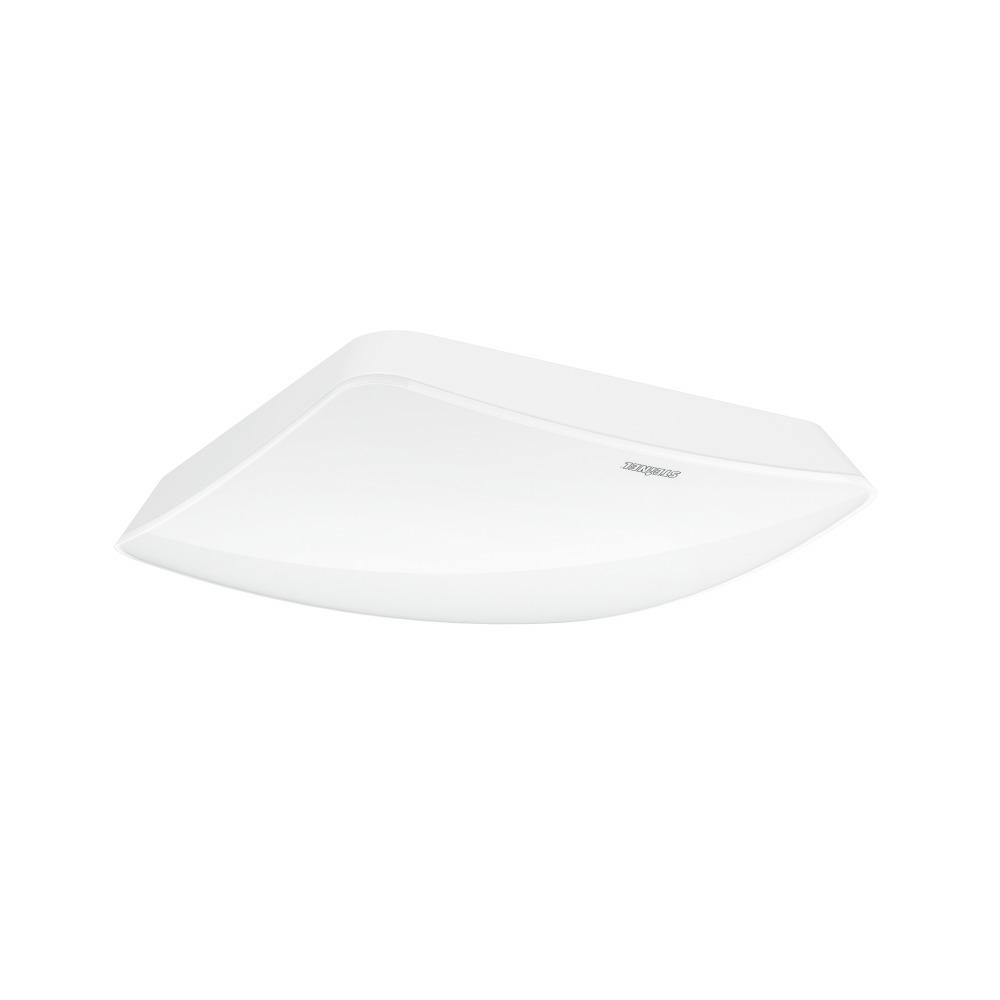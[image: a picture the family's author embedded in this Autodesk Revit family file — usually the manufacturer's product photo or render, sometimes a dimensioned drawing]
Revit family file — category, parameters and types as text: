
# Revit family: truepresence_057923
name_source: partatom
category: Electrical Fixtures
revit_build: Autodesk Revit 2016 (Build: 20151007_0715(x64)
units: mm (PartAtom-declared; Revit-internal decimal feet)

## family parameters
Cut with Voids When Loaded = No
Host = Face
Maintain Annotation Orientation = No
Part Type = Normal
Room Calculation Point = No
Round Connector Dimension = Use Diameter
Shared = No

## types (1)
- True Presence
    Apparent Load = 0 VA
    Default Elevation = 1800 mm
    Description = Type: Presence detector; Dimensions (L x W x H): 50 x 103 x 103 mm; Mains power supply: 220 – 240 V / 50 – 60 Hz; Power consumption: 1 W; Sensor Technology: High frequency; Application, place: Indoors; Application, room: classroom, lecture hall, one-person office, open-plan office, high-bay warehouse, production facilities, conference room / meeting room, hotel room, care room, duty room, recreation room, dining hall / staff restaurant, changing room, kitchenette, sports hall, reception / lobby, WC / washroom, warehouse, Indoors; Installation site: ceiling; Installation: Concealed wiring; HF-system: 7,2 GHz; Electronic scalability: Yes; Mechanical scalability: No; Mounting height: 2 – 12 m; Optimum mounting height: 2,8 m; Detection angle: 360 °; Angle of aperture: 360 °; Sneak-by guard: Yes; Capability of masking out individual segments: No; Reach, radial: Ø 15 m (177 m²); Reach, tangential: Ø 15 m (177 m²); Reach, presence: Ø 15 m (177 m²); True Presence reach: Ø 9 m (64 m²); Twilight setting TEACH: Yes; Twilight setting: 2 – 1000 lx; Time setting: 30 sec – 30 min; Switching output 1, resistive: 2000 W; Switching output 1, number of LEDs / fluorescent lamps: 8 pcs.; Switching output 1, floating: No; Constant-lighting control: No; Basic light level function: No; Functions: Group parameterisation, Semi-/fully automatic, Lighting scenario, Manual ON / ON-OFF, Neighbouring-group function, Normal / test mode; Settings via: Bluetooth; With remote control: No; Interconnection: Yes; IP-rating: IP20; Material: Plastic; Ambient temperature: -20 – 50 °C; Colour: white; Colour, RAL: 9003; Manufacturer's Warranty: 5 years; Version: COM1 - concealed white; PU1, EAN: 4007841057923
    Height = 0 mm  [stored 0 ft]
    Length = 200 mm  [stored 0.656168 ft]
    Manufacturer = Steinel
    ModVariant = No
    Model = 057923
    Number of Poles = 1
    OnlyDefault = No
    Power Factor = 1
    Product Name = True Presence
    Product group = Presence detector
    ProductGroupID = 4
    RLX_Detail_Level = 1
    RLX_LegendID = 4.1
    RlxData = Q
eAHUvXeUVNW7rtuAIElEFEUQRKTJGUldtaqQnLNIEhok5xyaIEFyDpIlJxUkCCh2VRciZgXM
OeesP0Uxcr5n1jv3qT3uuXfcf84Y5zD20+/7vfWtueaaK9Ddsn8rV9rly2n25/K/TrDuT35v
TC/bH1/e0sG75DZs50lLmx01EtbhvrgNL1/+Os91aU3HjBowbHT/icPGjG43aZS5YeMH5c+X
h01v6JY2Pm1S2qC0smmdzA1Km2CMTrvbJZXSaqXVS2uQ1iitTlpd66ic1thGr6I5pE4yj2WX
L3+Xp3Bau2FDhk5sPmrYxImDxqeVzcU+Co5P6582MK3ffxuNkar+L0fKbSN9neeKtPaDJgzN
VcSN4PZb7X/RnSvtCqU/2cH///nzv6fvGrfrMWPT0k6ZG50rLe3BUm2DNyZVCq7uMzP28DPt
gzwl9odX15geuzraLMj/V0Ywd+ic2M3vlAjSHiwcfDZyVWzH9m/CY2fcGXr3k02x1ks/CXep
czrc8KXNsbtabQ/3b9g5vKfKzliBClPDL86ZHDq2ZXesXv354XI/fR6amn937OffOgTzarbJ
aF4vK7bsZIdgWq5rYzWHZ8WWv98+yOm6I7bxpul+X3H29b7N7a1JleJf9J7p5xNnPtpvLGW/
MfarfWWzL80hmzn0uHtsOC3to/IF39wd+zISyn55wmsZeV9M+rRGF2L1MjbF3gk/ErvUvH18
3OKJsUaNb4zfdONV8XwdVsX6Va8Un3C2TbzB2snMIW5r4ubw/GcN48VvbB7/6frpscn914QH
HW4fL113YuyRYfWDMitaxBv+PC3Wt3qlYIBt28y2rTH0YqjYuA7xOusmxFbVK5B9bHOH+KVx
E2Jr/vo0tu2zJ2I37tkce2PLjljHyB2xwkV3xq75en5scO/vsp/9e1fsk4NTYyc+m5W9aYM7
ltic+/KkcyzKQ+TqD9GvccKMw/Fyzqr0Xu/3FWZfOsaAY9z89+rY2iPtg/Q6E/0xuvNu8493
Pdsm6GTzn3Ff/XjHyS2Cv/JkxR4s+Ev2t+M6BHPWToiVGnZ1aMDmDkF4/IRY14HHwyWbtA+2
LJvIugWTbdvbbNunX28YrCzXPJh99fSYXW9xu97iut7idr3FuN7seojb9RDmeuCccI198cTW
2LvWb9dA8KVdA3b9xO36eZzrx66ZuF0zYa6Zv35qF595bH+4V7ERsX8fbxt//fi+8JGuXWO5
5reJ13h0bzjvfaHY4D/axfdtOXsr+b1PtHWe/Lqv28THt/ggRn7n8dbx4Nf3YuT3/NvKxqkQ
Jz/4YksbJz1O/u2YpvFpe+u7fFmLJvHVK+u5nIzP6CfjM/oZg7HIGYOxyNkn+yZnn+ybfEyx
PLuZKzmeuao/nNIf9v02fpAyfuDHt/kEKfMJ/HwsC1LmH/j52xhByvEG/nhtn0HK+gR+fWyO
QWzi2j3M0+YY9Gh0fA/zVL9bf5sj/W79NX5Av82R8QP6NR+X2xyZj8s1f5eT8Rn9Ol6XMwZj
payPy9kn+ya3NSzPXNlvwTdvLc9c1e/mSq719+Nzvvz4nC+X6/y6XOfX5awxc2Uc1tjP/5PN
LeIrTpUPbJ+xdw42id/4aW3nW9Xu4K49rtVXSreL79/4YQzftVYbu4YrxvFtNjWL989u4DxK
Tc7n9OHZju3xXCeMqzzsc+sPfL+NE/hxTAM/vn0e+P3adoGfj43nzi9jKnf3l/oDco3jvMZ3
Xvt13sZjPs5z/zGu5unGxeu4XK7jdZ75Mi497RplxFduDrs1/PqhmvEzLzZ13tY4/svmFs6/
PWd77Id+rZ2vNqVzRrHFbZy/uPHB8MRQMl9o5ySs/jc/rB088nAT1/PBynBwrlmG8wUvNA3O
76np/D/Wu1Ln8VK4VZBx/Nsw57TojNbBgnobnH9/UZvggRp9Hif/qn/r4K2h27nWYicatQqq
zv/O+VorWwYz3igQJ69Sv2Xw7qlrnf9P/pbBoWMlnK/1nxbB77VKOf/H2y2Cz94p7fzXNgeO
k21PzWgSXGpYx/lljTOC19eGne/+Zc3gzJGmznPdfWzXH/2Tbv46/EbLVs7fP2F1eMmK1s5n
FL0mu7I9H+kpHhyJdamYzG194k217ZBY7XiRM01cz5PDwvHlozKcv/RY03iRN2o6/33yOnf+
u16t4ouWfuaO9599reOfz1vs/LTpbeL5vpkbYl+L/moVn/pPdhj/9R8LYuOLLPwvP+DYItf/
TnhhePCHC//L+x6+ebFvWdJyCzzf0QGe77HwaF6BzyfwV8qjfGfIdgUMPgN8QXm0kDxaWOCv
kkeLyF9t6sfBF1WNsj/A810YHi0mrlVGjr9O4OmhRtkGjxYXeMalRtk3MF/fg79eNXqDwJeQ
R28U+JIGn7NtKYHneKnRm0RpZeRlDLYD/M0G+ytr+Pngb1GNlpNH/bHjb1WNlhfpyujDV1CN
VpRHKwl8ZXmUnwz4DOV7e8BXk0erC3wN5TVN/Zj4WqrR2vIo1yDg68ijdQXXr+/hOvVj4rlW
qVG/Dvj8qlGukduMeoY/X3h/TvH1VaNlBb6BPMq6A561BjxrDXi/5njWGvCsNeBZX8CzvoBn
f3iU9QV8Q3mU9WW+jQw+gwyDz9CQPDXevpF3n6GBwEfkUX7EAnxjefR2gW8ijzYV+GbyaHOB
byGPthT4VvJoa4FvI4+2Ffh28mh7ge8gj3YU+E7yaGeB7yKPdhX4bvLoHQLfXR69U+B7yKM9
Bb6XPNpb4PvIo3cJfF95tJ/AZ8qj/QV+gDx6t8APlEcHCfxgeXSIwA+VR4cJ/HB5dITAj5RH
Rwn8aHl0jMCPlUfHCfx4eXSCwbXKtcs1CviJ8ijXKOC5Lvmca54a8NwHeHSSwN8mj04W+Cny
KNcu4Lle+fxG1WT4kqrRqQJfQh6dJvBZ8ijXNOC5jvn8etVkeHLATxd4nv/UaBl5lOse8KXk
Ua57wM+QR2cKPH/fUKM3GfTifR/ZLIEvIo/eI/D8/U2Nzhb4OfJod4HvYfB5IYMa8AXl0bkC
X0AezSWPzhN4/lDz516Bny+P9hX4TIM/uQ1qwPP3Cx5dIPB15NGFAr9IHuUeAzz3FZ/z9xc1
4MkBv1jga8mj/L3IZ+hQga8qjw4X+CXy6FKBry6P1jDoxfs+smUCX00eXS7wDeVR7lvAjze4
b1cY4wSeex9dKU+NHyVdJU+NHyFdLU+NHyZdI0+NX6sa9c8x/DrV6CCBv08e9c9J/HrVaH+B
3yCP9hP4jfLoJnn0LoHfLI/2Fvgt8uhWebSnwN8vj26TR+8U+O3y6A6xUxl9+F2q0d1ijzJ6
8HdI98pT47tK98lT4ztL98tT4w+oRjsK/APyaHuBf1AefUgebSvwB+XR1gJ/SB5tKfAPy6PN
Bf6wPNpU4I/Io0fl0dsF/pg8GhX4R+TRQOCPy6PcG4Afb4w1RhvLBX6ZspHy1Pil0uHy3P88
LxYbmcZ8Y4HBc2aAsVDgydFMeZ53fYx7BX6e0cOYY8w1yHoZ5IAnR+nD8+zuZswW+HsMtIs8
NX6WtJM8NX6mtIN8O9M2xnSjmTHFmGq0MloY0wSeHKUPHzEmGpOMJkZjY7LAk6P04Y8bJwzO
BeBXyaMTBH6FwK802JbzyzaAPymPPirwXNPUKNc6vccMPgM81xYePWJwPT4sT43nmsajB+VR
Pw6e+4Qa9fvjvvPzwfMcoUZ5vnC/8tzgM8Bvk0fp22fsNugF/C55lOcLPTwr+Azweww+22H4
bfHsg33z3PNzwz+mGvVri1+jGl1t0Mvzk88Az3MWj26UR9cJ/AZ5dL24Txl9aw3GALzfH+ed
+bxqpP4581RLLqe0nOumJ345WCeStrpq9tBiMxLNxlSJPD+paiw8fEbi5rQ8rmfO5zMT5Q9e
CF5ZXjX7kQdnJfpVfTx4rU7VWLHvZyW+mZQeeXxV1ex1u2Ykpk1Pd/34X9dViVzYmRZmnBuP
2fj2h/H/+axBZPSyh0J7Xp+eKPlH7sh9K6tmM/5T8QsBPYy/unN2cGBZ1RDjVzm8w+V/1Lsn
ce1/5jt/eMI9CXqTf5L/xdD77NLLY6vvqxuPPnpP4ttNZbI3bNkRZ9vid/dvdFvB3+I90mcl
Pj/3Y/adRUrkPFhxZuLLfP+GHmmTnsOcz5Wr1GjoU1VymHPhl8uEp46ok8OcZ399Q+jpjCCn
1Ibpib+K3JL98Olkzz9t9mXXOJr0o7JqZb89s0nO+e7TE42al8ve/UTLHNb2463XZX+ep33O
txeyEmenlc4+/s9FN4eN5Ts2yn84Obe2e+aFn+xXz8352mseClf4tZrzb63tGy5yumHAscx5
9InwA2enBRx7vy+Phla22xGkHFfAcelYIhzLGy8cCS19uEqEY7n+QIXQwFlNIsztgVM7Qx2q
BxGOJbtEeqjr5HTXvzHf+cem2PljWx2X21Zr4vzXba+K3ZZVJ8KavPbFgNjLtyT92D2NQi9c
uujmMPnvPdmZvZJz2/fSxFizIXPdnB97+evsk49F3LEcf6plzk9n1zVy67O/Tk6/7HEhxgyO
1skZ02tZBv7CnGI5j2+sG36h58zE+pIlcu4ccS7E+Ro9MDt+8LsrM7g2mjbfER/U57EQ6/D6
qh3xc8ObO7/n4R3xkeXPnyJXT3ZKj/Nre2THe6wr4K6xO28um3PtvrXZ6W/PSBRbfkPOV6uH
xNhX+yN1ci4+97ybT+abDXJ+7P9BNtftT/na56zY3yCDc9rYqJF+RXBkcJtIrYVZiXMlCgfT
9neMfLk3KzGqzNxwio85PyQr8VmjvPEuLbtE/jg7PHHdht05pZtMjDR/r0Zi7MYaiWbn50em
vLQn5+EVwxPke89dG3+sX1aC/guld8RW7cxKME7LMsvCK/YkfZmfcwelhiV7pj2+K9Lm2+S2
GxbUiBb/ITnmKzuGR/MP3uP2tWJgVvS3foXcHG7anRW9tsx6N7cb9mVF1x6c7ebcdnhWtNuB
tID93vH28GiBcrsjzOfTyzWi8Yk1osxzzb+7I98dGx4lP3rgqqDF3VlR+nev3BnutjMryjzH
HFwSO7Mn6RvcUCD+8qBkz6rFu3O6PZPc9uMBNRKHr6npxuy4bHji93f2uH2tPToh8exXqyNZ
Rb8ILvfMSnz6zL7wS190i/y7eHKi1sqp4fcOL448WWx64uehf4d4nr1SIitx6eKw2O7yvSJ5
q01OhDbOjQ1otizScP30RNd2l2O/bMmI/LIsK1Grf644c3vlr5GJr0PHc97acVVkyflKiXJP
VEvcvPeByE+fVE+8M7d6ovMtqyILFuzPufjaiMTX8++MlFtWNH72+emJ43fUi6R9dDFWZ1Vy
/Y/8sS524dTUxMj94yLtf18Tu+vqKe48Nq46N/TYL8n+o6vnhc4dSvZ/03BZeGvxqYmtV8+I
PPvxx+Ev1iXzLZn5gi5Lkj78/drI1fNHuTGf+vn78G8/z0iU+axkpOjU+yP3f9U/MTN0MnLt
qPRo4Z8j7rn70RdVopU6Vk3kKr0/cvu7I6OvfZE8rqsPT48WyCwU/+dSg8jrRyZHa698KBYe
tCiyKpgYvVh6feyjUpsih4tNj+46lBZjDb+5MSv60KTuYdawRbXJ0QV2PbCGx++bHh1g1wNr
2GV5VrS7edbw9hKjoiX3PRJhDT/4ulJ04P5qUdaw5E01orNaV4+yhi803h959vERUcYc9m3R
YPnz06Os4anOv4ffXJm8NgY22RCecmpqlDU82WxTeGiRKe56uLH/rOycX5L9DdZNz37nULL/
1OolsbeKT42yhleO/SjW6L5kfmZ/3viJJUl/x/Nrc2YuGeXGHHXh69j3/5kRZQ1vvvv+nEYH
B0QLTD0WCbetkFi+IYjWLFIrEj9bJVFzXNUoa7gjZ2Ri5owT7rhOL4wk8q++Ptq8wK7IO1l1
Eyd/rBvtUPC34Pi3VybK/NgyWr//gcgtA/fnfPTt2OhXJ48EP7aYkvNn63HRJ8eOjMz4+u9Y
rlXTonP/7R9Z2mBm7Ip8M90choyLxCZHs6JcVzc8syRcqdD0KOt/XdPd4d9fmBHtXats5Prb
CgaHXpsW/ftMn8iyF1dEVrcf7Y6lUs/9kW13jImy5tOmXx99dmPEzW31jbdF3+mUnFvvl1tG
s49d6c7F9vzjokNu2B9p0++hoPPMcdGfb54YYW7fHM6K9rDz2OTK9pGS7bKi3370rbu/nmk4
M7rZzvvz64tHOjXOip5fXTXMPGcXnh5dd3C2u07O5bbjsOcG66lnhXue1HwwK/qnPVsYc8PC
rOgl81wng+fYvm643nn7zjvq//bu09euJct5bix5fFQ017o1OVwD5z4cHR1WcH8O4391XyR6
x9wbElkNtkV67agbbfl83QTr/+bX+aP3z2/prvnft+6LTP93bKJBkZPB5SenRmbVHpfgGPM9
VSAo9lBWgvksyP1uePCE5HPy652rw906zkxk/1gssnRkenjBgmmJh7cMjJTLvzpW94XpCe6X
8YfXxp7bkPy+pt5P+eNV/pyW4Bp+MHN5znPzRrt78+HT+3OG9hmTyPdHwciY54onXikfTXCd
VP21bmLA5OQ8uzZqmdhxMX+C62TAu2MTM4fsz2Ge2zPGJW6rPzWHeQ4cn5Vouu7DGOvwwOyZ
ieuP2PVt5zd2ZmqiXjRvjDVZUXFG4tkZ88Jcq/c9PS1x/vih8M+Z/dz3Vvr+J5rLTG4jj3GF
kdfIJ640zS8KmBY0ChmFjauMIsbVRlFxjWkxca0pXGcUN643bjBKGDcaJY1Sxk1GaaOMcbMo
a3qLUc641fBjMj6UN9KNCkZFo5JR2ahiVDWqieqmNYyaRi2jtlHHqGvcZtQzGK++0cBoaDQy
MoyQERZ8E8micRE2Nm43mhhNDX4ma260EC1NW4nWptBGtDWFdqK9KXQQHU2hk+hsCl1EV1Po
Ju4whe7iTlPoIXqaQi/R2xT6iLtMoa/oZwqZor8pDBB3mw40BhmDDX98Q8wPNYYZw40Rhj9G
dKQxyhhtjDE4Xn+s6FhjnDHemGBMNCYZk8UUU9ZgqjHNyDKmGzOMmcYsI3UdWI97jNnGHGOu
Mc+415hvLDD8mqALjUXGYmOJwfr4tUGXGsuM5cYKY6Wxylgt1phmGmuNdcZ9xnpjg7HR2GSw
drDZ2GJsNe43thmZxnZjh7HT2GXsNvYY7H+vsc/YbxwwHjAeNB4yOL8HjUPGw8Zh44hx1Dhm
PCKOm54wTopHTR8zThmPG9lGzIgbOQbrnTBOG08YZ4wnjbPGUwbn7WnjGeNZ4znjeeMF40Wj
rTHCeMk4Z5w3LhgvGy2NVoa/rrjGINPgWky9RvEcI6Re23jOOfj7gXsDmHsno73BtQb4Ngbz
Avwr/xdTP5c9A3PbNT58csZVi7ODtMIbG626bnWQebxq6PXnzwbPju4RvnXnoeBAl0fC/1zb
J3hrdHb4kx4bgqlH/g1HJ84JbrpYNHglrW9wvG/hoHrvEYEtRdq6JzoHaQemNxz/XuUgbeXy
RsU//TvcYEXDCNufPdohQr1j3O2RCp/NCzM+yv4vLSoRLpe7QwR9vHW7yJiLW0Psr3Le98Ps
7722JYOZ5WpG0ObZVSJ+v1Xfru3msbBuNPjp42JBNfs3gFmHewUfhO9wmvPbi+FjbdcFB5/a
36jczceDyf/MDS9Zmx3cYfv8ZvNzAfvZ9cOTQflCJUKzns4bvHR4cCOOn/zIlrOhMqVyhYpW
KhWm/9E2tWycig1XrrnTHWv96TuCM+3eDa/auzKo2+nGYMClRcHP19QOLq1ZENR/KBKsWzjf
zYe63OK+7vOh5UYGD7crEWF+vWcUjFCfTb8y0vn3OS4/9uvO4JNJ/wR/P70h+O3lr4Pz7xwK
cv2VP/J6hXNBje6vBZyXFXd9EvQ49GJQtNK7wZsLng/a77w2ctv8c8GcqaUj1TafC155unak
8vcvBawz569Qi+YR+nuObh255sPnAtaXcY4uaRDhfLKunM8PP6oa4Tz2//xCwHnYsOp8MP76
38Lsl/VgPqxfrhLngy/unODmyfGfrJMreX7tOFgHjot1KHq4UIR1OHNbYZtXh+DQ0i0B1wHr
xfGyfhznDW+fc+Nxfjhe9s/1+Gihl5xynpjvskvngqfGtw1KLTgfDOm/MvizWs3IS/k2hb4q
USuy+9ZToRcbN4+0OrsuNP6PmpEy+78K/ft2zUj74oXDL5cr5WqU+pET/wZ8vr7A5YC69Lef
uPrnoZ+6etcv77j6P9PfdfU7K19z9f5yr7v6t+ZnnLY8d8blL77xuNNLPR53eb3C213d5bFt
rl52qYOrUfbX52gizP6/SnsiTJ2/yC2uPvB3eVdn7jkT4vPGM18I8fnp8w1dnVm5rasrTEru
f/I/yf3/lTfbjV9xUXL/g0LJ/c/9Mrn/77p3dJ+jjHfT6NPJ/cWT+5+9sJyrK02u4PbfacNT
yf3ddC65/xORZH11Z1fv2trKreOwT1u5dT34ZTOnZw40c3lm7gauHvNW/WRfRnL9h5my/08/
S67/0w2T69+u5KdufmU3Jtf/5XLvurrcQ8n1f/FUcv3f7Jxc/wcWJvf/ygvJ/Tfu0ixi/44r
nL2lpdPGXcpHQg9uDnG+uS5+71EyUubfzaHrovnc9XKh/78B+UMFPgm4XlqN+sTV1w5+x+mn
z7wVVNyxOHTj88+5muuPmucE19vnj73q9Pzvr7rP3+j9pFOeK1vr7grt6Jbt6u6Dtjvl+RMp
ty/E+We/PD/GjzoQ4nmy8sYD7rnzZen9oQv9c8J8nnlzaac8dxiP51Baly2hTjc/HnKf2/OJ
+WSeS3d13qXJ/der/JSb56gvs91xXZiXnEerlcl5PJNY6ea977qJAevD9cB499ZsF7A+P638
PczxrSqTcPu/NL1UmPX5aGMZV4/Nibn9jX13l9t/l/7t3PryPGE+PF8O99oUyqx5a8ipzZPx
11Rs7fp4DnE86ys0d3WXag2c8rxifbg+6Oc5xvrwXGN9eP6xPmeWJs/b1K3J88VzkPF4DrI+
Te5Lnj+eV8zncoXX3PFtLJbc/5GPW7t5LmvTxl0n4+94O+C6KbXtA6cXi3/mdEqbK93nZQvf
lLyeltVy2nBI8jo7fiR5nX3RJznObJsr43y0/R+nzw6swr8lDD/77zGn9R/P48Y99UyX5P4W
rHR64IVdTk/fd9DpwiVHnX57xXGnsWYnnM7fdNJp14KPOw09c9rpwxefcpp5bq/b76oTl5w2
LF7Z7bfSi8eddmuWz/XdXbSH019XrHV667unnN7SMznegqPJ8Vpfk1yXX3om1+WpLz51fWnl
/nE64ucCbj0Ghm52mm93HafX//VCcE/79cGS8OJgU7HFQdoLzwe/PHQqYD8XtjwfHH712eCb
yOnA/v1tsHzrU8E/XRJBkTrPBdfGXwyy/u7rthsXFAxW9SgUtNtXMGC+Y4rNy2D+vzbYmfFH
hxeD+14rEIw7+EJwbu9jYcZ/blzF8OXez/H3VIj5v7F0Z4jjqTg4CLHf8hsuZ3C8g7o+nMF6
vPr2cxlpzd/KWPPIkfDp1Y9kPPXcP2HWi77ZBf7IqDB2RHh28H1GzaWLw6znoK41QjuO5g2x
n7Qnc4UaXmoSzpyQFrp3W/sw6/5R9VWh2Z+0DBUp/mnodMt/Mwref2fYvu/J6Fe5rTsO1uHI
0bbBLWtfDCr3WRmwRmm7D2eMK7U8YB7vNNwVMD7rxDxYp4++rhNaUSYRnJ64NnR83Nkg7a+v
QvfseTYYOOCXcO9vbXv7Y9+6uZ+57ds35/OYAvkV8mhegc8n8FfKo/kNtitg8BngC8qjhYzC
xlVGEeNqg6yo6mtMixnk1xp+HPx1BtsWN6432CfZDfJoCXGjMnrwJQWeHmqUbfBoKYFnXGqU
fQNz8j34m1SjpQW+jDx6s8CXNficbW8R+HLy6K2ivDL60g22A3wFg/1VNPx88JVUo5XlUX/s
+Cqq0aqimjL68NWNGkZNo5Y8Wlvg68ijdeXR2wS+njxaX+AbKG9o6sfEN1KNZsijIYEPy6Nc
wBBRRl/U8GPiG6tGOSbA325wvFyzXCNNjKZGM4FvLvAt5NGWAt9KHm0t8G0Enp/xAN/OYN35
GZC1BjxrDvgOBmtMP+vb0SDvJI92Nlhj5tBFdVfTbgbzvcPgM+hu0HOn0cPoKfC95NHeAt9H
Hr1L4PvKo/0EPlMe7S/wA+TRuwV+oDw6yBhsDDGGyqPDBH64PDpC4EfKo6MEfrQ8Okbgx8qj
4wR+vDw6QeAnyqOTjMnGFGOqPDpN4LPk0ekCP0MenSnws+TRewR+tjw6R+DnyqPzBP5eeXS+
scBYaCySRxcL/BJ5dKnAL5NHlwv8Cnl0pcCvkkdXC/waeXStwK+TR+8z1hsbjI3y6CaDa3Wz
0UPgt8ijvQSe65LPtxrUgL9fHt0m8Nvl0R0Cv1MezRR4rlc+32VQ7zb2GHtV7zPdbxxQ9oA8
+qDAPySPDhX44QafHzSoAU8O+EMC/7A8elgeHSnwR+TR0QJ/VB49JvCPyKPHDXrxvo/shMCf
lEcfNR4zThmPy6PZAh+TR6cKfJbB53GDGvA58mhC4E/Lo0/Io2cE/kl59KzAPyWPzhZ47h8+
f9qgfsZ41nhO9fOmLxgvKntJHj0n8OflUe4xwC8x+PyCajI8OeBfFvhX5NFX5dFlAv+aPLpC
4F+XR98Q+Dfl0bcMevG+j+xtgX9HHn3XeM943+gpj24Q+I3GJuMDg3v6PuNDY630I3lq/Grp
x/LU+JXST+Sp8culn8pT4z9TjS4V+M/l0cUC/4U8ukDgvzTmG18Z8wT+a3l0jsB/I49+K4/e
I/DfyaMzBf57efQHeXS6wP8oj/4kj04T+J/l0f+IX5TRh/9VNXpR/KaMHvxk6e/yk0wvGROk
f8hT48dJ/5Snxv+lGh0j8H/Lo6ME/h959F95dITAX5ZHhwk8P2hQo4NNAJ/LGGQ2t+ndpoDP
oxrtbxngr1CN5pVH+9nngM+nGr3LMsBfqRrtbRng86tGe1oGeO6RdcYa412Bf1vZKnlq/BtS
7m889z/Pi5cNnllPGS8YPGcWGucE/kXjXoM+emYbs4yzAn/GyDJiRsIgm2GQA54cpQ8/1Zhi
ZAv8Y8ZEY7zxqMCfUDZWnhp/TDpafqTpcOOQMcDYaew3hhpDjAcF/oAx0KCPnj7GFmObkWn0
NXYIPDlKH76AnYeCRiGBLyyPXiXw9j+C4cBfbbBtUYNtAH+NPFpM4K+VR68z6C1u8Bngr5dH
bzBKGDfKU+NLqkZLyaN+HPxNqlG/v9Lm/XzwZVSjNxtljVsMPgN8OXmUvluN8ga9gE+XRysY
9FQ0+AzwlQw+q2z4bfHsg31XMfzc8FVVo35t8dVUo9UNemsYfAb4mvJoLXm0tsDXkUfrituU
0VfP8GPi/f4478yHPxJ3r9jd9F//VuF/fpb8dyG5XXfyexPfl0fbJz+bHUV9FnL9yfGuMM9n
Vyqjx2d4xqPOa/jPyPA+C5v3ffnM+X4yenwW0Kbx2B+fXU1kGT0+w5NR5zeoGxu+z2dRZaxT
AYP+x5UxB5/Rz7bUBQ3qUwYZfT7jczLqQgY1zxbf5zM+J6MubPh+3+ezq2hTH57+k0SW0eMz
PBl1EYP6qOH7fFY2JWPd6L9RGcfhM/rZlrqoQV3CIKPPZ37tWTcy308f9TXKbzAlo89nKBla
zECLG77PZygZeq2BXmf4Pp+hZCife/V9Pmtsn/nxyMDvlzn4+nrz9Pl5UfvjSO2ppD6Ol3Ho
8WvFepBR+3Xm3JBRlzTYBxnjU99skNHjs1LK/Byob1Lm90mWntLHPunZqczPi6y0Mj8v6jIp
fcyNrIky+pgbPVuV+fmTbVbGcTAPjqGswXEwZ5/dqozriayscYtBHxlzoz5skNHjs3LK/Pyp
Dyqjj/mSHUrJmBv73K+MufisvDJq5ku9Vxl9PtujjPUra7DGzQx/jsqaI6tgkJW1rxwDdQvD
9/msojJq5kvdUhnn0mf+uuJaI6OubDAeNcdF3cogo89nVZRRc1zUrZXR57Oqyqg5Buo2yujz
WTVl/jip26b0caxk1ZVRc1zU7ZQxns9qKKPmuKhrKqPPZxFl9HGs9LRX5teDrJYyejhW6o7K
6PNZbWXUHCt1HWX0+ayeMvo4Lno6K6PHZ3WV+WOnvi2lj+Mne10ZfRwrPW8qo8dnryljHxwX
8zivjPn5rL4yao6V+iVl9PmsgTJqjpX6RWX0+ayhsjzKqBulZPSShZX5daPnOWVsyzqRZSij
5vipzyqjz2chZbmVUZ9RlteU/bLPQFk+ZdT+2iDjmqGOGtwL+e0rGXVjg4w1Zz1vN9YZZDzD
fNYkJaOXvk3KuPfpo6epMmrWnbqLMvp81kxZWWXUzZXRw7mg7qCsrKnPWijjGUFG3VJZOWXU
rZTdqoza3+fc02xL3cbgeLl/yajbGmQV7CsZdTuDjPuNjNrfb9xbZNR+zmQcC3VHg225Z8io
Oxlk1Fw/1F0N3+czf29xf5BRv23QxzpzTbHGaww/ns9Wp2RcZ4y/XBlj+aybMmquM+rUPp/d
oT5qrj3qlcoYz2fdlfnrk/rOlD6uUTJ+TmHO9HGN0rPKIPPXMVkPZf46pu6pjD6uZTJ+dmJb
+hob9ESU+eudrJdBX2P7ertB3dsgo89n/Lzm+7i+6Qkro8dnfczTR801T32XQUafz/gZ0Pdx
zdOzkcj66PFZX2X+vqDup4w+7g0yfg5lW/q4D+jJUEaPzzLN0+fvFer+RJbRx/2SafAznO/j
fqGnoTJ/T5ENMOjz9xT13cro474i42dk38d9Rc8Og8zfe2QDlfl7j3qQMvq4/8j4+Z1t6eP+
o4d/q0jm71GywUSW+XuUeogy+rhPyfh50Pdxn9JzgMi29fcy2VBl/l6mHqaMPu5nMn6fwLb0
cT/Tw8+fZP6eJxtOZBk93M/UIwzf5zN+9+T7uMfp4eddMnp8NpLIMmrucepRhu/z2RXalj7u
cXr4eZk+enw2msgyau5x6jGG7/NZbm1LH/czPfzcTh89PhtLZJl/DlCPU0Yf97jr0bb0cT/T
c8JgW/8cIBuvzD8HqCcoo497nOwPZfRxj9PD7xgYzz8HyCYSWeafA9STlNHHfU/2mzL6uMfp
4XcLbEuPzyYTWeafA9RTlNHHfU/2izL6uJ/p4fcqbEuPz6YSWeafA9TTlNHHfU/2szL6Mg16
ThtsS0+mQZZlkGXa1/4G9XTD9/nsB2WZptzP9PC7IPro8dkMIsv8c4B6pjL6uMfJvlNGH/cz
PfxeiW39c4BsFpFl/jlAfY8y+rjHyb5RRh/3Mz3PKvPPAbLZyvxzgHqOMvq4x2cbXxnslz7u
Z3r4HRiZfw6QzSWyjB7uZ+p5hu/z2RfK6OMep+eCMv8cILtXmX8OUM9P6eO+J/tUGX3c4/Tw
+zr2S4/PFhBZ5p8D1AuV0cd9T/axMvq4x+nhd3psS4/PFhFZ5p8D1IuV0cd9T/ahMvq4n+nh
94NsS4/PlhBZRs39TL3U8H0+e18ZfdzP9LyrzD8HyJYp888B6tu1X/q4x8neM9hHffsaMpYb
KwyfcY9TryayPnp8tlJZWBn1KmURZdQh7beRMsZaYzBePfvKeNRrDZ/xHKFeR2R99PjMj3eb
MnruM+gj4zlCvd4gYzufBZoLfTxb6Nlk0EePzzYoa6KMemNKRi+Z/96nmXm2paeB9nGjMsbf
bLCPkvaVPuoths94VlFvJbI+enzmxyuhjJ77DfrIphnU2wwytvNZI82FPp5p9Ow06KPHZ9uV
tVJGvSMlo5fMf+/Txjzb7jB2GYx3vX0lY/zUjF7q3Ybvm656jzJ6fOa/f7lZGT171VdGGfW+
lKyd6v3KqBmPHj9eKfPk9BwwmAtZB4P6AcNnM1QfUkaPzx5URs2zmfohZfT5zH+fU9oyeunx
45HRR3bQYL832Vcy6ocNn81SfVgZPT7jd/z0FVFGzxEiZfeoPqqM7XzGfyug7ypl9BwjUjbb
HPUjBhnbzTbI+G8Ovm+OOXpOElnfbPvqs+NElnVXRn2CSNlsc2T+e6Qe5tmWHv57BX2F7CsZ
4z9qkBW0r2TUjxk+m6v6lDJ6fObHK6CMnsfVx67oo85Oyfi7iDqmjB6f8d9r2C9fyeiJUyi7
V3WOMnp8xn/n8X3zzdHzBJFtS4/PEsr6KqM+nZLRS+a/R8o0z7anDf77FePltq9kjH/GIKtr
X8monzR8tkD1WWX0+MyPV0cZPU+pj4y/K6mfVsZ2PuO/mbEP+vh7kZ7nDDJ6fPaMsoHKqJ9N
yegl898jDTbPtvQ8bzBebftKxvipGb3ULxi+b7HqF5XR47PymnMtZfS8pL6ayqjPpWRDVZ9X
Rs149Pjxqponp+eCwVzIhhvULxs+W6L6dWX0+OwVZdRLDepXldHnM//9UHXL6KXHj0dGH9lr
BvutYV/JqN8wfLZM9ZvK6PFZOa1VNWX0vKU+suWq31bGdj4rq20bKqPnHfWRjVX9rjJqtqXH
fy9F33iDHv67LnOeYF9XGO8ZTZSNS8neN0/fGGXUHxBZxnYrDeqm2pY+n31onr5Ryqg/Msjo
WWV8ZPht6fPZx+bpG6GM+hMiy+hZbVCP0n7p89mn5ukbpoz6MyLL6FljUN+tbenz2efm6aNe
a1CPTOnz2ReW0zfEvpJRf2mQUa8zqEdoW/p89pV5+gYpo/6ayDJ67jOoh2tb+nz2jXn67lZG
/S2RZfSsN6j9tvT57Dvz9PVXRv09kWX0bDCoh2m/9PnsB/P09VNG/SORZfRsNKiHalv6fPaT
efqoNxnUg1P6fPaz5fTdZV/JqP9jkFFvNqgHaVv6fPaLefp6K6P+lcgyerYY1AO1LX0+u2ie
PuqtBnW/lD6f/WY5fT3tKxn17wYZ9f0GdTdtS5/PLpmnj3qbQX1nSp/P/rCcvjvtKxn1nwYZ
9XaDuru2pc9nf5mnj3qHQd03pc9nf1tOH/VOg/qulD6f/WM5fdS7DOpeKX0++9dy+qh3G9Q9
U/p8dtly+qj3GNR9Uvp8lqbsDvVR51JGz16D2m9Ln8/875a6KqPOo23p2WdQ91ZGn8+uUNZZ
GXVeZfTsN6h7pPT5LJ8y6gMG9R0pfT7zv5vrqD5q/k0Y60LPAwZ1F2X0+cz/nrC9Murkv0uZ
HaXnQYO6lbalz2eFlFE/ZFB3Tunzmf/dZlv1UfNvoZgfPQcN6k7K6POZ/z1ra2XUV6uPnkMG
dQdl9PnM/863pTLqa9RHz8MGdXtl9PnM//65uTJq/v0Tc6bnsEHdThl9PvO/C2+qjLq4+ug5
YlD7benz2fXqoz5qULdVRp/P/O/vb1dGzb/xYn70HDOo2yi7PSXz/y0hqoyafwPGtmz3iEHd
Whl9PvP/XSNQRn2T+ug5blA3U0afz/x/Y2mojNp/zzBeGbX7B1A2l9GWLTf4XsN/r0K2zKD2
vx8aqYzafz9EttSgvtXg2DLt6wIj3epKygZYvdDg+1r/vTIZfdS+r4/V9xqVLauibcnmGdTV
lPWweq5R1Wr/+91e6qOnuvrI6KP2fd2snm3wM5n/OY/sHoPa/368izJq/7Mk2SyD2v9evpMy
av/zKtlMg9r/nNzM6qkGv+/IMFirFvZ1msHvHfzvMsjoo/Z9EasnGfxuKKJtG1s92Qhb7X/v
Q0Yfte/jujhhcL799cJ14LPGGm+VMupRyugjJ7td2QRl1E2UrVBG3VQZ1yn7YJ/NU7KTllH7
654en7VQH/WjBnVLZfT5rL8ynon00tM5JaOPzD9PecaSUXdR3zGr2ZZ5+PuXe5qM2j8Pjiij
7qhteTaR82zxzzWedWTU/jnJs5OM2m9Lxj6oOxlcBzyfyaj9cfB3CnNmvl3Vd7/V5NT+exAy
+si6qW+rMmr//dB2y/g7jr/b+qqPjPHI/Pcl25RR+33stmyfwd+f/u9fMsYj62lwHLuUUfdS
tlMZ9V3K2Ja/0xnLfy+wQ330+PnxfR3HxjFkaluyxwzqgcro8Zm/NrheyKgHqG+NMuqRKRm9
ZHcrW201GbW/FzZrW/Y5SH2blFEPVrZRGfUQZessI6cempIxP7IRKdkGy+gZlpKtt4x6uLK1
VrMt2/njyHX58h+/XL78Yf03efHht5e3f2vyp/HX5cS/RI1WfNpwxe6pfHX/t+TLSiv+Svx5
eeWfl5f/efmef62pxT+XU8p7Ll7+kM3580s/J5d/dLJ939ed97Rcu2tY1nUt15YtnbakW4Eu
Zdus+6RS2nUFXtnl/rmJzc792bhoW+NHNpe5nWJRMrKv/3teJvhfw/+/mv+535tSelhVt7Ip
2X+3+ax8sQmP/byzcxWxFy3a+yMbW1ZdbfmlyP9Zr1ZcPyP5q4qDNvdrPmscr/PG/eGVve5v
mLf/nJjh/JvtIpaXDshN41Y7fyo9FH+8VWXny26qGzectyxunzm/6Jom8Y7Pf7o7ZcyYfJh9
4Ft++eit9CXHvz/MPPCaj+vRHNTj5uC89uW85uC85qb++2N+TI6DsRif4+B4tC/z97t9cUxs
T84xMS6eY2J/eJtv0DiouhfPOvm1qvbxifJ8Rs54tl/nUb+22q963Hyc1/jOa7/Oaz7qd+vj
fOor21JfU/XKv03ihVZuD6+tWDZ7bc1mcfufRrgV/1W9JvFTOa/F8H0yG1vPzXH800VC8VMX
ajiPUpPzOX14tmN7vP3PMuxmXOVhn1t/8F/9F2oEfhzTwI9vnwd+v7Zd4Odj4wW181fby5jK
3fzVH5BrHOdtPMZ3XvtN5jmvMR/n7ZWT5RlX82T+vp/jSubJ43We+TIu/ZuuDeKnHqkV/LN1
V3bu6yPxhntrBxs+fiHbsrh95nLL4vaZyz9teUv84wlNXN6pfLn47plNXT6/4JuxWR2auXx4
rbdiz/Vq7nI7J+W3tW/h8iaZg8rv6dPS94dT+sO+38YPUsYP/PjMMWU+gZ8PWcr8Az9/xmAs
josxbK5uv+zT5homZ5821zDHyxxjE6/dS84c7dV9e8nVH0vpj5Fr/HjK+HFyzcflzJG1I9f8
Xc4cWWtyHa/LmaPN1eXM0fbtcuZoc3U5rxS0ubrc1na3zdX3s/6+n/X343O+/PhxP77Or8t1
fl2/zZ/rweXM0c+fMTj3Ot445575s0/OvdYnzrknZ468VpCcOXJvkq+1V7N+2nKnW/9fKrSw
cXa59e92W8t4LG13uHaFi9knbm8Vr/T+7vDgelfHDme1duPgU19Xl/oau34TWsbrz3gnRk/q
q+4qrW5u49waJ099HV7qa/JeL9k43nBRXdeT+io9Mj5j29TX7TEe45KnvpKP/TMP8tTX9nGO
OAby1Ff7pb7yz7YN+21TXwto+wr8vlJfHZj6SkGbZ+DnmfraQcsCf1yprya08QK/JqmvL0x9
rWHq6w5TX4OY+nrE1Ncm2twDv/6DFjYLYmm3xjmP1w1pEXTq/nbMndOUVy6mvorR1iZYeebi
HtYn9XWNqa9x1Pjuekh91aOOJWDb1NdBpr4mUuvgelJfJal1c3nq6ya15i5PfSWlzpHLU19b
uW9Ls/IcA3NIfbVl6isvdW24ntTXYupacnnqqzN17bk89fWanGfmzb5SX106skQ0/tj6OgHr
bBq32nnOA+eDnPPA+cDzHH5gRCufh31u/YHvZzw/DurH1/l12+r8unuW8Zpkfr6H8dUf13wY
x3mN77zNh/06zzPNtvc58/T9zN95HZfzjEfN+Hyecr3F/fXGeDx/6Pn/ep2lf4Vl6qstk9+9
/j//54Ry2wd5jCsEPq/A890xf640/PfSeL4rpkYLCHxBebSQQW9hg88Af5U8WkTgrxb4ogJ/
jUFfMcOPg/f7uNa8nwP+OtVocYPseoMa8DfIoyUM+m40/Dj4kqpRf+z4UqpRftagt7TBZ4Av
I4/eLPBl5dFbRDll9N1q+HHwfh+cC+ZQ3kg3OG+AryCP+j/4iipQzgPgOQeArySPstaAryyP
sv6AryKP+nOEr6oa9ecRX0016s81vrpqlHMJ+BryKOcX8FxLgK8pj3JuAV9LHuUcA762PMr5
BnwdeZRrAPB15VF/zeBvU41yvQC+njzKtQB4rgPA15dHuQ4A30AeLSvwDeVRf53gG6lGuW4A
nyGP+usNH1KNcj0BPiyPco0BnusZ8IE8yvUH+Ig8yvMB8FF51D9D8I1Vo/45g79dNdpE4JvK
o/xqFfDN5dEWAt9SHm0l8K3l0TYC31YebSfw7eXRDgLfUR7tJPCd5dEuAt9VHu0m8HfIo90F
/k55tIfA95RHewl8b3m0j8DfJY/2Ffh+8mimwPeXRwcI/N3y6ECBHySPDhb4IfLoUIEfJo8O
F/gR8uhIgR8lj44W+DHy6FiBHyePjhf4CfLoRIGfJI9OFvh0eXSKwE+VR6cJfJY8Ot2gF+/7
yGYI/Ex5dJbA3yOPzpZH5wj8XHl0nsDfK4/OF/gF8uhCgV8kjy4W+CXy6FJ5dJnAL5dHVwj8
Snl0lTy6WuDXyKNrBX6dPHqfwK+XRzeIjcrow29SjW4WW5TRg9+qGr1f4LfJo30EvpfBdtsN
+gC/Qx7dKfC75NHd8ugegd8rj+4T+P3y6AF59AGBf1AefUjgD8qjhwT+YXn0sMAfkUePCvwx
efQRefS4wJ+QR08K/KPy6GMCf0oefVzgs+XR8kZu4wp5ajz96cYko4LAT5BHKwo89zk1Wkng
eS5Qo5UFfpQ8WkXgR8ijVQWe5xQ1Wk3gh8ij1QV+kDxaQ+DvlkdrCjzPWWq0lsD3k0drC/xd
8mgdge8tj9YV+J7y6G0Cf6c8Wk/g75BH6wt8V3m0gcB3lkcbCnxHebSRwLeXRzMEvq08GhL4
1vJoWOBbyqOBwDeXRyMC31QejQr87fJoY4NrMGb46xYfV4366xyfoxr19wU+oRr19xH+tGr0
qMA/IY8eFvgz8ughgX9SHn1I4M/Kow8I/FPyqH/+4J9Wje4R+Gfk0Z0Cv00e5bm41rjPeFbg
75dH+wp8H2O1wTbPCTzbUqOZAs+2Kwy2eV7g6aVGBwh8prHMYJsXBJ5eanSgwLPtYoNtXhR4
eqnRwQLPtgsNtnlJ4OmlRocKPNvON9jmnMDTS40OF3i2nWewzXmBp5caHSnwbDvHYJsLAk8v
NTpa4Nl2lsE2Lws8vdToWIFn2xkG27wi8PRSo+MFnm2nGWzzqsDTS41OFHi2jRlXGE1EM2Xk
eO4xtIU8NT5H2kqeGs89hraRp8aflraTp8Y/Ie0gT43nHkM7yVPjn5R2kafGn5V2k6fGc4+h
3eWp8U8bvYxtBvcVWQ+DHPDkKH34ycYUw68tnvUmJ2Nts40TRnmBf00eTRf4LIF/XR6dLvAz
Bf4egV8gj95rsN9TxgmBf1T+EVP2Afhj8ugbAn9EHn3YOGg8KE+NP6Aa3S+P+nHwe1Wju8Uu
ZfTh31SN+rnhOTY+32FQA367PLpc4LfIo5vl0ZUCv0ke3Sg2KKMPv141ukrg1wj8OoN9LzX8
3PBLVKPMH/CL5FF/nuaa9+cRP9vgGfa//jM7+t9eN5l8raR7XeOXKa+enHQgKzG0Z0/3escf
v52eiIyYE+PVe9FyWYk+P+eK81q3L1NeSflt5bGJb36Ym9O+8JjIjszRiU259uWMeqpKpNrU
5ol8FYom2r22IbIwb53EkF9rJ3gV4D0PFU1Mub65y1ct2p9T76bRCfofrDY/5/I7YxKMk/oK
y7398sbHlc1yr1McM2VHbOqXydcj6jWR7tWWXXuOCnfdn3wN4iNnl4aXf5Ps+fTj38Nt05Pb
pr7yMvrwvMiTV491+/ooujfSbG5yDneVLxrtPy05t9J/1o6+cjk558bFm0crHkoeS/G6o6Nt
8u13xzjx4pjoPaPudcee+orMqqWzov+x19ixVkW/nh690V57xxrqdZlube8/kBU9ZK9N5FV3
V343PbrBXp9Hz9flsqKd7RV7bJv6Ss0Pyo2Nbig3L8L67BoxOtrlzN4I67Yhq3n0RLmiUda5
5YQ60Z4LakdZ5/MPF40WuK65yy/N2xf5rPXoKP2F/7g3UumTMVHGSX0F56ED+YLTNydfL1is
/s5wzy+Tr1DUa0Pdqzm3TBoem7U/+arEq/Itje3/JtnzVMeLse/Tk9umvrLzi4/n5RzMP9bt
69Fm+3J+6KY53FI08dL05NyKLaudWD+qjpvzK8WaJyYfSR7LFXm7JzJu+COy6rs5kdTXfaa+
BjT1VaGprxBNfc1o6utHU19Lmvrq0tRXmqa+9jT1daipr0lNfZVq6itWU1/Dmvp61tTXtupe
c9fA7WuyEoe6fO+ugZ6xqYnWF+eGeW1fvR0zEjuGFrT/hpgeeX3J9MT31e8Pr48EkQa9Jyda
F7onFvlzSaRXdlZixRUXYrymMPW1gFvu6pt4/6fNOcM+ejbyzg8dE3d+USRxcVj1SO3f0xPX
V0pPlM13PvL6WyUT/f5obq8sbRK5Zf+2nMcnDEjwasuLtVbkvLVitLsvWvQrGj9zb/Ke2vPM
VfE/rpqeyCrfPFI8z47YtmLJV5GGL66J7aptrxV8bVjkypx64SUvJ1+DePOvM8In7ZWrvG71
ywe/Cv94Ivk6xdTXLA46vyny6sq+Cea5YXCR6I//dnSvfS69NT162+fpiRtffCly5Jpm0YbD
b3KvYuz/8t3RRRW358S+evC/vfYx9XWQ9gSM+mefXlXpXiv5mb0aNLfdg7yC9rFQVnSNvZKS
+6t7nenRl+1VlRxX70cnRxfaPcirTmuesPvXXm3J2r7SIiva1e5HXiOb+irMQn/dFX3lh02R
S91fiHx8tFO03t9Xufurb/EK0Qsj0qPMf8L5UtHDVzWPMv6mK7ZHZu0aEL29/tHIgBYrI90H
jXb3RckS1wQ97k3eU7NqFQ4eqTk9ynl5tde+cMPYlOjiHbMj9z68LFwqI3l/LSqeGTttPYz5
4G1LYk2CKdEf5t0baXbNLzF7r2uU6yT1daKZ/TbnzP7yrijz/Pz5qxKLj3SKcj38fTw90efF
5DxXpDdPRI6WcmMW3D4wUX/v4kid2GORNX+PSbzX6F73zGmXMSJRY9r+CK8l9Wts653IZcX/
ieS2eeUx0CtEXtN8xpVGfqOAUdAoZBQ2rjKKGFcbRY1rjGLGtcZ1RnHjeuMGo4Rxo1HSKGXc
ZJQ2yhg3G2WNW4xyxq0G38OlGxWMikYlo7JRxahqVDOqGzWMmkYto7ZRx6hr3GbUM+obDYyG
RiMjwwiJsCkEgn7ghAE3B7APaCxuN4UmgjlCU9HMFDguaC5amEJLwbpAK9HaFFhLaCPamgLf
swPnAtoLf746WO0h62h0MjobXYyuht+2m/k7jO7GnQbfa/c0ehm9jT7GXUZfo5+RafQ3/JwH
mL/bGGgMMgYbQ4yhxjBjuMCzBmWlfk28jrB8pDHKGG2MMcYa4wzWdLwxwZhoTDImG1OMqcY0
I8uYbsww+H59lnGPwXmcbcwx5hrzjHuN+cYCY6HBWrFO4NfSr49fa7/2/lz4c+PPVSvbFvy6
+HPLeQZ/7v3xNrMM/LXCMYK/lriuoLGoYQpR4a9Njg/8teuvZa5t7/1nvtdv68fyYze2bcDv
28/Fz83P1c/dH5NXjjMVvwZe/dp49Wvm1a+lV7/GXv3ae/XnxKs/V17z23xS8efW6/+ONUo9
p/grUlhk/v9W+H/lmJvbfsY/+VTw2qPLgmVb59vrrOYHk0eeDd6rcdzRcMjZ4Mm3zgTbPz8V
vFYk4cDf++qZ4HyHp4NNc9q47Xid1XoDLb6sTXBNritDhcO/hyflLhlifDzjvpuoE2bsUu2a
hhhn5ZlJIca9bfajIfZz7sMrwsyF7d6yXvo++qVpiO1mW8Y4pwvkDbNdLduG7TKHTw6x3UcH
rgwxH+bBcTCPVa2fdsf2pM2B7Rmb8ZgD43N8bM9cGI+5MD7Hx77YbmfR27m90ob0r+k0o0c0
sr5Cevjsq1UjH536PXRya1VX1/34BlejfN6h0hVOd6/5M6Bv3dsfBeT9//nQ1WtLv+vq53q+
5eqtf7zu6qHRV1zNXOjf/3DM1cyR+upCJ1zNMVC/NGlzst+OjZrjZn8oNceBlu15OkzOcVM3
/qCqqzle6o/eeD/E56yDq09NcfX6Asl5DHsgOY+X8yb3v61ycv8rxyb3v/5Ycv+cA8Zx58LG
va5icv+VmiX3/9V9yf13Op7c/wU7d+wvbV5y/52qJfdftlhy/xufaubW8ZM1Td36/lOriatP
PBl19dY7kudj0uQ6ri6xOXk+1n2QPB8o4x9OT56PQcuT56P7a8nzceul5PlY2i15Hvr+mjwP
VTKS56H+s8n9z7kvuf+tdZP7v6EI+d7QgDbNbL9TQrVPXrDjnhLKe9vLtu57Q33vftPps9+8
4fIfS33o6jcOfeDqjX/+4eo6R/9wdXKee0PJeU8JvZeo48Zf8RnHNSV0rnZjV783tLGrpxZK
7v/Jlsn9p61tYedrSqjxxe52/vaGGo895/SjL552+ZFXyts67w191f8WO+9TQr9eiru6z6sx
VyfP11533vi8T54tbn5n2m1x87vikxOuLtPppKvv2xx3ddVrc1x9OqOl20/Zs8n9ns54xtW8
DpT9vrU0ud/vrspxdbevkvtNXqd73fXKfjfnT+7XXoXoxm36ZXK/fe5I7ve17cn9Di+R3O+Y
7OS6N22UXPf7hybX/cqfkute45bkul/3SHLd37icXPexJ5Prnrxf94aS9++U0IWC1dw676tY
za3z+7dTp4ce6evyDPVnPP1HKfc8GHksn9Pdt7pxM57c9ht/PafZ/cT6ZDwz9H1Xn3zjTafv
/Mv1tTfjqhWvuLrNifOuTt5nezPaTH/S5V+Uy3G6qvaj7vMHtz/q6nOfufXJyOq62tVav4yx
m7q6OvOlXE7L3v8465zR8JeH+LYhreGDJV09ttENrv7pn9f46zKt7Gvcb3szTl8/19Ufla7o
6h5XcN/vzeC1nPSt6ZOcT5dqyfmM2JycD88hPi/2zjGnt28+6nRHycNOb6j6oNOVHybn3TDn
pI2bHqq8njo99G/mDvf5eF4laH90HWYM+U97V5+1VxuSV1qUPJ5K0Qdc3Wp28nhmX508nsyd
byTnf2ZO8rgmV3DHcemMu08yjuRp6c7TrDubOf3tDXc/ZeQukny+X6xel/OeUbBudfe57seM
tkdKuHrXD3mcDiyTPM+L7k6e110vJ8/z4W+T5zf5HLd12508v4WPJM/vD/mT+7+pV3L/hxa4
50qoTN0Lbh3qjH/DaSz6gdMXhrCfdPc8QJsUYH7poa+2M+/0UJF7k9vvqFXfjjM9NPuuhNMS
P5e285weOn0o26mew6Enlua48TKPJvtmv5XcLn+pMq7vsTPJfv29ERqyJXl+Jj+ZPF9pq5Pb
j5uSnGefhsl5/9ksOd8Co5Lz1d9/oXobnw521MkJuG4XrHzW8YD5orkWBh3zLQy2Jp4L6t2+
zr6HeD748tNeLu9VM18QL/F8wCusL419Ltg/8UiYbUfZNcs4cw9Mz+C+GGmvuKyeeSZouurJ
YN4N8SB31WeCH9KXBwV/fS5o1Lyle510ie/yuf3MmPhNmNdFc90z1timT7m5ZWb1C40YdCZo
fPGNDMaYbWMzv7SXimWcr23XZOdFjSpdvdRdgy8UbRkwXr2N+ezzNY22bbwYpm/E3ANh7q+P
qhfNmH1XNCN/rznhtO7dMp5v0DvM/pjv7Ff6ZsQzWobTjgzOqB8Owmk/jMj4xv4OZH8cF/fh
l5++4+6/xa/0DWXaaznHdzoT4j627Rtxn7+T51AjnguhZ2aHFpR9JrBXCLtr3L6Fcz/X27dx
7ncPeVSj/vtUfF6Bz2fw50qD7QHP99V4tIDAF5RHCxn0Fjb4DPBXyaNFBJ7fHwDef8+P5/cJ
9PE7BT8O3u+D3zP4OeD5nQM1Wtwg4/cP1IDnZxA8yu8k6OP3En4cPL+joEb9seNLqUZvMugt
bfAZ4MvIo/5nPnxZ1egtopwy+m41/Dh4vw/OBXMob6Qb/mcyfEXVaCWBryyPVhH4qgJfTR6t
LvD8TEiN1hT4WvIov2cBfB2jrnGb4X/OxNdXjTYQeH4PQ402EvgMeZSLFvA8xAHPTYZHecgC
np9n8Whjgb9dHm0i8E0Nfkbj51c/Zzw/w1KjLQW+lTzaWuDbyKP+Z1F8O4FvL492EPiO8mgn
ge8sj3YR+K5GN+MOo7vA3ymP9hD4nvJoL4HvLY/2Efi7BL6vPNpP4DPlUX9t4PurRgcI/N3G
QGOQMVjgh8ijQ41hxnBjhDw6UuBHyaOjBX6MPDpW4MfJo+MFfoI8OlHgJ8mjkwV+ijw61Zhm
ZBnT5dEZAj9THp0l8PfIo7MFfo48Olfg58mj9wr8fHl0gcAvlEcXGYsN5rlEHl0q8Mvk0eUC
v0IeXSnwq+TR1QK/Rh5dK/Dr5NH7BH69PLrB2GhsMjbLo1sEfqs8er/Ab5NHtwv8Dnl0p8Dv
kkd3C3y6PLpH4PfKo/sEfr88esCgF+/7yB4Q+Afl0YcE/qA8ekgefVjgD8ujR4yjxjHjEXn0
uMCfkEdPCvyj8uhjAn9KHn1cHs0W+Jg8Ghf4HHk0IY+eFvgn5NEzxpPGWeMpefRpgX9GHn1W
PKeMPvzzqtEXxIvK6MG/pBo9J/Dn5dEFAs/9xXYXDPoA/7I8+orAvyqPviaPvi7wb8ijbwr8
W/Lo2/LoaYF/Rx5913jPeN/4QB79UOA/kkc/FvhP5NFPBf4zefRzefQLgf9SHv1K4L+WR78R
+G/l0e8M5vy98YM8Wt6oYAyWp8bTm27sMioK/A55tLLAb5NHqwn8Vnm0hsBvlkdrCfwmebSO
cZux3lgnj9YXeJ5r1GhDgV8lj2YI/Ap5NBD4ZfJoVOCXyKO3C3yWPNrUaG4sNObLoy0Efp48
2krg58ijbQT+Hnm0vcDPlEc7Cjx/z1GjnQWe+VGjXY07jCnGJHn0ToGfII/2FPhx8mhvgR8j
j/YV+FHyaKbAj5BH+wv8cHn0boNr8EeD6/A74yfjZ3n0G4H/jzzq7wv8L6rRLwT+V3n0U4G/
KI9+LPC/yaMfCvzv8ijzfNe4ZPwhj54W+D/l0TcF/i959HWB/1sefUXgz8ujLxlPGk8b/wj8
OXl0kcAvME4bZ4x/Bf6yPLpU4BcbceO04X/owrMtNbpc4Nk222CbXPY54OnFoytNAM+2jxls
k9tqwNOLR1dbDXi2O2mwTR6rAU8vHl1rNeDZ7rjBNldYDXh68eh9VgOe7Y4abJPXasDTi0c3
WA14tnvYOGLksxrwV8qjW6wG/EbThwy2yW814NkOj95vNeDZ7gGDbQpYDXh68eh2qwHPdvsM
tiloNeDpxaM7rQY82/1oDDaGGsOMkQb3G+B/lo6Wp8Zzj6Fj5anx3GPoeHlqPPcYOlGeGn9R
OlmeGv+bdKo8NZ77bZoxw7gk8Nxj6Cx5ajz3GDpbnhr/l3Gvcd7gvpptzDXIAU+O0offbewx
/NriWW9yMta1kGlh4yqBLyKPXi3wRQX+Gnm0mMBfK/DXCTz/E4PUKP8zguz3BoP9AZ7/iUD8
jQb7AHxJeZT/iT/A8z/th0dLG2WMm+Wp8WVVo7fIo34cfDnV6K2ivDL68OmqUT83PMfG5xUM
asBXlEcrCXxlebSKPFpV4KvJo9VFDWX04WuqRvmf4wN8bYHnf4eJfdc1/Nzwp+y8U6PMH/C3
yaP+PNUz788jvr7BH4n7fZ9djVHq3O4T/9nsKKXPKrnPkn15zNOfrowenyX7k696vcJy/xn7
wPvsY23LdnkNlM/oQ32WSWQZn+cz+KyPQUaPz/oqQ640+KwKhfUxV5/RT0ad36AuaPg+n/E5
GXUBw/f7Pp+VpE19jEP/NUSW0eMzPBl1IYM6w/B9PiumjP0VNuivqoyxfUY/21JfZVBXN8jo
8xmfk1EXMXy/7/NZUdrUd7U5309Gj8/q0aY+tvGfkdHjs7q0qY/14LOaRJbR47PayhiHY+ez
Bso4Dp/5NWU9/gd77wFv3VGXC++QUIwgLQgqSFBKEFhMWbNmBik5EHpLaNKUJBBCCS0JEJqE
DqEKiHRCKFIUEcu1gwXl2q5dv/v53Y979XrRa8ErIiqS+zyzZpHNm/dNzjrsc97Zez/55X/2
/j/vf9aevc5z1jP/qcToZxivx+9+fRjxO8KI8f5OGF+J8fUEGF9vAJviJoyvxPjKf+frPWBT
3ITdqGK8zjfDiN+5YiwzYXxlWb7eEMbXk2HTZ0wYX4nxldfm611hU9yEnVIxft63wIjfq2L8
vhPGV5blK/nJ15vAiDFuwibu8u+D72nfBmPc9J7+zSvGOPq0G1dsek//4RVjHH3aLSo21YH1
uHfF+Bn0ad9esek9/ftWjHH0aTet2PSe/okVYxx92ndWjHEnVrt/xaYyxG9Wsek9/QdWjHH0
ad9Rsek9/dMqxjj6tAcvYawD7aEVY/0mbLqnvH/E6H8PjPf+WPyc7t0jK8Z/5728JeyFxxAc
n6cTditCFWMs4/47IWDLMX9RsavglTEsd1LF+EKM/q3poOwUQ/9/VowvLEfsu+ggjs8rYvRv
AyPGZw0x+reFEaPP69P/X7ApbsJuVzE+f4jR7yo21Yv+X1eMcawHsen5wmcDMfoGxs+Y6kr/
f1eMcawvMVsxPn+I0XcVm74T/b+rGOP4vYj5il27YvT7ik3fnf4/VIxx/P7EQsX4/CNGf6gY
fX5/+v9YMcZNWKwYn3vE6KeK0ec9of9PFWPchOWKHV8x+neo2DdWjP53V4zleD/p/3PFGDdh
d6zY9StG/04VYwzvMf1/qRjjJuzOFePzkRj9u1SMPn8X9P+1YoybsJMrdsOK0d+p2PQ7pP/v
FWMcf2fE7loxPkeJ0b9bxejz90j/PyrGuAk7pWJ83hOjf/eK0efvlv6lFWPchN2jYjeoGP17
Vowx5AD9Y44hOB4LPmH3IgSMz1Ni9O8NI8ZnJzH694ERo0/+0GfOOcVN2H0JIY7PSWL07wcj
Rp+con/VWpZxE3Z/vGfcifhJjP4DYMTok3v0r17LnriEPRDvGXezitE/lRAwliMf6TNvnOIm
7DRCiOPzlhj9B8GI0Sdv6TNHmeIm7MGEEMdnNjH6D4ERm/hOn/nUFEfOE3soIcR9J34So/8w
GDH65Dz9a9eyjJuw78F7xn1bxeg/nBCwG+Mn4+g/AkaMPv9e6LN9P8VN2CMJIe5Y/CRG/1Ew
YvT5N0Sf+dwUN2GPJoS4q+EnMfrfCyNGn39r9JlDTHET9n2EEHdV/CRG/zEwYvRPhtFnPjjF
nYx3xE6HETsOP0+GnQ47A0bsZPzcgdGfyjJuws7Ee8bRvyuM/mNh0/Um7IxjRoxxd4Mxhvkq
4xgzYY8jBIw+/3bpnwWb4ibszFqWcfx7ZgzzKcYxZsIeTwgYff490z8bNsVN2ONqWcbxb5wx
zL8Zx5gJewIhYPT5N07/ibApbsIeX8syjn/3jGGezzjGTNiTCAGjz2cB/SfDprgJe0Ityzg+
CxjDfJlxjJmwcwgBo8/nA/2nwKa4CXtSLcs4Ph8Ywz4CxjFmwp5KCBh9PjPoPw02xU3YObUs
4/jMYMzxFWPMhD0d71mWPp8j9J8BI8a4CXtqLcs4PkcYw74txjFmws4lBIw+ny30z4NNcRP2
9FqWcXy2MIZ9a4xjzISdTwgYfT5b6D8TNsVN2Lm1LOP4vGHMcRVjzIQ9C+9Zlj6fQfSfDSPG
uAk7v5ZlHJ9BjLlKxRgzYRfgPcvS53OJ/nNgxBg3Yc+uZRnHZ1WJqRhjJuy5eM+y9Pmsov88
GDHGTdhzalnG8fnFmK/AGMeYCXt+xejz+UX/BRVj3IT9SsUYx2caY75cMcZM2PdXjD6fafRf
WDHGTRj7VlgXxvGZxph/gxFjzIRdSAgY/dP5DvYi2BR3Ot/BeCTCFHcG3jHmS4RQ9nT8nLAX
EwJG/0wY/ZfAprgJu+MxI8a4x8IY80VCKMuYCXtpxeg/Dkb/ZRVj3ISdXK/HuLNqzBdqHGMm
7OUVo89nH/1XVIxxE3ZKvR7jzq4x/6fGMWbCXlkx+nz20X9VxRg3Yfeq12PcE2vM52scYybs
oorR57OP/qsrxrgJu1+9HuOeXGP+vsYxZsJeUzH6fPbRf23FGDdhp9brMe4pNeZvaxxjJux1
FaP/VBj911eMcRP2kHo9xj2txvxNjWPMhL2hYvSfDqP/AxVj3ITxWANyg3HPgDHmczBijJmw
N1aM/rkw+m+qGOMm7NH1eow7r8b8VY1jzIS9uWL0z4fR/8GKMW7CTq/XY9wza8xf1jjGTNhb
Kkb/WTD6P1Qxxk3Y8+v1bgGMsYz5Cxi/LzHGEXsrbMKeXf23VYwxE/bcpetdAJwx76pxjJmw
t1eM/nNg9N9RMcZN2PPq9Rj33BozXY8xE/ZOvGf96D8PRv/FtSzjJuzdeD99D8byWhfWOMY8
H8aY98AYx7ITxiMqiDHuBTDGvKRijJmwi/GecfS/H3Yx7L0wYoybsEfUsox7IYwxL60YYybs
ErxnWfoXwuh/dCluwt4HnHH0XwSj/34YMV5vwh5ay14I7MUwxkzXY8yEfQDvWZb+S2D0Pwgj
xrgJO61ej3EvhTHmIxVjzIT9MN6zLP2Xweh/CEaMcRN2/1qWcS+HMeblFWPMhH0Y71mW/itg
9D8CI8a4Cbt3Lcu4V8IY8+GKMWbCPor3LEv/VTD6PwIjxrgJu3sty7iLYIz5UMUYM2E/ivcs
S//VMPofXIqbsI8BZxz918Do/xiMGK83YTu1LONeC2PMByrGmAn7ON6zLP3Xwej/OIwY4ybs
TrUs414PY8y7KsaYCfsE3rMs/TfA6F+yFDdhPwGccfR/AEb/J2HEeL0Jy7Us494IY8z7KsaY
CfspvGdZ+m+C0f9pGDHGTRjHcaa4N+MdY95fMcZM2H/Ce8bR/0EY/Z+BEWPchNlalnFvgTFm
uh5jJuxn8Z5l6f8QjP57a1nGTdjP4T3j6L8VRv/ipbgJ+3ngjKP/Nhj99yzFTdgvAGcc/bfD
6L97KW7CfhE44+i/A0b/nUtxE/ZLwBlH/50w+r8KI8bvMWGfrBj9d8Hofwo2xU0Yx+mIMe7d
sE/BOJ5HjDET9suEgD26YvR/hVDFGEtsamM+Eu9ZljHPqtdjnd8DY33fUTF+7oT9Gt7zevQv
htF/21LchH0aOOPovxdG/9dhxHi9CZu+x8XALoEx5q31eoyZsN/Ae5al/z4Y/TcvxU3YZ4Az
jv77YfT/M4wYrzdhHCOd4j6Ad4x5U8UYM2G/ifeMo/9BGP3fghFj3IRxLHaK+2G8Y8wbK8aY
CfttvGcc/Q/B6L9hKW7Cfgc44+h/GEb/d2HEeL0J43jwFPcRvGPM6yvGmAn7L3jPOPofhdH/
PRgxxk3YSbUs434ExpjXVYwxE/b7eM+y9H8URv8PYMQYN2G3rGUZ9zEYY6brMWbC/hDvWZb+
j8Ho/xGMGOMm7Ob1eoz7OIwxr60YYybsj/GeZen/OIz+n8CIMW7CvqOWZdwnYIx5TcUYM2F/
ivcsS/8nYPQvWoqbsD8Dzjj6Pwmj///AiPF6E3ZiLcu4n4Ix5lUVY8yE/Ve8Z1n6Pw2j///C
iDFuwji3YYr7T3jHmFdWjDET9ud4zzj6PwOj///BiDFuwm5cyzLuZ2GMma7HmAn7b3jPsvR/
Dkb//4cRY9yEcT7GFPfzeMeYV1SMMRP2Wbxn3M3xk9hnYS+occQYS+x/wBh3HH4S/++wZYxx
9DlnhHG3xM9nwv4C9pewCTuv+v+zYrfCKzH6f7WEPaP6/6tiJ+GVGP3PLWFPq/5fV+zWeCVG
/2+WsKdU/39X7LvwSoz+3y5hT67+31XsNnglRv/vl7AnVv8fKnZbvBKj//kl7Ozq/2PFbodX
YvT/zxJ2VvX/qWIdXonR/8IS9tjq/3PFbo9XYvS/uISdUf1/qZjBKzH6X1rCHlP9f62YxSsx
+v+2hH1v9f+9Yg6vxOh/eQl7VPX/o2Ier8Tof2UJe0T1L61Yj1dixa8cIvY9/Hf409hJqBj9
qZ+L2ENh9I+tZYeK0T9uCXswcPpXrViET4z+1Zaw04DRn8Y6Enxi9K9R44g9EEZ/GtfIFaM/
9WMSuz+M/jSGcYeK0b8mjH8fxO4Loz+NV3x3xeh/U40jdm8Y/Wls4o4Vo3+dGkfsnjD605jD
nSpGf+qnJnZ3GP1pfOHOFaN/Aoz1I3Y3GP1pLOEuFaM/9csT24HRX+77/wVgfD6cAeP1+MyY
sG+pGP1fhNF/7FLchE3PNT7riNHnnDBej/4vweifVTHGTdj0jOVzlxj9m9Q4+p+E0T+7Yoyb
sOl5Tw0gRv+mNY7+p2D0n1gxxk3YpD0/XjH6N6txjPllGP0nV4xxEzbp5Y9VjP531jjG/AqM
/lMqxrgJm7T7RytG/xY1jjG/CqP/tIoxbsJuWbGPVoz+rSrGmF+D0X/GUtyEnVSxD9c4+reu
GGM+DaN/3lLchE3tqw/WOPq3qXGM+XUY/WdWjHETNrUJ318x+rercYz5DRj9CyrGuAnrKvbe
itG/fcXeXTH6U7udGGOJTW3qH4T/GRjzrymHeNMSNgAnT99VMcb4in0fMOL0p3yBGK9HLNU4
Xu8/w5gzTtf7gSXsDjWO5RjHmFix0+ETpz9djxjjiN2xxvF6vwljnjtd73VL2J1rHMsxjjHf
XbEz4ROnP12PGOOInVzjeL3fgt0J/nS91yxhd61xLMc4xtylYo+DT5z+dD1ijCN2So3j9X4b
tgN/ut6rlrB71DiWYxxj7laxx8MnTn+6HjHGEbtXjeP1fgd2d/jT9V6xhN2nxrEc4xhzz4o9
AT5x+tP1iDGO2P1qHK/3u7B7w5+u97Il7AE1juUYx5j7VuxJ8InTn65HjHHETq1xvN5/gd0f
/nS9lyxhD6pxLMc4xjywYufAJ05/uh4xxhF7SI3j9X4Pdhr86XovWsIeVuNYjnGMeXDFngqf
OP3pesQYR+zhNe5F8H8f9lD40/W+fwl7ZI1jOcYx5nsq9nT4xOlP1yPGOGKPrnG83h/AHgF/
ut7zl7Dvq3EsxzjGPKpi58InTn+6HjHGETu9xvF6fwj7XvjT9Z6zhD2vxrEc4xjzmIqdD584
/el6xBhH7Pk17q7wqbfU4zMrdkrF6D92CaO20n9cxe4Bnxj9s5awXwJG//EVuxd8YvTPXsKo
mfSfULH7wCdGf9JQYp+C0X9Sjbtfxeg/eQn7ZeD0z6nYA+AToz9pIzHqHv2n1rhTK0b/aUsY
NY7+0yv2IPjE6E+aR+zXYPTPrXEPqRj985Ywahf98yv2MPjE6E9aRuzXYfSfXeMeCZ8a9Sz4
z6nYw2scYy5YwhhHf4p7Nnz+zp8LbOLLs5awiQc/BeznYS9A3Cvq9W4Onzix768Y/T+C0X/V
UtyEvbBit6hx9C+s2HMrRv9FFWO5P4bR/6GluAl7ccWeV+Pov6RiL6gY/ZdW7IUVo/+yir28
YvQ/vBRHnNjLl7CXAqP/kYrx+/4sjPfklRX7CfisN7//RRX7RMXov3oJ+xPg9F9TMZabsLdU
7OMVY8xrK/axitH/gYp9BBjx18F/fcU+VDH6b6jYD1eM/lSWGD+X/htr3AcqRv9NFXtfxei/
uWKXVIz+Dy5hfwqc/lsrxutP2PTd+H2J0Z9+v/zdEqP/w7XsxRXjtd5WsfdUjP7bK/ZaYMTp
v2MJ4/WIfWAJewcwxrxzCXs7MPrvqtjrWQ5G/91L2NuA0X/PEvZWYPQvXsJ+CBj99y5hbwFG
/5KKvQE+Mfrvq9gbK0b//RV7NTB+D36HD1bsoorRn+4VMd5D+h+qca+sGP1ljr8YOLn80Rp3
zHF/vTj1uD847eLPHHPxNf7gki+//tJ/uZT/4wT1r/DIdPz/75e+55KTLrrc/1/4yqX/WE5Q
x88X/scnL0GJ8T+8ucmnT7vxb5x243s+g/9/mv+f8Buv+4uTxsPaP/ahiz5y0kUfwc/y/yUf
uug77n7aCfz/ZWee9OLj7n3S60586ItPWFz35ve57l9f40HXPAE1nv4755L3n/wrv3WzHfr8
huN/l52EPiGHf92/uJsc/gOPgF4N+HgC+xiwf/U6QgUqPH7udeBdeunnjr3W4sHPecqZTzvn
lHPPePYTn3r2s37TFoowOfnnP7r+nT/8rlveme+vWoKPr8H3OOOxZx3Ly13K5TOf/+IDfvFJ
7/w5th8W//CKc+64/P7iu/zxHQ7FEX+nKYbvz3z7A+7EGF5nek//+Av5GfgILL1Z/gzU6xd/
5J9uyjbH4p/O+vFfeMI9dsr7f3jF3/78J97+gOn9d0/vEXPHKQZl7zSVXa4HrzV+Hj/wquW6
n3v3G+84fcYX/vYfyvtX5zv9wvL7D97zdqXurMf0/muvdRW6i+lafH/4uKsvcO07TnF8P30O
638kfDlmui7LTu/5edN/x09vyuull/7dscct7na/h92Xv3D82X/Nv15jyXvZP7/9ZNoSBEpY
tg8Xv/Pb97vTR/5x3OTsUP8Jx1A2L7zLaKeXP99KLobu4r9xgddlgbzW4mT8D7sQdjHsU7DP
wha4/nVgJ8IM7GTYqTB+7tNhF8JeCXsD7K2wi2Efgn0c9jOwT8E+A/s92J/BPgv7HOzzsC/B
ODf1ONg1YNeEXQd2AuxGsBvDToTdHHYS7LYwA+thCXZH2MmwU2D3gt0PdirsIbCHwx4NOx32
ONgTYOfAng47H3YB7PmwC2Evhr0U9nLYK2EXwV4Dex3sDbA3wt4MewvsrbC3w94JezfsYtgl
sPfDPgj7EOwjsB+BfQz2cdgnYD8J+2nYz8B+DvYLsF+CfQr2K7Bfg/067DOw34T9Nux3Yb8H
+wPYH8H+BPZnsP8K+3PYf4N9FvY/YH8J+yvY52B/A/tb2N/DPg/7P7AvwL4I+xLs32Bfhn0F
xv7GY2BXgR0LOw52VdjVYFeHXQP2DbDjYd8IuybsWrBvgl0bdh3YdWHXg10fdgLsBrBvht0Q
diPYt8C+FfZtsBvDbgL7dthNYSfCbgb7Dth3wm4OuwXslrBbwU6C3Rr2XbDbwG4Lux2sg90e
ZmAW5mAe1sMCbIBFWIJl2B1g3w27I+xOsDvDOJf5ZNgO7K6wu8FOgd0ddg/YPWH3gt0bdh/Y
fWH3g90f9gDYA2Gnwk6DPQj2YNhDYA+FPQz2PbCHwx4BeyTsUbBHw74X9n2wx8BOh50BOxP2
WNjjYGfBHg87G/YE2BNhT4I9GXYO7Cmwp8KeBns67Bmwc2Hnwc6HPRP2LNizYRfAngN7Lux5
sOfDXgD7ftgLYRfebXEhbPEivMIWL8YrbPESvMIWL8UrbPEyvMIWL8crbPEKvMIWr8QrbPEq
vMIWF+EVtng1XmGL1+AVtngtXmGL1+EVtng9XmGLN+AVtvgBvMIWb8QrbPEmvMIWb8YrbPGD
eIUt3oJX2OKH8ApbvBWvsMXb8ApbvB2vsMU78ApbvBOvsMW78ApbvBuvsMV78ApbXIxX2OK9
eIUtLsErbPE+vMIW78crbPEBvMIWH8QrbPHDeIUtPoRX2OLDeIUtPoJX2OKjeIUtfgSvsMWP
4hW2+BheYYsfwyts8XG8whY/jlfY4hN4hS1+Aq+w8p+ez3o+XwVcOBZ2HOyqsKvBrg67Buwb
YMfDvhF2Tdi1YN8EuzbsOrDrwq4Huz7sBNgNYN8MuyHsRrBvgX0r7NtgN4bdBPbtsJvCToTd
DPYdsO+E3Rx2C9gtYbeCnQS7Ney7YLeB3RZ2O1gHuz3MwCzMwTysh52y84Grn7Lzlm8/ZefP
Tzll5+XPPWXnI588ZefME+6+83sX3H3nxn93953znnGPnWte7Z47N/voPXe+ePq9dv7kVvfe
ud7iPjtX/Zv77Fz3r+67894v3G/nNt/8gJ3b3feBO7d/86k7n/7H03Ze/7gH76S/e8jOBa95
2M4N7/bwnb+57iN3/vRfH7XzJ//+vWhnnP41doeHPHonv/VhO28dTtv5q1vdb+fCs+65c8Ff
33Xn+R+7886v/tgddr78uWHn5If5nWt84fY7N/nkbXfe/JO33vm137/lzp1PuPnOZ55zs52H
L266c+0P3ninf+K37th73Wjn9TvfvPPFB5+wc8vvv97Ol37pOjuPusG1d0678Fo7n//KN+48
+g3H7/y2/4adl3zu6jt/+KNX27nRS6668/NnH7djH3XszhcefZWd155zzM5Fr1rsHHv2pSff
4o/+4+RPP+LLJ9/xX/7t5L//6L+efP9nf+nk8Rmgn23fAXFanG6bofNrJ06L0/NZ03YJcVqc
bpuh82snTovT81nTdglxWpxum6HzaydOi9PzWdN2CXFanG6bofNrJ06L0/NZ03YJcVqcbpuh
82snTovT81nTdglxWpxum6HzaydOi9PzWdN2CXFanG6bofNrJ06L0/NZ03YJcVqcbpuh82sn
TovT81nTdglxWpxum6HzaydOi9PzWdN2CXFanG6bofNrJ06L0/NZ03YJcVqcbpuh82snTovT
81nTdglxWpxum6HzaydOi9PzWdN2CXFanG6bofNrJ06L0/NZ03YJcVqcbpuh82snTovT81nT
dglxWpxum6HzaydOi9PzWdN2CXFanG6bofNrJ06L0/NZ03YJcVqcbpuh82snTovT81nTdglx
Wpxum6HzaydOi9PzWdN2CXFanG6bofNrJ06L0/NZ03YJcVqcbpuh82snTovT81nTdglxWpxu
m6HzaydOi9PzWdN2CXFanG6bofNrJ06L0/NZ03YJcVqcbpuh82snTovT81nTdglxWpxum6Hz
aydOi9PzWdN2CXFanG6bofNrJ06L0/NZ03YJcVqcbpuh82snTovT81nTdglxWpxum6HzaydO
i9PzWdN2CXFanG6bofNrJ06L0/NZ03YJcVqcbpuh82snTovT81nTdglxWpxum6HzaydOi9Pz
WdN2CXFanG6bofNrJ06L0/NZ03YJcVqcbpuh82snTovT81nTdglxWpxum6HzaydOi9PzWdN2
CXFanG6bofNrJ06L0/NZ03YJcVqcbpuh82snTovT81nTdglxWpxum6HzaydOi9PzWdN2CXFa
nG6bofNrJ06L0/NZ03YJcVqcbpuh82snTovT81nTdglxWpxum6HzaydOi9PzWdN2CXFanG6b
ofNrJ06L0/NZ03YJcVqcbpuh82snTovT81nTdglxWpxum6HzaydOi9PzWdN2CXFanG6bofNr
J06L0/NZ03YJcVqcbpuh82snTovT81nTdglxWpxum6HzaydOi9PzWdN2CXFanG6bofNrJ06L
0/NZ03YJcVqcbpuh82snTovT81nTdglxWpxum6HzaydOi9PzWdN2CXFanG6bofNrJ06L0/NZ
03YJcVqcbpuh82snTovT81nTdglxWpxum6HzaydOi9PzWdN2CXFanG6bofNrJ06L0/NZ03YJ
cVqcbpuh82snTovT81nTdglxWpxum6HzaydOi9PzWdN2CXFanG6bofNrJ06L0/NZ03YJcVqc
bpuh82snTovT81nTdglxWpxum6HzaydOi9PzWdN2CXFanG6bofNrJ06L0/NZ03YJcVqcbpuh
82snTovT81nTdglxWpxum6HzaydOi9PzWdN2CXFanG6bofNrJ06L0/NZ03YJcVqcbpuh82sn
TovT81nTdglxWpxum6HzaydOi9PzWdN2CXFanG6bofNrJ06L0/NZ03YJcVqcbpuh82snTovT
81nTdglxWpxum6HzaydOi9PzWdN2CXFanG6bofNrJ06L0/NZ03YJcVqcbpuh82snTovT81nT
dglxWpxum6HzaydOi9PzWdN2CXFanG6bofNrJ06L0/NZ03YJcVqcbpuh82snTovT81nTdglx
Wpxum6HzaydOi9PzWdN2CXFanG6bofNrJ06L0/NZ03YJcVqcbpuh82snTovT81nTdglxWpxu
m6HzaydOi9PzWdN2CXFanG6bofNrJ06L0/NZ03YJcVqcbpuh82snTovT81nTdglxWpxum6Hz
aydOi9PzWdN2CXFanG6bofNrJ06L0/NZ03YJcVqcbpuh82snTovT81nTdglxWpxum6HzaydO
i9PzWdN2CXFanG6bofNrJ06L0/NZ03YJcVqcbpuh82snTovT81nTdglxWpxum6HzaydOi9Pz
WdN2CXFanG6bofNrJ06L0/NZ03YJcVqcbpuh82snTovT81nTdglxWpxum6HzaydOi9PzWdN2
CXFanG6bofNrJ06L0/NZ03YJcVqcbpuh82snTovT81nTdglxWpxum6HzaydOi9PzWdN2CXFa
nG6bofNrJ06L0/NZ03YJcVqcbpuh82snTovT81nTdglxWpxum6HzaydOi9PzWdN2CXFanG6b
ofNrJ06L0/NZ03YJcVqcbpuh82snTovT81nTdglxWpxum6HzaydOi9PzWdN2CXFanG6bofNr
J06L0/NZ03YJcVqcbpuh82snTovT81nTdglxWpxum6HzaydOi9PzWdN2CXFanG6bofNrJ06L
0/NZ03YJcVqcbpuh82snTovT81nTdglxWpxum6HzaydOi9PzWdN2CXFanG6bofNrJ06L0/NZ
03YJcVqcbpuh82snTovT81nTdglxWpxum6HzaydOi9PzWdN2CXFanG6bofNrJ06L0/NZ03YJ
cVqcbpuh82snTovT81nTdglxWpxum6HzaydOi9PzWdN2CXFanG6bofNrJ06L0/NZ03YJcVqc
bpuh82snTovT81nTdglxWpxum6HzaydOi9PzWdN2CXFanG6bofNrJ06L0/NZ03YJcVqcbpuh
82snTovT81nTdglxWpxum6HzaydOi9PzWdN2CXFanG6bofNrJ06L0/NZ03YJcVqcbpuh82sn
TovT81nTdglxWpxum6HzaydOi9PzWdN2CXFanG6bofNrJ06L0/NZ03YJcVqcbpuh82snTovT
81nTdglxWpxum6HzaydOi9PzWdN2CXFanG6bofNrJ06L0/NZ03YJcVqcbpuh82snTovT81nT
dglxWpxum6HzaydOi9PzWdN2CXFanG6bofNrJ06L0/NZ03YJcVqcbpuh82snTovT81nTdglx
Wpxum6HzaydOi9PzWdN2CXFanG6bofNrJ06L0/NZ03YJcVqcbpuh82snTovT81nTdglxWpxu
m6HzaydOi9PzWdN2CXFanG6bofNrJ06L0/NZ03YJcVqcbpuh82snTovT81nTdglxWpxum6Hz
aydOi9PzWdN2CXFanG6bofNrJ06L0/NZ03YJcVqcbpuh82snTovT81nTdglxWpxum6HzaydO
i9PzWdN2CXFanG6bofNrJ06L0/NZ03YJcVqcbpuh82snTovT81nTdglxWpxum6HzaydOi9Pz
WdN2CXFanG6bofNrJ06L0/NZ03YJcVqcbpuh82snTovT81nTdglxWpxum6HzaydOi9PzWdN2
CXFanG6bofNrJ06L0/NZ03YJcVqcbpuh82snTovT81nTdglxWpxum6HzaydOi9PzWdN2CXFa
nG6bofNrJ06L0/NZ03YJcVqcbpuh82snTovT81nTdglxWpxum6HzaydOi9PzWdN2CXFanG6b
ofNrJ06L0/NZ03YJcVqcbpuh82snTovT81nTdglxWpxum6HzaydOi9PzWdN2CXFanG6bofNr
J06L0/NZ03YJcVqcbpuh82snTovT81nTdglxWpxum6HzaydOi9PzWdN2CXFanG6bofNrJ06L
0/NZ03YJcVqcbpuh82snTovT81nTdglxWpxum6HzaydOi9PzWdN2CXFanG6bofNrJ06L0/NZ
03YJcVqcbpuh82snTovT81nTdglxWpxum6HzaydOi9PzWdN2CXFanG6bofNrJ06L0/NZ03YJ
cVqcbpuh82snTovT81nTdglxWpxum6HzaydOi9PzWdN2CXFanG6bofNrJ06L0/NZ03YJcVqc
bpuh82snTovT81nTdglxWpxum6HzaydOi9PzWdN2CXFanG6bofNrJ06L0/NZ03YJcVqcbpuh
82snTovT81nTdglxWpxum6HzaydOi9PzWdN2CXFanG6bofNrJ06L0/NZ03YJcVqcbpuh82sn
TovT81nTdglxWpxum6HzaydOi9PzWdN2CXFanG6bofNrJ06L0/NZ03YJcVqcbpuh82snTovT
81nTdglxWpxum6HzaydOi9PzWdN2CXFanG6bofNrJ06L0/NZ03YJcVqcbpuh82snTovT81nT
dglxWpxum6HzaydOi9PzWdN2CXFanG6bofNrJ06L0/NZ03YJcVqcbpuh82snTovT81nTdglx
Wpxum6F7qd2ll77vs9+wePD5Zz3xqWedc63j/YnXOt7A/MCflpamd3c969lnnf3Mp5593lPO
OudxZ5174t3PffwZ550HAFGn3u3EUx/0wBPv/aATT3vozkMegrf3OgWwMcb3GW8ecu4zzzrx
6eeedd5ZT33sWY85/6zzzgd4yhnnP/MpeLWmfMQRfvLflq1UiqUqPvk755xz9llnnnvGMx/7
hPPOPufLTzjnjKc8/axrHR8tC19A4w/TxYCXqXD54OpPmGNYCc2s+hRCmLenh/ESAyzCEoxx
5XNsqQ1DLWMtg235QIZbxlsWsCzheGnHEo4lHEs4lnAs4VjCsYRjCccSniU8S/hSHZbwLOFZ
wrOEZwnPEp4lepboWaJnib58A5boWaJniZ4lepYov6rAEoElAksElggsEVgisERgicASgZ9R
uDKwxMASA0sMLDGwxMASA0sMLDGwRORnRJaILBFZIrJE+eVElogsEVkiskRhYWKJxBKJJRJL
JH5GYonEEoklEktkfkZmicwSmSUyS2SWyCyRWSKzRPlNTzxkGWtYyBqWsobFrGE5a1jQGpa0
hkWt4afZ+usvZW0pOzJgpMDIAVvKjiwYaVB4YAsRbGGCLVSwhQu2kMEWNthCB1v4YAshbGGE
LZSwhRO2kML6UudCC1t4YQsxbGGGLdSwhRu2kMMWdthCD1v4YfvyfQtDbKGILRyxhSS2sMQW
mtjCE1uIYgtTbKGKLVyxhSy2sMUWutjCFzs+XApjbKGMLZyxhTS2sMYW2tjCG1uIYwtzbKGO
LdyxhTy2sMcW+tjxj7sQyBYG2UIhWzhUH2WFRbbQyBYe2UIkW5hkC5Vs4ZItZLKFTbbQyRY+
2UIoWxhlC6Vs4ZQtpLKFVbbQyhZeufJkc4bccIVXrvDKFV65witXeOUKr1zhlSu8coVXrjxX
XOGVK7xyhVeu8MoVXrnCK1d45cbny/iAqU8YctKNz5jxITM+ZcbHzPicGR80hVeu8MoVXrnC
K1d45QqvXOGVK7xyhVeu8MoVXrnCK1d45QqvXOGVK7xyhVeu8MoVXrnCK1d45QqvXOGVK7xy
hVeu8MoVXrnCK1d45QqvXOGVK7xyhVeu8MoVXrnCK1d45QqvXOGVK7xyhVeu8MoVXrnCK1d4
5QqvXOGVK7xyhVeu8MoVXrnycHKFV67wyhVeucIrV3jlCq9c4ZUrvHKFV67wyhVeucIrV3jl
Cq9c4ZUrvHKFV67wyhVe+cIrX3jlC6984ZUvvPKFV77wyhde+cIrX3jlC6984ZUvvPKFV77w
yhde+cIrX3jlC6984ZUvvPKFV748r3zhlS+88oVXvvDKF175wis/KtgoYaOGVRHj88qPMjbq
2Chko5KNUlZ45QuvfOGVL7zyhVe+8MoXXvnCK1945QuvxgaIL7zyhVe+8MoXXvnCK1945Quv
fOGVL7zyhVcUkvK3y3rC+HQsyobXojl4LRpQAosCFAEoz+HyKC3KUR7+RTeKbLCEWgC4g7xX
agHgJqgFsO8tANfV1hReIfWDger7sXHAf4r9MGQbgZc/VkDDkCxaY6mPY3MIUMwZLa2AdtDY
TgKUh5jxNM55KoeHZh+HHioXxqaZ6/Dcyjn4AW2LscUIKBqfYhw8nkXjY6PrDfQoxmzy2PR0
Xe9TjgFFBzO2QwHFjFoE1MKMzUvXBYhxdNAXk8eWEyD4EE+0MsaWk+sGqCuaUYHVKA8nQAnt
CTzKjRk13bou9h7f2iR8o7Hx57pkcoSqo+wwtq0AJdOjsYpr12aS63IIuJt4GuPy5TnnO4Pv
G2NEi3WULOs7sDxAoyPaPbVd2qFhY4IJOab6FX0Hxcpoe6LpUdubHrcmQxV7i1qMzTDfBTQc
cSNMhIyWZ6zHd8w++hgNvli5px5fKPV5QEEztqlQiRR9TtA9k/uxKT+2ePlHeNk7lIwmDBBD
fOL4m0UtUH/8wlLOYwMEFzMxJKh/xC9jbH/iHuLL9LhB0dbGN35pA349BjoU8thCd51NoATu
Wo+2RvlY24F9+F0bfP1+zC5sN4BcSD5ANzP+ai04gZuObx1wd8qXtB0ajSHgi0P2x+as6XKO
Bjd/iGG8E8h9QQ78jgwJNOYxHage0hDRTq5NWdP1aDwh9wDp05gVGPxp4OPR4sXtHpvzpsNv
A83DlO0wZkm5w43HZ+NXPYDUJQXDB6LiqGuGIpevmLshmCH1aB+YlIq4Z/wa44BmIe4Nonkj
cufxlXHvY4QQl6Zcxh+e6fFLI8vB6xKFPCPmhD/P0IfyR5U7cBaswe8C/1LuTeoy7i9yHe9x
b0ojMHWoQEKjjnQOpQWTwBL+yhDJr8ibk3DnDdqsxkfc2tIqS/ijwh9+QE3w2yxNotThzqBt
iYslpCv82oDw549fBZob+PvgX1rCnz+qCOLnHr+N8fKoAJ4j+FsAB0uTJOG3mPE4KEQFgUtB
kArXyPiNmVgh/G0aPLn6kPBo4p1I+ENDuyXhMYU/l9JojB3qgxYZ/qRA+9LWBMQ/J/yyM54x
pZkc8XeMxwF+ESDi+OQAhO+Dh1wEDcAKXB6QwS+73KuM+ALh8Ya/DbQX8YssTUS2fmTt3gM8
2iV+Ej+Jn8RvFeJXMl+Jn8RvLURf4qfMD8mdxE/it57ixzwMad6VZH5MLPeU+TGLVOa3oRms
xE/iJ/FTt6e6PdXtuRbZ2iq7kSV+Ej+Jn8RvReK3Pt2e4zCdhvw2NKnbjUZK+6R90j5p39Zp
n+a7tDsPZTfCtYoYiZ/ET+In8ZP4Hb7XU0N+G5wZSvwkfhK/rRa/cZHBalY6HHyv5+7mu4wa
ppUOyvaWM0aJn8RP4rfV4jeuiluN+JUtZRpc6bDnyZ5jQS3z28i5MBI/iZ/ET+K3om5PiZ/W
uK9Pdinxk/hJ/CR+Er/Dj/kp89OYn3Y30+5mRSO1u1nZplO7m63X7mbq9lwe69L7MTtV5qfM
T5mfMr+1zfz2ecKLZnsq81Pmp8xPmZ/2tda+1trXen3G9K4sw1Xmp8xPmZ8yv7XN/MZzHq5s
a08tdbgyIdjGf5f4SfwkfhK/DRc/jflto7hd2XeW+En8JH4SP4mfZntu5Fq+KxJAiZ/ET+In
8VuR+B38Di/q9tycMbgrEqr9+DeJn8RP4rfV4scuQR3kroPct09EJX4SP4nfVovfnrc364tq
hhhsH6LpB+fswe/wss9LHQ6zyJ25Jo63Nc75OATncgrj8Uhx6MOgHV7WR0QlfhI/iZ/Eb0Xd
nhI/iZ/ELw8xe2NyNmw7QWK9jT2aRq4fgmdrjVBvcw5+sCkatp0IReNTjGg/fTWqNw5dEjGb
bPwY1PuUY0DRwRi2PlGuj9nFHKx3xlYoOD9E53jtodYhwHcBMf1QP29wQeKHO+i7FH1O3jqT
e8ORm/E2lnt52Q/faYcX7fDSGx/Teu3wssqlDsr89mP87WhcE8LhyIzyahMWsdoUfKza4ELs
hyHbqEXuWuReNFLiJ/FrSvwOvtuTn6huz6MhVqv+TImfMj9lfur2XFG3p2Z7qttT3Z7q9mQy
nUNAHu37Hp27pS/RdwbdvDFG65LLJb/2nXU2OKDOIIxZuO8c+h+DCTmm2rPrO29itphV4J3t
a8HeZJf73toh59KV7LtgB+TtwUSXTcnofTe47KNHypacrVGxT30eUNCgm3P8RHV7unLvTTeY
IaQhWmxklUuPr+l6N+A3gu523Ddlfk1lfvx1pE47vKw6K9qG6ynzU+anzE+Z34oyv4Of8LI7
8WO7JnbLJ7mzzQeETUk0dLJWOqxPwrYqXZb2SfukfdK+rdO+JPHbug1dDhVNiZ/ET+In8ZP4
aXezrRNDiZ/ET+In8ZP4SfwkflrpgGkhHiMBxjhf14DE3g9a6VA0UisdNN/lCua7aLKnJnuu
z9ihMj9lfsr8lPmtKPM7ePE7+GV+bP1omd+h42fr6Ev8JH4SP4nfisRvfSZ7asLL+mRo+yWs
Ej+Jn8RP4rfh4rfK3c20wct+idFBX1fiJ/GT+En8JH6a8KIJL5rwogkvZS+ay3azvuyd9rXW
Bi+uv4IJL+r21ISX9elOVeanzE+ZnzK/FWV+Bz/hZa8bvGjMb31Ear+6QyV+Ej+Jn8RvReJ3
8Jnf7mZ7Xn53s72Ln2Z77pcYHfR1JX4SP4mfxG9txW93md8qJ7xI/A5apPbr8yR+Ej+Jn8RP
4qcJL5rwogkvmvCiCS860QjHBMU+x964aH0MkR2HqcOZ1ms54WWVmZ+WOuxXJnbQ11Xmp8xP
mZ8yvxVlfprwotme6zORRuIn8ZP4SfxWJH4HP+Fld2N+q5zwoszvoDO0/fo8iZ/ET+In8dtw
8Vtlt6cmvOyXGB30dSV+Ej+Jn8RP4qcJL5rwogkvmvCiCS+a8LJZE15W2e2pzO+gM7T9+jxl
fsr8lPkp81Pmp8xPmZ8yP2V+yvyU+e0t89NsT8321GzPPMTsjcnZsMcB+aW3sY9D7/oheM6X
ItTbnIMfbIomVygan2IcvP9qFFYaDTnGbLLxY1DvU44BRQdjyqbLrutjdjEH652xFQrOD9E5
XnuodQjwXUBMP9TPG1xQ5qfMT5mfMj9lfsr8lPkp81Pmp8xvb5lfq0sdNNtzv8bN1vm6GvNT
5qfMT5nfhmd+q5zwonV+6yx4y3WX+En8JH4Svw0Xv1VmfhK/ZQFZ5/cSP4mfxE/ityLx04QX
TXjRhBdNeOGUnhxCCt73Pab1lIE03xlM8IkxWpdcLrNufGedDQ6oMwjjnB7fOQvHhBxTndPj
O29itv3gvLN9Ldib7HLfWzvkXCYR+S7YwWPmj4kuGzZ3ca3BZR99jAaDmTUq9qnPAwoaN041
8l2KPiePj8290Zifxvz2NubXqvitMvPTOr91zvaW667MT5mfMj9lfivK/Fqd8LLKMT+J37KA
rPN7iZ/ET+In8Vtb8WNfRupMygbz1PuQrPNM8wBhuVRMqY/oKMkSv3UWqf2qu8RP4ifxk/it
SPxa7fZcpfhpwst+idFBX1fiJ/GT+En8ViR+29DtKfE7aJHar8+T+En8JH4Svw0Xv1VOeJH4
7ZcYHfR1JX4SP4mfxE/ip+3NtL2ZtjfT9mZa6qClDntb6qBuT63z0zo/rfPTOj8bsct4LKsN
XYedyGNvehutHRczYjfyAfuOG8/1jL7uWW4T9jrH6sjeRV82KLddttzE3GCZY2/4bLW2G7Br
ujWhx5LEcc9y2/XepoTVjQGrINkvhShnUghY4OhNSOVapss5GiyyHGIYVzyaLmLXc6zFNNwZ
vayxNN1ggAzRRtSlluvdgJWX2FAd6yM5092azvHjbfZYVhlKY8F0WHXpUI1sB1v2YM8dFlji
s7Gkc8Bu7VycmfGBqDjqmn0/fsXcDcEMqfduMCl5fsWM5ZpxcFgdGgyiWYnceXxlE4YYPWrH
SuTORdNjcSa3b8eG7QWy+Mo5OZ9CH8oSztxhG3esDsXvAv9S7k3qMu6v7TEfEvdmGCdHogLJ
4U4PcQiOl09d7PkrQyS/Im9Owp03rkfBiFub+TtLXcDN7ANqgt+mbVX81O150F2K6/B56vZU
t6e6PSV+6vZUt6e6PdXtqW5PdXsq89tb5qelDur2VLenuj3V7aluT3V7ooO6dI6iv7tHD7RH
F+lQ+0u565/Bvn65Ryf02KuKflePnusBXbIxjH2v2G8Px3uWffiwP1+5FvrScY2MjmoTKzR/
kTurFdEvjW5ydHFnHBk61GmcKeSA7md0v48HgUZkxQ7fI0d0fqMvvBRMBl3cpYc4I75AOK00
4CBSXM8ky1bAOvT8bXMd1eupXk/1eqrXc8N7PbXGfZtF7kjfXeIn8ZP4Sfy2TvyU+G19Yirt
k/ZJ+6R9G659mut5pORnm3GJn8RP4ifxk/hpyG/rMkGJn8RP4ifxW1vx4+yTKz/TQZnfNmd4
R/ruEj+Jn8RP4rci8dNCB032XJ9JrhI/iZ/ET+In8VO3p7o9tcRdS9y1xF1L3Ddrifsquz25
1BAr/7TMb+3FUpmfMj9lfsr8VpT5aWdPdXuq21P7u2h/F+3vsnX7u7Q65rfKzE8bvBxpAsm6
4cr8lPkp81Pmt+GZnzZ4WTdhOoj6SvwkfhI/iZ/ETxNe1n4Mb65gSvwkfhI/id+Gi5+6PecK
wzbES/wkfhI/iZ/ET5mfMj8tddBSBy110FKHzVrqsOcxvzFl1IlGGymMyvyU+SnzU+a3tpnf
7rY327P4jQUlfhI/zt53w5CsdT71sWeziBCOebQ4gtL2ue8rpKUOWuqgpQ5bt9Sh1XV+Er9t
GMOb+x2V+SnzU+anzG9tM7/xaPf557gnnee3kdncHAGU+En8JH4SP4mfJrxsnRhK/CR+Er+t
Fj92CaYVid/B7/CyuzE/LXWYkxFtS6zET+In8dtq8aMwrK/47a7bc8/iNxbUhJeNzAolfhI/
iZ/Eb20zv30WP832RNNoUzNBiZ/ET+In8ds68dN8l43VtN1qtbRP2iftk/atSPtaXemw515P
JX5K/IbBkAaUSi3z421IJkfXUziHWO9MSqa3zvVDtokPAUTlEFLwvu+DH8quKb4zfrAxRuuS
y2x8Wt9ZZ4MD6gzCRshZOCbkmIwpKyd9503Mth+cd1hOOUb1JjusrLSoRea4P64V7OBjDia6
bPgXD2hwWG3mYzTYuaZGxT71eUBB40y9Voo+J4+Pzb3RBi/a4GVdNnjZ3XyXUcNywmrkHn9S
oP0uVzpoyA8Pkd1mUusWp8xPmV+RSImfKw0P06GdFyR+6yJ+GvLbXHHabzGV+En8JH7q9lS3
p5b5bWyGdyQRlfhJ/CR+Er8Vid/BL/NT5qfM70jidmW4xE/iJ/GT+K2t+GnMT+J3ZSJ3pH+X
+En8JH4SvxWJn2Z7eo9ZaSZZ5sBHeugKb+PeSPwkfhI/id+KxG99uj21zG/rtVnaJ+2T9kn7
tk77drnSYVwioc3NNlIoJX4SP4mfxE/ip8meGylwV9TDLPGT+En8JH4rEr+DH/LTfJc2hs+u
SGRa/TeJn8RP4ifxW1vx291Khz1v8KJuzw2etyPxk/hJ/CR+Gy5+2tqz1ezraNZL4ifxk/ht
tfgxuVnVaX4H3+2pzE/dnnsVUImfxE/it9Xix6xI4jdowosmvBiLYwhi2ekfJziE2A84pCDq
UIchYR94b3q2k9Fi0KEOeTzmw3c4yQInSfiUM+jCu4OTK2JIDut8je1jOVrCdREnVPQ49SJa
O55c4TqcUOGS8Ty8wvvxttpkc8ZRGL2LvhxmYTuwL+RscKZFb8pZGbYbBpxvYUKP8yeG8vuw
Xe9xkgaOsgg48qKcXGE7bNwfAk6z8Cakci3T5RwNTtQYYhiPtzBdzAN2sZb4rW235+4mvOy5
23MsqKUOGymMyvyU+Snzk/itrfjtrttzz+KnCS9ole61W7H1chI/iZ/ET+In8VO358aK3JFE
WOIn8ZP4Sfw2XPzGBG4PZ9kq81PmpzE/jfkVjcR58GHwNuDoeI359Tb7wcdxpNN0JjuHocds
B2s4hpm7jH/EeFFyQ4plHD1jkBGDlRifzL4fhzVzNwQzpN47bIecPIc1cxcwzO76gPFQRHPA
Mncew5y49zF6nLTLzr7cuWj6nHzE0Klz7NnLncUwZ07Op9AHw5H73GGcenAe46/4lzIemrqM
MVXbG+8xHjqw4KZPeFG355Gyn23Glfkp81Pmp8xvbTO/fZ7woswPTaNNFUiJn8RP4ifxW5H4
tXqog7o9N1XAvp7vJfGT+En8JH4rEr+DX+R+8Jkfu5wj1jqhjzsOwbmcwng8Uhx6DAnoOL+1
yRQlfhI/iZ/ET+K369meEr+vJ9tqqazET+In8ZP4ra34Hfw6P4lfSwL29dRF4ifx20rxK1Mh
rbZ4Wfvpngff78lPVL/n16M6rZSV+kn9tlL9+AiT+K16rUOrM1601qEVwWmpHhI/iZ/ET/2e
6vfc9aCfMr+WBOzrqYvET+In8ZP4bbj4aa3D1yMSm1pW4ifxk/hJ/NZW/DTmt7mr0PdbdCV+
Ej+Jn8RvbcVvd9M9lfntt5Cs4/UlfhI/iZ/Eb0Xid/ATXnaX+Un81lGc9rvOEj+Jn8RP4rci
8Tv4LV6U+anbc68iKfGT+En8tlr8mBWt6liHg8/89ip+45Zk2TvbD9HmYdeTPbXIfa9a01o5
aZ+0T9q31dq3DUca7bnXc1wfiGOphphzdIOLSSsdWhOxvdZH4ifxk/hJ/Da811Nr3PcqEJtc
TuIn8ZP4SfxWJH6t9npeXvz23OupxG9T9FDaJ+2T9kn7tk77ksRvbU4e2i+xlfhJ/CR+Er8N
F789D/mNBTXkt5FCKfGT+En8JH4rEr9tWOigyZ77lYkd9HUlfhI/iZ/Eb8PF7/JDfnvv9pT4
HbRI7dfnSfwkfhI/id+KxG995rtI/LQ0XuIn8ZP4SfxWJH6tdnuuMvPTbM/9ysQO+roSP4mf
xE/iJ/Hb9QYvEr+DFqn9+jyJn8RP4ifxW1vxoxSlzqRsjE19SNZ5pnmAvA8xpT7aPmfN9twv
AVnn60r8JH4SP4nf2orf7nb2XGW3pya8rLPgLddd4ifxk/hJ/CR+6vbcyLV8y2J36HuJn8RP
4ifx23DxW2W3pzK/Q0VkXX2Jn8RP4ifx23DxW2W3pya8rKvYHVpviZ/ET+K31eLHrGj7TvPb
+zo/id+hIrKuvsRP4ifx22rxGydHpt4nF0Me4hDcOIsk9jn2xkXrY4ijRA6DcX1vfEwhZF9U
M8Rg+xBNPzhnD36Ru2Z7arH6XsVX4ifxk/httfitMvNbn0Xuez7UQUN+e9Wa1spJ+6R90r6t
1r5VJn6tat8q57uo17M1EdtrfSR+Ej+Jn8Rv6+a7KPHbuoUNh2qktE/aJ+2T9m2d9mm6i0YK
JX4SP4mfxG9F4nfw013GmTlXtrmZFjocmvXIx2PPdY7MKK82YS6XTcFH9gkUKPbDkG0Ezl5z
QsOQLLbPw5Z5/VQw5my9w5Sv3Pc1CnPGsjcm56mct7GPQ+/6IXh2muNSvrc5Bz/YFE39QB+N
TzEO2JVvisJssyHHmE02nFyGcpiVljErLYfBmPp5fcwu5oBaGFuh4PwQneO1h1r3AN8FxPRD
/bzBBYkfbqrvUvQ5eetM7g0fYeNtLPfysh++i9GEwdswTL9Z3/XWWfzCUs4ulJK+MzEkl2zE
LyNWkuAXhomDvY3W+vrr4OzAZHwwmDZYf7U2gRI5hN5FXz7WdmAfftfGGxTniJK13QByWRNA
NzP+ai04YVMy0QVn+0Iv2zmDCYnRR29CKtcyXc7RRNAL0xNLkOkiyBGSxG9F4tfqkJ/ET2J3
+Uy3KNyoKVAviZ/rhuSs984aM26QizsUew/JR+vSQzbHm5VMjq6ncGJmeIUSnu0O6p7xHB4h
PMbRlPB9D4mfdAFij+evdcnlosC+g3gEB9QZhLGg7xxUiKIQU9V33+Hpny30AlXra8HeZIf2
hkUtcnmY+y5Ah9AKgAxkU2THd4PLUACoFr5YjYp96vOAggZiN36ixM+Ve286tPNCGqKNEOIq
mr0b8BtBowv3jamGNWgyQntt9rjdo+SbDr8NBw3OdrClnZY73HgIL37VA1p0vNEZagvVBkGy
70d9z90QzIB1Bm4wKXkyJ+PXGAcH1gSDaFYidx56j4ZHjB61YyVy57C8AC0WNvHQqCuQhd7n
hLZp6EP51eYOnAVr0BDBv5SGQeoyGhcW6xU8GgYDC65qlV+r4sdfbexyQuu4x58UaK9uz8uL
wbYJpMRPmV+RW4mfxO/rX+XXqvgp89s2YdvN95X4Sfwkfur23PBuT2V+uxGDbYuR+En8JH4S
vw0XP2V+2yZsu/m+Ej+Jn8RP4ifx04FGW7fuT+In8ZP4SfzWVvw4hWsfz3EfU0ZMWsIEY0xx
GxymQZXJM8lgdlPZBTWnwLlMscNkdsyE9piVZjDTGdBusg/FHL37JPGT+En8JH4rEj8+8lOH
ebBuwHbXmF0JzRghrHTCnGOP9VBD3Q+bk6ANpjnnHgtPOCiXMH0VC5E48xnLbcK4gg/TkbHy
qUxLxnTlEoX1M7hGxuomM0rRlYvfKrs9WYnYSfyOnmitqsEg8ZP4SfwkfisSP832VOa3PqIo
8ZP4SfwkfhsufprtuapsaZOuI/GT+En8JH4bLn6r7PbUmN+mCKDET+In8ZP4Sfw023PrJuhI
/CR+Ej+J34aL3+W7PccJmpmbBWIru4ztg4ea0mHyZsA2c9hjdtwUGJNbNNlzU5K95e8h7ZP2
SfukfRuufer1XH7o6/04J0fiJ/GT+En8ViR+B7/SYVz8oBONJGjzJ5lK/CR+Ej+Jn8RP3Z4a
8tNxfjrRqBy+VA7zOeSHjvPTiUaux1FIEScl1qXqWMtu+4CzlXA4o9UyPy3zm5+BHa2sVZmf
Mj9lfsr8NjzzW+F8F+3vcrS0atWfK+2T9kn7pH0r0r6DT/x2t7PnKue7SPxWLUJH63oSP4nf
VorfeH69wbnqA45tl/qtrfppwsv6dDMeLZU70udK/aR+W6l+TBmsxM+EgWlRWlvxO/jUr64G
1KEOaz9BRuIn8ZP4KfNbW/HbXeZ3+TG/pEXuay9eR8rodotL/CR+Ej+J34aL3yoH/ZT57VZc
Wo+T+En8JH4SP4mf1vltXSYo8ZP4SfwkfhI/iZ/ET4vctchdi9wT9jrGIeG5LPI3HfY1dtb1
PvVa5L5di9zH/lJtbL2RwqjMT5mfMj9lfmub+e1utqcmvLQ+/nY06ifxk/hJ/CR+ayt+u5vt
qQkvR0NcWv9MiZ/ET+In8VuR+LV6qoMyv9aF6GjUT+In8ZP4SfxWJH4Hv7/Z7jI/id/REJfW
P1PiJ/GT+En8ViR+B5/57W7MT92erQvR0aifxE/iJ/GT+K2t+O0u85P4HQ1xaf0zJX4SP4mf
xE/ip3V+G7mc4YoEWOIn8ZP4SfxWJH6tjvmtMvNjrhm7pI2t114sJX4SP4mfxE/ip8xv7cXs
irK8w/2bxE/iJ/GT+K1I/Fqd8LLn2Z5jyqgdXjZSGCV+Ej+Jn8RvbcVPE150mO3hsrrdYBI/
iZ/ET+K3IvHbhjE/HWm0G2FZhxiJn8RP4ifxW5H4HXy3pzI/ZX57FVqJn8RP4ifxW1vx290i
9z2P+Y0FNeanMb/jKZXDkKx1ON0l9hwNJhRztt4F2+e+nAEDKA8xe2NyNqQPgryNfRx61w/B
k7CEeptz8INN0eQKReNTjIP3X43qjRtyjNlk48cgHC2TY0DRwZj6eX3MqEVALYytUHB+iM7x
2kOtQ4DvAmL6oX7e4ILET+In8Vtb8VPmp8xPmZ/E73jru2AHj1aAiS6b0jbx3eCyjz5Gg4MK
S7PDdxHn0uWht9a4sdnhuxR9Tt7C7w07r8Y2RGlIXPYDJaMJg7dhmJo1vuutw4eiQZJdKCV9
Z2JILtmIlkisLSS0VmJvehut9bUt0g9omxgfTMi+tmssztBDqyb0LvrysbbLlg0d4w2Kc0jJ
2m5Ay8qagLaWGds1tuu9TQnfOjjbly9pO2dSCPji3oRUrmW6nKOJaFvFMN4J00W0jEKS+G2d
+LH1G7vswRec3ZjRvh7IGyzgSyGHRDrnsdUMCOc5ooEfcaojDnkco7TMb+2TQeZtU/4WbBoG
nWWrs2ylfTrL9viEFhKbKy5aH0NkeyWh1WG26yxbfm2JH27CXpOrlstJ/NTrqV5PJX5bl/il
3WV+TAwkfhI/3AFKpYb8eBuSQSdIT+EcSqOYUEKnnsOYZkYH3Hiz0H+Xgvd9j4HNqUMQQ5zo
eLMuuVzGHX2HXsPggDqDMBb0nUP3I3sDY6qjmr5Dt19GD41jP00t2JvsMMpqUYtc+zPV66le
z5wwIh/6UDq0c4cBbrAGPdAh5tIjnLqMXmXbG+/RIzzw+Z5WJH4Hv9KBvE+dSdmgz6oPCbMR
xi+EbxdiwswE/LnkMYHLCXMCevxJobNf4reZ2dycTFOZnzI/ZX7K/NZW/PY632V3id9hej35
gcgFNeS39j2h0j5pn7RP2rd12rfLxO8w4qf5LnOSq5ZjJX4SP4mfxG/DxW/PvZ4SP+S5LQvY
11M3iZ/ET+In8ZP4aaXDxorckQRS4ifxk/hJ/FYkfpzUlTosv3RDwOLMZLE6boSwwwUWXHrs
gzFkLulM2OECU3Iw0Sv3WHPJDCthswxsQMG5X1hpGsbBPCw7xY4XZTkqlqmWKCwdxTUydrUw
sUKa73KkB7zwI2euEj+Jn8RP4rci8Tv4yZ57ne+iMb8ji8K2CKbET+In8ZP4rUj8Ws38xtV6
e1jpcJgxP8323BRxlPhJ/CR+Er8ViV+rmZ8mvGyKYK3ye0j8JH4SP4nfhovfKjM/LXVYpQAd
zWtJ/CR+Ej+J34rEbxu6PSV+R1OwVvnZEj+Jn8RP4rfh4qduz1WKxqZcS+In8ZP4Sfw2XPxW
2e2pCS8SPx1lq32ti2zqNL+yZbnpsMu4w6GC2Q62nLqccVgcjjXssYX5gPOZueAt4/hAHEOI
jc+z78cDC3M3BDOk3rvBJJwiV6KCjYPDbujBIJpHEebO4wBD7EIdow9p4AM4Y1mc6XEEIw9s
xhHNBbI4wFD7Wpetrpf3tZb4bYpgrfJ7KPNT5qfMT5nf2mZ++3yow2GWOmjMb5UCdDSvJfGT
+En8JH4rEr+DX+qwO/FbZeYn8TuagrXKz5b4SfwkfhK/tRU/7fCinVr2KogSP4mfxE/iJ/HT
xtba2BrHIQdfBueLLkacAp0x+j4Y9n4T0kHuOsjdBhwdPzLCd5rwogkvAVNvBufswXd77i7z
01KHvWZHm1xOmZ8yP2V+yvyU+SnzU+anzC85673DvHLnOU6O5gFOY0G+i2NTPNq3I5Rw0oqW
OhTZVOanzE+Z3/Gxi0MfBu9xaJNJlpzY5KxpE76bMj9lfsr8lPmtKPPjI3+jzvPTUocNFnGJ
n8RP4ifxW5H4tTrmp6UOm5Cprfo7SPwkfhI/iZ/ET2N+W9dNK/GT+En8JH4bLn6a7bnqrGkT
rifxk/hJ/CR+Gy5+6vbcBLFa9XeQ+En8JH4SP4mfuj3V7amlDlrqUKbu8ywBe8gP38WIkwW8
Frl3LvS5t9kPOLhBSx2O3lIH7e2pJRV7zQiV+SnzU+anzG9FmZ+WOmid3/qIscRP4ifxk/it
SPwOfqnD7jI/TXjZa3a0yeUkfhI/iZ/Eb23F7+D39uQnxi4ZnFwch+BcToHnFGuHl7UbM5T4
SfwkfhK/DRe/Vc72lPhtSjYo8ZP4SfwkfhI/zfZcu8zt6xVhiZ/ET+In8VuR+GnCiya8aMJL
HiLOQDDTqW+u8zb22Pbc9UPwHKSG6npMFc/BDzZFw15zQtH4FCP2Rv9qVG/ckGPMJhs/BvU+
5RhQdDCmzMV3XR+zizlY78w4Pd91wfkhOsdrD/UohgDfBcT0Q/28wQWJn8Rvq8WPfxxpReJ3
8BNedjfmt8puTz69NOb39WZdLZRX5ifxk/httfhRGCR+aGAPVdYwgSUkNLDxX2k2Q+l6h8Y8
DjEbXEwa82tBuFZRB4mfxE/iJ/FT5rdr8VPmtwrhaeEaEj+Jn8RP4rfh4rfKdX7K/FoQrlXU
QeIn8ZP4SfzWVvyYh6XOpGywMWMfknV+7Mc1mDcQU+qj7dF9WcbpcsKkgD4ZYxwKjJB3OHk9
2nyEbs9xsFDdnhs5E1TiJ/GT+En81lb8djfhZc/iNxaU+En8OB/TDUOyaF6hSdWzWUQIY8Fo
UgU0sfo6+9JptifvTA4hBe/7HnNay+7HvjOY3RpjtC65XKac+s46GxxQZxDGW+o7Z+GYkCOa
qeWW+s6bmNFIdWyq1oK9yQ633NoBv4CxYLDYaTkHE1025dfju8FlHz12pMaO3TUq9qnPAwqi
CVyvlaLPyeNjc29KVQ/Z07rWQhtb82lrjTa2DpmTr1MXIv7wp42tD36pwz5nfocRP36iZnuu
otvxaF9DmZ8yP2V+yvw2PPMbey/30O15GPHTmN/RFq1Vfb7ET+In8ZP4bbj4jRq2GvFT5rcq
8Tna15H4SfwkfhK/DRe/y2d+u5vvosQPfbxHW6P26/OlfdI+aZ+0b0Xad/BDfrub73J57dvl
ZM/DiJ8Sv/0So4O+rsRP4ifxk/itSPy0u5m29lyfTFHiJ/GT+En8JH673uBF810OOkPbr8+T
+En8JH4Svw0XP8132S8BWefrSvwkfhI/iZ/Eb9eZn8b81lnwlusu8ZP4Sfwkfhsufnue8DIW
/JoNXiR+ywKyzu8lfhI/iZ/Eb+vEb88rHaR966x3y3WX9kn7pH3Svq3TPq10WJ9JmcuCtcr3
Ej+Jn8RP4ifx05Dfxq5lP5JgSvwkfhI/iZ/ET+In8cOZWAGnAnDjepzWEGI/DNnGYTCcLExI
ZzrwNiSTo+spnEOsdyYl01vnetyvxLW+iNKZDn3kjAHciogDKnrcoGjteHCF63BAhUvG8+wK
z/MBEGWTzRl3rXfRl1MkbAf2hZwNjrToTbmtthsGHG9hAo4QMUO5+bbrPW46TrIIOPGCgzLW
djixLQQcZuFNSOVapss5GhyoMeAYghJkupiHAedumD5mVy5lOlA9JBzwFlGXWq53A07Z6HGQ
CWY+8Oo60yEc9kyHbVjjrmV+R8qk1g3HA8fVxxNOJEoQOYmfsx6nBuG8y3IoJh/cvYfk4/RL
b/pJ6SR+Y3PId1B8nKLkU85oK1EZcGpTDMklG42V+EEukxtSLA3KDLWFakOos+9Hfc/dEMyQ
eu8Gk5KnfOQuoL3pcAxWMIimAufOQ+9NGGL0kGY+gDNOEjM9TqGKaEO48lecOwu9zwnnjYU+
lLOqcgfO4hgs/C7wL6VhkLqMxoXtcdgrGgYD//zThmd+/KuNnba11jjfskBL/NTtWfRKp/kp
83PIsdGRERy1NaHNx2QdMuljKN0bCTm3cT1UMyKpPtxpftuQ+Wm257KArPN7iZ/ET+Knbs8N
z/zG1XrLmZ9WOmzdEN+hOi3tk/ZJ+6R9G659e+71HEXza5a4a8jvUBFZV1/iJ/GT+En81lb8
2AeZOgzHG0xW6EOy40A9IO9DTKnH2CZmUGnID3dgXUVqv+ot8ZP4SfwkfisSP53mpwON1kdk
JX4SP4mfxG9F4nfw812U+a2P2OxXBrfX60r8JH4SP4nfhovfnsf8xoJfM+anyZ57FZvWykn8
JH4SP4nfhovfKsf8NOGlNRHba30kfhI/iZ/ET+K3693NJH57FZvWykn8JH5bKX5l9xPsUqbt
zbTDS4+97PKwa/VTv2drKrbX+kj9pH5bqX58hEn8tmV7s1X2e0r89io2rZWT+En8JH7q91zb
fs9xJ7YrW+i35xkvh1nlLvFrTcT2Wh+Jn8RP4ifx23DxU+a3V4HY5HISP4mfxE/iJ/HTmN/W
bQEj8ZP4SfwkfhI/iZ/ET+f5JZ3nx8kg5RzXQ374LkacAOdtGHC+LAdScHifzvMrpxiazmTn
cKZutoM1PJw3dxmHAek8P+6+iVOMe5wr7IPFYc+8OanzPY4cDG7IPY4WJpcSDigMHucRDzhr
MIZxNM/h4EwQzuDVpBHCIZG4RsbxwyZWaN/G/LTKHb+YTe36VOanzE+ZnzI/ZX7K/DZW5I4k
3hI/iZ/ET+K34eK359meyvyU+eEEZ9KAUjkMyeLgEBwW0nMOFaGYs0V3BQ4P6Us/GSCcCJ29
MVPnmOs8+j3i0Lt+CL6ssQLUW5w24geb4rjmGFA0PkX0c/ivRuEsaSxAjRndHuwuwef1PmWc
OZ3DYEz9vB59IDEH1MKM/XWuC84P0Tlee6h1D/AdOlYMul7GSw0uSPwkfhK/FYlfq8c6SPyO
lP1sM67MT+In8ZP4rUj8Dv5Yh92t87v8Uged5L51vZyH6ry0T9on7ZP2ra32sRNpHw+z1Rp3
3N9DRWNTfImfxE/iJ/FbW/HbXeK3515PiZ/ET0N+Q8Jsao/BwnGsMGECtuspnEOcoGQw6R9j
mtkm9v6gXZFDSMFzSjeGHwn5zmCIM8ZoXXK5jDv6zjrL2d3RGYSNUc7CMSHHVEc1fedNzJgm
7rzD0OoY1WNuPUZZMU8cY64jFOzgMfZposumjMj6bnCYcO+xRAFLOGpU7FOfBxTkBPKxYIo+
J4+PzZhlTuiQRQ7F1UoHrFvgzTGdCxjgttnjdgetdAgRfxnO2VaH/C7f65nU7bmxGd1uM1Nl
fsr8iihL/FxpeJgOU7tCwj7/MdlcJN90vRvQHME8KzQaJH698TGFUFfrhYiJbpP4rc+Q397F
jwSIXTJY0xmH4FxOYRRSTOfDEliPFqpJpRmw24ew4o5O16rET+In8VO359p2e+7zmB8bRFA6
tH4woz2iDYQmkcQPd2ATBFviJ/GT+En8ViR+B9/tuTvxGzUsJyyF6jGSgN7+vWd+Er9NED5+
B4mfxE/iJ/FbW/Hb3YQXjfltimCt8ntI/CR+Ej+J34rEbxvG/JT5rVKAjua1JH4SP4mfxG9F
4nfw3Z7K/DZj/O1oiKDET+In8ZP4ra347fOYn9b5bcjklsOJq8RP4ifxk/itSPzU7amlDuuT
iUr8JH4SP4nf2orf7jK/PU94UeanzE87vGiHl6KROstWi9y3fJG7JrwcrgtxHTFlfsr8lPkp
81Pmd/izbJX5KfNT5qfMT5mftjfDc8D1V5D5bcNsT21vto5Z3uHqrMxPmZ8yP2V+a5v57W6p
g3Z4OdzDf9sxiZ/ET+In8dtw8dvzhBft7aluT3V7qttT3Z7q9ryybs9Wlzoo89v2LO9w31+Z
nzI/ZX7K/DY885P4He7hv+2YxE/iJ/GT+K1I/Fqd8LJn8dNsT3V7qttT3Z7q9lS357p2e2rM
b9uzvMN9f2V+yvyU+SnzW1HmpzE/bW+m7c0yTj72xuRs2OMAifU29nHoXT8Ezz0SCPU25+AH
m6LJFYrGpxgH778a1Rs35BizycaPQb1POQYUHYzpKxSzizngrEpjKxScH6JzvPZQ6xDgu4CY
fqifN7gg8ZP4Sfw2XPyU+R0u89l2TJmfxE/iJ/HbcPHTmN+2C93hvr/ET+In8ZP4rUj8Wp3w
oszvcA//bcckfhI/iZ/Eb0XipzE/jflpzE9jfhzVzCGk4H3fY2STjWLrO4MxzhijdcnlMvDo
O+tscECdQdgY5SwcE3JMdVjTd97EbPvBeWf7WrA32eW+t3bIuYyj+i7YwWPw00SXDZu7+MTB
ZR89jmNIztao2Kc+Dyho3Dja6rsUfU4eH5t7U6pahk4P+eE7neqgUx2uYG/PVsVvlZmf9vbc
lIxRmZ8yP2V+yvzWNvNjcy51JmVjbOpDss5T6QBh0lxMqY9oK+Y9j/mNBVPvMIEvRze4mCR+
Er8+9iW1cB3mWWbMswxgWV+nWjplfsr8bMTU21hJgum5sTe9jdaO6a3rkMa6ZDwzXF8n8tqE
CcDIl3sXfaGS7bLlzF6DxLc3TCys7QY8iawJoJsZJ/Larvc2JeS7AXlxSW9t50wKASmvNyGV
a5kOzy+DtHuIYcyBTRcxFRjZuekxXbhk3aYbDJAh2oi61HJ49iEXxyxjZMzK/K4g82t1zG+V
4kd6xS4Z53wcgnM5BfbExA6T2QPmqaN7xiTLO7EpIrGp30OZnzI/ZX4Svw3P/FbZ7Snx2xQx
lPhJ/CR+Ej+J3+EPsz1Mt6fET+Knbk/XUziHWLrLXIdut946rOLP6IFj/5wmvKjbM6LLFXOb
BuzcwL6xjH5W9NeCINn3Y89u7oZghtR7h96y5MmcjHlLcXCYJhUMotn3mjuPnl4Thhg9OmXZ
95ox3mB6zFLiVg7YvKFAFj29OTmfQh/KXKbcYUsHTJNCFzT+pXQJpy6jW9mi99KjS3hgwbS2
4sc7ceVjfsr8NkWwVvk9lPkp81Pmp8xvw8VvlWN+mvCySgE6mteS+En8JH4SP4mfuj23boKO
xE/iJ/GT+K1I/NZntuc4QTNz1Sxm9mZsHzzUwTxM3gzofsas43FTYMzsXF7poCG/o5msrfKz
pX3SPmmftG9F2tfqGvdV9npK/FYpQEfzWhI/iZ/ET+K3tuJHKdJ8Fy0p3IuISvwkfhI/id/a
ip8me0r49iJ8LCPxk/hJ/CR+Gy5+6vbcq0BscjmJn8RP4ifxW1vxU7enMr+9CrTET+In8ZP4
ra347XO357g4XrM9N3IVhMRP4ifxk/itrfjtLvNTt+des6NNLifxk/hJ/CR+KxK/9Vnml7TO
byOzuTliLfGT+En8JH4rEr9W1/lpa885orAtsRI/iZ/ET+In8dv1Di/a2nNTxFHiJ/GT+En8
1lb8djfmp8xvUwRrld9D4ifxk/hJ/CR+u878KLc6yH2VInS0riXxk/htpfiVs+6swfF6wxCS
1E/qJ/XbuhkwUj+p31aqHxvwEr9tOcxWax2OVnrV8udK/CR+Ej9lfmub+e11lbuWOmxdoneo
Dkv7pH3Svq3WPiZFaeu0b+/r/DTb81ARWVdf4ifxk/httfhxJuSmi98qez0lfusqdofWW+In
8ZP4Sfw2PPNbpfhptuehIrKuvsRP4ifxk/htuPhpnd+6CtR+1lviJ/GT+En8JH5a6bB1E2Ak
fhI/id9Wi58mvAzR5mHX4qcxv/3Mxg7y2hI/iZ/Eb6vFbzsnvGilw9YleofqqrRP2iftk/Zt
Xa+ntE/a5zrHhl/RQJuGwdgUfCQzChT7Ycg2AmffCKFhSNY6n/rYTwVjzta7YPvc9zUqDzF7
Y3Keynkb+zj0rh+CL1truM73NufgB5viuNUUoGh8inHw/qtRvXHokIjZZOPHi/c+5RhQdDCm
fl4fs4s5oBbGVig4P0TneO2h1j3AdwEx/VC/4OCCtE/aJ+1bkfa1epqfprscmvTIrwo3KZ3E
D+o+JGe9d9YY56u6x95D8k2CnPdVR5PJ0fUUziFOUDK9dVD3bBNPNcO1csCmkd73PSSezwXr
OwOxjzFal1wuCuw762xwQJ1B2BjlLBwTckxV333nTcy2Hxyq1teCvckO7Q2LWuTSoPBdsAOa
LsFEl02pve8Gl330MRp8sRoV+9TnAQWNG5sdvkvR5+Txsbk3paqlDXHID9/hMmHwNuATx2aN
7/Cl8aFokGQXpi8ZQ3LJRrRE4nQP8WV63KBo7fglXYcv45Lx/J6+tmtsQnsId6130ZfPth2a
XmjoGHz93pTbarsBLStrAtpaZmzX2K73uOn41gF3p3xJ2zmTQsAXx/5dqVzLdDlHg5s/xDDe
CW3sid8mf0GbvsqP3zF2OaF13ONPCrTXEvdrKfNT5gfpCExA6/NX4ifxCwkzICKEuIpm7wY0
R9DjgEYDZztgR1BH7bUZtImj5JsOTREHDc52sKWTIndodUB40c4Z0J3BFkvGNtpQbQh19v2o
77kbghlS791gUvLU94w2TBwcmkzBIJqVyJ2H3kOqYvSoHSuROxdNjxYL+zfQo1EgC73PCR0z
oQ+lXZM7NNjQZEJDBP9SGgapy2hc2N54vy0be0r8lOldXuxL3yb+bMqrMj9lfsr80MMv8WMy
GHsm65BJ6ju7JBJybuN6qGZEUp3ZWkxdQBrdB8gw8nh78Oe4M81PHRI5gwGbPiSMyIypLKQ9
xITRGXSUZNZ+T5nfqJpowKCzAX09g0OTqFwrGbR04hCcyymwXRM7jOqgV8Sje8ag1wOQBKft
eyDx05hf6Y5Vt6crXc6mk/g5JpYSP3TAl151HN0n8dtEIZf4SfwkfprwsqIJLwef+Y06fWWZ
3567PZX5bXAGK/GT+En8JH5bJ35jT2Xm9LF5K9zV67kpSaC0T9on7ZP2bZ327X2yp8RP4qdl
flrpUGRTKx3K+g5N9jwq8132uddznCijIb+NnLujzE+ZnzI/ZX7K/Ha9sacyP2V+yvyU+Snz
0zK/o7zSQZlf26sJWhZKZX7K/JT5KfNbUebHDuDUYfW/GyCK2FAFq+NGCJsbYq8djyWBQ10f
yH2PDHY2yj222xlXEbqIvQe52RE2GQqjrGHHIWx2WHYiwg5F5VrYNQjXyNjQ0MQK7dtkT3V7
arKntvbU7mZFI7W7GR/A2uClmTXuu8v8Rg1bze5m6vZsOZubUzdlfsr8lPkp81tR5rdxy/yU
+SnzU+anzE+Zn7b2bG93M2V+GvObk+0txyrzU+anzE+Z34Znfnvu9jzMBi+UW2x4pq091375
g8RP4ifxk/htuPjteXczdXuq21Pdnur2VLenuj3b6/bk9JN9PNRB4ifxk/hJ/CR+Er/2xG93
Y37K/JbHuvR+HCdVt6e6PdXtqW7Pte323F3mt0rx05jfpoinxE/iJ/GT+O1F/HjA/JqcZSvx
2xTBWuX3kPhJ/LZS/Ax3HsFi9YjzSkOS+u1F/Zo4yX13/Z57nu6pQT8N+mnQT4N+RSS1xQuf
ttriZc22eFll6qctXlaZfh3Nayn1U+q3lakfH2HK/LwJA4UhbXjmt2fxGwvqTKO1X9R3OJGV
+En8JH7q9pT46UyjjRS4w4nehEn8JH4SP4nfhoufxvymB75eL9sPTuIn8ZP4Sfw2XPz23O2p
CS+a8KIJL5rwUjRSE1404aU3Pq7ZhBdlfsr4Lsv4pnuhzE+ZnzI/ZX7K/DTmpzE/Y1Pw5fzl
oouxH4ZsozI/ZX7K/LS/2brub6bMb8p29HpZBqjMT5mfMj9lfivK/GJZNtHn3g0hBhydPpR2
dOp6G3sfvQ+2H/K4Ot73fTDBDbkP1lKdUudi8A6Q7U0M4/J1Z5CSeWvwatII2T7iGjlmZ2KF
TMoGzfY+JOv8uHbD4MNiSn20fc4a85PoXSZ6072Q+En8JH4SvxWJ3/oc5c4dfmKXvYMaR5sH
9Xqq11O9nslZjz8JY8YmJFoHaLMO6vVUr6d6Pdvr9dznja21xl2TPTXkJ/GT+En8rkz8Wu31
3POQn8RP4ifxk/hJ/CR+6yp+GvKbhrn0etnQn4b8NOSnIT8N+W34kN+eM7+x4Nds7clJN7FL
xjkfh+BcTmEcP4xDHwbvMYZokmUOLKFp+x5I/CR+Ej+J39qK3z6P+R1G/HSow6aIusRP4ifx
k/itSPwOfsxvd+K3ysxP4ifx62PPnnSqZ8zZYnkO1tP0PN2ZUMb6Hm9Mzoa8A+Kxzgf9Aq4f
gid9CPUWC3D8YFMcjxYFFI1PEet6/FejeoOVQDFmLPPh8iCU633KWEOUw2BM/bwea35iDqiF
sRUKzg/ROV57qHUI8B0WEhksNRovNbgg8cNN9V2KPidvsZoKS6x4c8ptPOSH77S7mXY3u4Ld
zQ5e/MaVf1rmtymCdJDfg0IVTlzgvws/eRW+LC68C39eeuh/X7mU//ZJ2jWX/p2x/O8Y2HKR
8ToXfvLSUq6EXO7HNWqZ6R++/dZ8x88fjdekTX55u6sfD1zgc6/+4MX5i7MWT1w8FT/PIUK7
9rmLMxaPWzwG6BmLp+BfHrMwi7CIi7xwC8+I46eIQ/DpCnw9dgexhu+udx6ucSaucrhSHT73
cagF4r7pboudxSmHfFq3eNLi6Yuz+e/XPxVXeBqin7l4MkrYI0cy+lC7wQ4+6RxciXVhTZ65
eOziCYvzgJyz+I9Ln4Cf/LZPx7+j9FUn77zpOsdesLhgcSK9q9TXqz8LJc7F3XsarlXirt3j
Dp2IO9Xjp8W3N0uvYbpSK6/Hnoe7+NXf+spqdUy50rUXxx2Gh8ccBluGpn+/4TKI95/jX9zF
H/++65/8tf9Q8MXCvLzin2fcUf3vtvj0682owVsRuwN7A+yqpdzJJ7+0vI5PEvxlf/J8+Idh
9BVi5RL1B8te2X/XubKAI/z7Va/Gf5h+bw9birpPeX/Zs2r5GdUtxZW3NzkUgH8M/htvCZxj
/y917x0lVdVu6wMKkkREUQRBRBqQnENX7SpyziiShAbJOYcmSJCcc5ScVJAgoNhVXYiYFRBz
xpzTpyhG7vusmuvcOr80fv/cMe5lnKfnfGe9e+211w50t5xvz8xROhdHnH+83XUj/y/3fkPr
8GPyzPR/rsqRK0fumTkLJa/JhhZX00epXTn/64z9/71+/tf0Xe/mNmp0jhwnzY20RX24RJvg
zQkVgut6TY89+ly74Kpi+8Irq06NXRdtGuT9Kz2YPXhW7LZ3iwU5Hi4YfDZ8RWz7tm/Co6fd
E3rvk42xVos/CXeueSpc/5VNsXtbbgv3rd8pvLvijli+cpPDL8+aGDq6eVesTt254TI/fR6a
nHdX7Off2gdzqrVOb1YnM7bkRPtgSs4bYtWGZsaWftAuyO6yPbbh1ql+X3H29YHN7e0JFeJf
9Jzu5xNnPtpvLGW/MfarfWWxL80hizl0u290OEeOi2Xzv7Ur9mUklPXquNfTc7+c9DkanI/V
Sd8Yezf8WOxys3bxMQvHxxo0vCV+6y3XxvO0XxHrU6VCfNyZ1vF6qycyh7itiZvDi5/Vjxe9
pVn8p5umxib2XRUecKhdvGSt8bHHhtQNSi1rHq//85RY7yoVgn62bVPbturgS6EiY9rHa64Z
F1tRJ1/W0U3t45fHjIut+uvT2NbPnordsntT7M3N22MdInfHChbeEbv+67mxgT2/y3r+752x
Tw5Mjh3/bEbWxvXuWGKz1l6VxrEoD5GrP0S/xgkzDsfLOavYc53fV5h96RgDjnHT3ytjqw+3
C9JqjvfH6M67zT/e5UzroKPNf9rauvEOE5sHf12VGXs4/y9Z345pH8xaPS5WYsh1oX6b2gfh
seNiXfofCxdv3C7YvGQ86xZMtG1r27bPvlE/WF6mWTDzuqkxu97idr3Fdb3F7XqLcb3Z9RC3
6yHM9cA54Rr74qktsfes366B4Eu7Buz6idv18yTXj10zcbtmwlwzf/3UNj796L5wjyLDYv8+
2Sb+xrG94cNdusRyzm0dr/r4nnDutaHYwD/axvduPnMH+QNPtXGe/MavW8fHNv8wRn7PsVbx
4Nf3Y+T3/9vSxikXJz/wcgsbJy1O/u2oJvEpe+q6fEnzxvGVy+u4nIzP6CfjM/oZg7HIGYOx
yNkn+yZnn+ybfFSRq3YxV3I8c1V/OKU/7Ptt/CBl/MCPb/MJUuYT+PlYFqTMP/DztzGClOMN
/PHaPoOU9Qn8+tgcg9j41buZp80x6Nbg2G7mqX63/jZH+t36a/yAfpsj4wf0az4utzkyH5dr
/i4n4zP6dbwuZwzGSlkfl7NP9k1ua1iWubLf/G/dUZa5qt/NlVzr78fnfPnxOV8u1/l1uc6v
y1lj5so4rLGf/yebmseXnSwb2D5j7x5oHL/l0xrOt6zR3l17XKsXSraN79vwUQzfpXpru4bL
x/GtNzaN982q5zxKTc7n9OHZju3xXCeMqzzsc+sPfL+NE/hxTAM/vn0e+P3adoGfj43nzi9j
Knf3l/oDco3jvMZ3Xvt13sZjPs5z/zGu5unGxeu4XK7jdZ75Mi49bRukx5dvCrs1/PqRavHT
Lzdx3tY4/sum5s6/M2tb7Ic+rZyvPKlTepGFrZ2/tOHh8PhQMp9v5ySs/rc+qhE89mhj1/Ph
8nBwtmm68/nPNwnO7a7m/D/Wu1zn8XK4ZZB+7Nsw57TwtFbBvDrrnf9gQevgoaq9niT/qm+r
4O3B27jWYscbtAwqzf3O+erLWwTT3swXJ69Yt0Xw3skbnP9P3hbBwaPFnK/+n+bB79VLOP/H
O82Dz94t6fzXNgeOk21PTmscXK5f0/klDdODN1aHne/6ZbXg9OEmznPdfWzXH/0Tbvs6/GaL
ls4/OG5leNGyVs6nF74+6057PtJTNDgc61w+mdv6xJto20GxGvFCpxu7nqeHhONLR6Q7f/mJ
JvFCb1Zz/vvkde78dz1axhcs/swd7z97W8U/n7PQ+SlTW8fzfDM7xL4W/NUyPvmfrDD+6z/m
xcYWmv9fvt/RBa7/3fD88MCP5v+X9z1888L3gfyMDPirBJ6fB6hRvq0DPN9AAv4aeZTv0Ngu
n8FngM8vjxaQR/mZG/DXyqOF5K8z9ePg+Y6XGmV/gOe7MDzKd/Jwg+F78DcKPJ9To2yDR4sK
PONSo+wbmKvvwd+kGuXnH8AXk0dvEfjiBp+zbQmB53ip0VsF3177nlLm2Q7wtxnsq7Th54O/
XTVaRh71x46/QzVaVqQpow9fTjVaXh6tIPD8WoMarSiPVhL4yvJoFYHn+376qhl+THx11WgN
edRfk/iaqtFagmvX93CN+jHxXKfUqF8HfF7VKNdJbaOO4c8X3p9TfF3VaGmBryePsu6AZ60B
z1oD3q85nrUGPGsNeNYX8Kwv4NkfHmV9AV9fHmV9mW8Dg88g3eAzNCRPjbdv5N1naCDwEXmU
H9EB31AebSTwjeXRJgLfVB5tJvDN5dEWAt9SHm0l8K3l0TYC31YebSfw7eXRDgLfUR7tJPCd
5dEuAn+XPHq3wHeVR+8R+G7yaHeB7yGP9hT4XvLovQLfWx7tI/AZ8mhfge8nj94n8P3l0QEC
P1AeHSTwg+XRIQI/VB4dJvDD5dERAj9SHh0l8KPl0TECP1YeHWdwrXLtco0Cfrw8yjUKeK5L
PueapwY89wEenSDwteXRiQI/SR7l2gU81yuf36KaDF9cNTpZ4IvJo1MEPlMe5ZoGPNcxn9+k
mgxPDvipAs/znxotJY9y3QO+hDzKdQ/4afLodIHn7xtq9FaDXrzvI5sh8IXk0fsFnr+/qdGZ
Aj9LHu0q8N0MPi9gUAM+vzw6W+DzyaM55dE5As8fav48IPBz5dHeAp9h8CeXQQ14/n7Bo/ME
vqY8Ol/gF8ij3GOA577ic/7+ogY8OeAXCnx1eZS/F/kMHSzwleTRoQK/SB5dLPBV5NGqBr14
30e2ROAry6NLBb6+PMp9C/ixBvftMmOMwHPvo8vlqfEjpCvkqfHDpCvlqfFDpKvkqfGrVaP+
OYZfoxodIPBr5VH/nMSvU432Ffj18mgfgd8gj26UR+8V+E3yaE+B3yyPbpFHuwv8g/LoVnn0
HoHfJo9uFzuU0YffqRrdJXYrowd/t3SPPDW+i3SvPDW+k3SfPDV+v2q0g8A/JI+2E/iH5dFH
5NE2An9AHm0l8Afl0RYC/6g82kzgD8mjTQT+sDx6RB5tJPBH5dGowD8mjwYCf0we5d4A/Fhj
tDHSWCrwS5QNl6fGL5YOlef+53mx0Mgw5hrzDJ4z/Yz5Ak+OZsjzvOtlPCDwc4xuxixjtkHW
wyAHPDlKH55n913GTIG/30A7y1PjZ0g7ylPjp0vby7c1bW1MNZoak4zJRkujuTFF4MlR+vAR
Y7wxwWhsNDQmCjw5Sh/+mHHc4FwAfoU8Ok7glwn8coNtOb9sA/gT8ujjAs81TY1yrdN71OAz
wHNt4dHDBtfjo/LUeK5pPHpAHvXj4LlPqFG/P+47Px88zxFqlOcL9yvPDT4D/FZ5lL69xi6D
XsDvlEd5vtDDs4LPAL/b4LPtht8Wzz7YN889Pzf8E6pRv7b4VarRlQa9PD/5DPA8Z/HoBnl0
jcCvl0fXibXK6FttMAbg/f4478znNSP1z+lnWnA55ci+cWrilwM1IzlWVsoaXGRaoumoipEX
J1SKhYdOS9yW4yrXM+vz6YmyB84HF5ZWynrs4RmJPpWeDF6vWSlW5PsZiW8mpEWeXFEpa83O
aYkpU9NcP/7XNRUj53fkCDPOLUdtfPvD+P98Vi8ycskjod1vTE0U/yNXZO3ySlmM/0z8fEAP
46/slBXsX1IpxPgVD213+R917k/c8J+5zh8ad3+C3uQf/oul/zMzkVVyaWzl2lrx6OP3J77d
WCpr/ebtcbYtel/fBrXz/xbvljYj8fnZH7PuKVQs++Hy0xNf5vk39FjrtGzmfLZMhQaDn6mY
zZwLvloqPHlYzWzmPPPrm0PPpgfZJdZPTfxV6PasR08le/5pvTer6pGkH5FZPeud6Y2zz3Wd
mmjQrEzWrqdaZLO2H2+5Mevzq9plf3s+M3FmSsmsY/9ccnPYULZDg7yHknNrs3tO+Ok+ddyc
b7j+kXC5Xys7//bq3uFCp+oHHMusx58KP3RmSsCx9/nySGh52+1BynEFHJeOJcKxvPnS4dDi
RytGOJab9pcL9Z/ROMLcHjq5I9S+ShDhWLKKpYW6TExz/RvynHtikp0/ttVxuW21Js5/3eba
WO3MmhHW5PUv+sVevT3pR+9uEHrp8iU3h4l/787K6JGc295XxseaDprt5vzEq19nnXgi4o7l
2DMtsn86s6aBW599NbP7ZI0JMWZwpGb2qB5L0vHnZxXJfnJDrfBL3acn1hUvln3PsLMhztfI
/lnxA99dk8610aTZ9viAXk+EWIc3VmyPnx3azPndj26PDy977iS5erJSepxf3S0r3m1NPneN
3XNb6ewb9q7OSntnWqLI0puzv1o5KMa+2h2umX3phRfdfDLeqpf9Y98Ps7huf8rTLnvZvnrp
nNOGRtW0q4PDA1tHqs/PTJwtVjCYsq9D5Ms9mYkRpWaHU3zM+UGZic8a5I53btE58seZoYkb
1+/KLtl4fKTZ+1UTozdUTTQ9Nzcy6ZXd2Y8uG5og33P2hvgTfTIT9J8vuT22YkdmgnFalFoS
XrY76Uv9nCsoMSTZM+XJnZHW3ya3XT+varToD8kxL2wfGs07cLfb17L+mdHf+hRwc7h1V2b0
hlLr3Nxu3psZXX1gpptzm6GZ0bv25wjY793vDI3mK7Mrwnw+vVI1Gh9fNco8V/27K/Ld0aFR
8iP7rw2a35cZpX/X8h3hu3ZkRpnnqAOLYqd3J329m/PFXx2Q7FmxcFf2Xc8lt/24X9XEoeur
uTE7LBma+P3d3W5fq4+MSzz/1cpIZuEvgivdMxOfPrc3/MoXd0X+XTgxUX355PD7hxZGni4y
NfHz4L9DPM8uFMtMXL40JLarbI9I7soTE6ENs2P9mi6J1F83NdGl7ZXYL5vTI78syUxU75sz
ztwu/DU88XXoWPbb26+NLDpXIVHmqcqJ2/Y8FPnpkyqJd2dXSXS6fUVk3rx92ZdeH5b4eu49
kTJLCsfPvDg1cezuOpEcFy/Faq5Irv/hP9bEzp+cnBi+b0yk3e+rYvdeN8mdx4aVZoee+CXZ
f2TlnNDZg8n+b+ovCW8pOjmx5bppkec//jj8xZpkvjkjT9B5UdKHv18duW7uCDfmMz9/H/7t
52mJUp8VjxSe/GDkwa/6JqaHTkRuGJEWLfhzxD13L35RMVqhQ6VEzpL7Io3eGx59/YvkcV13
aGo0X0aB+D+X60XeODwxWmP5I7HwgAWRFcH46KWS62IXS2yMHCoyNbrzYI4Ya/jNLZnRRyZ0
DbOGzStPjM6z64E1PLZ2arSfXQ+sYeelmdGu5lnDRsVGRIvvfSzCGn74dYVo/32Vo6xh8Vur
Rme0qhJlDV9quC/y/JPDoow55NvCwdIXp0ZZw5Odfg+/tTx5bfRvvD486eTkKGt4ounG8OBC
k9z1cEvfGVnZvyT7662ZmvXuwWT/yZWLYm8XnRxlDa8ZfTHWYG0yP70vd/z4oqS/+8XV2dMX
jXBjjjj/dez7/0yLsoa33fdgdoMD/aL5Jh+NhNuUSyxdH0SrFaoeiZ+pmKg2plKUNdyePTwx
fdpxd1yn5kcSeVfeFG2Wb2fk3cxaiRM/1oq2z/9bcOzbaxKlfmwRrdt3f+T2/vuyL347OvrV
icPBj80nZf/Zakz06dHDI9O+/juWc8WU6Ox/+0YW15seuzrPdDeHQWMisYnRzCjX1c3PLQpX
KDA1yvrf2GRX+PeXpkV7Vi8dual2/uDg61Oif5/uFVny8rLIynYj3bFU6L4vsvXuUVHWfMrU
m6LPb4i4ua28pXb03Y7JufV8tUU06+g17lxsyzsmOujmfZHWfR4JOk0fE/35tvER5vbNocxo
NzuPja9pFyneNjP67cVv3f31XP3p0U123l9cVzTSsWFm9NzKSmHmObPg1OiaAzPddXI2lx2H
PTdYTz0r3POk2sOZ0T/t2cKY6+dnRi+b5zoZOMv2dfNNztt33lH/N3av3nYtWc5zY9GTI6I5
16zK5ho4+9HI6JD8+7IZ/6u1kejds29OZNbbGumxvVa0xYu1Eqz/W1/njT44t4W75n/fsjcy
9d/RiXqFTgRXnp4cmVFjTIJjzPNMvqDII5kJ5jMv13vhgeOSz8mvd6wM39VheiLrxyKRxcPT
wvPmTUk8url/pEzelbFaL01NcL+MPbQ69sL65Pc1dX7KG6/455QE1/DDGUuzX5gz0t2bj57a
lz2416hEnj/yR0a9UDRxoWw0wXVS6ddaiX4Tk/Ps0qBFYvulvAmuk37vjU5MH7Qvm3luSx+T
qF13cjbz7D82M9FkzUcx1uGhmdMTNx2269vOb+z05ESdaO4Ya7Ks/LTE89PmhLlW1z47JXHu
2MHwzxl93PdWyfWcGc1pJpdxlXG1kdvII64xzSvymeY3ChgFjWuNQsZ1RmFxvWkRcYMp3GgU
NW4ybjaKGbcYxY0Sxq1GSaOUcZsobXq7Uca4w/BjMj6UNdKMckZ5o4Jxp1HRqGRUFlVMqxrV
jOpGDaOmUcuobdQxGK+uUc+obzQw0o2QERZ8E8micRE2NBoZjY0mBj+TNTOaixamLUUrU2gt
2phCW9HOFNqLDqbQUXQyhc6iiyncJe42ha7iHlPoJrqbQg/R0xR6iXtNobfoYwoZoq8p9BP3
mfY3BhgDDX98g8wPNoYYQ41hhj9GdLgxwhhpjDI4Xn+s6GhjjDHWGGeMNyYYE8UkU9ZgsjHF
yDSmGtOM6cYMI3UdWI/7jZnGLGO2Mcd4wJhrzDP8mqDzjQXGQmORwfr4tUEXG0uMpcYyY7mx
wlgpVplmGKuNNcZaY52x3thgbDRYO9hkbDa2GA8aW40MY5ux3dhh7DR2GbsN9r/H2GvsM/Yb
DxkPG48YnN8DxkHjUeOQcdg4Yhw1HhPHTI8bJ8Tjpk8YJ40njSwjZsSNbIP1ThinjKeM08bT
xhnjGYPz9qzxnPG88YLxovGS8bLRxhhmvGKcNc4Z541XjRZGS8NfV1xjkGFwLaZeo3iOEVKv
bTznHPz9wL0BzL2j0c7gWgN8a4N5Af7C/8HUzWnPwFx2jQ+dmH7twqwgR8ENDVbcuDLIOFYp
9MaLZ4LnR3YL37HjYLC/82Phf27oFbw9Miv8Sbf1weTD/4aj42cFt14qHFzI0Ts41rtgUKXn
sMCWIseapzoFOfZPrT/2/TuDHMuXNij66d/hesvqR9j+zJH2EertYxpFyn02J8z4KPu/vKBY
uEyu9hH0yVZtI6MubQmxvztzfxBmf++3KR5ML1MtgjbLqhjx+630Tg03j/m1osFPHxcJKtu/
Acw81CP4MHy30+zfXg4fbbMmOPDMvgZlbjsWTPxndnjR6qzgbtvnN5teCNjPzh+eDsoWKBaa
8Wzu4JVDAxtw/OSHN58JlSqRM1S4Qokw/Y+3rm7jlK+/fNU97ljrTt0enG77XnjFnuVBrY63
BP0uLwh+vr5GcHnVvKDuI5Fgzfy5bj7UZRb2dp8PLjM8eLRtsQjz6zktf4T6TNo1kU6/z3L5
0V93BJ9M+Cf4+9n1wW+vfh2ce/dgkPOvvJE3yp0NqnZ9PeC8LLv3k6DbwZeDwhXeC96a92LQ
bscNkdpzzwazJpeMVN50NrjwbI3Ind+/ErDOnL8CzZtF6O8+slXk+o9eCFhfxjmyqF6E88m6
cj4/ulgpwnns+/n5gPOwfsW5YOxNv4XZL+vBfFi/nMXOBV/cM87Nk+M/UTNn8vzacbAOHBfr
UPhQgQjrcLp2QZtX++Dg4s0B1wHrxfGyfhznze+cdeNxfjhe9s/1+HiBV5xynpjvkstng2fG
tglKzDsXDOq7PPizcrXIK3k2hr4qVj2y646ToZcbNou0PLMmNPaPapFS+74K/ftOtUi7ogXD
r5Yp4WqU+rHj/wZ8vi7flYC65LefuPrnwZ+6eucv77r6P1Pfc/W7y1939b4yb7j6t2annbY4
e9rlL7/5pNPL3Z50eZ2C21zd+Ymtrl5yub2rUfbX60gizP6/yvFUmDpvodtdvf/vsq7O2H06
xOcNp78U4vNT5+q7OuPONq4uNyG5/4n/JPf/V+4sN375Bcn9Dwgl9z/7y+T+v+vawX2OMt6t
I08l9xdP7n/m/DKurjCxnNt/x/XPJPd369nk/o9HkvV1nVy9c0tLt45DPm3p1vXAl02dnt7f
1OUZueq5etTbdZN96cn1H2LK/j/9LLn+z9ZPrn/b4p+6+ZXekFz/V8u85+oyjyTX/+WTyfV/
q1Ny/R+an9z/hZeS+2/YuWnE/h1XOGtzC6cNO5eNhB7eFOJ8c1383q14pNS/m0I3RvO46+V8
338D8kfyfRJwvbQc8Ymrbxj4rtNPn3s7KL99YeiWF19wNdcfNc8JrrfPn3jN6bnfX3Ofv9nz
aac8V7bU2hnafleWq7sO2OaU50+kzN4Q55/98vwYO2J/iOfJ8lv2u+fOlyX3hc73zQ7zecZt
JZ3y3GE8nkM5Om8OdbztyZD73J5PzCfjbJqrcy9O7r/Onc+4eY74Mssd1/k5yXm0XJ6cx3OJ
5W7ee28cH7A+XA+M90C1tgHr89Py38Mc34pSCbf/y1NLhFmfixtKuXp0dsztb/R7O93+O/dt
69aX5wnz4flyqMfGUEa1O0JObZ6Mv6p8K9fHc4jjWVeumas7V67nlOcV68P1QT/PMdaH5xrr
w/OP9Tm9OHneJm9Jni+eg4zHc5D1abw2ef54XjGfK+Ved8e3oUhy/4c/buXmuaR1a3edjL37
nYDrpsTWD51eKvqZ00mtr3Gfly54a/J6WlLdaf1Byevs2OHkdfZFr+Q4M22ujHNx2z9On+9f
kX9LGH7+36NO6z55lRv35HOdk/ubt9zp/pd2Oj219oDT+YuOOP326mNOY02PO5278YTTLvmf
dBp67pTTRy894zTj7B633xXHLzutX/ROt98KLx9zelfTPK7vvsLdnP66bLXTO9476fT27snx
5h1Jjtfq+uS6/NI9uS7PfPGp68tR5h+nw37O59ajf+g2p3l21XR6018vBfe3WxcsCi8MNhZZ
GOR46cXgl0dOBuzn/OYXg0OvPR98EzkV2L+/DZZueSb4p3MiKFTzheCG+MtB5t+93XZjgvzB
im4FgrZ78wfMd1SROenM/9d6O9L/aP9ysPb1fMGYAy8FZ/c8EWb8F8aUD1/p+QJ/T4WY/5uL
d4Q4nvIDgxD7Lbv+SjrHO6DLo+msx2vvvJCeo9nb6aseOxw+tfKx9Gde+CfMetE3M98f6eVG
DwvPDL5Pr7Z4YZj1HNClamj7kdwh9pPj6Zyh+pcbhzPG5Qg9sLVdmHW/WGVFaOYnLUKFin4a
OtXi3/T8D94Ttu970vvc2cYdB+tw+Eib4PbVLwd39loesEY5dh1KH1NiacA83q2/M2B81ol5
sE4Xv64ZWlYqEZwavzp0bMyZIMdfX4Xu3/180L/fL+Ge39r29se+dXM/c9u3b85fZQrkV8uj
uQU+j8BfI4/mNdgun8FngM8vjxYwChrXGoWM6wyywqqvNy1ikN9g+HHwNxpsW9S4yWCfZDfL
o8XELcrowRcXeHqoUbbBoyUEnnGpUfYNzMn34G9VjZYU+FLy6G0CX9rgc7a9XeDLyKN3iLLK
6Esz2A7w5Qz2V97w88FXUI3eKY/6Y8dXVI1WEpWV0YevYlQ1qhnV5dEaAl9THq0lj9YW+Dry
aF2Br6e8vqkfE99ANZouj4YEPiyPcgFDRBl9UcOPiW+oGuWYAN/I4Hi5ZrlGGhtNjKYC30zg
m8ujLQS+pTzaSuBbCzw/4wG+rcG68zMgaw141hzw7Q3WmH7Wt4NB3lEe7WSwxsyhs+oupncZ
zPdug8+gq0HPPUY3o7vA95BHewp8L3n0XoHvLY/2EfgMebSvwPeTR+8T+P7y6ABjoDHIGCyP
DhH4ofLoMIEfLo+OEPiR8ugogR8tj44R+LHy6DiBHy+PTjAmGpOMyfLoFIHPlEenCvw0eXS6
wM+QR+8X+Jny6CyBny2PzhH4B+TRucY8Y76xQB5dKPCL5NHFAr9EHl0q8Mvk0eUCv0IeXSnw
q+TR1QK/Rh5da6wz1hsb5NGNBtfqJqObwG+WR3sIPNcln28xqAH/oDy6VeC3yaPbBX6HPJoh
8FyvfL7ToN5l7Db2qN5rus/Yr+whefRhgX9EHh0s8EMNPj9gUAOeHPAHBf5RefSQPDpc4A/L
oyMF/og8elTgH5NHjxn04n0f2XGBPyGPPm48YZw0npRHswQ+Jo9OFvhMg8/jBjXgs+XRhMCf
kkefkkdPC/zT8ugZgX9GHp0p8Nw/fP6sQf2c8bzxguoXTV8yXlb2ijx6VuDPyaPcY4BfZPD5
edVkeHLAvyrwF+TR1+TRJQL/ujy6TODfkEffFPi35NG3DXrxvo/sHYF/Vx59z3jf+MDoLo+u
F/gNxkbjQ4N7eq3xkbFaelGeGr9S+rE8NX659BN5avxS6afy1PjPVKOLBf5zeXShwH8hj84T
+C+NucZXxhyB/1oenSXw38ij38qj9wv8d/LodIH/Xh79QR6dKvA/yqM/yaNTBP5nefQ/4hdl
9OF/VY1eEr8powc/Ufq7/ATTy8Y46R/y1Pgx0j/lqfF/qUZHCfzf8ugIgf9HHv1XHh0m8Ffk
0SECzw8a1OhAE8DnNAaYzWV6nyngr1KN9rUM8FerRnPLo33sc8DnUY3eaxngr1GN9rQM8HlV
o90tAzz3yBpjlfGewL+jbIU8Nf5NKfc3nvuf58WrBs+sZ4yXDJ4z842zAv+y8YBBHz0zjRnG
GYE/bWQaMSNhkE0zyAFPjtKHn2xMMrIE/gljvDHWeFzgjysbLU+NPyodKT/cdKhx0Ohn7DD2
GYONQcbDAr/f6G/QR08vY7Ox1cgwehvbBZ4cpQ+fz85DfqOAwBeUR68VePsfwXDgrzPYtrDB
NoC/Xh4tIvA3yKM3GvQWNfgM8DfJozcbxYxb5KnxxVWjJeRRPw7+VtWo319J834++FKq0duM
0sbtBp8Bvow8St8dRlmDXsCnyaPlDHrKG3wG+AoGn91p+G3x7IN9VzT83PCVVKN+bfGVVaNV
DHqrGnwG+GryaHV5tIbA15RHa4nayuirY/gx8X5/nHfmwx+Ju1fsbvqvf6vwPz9L/ruQXK47
+b2J77tK2yc/mxlFfRZy/cnxrjbPZ9coo8dneMajzm34z8jwPgub9315zPl+Mnp8FtCm8dgf
n11HZBk9PsOTUec1qBsavs9nUWWsUz6D/ieVMQef0c+21PkN6pMGGX0+43My6gIGNc8W3+cz
PiejLmj4ft/ns2tpUx+e/hNEltHjMzwZdSGD+ojh+3xWOiVj3ei/RRnH4TP62Za6sEFdzCCj
z2d+7Vk3Mt9PH/X1ym82JaPPZygZWsRAixq+z2coGXqDgd5o+D6foWQon3v1fT5raJ/58cjA
75c5+Pom8/T5eVH740jtqaA+jpdx6PFrxXqQUft15tyQURc32AcZ41PfZpDR47MSyvwcqG9V
5vdJlpbSxz7p2aHMz4uspDI/L+pSKX3MjayxMvqYGz1blPn5k21SxnEwD46htMFxMGef3aGM
64mstHG7QR8Zc6M+ZJDR47Myyvz8qQ8oo4/5kh1MyZgb+9ynjLn4rKwyauZLvUcZfT7brYz1
K22wxk0Nf45KmyMrZ5CVtq8cA3Vzw/f5rLwyauZL3UIZ59Jn/rriWiOjvtNgPGqOi7qlQUaf
zyoqo+a4qFspo89nlZRRcwzUrZXR57PKyvxxUrdJ6eNYyaooo+a4qNsqYzyfVVVGzXFRV1NG
n88iyujjWOlpp8yvB1l1ZfRwrNQdlNHnsxrKqDlW6prK6PNZHWX0cVz0dFJGj89qKfPHTl07
pY/jJ3tDGX0cKz1vKaPHZ68rYx8cF/M4p4z5+ayuMmqOlfoVZfT5rJ4yao6V+mVl9PmsvrKr
lFE3SMnoJQsr8+tGzwvK2JZ1IktXRs3xU59RRp/PQspyKaM+rSy3Kftln4GyPMqo/bVBxjVD
HTW4F/LaVzLqhgYZa856NjLWGGQ8w3zWOCWjl76Nyrj36aOniTJq1p26szL6fNZUWWll1M2U
0cO5oG6vrLSpz5or4xlBRt1CWRll1C2V3aGM2t/n3NNsS93a4Hi5f8mo2xhk5ewrGXVbg4z7
jYza32/cW2TUfs5kHAt1B4NtuWfIqDsaZNRcP9RdDN/nM39vcX+QUb9j0Mc6c02xxqsMP57P
VqZkXGeMv1QZY/nsLmXUXGfUqX0+u1t91Fx71MuVMZ7Puirz1yf1PSl9XKNk/JzCnOnjGqVn
hUHmr2Oybsr8dUzdXRl9XMtk/OzEtvQ1NOiJKPPXO1kPg76G9rWRQd3TIKPPZ/y85vu4vukJ
K6PHZ73M00fNNU99r0FGn8/4GdD3cc3Ts4HI+ujxWW9l/r6g7qOMPu4NMn4OZVv6uA/oSVdG
j88yzNPn7xXqvkSW0cf9kmHwM5zv436hp74yf0+R9TPo8/cU9X3K6OO+IuNnZN/HfUXPdoPM
33tk/ZX5e496gDL6uP/I+Pmdbenj/qOHf6tI5u9RsoFElvl7lHqQMvq4T8n4edD3cZ/Ss5/I
tvX3MtlgZf5eph6ijD7uZzJ+n8C29HE/08PPn2T+nicbSmQZPdzP1MMM3+czfvfk+7jH6eHn
XTJ6fDacyDJq7nHqEYbv89nV2pY+7nF6+HmZPnp8NpLIMmrucepRhu/zWS5tSx/3Mz383E4f
PT4bTWSZfw5Qj1FGH/e469G29HE/03PcYFv/HCAbq8w/B6jHKaOPe5zsD2X0cY/Tw+8YGM8/
B8jGE1nmnwPUE5TRx31P9psy+rjH6eF3C2xLj88mElnmnwPUk5TRx31P9osy+rif6eH3KmxL
j88mE1nmnwPUU5TRx31P9rMy+jIMek4ZbEtPhkGWaZBl2Ne+BvVUw/f57AdlGabcz/TwuyD6
6PHZNCLL/HOAeroy+rjHyb5TRh/3Mz38Xolt/XOAbAaRZf45QH2/Mvq4x8m+UUYf9zM9zyvz
zwGymcr8c4B6ljL6uMdnGl8Z7Jc+7md6+B0YmX8OkM0msowe7mfqOYbv89kXyujjHqfnvDL/
HCB7QJl/DlDPTenjvif7VBl93OP08Ps69kuPz+YRWeafA9TzldHHfU/2sTL6uMfp4Xd6bEuP
zxYQWeafA9QLldHHfU/2kTL6uJ/p4feDbEuPzxYRWUbN/Uy92PB9PvtAGX3cz/S8p8w/B8iW
KPPPAepG2i993ONk7xvso659DRlLjWWGz7jHqVcSWR89PluuLKyMeoWyiDLqkPbbQBljrTIY
r459ZTzq1YbPeI5QryGyPnp85serrYyetQZ9ZDxHqNcZZGzns0BzoY9nCz0bDfro8dl6ZY2V
UW9Iyegl89/7NDXPtvTU0z5uUcb4mwz2Udy+0ke92fAZzyrqLUTWR4/P/HjFlNHzoEEf2RSD
eqtBxnY+a6C50MczjZ4dBn30+GybspbKqLenZPSS+e99Wptn2+3GToPxbrKvZIyfmtFLvcvw
fVNV71ZGj8/89y+3KaNnj/pKKaPem5K1Vb1PGTXj0ePHK2GenJ79BnMha29QP2T4bJrqg8ro
8dnDyqh5NlM/oow+n/nvc0paRi89fjwy+sgOGOz3VvtKRv2o4bMZqg8po8dn/I6fvkLK6DlM
pOx+1UeUsZ3P+G8F9F2rjJ6jRMpmmqN+zCBju5kGGf/NwffNMkfPCSLrm2lffXaMyLKuyqiP
EymbaY7Mf4/UzTzb0sN/r6CvgH0lY/zHDbL89pWM+gnDZ7NVn1RGj8/8ePmU0fOk+tgVfdRZ
KRl/F1HHlNHjM/57DfvlKxk9cQplD6jOVkaPz/jvPL5vrjl6niKybenxWUJZb2XUp1Iyesn8
90gZ5tn2lMF/v2K8XPaVjPFPG2S17CsZ9dOGz+apPqOMHp/58Woqo+cZ9ZHxdyX1s8rYzmf8
NzP2QR9/L9LzgkFGj8+eU9ZfGfXzKRm9ZP57pIHm2ZaeFw3Gq2FfyRg/NaOX+iXD9y1U/bIy
enxWVnOuroyeV9RXTRn12ZRssOpzyqgZjx4/XiXz5PScN5gL2VCD+lXDZ4tUv6GMHp9dUEa9
2KB+TRl9PvPfD1WxjF56/Hhk9JG9brDfqvaVjPpNw2dLVL+ljB6fldFaVVZGz9vqI1uq+h1l
bOez0tq2vjJ63lUf2WjV7ymjZlt6/PdS9I016OG/6zLncfZ1mfG+0VjZmJTsA/P0jVJG/SGR
ZWy33KBuom3p89lH5ukboYz6okFGzwrjouG3pc9nH5unb5gy6k+ILKNnpUE9Qvulz2efmqdv
iDLqz4gso2eVQX2ftqXPZ5+bp496tUE9PKXPZ19YTt8g+0pG/aVBRr3GoB6mbenz2Vfm6Rug
jPprIsvoWWtQD9W29PnsG/P03aeM+lsiy+hZZ1D7benz2Xfm6eurjPp7IsvoWW9QD9F+6fPZ
D+bp66OM+kciy+jZYFAP1rb0+ewn8/RRbzSoB6b0+exny+m7176SUf/HIKPeZFAP0Lb0+ewX
8/T1VEb9K5Fl9Gw2qPtrW/p8dsk8fdRbDOo+KX0++81y+rrbVzLq3w0y6gcN6ru0LX0+u2ye
PuqtBvU9KX0++8Ny+u6xr2TUfxpk1NsM6q7alj6f/WWePurtBnXvlD6f/W05fdQ7DOp7U/p8
9o/l9FHvNKh7pPT57F/L6aPeZVB3T+nz2RXL6aPebVD3SunzWQ5ld6uPOqcyevYY1H5b+nzm
f7fURRn1VdqWnr0GdU9l9PnsamWdlFHnVkbPPoO6W0qfz/Ioo95vUN+d0ucz/7u5Duqj5t+E
sS70PGRQd1ZGn8/87wnbKaNO/ruUmVF6HjaoW2pb+nxWQBn1IwZ1p5Q+n/nfbbZRHzX/For5
0XPAoO6ojD6f+d+ztlJGfZ366DloULdXRp/P/O98Wyijvl599DxqULdTRp/P/O+fmymj5t8/
MWd6DhnUbZXR5zP/u/AmyqiLqo+ewwa135Y+n92kPuojBnUbZfT5zP/+vpEyav6NF/Oj56hB
3VpZo5TM/7eEqDJq/g0Y27LdYwZ1K2X0+cz/d41AGfWt6qPnmEHdVBl9PvP/jaW+Mmr/PcNY
ZdTuH0DZXEZattTgew3/vQrZEoPa/35ouDJq//0Q2WKD+g6DY8uwr/OMNKsrKOtn9XyD72v9
98pk9FH7vl5WP2DcaVlFbUs2x6CurKyb1bONSlb73+/2UB89VdRHRh+177vL6pkGP5P5n/PI
7jeo/e/HOyuj9j9Lks0wqP3v5Tsqo/Y/r5JNN6j9z8lNrZ5s8PuOdIO1am5fpxj83sH/LoOM
PmrfF7F6gsHvhiLatqHVE42w1f73PmT0Ufs+rovjBufbXy9cBz5rqPFWKKMeoYw+crJGysYp
o26sbJky6ibKuE7ZB/tslpKdsIzaX/f0+Ky5+qgfN6hbKKPPZ32V8Uykl55OKRl9ZP55yjOW
jLqz+o5azbbMw9+/3NNk1P55cFgZdQdty7OJnGeLf67xrCOj9s9Jnp1k1H5bMvZB3dHgOuD5
TEbtj4O/U5gz8+2ivgetJqf234OQ0Ud2l/q2KKP23w9ts4y/4/i7rbf6yBiPzH9fslUZtd/H
Lsv2Gvz96f/+JWM8su4Gx7FTGXUPZTuUUd+rjG35O52x/PcC29VHj58f39dxbBxDhrYle8Kg
7q+MHp/5a4PrhYy6n/pWKaMenpLRS3afspVWk1H7e2GTtmWfA9S3URn1QGUblFEPUrbGMnLq
wSkZ8yMblpKtt4yeISnZOsuohypbbTXbsp0/jpxXrvzxy5UrH9V9izeufntl27cmfxp/XUn8
S9Rg2af1l+2azFf3f4u+rLDsr8SfV5b/eWXpn1fu/9eamv9zJaW8/9KVj9icP7/0cXLlRyfb
9n7daXeL1TuHZN7YYnXpkjkW3ZWvc+nWaz6pkOPGfBd2un9uYrNzfzYs2NrwsU2lGlEsSEb2
9X/NywT/a/j/V/M/93trSg+r6lY2JfvvNo+VLzfmsZ97Zs5C7qWMORpaVl1teaXI/16vVlw3
LfmrigM29+s/axiv+eaD4eU9Hqyfu++smOH8W20jlpcMyE3jVjt/Mi0Uf7Llnc6X3lgrbjhv
Wdw+c37B9Y3jHV78dFfKmDH5MPvAt/jy8TvoS47/YJh54DUf16M5qMfNwXnty3nNwXnNTf0P
xvyYHAdjMT7HwfFoX+YfdPvimNienGNiXDzHxP7wNt+gYVBpD5518mtV+ePjZfmMnPFsv86j
fm21X/W4+Tiv8Z3Xfp3XfNTv1sf51Fe2pb6m6sK/jeMFlm8Lry5fOmt1taZx+59GuAP/VZ3G
8ZPZr8fwvTIaWs9tcfyzhULxk+erOo9Sk/M5fXi2Y3u8/c8y7GJc5WGfW3/wX/3nqwZ+HNPA
j2+fB36/tl3g52PjBTXyVt7DmMrd/NUfkGsc5208xnde+03m2a8zH+ftlZNlGVfzZP6+n+NK
5snjdZ75Mi79G28I4icfqx78s2VnVq6bIvH6e2oE6z9+KcuyuH3mcsvi9pnLP21xe/zjcY1d
3rFsmfiu6U1cPjf/W7EZ7Zu6fGj1t2Mv9GjmcjsnZbe2a+7yxhkDyu7u1cL3h1P6w77fxg9S
xg/8+MwxZT6Bnw9ZyvwDP3/GYCyOizFsrm6/7NPmGiZnnzbXMMfLHGPjb9hDzhzt1X17yNUf
S+mPkWv8eMr4cXLNx+XMkbUj1/xdzhxZa3Idr8uZo83V5czR9u1y5mhzdTmvFLS5utzWdpfN
1fez/r6f9ffjc778+HE/vs6vy3V+Xb/Nn+vB5czRz58xOPc63jjnnvmzT8691ifOuSdnjrxW
kJw5cm+Sr7ZXs37aYodb/1/KNbdxdrr1v6t2i3gsx65wjXKXso43ahmv8MGu8MA618UOZbZy
4+BTX1eX+hq7PuNaxOtOezdGT+qr7iqsbGbj3BEnT30dXupr8t4o3jBef0Et15P6Kj0yPmPb
1NftMR7jkqe+ko/9Mw/y1Nf2cY44BvLUV/ulvvLPtg37bVNfC2j7Cvy+Ul8dmPpKQZtn4OeZ
+tpBywJ/XKmvJrTxAr8mqa8vTH2tYerrDlNfg5j6esTU1yba3AO//gPmNw1iOe6Icx5vHNQ8
6Nj1nZg7pymvXEx9FaOtTbD89KXdrE/q6xpTX+Oo8d31kPqqRx1LwLapr4NMfU2k1sH1pL5K
Uuvm8tTXTWrNXZ76SkqdI5envrZy7+amZTkG5pD6asvUV17q2nA9qa/F1LXk8tRXZ+rac3nq
6zU5z8ybfaW+unR4sWj8iXU1A9bZNG6185wHzgc554Hzgec5/NCwlj4P+9z6A9/PeH4c1I+v
8+u21fl19yzjNc74fDfjqz+u+TCO8xrfeZsP+3WeZ5pt73Pm6fuZv/M6LucZj5rx+Tzleov7
643xeP7Q8//1Okv/CsvUV1smv3v9v//PCeWyD64yrhb43ALPd8f8ucbw30vj+a6YGs0n8Pnl
0QIGvQUNPgP8tfJoIYG/TuALC/z1Bn1FDD8O3u/jBvN+DvgbVaNFDbKbDGrA3yyPFjPou8Xw
4+CLq0b9seNLqEb5WYPekgafAb6UPHqbwJeWR28XZZTRd4fhx8H7fXAumENZI83gvAG+nDzq
/+DLq0A5D4DnHAC+gjzKWgP+TnmU9Qd8RXnUnyN8JdWoP4/4yqpRf67xVVSjnEvAV5VHOb+A
51oCfDV5lHMLeH5iw6OcY8DXkEc534CvKY9yDQC+ljzqrxl8bdUo1wvg68ijXAuA5zoAfF15
lOsA8PXk0dICX18e9dcJvoFqlOsG8OnyqL/e8CHVKNcT4MPyKNcY4LmeAR/Io1x/gI/Iozwf
AB+VR/0zBN9QNeqfM/hGqtHGAt9EHuVXq4BvJo82F/gW8mhLgW8lj7YW+DbyaFuBbyePthf4
DvJoR4HvJI92Fvgu8uhdAn+3PNpV4O+RR7sJfHd5tIfA95RHewn8vfJob4HvI49mCHxfebSf
wN8nj/YX+AHy6ECBHySPDhb4IfLoUIEfJo8OF/gR8uhIgR8lj44W+DHy6FiBHyePjhf4CfLo
RIFPk0cnCfxkeXSKwGfKo1MNevG+j2yawE+XR2cI/P3y6Ex5dJbAz5ZH5wj8A/LoXIGfJ4/O
F/gF8uhCgV8kjy6WR5cI/FJ5dJnAL5dHV8ijKwV+lTy6WuDXyKNrBX6dPLpebFBGH36janST
2KyMHvwW1eiDAr9VHu0l8D0Mtttm0Af47fLoDoHfKY/ukkd3C/weeXSvwO+TR/fLow8J/MPy
6CMCf0AePSjwj8qjhwT+sDx6ROCPyqOPyaPHBP64PHpC4B+XR58Q+JPy6JMCnyWPljVyGVfL
U+PpTzMmGOUEfpw8Wl7guc+p0QoCz3OBGr1T4EfIoxUFfpg8WkngeU5Ro5UFfpA8WkXgB8ij
VQX+Pnm0msDznKVGqwt8H3m0hsDfK4/WFPie8mgtge8uj9YW+Hvk0ToCf7c8Wlfgu8ij9QS+
kzxaX+A7yKMNBL6dPJou8G3k0ZDAt5JHwwLfQh4NBL6ZPBoR+CbyaFTgG8mjDQ2uwZjhr1t8
XDXqr3N8tmrU3xf4hGrU30f4U6rRIwL/lDx6SOBPy6MHBf5pefQRgT8jjz4k8M/Io/75g39W
Nbpb4J+TR3cI/FZ5lOfiamOt8bzAPyiP9hb4XsZKg21eEHi2pUYzBJ5tlxls86LA00uN9hP4
DGOJwTYvCTy91Gh/gWfbhQbbvCzw9FKjAwWebecbbPOKwNNLjQ4WeLada7DNWYGnlxodKvBs
O8dgm3MCTy81Olzg2XaWwTbnBZ5eanSkwLPtDINtXhV4eqnR0QLPttMMtrkg8PRSo2MFnm2n
GGzzmsDTS42OF3i2jRlXG41FU2XkeO4xtLk8NT5b2lKeGs89hraWp8afkraVp8Y/JW0vT43n
HkM7ylPjn5Z2lqfGn5HeJU+N5x5Du8pT4581ehhbDe4rsm4GOeDJUfrwE41Jhl9bPOtNTsba
ZhnHjbIC/7o8mibwmQL/hjw6VeCnC/z9Aj9PHn3AYL8njeMC/7j8Y6bsA/BH5dE3Bf6wPPqo
ccB4WJ4av181uk8e9ePg96hGd4mdyujDv6Ua9XPDc2x8vt2gBvw2eXSpwG+WRzfJo8sFfqM8
ukGsV0Yffp1qdIXArxL4NQb7Xmz4ueEXqUaZP+AXyKP+PM02788jfqbBM+z/+c/M6H973WTy
tZLudY1fprx6csL+zMTg7t3d6x1//HZqIjJsVoxX70XLZCZ6/Zwzzmvdvkx5JeW3d45OfPPD
7Ox2BUdFtmeMTGzMuTd7xDMVI5UnN0vkKVc40fb19ZH5uWsmBv1aI8GrAO9/pHBi0k3NXL5i
wb7sOreOTND/cOW52VfeHZVgnNRXWO7pkzs+pnSme53iqEnbY5O/TL4eUa+JdK+27NJ9RLjL
vuRrEB87szi89Jtkz6cf/x5uk5bcNvWVl9FH50Sevm6029fF6J5I09nJOdxbtnC075Tk3Er+
WSN64Upyzg2LNouWP5g8lqK1RkZb59nnjnH8pVHR+0c84I499RWZlUpmRv9jr7FjrQp/PTV6
i732jjXU6zLd2j64PzN60F6byKvurvluanS9vT6Pnq/LZEY72Sv22Db1lZoflhkdXV9mToT1
2TlsZLTz6T0R1m19ZrPo8TKFo6xzi3E1o93n1YiyzuceLRzNd2Mzl1+eszfyWauRUfoL/vFA
pMIno6KMk/oKzoP78wSnbku+XrBI3R3h7l8mX6Go14a6V3NunjA0NmNf8lWJ1+ZZHNv3TbLn
mQ6XYt+nJbdNfWXnFx/PyT6Qd7Tb1+NN92b/cJfmcHvhxCtTk3MrsqRGYt2Imm7OF4o0S0w8
nDyWq3N3TaTf/EdkxXezIqmv+0x9DWjqq0JTXyGa+prR1NePpr6WNPXVpamvNE197Wnq61BT
X5Oa+irV1Fespr6GNfX1rKmvbdW95q6BRqsyEwc7f++uge6xyYlWl2aHeW1fne3TEtsH57f/
hpgWeWPR1MT3VR4Mr4sEkXo9JyZaFbg/FvlzUaRHVmZi2dXnY7ymMPW1gJvv7Z344KdN2UMu
Ph9594cOiXu+KJS4NKRKpMbvaYmbKqQlSuc5F3nj7eKJPn80s1eWNo7cvm9r9pPj+iV4teWl
6suy31420t0XzfsUjp9+IHlP7X7u2vgf105NZJZtFil61fbY1iLJV5GGL62K7axhrxV8fUjk
muw64UWvJl+DeNuv08In7JWrvG71y4e/Cv94PPk6xdTXLA44tzHy2vLeCea5fmCh6I//dnCv
fS65JS1a+/O0xC0vvxI5fH3TaP2ht7pXMfZ99b7ogvLbsmNfPfzfXvuY+jpIewJG/bNPr6p0
r5X8zF4NmsvuQV5B+0QoM7rKXknJ/dW15tToq/aqSo6r5+MTo/PtHuRVp9WO2/1rr7ZkbS80
z4x2sfuR18imvgqzwF/3Ri/8sDFyuetLkY+PdIzW+ftad3/1Llouen5YWpT5jztXInro2mZR
xt949bbIjJ39oo3qHon0a7480nXASHdfFC92fdDtgeQ9NaN6weCxalOjnJfXeuwN149Nii7c
PjPywKNLwiXSk/fXgqIZsVPWw5gP114UaxxMiv4w54FI0+t/idl7XaNcJ6mvE83osyl75pf3
Rpnn5y9em1h4uGOU6+HvY2mJXi8n57ksrVkicqSEGzP/tv6JunsWRmrGnois+ntU4v0GD7hn
Ttv0YYmqU/ZFeC2pX2Nb70ROK/53JJfN6yoDvVrkNs1jXGPkNfIZ+Y0CRkHjWqOQcZ1R2Lje
KGLcYNxoFDVuMm42ihm3GMWNEsatRkmjlHGbUdq43Shj3GHwPVyaUc4ob1Qw7jQqGpWMykYV
o6pRzahu1DBqGrWM2kYdo65Rz6hvNDDSjZAIm0Ig6AdOGHBzAPuAhqKRKTQWzBGaiKamwHFB
M9HcFFoI1gVailamwFpCa9HGFPieHTgX0E7489Xeag9ZB6Oj0cnobHQx/LZ3mb/b6GrcY/C9
dnejh9HT6GXca/Q2+hgZRl/Dz7mf+fuM/sYAY6AxyBhsDDGGCjxrUFrq18TrMMuHGyOMkcYo
Y7QxxmBNxxrjjPHGBGOiMcmYbEwxMo2pxjSD79dnGPcbnMeZxixjtjHHeMCYa8wz5husFesE
fi39+vi19mvvz4U/N/5ctbRtwa+LP7ecZ/Dn3h9vU8vAXyscI/hriesKGoqqphAV/trk+MBf
u/5a5tr23n/me/22fiw/dkPbBvy+/Vz83Pxc/dz9MXnlOFPxa+DVr41Xv2Ze/Vp69Wvs1a+9
V39OvPpz5TWvzScVf269/q9Yo9Rzir86hQXm/0+F/1eO2bnsZ/wTzwSvP74kWLJlrr3Oam4w
cfiZ4P2qxxz1B50Jnn77dLDt85PB64USDvwDr50OzrV/Ntg4q7XbjtdZrTPQoktaB9fnvCZU
MPx7eEKu4iHGxzPue4maYcYu0bZJiHGWn54QYtzaMx8PsZ+zH10dZi5s97b10nfxlyYhtptp
GeOcypc7zHbVbRu2yxg6McR2F/dfE2I+zIPjYB4rWj3rju1pmwPbMzbjMQfG5/jYnrkwHnNh
fI6PfbHdjsKNuL1yDOpbzWl6t2hkXbm08JnXKkUunvw9dGJLJVfX+vhmV6N83r7C1U53rfoz
oG/NOxcD8r7/fOTq1SXfc/UL3d929ZY/3nD14OgFVzMX+vc9GnM1c6S+rsBxV3MM1K9M2JTs
t2Oj5rjZH0rNcaClu58Kk3Pc1A0/rORqjpf64psfhPicdXD1yUmuXpcvOY8hDyXn8Wru5P63
3pnc//LRyf2vO5rcP+eAcdy5sHFvLJ/cf4Wmyf1/tTa5/47Hkvs/b+eO/eWYk9x/x8rJ/Zcu
ktz/hmeaunX8ZFUTt77/VG/s6uNPR1295e7k+Zgwsaari21Kno81HybPB8r4h9KS52PA0uT5
6Pp68nzccTl5PhbflTwPvX9NnoeK6cnzUPf55P5nrU3uf0ut5P5vLkS+J9SvdVPb76RQjRPn
7bgnhXLXftXWfU+o931vOX3+mzdd/mOJj1z95sEPXb3hzz9cXfPIH65OznNPKDnvSaH3EzXd
+Ms+47gmhc7WaOjq9wc3dPXkAsn9P90iuf8cq5vb+ZoUanipq52/PaGGo886vfjFsy4/fKGs
rfOe0Fd9b7fzPin06+W4q3u9FnN18nztceeNz3tdtdnN73TbzW5+V39y3NWlOp5w9dpNcVdX
uiHb1afSW7j9lD6T3O+p9OdczetA2e/bi5P7/e7abFff9VVyv8nrdI+7XtnvprzJ/dqrEN24
Tb5M7rfX3cn9vr4tud+hxZL7HZWVXPcmDZLr/uDg5Lpf81Ny3avenlz3Gx9LrvubV5LrPvpE
ct2T9+ueUPL+nRQ6n7+yW+e95Su7df6gEXVa6LHeLk9Xf/qzf5Rwz4PhR/M43XWHGzf96a2/
8ddzDrufWJ/05wZ/4OoTb77l9N1/ub72pF+77IKrWx8/5+rkfbYnvfXUp13+RZlspytqPO4+
f3jb464++5lbn/TMLitdrfVLH72xi6szXsnptPSDT7LO6fV/eYRvG3LUf7i4q0c3uNnVP/3z
On9d5ij9OvfbnvRTN8129cWS5V3d7Wru+z3pvJaTvlW9kvPpXDk5n2GbkvPhOcTnRd496rTR
piNOtxc/5PTmSg87Xf5Rct71s0/YuGmhO9dRp4X+zdjuPh/LqwTtj67D9EH/aefqM/ZqQ/IK
C5LHUyH6kKtbzkwez8zrkseTsePN5PxPz0oe18Ry7jgun3b3Sfrhq1q48zTjnqZOf3vT3U/p
uQoln++XqtTivKfnr1XFfa77Mb3N4WKu3vnDVU77l0qe5wX3Jc/rzleT5/nQt8nzm3yO27rt
Sp7fgoeT5/eHvMn939ojuf+D89xzJVSq1nm3DjXHvuk0Fv3Q6UuD2E+aex6gjfMxv7TQV9uY
d1qo0APJ7bdXr2vHmRaaeW/CabGfS9p5TgudOpjlVM/h0FOLs914GUeSfTPfTm6Xt0Qp1/fE
6WS//t4IDdqcPD8Tn06erxwrk9uPmZScZ6/6yXn/2TQ533wjkvPV33+hOhueDbbXzA64buct
f97xkPnCOecHHfLMD7YkXgjqNFpj30O8GHz5aQ+X96iWJ4gXezHgFdaXR78Q7Bt/OMy2I+ya
ZZzZ+6emc18Mt1dcVsk4HTRZ8XQw5+Z4kKvSc8EPaUuD/L++EDRo1sK9TrrYd3ncfqaN/ybM
66K57hlrdJNn3NwyMvuEhg04HTS89GY6Y8y0sZlfjleKpJ+rYddkpwUNKly32F2DLxVuETBe
nQ157PNVDbZuuBSmb9js/WHur4tVCqfPvDeanrfHrHCOrnelv1ivZ5j9Md+ZF3qnx9NbhHMc
HpheNxyEc/wwLP0b+zuQ/XFc3Idffvquu/8WXugdyrDXco7teDrEfWzbN+A+f/eqgw14LoSe
mxmaV/q5wF4h7K5x+xbO/Vxv38a53z1cpRr136ficwt8HoM/1xhsD3i+r8aj+QQ+vzxawKC3
oMFngL9WHi0k8Pz+APD+e348v0+gj98p+HHwfh/8nsHPAc/vHKjRogYZv3+gBjw/g+BRfidB
H7+X8OPg+R0FNeqPHV9CNXqrQW9Jg88AX0oe9T/z4UurRm8XZZTRd4fhx8H7fXAumENZI83w
P5Phy6tGKwj8nfJoRYGvJPCV5dEqAs/PhNRoNYGvLo/yexbA1zRqGbUN/3Mmvq5qtJ7A83sY
arSBwKfLo1y0gOchDnhuMjzKQxbw/DyLRxsKfCN5tLHANzH4GY2fX/2c8fwMS422EPiW8mgr
gW8tj/qfRfFtBb6dPNpe4DvIox0FvpM82lnguxh3GXcbXQX+Hnm0m8B3l0d7CHxPebSXwN8r
8L3l0T4CnyGP+msD31c12k/g7zP6GwOMgQI/SB4dbAwxhhrD5NHhAj9CHh0p8KPk0dECP0Ye
HSvw4+TR8QI/QR6dKPCT5NHJxhQj05gqj04T+Ony6AyBv18enSnws+TR2QI/Rx59QODnyqPz
BH6+PLrAWGgwz0Xy6GKBXyKPLhX4ZfLocoFfIY+uFPhV8uhqgV8jj64V+HXy6Hpjg7HR2CSP
bhb4LfLogwK/VR7dJvDb5dEdAr9THt0l8Gny6G6B3yOP7hX4ffLofoNevO8je0jgH5ZHHxH4
A/LoQXn0UYE/JI8eNo4YR43H5NFjAn9cHj0h8I/Lo08I/El59El5NEvgY/JoXOCz5dGEPHpK
4J+SR08bTxtnjGfk0WcF/jl59HnxgjL68C+qRl8SLyujB/+KavSswJ+TR+cJPPcX25036AP8
q/LoBYF/TR59XR59Q+DflEffEvi35dF35NFTAv+uPPqe8b7xgfGhPPqRwF+URz8W+E/k0U8F
/jN59HN59AuB/1Ie/Urgv5ZHvxH4b+XR7wzm/L3xgzxa1ihnDJSnxtObZuw0ygv8dnn0ToHf
Ko9WFvgt8mhVgd8kj1YX+I3yaE2jtrHOWCOP1hV4nmvUaH2BXyGPpgv8Mnk0EPgl8mhU4BfJ
o40EPlMebWI0M+Ybc+XR5gI/Rx5tKfCz5NHWAn+/PNpO4KfLox0Enr/nqNFOAs/8qNEuxt3G
JGOCPHqPwI+TR7sL/Bh5tKfAj5JHewv8CHk0Q+CHyaN9BX6oPHqfwTX4o8F1+J3xk/GzPPqN
wP9HHvX3Bf4X1egXAv+rPPqpwF+SRz8W+N/k0Y8E/nd5lHm+Z1w2/pBHTwn8n/LoWwL/lzz6
hsD/LY9eEPhz8ugrxtPGs8Y/An9WHl0g8POMU8Zp41+BvyKPLhb4hUbcOGX4H7rwbEuNLhV4
ts0y2CanfQ54evHochPAs+0TBtvkshrw9OLRlVYDnu1OGGxzldWApxePrrYa8Gx3zGCbq60G
PL14dK3VgGe7Iwbb5LYa8PTi0fVWA57tHjUOG3msBvw18uhmqwG/wfQRg23yWg14tsOjD1oN
eLZ7yGCbfFYDnl48us1qwLPdXoNt8lsNeHrx6A6rAc92PxoDjcHGEGO4wf0G+J+lI+Wp8dxj
6Gh5ajz3GDpWnhrPPYaOl6fGX5JOlKfG/yadLE+N536bYkwzLgs89xg6Q54azz2GzpSnxv9l
PGCcM7ivZhqzDXLAk6P04XcZuw2/tnjWm5yMdS1gWtC4VuALyaPXCXxhgb9eHi0i8DcI/I0C
z//EIDXK/4wg+73ZYH+A538iEH+LwT4AX1we5X/iD/D8T/vh0ZJGKeM2eWp8adXo7fKoHwdf
RjV6hyirjD58mmrUzw3PsfF5OYMa8OXl0QoCf6c8WlEerSTwleXRKqKqMvrw1VSj/M/xAb6G
wPO/w8S+axl+bviTdt6pUeYP+NryqD9Pdcz784iva/BH4n7fZ1djlDqX+8R/NjNK6bMK7rNk
31Xm6U9TRo/Pkv3JV71ebbn/jH3gffaxtmW73AbKZ/ShPssgsozP8xh81ssgo8dnvZUh1xh8
VpHC+pirz+gno85rUOc3fJ/P+JyMOp/h+32fz4rTpj7Gof96Isvo8RmejLqAQZ1u+D6fFVHG
/goa9FdSxtg+o59tqa81qKsYZPT5jM/JqAsZvt/3+awwbeq7zpzvJ6PHZ3VoUx/b+M/I6PFZ
LdrUx3rwWTUiy+jxWQ1ljMOx81k9ZRyHz/yash5k1A0MxuPYbzDIwwYZ6+szlAy90UCLGr7P
ZygZyudoc8P3+ayYMsa5ySCPKGMbn6Fsi95soA0Nvw+foWQoY6ONDd/ns6bK2N8tBnlLZRyv
z1C2Rbk+0ZIGGX0+89cu9wceShj0eU9dVhl91HCrMu+puymjjxrSlPk5MI9WytgHNZRS5j11
G2X0UcNtyrynLq2MPur/wd6bAEp31GXeHZJACFtYVFTQoKwCh1pOnapCllwI+5awyaYkQAhL
gJCEHSTs+yIgshPCIosi4jLu4IIyio67fjN+8zGj44DjgiMiKpLveerUIc2b903uufS9b3X3
8yb/213/+6/T1d3PPb/616k6Rfvu6mPcydXuU31THfpvVH3Tc5bvV32MY5n2XdU3PWf59Opj
HMu0Byz52Abag6qP7Zt802fKz48+lr8Pxs/+WPycPruHVR9/z8/yprDnH0PneD6dfDejq/oY
y7j/QRd8yzF/WX1XwiNjWO/m1ccH+li+BQuoO8Ww/L+qjw+sR9/3sIA4nq/oY/mWMPp4rqGP
5VvB6GOZx2f5f8OmuMl36+rj+Yc+lrvqm9rF8uerj3FsB33T+YXnBvpYNjC+xtRWlv9P9TGO
7aXPVh/PP/Sx7Kpvek8s/131MY7viz5ffdeqPpb76pveO8v/UH2M4/unL1Qfz3/0sTxUH8t8
/yz/Y/UxbvLF6uN5jz6WU/WxzM+E5X+qPsZNvlx9J1Yfy7etvqtVH8vfW32sx8+T5X+uPsZN
vttV33Wrj+XbVx9j+Bmz/C/Vx7jJd4fq4/mRPpbvWH0s87tg+V+rj3GT75Tq+5bqY3mn+qbv
kOV/rz7G8Tuj707Vx/MofSzfufpY5vfI8n9UH+Mm36nVx/M9fSzfpfpY5nfL8iXVx7jJd9fq
+6bqY/lu1ccYaoDlY46hc9wWfPLdnS74eD6lj+V7wOjjuZM+lu8Jo49l6odl5pxT3OS7F12I
43mSPpbvDaOPZWqK5eNrXcZNvvvgOeNOxk/6WL4vjD6WqT2Wr1Lrnrzkux+eM+5G1cfyaXTB
x3rUI8vMG6e4yXc6XYjj+ZY+lu8Po49l6pZl5ihT3OR7AF2I4zmbPpYfCKNv0jvLzKemOGqe
vgfRhbjvxk/6WH4wjD6WqXmWr1XrMm7yfR+eM+7bq4/lh9AF3w3wk3EsPxRGH8v8e2GZ/fsp
bvI9jC7EHYuf9LH8cBh9LPNviGXmc1Pc5HsEXYi7Mn7Sx/L3w+hjmX9rLDOHmOIm3w/Qhbjj
8ZM+lh8Jo4/lU2AsMx+c4k7BM/rOgNF3HH6eAjsDdiaMvlPwcwfG8lSXcZPvUXjOOJbvBGP5
0bDpeJPvzGNGH+PuDGMM81XGMWbyPYYu+Fjm3y7LZ8GmuMn3qFqXcfx7ZgzzKcYxZvI9li74
WObfM8tnw6a4yfeYWpdx/BtnDPNvxjFm8j2OLvhY5t84y4+HTXGT77G1LuP4d88Y5vmMY8zk
ewJd8LHMcwHLT4RNcZPvcbUu43guYAzzZcYxZvKdQxd8LPP8wPKTYFPc5HtCrcs4nh8YwzEC
xjFm8j2ZLvhY5jmD5afAprjJd06tyzieMxhzYvUxZvKdi+esyzLPIyw/FUYf4ybfk2tdxvE8
whiObTGOMZPvPLrgY5nnFpbPh01xk+/cWpdxPLcwhmNrjGPM5LuALvhY5rmF5afBprjJd16t
yziebxhzXPUxZvI9Hc9Zl2Weg1h+Bow+xk2+C2pdxvEcxJgrVR9jJt8z8Zx1WeZ5ieVnwehj
3OR7Rq3LOJ6rSkz1MWbyPRvPWZdlnqtYfg6MPsZNvmfVuozj+YsxX4UxjjGT77nVxzLPXyw/
r/oYN/l+rfoYx3MaY75SfYyZfD9YfSzznMby86uPcZOPYytsC+N4TmPMv8HoY8zku5Au+Fg+
g89gL4BNcWfwGYxbIkxxZ+IZY75MF+qegZ+T74V0wcfyo2Asvwg2xU2+2x0z+hj3aBhjvkQX
6jJm8r24+lh+DIzll1Qf4ybfKfV4jDurxnyxxjFm8r20+ljmuY/ll1Uf4ybfqfV4jDu7xvzf
GseYyffy6mOZ5z6WX1F9jJt8d6/HY9zja8wXahxjJt8rq49lnvtYflX1MW7y3bsej3FPrDF/
X+MYM/leXX0s89zH8muqj3GT77R6PMY9qcb8bY1jzOR7bfWx/GQYy6+rPsZNvgfW4zHuKTXm
b2ocYybf66uP5XNhLP9Q9TFu8nFbA2qDcU+FMeZzMPoYM/neUH0snwdj+Y3Vx7jJ94h6PMad
X2P+usYxZvK9qfpYvgDG8g9XH+Mm3xn1eIx7Wo35qxrHmMn35upj+ekwln+k+hg3+Z5bj3cT
+BjLmL+E8f3Sxzj63gKbfM+o5bdWH2Mm37OXjvdM+BnzzhrHmMn3tupj+Vkwlt9efYybfM+p
x2Pcs2vMdDzGTL534Dnbx/JzYCy/sNZl3OR7F55P74OxPNaFNY4xz4Ux5t0wxrHu5OMWFfQx
7nkwxryo+hgz+S7Cc8ax/IOwi2DvgdHHuMn30FqXcc+HMebF1ceYyXcxnrMuyxfCWP7IUtzk
ey/8jGP5BTCW3wejj8ebfA+qdS+E74UwxkzHY8zkez+esy7LL4Kx/AEYfYybfKfX4zHuxTDG
fLj6GDP5fhTPWZfll8BY/iCMPsZNvvvUuox7KYwxL60+xky+D+E567L8MhjLH4bRx7jJd49a
l3EvhzHmQ9XHmMn3ETxnXZZfAWP5x2D0MW7y3aXWZdwrYYz5YPUxZvL9OJ6zLsuvgrH8gaW4
yfdR+BnH8qthLP8EjD4eb/Lt1LqMew2MMe+vPsZMvo/hOeuy/FoYyz8Jo49xk+/2tS7jXgdj
zDurjzGT7+N4zrosvx7G8sVLcZPvp+BnHMs/BGP5p2H08XiTL9e6jHsDjDHvrT7GTL6fwXPW
ZfmNMJZ/FkYf4yYfr+NMcW/CM8a8r/oYM/n+E54zjuUfhrH8czD6GDf5bK3LuDfDGDMdjzGT
7+fxnHVZ/hEYy++pdRk3+X4BzxnH8ltgLF+0FDf5fhF+xrH8VhjL716Km3y/BD/jWH4bjOV3
LcVNvl+Gn3Esvx3G8juW4ibfr8DPOJbfAWP512H08X1Mvk9UH8vvhLH8SdgUN/l4nY4+xr0L
9kkYr+fRx5jJ96t0wfeI6mP51+iqPsbSN/UxH4bnrMuYp9fjsc3vhrG9b68+vu7k+w085/FY
vgjG8luX4ibfp+BnHMvvgbH8mzD6eLzJN72Pi+C7GMaYt9TjMWby/Raesy7L74Wx/KaluMn3
afgZx/L7YCz/Zxh9PN7k4zXSKe79eMaYN1YfYybfb+M541j+AIzl34HRx7jJx2uxU9yP4hlj
3lB9jJl8n8FzxrH8QRjLr1+Km3y/Cz/jWP4QjOXfg9HH400+Xg+e4j6MZ4x5XfUxZvL9Fzxn
HMsfgbH8+zD6GDf5bl7rMu7HYIx5bfUxZvL9AZ6zLss/DmP5D2H0MW7y3bTWZdxHYYyZjseY
yfdHeM66LP8EjOU/htHHuMl343o8xn0MxpjXVB9jJt+f4DnrsvyTMJb/FEYf4ybfd9W6jPs4
jDGvrj7GTL4/w3PWZfmnYCy/cilu8v05/Ixj+adhLP8/MPp4vMl3cq3LuJ+BMeYV1ceYyfdf
8Zx1Wf5ZGMv/DUYf4yYf5zZMcf8Jzxjz8upjzOT7CzxnHMs/B2P5/4XRx7jJd4Nal3E/D2PM
dDzGTL7/juesy/IvwFj+/2D0MW7ycT7GFPeLeMaYl1UfYybfZ/GccTfGT/o+C3tejaOPsfT9
TxjjjsNP+v8HbNnHOJY5Z4RxN8XPp8H+EvZXsMl3fi3/r+q7GR7pY/mvl3xPreX/XX03xyN9
LH9uyfeUWv589d0Cj/Sx/DdLvifV8v+pvu/BI30s/+2S74m1/HfVd0s80sfy3y/5Hl/L/1B9
t8IjfSx/Ycl3di3/Y/XdGo/0sfx/l3xn1fI/VV+HR/pY/uKS79G1/M/Vdxs80sfyl5Z8Z9by
v1SfwSN9LH95yffIWv7X6rN4pI/lf1vyfX8t/3v1OTzSx/JXlnwPr+X/qD6PR/pY/uqS76G1
fEn19Xikr5Srhuj7Pv4e5enaSag+lqdxLvoeBGP52Fp3qD6Wj1vyPQB+lo+vvogyfSxfecl3
OnwsT9c6Esr0sXxCjaPvfjCWp+saufpYnsYx6bsPjOXpGsZtq4/lq8P490HfvWAsT9crvrf6
WL5mjaPvHjCWp2sTt6s+lk+qcfTdDcbydM3h9tXH8jROTd9dYCxP1xfuUH0sXw/G9tF3ZxjL
07WEO1Yfy9O4PH07MJaXx/5/CT6eH86E8Xg8Z0y+b60+ln8ZxvKjl+Im33Re47mOPpY5J4zH
Y/lXYCyfVX2Mm3zTOZbnXfpYvmGNY/kTMJbPrj7GTb7pfE8G0Mfyd9Y4lj8JY/nx1ce4yTex
5yerj+Ub1TjG/CqM5SdWH+Mm38TLn6g+lr+7xjHm12AsP6n6GDf5Jnb/ePWxfJMax5hfh7H8
lOpj3OS7afV9pPpYvln1MeY3YCw/dSlu8t28+j5U41i+RfUx5lMwls9fipt8U//qAzWO5VvW
OMb8Jozlp1Uf4ybf1Cd8X/WxfOsax5jfgrH8zOpj3OTrqu891cfybarvXdXH8tRvp4+x9E19
6h9G+dMw5l9TDvHGJd8AP3X6zupjjK++H4CPfpanfIE+Ho++VON4vP8MY844He+Hlny3rXGs
xzjGxOo7A2X6WZ6ORx/j6LtdjePxfhvGPHc63muXfHeocazHOMZ8b/U9CmX6WZ6ORx/j6Dul
xvF4vwO7PcrT8V695LtTjWM9xjHmjtX3GJTpZ3k6Hn2Mo+/UGsfjfQa2g/J0vFcs+e5a41iP
cYy5c/U9FmX6WZ6ORx/j6Lt7jePxfhd2F5Sn471syXfPGsd6jGPM3arvcSjTz/J0PPoYR9+9
axyP93uwe6A8He8lS7771jjWYxxj7lV9T0CZfpan49HHOPpOq3E83n+B3Qfl6XgvWvLdv8ax
HuMYc7/qOwdl+lmejkcf4+h7YI3j8X4fdjrK0/FesOR7cI1jPcYx5gHV92SU6Wd5Oh59jKPv
ITXuBSj/AexBKE/H+8El38NqHOsxjjHfV33nokw/y9Px6GMcfY+ocTzeH8IeivJ0vOcu+X6g
xrEe4xjz8Oo7D2X6WZ6ORx/j6DujxvF4fwT7fpSn4z1ryfecGsd6jGPMI6vvApTpZ3k6Hn2M
o++5Ne5OKJO35PGjqu/U6mP50Us+spXlx1TfXVGmj+Wzlny/Ah/Lj62+u6NMH8tnL/nITJYf
V333RJk+lieG0vdJGMtPqHH3rj6Wn7jk+1X4WT6n+u6LMn0sT2ykj9xj+ck17rTqY/kpSz4y
juVzq+/+KNPH8sQ8+n4DxvJ5Ne6B1cfy+Us+sovlC6rvwSjTx/LEMvp+E8byM2rcw1Amo56O
8rOq7yE1jjHPXPIxjuUp7hko8zt/NnyTXp6+5Jt08DPw/SLseYh7WT3ejVGmn74frD6W/xjG
8iuW4ibf86vvJjWO5Qur79nVx/ILqo/1/gTG8o8sxU2+F1bfc2ocyy+qvudVH8svrr7nVx/L
L6m+l1Yfyx9aiqOfvpcu+V4MH8sfrj6+35+H8TN5efX9FMpsN9//K6vv49XH8quWfH8KP8uv
rj7Wm3xvrr6PVR9jXlN9H60+ln+o+j4MH/2vRfl11ffB6mP59dX3o9XH8lSXPr4uy2+oce+v
PpbfWH3vrT6W31R9F1cfyz+85Psz+Fl+S/Xx+JNvem98v/SxPH2//G7pY/lHa92Lqo/Hemv1
vbv6WH5b9b0GPvpZfvuSj8ej7/1LvrfDx5h3LPneBh/L76y+17EejOV3LfneCh/L717yvQU+
li9a8v0IfCy/Z8n3ZvhYvrj6Xo8yfSy/t/reUH0sv6/6XgUf3wffwweq75XVx/L0WdHHz5Dl
D9a4l1cfy8safyH81PJHatwxx31+cdpxf3j6RZ8+5qIT/vDir7zukn+5hP9jB/Wvcst0/P/v
l7z74pu/8jL/f/Grl/xj2UEdP5//H5+4GDXGf3hyw0+dfoPfOv0Gd3sq//8U/7/eb732L28+
btb+0Q++8sM3f+WH8bP8f/EHX/lddzn9evz/JY+6+QuPu8fNX3vyg154vcW1b3zPa3/+hPtf
/Xpo8fTvnIvfd8qv/c6NdljmOxz/XboT+uQ5/OP+xd3w8C94BO+V4R93YB8D9q9dR2hAdY+v
exJKJ1z49N+2RRHMRf75j697hw+986Z34PPjFydeeCzjL+H6mC986b6//IR3/AI7CIt/eNk5
t1t+ftEd/+S2h/oRf/sphs8f9bb73p4xPM70nOXxNfASWFuz/BpoyS//2D99JzsVi3866yd/
6XF33SnP/+Flf/uLH3/bfafn3zs9R8ztphjUvf1Ud7kdPNal7+n4ctzPvesNt5te44t/+w/l
+avy7X9p+fkH7nbr0na2Y3r+9ce6EouL6Vh8fvi4qyxw7NtNcXw+vQ7bfyT/csx0XNadnvP1
pn8nTk/K40kFuPh7/jrvCUull/zz206hLbnw5Vt2/Ba/+5l73/7D/zjevezQ8uOOIQ8vvONo
Z5S/yyojhu7i37hy69JAHmtxCv6HXQi7CPZJ2GdhCxz/JNjJMAM7BXYajK97LuxC2Mthr4e9
BXYR7IOwj8F+DvZJ2Kdhvw/7c9hnYZ+DfQH2ZRgnnR4HOwF2ddhJsOvBrg+7Aexk2I1hN4fd
CmZgPSzBbgc7BXYq7O6we8NOgz0Q9hDYI2BnwB4DexzsHNi5sAtgz4Q9F3Yh7IWwF8NeCns5
7JWwV8NeC3s97A2wN8HeDHsL7G2wd8DeBbsIdjHsfbAPwD4I+zDsx2AfhX0M9nHYT8N+FvZz
sF+A/RLsV2CfhP0a7Ddgvwn7NOy3YZ+B/R7s92F/CPtj2J/C/hz2X2F/AfvvsM/C/ifsr2B/
Dfsc7G9gfwv7e9gXYP8X9kXYl2Bfhv0b7Cuwr8I4kHgM7EqwY2HHwY6HXRl2FdgJsKvCToRd
DXZ12DVg14RdC3YS7Nqw68CuC7se7Jtg3wz7Ftj1Yd8K+zbYt8NuALsh7Dtg3wk7GXYj2HfB
vht2Y9hNYDeF3Qx2c9gtYN8DuyXsVrBbwzrYbWAGZmEO5mE9LMAGWIQlWIbdFva9sNvBbg+7
A4yTlE+B7cDuBLsz7FTYXWB3hd0NdnfYPWD3hN0Ldm/YfWD3hd0PdhrsdNj9YQ+APRD2INiD
Yd8HewjsobCHwR4OewTs+2E/AHsk7AzYmbBHwR4NewzsLNhjYWfDHgd7POwJsCfCzoE9CfZk
2FNg58KeCjsPdj7sAtjTYE+HPQP2TNizYM+GPQf2XNjzYD8Iez7swjsvLoQtXoBH2OKFeIQt
XoRH2OLFeIQtXoJH2OKleIQtXoZH2OLleIQtXoFH2OKVeIQtXoVH2OLVeIQtXoNH2OK1eIQt
XodH2OL1eIQtfgiPsMUb8AhbvBGPsMWb8Ahb/DAeYYs34xG2+BE8whZvwSNs8VY8whZvwyNs
8XY8whbvwCNs8U48whbvwiNs8W48whYX4RG2eA8eYYuL8QhbvBePsMX78AhbvB+PsMUH8Ahb
/CgeYYsP4hG2+BAeYYsP4xG2+AgeYYsfwyNs8eN4hC0+ikfY4ifwCFt8DI+wxU/iEbb4OB5h
i5/CI6z80/lZ5+crQQvHwo6DHQ+7MuwqsBNgV4WdCLsa7Oqwa8CuCbsW7CTYtWHXgV0Xdj3Y
N8G+GfYtsOvDvhX2bbBvh90AdkPYd8C+E3Yy7Eaw74J9N+zGsJvAbgq7GezmsFvAvgd2S9it
YLeGdbDbwAzMwhzMw3rYqTvvv8qpO2/+jlN3/uLUU3de+uxTdz78iVN3HnW9u+z8/jPvsnOD
v7vLzvlPvevO1a98t50bfeRuO1864+47f3qze+xcZ3HPneP/5p471/7re+2854v33rnlN993
59b3ut/Obd502s6n/vH0ndc95gE76e8euPPMVz9451vu/JCdv7n2w3b+7F8fvvOn//796Gec
8XV22wc+Yie/5cE7bxlO3/nrm91758Kz7rbzzM/faee5H73Dzq//xG13vvK5YeeUB/udE754
m50bfuJWO2/66Vvs/MYf3HTnDte78c6nn3WjnYcsvnPnWh+4wU7/+G/bsXe//s7rdr5550sP
uN7OTX/wOjtf/pWTdh7+TdfaOf3Ca+x84atX23nE60/c+Yy/6s6LPneVnT/68SvvXP9Fx+/8
4tnH7diHH7vzxUdcaec15xyz88pXLHaOPfuSU27yx/9xyqce+pVTbvcv/3bK33/kX0+5zzO+
fMp4DtDPtj8BaVqabluh81snTUvT81XTdg1pWppuW6HzWydNS9PzVdN2DWlamm5bofNbJ01L
0/NV03YNaVqabluh81snTUvT81XTdg1pWppuW6HzWydNS9PzVdN2DWlamm5bofNbJ01L0/NV
03YNaVqabluh81snTUvT81XTdg1pWppuW6HzWydNS9PzVdN2DWlamm5bofNbJ01L0/NV03YN
aVqabluh81snTUvT81XTdg1pWppuW6HzWydNS9PzVdN2DWlamm5bofNbJ01L0/NV03YNaVqa
bluh81snTUvT81XTdg1pWppuW6HzWydNS9PzVdN2DWlamm5bofNbJ01L0/NV03YNaVqabluh
81snTUvT81XTdg1pWppuW6HzWydNS9PzVdN2DWlamm5bofNbJ01L0/NV03YNaVqabluh81sn
TUvT81XTdg1pWppuW6HzWydNS9PzVdN2DWlamm5bofNbJ01L0/NV03YNaVqabluh81snTUvT
81XTdg1pWppuW6HzWydNS9PzVdN2DWlamm5bofNbJ01L0/NV03YNaVqabluh81snTUvT81XT
dg1pWppuW6HzWydNS9PzVdN2DWlamm5bofNbJ01L0/NV03YNaVqabluh81snTUvT81XTdg1p
WppuW6HzWydNS9PzVdN2DWlamm5bofNbJ01L0/NV03YNaVqabluh81snTUvT81XTdg1pWppu
W6HzWydNS9PzVdN2DWlamm5bofNbJ01L0/NV03YNaVqabluh81snTUvT81XTdg1pWppuW6Hz
WydNS9PzVdN2DWlamm5bofNbJ01L0/NV03YNaVqabluh81snTUvT81XTdg1pWppuW6HzWydN
S9PzVdN2DWlamm5bofNbJ01L0/NV03YNaVqabluh81snTUvT81XTdg1pWppuW6HzWydNS9Pz
VdN2DWlamm5bofNbJ01L0/NV03YNaVqabluh81snTUvT81XTdg1pWppuW6HzWydNS9PzVdN2
DWlamm5bofNbJ01L0/NV03YNaVqabluh81snTUvT81XTdg1pWppuW6HzWydNS9PzVdN2DWla
mm5bofNbJ01L0/NV03YNaVqabluh81snTUvT81XTdg1pWppuW6HzWydNS9PzVdN2DWlamm5b
ofNbJ01L0/NV03YNaVqabluh81snTUvT81XTdg1pWppuW6HzWydNS9PzVdN2DWlamm5bofNb
J01L0/NV03YNaVqabluh81snTUvT81XTdg1pWppuW6HzWydNS9PzVdN2DWlamm5bofNbJ01L
0/NV03YNaVqabluh81snTUvT81XTdg1pWppuW6HzWydNS9PzVdN2DWlamm5bofNbJ01L0/NV
03YNaVqabluh81snTUvT81XTdg1pWppuW6HzWydNS9PzVdN2DWlamm5bofNbJ01L0/NV03YN
aVqabluh81snTUvT81XTdg1pWppuW6HzWydNS9PzVdN2DWlamm5bofNbJ01L0/NV03YNaVqa
bluh81snTUvT81XTdg1pWppuW6HzWydNS9PzVdN2DWlamm5bofNbJ01L0/NV03YNaVqabluh
81snTUvT81XTdg1pWppuW6HzWydNS9PzVdN2DWlamm5bofNbJ01L0/NV03YNaVqabluh81sn
TUvT81XTdg1pWppuW6HzWydNS9PzVdN2DWlamm5bofNbJ01L0/NV03YNaVqabluh81snTUvT
81XTdg1pWppuW6HzWydNS9PzVdN2DWlamm5bofNbJ01L0/NV03YNaVqabluh81snTUvT81XT
dg1pWppuW6HzWydNS9PzVdN2DWlamm5bofNbJ01L0/NV03YNaVqabluh81snTUvT81XTdg1p
WppuW6HzWydNS9PzVdN2DWlamm5bofNbJ01L0/NV03YNaVqabluh81snTUvT81XTdg1pWppu
W6HzWydNS9PzVdN2DWlamm5bofNbJ01L0/NV03YNaVqabluh81snTUvT81XTdg1pWppuW6Hz
WydNS9PzVdN2DWlamm5bofNbJ01L0/NV03YNaVqabluh81snTUvT81XTdg1pWppuW6HzWydN
S9PzVdN2DWlamm5bofNbJ01L0/NV03YNaVqabluh81snTUvT81XTdg1pWppuW6HzWydNS9Pz
VdN2DWlamm5bofNbJ01L0/NV03YNaVqabluh81snTUvT81XTdg1pWppuW6HzWydNS9PzVdN2
DWlamm5bofNbJ01L0/NV03YNaVqabluh81snTUvT81XTdg1pWppuW6HzWydNS9PzVdN2DWla
mm5bofNbJ01L0/NV03YNaVqabluh81snTUvT81XTdg1pWppuW6HzWydNS9PzVdN2DWlamm5b
ofNbJ01L0/NV03YNaVqabluh81snTUvT81XTdg1pWppuW6HzWydNS9PzVdN2DWlamm5bofNb
J01L0/NV03YNaVqabluh81snTUvT81XTdg1pWppuW6HzWydNS9PzVdN2DWlamm5bofNbJ01L
0/NV03YNaVqabluh81snTUvT81XTdg1pWppuW6HzWydNS9PzVdN2DWlamm5bofNbJ01L0/NV
03YNaVqabluh81snTUvT81XTdg1pWppuW6HzWydNS9PzVdN2DWlamm5bofNbJ01L0/NV03YN
aVqabluh81snTUvT81XTdg1pWppuW6HzWydNS9PzVdN2DWlamm5bofNbJ01L0/NV03YNaVqa
bluh81snTUvT81XTdg1pWppuW6HzWydNS9PzVdN2DWlamm5bofNbJ01L0/NV03YNaVqabluh
81snTUvT81XTdg1pWppuW6HzWydNS9PzVdN2DWlamm5bofNbJ01L0/NV03YNaVqabluh81sn
TUvT81XTdg1pWppuW6HzWydNS9PzVdN2DWlamm5bofNbJ01L0/NV03YNaVqabluh81snTUvT
81XTdg1pWppuW6HzWydNS9PzVdN2DWlamm5bofNbJ01L0/NV03YNaVqabluh81snTUvT81XT
dg1pWppuW6HzWydNS9PzVdN2DWlamm5bofNbJ01L0/NV03YNaVqabluh81snTUvT81XTdg1p
WppuW6HzWydNS9PzVdN2DWlamm5bofNbJ01L0/NV03YNaVqabluh81snTUvT81XTdg1pWppu
W6HzWydNS9PzVdN2DWlamm5bofNbJ01L0/NV03YNaVqabluh81snTUvT81XTdg1pWppuW6Hz
WydNS9PzVdN2DWlamm5bofNbJ01L0/NV03YNaVqabluh81snTUvT81XTdg1pWppuW6HzWydN
S9PzVdN2DWlamm5bofNbJ01L0/NV03YNaVqabluh81snTUvT81XTdg1pWppuW6HzWydNS9Pz
VdN2DWlamm5bofNbJ01L0/NV03YNaVqabluh81snTUvT81XTdg1pWppuW6HzWydNS9PzVdN2
DWlamm5bofNbJ01L0/NV03YNaVqabluh81snTUvT81XTdg1pWppuW6HzWydNS9PzVdN2DWla
mm5bofNbJ01L0/NV03YNaVqabluh81snTUvT81XTdg1pWppuW6HzWydNS9PzVdN2DWlamm5b
ofNbJ01L0/NV03YNaVqabluh81snTUvT81XTdg1pWppuW6HzWydNS9PzVdN2DWlamm5bofNb
J01L0/NV03YNaVqabluh81snTUvT81XTdg1pWppuW6HzWydNS9PzVdN2DWlamm5bofNbJ01L
0/NV03YNaVqabluh81snTUvT81XTdg1pWppuW6HzWydNS9PzVdN2DWlamm5bofNbJ01L0/NV
03YNaVqabluh81snTUvT81XTdg1pWppuW6HzWydNS9PzVdN2DWlamm5bofNbJ01L0/NV03YN
aVqabluh81snTUvT81XTdg1pWppuW6HzWydNS9PzVdN2DWlamm5bofNbJ01L0/NV03YNaVqa
bluh81snTUvT81XTdg1pWppuW6HzWydNS9PzVdN2DWlamm5bofNbJ01L0/NV03YNaVqabluh
81snTUvT81XTdg1pWppuW6HzWydNS9PzVdN2DWlamm5boXtp3SWXXPzZqy4ecMFZj3/yWedc
40R/8jVONDA/8KelpenZnc56xllnP+3JZ5//pLPOecxZ5518l/Mee+b558OBqNPufPJp97/f
yfe4/8mnP2jngQ/E07ufCrcxxvcZTx543tPOOvnc8846/6wnP/qsR15w1vkXwHnqmRc87Ul4
tKa8xBF+8nfLVhrFWtU/lXfOOefssx513plPe/Tjzj/7nK887pwzn3TuWdc4MVpWfiaNP0wX
Ax8uW386nuOvS2Rmy/mUv6Kbn04P4xEGWIQlGOPKy9jSGIZaxloGW0ZbhlvGW1awrOF4aFeO
zRqONRxrONZwrOFYw7GGYw3PGp41fGkOa3jW8KzhWcOzhmcNzxo9a/Ss0bNGX94Ba/Ss0bNG
zxo9a5RvKrBGYI3AGoE1AmsE1gisEVgjsEbgaxSpDKwxsMbAGgNrDKwxsMbAGgNrDKwR+RqR
NSJrRNaIrFG+m8gakTUia0TWKCJMrJFYI7FGYo3E10iskVgjsUZijczXyKyRWSOzRmaNzBqZ
NTJrZNYo3/QkQ9axhpWsYS1rWM0a1rOGFa1hTWtY1Rq+mq1ff6lrS91RAaMERg2MIhhVMMqg
6MAWIdiiBOtK3aIFW8RgixpskYMterBFELYowhZJ2KIJW0RhfWlzkYUturBFGLYowxZp2KIN
W8RhizpskYct+rB9eb9FIbZIxBaN2CISW1Rii0xs0YktQrFFKbZIxRat2CIWW9Rii1xs0Ysd
zy1FMbZIxhbN2CIaW1Rji2xs0Y0twrFFObZIxxbt2CIeW9Rji3xs0Y8tArJFQbZIyBYN1TNZ
UZEtMrJFR7YIyRYl2SIlW7Rki5hsUZMtcrJFT7YIyhZF2SIpWzRli6hsUZUtsrJFV66c2Jyh
NlzRlSu6ckVXrujKFV25oitXdOWKrlzRlSvnFVd05YquXNGVK7pyRVeu6MoVXbnx/DKeYOoZ
hrpy4zlmPMmMZ5nxNDOeZ8YTTdGVK7pyRVeu6MoVXbmiK1d05YquXNGVK7pyRVeu6MoVXbmi
K1d05YquXNGVK7pyRVeu6MoVXbmiK1d05YquXNGVK7pyRVeu6MoVXbmiK1d05YquXNGVK7py
RVeu6MoVXbmiK1d05YquXNGVK7pyRVeu6MoVXbmiK1d05YquXNGVK7pyRVeunJxc0ZUrunJF
V67oyhVduaIrV3Tliq5c0ZUrunJFV67oyhVduaIrV3Tliq5c0ZUrunJFV77oyhdd+aIrX3Tl
i6580ZUvuvJFV77oyhdd+aIrX3Tli6580ZUvuvJFV77oyhdd+aIrX3Tli6580ZUv5ytfdOWL
rnzRlS+68kVXvujKjwQbETYyrEKM5ys/Ymzk2AiykWQjyoqufNGVL7ryRVe+6MoXXfmiK190
5YuufNHV2P/wRVe+6MoXXfmiK1905YuufNGVL7ryRVe+6IogKX+7bCeMZ8dCNjwW5uCxMKAE
FgKUk3g5D5dTaSFHAUfhRsEGa6gHgE+Qn5V6APgQ1APY9x6A62pvCo9A/WBAfT92Dvir2A9D
RvdhGHt5cA1DshZw6+PYHYIr5oyeVkA/aOwnwZWHmHE2znmqh5NmH4celAtj18x1OG/lHPyA
vsXYY4QrGp9iHDzOReNpo+sNeBRjNnnserqu9ynHgKqDGfuhcMWMVgS0wozdS9cFwDg68MXk
secEF8qAJ3oZY8/JdQPoim5UYDPKyQmuhP4ETuXGjEy3rou9x7s2Ce9o7Py5LpkcQXXUHca+
FVzJ9Ois4ti1m+S6HAI+TZyNcfhynvOdwfuNMaLHOiLL+g4qD2B0RL+n9ks7dGxMMCHHVN+i
70CsjL4nuh61v+nx0WRQsbdoxdgN811AxxEfhInAaDnHerzH7KOP0eCNlc/U4w2lPg+oaMY+
FRqRos8J3DO5H7vyY4+Xf4SXPkPNaMIAGOIVx28WrUD78YWlnMcOCA5mYkigf8SXMfY/8Rni
zfT4gKKtnW98aQO+HgMOhTz20F1nEySBT61HX6O8rO2gPnzXBm+/H7ML2w0QF5IPyM2MX62F
JvCh410HfDrlTdoOncYQ8MaB/bE7a7qco8GHP8QwfhJIfSEOfEeGAhrzmA5SD2mI6CfXrqzp
enSekHtA9GnMCgz+NPDy6PHi4x6786bDt4HuYcp2GLOk3OGDx2vjqx4g6pKC4QXRcLQ1g8jl
LeZuCGZIPfoHJqUC94yvMQ7oFuKzQTQ/iNx5vGV89jECxKUrl/GHZ3p8aVQ5dF2ikGfEnPDn
GfpQ/qhyB81CNfgu8Jvy2aQu4/NFruM9PpvSCUwdGpDQqaOcQ+nBJKiEXxki+Rb54SR88gZ9
VuMjPtrSK0v4o8IffkBL8G2WLlHq8Mmgb4mDJaQrfNtw4c8fXwW6G/j74F9awp8/mgjh5x7f
xnh4NADnEfwtQIOlS5LwLWacDopQIeBSEaLCMTK+MROrC3+bBmeuPiScmvhJJPyhod+ScJrC
n0vpNMYO7UGPDH9SkH3pa8LFPyd82RnnmNJNjvg7xukAXwSEOJ454ML7wUkuQgZQBQ4Pl8GX
XT6rjPjiwukNfxvoL+KLLF1E9n5k7X4GOLULfoKf4Cf4rQJ+JfMV/AS/tYC+4KfMD8md4Cf4
rSf8mIchzbuCzI+J5Z4yP2aRyvw2NIMV/AQ/wU/Dnhr21LDnWmRrqxxGFvwEP8FP8FsR/NZn
2HO8TKdLfhua1O2GkWKf2Cf2iX1bxz7Nd2l3HspuwLWKGMFP8BP8BD/B7/Cjnrrkt8GZoeAn
+Al+Ww2/cZHBalY6HPyo5+7mu4wM00oHZXvLGaPgJ/gJflsNv3FV3GrgV24p0+BKhz1P9hwr
apnfRs6FEfwEP8FP8FvRsKfgpzXu65NdCn6Cn+An+Al+h7/mp8xP1/x0dzPd3awwUnc3K7fp
1N3N1uvuZhr2XL7WpedjdqrMT5mfMj9lfmub+e3zhBfN9lTmp8xPmZ8yP93XWve11n2t1+ea
3hVluMr8lPkp81Pmt7aZ37jPwxXd2lNLHa4IBNv4e8FP8BP8BL8Nh5+u+W0j3K7oPQt+gp/g
J/gJfprtuZFr+S4PgIKf4Cf4CX4rgt/B3+FFw56bcw3u8kC1H78T/AQ/wW+r4cchQW3kro3c
tw+igp/gJ/htNfz2fHuzvlAzxGD7EE0/OGcP/g4v+7zU4TCL3JlrYntb45yPQ3AupzBujxSH
Pgy6w8v6QFTwE/wEP8FvRcOegp/gJ/jlIWZvTM6GfScg1tvYo2vk+iF49tbo6m3OwQ82RcO+
E13R+BQj+k9fi+qNw5BEzCYbPwb1PuUYUHUwhr1P1OtjdjEH652x1RWcH6JzPPZQ2xBQdgEx
/VBfb3BB8MMn6LsUfU7eOpN7wys348dYPstLf/hOd3jRHV5642Narzu8rHKpgzK//bj+djSO
CXA4KqM82oRFrDYFHysbXIj9MGQbtchdi9wLIwU/wa8p+B38sCdfUcOeRwNWq35NwU+ZnzI/
DXuuaNhTsz017KlhTw17MpnOISCP9n2Pwd0ylug7g2HeGKN1yeWSX/vOOhscvM4gjFm47xzG
H4MJOaY6sus7b2K2mFXgne1rxd5kl/ve2iHnMpTsu2AH5O3BRJdNyeh9N7jso0fKlpytUbFP
fR5Q0WCYc3xFDXu68tmbbjBDSEO0uJFVLiO+puvdgG8Ew+343JT5NZX58etIne7wsuqsaBuO
p8xPmZ8yP2V+K8r8Dn7Cy+7gx35N7JZ3cmefDx52JdHRyVrpsD4J26q4LPaJfWKf2Ld17EuC
39bd0OVQaAp+gp/gJ/gJfrq72dbBUPAT/AQ/wU/wE/wEP610wLQQjysBxjhf14DE3g9a6VAY
qZUOmu9yOfNdNNlTkz3X59qhMj9lfsr8lPmtKPM7ePgd/DI/9n60zO/Q62frWBb8BD/BT/Bb
EfzWZ7KnJrysT4a2X2AV/AQ/wU/w23D4rfLuZrrBy37B6KCPK/gJfoKf4Cf4acKLJrxowosm
vJR70Vx6N+tLn+m+1rrBi+svZ8KLhj014WV9hlOV+SnzU+anzG9Fmd/BT3jZ6w1edM1vfSC1
X8Ohgp/gJ/gJfiuC38Fnfrub7XnZu5vtHX6a7blfMDro4wp+gp/gJ/itLfx2l/mtcsKL4HfQ
kNqv1xP8BD/BT/AT/DThRRNeNOFFE1404UU7GmGboNjn2BsXrY8hcuAwddjTei0nvKwy89NS
h/3KxA76uMr8lPkp81Pmt6LMTxNeNNtzfSbSCH6Cn+An+K0Ifgc/4WV31/xWOeFFmd9BZ2j7
9XqCn+An+Al+Gw6/VQ57asLLfsHooI8r+Al+gp/gJ/hpwosmvGjCiya8aMKLJrxs1oSXVQ57
KvM76Axtv15PmZ8yP2V+yvyU+SnzU+anzE+ZnzI/ZX57y/w021OzPTXbMw8xe2NyNhxxQH7p
bezj0Lt+CJ7zpejqbc7BDzZFk6srGp9iHLz/WhRWGg05xmyy8WNQ71OOAVUHY8pNl13Xx+xi
DtY7Y6srOD9E53jsobYhoOwCYvqhvt7ggjI/ZX7K/JT5KfNT5qfMT5mfMj9lfnvL/Fpd6qDZ
nvt13Wydj6trfsr8lPkp89vwzG+VE160zm+dgbfcdsFP8BP8BL8Nh98qMz/Bbxkg6/xc8BP8
BD/Bb0Xw04QXTXjRhBdNeOGUnhxCCt73Pab1lAtpvjOY4BNjtC65XGbd+M46Gxy8ziCMc3p8
5ywKJuSY6pwe33kTs+0H553ta8XeZJf73toh5zKJyHfBDh4zf0x02bC7i2MNLvvoYzS4mFmj
Yp/6PKCiceNUI9+l6HPyeNncG13z0zW/vV3zaxV+q8z8tM5vnbO95bYr81Pmp8xPmd+KMr9W
J7ys8pqf4LcMkHV+LvgJfoKf4Le28ONYRupMygbz1PuQrPNM8+DCcqmYUh8xUJIFv3WG1H61
XfAT/AQ/wW9F8Gt12HOV8NOEl/2C0UEfV/AT/AQ/wW9F8NuGYU/B76AhtV+vJ/gJfoKf4Lfh
8FvlhBfBb79gdNDHFfwEP8FP8BP8dHsz3d5MtzfT7c201EFLHfa21EHDnlrnp3V+WuendX42
4i7jsaw2dB3uRB5709to7biYEXcjH3DfceO5ntHXe5bbhHudY3Vk76IvNyi3Xba8ibnBMsfe
8NxqbTfgrunWhB5LEsd7ltuu9zYlrG4MWAXJcSlEOZNCwAJHb0IqxzJdztFgkeUQw7ji0XQR
dz3HWkzDO6OXNZamGww8Q7QRban1ejdg5SVuqI71kZzpbk3n+PI2eyyrDKWzYDqsunRoRraD
Lfdgzx0WWOK1saRzwN3auTgz4wXRcLQ1+358i7kbghlS791gUvJ8ixnLNePgsDo0GESzEbnz
eMsmDDF6tI6NyJ2LpsfiTN6+HTdsLy6Lt5yT8yn0oSzhzB1u447Vofgu8Jvy2aQu4/O1PeZD
4rMZxsmRaEBy+KSHOATHw6cu9vzKEMm3yA8n4ZM3rkfFiI828ztLXcCH2Qe0BN+mbRV+GvY8
6CHFdXg9DXtq2FPDnoKfhj017KlhTw17athTw57K/PaW+Wmpg4Y9NeypYU8Ne2rYU8OeGKAu
g6MY7+4xAu0xRDrU8VLe9c/gvn65xyD0OKqKcVePkesBQ7IxjGOvuN8etvcs9+HD/fnKsTCW
jmNkDFSbWF3zF7mzWRHj0hgmxxB3xpahQ53GmUIOGH7G8Pu4EWhEVuzwPnLE4DfGwkvFZDDE
XUaIM+KLC7uVBmxEiuOZZNkLWIeRv21uo0Y9NeqpUU+Nem74qKfWuG8z5I703gU/wU/wE/y2
Dn5K/LY+MRX7xD6xT+zbcPZprueRkp9t9gt+gp/gJ/gJfrrkt3WZoOAn+Al+gt/awo+zT654
Twdlftuc4R3pvQt+gp/gJ/itCH5a6KDJnuszyVXwE/wEP8FP8NOwp4Y9tcRdS9y1xF1L3Ddr
ifsqhz251BAr/7TMb+1hqcxPmZ8yP2V+K8r8dGdPDXtq2FP3d9H9XXR/l627v0ur1/xWmfnp
Bi9HmkCybn5lfsr8lPkp89vwzE83eFk3MB1EewU/wU/wE/wEP014WftreHOBKfgJfoKf4Lfh
8NOw51wwbEO84Cf4CX6Cn+CnzE+Zn5Y6aKmDljpoqcNmLXXY8zW/MWXUjkYbCUZlfsr8lPkp
81vbzG93tzfbM/zGioKf4MfZ+24YkrXOpz727BbRhW0eLbagtH3u++rSUgctddBSh61b6tDq
Oj/Bbxuu4c19j8r8lPkp81Pmt7aZ37i1+/x93JP289vIbG4OAAU/wU/wE/wEP0142ToYCn6C
n+C31fDjkGBaEfwO/g4vu7vmp6UOczKibYkV/AQ/wW+r4UcwrC/8djfsuWf4jRU14WUjs0LB
T/AT/AS/tc389hl+mu2JrtGmZoKCn+An+Al+Wwc/zXfZWKbtltVin9gn9ol9K2Jfqysd9jzq
qcRPid8wGMqAqNQyP34MyeToeoJziPWTScn01rl+yDbxJICoHEIK3vd98EO5a4rvjB9sjNG6
5DI7n9Z31tng4HUGYaPLWRRMyDEZU1ZO+s6bmG0/OO+wnHKM6k12WFlp0YrM6/44VrCDjzmY
6LLhXzxcg8NqMx+jwZ1ralTsU58HVDTO1GOl6HPyeNncG93gRTd4WZcbvOxuvsvIsJywGrnH
nxRkv8uVDrrkh5PIbjOpdYtT5qfMryBS8HOl42E69POC4Lcu8NMlv82F037DVPAT/AQ/DXtq
2FPL/DY2wzsSRAU/wU/wE/xWBL+DX+anzE+Z35HgdkV+wU/wE/wEv7WFn675CX5XBLkj/V7w
E/wEP8FvRfDTbE/vMSvNJMsc+EgnXfnb+GwEP8FP8BP8VgS/9Rn21DK/rWez2Cf2iX1i39ax
b5crHcYlErq52UaCUvAT/AQ/wU/w02TPjQTc5Y0wC36Cn+An+K0Ifgd/yU/zXdq4fHZ5kGn1
d4Kf4Cf4CX5rC7/drXTY8w1eNOy5wfN2BD/BT/AT/DYcfrq1Z6vZ19Fsl+An+Al+Ww0/Jjer
2s3v4Ic9lflp2HOvABX8BD/Bb6vhx6xI8Bs04UUTXozFNgSx3OkfOziE2A/YpCBqU4ch4T7w
3vTsJ6PHoE0d8rjNh++wkwV2kvApZ8iFnw52roghOazzNbaPZWsJ10XsUNFj14to7bhzheuw
Q4VLxnPzCu/Hj9UmmzO2wuhd9GUzC9tBfSFngz0telP2yrDdMGB/CxN67D8xlO/Ddr3HThrY
yiJgy4uyc4XtcOP+ELCbhTchlWOZLudosKPGEMO4vYXpYh5wF2vBb22HPXc34WXPw55jRS11
2EgwKvNT5qfMT/BbW/jtbthzz/DThBf0Svc6rNh6PcFP8BP8BD/BT8OeGwu5I0FY8BP8BD/B
b8PhNyZwe9jLVpmfMj9d89M1v8JI7AcfBm8Dto7XNb/eZj/4OF7pNJ3JzuHSY7aDNbyGmbuM
X+J6UXJDiuU6esZFRlysxPXJ7PvxsmbuhmCG1HuH2yEnz8uauQu4zO76gOuhiOYFy9x5XObE
Zx+jx067HOzLnYumz8lHXDp1jiN7ubO4zJmT8yn0wfDKfe5wnXpwHtdf8ZtyPTR1GddUbW+8
x/XQgRU3fcKLhj2PlP1ss1+ZnzI/ZX7K/NY289vnCS/K/NA12lRACn6Cn+An+K0Ifq1u6qBh
z00F2DfyvgQ/wU/wE/xWBL+DX+R+8Jkfh5wj1jphjDsOwbmcwrg9Uhx6XBLQdn5rkykKfoKf
4Cf4CX67nu0p+H0j2VZLdQU/wU/wE/zWFn4Hv85P8GsJYN9IWwQ/wW8r4VemQlrd4mXtp3se
/LgnX1Hjnt8IdVqpK/qJfltJP57CBL9Vr3VodcaL1jq0ApyW2iH4CX6Cn8Y9Ne6564t+yvxa
Atg30hbBT/AT/AS/DYef1jp8I5DY1LqCn+An+Al+aws/XfPb3FXo+w1dwU/wE/wEv7WF3+6m
eyrz22+QrOPxBT/BT/AT/FYEv4Of8LK7zE/wW0c47XebBT/BT/AT/FYEv4O/xYsyPw177hWS
gp/gJ/htNfyYFa1qW4eDz/z2Cr/xlmTZO9sP0eZh15M9tch9r6xprZ7YJ/aJfVvNvm3Y0mjP
o57j+kBsSzXEnKMbXExa6dAaxPbaHsFP8BP8BL8NH/XUGve9AmKT6wl+gp/gJ/itCH6tjnpe
Fn57HvVU4rcpPBT7xD6xT+zbOvYlwW9tdh7aL9gKfoKf4Cf4bTj89nzJb6yoS34bCUrBT/AT
/AS/FcFvGxY6aLLnfmViB31cwU/wE/wEvw2H32Uv+e192FPwO2hI7dfrCX6Cn+An+K0Ifusz
30Xw09J4wU/wE/wEvxXBr9Vhz1VmfprtuV+Z2EEfV/AT/AQ/wU/w2/UNXgS/g4bUfr2e4Cf4
CX6C39rCjyhKnUnZGJv6kKzzTPPg8j7ElPpo+5w123O/ALLOxxX8BD/BT/BbW/jt7s6eqxz2
1ISXdQbectsFP8FP8BP8BD8Ne27kWr5l2B36XPAT/AQ/wW/D4bfKYU9lfodCZF3Lgp/gJ/gJ
fhsOv1UOe2rCy7rC7tB2C36Cn+C31fBjVrR9u/ntfZ2f4HcoRNa1LPgJfoLfVsNvnByZep9c
DHmIQ3DjLJLY59gbF62PIY6IHAbj+t74mELIvlAzxGD7EE0/OGcPfpG7Zntqsfpe4Sv4CX6C
31bDb5WZ3/osct/zpg665LdX1rRWT+wT+8S+rWbfKhO/Vtm3yvkuGvVsDWJ7bY/gJ/gJfoLf
1s13UeK3dQsbDmWk2Cf2iX1i39axT9NddKVQ8BP8BD/Bb0XwO/jpLuPMnCu6uZkWOhya9aiM
057rHJVRHm3CXC6bgo8cEyiu2A9DthF+jprTNQzJ4vZ5uGVeP1WMOVvvMOUr932Nwpyx7I3J
earnbezj0Lt+CJ6D5jiU723OwQ82RVNf0EfjU4wD7so3RWG22ZBjzCYbTi5DPcxKy5iVlsNg
TH29PmYXc0ArjK2u4PwQneOxh9r2gLILiOmH+nqDC4IfPlTfpehz8taZ3BuewsaPsXyWl/7w
XYwmDN6GYfpmfddbZ/GFpZxdKDV9Z2JILtmILyNWkeALw8TB3kZrff06ODswGR8Mpg3Wr9Ym
SCKH0Lvoy8vaDurDd228QXVeUbK2GyAuawLkZsav1kITNiUTXXC2L/KynTOYkBh99CakcizT
5RxNhLwwPbEEmS5CHCEJfiuCX6uX/AQ/we6ymW4h3MgU0Evwc92QnPXeWWPGG+TiE4q9B/LR
u/TA5vhhJZOj6wlOzAyvroRzuwPdM87DowuncXQlfN8D8RMXAHucf61LLhcC+w7wCA5eZxDG
ir5zoBChEFPlu+9w9s8WvEDT+lqxN9mhv2HRilxO5r4L4BB6AcBANgU7vhtcBgFALbyxGhX7
1OcBFQ1gN76i4OfKZ2869PNCGqKNAHGFZu8GfCPodOFzY6phDbqMYK/NHh/3iHzT4dtwYHC2
gy39tNzhgwd48VUP6NHxg86gLagNgWTfj3zP3RDMgHUGbjApeSon42uMg4NqgkE0G5E7D96j
4xGjR+vYiNw5LC9Aj4VdPHTqisuC9zmhbxr6UL7a3EGzUA06IvhN6RikLqNzYbFewaNjMLDi
qlb5tQo/frWxywm94x5/UpC9hj0vC4NtA6Tgp8yv4FbwE/y+8VV+rcJPmd+2gW0371fwE/wE
Pw17bviwpzK/3cBg22IEP8FP8BP8Nhx+yvy2DWy7eb+Cn+An+Al+gp82NNq6dX+Cn+An+Al+
aws/TuHax33cx5QRk5YwwRhT3AaHaVBl8kwymN1U7oKaU+BcpthhMjtmQnvMSjOY6QzXbrIP
xRy9z0nwE/wEP8FvRfDjKT91mAfrBtzuGrMrwYzRhZVOmHPssR5qqPfD5iRog2nOucfCE16U
S5i+ioVInPmM5TZhXMGH6chY+VSmJWO6conC+hkcI2N1kxlRdMXwW+WwJxsRO8Hv6EFrVR0G
wU/wE/wEvxXBT7M9lfmtDxQFP8FP8BP8Nhx+mu25qmxpk44j+Al+gp/gt+HwW+Wwp675bQoA
BT/BT/AT/AQ/zfbcugk6gp/gJ/gJfhsOv8sOe44TNDNvFohb2WXcPnioKR0mbwbcZg73mB1v
CozJLZrsuSnJ3vL7EPvEPrFP7Ntw9mnUc/mkr+fjnBzBT/AT/AS/FcHv4Fc6jIsftKORgDZ/
kqngJ/gJfoKf4KdhT13y03Z+2tGobL5UNvM55Ie289OORq7HVkgROyXWpepYy277gL2VsDmj
1TI/LfObn4EdraxVmZ8yP2V+yvw2PPNb4XwX3d/laLFq1a8r9ol9Yp/YtyL2HXzit7s7e65y
vovgt2oIHa3jCX6C31bCb9y/3mBf9QHbtot+a0s/TXhZn2HGo0W5I72u6Cf6bSX9mDJYwc+E
gWlRWlv4HXzqV1cDalOHtZ8gI/gJfoKfMr+1hd/uMr/LXvNLWuS+9vA6Uka3W7/gJ/gJfoLf
hsNvlRf9lPntFi6txwl+gp/gJ/gJflrnt3WZoOAn+Al+gp/gJ/gJflrkrkXuWuSecK9jbBKe
yyJ/0+G+xs663qdei9y3a5H7OF6qG1tvJBiV+SnzU+anzG9tM7/dzfbUhJfWr78djfYJfoKf
4Cf4rS38djfbUxNejgZcWn9NwU/wE/wEvxXBr9VdHZT5tQ6io9E+wU/wE/wEvxXB7+Dvb7a7
zE/wOxpwaf01BT/BT/AT/FYEv4PP/HZ3zU/Dnq2D6Gi0T/AT/AQ/wW9t4be7zE/wOxpwaf01
BT/BT/AT/AQ/rfPbyOUMlwdgwU/wE/wEvxXBr9VrfqvM/Jhrxi7pxtZrD0vBT/AT/AQ/wU+Z
39rD7PKyvMP9TvAT/AQ/wW9F8Gt1wsueZ3uOKaPu8LKRYBT8BD/BT/BbW/hpwos2sz1cVrcb
n+An+Al+gt+K4LcN1/y0pdFuwLIOMYKf4Cf4CX4rgt/BD3sq81Pmt1fQCn6Cn+An+K0t/Ha3
yH3P1/zGirrmp2t+JxKVw5CsddjdJfa8GkxXzNl6F2yf+7IHDFx5iNkbk7OhfBDkbezj0Lt+
CJ6Cpau3OQc/2BRNrq5ofIpx8P5rUb1xQ44xm2z8GIStZXIMqDoYU1+vjxmtCGiFsdUVnB+i
czz2UNsQUHYBMf1QX29wQfAT/AS/tYWfMj9lfsr8BL8Tre+CHTx6ASa6bErfxHeDyz76GA02
KizdDt9F7EuXh95a48Zuh+9S9Dl5i3JvOHg19iFKR+LSH6gZTRi8DcPUrfFdbx1eFB2S7EKp
6TsTQ3LJRvREYu0hobcSe9PbaK2vfZF+QN/E+GBC9rVfY7GHHno1oXfRl5e1Xbbs6BhvUJ2X
lKztBvSsrAnoa5mxX2O73tuU8K6Ds315k7ZzJoWAN+5NSOVYpss5moi+VQzjJ2G6iJ5RSILf
1sGPvd/YZQ+9YO/GjP71QN1gAV8KOSTKOY+9ZriwnyM6+BG7OmKTxzFKy/zWPhlk3jblb8Gm
YdBettrLVuzTXrYnJvSQ2F1x0foYIvsrCb0Os1172fJtC374EPaaXLVcT/DTqKdGPZX4bV3i
l3aX+TExEPwEP3wCRKUu+fFjSAaDID3BOZROMV0Jg3oO1zQzBuDGDwvjdyl43/e4sDkNCOIS
JwberEsul+uOvsOoYXDwOoMwVvSdw/AjRwNjqlc1fYdhv4wRGsdxmlqxN9nhKqtFK3Idz9So
p0Y9c8IV+dCHMqCdO1zghmowAh1iLiPCqcsYVba98R4jwgPP72lF8Dv4lQ7UfepMygZjVn1I
mI0wviG8uxATZibgzyWPCVxOmBPQ408Kg/2C32Zmc3MyTWV+yvyU+SnzW1v47XW+y+4Sv8OM
evIFkQvqkt/aj4SKfWKf2Cf2bR37dpn4HQZ+mu8yJ7lqOVbwE/wEP8Fvw+G351FPwQ95bssA
+0baJvgJfoKf4Cf4aaXDxkLuSIAU/AQ/wU/wWxH8OKkrdVh+6YaAxZnJYnXc6MIdLrDg0uM+
GEPmks6EO1xgSg4meuUeay6ZYSXcLAM3oODcL6w0DePFPCw7xR0vynJULFMtUVg6imNk3NXC
xOrSfJcjneDlP3LmKvgJfoKf4Lci+B38ZM+9znfRNb8jQ2FbgCn4CX6Cn+C3Ivi1mvmNq/X2
sNLhMNf8NNtzU+Ao+Al+gp/gtyL4tZr5acLLpgBrle9D8BP8BD/Bb8Pht8rMT0sdVgmgo3ks
wU/wE/wEvxXBbxuGPQW/owmsVb624Cf4CX6C34bDT8Oeq4TGphxL8BP8BD/Bb8Pht8phT014
Efy0la3ua12wqd38yi3LTYe7jDtsKpjtYMuuyxmbxWFbwx63MB+wPzMXvGVsH4htCHHj8+z7
ccPC3A3BDKn3bjAJu8iVqGDj4HA39GAQza0Ic+exgSHuQh2jD2ngCThjWZzpsQUjN2zGFs3F
ZbGBoe5rXW51vXxfa8FvU4C1yvehzE+ZnzI/ZX5rm/nt86YOh1nqoGt+qwTQ0TyW4Cf4CX6C
34rgd/BLHXYHv1VmfoLf0QTWKl9b8BP8BD/Bb23hpzu86E4tewWi4Cf4CX6Cn+CnG1vrxtbY
Djn4cnG+cDFiF+iMq++D4eg3XdrIXRu524Ct40dF+E4TXjThJWDqzeCcPfhhz91lflrqsNfs
aJPrKfNT5qfMT5mfMj9lfsr8lPklZ713mFfuPK+To3uA3ViQ72LbFI/+7ehK2GlFSx0KNpX5
KfNT5ndi7OLQh8F7bNpkkqUmNjlr2oT3psxPmZ8yP2V+K8r8eMrfqP38tNRhgyEu+Al+gp/g
tyL4tXrNT0sdNiFTW/V7EPwEP8FP8BP8dM1v64ZpBT/BT/AT/DYcfprtueqsaROOJ/gJfoKf
4Lfh8NOw5ybAatXvQfAT/AQ/wU/w07Cnhj211EFLHcrUfe4lYA/54bsYsbOA1yL3zoU+9zb7
ARs3aKnD0VvqoHt7aknFXjNCZX7K/JT5KfNbUeanpQ5a57c+MBb8BD/BT/BbEfwOfqnD7jI/
TXjZa3a0yfUEP8FP8BP81hZ+B39vT75i7JLBzsVxCM7lFLhPse7wsnbXDAU/wU/wE/w2HH6r
nO0p+G1KNij4CX6Cn+An+Gm259plbt8ohAU/wU/wE/xWBD9NeNGEF014yUPEHghm2vXNdd7G
Hrc9d/0QPC9Sg7oeU8Vz8INN0XDUnK5ofIoR90b/WlRv3JBjzCYbPwb1PuUYUHUwpszFd10f
s4s5WO/MOD3fdcH5ITrHYw91K4aAsguI6Yf6eoMLgp/gt9Xw4x9HWhH8Dn7Cy+6u+a1y2JNn
L13z+0azrhbqK/MT/AS/rYYfwSD4oYM9VKxhAktI6GDjX+k2g3S9Q2cem5gNLiZd82sBXKto
g+An+Al+gp8yv13DT5nfKsDTwjEEP8FP8BP8Nhx+q1znp8yvBXCtog2Cn+An+Al+aws/5mGp
Mykb3JixD8k6P47jGswbiCn10fYYvizX6XLCpIA+GWMcKowu77DzerT5CMOe48VCDXtu5ExQ
wU/wE/wEv7WF3+4mvOwZfmNFwU/w43xMNwzJonuFLlXPbhFduBaMLlVAF6uvsy+dZnvyk8kh
pOB932NOa7n7se8MZrfGGK1LLpcpp76zzgYHrzMI40fqO2dRMCFHdFPLR+o7b2JGJ9Wxq1or
9iY7fOTWDvgCxorB4k7LOZjosilfj+8Gl330uCM17thdo2Kf+jygIrrA9Vgp+pw8Xjb3pjT1
kHta11boxtY821qjG1uHzMnXqQsRf/jTja0PfqnDPmd+h4EfX1GzPVcx7Hi0j6HMT5mfMj9l
fhue+Y2jl3sY9jwM/HTN72hDa1WvL/gJfoKf4Lfh8BsZthr4KfNbFXyO9nEEP8FP8BP8Nhx+
l838djffRYkfxniPNqP26/XFPrFP7BP7VsS+g7/kt7v5Lpdl3y4nex4Gfkr89gtGB31cwU/w
E/wEvxXBT3c306091ydTFPwEP8FP8BP8dn2DF813OegMbb9eT/AT/AQ/wW/D4af5LvsFkHU+
ruAn+Al+gp/gt+vMT9f81hl4y20X/AQ/wU/w23D47XnCy1jx627wIvgtA2Sdnwt+gp/gJ/ht
Hfz2vNJB7Ftn3i23XewT+8Q+sW/r2KeVDuszKXMZWKt8LvgJfoKf4Cf46ZLfxq5lPxIwBT/B
T/AT/AQ/wU/ww55YAbsC8Mb12K0hxH4Yso3DYDhZmC7t6cCPIZkcXU9wDrF+MimZ3jrX4/NK
XOuLKO3p0EfOGMBHEbFBRY8PKFo7blzhOmxQ4ZLx3LvCc38ARNlkc8an1rvoyy4StoP6Qs4G
W1r0pnysthsGbG9hArYQMUP58G3Xe3zo2MkiYMcLXpSxtsOObSFgMwtvQirHMl3O0WBDjQHb
EJQg08U8DNh3w/Qxu3Io00HqIWGDt4i21Hq9G7DLRo+NTDDzgUfXng7hsHs6bMMady3zO1Im
tW5+nHBcPT1hR6IEyAl+znrsGoT9LsummDxx9x7Ix+6X3vQT6QS/sTvkOxAfuyj5lDP6SiQD
dm2KIblko7GCH3CZ3JBi6VBm0BbUBqiz70e+524IZki9d4NJyRMfuQvobzpsgxUMokng3Hnw
3oQhRg808wScsZOY6bELVUQfwpW/4txZ8D4n7DcW+lD2qsodNIttsPBd4DelY5C6jM6F7bHZ
KzoGA//804ZnfvyrjZ1ua63rfMuAFvw07Fl4pd38lPk55NgYyAiObE3o8zFZByZ9DGV4IyHn
Nq4HNSOS6sPt5rcNmZ9mey4DZJ2fC36Cn+CnYc8Nz/zG1XrLmZ9WOmzdJb5DOS32iX1in9i3
4ezb86jnCM2vW+KuS36HQmRdy4Kf4Cf4CX5rCz+OQaYOl+MNJiv0IdnxQj1c3oeYUo9rm5hB
pUt++ATWFVL71W7BT/AT/AS/FcFPu/lpQ6P1gazgJ/gJfoLfiuB38PNdlPmtD2z2K4Pb63EF
P8FP8BP8Nhx+e77mN1b8umt+muy5V9i0Vk/wE/wEP8Fvw+G3ymt+mvDSGsT22h7BT/AT/AQ/
wW/XdzcT/PYKm9bqCX6C31bCr9z9BHcp0+3NdIeXHveyy8Ou6adxz9Yottf2iH6i31bSj6cw
wW9bbm+2ynFPwW+vsGmtnuAn+Al+Gvdc23HP8U5sV7TQb88zXg6zyl3waw1ie22P4Cf4CX6C
34bDT5nfXgGxyfUEP8FP8BP8BD9d89u6W8AIfoKf4Cf4CX6Cn+Cn/fyS9vPjZJCyj+shP3wX
I3aA8zYM2F+WF1KweZ/28yu7GJrOZOewp262gzXcnDd3GZsBaT8/3n0Tuxj32FfYB4vNnvnh
pM732HIwuCH32FqYWkrYoDB47Ec8YK/BGMareQ4bZ0JwBo8mjS5sEoljZGw/bGJ17ds1P61y
xxezqUOfyvyU+SnzU+anzE+Z38ZC7kjwFvwEP8FP8Ntw+O15tqcyP2V+2MGZMiAqhyFZbByC
zUJ6zqGiK+ZsMVyBzUP6Mk4GF3aEzt6YaXDMdR7jHnHoXT8EX9ZYwdVb7DbiB5viuOYYrmh8
ihjn8F+Lwl7SWIAaM4Y9OFyC1+t9ythzOofBmPp6PcZAYg5ohRnH61wXnB+iczz2UNseUHYY
WDEYehkPNbgg+Al+gt+K4Nfqtg6C35Gyn232K/MT/AQ/wW9F8Dv4bR12t87vsksdtJP71o1y
Hsp5sU/sE/vEvrVlHweR9nEzW61xx+d7KDQ2pSz4CX6Cn+C3tvDbXeK351FPwU/w0yW/IWE2
tcfFwvFaYcIEbNcTnEOcXMlg0j+uaWabOPqDfkUOIQXPKd24/EiX7wwuccYYrUsul+uOvrPO
cnZ3dAZhY5SzKJiQY6pXNX3nTcyYJu68w6XVMarH3HpcZcU8cVxzHV3BDh7XPk102ZQrsr4b
HCbceyxRwBKOGhX71OcBFTmBfKyYos/J42UzZpnTdcgih1LUSgesW+CHYzoXcIHbZo+PO2il
Q4j4y3DOtnrJ77KjnknDnhub0e02M1Xmp8yvQFnwc6XjYTpM7QoJ9/mPyeaCfNP1bkB3BPOs
0GkQ/HrjYwqhrtYLERPdJvitzyW/vcOPAohdMljTGYfgXE5hBCmm82EJrEcP1aTSDdjtSVhx
R2doVfAT/AQ/DXuu7bDnPl/zY4cIpEPvBzPaI/pA6BIJfvgENgHYgp/gJ/gJfiuC38EPe+4O
fiPDcsJSqB5XEjDav/fMT/DbBPDxPQh+gp/gJ/itLfx2N+FF1/w2BVirfB+Cn+An+Al+K4Lf
NlzzU+a3SgAdzWMJfoKf4Cf4rQh+Bz/sqcxvM66/HQ0ICn6Cn+An+K0t/Pb5mp/W+W3I5JbD
wVXwE/wEP8FvRfDTsKeWOqxPJir4CX6Cn+C3tvDbXea35wkvyvyU+ekOL7rDS2Gk9rLVIvct
X+SuCS+HG0JcR58yP2V+yvyU+SnzO/xetsr8lPkp81Pmp8xPtzfDecD1l5P5bcNsT93ebB2z
vMO1WZmfMj9lfsr81jbz291SB93h5XAn/233CX6Cn+An+G04/PY84UX39tSwp4Y9NeypYU8N
e17RsGerSx2U+W17lne496/MT5mfMj9lfhue+Ql+hzv5b7tP8BP8BD/Bb0Xwa3XCy57hp9me
GvbUsKeGPTXsqWHPdR321DW/bc/yDvf+lfkp81Pmp8xvRZmfrvnp9ma6vVnGzsfemJwNRxyA
WG9jH4fe9UPwvEcCXb3NOfjBpmhydUXjU4yD91+L6o0bcozZZOPHoN6nHAOqDsb01RWzizlg
r0pjqys4P0TneOyhtiGg7AJi+qG+3uCC4Cf4CX4bDj9lfofLfLbdp8xP8BP8BL8Nh5+u+W07
6A73/gU/wU/wE/xWBL9WJ7wo8zvcyX/bfYKf4Cf4CX4rgp+u+eman6756Zofr2rmEFLwvu9x
ZZOdYus7g2ucMUbrksvlwqPvrLPBwesMwsYoZ1EwIcdUL2v6zpuYbT8472xfK/Ymu9z31g45
l+uovgt28Lj4aaLLht1dvOLgso8e2zEkZ2tU7FOfB1Q0brza6rsUfU4eL5t7U5paLp0e8sN3
2tVBuzpczr09W4XfKjM/3dtzUzJGZX7K/JT5KfNb28yP3bnUmZSNsakPyTpP0sGFSXMxpT6i
r5j3fM1vrJh6hwl8ObrBxST4CX597Etq4TrMs8yYZxmgsr5OtXTK/JT52Yipt7GKBNNzY296
G60d01vXIY11yXhmuL5O5LUJE4CRL/cu+iIl22XLmb0GiW9vmFhY2w04E1kTIDczTuS1Xe9t
Ssh3A/Likt7azpkUAlJeb0IqxzIdzl8GafcQw5gDmy5iKjCyc9NjunDJuk03GHiGaCPaUuvh
3IdcHLOMkTEr87uczK/Va36rhB/lFbtknPNxCM7lFDgSEztMZg+Yp47hGZMsP4lNgcSmvg9l
fsr8lPkJfhue+a1y2FPw2xQYCn6Cn+An+Al+h9/M9jDDnoKf4KdhT9cTnEMsw2Wuw7Bbbx1W
8WeMwHF8ThNeNOwZMeSKuU0D7tzAsbGMcVaM10Ig2ffjyG7uhmCG1HuH0bLkqZyMeUtxcJgm
FQyiOfaaO4+RXhOGGD0GZTn2mnG9wfSYpcRbOeDmDcVlMdKbk/Mp9KHMZcodbumAaVIYgsZv
ypBw6jKGlS1GLz2GhAdWTGsLP34SV3zNT5nfpgBrle9DmZ8yP2V+yvw2HH6rvOanCS+rBNDR
PJbgJ/gJfoKf4Kdhz62boCP4CX6Cn+C3Ivitz2zPcYJm5qpZzOzNuH3wUC/mYfJmwPAzZh2P
NwXGzM7llQ665Hc0k7VVvrbYJ/aJfWLfitjX6hr3VY56Cn6rBNDRPJbgJ/gJfoLf2sKPKNJ8
Fy0p3AtEBT/BT/AT/NYWfprsKfDtBXysI/gJfoKf4Lfh8NOw514Bscn1BD/BT/AT/NYWfhr2
VOa3V0ALfoKf4Cf4rS389nnYc1wcr9meG7kKQvAT/AQ/wW9t4be7zE/DnnvNjja5nuAn+Al+
gt+K4Lc+y/yS1vltZDY3B9aCn+An+Al+K4Jfq+v8dGvPOVDYlljBT/AT/AQ/wW/Xd3jRrT03
BY6Cn+An+Al+awu/3V3zU+a3KcBa5fsQ/AQ/wU/wE/x2nfkRt9rIfZUQOlrHEvwEv62EX9nr
zhpsrzcMIYl+op/ot3UzYEQ/0W8r6ccOvOC3LZvZaq3D0UqvWn5dwU/wE/yU+a1t5rfXVe5a
6rB1id6hHBb7xD6xb6vZx6QobR379r7OT7M9D4XIupYFP8FP8Ntq+HEm5KbDb5WjnoLfusLu
0HYLfoKf4Cf4bXjmt0r4abbnoRBZ17LgJ/gJfoLfhsNP6/zWFVD72W7BT/AT/AQ/wU8rHbZu
AozgJ/gJflsNP014GaLNw67hp2t++5mNHeSxBT/BT/Dbavht54QXrXTYukTvUK6KfWKf2Cf2
bd2op9gn9rnOseNXGGjTMBibgo9URnHFfhiyjfBzbISuYUjWOp/62E8VY87Wu2D73Pc1Kg8x
e2Nynup5G/s49K4fgi+31nCd723OwQ82xfFWU3BF41OMg/dfi+qNw4BEzCYbPx689ynHgKqD
MfX1+phdzAGtMLa6gvNDdI7HHmrbA8ouIKYf6hscXBD7xD6xb0Xsa3U3P013OTTpUbkSbiKd
4Ae6D8lZ7501xvlK99h7IN8k4LyvHE0mR9cTnEOcXMn01oHu2SbuaoZj5YCbRnrf90A8zwvW
dwawjzFal1wuBPaddTY4eJ1B2BjlLAom5Jgq333nTcy2Hxya1teKvckO/Q2LVuTSofBdsAO6
LsFEl01pve8Gl330MRq8sRoV+9TnARWNG7sdvkvR5+Txsrk3pamlD3HID9/hMGHwNuAVx26N
7/Cm8aLokGQXpjcZQ3LJRvRE4vQZ4s30+ICiteObdB3ejEvG83362q+xCf0hfGq9i768tu3Q
9UJHx+Dt96Z8rLYb0LOyJqCvZcZ+je16jw8d7zrg0ylv0nbOpBDwxnH/rlSOZbqco8GHP8Qw
fhK6sSe+TX5Bm77Kj+8xdjmhd9zjTwqy1xL3ayjzU+YHdAQmoPX8K/gJfiFhBkQEiCs0ezeg
O4IRB3QaONsBdwR1ZK/NkE0ckW86dEUcGJztYMsgRe7Q6wB40c8ZMJzBHkvGbbRBbYA6+37k
e+6GYIbUezeYlDz5ntGHiYNDlykYRLMRufPgPVAVo0fr2IjcuWh69Fg4voERjeKy4H1OGJgJ
fSj9mtyhw4YuEzoi+E3pGKQuo3Nhe+P9ttzYU/BTpndZ2JexTfzZlEdlfsr8lPlhhF/wYzIY
eybrwCT5ziGJhJzbuB7UjEiqM3uLqQtIo/sADCOPtwe/jzvT/NQhkTO4YNOHhCsyYyoLtIeY
cHUGAyWZrd9T5jdSEx0YDDZgrGdw6BKVYyWDnk4cgnM5BfZrYoerOhgV8RieMRj1gEvAafsz
EPx0za8Mx2rY05UhZ9MJfo6JpeCHAfgyqo6t+wS/TQS54Cf4CX6a8LKiCS8Hn/mNnL6izG/P
w57K/DY4gxX8BD/BT/DbOviNI5WZ08fmrXDXqOemJIFin9gn9ol9W8e+vU/2FPwEPy3z00qH
gk2tdCjrOzTZ86jMd9nnUc9xoowu+W3k3B1lfsr8lPkp81Pmt+sbeyrzU+anzE+ZnzI/LfM7
yisdlPm1vZqgZVAq81Pmp8xPmd+KMj8OAKcOq//dACjihipYHTe6cHND3GvHY0ngUNcH8r5H
Bnc2yj1utzOuInQR9x7kzY5wk6EwYg13HMLNDsudiHCHonIs3DUIx8i4oaGJ1bVvkz017KnJ
nrq1p+5uVhipu5vxBKwbvDSzxn13md/IsNXc3UzDni1nc3PapsxPmZ8yP2V+K8r8Nm6ZnzI/
ZX7K/JT5KfPTrT3bu7uZMj9d85uT7S3HKvNT5qfMT5nfhmd+ex72PMwNXohb3PBMt/Zc++UP
gp/gJ/gJfhsOvz3f3UzDnhr21LCnhj017Klhz/aGPTn9ZB83dRD8BD/BT/AT/AS/9uC3u2t+
yvyWr3Xp+XidVMOeGvbUsKeGPdd22HN3md8q4adrfpsCT8FP8BP8BL+9wI8bzK/JXraC36YA
a5XvQ/AT/LYSfoZ3HsFi9Yj9SkMS/fZCvyZ2ct/duOeep3vqop8u+uminy76FUjqFi882+oW
L2t2i5dVpn66xcsq06+jeSylfkr9tjL14ylMmZ83YSAY0oZnfnuG31hRexqt/aK+w0FW8BP8
BD8Newp+2tNoIwF3OOhNPsFP8BP8BL8Nh5+u+U0nfD1eej84wU/wE/wEvw2H356HPTXhRRNe
NOFFE14KIzXhRRNeeuPjmk14UeanjO/SjG/6LJT5KfNT5qfMT5mfrvnpmp+xKfiy/3LhYuyH
IduozE+ZnzI/3d9sXe9vpsxvynb0eGkGqMxPmZ8yP2V+K8r8Ylk20efeDSEGbJ0+lH506nob
ex+9D7Yf8rg63vd9MMENuQ/Wkk6pczF4B5ftTQzj8nVnkJJ5a/Bo0uiyfcQxcszOxOoyKRt0
2/uQrPPj2g2DF4sp9dH2Oeuan6B3KfSmz0LwE/wEP8FvRfBbn63ceYef2GXvQONo86BRT416
atQzOevxJ2HM2IVE7wB91kGjnhr11Khne6Oe+3xja61x12RPXfIT/AQ/we+K4NfqqOeeL/kJ
foKf4Cf4CX6C37rCT5f8pstcerz00p8u+emSny756ZLfhl/y23PmN1b8ult7ctJN7JJxzsch
OJdTGK8fxqEPg/e4hmiSZQ4s0LT9GQh+gp/gJ/itLfz2+ZrfYeCnTR02BeqCn+An+Al+K4Lf
wV/z2x38Vpn5CX6CXx97jqSTnjFni+U5WE/Tc3dnujLW93hjcjbUHTwe63wwLuD6IXjKh67e
YgGOH2yK49aicEXjU8S6Hv+1qN5gJVCMGct8uDwI9XqfMtYQ5TAYU1+vx5qfmANaYWx1BeeH
6ByPPdQ2BJQdFhIZLDUaDzW4IPjhQ/Vdij4nb7GaCkus+OGUj/GQH77T3c10d7PLubvZwcNv
XPmnZX6bAqSDfB8EVTh5gX8XfuJKfFhceEf+vOTQf1+9hL/7BO3qS79nLP8dA1uuMh7nwk9c
UuqVkMv8OKHWmX7xHbfgM77+aDwmbSwvPxbn5fy43wKve5UHLC5YnLV4/OLJ+HkOPbRrXbA4
E55Hws5cPAm/eeTCLMIiLvLCLTwjTpwiDvFPR+DjsTuINXx2nfNxjEfhKIer1eF1H4PfIO6a
d17sLE495NW6xRMW5y7O5u+ve9rivMVTEP20xRNRwx45ktGH2jft4JXOwZHYlvPwzp62ePTi
cYvz4Tln8R+XPA4/+W7Pxe9R+/ipdP50nGOfuXjm4mSWrlQfr/J01DgPn95TcKwSd60en9DJ
+KR6/LR492bpMUxHauXx2PPxKX7tW19Zq44pR7rW4rjDqO+Yw/iWXdPvv2XZieef41/cRR/7
geue8vW/KP7Fwry0+r/AuKP671Z49evMaMFbELsDez3s+FLvlFNeXB7HMwn+sj9xAcqHUfTl
+soh6g/WvaJ/J11RwBF+f/yV+Yvpe3vwUtQ9y/NLz1XTOYvubimuPL3hoQ6Uj8G/8SP52i93
+/3uT9z1vtaOSy75/LHXXNztvKc87dzTzjzvzCeddcFZ510fX+GhnzTP39O/S9/KVYCRb67u
5Ygp8usfR+Z8ve/S0g3K08N/yvzVSRfyu7m8dpUDTD8O+aP93c/c+w6/+5nP3H769aFl/FGe
slicDNvLP7Z6/Pc7D7jkzy/57OKke971Hnct3/stj7klWv3fFndeHHsl/uPPY/HvuCsfx38n
XPnKx1/5qieceOJVT7jqVU+8+rWufuLVrnm1q171Gte+xjWvddJJ1z7pxKtf57rXOem6eH4S
D3IMax573AmoeNLVrno1eGf+u+STi2ufcOzn8N8x/z977wHWVLYu/O8QCBaKCAhKFTwgoEgM
vQVGEGcGjAgRpQgDGgSkV6lBxpEaYGz0aHACJBJESoAIRKVJRwhICb1D6L3+t3Puqfd/7zn3
++69332ey34ge2eXtfb6rXe9633ftbM2H8DGB4HyQfarAFHwVgHoNzH9UzkACBuUnQPGeRg8
qncMAkCgEBgbJ3jPMOi3c8CjfOwcx0/D9U1/8oTxXwxPfNUmIIX47nq+vdeHIUHpS2acZwwc
fl1QfrgYAaZw4m+S/j0PCBu4X5jv24G/ZAoe4TsNge/3AFxgNmx8UD4ACezlYH+/4uDjgMAB
gQMCBwQOCBwQOCBwQOCAwAGBAwIHBA4IHBAAeIJ6WDIZGMUBooym0ckNPQ1F1wb4xg0Xco0j
364+MbcoG2/PKAteRur9tKfwhrxsKm7+cB+ImkH2xe/YHepJqdvpQKVLdl/92mFEdevbNKhd
hfWoNklMO03HjyXhB4DJTKfJmQl/r7Bo+PIoT7QLoaSfUELSqho9+V8BH5pqVai8dUotD52S
1U3QqNM+f7WTMT3uEMRo27qH7w+MyJDGInD0upNVdt+yv5lM9M9JjpoX/VDRT7Nwf7ZF1ELX
rnMaluf7IU80qQS0q29FEPq7vjBY1T4PasLsfHo7puY9igKjswpRElhV7Lc0/jOXJdXn/dSs
pnRxResxlVDL0He8eNJYw7oMq2e8jDRxkbtDT9VMTD9N7yLOru5f8pWRekBXtepwPh8qNj21
0MKL1XRludqI9495jgjjEzTPs1LNNoqdszYd4buQdnfbzNL6XTiyej3Mwz0qKrZqHKL3n3f/
EMoeoTmlr7/S6yxRs07X3cmV1tPYnZ/qF7hHer+HXYYUMyUHjO0h7yAJF7HX/pIvB4GU2+zK
QPPvILA+Vj2aDWHT8wHok3uDU5n3GRIxWVGLxLwp5DXwUIrmhomvKbIatYoDpqh+jK9N5Kdd
Ep80YHZ/Se3/akvdD9fZPintv6i4QpB9gbcLbs6zyu7sW30x03IPZ76pp8xW5QnbkhQhQNKg
Z2F6f5uX8EhG+Yey/jy0y9cOizFE+XYEsb+rw2zj+WRew1wdWBVxOtaKpl7xohhda/1291u/
0T7GrBivJVftQEr+NqX/o28/kIhJKaSkSBwC0Sp+4stKhEb+S/xh2spWxKfkFKIzCYMJaGxc
TNCDvIsclg5RUnBVbkbEBtSdGWjvHbLZ9mlJOuPiE7zrw9gpbHxYQzNETlvH7wNPH9ZQLyFX
fWrT7ETkKE2eqf4sxti1i8ykEezflf7wiKj+MxrVNVSwZ3IhmigpprpGfIcTRJu0jGfFNwCT
1OKcfcACZR7QrrG7wJMa9KOh9+69rM1MYIpIcomblo/OfH9V/+/S/I9y8J5eLQvhrryVnSeW
g/N9oKfreM/V9XJr+ud9QLEzwJS/paVEHQucNDjULBNjmvokdomoUfem3I0wcVTZsGS+Oe81
WwhurKU8kESaL9c4lvW9m7pB+9jxo2s34xss9i5yOZrwNSfvAzX6sV+JSOU7ws3PZbxp/DoL
r4xti5Bj/aWofeD+3qRmdvkbsCYmCbPGjo+Zibdqymr83eYt8SOxRrVPI4Lts5sQ/OJ/XzK2
K+cRyldXBU0Q/clVESHlr95QRS801jqX7AMePr29FtKPegUYI8aDINWKXytdQqP25EOxU9Ts
/KCFPFOLpxF2f5/gP/8dWt8T5NUcr+qzQQt6sdA+scLZNFAZhPZzty1VYejcEcYC5wzqomZk
SLvoyP68py3qWTPymrP3pjJ3Gp6UI5oxYSSFu4GpN0b8cOqsjxBCuYkv6ogTKOShF7nkaYEU
f+eNyBp/4oPG8HVa3cXVF/ZwIed4roizNGuUMDFP09BRKBf9cSwnqya5pT705RSBplJliDDe
cORfSLDMNVjA/0zXmG7tJXo7yxchP6hvekE1e63JhBU/8lxLbV6dYZyrwEKlG+22ymWHEVEO
d2KZQmybNVr8+JG/BsCOPcQJAOxVKD1XKqmjZ0fH0HMorfYj2AjvO2fv/HCPop2P3J7jNCkv
wlCE7ncZxdrbiamubmlVNBMik6fM51oaRYbtHeCSL/860X96W4nmx0z19mN5GgosJidzNrsi
ryhOIxwNU/02TYJJ5Ia32h53jx0BxLUJ6o0tZ7EOfN5oC3JBuUmFmYUcuaEweGK9Qrq1KCuf
QBVpE/k69IOCSe8qMwPx6TXUdvUYnch+U+CYQFWkQwkRki5EMRUmltY6jbCpmZJ3fYKm8FNS
VLPAppYm8T3+lc0IOYK6Z82DO6fc7uUazxuW95SO4/iXxrlCbpMG8gMVcF3S8TXAtolPqGpG
WbDTdtsSrMF/lrmjVdjy/iT2r8rrzZ5BB76N3Bx1oz2vPFKWvXcrCaSXk0ttHrWQqEa1gmI6
sF0WFqIS9v0WqAUZbRYf3Uz4d0zj8ZK+pl7Muiba0y6xqbQIyb9K9J/b5BRv7UlxTb/sxij3
cpjrxXmvYIOLafem/eKaZhj2kXiagRfWW+9iJAfAw8ePNovEvaxvTpmjgI3OpMITFXbSlo+J
cPn+Kks4ZR+4Y3HeF+3lT0qrO3MZoMewYQ8BMA4ZSDCdLgPUKjkaNjwNEmwM/ajaRiLpkJCL
Q7uP3LJMMRXefLrw+FmudaekxqvSlahIlb4vVrQamg8DSdLY0SfPUs/v8RDKguW321aPraaQ
w6IwCrgV1ErijXSbqPQeUoo8y9xev0xGPraqavMvhebESgoDXGy/7+D76C0q+x7qW+73ruuI
r+BIkRnYmZD6eypRw5aESrkUsJ1Qi32KPEpN/HZG4Esg+tsp60f9J5NZGUjwqYX/yMLOGVWk
I0XovH9PRiHvad+E8QP/3cj0mQkXCq2oqeFZExqtkZzcWB916M3LkwB7oxmfimfymLF3gs9U
IbqfpHh7iK9e04xNU3GAwNAl1VYYeqERiCquy3octZ4QYwhW6QgnD9aOC9wAhAHAEkOSVUbD
dY9zF067mbEM0CP1oUrcHdO5DBZGewT5VtWgtxTUA08nth+iMTGJysZm5r5RsOhCZTMNqkov
fihDguc7eF9n75oLYdSPpHbHfNvmxj4gXl2v7Zm08c0M+lp6kjCGmIc1TsT+CYKsJACN/SNW
cNcfzaXK0K6h25QkXKLFH+2lu+IdbV7I6DRUHSi4TP6NnsCcvVtRW1Bi/5c267FQOfzIdmWJ
phMpJVO50dj/r22XP+Xy/7+Gpd8gozKL1IqEpKIdRnSP8T7vSfU3zWsi3ypyKA5gTKzwjZMu
1vo42UPSAM6TZK9ofzLri/beQ63CsiP3osoDKcHTibecVbTapmdrWMd47jvGPhwEH60R5kg6
VhXtgGVjSwIEuABJORyBLWkBCjhIgvZhKAuZGij9ehHWoxIwhEaIW4eFZau2BzI8m/G961ug
BkhzVF8eW4SRy0TUHANp5o172UNI4WFu/pcUnKqK0FmWYMjk1k4VanM7lFGmWLvQLDuENLVg
PZ8aCoxm7QPKHhsRrmrnu2a7+Of/xQASH9QDx/zB/z8uetfkUrLTp+VJyfPGI2ugMf1bLnWv
kCFGisTPgf2+22ioSrTzIsFzCZ+tOetqI7jJXK2gUBgLm0ucdn9K499dQ5t6Ut1RBcOu7THU
fcAAdWiZs356NSXOt7s8p1QFdWWKr0fycrb5XWPfp2jBp3qKF7lyrSi7VsUlZp2VWQzTye72
W229/aV8QyifU3nTCuU6OThTtsKHg5fYKFpsdlxsg5cAu2s8IQBdGBqpCJGuEjoOCEMBtnAs
QP9FK9ruRDQ5M07QRPf6NyE2UicGP0DViTgxTHU7jB/UhGJ7TW6Qx+C6ZvvAO/ZeYoBjvNMg
t+DstqBnKlxceWE3nOTjn71zHuyAzDEQnG/xyLwlYWKpWXacs/ds1qMeBepOG13EieZWiSnB
B1wEOQwCkoA3lH7sT0jYOdgBYQsDNMB82fNiRUiK2UOiVC2kOOLmY0MgK08tDOulxgQNzRkn
o3BvubB/uurfXgt32ahOpcyQ5IhJjY3NUpBlmsWXH8hNcekIE23i/K0l1jgvGwZcvBE1d03t
L3IRpI7dZXujd3GILyXr5GaEH97I2wxeblwtJjc/Lt2WXJSZJVBlElKmR/nxhQLtxup1Lnif
IV1YgKP22jegfZwlAPwrr6Q1ODaMVQK/XNOmD7OD6mKdzR4S6AgYgHuPYu+aNBTWSIH92NgC
rF4F3d6cVPuYd5Y7n0QIoYh77jpMcieiSZveC2mgdSTDQHyU0c7CKlt3d8pPYKQcc7WRP51y
vOQV/6HDAvXINEkwti2PuunaF3+46uFVIgkpgvLCLcdWBX14doosuK0m3c9dGjWmAfC8xAb8
3qf9CypQbdg0eCrxpD8pzLrkPds1sROd9fMeqBQmh71r/rHbBGmg9Gja4N07nRVGdJv4WOhR
3qc9VrboQudq71JnDauoofl5ySHzm7h3XOE/CT5lW2xmKc9b6Oi+nG+b7SGRO2+nNfomDV3B
kV9MFqDI+TWBHQo4e+e0xnF9+6RjzHCTrxxM3Edh3MfEY7BZu0t+HDIJavpqnq2HY68IQ4Wh
4oCBJ1RUj66oHj56Ovx7HBaAQTxbuYCjsZ51wpMwgIMufIyelSQM8+nyyuCzHnmrapZDyfAU
n5P4KiLHMNWWj48N0cV2m/iRcRlTbPcIYaraG9CjKQoWAV3OKe89gXHy3R7QZfPq2we4ba/9
pGniKvE4m1h5JFNCyUHF5ezaSilupdnAYa3BfAHso/aBlLQj3YYz6G01uY0IXWFoHa+H7J8F
GtADYOTiYQfJFVXFjlTvU2Imtv7PyogPwnhbxRf+bbn94xFeEeetS47fp54y6aWWmtg+x7+J
GL9gW55dqpbXRyqbnrjIJSggcNmUeeouX3IV9G4quj+9F44fnprbimB8mXS9mRk6cWhee/T4
Hsk5rsGTZuDD1ywfvgw9eSwSykYB2zsgUBsW8FhSCuL5lZ9PB6gyOv090cDYP/wKVgmmDhmS
9OALiHYYhclm84npe3YBCUfB/RDPYZgmBGsNCYcYew4fjYSKAlVeUKBenoTHlMYHXIyhyrEW
ame5n06T4p1lxyS7T8X4ekeH2TmKkyi34vGznCQChQ+NGOQWUsVkUPzkliPBkwXvpzjtKFBd
R15fdRiXPtw2M7l2oc32kWn4TVTvvbWV1Lb+qJY64WZKCvIEsyGs6SrkmWaq4CKRpbvgyM9/
Mipq6c+P30AAuvLtIn5+bJCWiLPJZJw4MW/ZKb7UfC9gK6Lr3+cNo63PTuWazKxLRctNXORN
6slI6GfM3/yCYSQPITZJW99l1hoKAnePHf35pNGhxgXO26mXvHaq+uJ6ZJfWl+dHea+f7/5i
WiPl+BvS1LorzyLwDUNbC8oVAInEKp2OPXLIDk3HvhQ+VqNHJ2p9U8dJx2ojxQE9USApSoDJ
Xov9hQOOlVICRCEeMF0ldvqF9wC8lYttpER4+KjSYextrB6oph+wXdUfNJ0ayPRX6WnCu1gE
rjZxfKbmpGpaUc8WmXv3k1IwUtJPGxcajR3hUhaZL1ci7Fk3iX5unW3TVFa7H94sNGX8HknK
icynTZSRkS2Mno8m6DuIX+caHmvpQgxp6z91VjS6Ks6Pdc269eXN9rDsJNdURy85zagWaJYv
MPfCD6xBGb3kZ56SXd6OTnMYl3xDMx1/B8kJsoNTQYoTJWre5Do3+n5qxx7Pu5K9e9EV2I8+
qT/gzJxHg4b1f94txqkpox3KEcelDzMMJWIwLIkmYzr5ch7KtsAP8k7R1EJ+6o/dAtgNsDlI
tnlFEbMpUUlJaVW1eiGwzz2eudRpSqPhlvS80TRugVfv36tPyIfCtZoXmPboidDZWiaVv3ag
B7IUyHxF6lELwRAq+GbbxZt0f8D5XOMwjIQZXUUQmGh0qaEWw481HtHRNtt3dXeg3OJWhumK
IMPb1DCpr6Amj7HCed5M5eqqWeJxyesAXZFdSQ5sENoQzzl2uiLYnGQHYRzwyGMCfJ59oA/s
kE0OPxxufMgHKrYRThuWo83T+a+IvLQDJeIYDHTUFYFarPggxHOQs06AC+yZMZBPRa6swEJG
cw3tt0xTAbTqVIeZ1jOLeFq58mK0dwtfosSLLZPJFzuXKok0+/6HjK3VDvQayyYdrSZPQ8PX
pUooKRhXA4ZWsRzBaQhxY2+l2jx4Z0olAzdZfru1vSvsHkurSy656yalueGLia+7e/tVIhOu
hpHCuCSlOI2wGMptXplt3SlMkzzD8y46givxaEPL8/mXo+faOm/TTt0qcrantTmYpPUTHVVz
Yt27zBk05XaBRv1KMDAg6Nf8MD0zDF3kA55hboZpbi0wmJ4z9khrd3ZtN+E3r3HB04yHk1Kf
Waxfy3v9dWDxR7M3+SRaYTG7U9gnVnWTiW5FNimpedbYxMfMff4qJgUzvlODML5qz+fCzGrf
feSOctsDg5hGNqYund15Rl5lK6t9NWO0Cop8tOJVp+0nWn0OjwUU2kunLmQW54VkzDG7V2z6
+/rIaAN0ee/JiUGFL1FRI/xJGW+5MiWbFfJWUU8XYaZ+ZQ8cmJ/WYD7TFCPtHf00F+k3RvST
NYS+5ch1VMfJeUtyJZ3LMgNttggTUrYMKkh97srY6aiKMAwSuWS9x2601AhqLpX7WsGs6Qum
vYIYCMXv6ju8g9UcKTbicCvL8oFJys64nbBJ+W9GOifWl7qAGnfbrN622/HyXoc1G5S3PW2+
if95zXIVawr9Ysya47MeXclmeeIDNP+YpDEGkrnTK+RUjskhlsnClXh/6+79rr+iecU+9ekC
JaN9hfPmvyP92txFU1xTM2SjV1V9OMG+CZpOZpWEChptYd3llUMiZSEQGskJN2MBNkIV9CxO
XAyj305ss6msQRjqOD5taePMy2rrbreKSoq210WMKoj0pJC3n4/4JdyrCagT5mBy1OrBB2Fg
A9AGmN/UfzhOHerDZewJ5d/Vq1qCAiUL7HSR90ANUMvHC0ipPwzHvQdq7aTUIbjhpI3IkilJ
h8envw/n8hdgQv1FtSINpVLfwWbDcdrY2mOaoCEKT9AAP+jcrTIZkptNlZOKtb2WTartmShi
+4xyF4ZlodvgVubLp9yk9YLgoNJ+MpqAECalOL5MnJjeB4ZQmVvTMx3OKpop7szyUzHPbhEZ
J6ZJqb5WWTvlnzMfqTCiklJKapzTezykm2n7wBGVFMtC5fvI77OMXnczrEsdv7+K6zNTUxhR
w1CQ48ZNt0qVGxfjmAPl5U7ibj0rEu1aL8jtUz6BP6i6NuncOGfVZrtKXUE3h9ztkaepElxo
5TdW66kzscYhk6U3JgMDJfRVi9s7nZx7A+Nuv7jkgrKJu/G8mZirQ9tRc213Y6Q+OZFDTMPY
l0QTZecuB3AO3FsJtIE9b35smEXNap9itTszyD7VylaEpGrlKqNDkZFV3yn4GGEviNNLQIfo
JT/gIPqAbb6rIdCDizDm2TuEvXsqJnEfmO84WUOhVKrDTMm4fIm3F+NM+NvHuQirpfvAsiRt
bavRCA/AnSlW77hcvjhRgvzukZuTEpzJdyflJ36jTggMniJ9penmrXiOmdOV+74WT464kRPF
BZc2nkkbz/ZkdjNs4zWi4r+aFznYvio/la7S44ZGaWLUvMXCV1JM0KdocL/IFMdn5i2ajoUR
Hv+mlEIbemlmO0iTaRZ6L6RfYB/g8s2WEGv21ta3V8rOfnkk7qkViURIImIobfvAe8jU5Jp1
Y7VFpop3tMPTsHkf8TgzFxPhKhPTLxpGHRbnG54xSZgcdrpwrZ41aCSKfbMO2QaPcUFwICfR
d0c49bQBKFYYq6YHiivWjvsr1Oe4E10Y993xo43XLrElwDQPldBF6RxL0Gy2JD5PAPTqy45G
TsJm/aB+HHBxSbdaQC0AUsZumqAm+1JmdJm9L0HtjpCfvn0CfI6DySb9Upg9CRACL7M7HAUF
V3p8/KJEO6FASpHx5sNq31q5eOy526Vi3vMJtoXWixsRZxkWX4+7G1o7Z8X/HOZh6UJF1J3s
7c/37roZu0LJWOC9yqx3axNs04j6+zj8X3i2kxmWbVMzHf1pZgaOLXQJ7jcMZpezS0c/vtx8
Afe09grWGQwUnZByZDY7vsTlKv4yR3Dwk0kJM6+V8NBJl3nISFEjSEmnMXRCXzbPEeXiGuCR
Gd6dht5gB4fQ+VYw0Q8PPKHHYQAWrsEBFj8YbPHzD6Anh6REXhpKuq0nmgwcU4JNiryDAWCJ
wV9E2B2KXQZbP04UoqbHnEmQSjA+VAKYbUV6tiSR43m+A+tEGFQd2kry2NO4l2w1QOQCgB48
PSdAvxB5hn6G/guHNdsmZJDdDwpAcAvsNQZwUWyVH6gkjoGZvAX/X5po6zHBGqw9JpNgrHem
SXmRpP88ZQd9e0wDfyzQ8gFJ0V7DGKP/5S+I/naLN75324LVE2+KyVs618IV6kzbhYwZQCUh
6TRfa7JXCoZEM0Lp1sdbGL0rabeZL7dQJ0r//MBo1TDQ80ThynB2VNJOfkM/t5C7hV9AC+BS
i1UEwLhECeib2Ev3wdg1ICOSDsLjR+Edh+IBgM4nDrwPlwLRlCyCbZVu5seuFjhqzkz4XXWC
tlyFJChjVVyeUB/ufrqJlMg7OSw8EVA6GhuOleKA07nYtukcU+EQPUkh+nE7fqBCzyhBXO9b
WnaH44FrxocMjoBxEYAHC8FJ+kCxwJNPSUokFl9DZBz6NumBB6dK70aawfgd8ect7WjneJug
R2b1HIHPXZvg5eYhU1M9kMK/ZfPnb5yPp2QY2yp5b7+Sd3rz18eR55G3OBtASjL28OSJj9Jv
NqEF3xfk2Vajq9pQLduH1gp7RCwDpfkE2sUwyJ9u9XVUw0sx8H7KO55QhPadQ1jrO0L+fbB5
SWu2QYOE22n0JGgt4AAfhk2ScYOgA3E63NjITuk036D8IGgYgZYyFv6VC8L3zdHAaH+TI0E1
xwwIaFAdOwr40LF8bEmTR+fB34TAJLkua0DChfyruNtMWmXOcF0RTpo+GoX7ju8ba6AEa8zm
CxXDgnZZbaSi7EthKL8YBLTVgDFJOwEAos428lb0DkQYbQPvEDbpzjANtySRHJNi5UlSCKnC
eWaHxXThSpPZUD1k6l6xjapzNDneKmjsio6Vn1TUAMmftGmU8G+Oj471WG4Haf14g1CBqI8O
Q9uEL6znWXfYUFaniaSZtMaHXrEtZ6e5i5W78lr6sgT2SJlruJerK1YyzDIqMZkyupw8sTjF
pjXuejPWg5Q99YXjXqnXWHeTma5eovE6R7TdJeC9B1iOdbaHeorwPjPAE/R2OarC+XTZQAmi
AbT3geFlp8E1gTh/TO0OF8oOLiUsQP/mFoMBiiRFJRgw1J4gzN4H9cdJ6SWx2RuAdaF+xE5I
jB08RBctY8N+c6BBF5sNCxDZOYwP2cmFW/C1sAljpSTNxLyOhvPzg7kaQHCtMFlRbBJ70jQM
0ZIAT30+QgkOp5Db65PosTIk0oSGIM6DC/PSmRaa6lkTEHFe97Hpm33g4mwT2XpZe9Qo/3Vr
m3MkgSFOwRXEl1+j9JwlRjIJcOBPI79/lsd/2YCpMEwEmnwZAu3GGMwDA+hwcc2XPCdnYkly
jOryieEg/+UEr+4ir/Uhs6Rds4/IsswvX2bLvAWtt1d9GkNbIxjULCoG4eW5A2/ZPvJsIBl0
hwXaeyAkKQNrtpHHxyD2mnpsiceOgi2Q60hJRgDUR8gP4hnO5Stoz64Hx2HB3hYyKj9oECn4
4PdBCSWYdBJxNlhfBi8JMg6AfLOGhOnnjI59CwRzQSJnYbNXREpHYey/TBLPcKF+4jryFoxj
simqH7E/A8bfzMSlFLUguEG36KRE8GqapL1eJBR7VpidLi5ZguX4PgmXD9SQC40UJbvUMAEG
BtDDyRne31TeoHCztv4jXwOjk3Rld2alLam9TQWtU3ZoxSdIJtXX0L+yidb7m1Q5KKZpaNt+
kobRFdjg35P803fIcn/izBwTv8CUgTezHgztvFwq3FZNq2JuL7drl7fyXo9RnTUTvE2SW5iw
WIOZFp43FSm+l4JozhlBzLMpGn5utODXtb/AQy/B2kL0D9XuAwSKEjiY9nCu7mcD0Io7IzQO
AA5vFYGRRkDTIwHeJxQpe9+DI14JgIK6DSvXCsD7vrOH1wDMqGF5tzqRl/Z66+GtwE2AF+xU
wJ4GBJpBB3vvEjDcY/etrdO59BQ1w8vY9cCelh1kjeVrABXwDB2w9sfC+05NkyJnxAd/Qk8H
muku/KTmkpHPN8iF0B7Xg/6iB0MogaJ4DxTF4KzYBez9/IK86fzbBAzj/ULW8hWddMVfYpQN
VSdXfTaCzMZ5SE6gKBL/bVEEAC9XbsduV7feEb+JI9In1wfFuW4Ru/rLb8sENAcwJNFvor2v
ZqT3LfRnIHQXnFKIOU2+xnV82LvC4SJy5V4aFkmwel8VoyM5UeD6xESGveF9ohO5OynhLvZm
JN+DIw7YmDmAJwE4K74Ap5uxAe9g0gmykYpaYMXZSxmaQvRMuewg+hCwc50KNxMHAYF8PNns
+H0Ov+Yy9gYlFXsNXhsLqRLg9QBK2KS+SSaoIXwTlMBIJGgd+bGn3AHdUwNIFHDczVR0GvuT
2lTLoWQYf2ApC/iYk1LSdP1wJBRIAkMSspLfp7GZ2IRTaPkGGNC/YWimu1qVOTv653p/lBQn
xtztKVjPib9la/XMK14yUPkWMap/wuIBjP4nEfvXa3G/suipUhuz+lEDM1v3oYW9wc10tL/y
+nhMG7xXB33E3ShAsjllpIxrOO/YXUG2qodV0aV1Mce5psq9cOiWOTCqNBPvnJRo5cSwyvCE
L/O9Sy2eeObBNfJCeyNcV6/CDpCTKDmLBQLYVtiHOgQgKCVtLAeUTRjKlmFnJ3BJzBBOFxLV
xtJFz4DNDmdXMnj4ozo46AD2O6BKrfIFvXAIbfhblEsrPIp+HCb99qwYJDgcYg+OAJByIkfM
oUfyrHBmiFHpwx0eVWZ4DcGfB0q1idL17D8h0Lc7Grer9YAEbaSHDt0xQSZYH1El3PSdEqni
HbduMY2xlatTWmrxWM9vqlibAb9Byim1mCQGGKVFdFKJhGj75MgqL6L0MYV7Z/81tT/vOVOF
5jcx5ef/aK8/4VJ8Ps6mlACP2inyipebADZNXuX7ZTQlU5pULFxWGLvyo0WiN9bilBnT8wa9
eSsMYdNedwsT05bxiBC1qYzSK6qGnl/0n5pzFXQIcD0cPQEJeFiNNpJLWgL9YUWjieSFRCtp
C2uPFPvg8OJ0NH9zVPjJ6hnvzYrfPVTjK+cuG1qjPGz6l6Tm1gWq7Lh8OaZhGgscdBkIRis8
HlBzeCszGwCGPWCTwgnwVh4sGCJ8qQcOqdJ5Xvo063GAiAE6KLdsIHy4jh7oKgJAhugG9GSp
Qeg99tTOkfcRJztCU/Rj+ykP7Nl/UkFbaE6I2xPnI4X5cGBvPi1vx3vsIkwfQQeMaz2+T8L+
hA6ZwGpMVyLMrYqMu6yXIod5yCJSq5vRRc+a4C2MtpYBHcjM1IrfGzOaIZ+hTs7eO57ISCKc
DzSQ/92FfeKj/sRMuUS35RbmgpNTVEZhja51dOKg8y6s1EVltul+7YJFwz4QevTKku8psdIC
xz0XQ7SP0cSryyeKc9/PWSAMbcix33O6ltuoeOEf6lek5lvI6b+TbxGNbpBSNLR+WNW4Aru5
yBEZflLv2NEE01uG9SPPvMUXT7Zn0yTwowrqjD7WlYtxd3ypCwmOp8g2JHDwYNusvmSdjoie
zEBXbX94bv/ADox8A1cAtu0PEI/DWLWAJaj/yzPtkiUJxmzhsXV8QIUdm0OVkDjAthn+SVIP
NEpjuwy8SbqST/z6UKcygYyKAeOWEn6W8grxjvAuMWfM4FCNe1+GWbzHG8yYd3PORmTyvOQd
ro3wjEFArlXv2DHz5OHTCcbRweEyDi/hKW+55Ev5MiTbbxCcyV4MQWtK2Hl4gs/XbsuYZX5y
aakEq60mL3iFM5fY2tPeTnOLJGiOxLakRRBTnIhwY9AW+4cL5MObr0EKNsbVu2LvWywdjpsO
OZdzEJJT1tyKaWZfUrIedsQrmL4rl+wuTS1ztzEIdQ5bh/ncoxbZR0W7t9vk7KnXNka86yxm
eoItR/e6fpvJtCOJ+2kXKgDmaRupuKAYyDYqdHq6qtbOOtr9soF1dCmbjL7X6USL7Bh+7F0h
eRzaOKj6ZqWfbC8+8mKc4XzXEsyUVComFfzBwcLC0gl0sfcB6jLHtrVv5vjRtZJd/kU2FfPQ
lPCnzrlr5EHOnvMBO5DQdufAFroQ6wStTrbnvD8ee+H3T9m8onYkgLJ1qRLq6mWBW4WmPS+/
7zAIvQVlIdf27PBO+LZlKEtlL8UAVWjNuiKbV7pV8d1rZikyJYSeujrRmyjcuDh8VNfuYd68
pOMwzAHwPjYI02sxBtivnISqQzWWoJLubMZ1b+4Y9G9GP7Hw+D4P+EgumeEDGDNkmgU53438
zI94UZpUU1sZaO/rrxbG6h3R3ZxUYLTfc3WaYlINVUeKtCea9dtNlNuFwR7x5T+srN9P0PDV
QuiTo+Iu/8p8MKFe1VIBGXEuP9RNRdz4daxJ5zb/p8Ei6YaOwAvUwjSfruwOMzEZT/ABFTlR
wWnVX3C5TW6/rJYuZCH7VkXus6zU1M28EL3aVzSzGWYW5jem3Q1GIhHRw/r2L+8mcfTXKYba
3RGSpNHBj9JE40hwA93IVgvnwsqPXtLmsF7l856HShosCWKC6k5y1J3EIobBmtUe5FFfgGpj
o6Y5S3g9jnEm8GU8BH/fO1V37ZIkAJxkb1yqBRDJAslYkzlJk9t6d7iHjjsPH1a5Y96Pe/nR
JRJWNm9mjCER2H9UnvYFR0IVMDnxXdpy8QFaK9s88uksm880JBFPQ9WmRa/MTrneyvKKliPi
243tkSVqBgaXpf5pjt9ggk9eWGd5jQkwjFdICGBZJSP2vqu7SMoP98irph/tXj8Q2j1EwWkh
nSyMnN0u/+RsxMGKmhKP30tJN4R39i3iPSNwfo9YKlYp5SozCNH1nEH9Nken7tIoAgsxdsbI
RJMkv9Ma3Qs2iTdQ9Twdff8dff9w/3CvownWo4cSbAZt5gbvCOmMHkq0CDCsOynQ8pOQ5B10
3UmoDsTrNJ7PAtHBPcfGJ5UczrVjeDORa9QsgHv2UL4UMYhtIvvkIjQIuMOvow+GhRAdl3Sl
nqjzXZTLSDh98XD5Fzt+eOL3SXyIWg0YQuotaVy9TiVwd5p63gzt60dESGm63m8KzeytTlrc
ZgRLWrzK+pricpM0pvuOsq6+Uxo6uCJXZKg+lObVoof5XeD++Q/o0ee5Nll+rDIXHOOynTgm
ry0kityEnswh5Ox0eDx7DT4fwklMa358j0ntSdn4cF3dbUtrSvwFwlC1SKB2Ku37K6OlQU5O
sqfK8aEDuLkrMZe7ChA0dFBBT3bVTp3mvc5eijr6eKJVTqXBnp2jkMPriLNvTijgBmn9kt/+
+jQezrPNQ8qHj76H6aWE+783tJk8VidCLx2hcw/aTE4kmgxxzx5xN4gspYuAktwfzj33MfWj
CPM199xLk1ApcLN7HLYeKdIv6e4pqIbtr4VzD5kFcy9y7wPHTBZM9gG+625GnsJNk1jndGPj
OdMUUoYpGBCp6I+5N7B2fyt73itgRzpS6/79Q0M3SKsWstQCidO3n6WLxQjM9VJN4D1JVWHz
Sf9xGf0zfjZjgxoZSEN2t5Uaml9o5YZzC5IWtQltrJy8XUPT6nQqtQ9jdUVaJk4wVy7cckEQ
emhMAusP0r+Of1p5Ad49ym0V3hm9scMlusrssbTdu9HUYbXY1zLL5dSz5vDId67FmeCwLjlJ
pRRYh/QMXwcfrTmLb0pwFCIERpwtBfK9Kfr+H57egO0DkYrg/3X5RY5+UEWIDNLo7nogM0P9
YZB9v74/th8aJOke7Q55f7qyyiz4UgD3gtpIiQx4jciO+hX+mzIbIoOpu9UmO4eeeGk9NJkE
W32uIbxWicup3GtlBOVMS9dlIZBKvt3dWtf3ZEj3ClCLVx3HPo3zzIjjuqOii9RcaLqIyA2j
Dum2/Mz2qSlmgXOKw0clBR8DA3tp8Fm4//Olzd8ws3Kjxwo9sWp6nFcX9LlSj+wDJ1vbDc06
o5KevfZgrkgb7QM/5nV0L6fP9+WIMrYkilxbdio6CqzD+gj2oYanFL7q/mo5Zl89G5qatNt4
SqGgeDZUsa7DXgOMDElIw5J7BC3TbucHDixbJUnWx5GJGeLFaWufYdO+xaQx6x/005yddq9x
De+g5DhiWo/O2OuHuEdeyF3kWE3gfIMbrHinFT4jyXtLbFCoMyB8RrpEvEBHbzWBvW+S803k
NGfuIvtqYh/vTc5c3GAG7f3DwIFjOu5O7Kv9khmVVcLNBK2Iw4x2/rjJFrv71KsFpur5v9Fu
hz2WKNHMnbXJDRLpMHVGRlOQgG/PCsZxH3jyhhR8NvbIXP7bYlecLkEhY3Vx9wPTpOxsZPTZ
yNpzet+eL/m/XNhT7LOrTfnFXot2+WGaQfIigo7lJXUaioEX3ip6dxcTHHMRyntfrmvMrGg5
oGcvEwaW+vHThXEqW4LEfcDIyTl7mUneEriX18q6i4woRuyshf5qHocOPE/NXlMp+2FnPXPr
yuWyYs7XPl5FxLz6OWSA0k9asl80H8zWkTfd2pAdn25efeLWxpqN2WN1777+QAmryl5bu1qM
3FNBsdiFmzNNUUUEhlF6SsXP/KwioyIMS9dv/NAZlkhYCkZ7MHxPltgiUrhzRWI40O12GT4K
uoMy2VtFHufceJ66u6V7Rg48Aec/uZEg6zRV2Z+5D0hJSyyaKC+VG2/XkUW+Y1g7kXWvgVVO
znt04gJ6p3g64S4/Je9rd1n34rZK2HfcT6eKy0Nr6ju2J5m7H96lP6NOZ4hcJDlsUNpWldwy
21g0754sE/dNivFemwxPTGj0zPSO6ytn/BjBeXeBj+HeZqIdqlu823Lu+nXN3ECtd67L7U0t
E6S7gt0uhpn5wgW/FRk9U+Ju4xOV+sdPpPwHK/q4vWyaQcTJAsyDHkLYFl02O3+vqXLHjtfU
cTcFuYi1NXPZBZ+JxN6kummYGgeFe/LV/6ffwn/wjg9OPyBwQOCAwAGBAwIHBA4IHBA4IHBA
4IDAAYEDAgcEDgj8txAI2+/e3//SyQ78zYSe32aIBeer/B82oefREt6XfzOhpzh4k2wQjr+e
WvPQ4SO/z+jJ9m3Cz8Dfp/RkYwfYD/PxcnNxsh/904Sfhw7zgdN6qvML6Jt6+oUnFglKXURc
/8nL1//Rr6/y3xUUfjhxUlpFVeM7Mx/Cx09V7R1CwmfULOy9Hz559jyzTdnI/MbNiKevfyN+
Gf3DpctXHO79LGNgiL6D+WVI9uzd6hG5BTBvgb++qz9W5be9fH8zDei3/X87DWiR0n9LtR9k
ckDggMABgQMCBwQOCBwQOCBwQOCAwAGBAwIHBA4IHBA4IHBA4IDAAYEDAgcEDggcEDggcEDg
gMABgQMCBwQOCBwQOCBwQOCAwAGBAwIHBA4IHBA4IHBA4IDAAYEDAgcEDggcEDggcEDggMD/
XgLgJHq6gfGmItaNbkFBPPuA8BvXIyFsqjv3Szty2kmfVjSDjJslahhBnxZ2kLzlnroXEhYg
4hXyq6rg+wwUHSsb3HjXwhctcsD3pSV76+xZeYQV8kaXm1TuNCTPL/VG7L4MRk+77gPj1i1h
z/skWNDhPDN3cCrq8aCd4sF94J6EYGBq2OYLxMAYlXNbv43iLdKskvvpxhdabejFNoppsqav
5V2rTPPYMq/hykup/I5tweq0oR338N6PC+9taBHvd/751PU2yB29+0BjacY+cL4E2cNZfZs4
sHe3cX3T9cNeq+7flCiip1SNofkrozH0M7XE3TNT1t26I9c0r/19llmecdaPKZntaPRUS+tU
6QlC3qUklu3jwSr/efhpb7v/vXL0/6bk8JW+MIoZKcQ6bwcpWXfu/81N/C/PFRJPHNn1Sjeb
Hgsb2oTp2/034kBCqLQcp05t/+XF3F2xHoe5OvWduImChe3m27Ntb/yWtmRCSKEsveGLG7Uf
xZCVWRs5BYu0ByEi1tWZ1Mqb6trNjqXO7dML3pu/DGUob3VR3Tj41+YiXLS7vfL5ENoNHnnV
M+7nNcNwsJ4Jdetsy03FOyVOyEtlStPbLyDvyptbzn7dB2Qb3T5kDMBzu/PmMfq1d7znP9dc
CDMYF3JC9669T6GEsC7yKChkT5zZSN8Vii/Tsal0/thEW39+RxTdn60dcyuPnod7arwPPKCq
BI4MxN7CBocGIqXCmC17szMSbZBXtuZ7l52WPJ/vhtb0MMIUlVTXNd94IY3qFi00K1/1psSP
5QO91tO1n3UkpKvO20+0smYHGtwghTRG5a/bYafL1gUHXrVeRJ7TU/UPrFjydh9V0WH6TyrL
V5734E7vz0971bt5VGR6vvVeMagVJ2HN87coZq47vwwM6wy8bFsMUzSHOnnnGsl3oJz9kAKU
4C2fXOTSOF0XqZv3LH4jotp2+Ub6rjpvC3nMYU9y0WKHkRV2Fbo8vXkTnNBRG70PqDgNtGN3
tipuIId5BcOaLP1XBv/nXcqmyfDKR/Quc1Tf3PpWANhwl6W4uVtwRvvw3UrCF6VKmTsRD1ze
4OWEdFE/DnPnEdrehBpHwZa6bt5GUYLTmTMuk4U/hP2hGzbXZYEzAa8rLcvdPRHhvWQc4e9C
tv3DC90fH8ys7cW4j+79cEeEHGKxeSZvtCSR1Lt1npa+ef6KmoAvetSv8tfh5rsShsWrFz7b
65dQGYjEwIkiayea+wSjuMj9c5wkY2cl1GAfoOF3uzuRBOj1FnMewyX5hbMjv5Xg59fmcg2C
Vu3pGsZumcFPxtZWFHUnO9Z3qUcvDgzcwnol7ex4eT7pbd181GM6sNYYzdpdVeK53KIVTBjY
5HFQFfDfLMc0SYQocbMqPDVQtCXtuoVO3RjvofZ1N6g3SjWY3GWMFq1fyCvc2q69GrVOXFB5
423WADMJfRzXGHaU0oXMzwxwWkWVC4U3Dnu2P7R87H7FM8ZhdH0pkGeoKq+y3EO0Ru1YMY+j
+/fzcZVhlU9aV7VUQurDP9/q8tGOX9ctiPCvbLxjatGX4H6+j+qH52HUu2R1EYPoutj/Rm3y
n54VZNGPRT5BrgwdU2X1El0oZeNSKU6R8wiE7hX2sI8TM0+bUDHC1sJfAsqznEUeX6unhsd5
H6+e+SrkNWdsSBMYNzP+SiojZkcmUZwWsj4svL8Qxx7xD28Sppsav1rviyI/2wcej57k+K8j
+KXyWUwM6vGzJ85NuuX1w0nbdoMqun9YGDEgOoMzkBYvSOHPjTkXnzcIeXaN57dnTUbn1NWc
85Mb3Y/O2mSO5vYxt0JUjErVgiIimyaMnr45lJK3LPapnoB06lqcDxm7zpNDXhUbxRtEpfXr
Tq5rS1x4veDttQ9AMZTBwflVk1H7Dn9qTQy1wlfE5UZ8RQ3WI/Dxjf4f3xIcRQLcuPb6iboD
n7MqN6+8FDND5nLKq/uXH5Vw9kRo4nvPOQmborYayxxZ0Jj6GdsGV7HdP3y6/QfmarkQL9tA
X0O2KOy3zuVHfoTQMx5I39GWnKn0S6dqw/IXPnRe1Bx3aPfLrh77ZawhLJ80vhwtj8dIw4KC
Bke8Akdn0FVbqOeNCmbTgYozlIm+qteisMzO5eh1+9AzC0ZOI6icqbSd1N2KWjqnZWVnQfIW
pXHEY/lRJ2vraVeWsyBDfBYDvhNUhAtX0PfVNmrlfP4n69B9oGjq5JPe2XejoophFnOeBVIO
EqY9wjq7VqcEUO5Lzzp4CtIZRhnGtAwxnJLDT0aNN3sDrWu3GgOzWBE/heXMa29KnBvJ/bqq
i3B3Ug6ZOwd1Ql1zC/Tn8HbkjaPFy5QuBqgH+p1H7FEaodcrftKMnru3VzOQ5lgXvQ8Mnihw
3e6PMICONw9O26b2exZRMHnVtkWjLqsG2194ySm2ZtY9wQpl/oiuKfwNstbDbHwhb4z16Wmt
kswV1/RaWr/Qjmr69a7KyQJgK+9XSui6QBhmITX0TvVt26sTZmK7eEMasFPQbpbBhcdlYjcX
B9aabK9mzr+TFOkNuaAxXYp6hGKbjtzb9nISaCnX0Osb9smbSJWphK1znrOvbbLpKzOvnb/o
nOBdki5d2vyZNdnr4Drsv0uzzdep+PSR80J8W0tqA7OcX9oe7I0O51rjywskB3omPzWFtDzp
21EpWrGscBytSnBzmsxtMjSvat4eskHMXCVnr2/flOzMb/sxeZrMelalK9Sb2UXNnhZsKVc3
XddvtF/5fuRRSLlW9W6cS9eKwoMXuqwy/XqHFb1hQ9s5ihaLHDa4krq62zMosm3DQ0XbXhiX
/T5zUnWsvmLOAOrv/oqSizw/bnEc/6oHjVqqgw0PXFJ4gpp832pmvNUxW7G4sQOdX44N2yTs
A6XIzQXn7knHONA6uOOt5Veyt4yplvDX1K+7Oelb5LQP+Czzk7pWRLyYEv5S+hVFrWB7N13a
057T3Iu4ko9iUvRp1Db+nxOX5lTmpiseHz2F/yzZ19Ym/dB0qVlpPrril84zYUKSXZkEW4jD
6EZBZdbXtLN7Z04VrpiMTeuioq0N8PZrXGGysFwd/k2v3Rf8JYm6NVfZw/7A2edzbayAMWxx
fOJrI30vkjd7MrPBiFyFA2dxbi/cByaxu7ho7YLA95fB2kCi9n7hHWi+PvZkm7CI3BnK2gcu
QZefljrsTaZd2wfUwWK00nfGFMEqKpMVQDafCltRQmr8+Bw1F1MFepi/4He5JPBpmQ0Xcqrc
ZMPaV8Dk7XYyorULA9OMht13tVBg/smTrxpsc6oy/gDmrwT2jMOBsktD2+IynjI6aW94J19u
kAn+4KzU+cPxfA7dlRHIz+FZFgbNAKrO0yoSPtv1CFkFvVwRpc2Ff7boH1JbcFUUfKkm0Ns3
GfchZ9PiJDUdaRgXg6RjXSk+3w3d38nCaZHwhPZ80s5b0IJ6TDue99RzH7idObkCdmkNb7nj
9n7Z4rCdc7ujckQ33qXNtq8ee19h8q4Bo39AWdAMlXujfh4ZT0ci1cHX9qRc2H6yD+Bhz5p/
ecCHfOWt5Za9t40xQTa8PiWkKeLCt0S5qzS9dT7LPEwhwVVxRZOZuISzV47ei3djZs3duaKq
tiXpKZOx93ykuKd0j/+Husw5tOTwUuAZzwrc3pMRWC1tJvD8e1qYFxM0gTXlvNVMbPLVYz4d
fbq1rsL9XdR6Js/Ley2Gt52GZRxCFyihPs5l8SvHXOd8bMfL4hOZwYjSFc0K97FP2Pt5K27j
w131q2LhQZMqqYvrXxd4Lii8vqAhvLt71KjngU6lc9c93D7gaCI55B143bs8ZqBV/acsjN9u
pufU4sDs/HUerWWKxuzeEH491WjvOXdRf9LOUvemLvtoS+tMmY2tt4w+NSsLr92jYuYvFL79
sNp0+5yN0XHH9Rejpyo7Kzu03GvX1Hg28u3l9oHwO6MW84GCn2EvxqVzVJ94t75xpTiwjMM+
5K+WZQ4QZCC5g74a7duoiCaYmrtsjMc17lPUF9fj5Ccy77jp3rnfhFyIjfNyWrcvneW2ncmc
Fike2b4Q2XejNlq7IqOm0tbdsc21Tjkzu1Y70KRFj1ar48yoDy68M5WERs9V+8nolxcxoBkx
8B6cpjU+s7fMMMz/hH4lfTqnRVws9ISREByROe7OKr8ovXtb5yLP5wjGPpBmfSWyrkM11N29
d0UdpDQ681q0E3mr//65KsOmok8uYABmPPGF2F6tIqSC2lmQok5Jpn3aO4E2IgtMpcQhdOez
HKnveT5l+ZaOCGbHR/cJd5cipresFORrw96R3vpx3S7ZxkXGo7zGiEy8RStVpyHM/9RLL2Xf
JpKU1ITCImK6SauL2rOC1WAhKCeqaXyLjthTa+e2Kp51nRv121a48aEbrtm9tGttlLWBrlIA
k+Z+r4D325UcZa2Sx9yy4w2+ipoRHRt6f2wnSu+Vb0K++lS8fY935uN/ERToVL6T/4xgaFP5
2eaN2BNQHZ3RgPMHRWv+ciHs+lpfhyz1661s0QykuaLhkgKRqe1FjCYvGhFcmywj4zE51Szx
Da2ryS0DMj2Fhjfff3T9QfuCLNHdIm7D0mmW50Ncs5C8him/S7LiKTOwa2h75D5P0dMIQSS7
WReRMyIyF/eBXzbXtTNgqjN0mu6q2h0xKmpAROFGJPmH/lMyd1C/eq4etdDajbvOY8+YschZ
mGUSxnTLVQxqezi//kMr6n/ICbqKzCJ7hv98H5FJ82ny7bKuMjOBi41jHD8Dj7TrfK3H5iPE
k1sDHgRtEd1cbCZXzstKpfg0CAZU3ErtIbksGre4KPcttiszlFGxgi+qrzprVEzEe7fl36tj
rGrf39oemd0lR/nFImEyeFypcxSJ1tEOFwzwn6acTU6OIkJGacuP35uMpUavqfavf5E2YtLc
xmHkEzIstWyqjbnV56LFtfF7edRHxuhBBlzQzNx/EfqHdN6bH/osZfAlyrQO5qeORVeMQx8x
qNqPYirYDp+toqvR/xHa/8KYDmQTbd5m3GVjagIfS85oAwZXXbfzC4/IlPs/mLT0Vd50vGBa
gJGeJWF90ppdNGzb56wLUhv9uc7bFOmQqTdY9IUpvKXTym0wcCnmeHOi8kkTTwq5aVwC0xcd
XPGkaaVvOxEjn8xpXD8dX1ejzDD2fOeONm40tuxNKVxfk/3CzBrgtOzULPNyJJqhb1rFezu3
i//gsSICvrxKPG7Sbqpbx3nTljp0WY1341WgPUbKud1nSw6P35tN3tabCay1qjh+i5jTqi5L
K5DfjcVgRhwMthEGfbM8+MSui6ULOVVj0UmLO64Wai9CF5eHlcLOas7ldoJ+ODWHpKwIdW38
odJBI7B8JykeI0cY8PCZpRRZtzFJlT/MKgp9JTiOBE2lgG+3C95cmXdaD6dPh9hrVLYQHU6o
6qYiRtNsjpcRkfXMN2JaaiR37W5/UqljbLHnWXL15A3V/mfK7bMmAQz02odqi44fM+I++38J
2HHvcu/P++zO+eMnqvU2H6bqiqCnbfbeEiUt9jyzdrZiT33jxQ2yc/L6OUMlDqZEzi8Fxpcv
pzZ23hVscVt3dVlt121s9GOruFaGna9HruQdLXmCN2k557yJ7p2frTGs27brqpmKa1G0NrxR
wp+ICutVYSkODNyhazAlfuPUCsS7X10Y+eFLcNjusqcdo3cnrhfLKtE5VVrcEJm6ReX1IIb8
uNVssAYGb+Kuadx3iw5u6fLCmyxyPlrLbflscgr3ysZ0LvAHqZAFv3IEgZdfsSr41gjlazX+
BrzwfcxuRT0J0jKyotxMkm4PbrpJ1c17NbuZNzf+hcfxh0lP6htQ5xM3cR1eU/Oj1b0CDi3u
i+/coEWDKz8MmpTER1tbDbyYYKTyPXacf9PJY9llqGtBwLeVPKqWz+rKut6eE099JDmxQsG9
fzm1yPfi9mbH9gNHBSsCGLUefdPK0/T4S8yv2vciyz+ZoC5QyUGejrVhb2lXNBRCzm8KUvkG
HvJb15JvjIG3IGNh58eNyAr7Q5mxgf3SPvDSYnBTBxEkK7tAdZ7jqY767Cinbsrn+EJcnNG7
xuQUnx9olxzNXXpWX14WfOqB89Cd2vVeJIoUslnI42I8yMumfDOybUPu7VspvOxvxf1ilAEH
N8jXhbUbTe3D0lCne1/bxFH69CIj98AEr+eecNAk6tvozPXbjJbCl3Db/aM2/6+PnxJ66+EV
tOXAU92/Z8vThx4Y4BR8kV984xX/yW2kweeopS1VPKZib1dypuwFoM77pqom74POo3TBByGI
4oW59W0FL55TFdc3LUpRERbnrc9F7q07Ti3q7tyCfVJ4wnN9adh+XlFUK6uSZRV2aqAf1AQq
4njrZOdE+JOGuZ7Myh3xCw57PGM64V0XfN6PWu6C76gNf9qOtoWXqgTa60TGUtrmoT89+ZKV
OLMId/l5s2R31yroyfWMgbuh+vRpndOlqk1Rsa4ivlO7u9YhfmW0sKfEt76xuBht8u1SdINV
b7SqVPBTU9KgCXztphnyvmgoymDPmhy1gucPSHQOQRl+ppeuw504b3dsSS7Uz6KqQjXdgm+t
6iB+Gxlgralc4ykIevWMH20W37hTjcwnlr/oD+mOndzGjiA0Rd00pUJON7qlBoZcKS9WtNxO
VoG+cWYeVx/AyG88Ap2WF8j8WNqDJOYuHsZsps+sB57zNnPDH4mb/9hbsKzsXPYzqvdjJCd3
to/v+DaPjCf5a/eyOFGXau2/D8hhEnzPG/1mq31TLYRX5OekwEfIYgc3k4spYZ0DhNBW9TRK
8vvFoWDffnYMKmL7KpVog++/U6eLzHXMvloDvuHCyKM3usS8d+nyk8TQCXd7+Byqh60ztaPh
SlZ5rDhmYSrrs7JVF6sqiL6ZGc00WgvxtW1k9oVVs0bw0b7TXU7xXjvG0DXNR8vtxYpbZgpx
tAhxFnLr/S7ieNnu13L7O6K/qJnjAuEzBFIJ+FYlp4xlQyb1dSN6GVRisqwI6pSN7WZ1+1Rk
Q0v3Vlrtc69CdaLjzjMf6NubMyZN6JRgkVSFR+sT4xQnjUVkeVMkp2NbWd8irlp57546vMDb
effp0Nhd+6ptcTGLIGjh8Gp9RzZRR6fhskr3KqZzjtQX8l4z/Gvh7ZLU7/YB9yahC5o1vPG1
U+c/uSjMz1pyun+ccWhIr7f3FRdeFK++/eZWDZ0m4S6T4Mct8YYqZ5neAlW7PCz+RGw74EGK
ro7p7F7EE6/QVq3nnGjKFW+56Hfqr7IHG7derI2/QkiMznbwfHjte240woo2qR78gE79/6h7
84Amr3R/HKXKjFYoIqAgwYEWBAqI7FvQymKVQCkElNWCskrYAyQsWobKIqRUkSQsqUEDJBBE
CCGERQUMO2IIS0jCJjshrGHH3+vM3LnOcn+9vXfmfmf+Oznv+56853nPc57t8zzH5b3I01mT
TE2LW0gQ4IVZxCaamD0NjGyJ4TBCV1Jwm9aNKO/4+exvxZuerH7RUd2IfLstC9qMKOauxJzM
LTq87rlu6HuRq7fXQdUP9K7X8GJGqJHajLacFy337rcan/lb5vwX6fn/86+pTV0iTmvHnVzr
TmrqGGHpRrgKbB4HGJ9gEq6RWlY6eSxHrzRf5HXCdCaGUIKPu1HaoB7h0LVhhizISLe2Li+Z
8BsYUfTju1+t+m5TR283qsMJAuURMCmkpkZomGVnJ+Tcb407oq3jO0q3XSIidGvBv/O2T4pY
NcR74oW3HMZxh/ddGK6UeYjB+HQMTjqy9cuR3+eJj2kfhC8Ew44vQLRhNzodZ5jpQfW7WLyp
lYsAypuca2wgE59IX+1v9OG9jZl/bnTXSs8xvaa6yzXRv4jhbA2yinJx6iFtgzxS3ouckFFm
vhdBOjRuGYw5U6xo+NAqOb0rJQXc8VCNcolG+sllp7jZO5d/sUjlyW2YxYAaC0x22Vf88aaM
OOCrpQoTsgN7xKMNRt6sn20lkGhyvHtIaAUUdbj8SFrw9Y4WInaqBO9No+lIQhxGe5KlLsfd
zgMp3QjY4C8rRvK7ok1IPOl0tkpS4hWKVflhsAEpuvI8obZOa3XMKpIRkLIU5/HO9OT/dg2J
+uFKA+SgUtFOrHNLMykC/ZteBI4N3emFiQqlE6dFj1AKMxQDbUYRvDJXZ64jCw93JWhrv2bB
P1e45DZNesA/mEb2i5B6Tm4Be30dqIMBv7u2NBX/IvJ2d0lehreV573XQTR9R56ZvGkIdHlH
ylnPcmd01i2p1OssQk/ILBWURTOGG3D44ULufmu9v8JVx/lbHZNE9Xz55LhL7SShTnaQGEh1
CBuuBQeO1l0H067JCAasMzrsrHYsntGz6QEUF7qVUZSN4C5Lv4G6a9Vo5UA1OkY9F4TLyuN6
7jvZVJ5wCGpsEH+Q0/8AW5pCzIvHNJ32x30+/LaSSAR3nPfhixYF7bluve1X8rHjuR5OHmkz
SRh5XU7dU8r9eY4Wf2Vrql9FZ26CEDcQHicX0NIbOaxvu907E7MMXtIjTkg4NJxxsXPOr4tZ
xknHzG6iTPKJ6oLVCjzWjyfGd1MsAQtoJzHDiei6GTrIfQfR54beWufx7RvP7FGZHQX1Q0jm
lvvxgZUQzgq3L8rW1EV1KHdjPH4pAmtzJTNGX4OXjHlVqqCOkp2h5aLsiDhE19zczoVFdqJ1
ZrCuf9rzqG6FUdt9hvK1NgxqJYZ1wVQrvVcXfXRdyHGHjgmPKezWQKcm7UO86TINM6YEiUvB
gZM6JrjzMdfWERU+gS4I5YXnM2I3e00Ugr+MfS/CVz233RAZvXKDP3ytQHtZwBULfzmD60iu
9RnPkTJ6kBB/vSL7biCYp3ljAaFqve9QVSLA5TdScIoJQ2wWNr7nzZduYmGvZh1bhZo6kH2p
qSlbBHVD5amUxXcJP8IV5AnTn2OPeYIkDujRK0cahbDCfAxofWf9hWmmhEocIWCtxcA4ZKwr
TJHK57gxBRz8xZ4A9+rw+ccea/ESd+KMmOStODMIKcm3PCH3G/HJIj6k7AnzRIBb0JUmAu5z
n7FhqqRQR2RSjYD1ViMoKZlfFpv53/LG3z4vutox/mPYFj0iJDCyy+RRUtGt5i3vfU1ZpfhN
sW/6Y5GjoAlMftPLY3eJ0QWrs12U5ETGvjlNTDS7bUPd+GGXYWzwWL6OBSX4tobjTkeoeFnp
2sa7Jg8CMSI2fhiOL9d+MrX/+c4D30mFuyzBWuU7z3XQsYajHhUW+iHhc0yLhja0mDur1irc
r8TR6Ts+v+ep7ZaqlCfdiVEx0xuqYKOML9fIMVOv2Ng4cbuzJya1b227pGgavpaTWC1eT1yz
Hu2a89UDnxfYXqn/uuN1c2vKxh9NmIYf4FO1cy+nwon+guWHHkO8E81x24UGpnspJkLSm434
IYKf5cR+Uo5LySlXhYUYHDyXaipK8F1zmkKw2HvKzeIn37mmbg6VO/RQPTy7wA/QqOdiniyE
6WpikaO+d4K3vjHqCyMsN7LzvUg25YKJs99VWGyFlgvktHShSppqS3j3xFuCulAp3Ls84QDD
sbUcjBSvfV7VIC44fTRrArt2f8dFA/NeZLbctlUGMDa+5dLGXFve0rJf4vuEGAaVzLRESjss
Vy5etjg7UeQAA8W4rCusvt49SUCyTPoCZUtQfkwnlkh/85xPjxZm+1iDyZRt73LlKTkVDMI7
IRHvY5tU5W/uSmP2jit/w8OK04Y7jHcSZQAX0xoiWJQ6vo6fqgSlEBbfjGXaMhbIs8a9usJT
D1+YProHBCXQa47yD+7uOIKLt9Re9p0PU4pPKe9FIlfEWfcGtCeKi76ZzJnwTQDTTZsYkqsl
edqKQxdMX2f1j3zvUkyI2pcIuW/SeOtkdNh5b/NU8mTD/pKpdXY/Mlvhq93rXcOnLzPVcJqc
fNXjtcq7j6BRCWsK85A5Spt4lKSz/Ql9BbBfh50dp08d/V7kC98asdtvTNJXHGl+1fkM/vEe
FHX/x5aOl7veXSKL6DjuSkm+LdQHo3WSkfwuPbf8MNdzPdr7IrfKDgg0RThAuqjNx6gkB69W
VhJxsFFqASJ92VRBujccTeY6QHXfoQuWz2z/LTf8P+wRaxmuLnUl7+08HKbCMOTaeXRaAEG5
rrNz68xnRRhxUl79kg/TREJCO9GpqyuoHpT85J2jHca7XLZDFwmFJKhh+L65BSa+WELq8vfP
N0u6bAw5y4sIA81Tcg1FGTivuHgcJUyrFwAkMZcHNB30XRBYX6Vy8T1oi5Sujt6Lz6c1uac2
tCpnPbo6u2c2k1PBx3o6eamI9KFsm7Q4+S0vhcCBMr3h9PzxOCjzTGXC8VDT39f9driCUnO1
Qq+elqRjX2inSd5YCUzhS3vVuyBziPvbtcQfo38+4JEfVK1f5nVXXiOR3URcdOZwmElQtk/j
zxO+PgOGKvH+uejB5YVO0cTeiDg7Wkfm5JCxMS89q9rQir0wJJioTM32ZkXaVBgWt+HiZH7z
Sx9IVBHC2J40KWK1vxdpWvn0+xe/9MB/ef1w/rxQp6yLk97PdwC5kohqKRs3FTTClge+NzUp
F4sOQ/nMZEfzhx04RmjmSP/e8XeihfN5yyvJ1DJWtAW6LAOOjYs4aVJ2qnLRCiXuxxHDBSo4
bsm/IpRUvpbfojB5Zp/G04jRmC2mp7leT4N4EjkKPWl4pTVXLiG5GeJbwGQLQVkZVo3rWwZz
ezMm1mPz0a9uB0XZ9Y0+4vfBbFqZxX4+3wF+npBeOvKteHrxels/eRj91vj2q9flfSTVqIEE
ZU7RcVSt+F3SetnUVWUlWq9RWFPcl7GojCJlKVOlSYuJ19ATPYNJTxa1yJzJefhcIWRA2HBX
P1aDWSUP7QIzCL4LyOUzsxiPr2OnOdLM5D13ivqiB+4w9lyVh0lXlH0ZKAlluyE8UHT6wpxN
w6IdHFdD+6GvhK64f8q5AlKCyrdKSTOfEetZr4/6bPwhFFV6W1w3MHJgmeJYo95VCfHsKVIn
fC7fqYU2W5mOkbIRhbniS1Kw5YvH1EeSQHUt18Gy7EXxLfxa9NR7EScqJJb5XC8Wp3mqlhtl
iwTfDXwX/wy+J4UPOUeTpcPAaqGrB3vSJ56RpyZdhPoTbFS1+GrSmwEozdKuqLP6i7SdmPHX
b4lryHVfh40DXD3xFHdNBh7NPR3GdU0OW3G8W+Qz1rwj6c7jC1pNE3C9Qdl5blWenbw82660
hCssBOGYzLww7tPLJF6xguDKrHmbAc7SMaep3ssRvcLKrqkMAHbzL8JTxILebAevfE0ld3HE
DwZEB2IEe/nF075MoaFgQNFfYeTog24nvW2l9NPVS2+LU/jb4IGmevBeR8QZ/raEmJEVxZ/A
GxjzfNM7U/gu4MWb5bBx8xR8yoL4gI+8ohzq0usKGEtyR04tzYd3J/DOf7lw//EX3jZmZGTb
PH43wa637+Tg1QHilpFDE39PL0grW/SUDVZwxe5fyeNLye3aV471npk7Ffdz+NNcm7vIR92n
HBXoCUmU0DL7RquaHyO5yCKbL0xRjS3iIjOPkD2JC5+W1im2CL4RJxVHFr1LNMAUySfHbkqB
r1RsgAp1FSe1B0RmthnWno5RGvsZyeXL8l8XMbZlVCrSoYrzFTDAschah6WaHa23cngcFhE/
NjBn52EUqwPqdAwcSYxTkDd9/JRGC683xGBLqLrLjwQL70WOeIPjI6eAqP2dKE0kXlE6bIYI
Z8gLCY/d4+77zW4ZhYE7e2fq62fFrnbNNHbBNaWgGQNNZm2owSHWqrffwrLanciM6A+uRKtB
6t2meA03gh/1XlLNM38COHFmI7iHLeZBY44UdGGQ45mqhwxlNHfCxulP59A5ZJsKo405Ek9s
Uj6oxPktdnlZr+Bm5NyX9km6qdY0SLFQnfpB4oMTySHFNkf4XYie40bUp70hDKjbDzzIJso3
4iyJn/Tjy7l7PVrHnOATkSP41FSsNp+vXkOatt12e7XxRGHVZv5U1xQGhtUNE6qU6UySdK3o
tj2VM4Z8ILYR+saEHSaQW+ieGQO/6NPcWHa8e6omCi4MqkeA35h2S7jXtXtjo7SuL3BwssnQ
jBE9pO6JbgWvSIVVy/mwl+7pkd3vRheFL8kJV86FeN9qRkp5wOk7LxZdJa6Dv41C8pKLZ90v
9qrtVZpaV3hYzJ3Xggrv8pYQReGGmBPb2icF3lAX/6UQfpdjiwU4gEFUHhFL6DWenBQLdSMs
ium4gfqgEyndfTOvcHDtTSnQjCmZNyV6Z7j63RC77vaga1drAdMaRzu3op66TncIv6kwIa8r
ZcDxbGqvTOBsaVDcoaBd0Wv/+KX/a0c8sOoR6YonUYMIaWdTiURiQa8k6DrmE/UpeyJDmyNV
rg27LZ8dpho50TlMfJ2dcJYZNp/JHV8MCSwhteiOV0J6FHQhjpbfP4/5lxHgIiKSTcUFDFoj
TWc8IdvnZTobnm1Ns3K0Tzx8LmS4nTY83UU3BMKvJz9TxltvbOa27P9uaZEINvQartmuc+GZ
xsRcB907saN7imW/+fzoD79E0P89aNTApICG93/kp3y9/1yopqPCVF1pmqaj5AJLR2Q13w3L
uxapQQ1bh3kbBaMSmoU037LeZEN/nKt/+gOXxFBQVI3Jw3Cb6ueqUqaZ23ArHlNn2cK2pwuP
TEz0bomMfxY7NTUv2jaVJGXi7LnCeTBCDda9tGYRvaM++WPsfj2gBhsJifnlL/eWiz1SNtkR
i+PfMXVXp9JzACktYdq3/W5eNphll9HhC9LvGWQ9qJ1rBPH1xgH8yDSi0ZXse77cfTOjaVH+
hg9rRTJazGSPHQ+cEg/RFX4mAebEX4/tH9CyQsD2euF75jtdcjBeE1l1OvFmLzxh0IQSt7TK
bzmaPVvrIrtRXYgol3Ze+1TuS/fMfeoTvqMT8s7uJqqvKNbB2nwXfJPiZthgoKo8PtnhODJA
bMxIEfo90w/bhq8O1YXYFSV+j5iy2uGZkOew1dLplHhZgjbTpUF8unrbKgJDdiPUO4YEZ9Tr
xwb0UeYBTaHnKX4N0EE28JHfTOmqKqE5ZrZj/YfNGJml7vcXSFn7X1zrn9h4IdhOvORxpVaN
BJ1yk2vxel6kGACFm7cTO4sWRRtnPCQ3NVAwNIfjzRvaUH5HfFmZmiq1YBXp8UEgV/NmRtoN
MsJhgdeHNzxTC/YPPy4dwqO3RgaFmvbDYkjmttuK4V09F5dD8+1kTnPLdfl0J1Ld7raPihrO
2+eZ6T6qTfFsrXRt8Hfh08/IVuCzeV1y/e47lQgNjFjkcN1vRhPe4I4GLAX5+ANmfLwpbGzC
PtFrzTRUfB6VnpEK0/T2YVdaxqpRLR1Ba6JOv7SC/8nXD1T0RWpKueCDA9lg8WDp2IBWBv6d
Pc3psgmovENbcydJqbQ+Imdffu6UdAxBaMd6SQtPfE3s6xkWsxugHX03HzZM5D3u6H5TKR3r
J3o81I+ThyhGbxzojah1DjfOgfkzxsSdT3TG5We0lXQytmzTCvmi+KD4U1sQljYQWSEvS9kU
Mdj9oPIMD0AEk6E7o5FdSLy22HNNlrxPhnyHPTnBunTX3b0V5XuW0JOYcKBXd1tuDs7vnM3r
8B4pp6bl7lwh6QiYGC+O2Ff926qr0hlZOtSa/KbS3RjB8lbsqUGq6q5rGBlwgL2NlrgMDltz
i3IhzLpd9STivpBLoEOkXCpmscE2jefEs3KYPgUZB4kRicWwQkiH45ijpwylyJOMWZ94E65e
sP9Cr2SQ+7WBdNSN2W0JHTkPA+UOArN0+1Ok9CCmkPdjXKKHzTd2kr3vRYqMclsgKli/Dpqm
V+PEOiHCv/h0P4plUaCgrZROO+3B6OM7TFZgqJEjB8t9SfCz5Rsv1hRMSwUGJ53Hec7sserH
OpPlypc7CCVA4DDHMv5nhPjdAbHECVeCoY1I9f7jcOUJ4ov+8jEmuNkFthGScJEnHHE3z872
CuZ2LFIJzJEOwnx/RBG1nD2ZaxEJuvsk6vGkD3iPLpf5ZtwaM7abPV/rqdDhhATfy4ZGLH4r
cYlpQgw3x8GwKzGVmCKoxbO2YezDTqQurCVM+HIGK2GW9/PiVScecyttUBhANm32m3t4g7XI
zBq1RT4Tfy9SHcN82TUPkuka7+4awPtR43U9W9qXt0ceD5xZ1HOxavemRzGh+jHj3sjmpH+C
x+m/yR9xAx4yxUQ+exafphRIJBZVWdo88r34KS1r7nFH4yfm+j8vlPbMZdXe3ih8izWw0rnr
3egqDAksXt91xr9rZgTicWc15NPreBFR3d0TRd+Nj7DCQylyhLzg/KplGBMVjuavsM9iyTct
4WkEGAuq12nb7CjyU1xV5G0ugn9tGIepbzJNPIx0L4L5D8zQ8yMYK4YrptDAvpi6yOG1r9G4
n/A3ZKJf2YmF5tw1hRtQfwtXyaGe81VbC2ih8PYhDgp40gZREL7uNeIC/VZ87cOcjYInq/W4
gir9LkzpdcLi4UbCZECs81zmskeukEh1t0UwId8eOTXbRKuM8eoBvQYWjDsz3jg3t3pdXlqY
SuQDksOt0qVnrfP6RsAdr81fIuOn8YaK8w/ncC4a70UkWs8f/aX7P74eur2/wpa3B5WWMWur
4uVaJHkk7A9RpQg1lKdvLf4MyKtstbDdeaTC2TpRh2NOg0jyfI56MjrLF25DPRwFop1RmcS4
HwOc3PNgX96ai9bsZDwe43Nt6h1BFJcvHWx3wLI3Yh9V9Bc+cjchs3uFspLrcsWYNA2S2JEu
Eg6sEk4oRvmicXkSegMm777rTZgso3bEz/cnrkevUm1difG5kd4syUVnCX2Ox+3YpI42DJuj
NSbEZOhYnMoNMjy/gOCSCHvExBgJA86eayxzYD6tqn7+cXCrgBfANNjXDNOZT7zliABEZkZ3
OG1nfA866s+5Ni5TEu5HcQoGInA0KQB7OIwvFuO7G89ZNLcX2rEMps/JtdABYNGEojS+xWF1
vg1NFbQaYr1swTHraTNkI9VouXRKXBSnHgmhjG6sBxLCzSwQmB8R4KzeolyPK12GulFkhVmo
bXRuLPY1BGrTjbv4mqZ4G5RORSgui6l06cO6zfl8gwUGw7HIf2A1IHWLGT6JwSEOzLj5PRa+
aNm7HrYaGlhg8V7k097bozGN01peYo/9PU7FfvP2uVprH1VCUh/rbQY/v37bDV60m6kvvb8J
ukeIrHoXYbdmQhrlcoYfTalotHFM8j2mzBEBrWl+g+gFCatemvqk8lcUSJ6We00iHOtTZeeb
7KNVDif1DegKkhr5ZKnQcl9XwuuesYK+N2W944QMQ+vXLQSct2avwl12CQGrBjiplJRbJCXH
7yTc+XgJ/Su0xRVdh4Ztwt2I3WPsWnAJrIYPPVVjUN68o+NxXsK8L9Z60gu6NG2YA5KDQtsA
l5tBtXTtHGalk2VVA6AqLGrMAPjmbFmbzHhrXumi6KxQC45GXQ7EbDrZJAq+9MKjqsSTaYiv
wsPIw8QM7a+5ufDAFRfCPGVAbweEJawhl8STSteujkrvQK15442fnSPbt7JynWWgOgstMprR
Gy+nETmX3Inxx+sVMUHQzang4Ta2o43/ulJQ0XnkDliiRsJsAHE2Qjo9yym4WyVU8A0jZRma
k5WbDk9sLgJNWjSIFSzCfnKfmbF46mYTArNQDNk7VT7Ru/he5Bbkx6ijdekRs03ylDm2nxj1
ES4hZZn3Rpd/0wONcnsbTSTGv4jrHp+7+mz8fmeZDZoL6rZgWPrGueGbkXoem20oX1PRsOS+
3IIMqvuovfz6SXLzpv5wT2/kzoaSTx8xxIflkhhdYy57cV6+i4fyzXX9QatpQJ1gFq275lYF
damcRQoLeXei+YplA7Kl3/Vaj46Se7raUQ/o9zDZ6bD4NI3cSsVbZ6afbU8sqpvGfTPJgNTP
b4tP04IWJ5zEWdXb47d3c5l2gsn5a8zbG8suhMWj1ym28cc6ZHz4SSw46lq3w4aM/dP1zuBl
yriS6UhfFTK6zHZXcIVb79VoK8oRaptx8GFy3FrhwDl56zSBe7rzQiANd1ww4N7jT8i9nhVY
S/BrUShkzEWLUSdu+fhO9ObcywrcS6/adHIHTEkrh/lmRtoNuZ//rxexBHYez5L2oHvoOVhC
oFAnYUrKSmfr73LOmzsZR4/eI1QpZGP2vjWEFKwhHK1bCee+dJn37OJDQY1pfe5oNN/JcfKQ
T1h0bjeMNsSJXDBz2ybbyRQ6MTMqqws02WGLjgoNblZS0M6UzF6nLjaRgElFp904bvFoMcO0
KRThEr6qQXsvontNH07byu8lDzfi3OO6FlCZlX59yw6yvt5xVZe/nE/iHBoTEwGCFlNBv889
enW4htKikzCZHuFs58T4ibQxj6EjfOqE2LkC3mU+6Ez00h9J6MPt7Mor8DS5C+uCsxqty4MF
O6ZUEEvnxO6tYeG6vPPEIIGvt3On1aRr+LpMcaNvDZnb7l2rnroMtWXEoH8Rlvk/9PqGujES
bicozEoH7bwXiZnJDbLFFxNKu7y+oaQCcD2+5BiXiBbospVMN360Svhi3fOd4B7Ls+Ut1be8
PuK2+5r6QjD3POmh5fZyolLwdTIOZxUVtzh6H7lKPlwRzYyp0xnVAhkGoFu6Byhp5TEOwy2G
OqW9NiGKJbJFQ2K/DxEn500uwnoLYQoVVeOqdbs2b4LdBSCq8ObIjue5yDQabfq9yH2QQplU
WtxVVlFjklNwHhK9KjWfeGMYf0MxanxdlzW7tOizappry3hENDzUCiA83mYejZIeCVuWcBjc
jeqqfLDiTEHomzqrb6u1Yf1R2qQzU5Hij+IEQRiZspExhQyVlp7T7/zmt+P1HNacHBAkXJ1Y
sX++TGx+Nz2wLChuadq2wmk/fXR6yqveMm5OWU6NmMi4g4BnvBk5X/4Vrcb4p8qQqmYu5R7F
t2F5rsVQoz2T19kLfmFuaANEWcnmRLB2mGkKbcCHmmxEO2nUB93XvDagorx7A+Gb/Db6p2Cl
FgOKOChwm+vECKDjair9ieU4cA4tEPAaPw1usKSZsx+dZbzdih7KmcWbWs5dkyxmLbKygZjB
kNiT4ATxJZQP88RtskzwsUZb+5gM7UstzUCIazXygmmUXovOCaakJOhsyj8jZvqP3RaGp2bZ
CU99w9ZPn44jOY7nRvMdPXQXbeFi+fN5FeFc2nMtX5i4SOj8N210BVJr6/BJKA+3PDWSLHz5
JsquwOzR/Cn9yVsAjo/KH/BK85FZtNMHTcqQmbbIH8XFlJ8KlLb0oR7uxwhpxPXgRXMAX+2t
rEFlizlyuL/b0h8oZQVdfbPhzCGWf9Gl60nzcAJEV3qv4IVZYUzkpTF4MHlYNFO+yIYmNdJQ
UeQz59SJ4JbZWYT4MRZEX0YLrHg+enIr5w1UNoZyy4+zQNKkaG0ec1UbOrE5SPWQdkU5Mgzr
R2M8Ez/ZWp08v7fnIhUUpntziCr5IDufulLu/pJvQ0rYl44aRC/HapCqGCWDINIrWPku87Zb
tU70gr/ZRWYAjbcQaBQ5NrWtCOMdom/2QiTNd+yTw1ltKzt3jTa/YDEfeapAM56GzLCMQko9
0yNZcmVgDJNId0kLKNTqiylBOdP7+Y5sn2nhb3FUqgqXyzbQGmdjhfllAderrDi3+Rbq9+8j
1+x/Imo56EIcVscvtv1jv+8vjCaRm6M5RIXOD6jh09SwRGIJ/0RzrK9f352v9n1qiSv8l1+3
vYEbOC2rRgwJbJ5W3U7zsa/0Sm+JNqQ42T+Kc/Ze2EhNq/vM2V5miza1ml/G2EpuaWWtLAG2
jo4Q/raFbmceaRPyyMEmOXzXxp8YSIc6Mc2nlNArn6Am6YV2SxxQNqeufTGxs/+YBznBLzKo
WjA9oKiLVJ4oHVo3c7IaQuM0jx81Gd04EHPxhXnjFnZM5dVb4aJmmK0XzZvDepCt8464tz0F
46EF5oTaIupPpjYpCrt/mvOBy9ybQqt6Wpfd4bmWl7lwqu9AU0djghpf9nmpOx3lFL3um+tc
Qd+dfSJDaRcX7hfHkZeo8AGcMe2Um5t9ZU6WrhSgz7umG0uZ13tZUSIaexYlvH6BniI+szXv
RdyLnLZpXpsJF3/8bzmFwUHkdCconB/ZayWpD4U6spWUO3TPpOzGz91t3/hEo7FwNjdtcZ9j
QO81SWBjtQcpXgH8GVqEji96qWQpME1lMrKTgTjgaRY4N98pOB7UeLdpu6pBfmZDHY3P0OLc
8mPBAvh6nPZ6W0bC3pQ6BcZyGF/eHpse1viJF2P8uP8s17Wgk3s9IReryeW4DRhMWSDj69SD
llbm1pD9uwlqFEirANz6xb1PTZRuQk9u1flNBNMT1NZe51efUylXLBmdBPI1YkYfyos9DVGR
B913w+SZ9XCv11SOWXs2krzohqrUhQU2kWfusEoYCMmTSBjaFRu9JwFDGDSP7ncMbxRVQZGQ
N2Fhi9DhNl7t2bQi7o/RxSkEJbWUFNTnFywu/BLF/6Wux2zIxn41WZkZliA4XnPx58BTWwqE
entQ89iclM47Qba3P93JppPlxJxv/v43y3T8D/qRXixa7HgGfDEuW85grugVHsnied/vOBFN
UDJzYkKxdGHm+vbPyewfkrpxZ+jk+3MlXI4ZHbFmdSpmQGk/q3hglDXKdGKOjd/sdByDzkS1
ONo/Cki9A2lwR3TPXl+fCG7wFd4PoKpSFLEeB7uiv4yX3v0aS3YcX2EFBgl0x6m2B9sMVD+D
W0gJ+w2WxqYW3m7IpGNG3kRELmBDXDEoTV29ntcsqXGsH8UBrJbyI/yz/zNyH1gNn6QbzNHh
tf74lL/YmhZvIojhqy+1bWdM5TW2nyymAykm1ags2wChxnIc9U9bE/7dh61J8aw6Fd2N2Eqb
8p3cPTZPn2MacNkNhjD/BhktsaRxdHrFGCRWiqeUaEVsYPIC0uLurIEKdn/wmJpw66PC1ljh
VZmKwaVpYeGL3pbWzkUYvZaE7Er3ZiZMDU/UoLk3d1pFOkLM57H8ZGZo4h3OmVHQyG5X6IPv
ApDRx2uKeucZVP2bt2xj1RsTaLlUgmlPALmE/y7zjfh/7FEiIkcY84nPYbcWMmWXQZwWvQAE
OSEV2TJBDi/tRYygphF2giHRARMLQUiXjermMIJodqQ6YbyvKkWgs9znjtVVKvdpuOWwwDyT
e+cXvsz/wCVzQCIWPxfxAuwZ1DksH62V/16kbnmKBJ11tYaAs5vpUnpdxtfDpB2sHPRYUrAU
8jtbOBGL3DjkFuaGXQyhjXCWKypW9O/vQr4qWavuZqOp/s1YU+YEDQak9PRKSToNJBDxGIHO
KCPluHLO/v24rzh94/N1TSGmbjYHG1gDeH9miPa3REyqABI9XZ8ubbmpy0M38kybW84flR/N
UT1NXdmwyt3VG0vIySCyUcw8tp+uAwadQvRREiRDawp6ebkJhxTei3hL+P8Caf4VL9+mlElZ
c7B2nkk1Vfc1HW17KND7pV9yENqDjbBiPlR6mKyCLUGvNDe/OGOoq3Cm5uvmQF1DwwP6R4wS
a0hpi68x0U31hbfccUfiFMUYEbL1jpK8kWQrPUbg7e9rz681hGxHhxnk4fb0n68KBkZ7s3yL
W9/q052nkJY9md0QBSJmKRAlPnJPSsfK88LzBgdEWWhThss5A0M5ze8WzGezoEbC876TXsf1
NSrtF7QGeGEkTGoKFV5S9M47Nxvq9O1vJ6SkFMYv/l+BnMAw979nut4DTFdazCgKMF2zcva+
jbYCTFcXm1aC3o70Zp1LJRJqud2g4RDu7e1dLtZ+hDE+YrDLXaXR1AbRG+u368ytaff/6LDN
8NAZnnzooO/eKMlWx5ZDoXo9sajDBz7fgs0w6VGCK4uet6gWU9FHkO673f5U//r8D6YrLpPi
N91SQ9OVWnG6bKZRQuCOuXxaM/l0yTAJaW/3Rk8z47FPb44PiMNCLBZmb5t3UMtZuuHrjt5h
yvVR0OGXfIXC5qMx79J//8hIrX1AAu4+OpBe7P5WM7CWIqtG0LJOcEeYbwdh4xz1oBFv8HGJ
8jBACbq7eOPPi/ngmXXXIYPoe18MkyzeOj7IpqxW8UNk1Irqhol5abfdyeaw/vPatj1lHMkH
jxfXiOdjSE11ebxlDzlfyr0MAKSW2x+ugfJ71ZIqPCPz/M+j/hcNBjNsn2ZXsh7euLSbdObZ
f3HXf3YfeBPTy7CTWdmpDAlp0Fjs9JCFAEWrKiDx862d9cN11ysCC9a55Lj6EtSJaGJJmrfv
wbzY8rmw1wk+ldoLIGnXPgO7zk6a0cPvbnCwFA9XdRJFJ2G9UUHHCY66QDFvMCEGEhfgYiGT
9k9cJGswQUcREWL5mAqDyRnCer0MS3I5SIsDoKCMyCp5RsuMtNog2jgRQ7VJ+9n1vYhYjcQr
8AF+K5vzxSAbxnuFRtmQW6ScraEO78h72zucepdMJCTKPuRzOOoz0z+5GP5zYv8WLdE7I6Zi
t8IMb/ve7j7DjzcMnYlda755Y+7kGo/i3rxBIDNX9B3NCdhCilOnZXMzI9RpxKheeUOGQcE1
210rMgzzdy6hASuqnGUY9eUV7zitwWzL6Ha8cp0VbU9+wlspBOqSYiZ4YPeUc3WyXFXqhzjX
yuJFsuIYvKlIRjBbcO+EfdLoBMudcQ+GRom90bK1hKfgSWFSkIsRu3rj8KYJ8U7m5t2m4K57
5BmTp40SitpyJcv2C8VkTAqR2+7XApVuhtpuEpQusv9PqK2oP2BFVKeF/1kRkZScxPx4Sesm
ojh8+aUExN9UQ3f7CSzXfGaNkJFle+NaeX89kOhqnihdTNPRYRcXtR95PS4wdOdGUGpmB2MG
1t1LNf+8t/w5GOQFgBdtuUQikCIkaXvwcji3tyh6fh+wjzpgiZ1Tnwo/dot92Fv+6BZLuJJ6
KD806c7u70ZVRjIoryD3nvI5V/DoRk9zGklZ3acNurPeya3X4f1pyd6JHvUZ6dQ03OT3aUfy
uVdK8Pr7XzhSlACcPfhuyPkMMNcBDFRwIiSEnhfHY/0JZ/FoAuCZt7RJO6N44c/UFv054sDz
kGXlu+5fDZ7MsiFQDw/2rS0EkHFH1Bqj5SYNiPw5ITkAF3qi960Gopdi3MbUc3to+1rwJspc
Rn1dDetfdF4lHvc1XOh7APHiz6P+/cav1ls+uTZtjyOfDs8u7E5FwbqnxmWiyo+KXqAgXxbJ
YQtbsjDuMXy3dW/05s4DtlpK0SvaZSe77Mer0L6IjOvGTh7tHGx9BOT6KWNZ9Yon/iezoWys
T4edefGSH+WEJYemxzInu+jbJteupDOZSe6l3hOLRyr4i9yd4Vf0GsqnCOQ4VC9G3yE5iHFy
TYjFBwoM1dOIqeUv0fiD/6+D93+fvv+d3t8xTBWMaqI6F1Xgm0MPv+N7qrSQ1wKdmHrjgRRH
RfkQgzTvuIgVnQR07kMGbDkcG4A/WFoDfa11ywQeRtK26nm7Gknv13awa6REyU2/dSVb/KRB
CBDYJ3CneJCGvXpEMXamWGsnR/xWjU+XhMSCoFt+ruBE7yi7b42+Kokh3LSNXtPos9ydXQrK
XGNJ8lRbdA7MvfjvvPj/7p4PhnkkNHzyLw3zH+Ja1+0nR+7uY9/Aff3WbbgGyN5Zc3kl9IsK
d0QOoFXYlI9TZNVTM1lW4G+cDWVpDVPT+fkMu6aWRuK7G3PQLqNh04BxLqGF7UPt8C98RcsC
tArMB9eIji7A+TYfOD8GJvFBq4g2nAo6DNSx0q3VH45enUdh6rOW+29vF6grLXTaP/rA+Yl3
6v7C6CgmaHM+GB2Tf2N09I6LJYoo3mE0Zdvt+s0der4+X+GhWxoyn4v3YQkC9zr3mftXX3/6
+48p5sN6FgfyNPn9bC3sUETRKF/rLOsJxEUNvRQpSJP2cQFbfBs2R6raZkpNHP7q548f/Dvt
X8vGB0S3fx8lxzRGNHWOqYpFhEWBvnjHXjpfaeqIVIT1OsWQyBgBpBMwDqxKBBDzcXqWzmhv
qMb0w4IrNU3dwu3WEdNK574lYfJ1lidHvhJcW35z2lPAoxsxI+p4jS4k9w08xx5B70mCPasT
/yzU7weO2JBRnsUYbKClV+++F4qY67RBf4CssnIp5+Ay6eHFKQKoI+CNV66ytBSD/535/Zt0
iSVHBLTLHjOuHowKrh/21eMmHkybf0OVTtdxtstHxH+duTxTHYhGifd1WjlMpBJqCLVfZd/2
nLpaJHGOCYnsRpXP1teZmLKirw6szRHfi8j2VizG6LITDGrVUXse7abfysa2D+iZmU9V/oDe
2bjJWyMHo8QUXXvL3dOe69WRuVPceHqME5Ttm54lKc2cs3KA6t2ruPNPpp3oVO0M1cpFC3qC
aWvLcurxT0E5XzwWmzWX29EoWg9gORZG5lB/wHIgtKzAWRXh5leH6ol482vo/2Rj1ZPGL6cm
8uNb7JqaG4m8l30kbFj1Bw+njBYTZNELsDE9S1JSShdOLCmq6rQ699tTQBpm2WRNvSbN+CFn
BJN3hO6yVfAhrlXsjlJ8zWvdnDeIt5eWhPuq+NQfP2o6uiGyafFCU3TV8BUkmRC84DqOboS3
0MpV1X0aA8tHyL78oczV4SYiMvqDXSBxQUTkwGtYxld6GRRSIAU6+lrm2G4qzu0FUNrpxxM6
bwcOL4aY1ZnQrBqP3L+ij9ywqC8ad/bQsbgFBW9qf4yqOSS2bj80ZGqYHzyCg9RU+IT5BLB5
p3vHC1g+bpTwct+QwfozdeRTIV96Ki0NB4aJHlHR2TBITSp1Tc1knrh5Db9gySgxJ62IVv7C
J/y13H9hsdDjqzDjOGZ4jPErc+vX9sfX5SVnO2tN3QthgzR7RBDRLMxYn6ljwO9pZeqEF/P1
HK9dLLi0Jc7N48Dodfbj8XtXZe+hhyjcnj4tDomJ2HdJHnOvBExWBR0g41Bzf1VHV4+p6975
RvYeRdjAHTJF2rPdrlo1v9ULVm8xqrl27RGeS5IpQUnrMRWBAk7mU3E3Jn9hjv/Sl0FqXffU
88BTHT/kCK0FVDvxslTpkTdRw874ugxtdZ93eFPGvUByX0uHo440U5IdQMZqPFGzCYAV3DAJ
iVBNeJ3wyXggGxrm4wgEN5xGg9jB0OhUfMOIYmAN6gi3R+wVvniZKe3oIVKfKbrM+G5VuklB
NS3PtIe4jynp1eNWwJXy7p/GxrmElTOlwMfaVVvA14iA/wJbQsQ+Mf/kn0u5D1iuGeJkOx4b
kIoB6qtIzrf+jnre/Nst+Kgf4Bl4nL/nQIUCnoGrVq1Fbw20bEoSAReiDUlKBj/p8EftvXlC
wiiPE0GqKfxubIQFGw2M6joJyHBvbrphyYqQbgWS5mT2SuoaBhLR/A8i3HKF20tCwCyuwuxu
GRpOeR0ks/b9qpDVgjlZZQYgqj7I8AfsFLqulA4v9VDBUvQdd9Co+N2tvDHQK6aBUD9MMus/
eD/gD55DX9OeEPES/kgVYHKa/4FakTBTPygh9FIKIluXXQopIXmlbq2NcUkrBzG1X33HzO62
PrRdWDcezLdbtzDxTTu7k92qffkjOh/6Kqp+6NG5mJwmrd85jCG0KI+nZjaUG9NfvmqEsP2G
9ntIPNQ1qXuE/rXGBuMvx6rht9gabcxzz/Xcsmw3ltSa2+jeffY9a3Ka9rW/1fto3L/X/HWl
c6zAibSB3i3bMb4c/K5HHk9pMcjw7JtQYlFT0XFOXHDswESbzAyGb6W70j5RZcmEtD1RH/nJ
zsGw3NTMo4dLn9d2JPmOTkNxtevzrE5e33kydOZBeuC7zflGeCCWRGLMRNonWyhAa4OOjg7L
+4Tcrq8vCjYvKhyfdQU/QFmryMho1uBZ6Xo2gUAC3DRy/7rY2b83p3+bvt/09HipbMsa7GqT
joq9rU3YeaNWrgwLzAng27Imy4+vMVBvYMIUwQRWfSkopYDlcA0q9gWnV5BpUzOPoVAXDeBa
rI6efI1Y/5yyLpdzi8NE/zVWrXIbostjpzl6aWaphK87Cr3s5ZxeFiD/wOYlxzTR8XVfZL2j
XL+vjK/+IM1PqQXAdEafJZtBHaG6UlIgtdQ7IRf+ieQDrHXIia4oFiDsozEAjgJU8zsGwO00
+KgXwO1PcR+4HXcEdXmGdmL7SkvruvaUkJiyvJGaHhZe/EcUy3fLqLzM4C0mR+fZkmAue3Y7
P8ohvbL6keYMJQGnHVTVO+bRxpeUAqdCnWwC0AT0J/cmGws9hZyGR5y8tsWQzmqcSyAAZdk2
H45el8+aWPZoBBge8YCN/sDw4E++74kxfiEuviR6Ybc7FPVdQC5Srtb7vPZ1fFB7O1qgY7ii
gaHDARjL0lwBd8fGf1n0zR/JFYvTZUHMKGG+RL+q168HCKpA9Zy6I/dmpiXNeB4YlAqzz9ei
3ef75Y9pC9TgcFXI96R0OHO5g4NhcOEwF24uJyD5ySqD1muLBnMrUKAlI3LqTvfrohf5yxXq
HbkY18MzGZfeEEmNj30mJ9wIHEtElqFOSE/l2MGWX/huv67Iq2iP0Q7jWE5H+RFKw5chdWmF
opcpkn5yIx2V4STc4W794vUgckmK4B3BTJ3Ih+jbHpIKjhfNiLcxLqJbw55KB8mnrV/HbGU7
6I/7u0KIeNUXhXUJyYHYYnyaafOAh1MLNAbadaOB/Flozs0lw3uu2kc34wnWMhl4n5bc+B1I
x4YqI3ydjVd+RfNw1AfSg4BoGABNOsC58zH9/v3a0mWswgdH3RiwmxGXmjJUuCbCJJQilhNk
sAPFFQ0TlPJ6ZB9Npnkr0XCaALxI0lfpUsnaD9PH+S4WZfYpiDJocwunPjc7oXhzMAUrmF11
yWkb86CO9NPtE7PfHoX+8+ghNgl1tNL1iLLSYwKV5JCWFwCu9fjWGD7qAnBtCcC10R4ogGv9
gXyu/+BaLtgIjab+wdJ2tH8onfzaLnyretom1LrpVSMRWjQXxbLW6mJfo+JZ23H1ZKZNcrRq
lU3s2hUi3hTiADnzYx11LWhEPvft8AOMZsfWQyaR7zWVeJkeovwtDWQhDZzKoODLWPCbiJfx
VfGO++0hXGhIzqI4UOz3527uGOglgOY1bwf4dgjg2w40Bp27Jd3JpevomtepE5Qb/QH8GeI/
gqWrWv5m7BgKX9ZzE7ykrlqYk88VBCJQY2EvY258RFFl6jf12c677zrSEFa1dUeWqvz7S0jU
2JSX9SFaxRsBFVBwc6vGDt5urdxuwvCzmHg9IaU8mG5SnjzyXuR68gNIbYDQN489vXv9UMtH
o/695q9Txw+diFKZarTAihu4jjEkzpcHmmr432IV+QufBRL5Jt2FTi2y4SV41KNo0pqGeZ3W
miXLllEIFaksuBBr83LSPgmuo38/yMWwf5rQ/5h2Hq+GoXglbYOkpW0ShAstjgo7nVAPF3WU
tMNnx2P+3sv+G/Udzt+RCb/Ned1WaTXsEoDVciOjidhZNF9HB6yWivrmhGxPiOb2iIo7YyIo
9+CidT5V/3YNB2lowPJSSIKz2EHlIAx660tkpU3S5J44SVdXH3KhptveOPMtDT9ql9zcGXKx
EsjUK4J9aup5tqWPb2nF9jbtCdRIJfAldXVHPQobUTXmvxx7+R8SNAGIeznqDzgBtR55vn5V
lgdPr37Bks/x/GQ76CKbfW/digs3UwerzgAcatfSKhhvzGWTIjfHvQOoshqAM8wR9I2z7Cla
99RA/rEEA5D03reR/G9ry8YXuIXpyDcranxdPS5hJBmpOuFTt/15lyQ7MC3gk6QPknWHCwIk
a+uiV2dBvkvg/pkAWc13gS4fNOnEidLBvfu7IfjO5k77u2cqF4+F77xs8Ko6NcxRGjTxHakI
R99PFxbnYmLjCb4q+1YRhjAhpoAn7Sg5Ari0U0B/TggU7QHYLN8+Z19ltmKkwbO7v9QmRPCM
zJg8ZBoZ134/IbTMFUiyjuRnXOlDPghsHD248uIjKobmDgcF7Ez4BgF1SymQToWXT4HkCj2o
wjjJhQ+F1aDXCdgnJyyYuhG+t7WihQYyUXNL/n2Lc3IyUaSs0S6oe0v9CVeiahsYje9JH7jj
NfjR0H+v+WtibZ/RiRZ6rCWxu5UVQnIhNGO6+Yr2bE20JhRqeO6ZktL5Fe/iLbk6uVmK5Ubq
ErkrcmPN+JOvZo+2J8tvxL1bVa6vqoX5m4KBSl7V6yThDjObBE/NSxGAjRgEb5+WlY6HtraQ
kjvuoX/vNf+t+lC7y+Gse12yIlFlWSjvkakcSCpLyNoG6tvrH3VijQ5jBArFdNuBQPLeuJkR
qarrsyNlsxGdsBARWnrhD/Tn6wvmtGZ54ZrZzilJKOgnlho5oJkO1VWYxVkSSQByQUcS+YqY
eOmO54//HKpItBMJab5EYsqHoh09aWc+E2C0iutql5SZCPHBvkSiynzFmMOyhWWj7dggTWHX
ZdUUUosEvp3BOAAeA1Iv2o+8mLAwMWNH5Je/fvWylaVsx9Ig8gDpaTRQ92ka0rbLMIA65tm+
OShwctG1jAGfcLz8uYTmnrzh4uxa9cTUpfCEm5Fsusuy2Ne0EGXHD+KzAxCf3n8Wn96ph3BL
fjkNAH8+thsZkwGk517uwxZjY5m/Zs5eqOOJDb6tZczdmTt/ppUoOUz56HiO+IZdvuQI01Ur
KpPXmOxds/tzYeZDk2wjM/7CgisgijIPl2cogn0Oro+MP5Ht+/PTQONTxCZQ2Hplp0/Vo39d
HpycQanJt54gcGv9Wu4Zr02xU4DaZaMDNimnfgtEO2OA8ix7Hz/9t+1fpenqrZzXWdZZnJz0
xHel6wHxhI5sK71eS5tYom+cg6TkSI2OYEo7ZYdesB8K626vjNDKT3SsqIZnmrcHpd2eXXPH
3uaUU8DStepAxhhHIDWK+KLn2x8934scqrGvjjn1qovyKv5xEEBR3rGTD92xStgVrd3s4fXm
mDrTHHXypEedp3S4+NzfzuHfracwoTSvzvEl77vZcWdu01rD3WYiLLBq+3SM3hAruEsHYwtf
iXH0oO9Nd0DnduJSNA2zFm+cnbr6aK+8sVL3bGP5ODtfMbTZNsahxKdFj0MuRknrwjHUBOW+
9F6RjX+K1PwgMZn6UB1JSZ5vXJbIvby2qEuTzDv7uW/g/YV7DoYfNNpUtsK233FAXio81wWY
0vRPTNmTFoA6qyGaYTYX4dftWy8vIabsWARhBRH7/8SU2L9iSpvXmw5WZzYW3bYNQvYGZoMZ
nQnvdhmz2XGJzQoqk3UZ3y7ERadNCjIrUDtyhdRC2+ZOW4czVeKfAkC6Ai89tTdGVs8iuQdZ
bO+8vNxISGddA1NXKlEJQK0hbXv8AQQGUgggEi+sffPRqpGPtwHp6u3mAUGDhC74NJfgs/L9
ne3vvIoUCxJOcohISw6rbIcSYPyQwT184c5HD4rgu8tNDfoHphW/6S+D6ppSQ2axXWFzVk4O
norpnFepQt+L4e71Ao1dy1EL8Q3eLadu53pKVf0l1ZekOqsddPUcXWE/KgLIKl/77ONR/7b9
a9C4B09GuU5MmilOPjD0Dbjex+acvkKuFwWlEHHieRKHVU2mk8Cu8UeIt3tCTttBzv+G3puY
Q3ftngZM/qBNJ07lzzFuiSFdkc3CTjpMvb3ePkYAcbpO5tagl21veqC+kRn/27f7d+s5eG79
9CjkdPSkV+SNG2OsRE92ZEKgnj8VAnWBLrhq5FaXEHAKEREg0pqjPao+ysGc3nxQNNJ3Itvt
6v3aDVHKbSCZceSabi6h1yMKojd37SHLnQmxULbH+3TNEsu/3D5Us7x5N3z0H08WiTY0QYUI
pAoydME//05w3uMbWuSoIWFNgVaS6GQ+5POqcBx2LwHTXBFuykjKwrCDe9nef1BbCXFVNg+l
E1+T4cbPpzU8dl+OvguEr3U515Z53+YWZiBftgPBHiY8N0F6oWTJp97BvUtRfszqRNKIccjM
cLPC8B/YcGKXERAFsKGm+mRd/rd8CwUFsufm/Mn3Is+IpogPqb8tx49eGG3U2j05KbiUL/Z7
N1HIG00PglpbG9WS09nB19WZ2ZJVgXH5+lC2OtG7YK8kBfACn/4LMh1A5XzhXOgTsfpsjVj0
YhNHD9fDKZY7eTL4O4svWv/CQSt9cUDC36reJVle+PpE5zufOay1MwDvMBcnyd520F3dk1Xy
GSw+Tnr6gyBjoM2ug0HLNTZ2PWxd+OQmxJHnv3R+0Z1iQ/Plo1H5g8f/Qsb+xQv94cdfVfH8
2xs+6sF7EuP82iYU9beA8uGNzr7ZzzQdqpfKgCpdSovRiRJaxQTllohe4tpvUwQjb/t2RGrA
0E3tjA6B9o5GMnCOUZG2DdO/3JGcRiimFXti6NlOULBxUS/ZfQm5BdQsavtMwuWjP/s3bQKF
4oH67Uwny2ZGQOqKrSgIpj8jV/5FHuCkDI4LoIbchJHkhOne6dls/CLOI/LWNQZ2t9J2iCYT
hDttHzjuHRf66ffVwvoni2Witpxt8Vt19brXmipxyVkwJBPRwlaiRzVvVwBYXlCr8T+eQgfk
EFlz2wX32lRPVEben6/JWbzx3dhAOMuDQDJcXV7gFQ6SWe0z6HXvkjtOAvtM2+oBI7eBsBsh
x2ZL/BHgvor07GwfOwbV2TrYkMDXgciSbZl+L3PDzKe43cu6CoXtR5+NlmvVyU5OXyJdHBN/
wYyUjw5IC39eTIBN3RJi0GtxuQ8A6w9LRKcR0UWNgd7KzRIfB0Q+TPgw2PULC0zCUzRaSEYo
yEXLzzIwqG+5JoK7TvGomMMXf/6YKt/n3zSAWY9PmkoBUTH7eFJtaISApcOLP8inDzIl56Np
Wb5A4VZQCrK9O+RIzIOmmdT0WoOxln5fZAwhrzPkq0xe86h9o8jzX7AIfo0Im8tzHtlOPFLj
U7uZQxzOraG7WXeyyK6pKUTBz67EGqp9Qu8YFMhOW506YLVnXhNLjJDofs3pN4R2YPMCYofk
JzxaaU5W0bBr5b3+NCdLOOlVJw0lbfOTd239L1ulH9PmX7ZdAqre/TJPc6SpW3fM2z0XQRa3
5vTBmm0e90aAGq1fC+Y2ocxEZcb8dZTrAW0Tj+UrMflt/czKbIyx3A/d9CzKyvRL/qi1uYOz
uYVFtSbHX7D65HjrP362VrwikI+7PXCu2NNdtZTf+L0RrN9qQT3FuoyFHwh+8Vf/J6ooHlgv
kRx/0ZBQKTkTOYvc5o1h1uuP79W14dYfnGk1+/h+0KGehu6KBprx+Ov0LN0T4/xhdqetfcDS
M/Wi8zgqCjSqkYPPXG5lGm3Vw80GIEa1QlbebCpOwWX5fJmjpWX8YcjsxoFfktH/fQfFgd8g
GsKU6nPaoXxSutftjFXydwHSMYZmcrMMiv4tDtk8RpABS0W5zphF4FU/5Q8Ou1+eAEHo+pyu
7tfDRtBNC7xrusGEsorpblcCumUZIawfrfoFnfBjavzLtg9IbJeFLmZstZHf9QWPu7d2DQ1t
mt6TyY2YKHpBn5El4jyxYSshLItLIx2f/aatVyylQDxEqgaSU2wzU/0sWubwlz0PXmJLb7mj
KptShcoDh8ru/MOn+ht630RnUCpgN0c2Jusc+HRbYb+0pmKt8squ1gXNmr/+u29UnfK1hLk9
ip8Bp5eMunYXft1eaWFoO4uuYln4WYUtHtw2aCgL8Rp2taP7FhN5hUmoHEsGSVaT6QTUWFL5
aDTR+xy2uMzcMKJ6sI/PjADOdWm8m2XlwFOnwrlOUCngqKnHoNxtoZeE8eSgEYIyjJbKysX9
PH2djLTl1KcnsGQA1BJuTVu23Fb0zC+slF+z9RaDqchF3U1ME0zODTsxrnIvp4zLt5B3mvJK
d2pmlNveYC1YJZpJJRG6X5bf46CXBBJKLbXn1+uusve2izN5qadySPW+JVv7d6FpiS2f5H00
4X/bpoJ2BhJIz1qKjlsSqi+pc+gRDm+LyUoq/uR9ffgs0XS7Ajj16NkRp1mNukW+Z8TaMaW0
xEtcrHURgLxpDDmMvW3nAd6LibSpPTryj6eBZHQJAz0A1Fp5MZt4xPvgqTVToMiJz6xv9qb7
HbfQv/6/J56Vch71FrkQXa00b/W+al9ctvv26iljoAZh/88yHe2ZTyNcJhN/75qxw0Ss76Ee
dw0/mASwnkNpUwmJyccl/iJsdtg87/Z7kc1DfRqhQbXZxfjXg+NR8o+wmkwL+XTjPj8gR9pl
TX3m8FcOOjo81brLv5AA+WvW6M/dRNNyjYiIivowrf+PuzePZzt7+4fpwkwXHbW11k4XWopR
a5FoZ6hOaxlDpJbQobVW1BoSpB3TaquaGlW7tLSWBKlaIiKiLUJtVSKI2HeS2CII+mTu+/mD
zqt92ufnvl/f/v47Vz7JdZ33+Zyc5TrXeV99WSzgzZgsT7008h8mesEFNMtlbxppxilBZPGx
/KuB9a7O5HCgiFpP60xxiuiUA6XQBBNB/UHk9cct803KFHKkbXZkuInOYmRmjc61cUNQGtEs
9PB9rxLlF1OouaD2zWGwW4NxB2TSb1Sbnz5wRt/5deKN2+F8Mixbx0srds8jpA5J9nxsRFks
f7Gz6G515QG2vk81hBp4kqmGIcH9/E8QzBBxSeDK7xvaEP7ODMe4GaJV/bKbDjo+a5HdV6JH
wM+Or41g3Bk7Hm/UuVOcE9xV7BPhHwRwu5fNT+BZLpKU12j5t2JK0B9L5PHwtaSHji0C+Jj1
H69rRhHZKq8Wavu7V5yex4oCBlNofj40fz4rjX4uBlAFe7dR77/KX7Hp05jpa7fcX/7Qq9wp
3/GKfUcIZVYRQQnBKgxWuLZaLutlAaquyP/LwLf4wXYF+asTmbchP3ODscYrsp495zKdkpLm
zBsxp0bDeX/vibyx5ai+sr+pmOYvtmdq3g7T6NPse/0+qIehaBih1hWywEBXZzIj368YQLEp
kY/0ixGPGs91MfQfJJmGzrVBJP2JlOaZlxiU/1m9qg0YBH8nXV9Mux9OfZ3GcZcMl/mtjWOu
dHjBenDGj3WJ6JWEdldcqA6XatnBH3/LWdDKXxd3DI+suCqdX1iPg4fbH272Yf+c2VMESlw0
2LZp+Nxg4/8tfsVqE5WgLjnRF24cXBDUh7rfrAjGcjmjvT6hGsA1uVcPPf6t+xv8ZE9Y+ePu
LIqh7G8Zicw+dUscA2tRg52LPFSXvq73P0BIcphtjdIo4Acj3Xy/Ll69Q3MctvJykPK+SWWG
IFDa/1EDCn63UsW0bNqnlCRNQVV29pS7YQfXPwi0ahgiDXjqrO315QpQzMvFfeKlxtU1+raF
2V7FLbma8W7MXCY/RSsqQtDtyUaNN9L49PxM78d7d/sPDta8XWSxaogRY1hf6UWgCYbEK7l0
47rcfm6wDnI7nlW7QImKz2Ala+vnN0FGo0+HlI5n1kwaU6NgDNZu6Y1a/1X+ClrY5YJyn1ZQ
UKOJVnVj48rDPeH6IdYwh7HM2/h8B0x5weQyIUBshGkhb1KftHhYMbzqyuct/6sq/6EfbIuC
FzEdUmBpgHoMzWZJJuXC+xIHP3qNqIWqXhF99Zp9dlfSzq4ZRLA1OeTXl7AmuVW5GrwWw9aA
gloI84aFId1Eercc2tftUEzVMhD2rJnhonvJoOQK6dniFHsckn19Lm8ExG5zcWXs+G48unz8
zSBbdNGwxkkSVzrLuYS2LlW0sedPjEY8HcDEzk2ro216QRJdNBj5WI/V+8LRwyzJBN9LWQUM
nvWtWG8+H0C0NqX8O6lWqZBaYcky1AtFfnhBGwImA75HsliyA96id603J3GPSgl9tlW+gnpK
8N0St9z3GlTITwzuSkF0i1CpJSpWfXj49KAjf0VRZMYPHDb2MUCgUvPVwQWK7t7j0ln5pp4c
b7yFEqqn4aFTzmdr8q083HV9yrukYGC24Q9f4Py4fWk71vwOc3Bm1p/VgwmfLgeM74zy317O
ZKuZh1hi6UmJlHfH32dXwMvAKtVovMvZQ2e2GqigFDw1NMbPaFUkYSbr0I/oX8jUBEngY0/n
W3U78R8bE4mhQLIDIq5fvCNzuLFJFyZEowY2BBnDkr1Jd/0ZmgpAxZyH1sLnm+gyvqlNR0z5
HXMt912JuaJBKFCn/eoSP001+rrUi41aRQpr5NCud8I0GURhFfITFmS30XlCN8IyMhYFyWUC
s++9sKJdgDBiS5ap3XqSU1kpMnHC1u9Pubnja+G/j6wcBoYxKCXy4+qblG408F/lrzgu5/9t
JBm6wchjYdbUk9VNofqgNJVivoMq4FTeIJVtDc/lCm7XP+xzQVOvpDpmVgMoH4v3K86ZXSJe
Ha7pWr0A7FT77l/mv8UPdl4OqqbrzgXjv8fHyGXUonO8uq/2ST3Oiw7hHp9dHa8hsCP5eZ5Z
KQaRcYAjv/J5A227aEHmasNhTSCn+5W9i3wWrz89bmw18m1qHL156UHkkpz6gNmZX4BRSKza
yfCT78m7H+6GfmxMId5awlqLKjfoWly98oR/8bAcd10lR775nZo5zPsdd60p1z+XKQaMiRhF
g6xZkCR04MHN724PQutA5p/hJn6FfspY89d0Q4dUo9gZl9TvqG4Mq6G1GFvF8Lc3HyZ+bHeT
/BWhjjsOTe0ux9BX0bRn1mJGyT4tWRNBwZzDd4gJvRGwsEvcfnmH1u1eK9ZRjr/1rhutqeRf
9nQ24O2vgSEfr1XZ3dlk9lsVvpPpcPe9MrmaM2Ffqi2q8ZQtK0vkBM/WYGZf5oWvTV2eDBfl
yt0v2OUn7NHmr7iYVO4zCWrro4gPDzrgzXhFd8EVu7d+x/aVWxkByptUb6kQpZbe5Y5AjHLK
isV8UXlem3YotA/T8ZROzp2l8RdeMtARKZ+2YH5CJm0+mwAFKzYsvGlje1wGI9L9ttuRxc7D
2rpLd+RLQ3FREDF+WOJMXk0Qxffoijaxcnobt/Tc6OteouaZXnuft1AX724ntWwURJPvj4yg
6p5I5CrfCLj8uc7wFf1zpwenkmHjcr3ttsFhtzBVB0gT1cUghOji2uaFlEOV7rs4ziwp8JB9
CsLSbBqhkLacyUAY6piWlbtUcRhrqcSSeCj1s1X5XDX/o54dplmTRNaJ9cL7VV06Fxw6gxd6
Jl1HPUtyhsD+OP8e8KEoiEhJwwEeLhrhhRlUd59YORckvlJkHp2kBQKumwOXVLd+MfN1DsVt
0SuVzIsysNRrTU5UAIYhE2BGLbDEgcRpd/t6q59JKTQ0j9f1rm4fKJ1tTFxoxhcX31990NZ7
mNlzEUTjB79Y/7Tv7MZXslMnqLD7tDRSXkeHHzzn6o2wDZx0OTHbNG2GLaFpAnG1I92o65In
6tRmSipP6w4Ai9zJ13zI3qbps91hJ3dNveEf/RzizmzU+HH5a6bwp/A+aPTBsAsDDxqyhs2Z
Kr80U1UyyQ9OvK3LYGiymuWcZpSUzBn42BKC4kAEOn6uMXVP/kUylDH+tokca8rm36jtP/r5
BcXHtftPlfcdGx06nwaLT1fzfNSZQlO7luZGtB00aAIff0OEiIpOLdm835U5Xo+lty3jqDNq
kJkI5WsVq14n2IOYcv8XrGUAUoiBvCZ1bcvxfd3eSPC3Nd/FAqCCaIgzaSLj8Hp+hvsEiDrV
ejeC0e3ak9pNmjFfT5FBKwXNmb+RnX476PvHwNWJOD5XplV0SkQNnxFRCYoK239lIwqJzA6e
e1vSG+BB33/yIgWGw3RNmZNmbq5tMMo03JRZB1DJLGUTy5ZNsD+T5MiniJlWbaqmSFXio64G
9nylgXIZV/DzUQpf7ojcZTAlVXbS27CX3pYPlgA99QHoWhL5ya4wBOQRfOewNXBcdewxRFjJ
23/odRMhxUt1eIKoaVJblwW42D5gf++DQHiP/CZn60ag31R5O6pH3zwNeaZ94WSyC1b/gdz0
xUctf3sSjNs02OePGz1fzw8wHYuO0tCdLPHmHwiLcICWIipt/Fyu7uv+x9Fuhw5uPdqvWnIK
2H4QcIjJj0l49UDe155ZPezpkMFKgFb26mWq7x95m8lI1Qf0B7Pu8xKU7Ecu2rT6Q41r+xjL
nYkL1UsTRQEK0h8EUF2E4HGlhxuB/Iizbcq9W0ZQ7ZGuNCnDjNI6tPJtq1umoeA4i6ONyLsJ
jognMyJRCOxhVlxNfhx8DXgzOvbZZFnHmrMI87QODjQdXOQi6Hloo86Py1+xDhACMkxPTTEq
OH7KvfFQf3VIe+CaDlU81JvovV2aEqlg9Cbj8kHBywNdbTOFMxoT93xc7TOaROWfa1Ubh+cI
/eto9uOafBuyxszAc+2ZNzmsmOeeReYpcCOp9SPwVn7Ufrb0P+MN6Lc9kVVbjeSr9uoCP1Js
04picP5ggvbFxUHM4mj+s8lgRddhb6zyfbtEPneGcg73rIK+LMsspdxZSufWVOtE2LUYhd8p
+MklmOdbfDAOTk3c+XwjiO21y/V0HS5M2dC+VaU29V62x2SorY+15S1tJ0ohiGclOtkS5ZXe
Zyjh2RrpT30eYFLA5BECTGIC3EdazdPXVZIkX/oVWAEbHaLXh+vUKjaq/rj8FT5PClm3qg/y
a4EDEWSno/1Ae0UKNUTsxDnOuADuZBYjfvifOE37uLr/K7IQUHaw1fDQ2Hy49yXb7Dfv8c/T
Gky0lt2IVPvmWYQ2hHe5Tl9R+Q5GqcLywVGFJ1tdp6/ytAsI3wkg4TXwlsdTIW2nmDWBdt3w
25miGjzDi9Zxxrx4u6zwKltnE5+a2JuNj6fo1rHig5N0/bUJ/Dxs2s01RIxl5c+t3J25EYMQ
DdRWWBKjrnm+KUOF0kwhxAQnoSRswPyIRETboSfy6eXx6zIB9DeN5nCvapL7peZ3/nxXO9GZ
HB0bLTlGW5MsD3OqOHNq8x5/o4F/yl9+oL3XMHpxNs+xngSONMEolmd33HkwtydCP2yot6+C
e31M/VIiKTYh391bCpO4rNJReOpUhXoRvufgzhsfm/w25V3Sk/WlBeOOU9C0CwS08PWJZIvn
UEXDR21RvtIIZEyMDe8JsUAM6u1Au5WiG2qHe4PH+awZWGfgnFKWOljG60tyeVsN/Gv36YO6
/OTwjJSLDt2EYpOQlea0uOzeLNcakFQ+PwsGcOT3XbITQWWndLgGdKGWzKYU/ef66WlxZksV
+l5VZJA4P/t1Bq1i98omFAcWZ2/n9COt9sIcqZ5ZzcCewTSD6GJTj0zJIOkA1Q8CmIKHV45u
+sXHwhcfJ8ptT1SlINyvS92VwUsb9LYGPyjMsX+wRqR5izADKWSzbSnws8wUfa7ekn4+3Q/k
EACdhKcRmHPaIPMDpLVpTCZj54YrTh9X45uSdzlN2WUMu8wrFQexf77nV7I3HuWSvO7FTO0h
FADeQru5r9xS//Z+DBM+XnG4pdARZJ6fmX25kdLkahctYUrQyRJkPtlqvF83WAoc4PqQhW9B
TP00fuKnLdG5WXviFVu0v0YvNs8cM9SZwk9huH/PX2c2VnKnSJBbNziYpu+QACpA/tKz4pSA
7X7AIFofaB9sITupBrD+ZIacJU4M7vu+1HYtS/GIvw9D15YJvLRQq00kZY+thhhc36jv4/IX
90NRbo7QKL6YoDVYi/XHCamPa3vGGhmdYlZcQkWsbuPfpWVi5pYGyNyo0BktUq5FisZkiJ1d
cIExrzOOXaem97Hdb1QGSTmmnUrWFhHxFu9G7+KkwaTLBw0hOVghjIv7KpyHeBIPUeHoB4mY
Bu+9Q9Cm3USCa3EV3ET0PTvt6vCYt+HNVY8vbzX0r+2Dq0Gybbhr6fCQGMT5mVm1tpyJlVJA
tydTI5glqb1cgHZeuDA5uzJ7iNykZEXp0KoAOO8vw9QGAypSQMZLWfcm7mWET9yAVm2AIWiZ
Bi396/Ksb5TMnCJiygCm9Gsix+jFnBsb6c4zYJ5RwlmQ6DC4v8Nrhu1qMOHuc8h7RQMu00LS
vMcesHKtDTh+dGs66Q9srBrB+9fhzMB+x4ITWPv2hVQZv3mQdRL0g4AvvLql7LvZd33GdSVZ
s5F+PXj5m3FI49dFztzFicaCYQTNZ9v7jag2APzWijsDg0paVZ37gW96AozNe+QYE8penFxy
VAQBhZRHh8hFZgoVxebM5RdMEKRcct7jC4KixVebMLM/sRZ5+qzzSlu+e/s6R5DAzmNBye88
3i/nvdf2vjRvrt/c9KqOEPBqFhx8PxVrLbdmd0+VzlUU9DbM8J4nLNsPqBU5mQ1DiEWB0TAW
FTBK7Jj1oRM0geQoE8irqRsb315+Jd7BUkHzL9nTfSDrFWAs4ZRWslJHproktsSUHGlZIcJs
LQq6MlWR7T4eqt1G92H1rMqIVy8NNjXoLcuNdaztX+sLEfts83z50nLX4hQkt9X1MQP9rKY+
OgnRJ/9BIJLP4+3wqvHuoivpbcQ7YPkJz+LOkWyYV5GXJ04dweemzDII4X/hTSJzigKfQrmX
nZTdCO8bLv8cgSN69RLrm6G5ELkxKEtV0zor3BODmUXwuqzZkZQVedaFl6VGEsFh3JlABtis
PbODHefGIaz+Dnx3sn+rgX/tInNbTvnQuOi5p6/lWr2l3Vvzpi5JsY1DMquw+4mBjasfBESm
KYWH4gEqnJWgyvOlqnfrUmjFqTHgbdP8KKGk+zzu8ewevH+PafP09x4boXwXQEVfc5lajYf6
WB9uBwVAvcotsl3cDANptpADRRrriiA/Vt0Ryi9pTbEB26NT9BeN4Tuju4HZMd7UeyzreCjH
iUP8Ybf5RpUfl7/Ygbktr3zY+7TkjB4Az2SgzpARjo0kUxyk/HoOHshpqFw66vwrQ7Ijvl6n
rRlvbGJf+xzr1oNOxqTSSw14HYcBVWaHPjb9bcqCB/XjPU7LRP+tpjTgUg0/dt/w5AcBWRjz
HDACsPJBIBT65GdoVPdans8HgRpAvna1Y7tWuMFvWWinVATNI4kL0Las3B241dC/zmkkgKss
kd5pt1rMhEQ0a/UQnvsawtUc7yyDUjpDrWxampMnSuQbq3QY4tpToWFEXwDe1piGMO/V9a/4
Hku+6bUuqWXdDTifnNeD5g9Am+59yms032YUlYeaDY7Gwat7Z4JvZ6dA+fTXSUSUC5/awxQL
lMMgwmZAYyZNNQHmozA/n5W5rPvh7u5Xg0v6avzXUvPsx9Fux1N6V/+cvPGZRvqKg6JsYCnv
77wC3esfBDxCVuU0vWi5pvl9SmrM/x46jmSPdmd6zrm/jlFjyO9xfpdpnbi8DINeNeNxn+3/
4TNV+JYeharrSgdO9uT5IYVSrIPLS4F4SPlhgyZQ661gjMsR2kzuDZDCOcC5Dikd6VrVtxnK
/MQHEQDRKerBEDBwhLCTvuVYo0kWhrVl6HXhi0vWP/zQ8rRvsiFa4aIW7vXwNvqNf1kzAeYk
72xC/q12aMVZ0revzd2sXbXa9EEiPsd15ZjTCKbAbJXVf4chEsTT0d0npVPS0DZOSLQHPvXq
ofJktEesIFbyTTw/YL/qo42qZfYiztf0SEtmPhltlRiavJTwgm2t0asY/chc25R0ateeiXxs
X1fP/PW55qeQxl9J8TkTdrYYtJAbsey05ATeBnkr2fAfT9O2jTo/Ln/56Bqz8maqo+TBdSVL
PD/MJqqkuGfX0KgXBtslR5q+gw6U2tkQfIsfIAUbiKA33rkfo+42XgYjmvq2qg7YZ+Gkivbv
O/ex7W9Ulj3Hbs2HAp7nM6faTWw55gZKu8rdqVkjmJzEtZnjyOcPcLHP59+8OGlPFLdvz/fq
hA2N5iylxEH4ueDGuTcj+rcW9nyzeoDwq4htLpfdZpF3ki26Mm0w5T/lj4BB4JeGInwWY687
mPLc7NfZrzEnmPISgFGDKkPyPCVUaZ1dbrQmrLv80MgQ9jeSxcvkZ1wOQCYJ/zVPawafdLwy
InOHJ3W753IrJw2pLmVJiLlpLpXHIEtyTtpPLegRTTQc20z4rB6WoTOeGETw3YchtM8G7QkI
zDV7lXIY1AZ1idJ1Hd2sU5o60EILbVwK+UCCcol8S5T4n8/1dVgy0ro6XeVXeZV7poi//Paq
yKyl3jFrXceU3N+JY/7JvrGx9YQA3bTI1w8ykw4etAHdjMYv1RyEEJcALyY6Do9oDvIjo9yU
OnMOfrfpNxt/zy9/+YGTIIry+2pftOG8n07FJcx0rW3KXXOtpVEvfNYgPfEOZ1X5ihQ/jf0f
3W3Fqz7ARmOHmiKT5MOAC/zczMB+3Y+sfrPiHsSy84yeSbuM2/ijGpu2Z7O7SHjRoSSUST1u
15G1y6e2eD7a+RPnRR0BfMpAV9IL/Qv+5UnHLMMTTDHbiCtmi3OmdRQUHimFqpeLjOrX/bVp
ipL+AzNdbUL2j1atCvOGu7agCsO0U0zYySVdZbxWkw2tOyzQEtXBHBaOWB0WOfJBABaDX/ck
8zO8SgxVh6chohx/YcgC65szdRY7O4oCvZO0rLSsI/K8Od3Jg0lJifey+F7NFmh/4YPPhvsJ
CD5Ni3L97XVdVX2GclGcF1H3BNo2OcPFtfeh63Lb/Cm2SCh7oEORJIqKvZs/Og4bT1qWje4k
HIi1XL4YK1B3fFPX+E3dxpwciz/d20fLqO4swlhneV2imka/uTdz0hri90HAwKQvRIpSxBVS
Y3bbK06+KlChdARO+/zcZDWMie7IJZhRCDbbEzap3Cx8xTKFQrkTG3AHcr4kXBfowtHPPpB9
YZlqF+OkMY56kZUodLZqs+ZvV9KYHdzR0yl3nuNjCkwsskiq/ZV6pCOrcUo04i5vV+7DK1u8
od3lOAUZ0y4GZLis/pi6W2KCOgp6TX4OJstUfC+7xyM0Zf7vQQo+BjbLq0qX+/xlOf5ohiiL
0XgtnyldisVandMB9g0Oezs5x2RKDeZdoaPnQNaH6ow3vZjfufb5BP7Z1+22nlaXE9XUxaBo
UX/Dkr7CpLgBXjukiP1nY6h8TyIR90hNdDIx4XD5SR+zvTpuSoshj4eky7jKRXz6Ie4mjR8J
X+5t4A8tf8zoEdoV3L0Dm0BtWD8RUr2YvF20nfYol39H8P+a41P+4R67Hbs/EBi6lGIhZ+1V
1tjmP4FBi7dBmnQl2SHL6xLhrx6KSIIqpk+G0TV7e00wam0akzVWYgqB0v0fte7/mXgiIB+W
2vFu8W70zO3rJ8HZ4CTwrvV4p1XozNHrGk9HfZsvRsv3avdR2NtCAj97MVhA4Lgu5nF3PX2V
yQ4jlmZES4/qJOS6Bq/Fi0W6UQPWbZveOaH3cYH8gRXhGzrgGJ24sh4bhbErUKoAmfC0HLNc
ezCCLTc2oNmWvzLIzEvpNvqOewtrNRFmluZqXsePDWO1Rfu3Izp8t/etXICG+SD/biI+v0SQ
AJdywsEXSaJGRyB22leNLZcINi3l3/+9QeHHxS+f9/0csGD8E59wVyeSjbWveVVdAyaXc5hR
jkninXla+TgZtGaZribPwHu/Kbnpa/uWZKRp5pmkZW3kDhFl/bl+5mPD36psFQVmkn3PjUmp
W2XcycqHQT2TbwXQh7MSCai+XsodrqDfKom1m1h0I0yboTvowios1grjxfITHLAkMKOAlWfy
N7YU+bZk/a7B7sxEACpJbm0/qymD6mQkFWkRbEbpa98tNSy2v1lKsUepyEXxBNaXTgKMkSlg
SBB1cfLheQHXXxr7UhMkARXeZFTvjpnP3tTj19la3X6tKC6yUbGRUbnjnBqu+PibLBfDIKfa
xjpM5QeBwWH7nbFzx8r98CiliqPUQqhJoCszFaL8zxhppRdPIYDuZfYIEzei3ybMeUw/rU9T
loaWxBib+az1RSZF5KJk7QiuipTodX/Ok0DWHXq2jHqko3GXluPduvcwQJrtiNyq3zknVckJ
dPB1LPfmlUOfac8vPTUTjg9wzul5H+o0yHrqttBNdHf1jvMaDvUk6OlmJKHQA2bbslY0Jx7P
LxdRT2GzFPN1r04etLHM14y/682CPITUfaYK39SjXVen/ng67Bog+hIvvriwZy3JWwQltf6y
FgoChWMXttUTDtBUWfK/6Zmivcowqj7XDA8mcmZzF75H+fuYbWdsLVRrXwdn5uyLtZwPAicr
dx8cNmpk/1XZUfhB4Dhg+MC7ed2xYzUoX2n2EPemof5nyUYEBCQQNDHv4WGfSjHfizbVrv3u
Xt2QZeZQ8pzqUA9+aLk1BtYnTFiIYQTr7lPU14l1q+QwYwJs3hdQ8kEwki592n8CHShmuBGe
aEousKueERbnZyAskpjSmXgpOZWfULvdZbST7I+sp+P6dhwaR5b7zepF1+yNA9VFr5RG38S0
WmK1XJwJ0Fyukg46THJmo8aPyl8+LpuKZNDv5ePqwRLayggu6XlXW4VTqS0k1ZMHvrkd/iOT
HmoIHrRgpvjpajFI0dnWYN+jV4ZXjlKIE+e5N68f+sjuNysqRxXY7pXkAPdO+llS+gpxlzAR
QRKXqQp/PbzQ+/h0+6i/7hu6kyzV9hjDpQYyRvZcyo23MSU5brt0Y0shZz0oDbXFju5zHaAg
jUuKPIjg6Jp+alqcKDd+W83yjoailHr89+xLScme9MXplhDmbDsYIhFefmW/wFf26R8c8m53
1NEIv9Z0FPKMfUhd2ZNS2fjQBWXmFdfg5T6FWCifb0zkDuJls/v3S3GFGbkLkCN+LpNUUy4h
pPeWgu+uJ3ZnNiI3ZCeSiuJIpyMGnVpfZykp2XXrV4oYhbBFg0fluj3S+0x+2hU8/kGgvHCR
q5fYbTI5mMzV4Wfkw1rNg1rHQ8MrKfv5d/FCn2xU+VH5SwfjHYaT9XkObaeVGCEgmqh+6fNn
A63yFbVXiQzSlCaw/wj5F58jh3tTalXh5UfenVIfDwnGrK8zTpeA5Tn0y8UvPrL6zYoShI6p
s/jYVyw5aGiGYsXeBuS2ZJJHXQ2GgIK9b2VvJy5co+G8Vp+NedIQS/qKM+0/+fCvdLqC7jvw
I9AjnlhUbSlycUIHsdnbA2Fcs/SLnqRKG7YRewt5ARehG7Jf7yt7Ln/sPNdb19Pzt5+RsOSR
Vr8XLzjy83I8q5g0VAS51yHvh+in60NF0dXA40zpAmNIezHE6Pes9PXT2dJrDUGWhNOBvH78
5Y3gwpxKoGuYaUiWcsaIJj9ULM8sOFEImBp7BTKwD0gXvtBRYHJaGjpZTwdn4z1SuOOkSDqj
YNq0/LM8G18c8bprfcoabWt0UsZBKLrIbISd+mtBIjou4/6eiUR02oC5GOuMTrhY8VQwIbA3
udh6dtmgY1HbeqqmQvZC5szL3Xs3AvmWy4Lby5s8CNLZJ7ptn7ocefVeN0sIMsGnacBipdRa
+pyeyFlmnCvhh3fsKLuJd6nk9LMwmm5oe/VB+wyldRxw5uTWnrTtVAsqmE/ulm/ViPiheee9
hcl55QHn99i+mN4dD4S0DJuW6/1c6bXEpbV+S5HPu7EEhB/PW2f29si+9HM/V1s43nUQoeSQ
UVO2Ft/3KyT5yHSG4O9p0pwUfWed5U5d7ztYcFf3A7kytC3GX8N3kZsHAvarLWx6r66MWq+x
SIgxV4SIoZqn6O+TOOJntnz4PrxEOuA4N592/pTopu9vFr7cUaUiUyA/kOoT9zotd4iZM1me
lQnEL2qnSPIDJbd3lv/sMwVXVzogHS9uooljyVlaFSDCHrVBDjDWpj1Q18UcN1v9dqUdv07m
3vTVjGXwYiGAMWElU7Jlc1L7bP5aw9/fEd616b6qH9JJA9Uv8eA7J4+zB1FCAYO5fPZ3aXTx
brstRS1oBrmmAW1tDG5sSu+Ngl3pLLFEUQas0Ema3JndkhPsKJhwnIh4J0lrCeQRBzewnIY6
EyFGXjk7or6yvwq12LXlTUmfC46NNQN5G0iztP2Av2aVuyXxft8lPBGfQ80IqH9jR4YEuzCZ
liIjmr3p8wHm/HR4bsAHnrPwWYG6zb7r36JA4fi4J/MlJE1oq3gXzU8r/6JCcajHQkyKNt9V
KyUY2mPQs8SjR/FcQwcdox9rr8nsti5xtAzBRC8eJ4ixQQLThz7dkF+aDI5PIOQX5A3Dg7/X
0sMOzWqtuaq5dkTTNDz5jINWwBlFXTNztfW4urE908P0GTXnktyRYM4EMXcEbMwrBp0/9pka
fLpu/4lPvvsg0NJ709d/zqcmRn9EXtaOztUW6TOSLD91OLy+RIy1jbhylJ+BumyCXIpDvWoP
TvUSm4JRGouMI7QPEbYWkDi9g8YLu2bkZdSg/mdt6L55gwH1kjzk232hX9lhBQ4sXbuEjZI7
H9hkZFmgwfRYvbKUAKh41LlUqKOCmguw2X5o006J/0/yDmZZSGkgDAJWxK2jMdNTl4qpk1R4
rZsZjUdfvHnVMQZqFk59K/wdx8whFiKpUyCZoinGM7wAUHVExNslcgVZlz/dFl/cJS/KeZXs
xi+nd3fDMhq7qjs742vkn+uqtDTNZDPueXBvesgmTDzylH1+PVKSAdzj2FVuC/ZFI6Sjixan
HiL+bwm0Fdj302icGTlvrqUmX0myL8O5oXOFidUKo9a/IolTyJ0SP7biQZmWo0Oa+8uJFtlF
HFl7V1oiORqGJ3mF90M2vdhPv5MvfLLLc8o91q3gcrDOMd3DUHpXew8GZXsCq6t4Ah3sge0V
Dh5pwJoKL2lUNcW/JvneRlCMjK556hSv3k+1LwwXYgZy2SB5iTosHkW9I5y5Ho7f9kGAIM/j
nTQaO2sd5tB7wPGXwdKFvhWo6vQ186ayIDmXmug10n5qxf2UBM+MyjaNAWOwKCDLtWLbm8/T
n/LhuA40P8eUXWypXaMuNDjtZWjCXFkGgZRoEr3VXZdMBHXx6S+ErUHabRJtgMEctthU1Sbq
R0HbcL/FdZMmo79ksqiJC3sQ3R1oPtWVRE/2fqINr4NtWfa96Hvv60NTjo98fHSa/EBwkWys
J9fFyBVil3AKwXcMa/Edw3c+3a5fziUkbk5tud6aH5CSN1EMlrCIfDoBD7fqG3bDApOY7CvV
vCflakLM8W5D8YH19juJMVLenvZIzznKk0F7/OoPsOufrsK39UTWbazteMdiR34mJPt1ppHQ
uqrVVE3wZJYr88/b+vaTui9ODw8wiLCw3aGPvJa4rqO5aerKOaiirLtcQeSZLYXKP864Zspp
Yh5kDqXdjVZYvH0dcPHR+uMKoh8lISauJryvjMsCFpa9gF4Z6W7jnHQIWaCa8x6Z3jQPoVJF
u+/MUYHAfg6u2Wnk4rrOrO4q89baHnFeLSAzix+YFU0c+mMc7682Qff194KfOxaqbQL2KkLF
+1PFHNtExWzajGGJdx6srVoN77z1eRJVPuSn6/kOLvnb01RrMGYtPpRnnvapMM7hVC+/MCfW
ybUXEKQQ18Sg7y8DGbiVptYUz9eMeti9oXtdlYh+Ley3scl2bJ8yeerUHgqhd9cCjaL0LRaq
CXBy93RPdQNek0XTyWQI72tVd6TU9Uuu0G1oYsjtIRZBgSuFJqsn4SfQSGlciOTm8+aNygW+
/K9wgBd0siHNNR2qSI0268H4L/TYe2YZNFJ9zWvw3UAkHLH9kJkZXEPj2iD9Qbsd3rzcdcw4
+IbXjU3mvmGBzz1uMZh+IIBXWOxd0qQgpvucuZ1kPcT2x5bFyk/TOg8Kby3U580lvQEOv3Qr
qr8+WFXolOZ01VFlBYSYJVbFVtVGJZFPq51EhNCQChXfD3yWM53f5NuS4J0+q6kWfyw6jSa7
aJSopviK3GWOEFEpcSAkqa5097FhZz87hix6Ju73QkeweRouKtuser1BEn0RJD/c9c+a4snG
N3cPYlVsz0k3Xbql45fFmd5VXNHNTzhiZpUzZBKEeDxZ4D4G23F+3C/fvgjnh4DSYAtmFeZS
Ogw5vgfHraJcJRHltqbgIfmZg4Wv6JVLs86tepHtCKe2AM97Q78NTo+vVRSCyrUv1WZzi8+c
EtlY72+7fGCpL8UBkesTRJXfmW/wIACMqum+p73+QcBf8OHWzjS7IFMQsbUAg58RyOn/7n4W
aX4a9c67Bl3x63dJS9T+8/1fecAmCErzD4wushQOmgqZ15lIg4lw+n5XRv8KhiYtIiBo/7PH
VqwmF4PUzpc6SWAyvN4HBIUZxMo/t85xJtF7SZaV34dsfHn7fhzbbprtNAKOLr/WmUK1eNuh
7oAX5yYX2FcT/O/c4bi/zkivwlTe16/RR2rb96b4r7ZZ5L4symv1fT0L9r9fYRALINnd8yDw
L4V9phd+uTtCY3YAluHLylyRz7xlA5aOkhqyZY/cxZ/LPy0RsZj0f1HYDH++kA/GpMsGsMkl
Yd4BEp70IgXHrBNz/FgOdxVmE/LaQaFq7uzm5dzGF/f/q8zfjHUcWamY1ieahnYDiB8EOPhX
rrJRxqZKYceYcmSeLorrJUzaLi3vtjpcVsgcgqxGzChF/X8EKgrsmp9yfu5Abnjc1EHaR2oE
TLnLKzPntCCvGjDhzYu5vDM9gSCqu8pjH9ozGtwbJ4y4QjPXNPoROiqi4IGyN1T2Rrtdkfxu
IyARA7/xRV2RXqrWHgyfUeSxxKrBfzOKtP7DKGKaJVQIM+YzithQI7A688rUn3BtwzODJAOl
V1nIscM9PA0B8md2DF8aw6s1p24Vg4IdHl7MokqAbVbHH/RTxrJqVe3HDHtOLTD4cddFQbLl
k1iKNtjX4i2xN4I/c0ceerIRxzddFjzDsNaaWpKd8xPhNETsraDDz5knLWMijg22ai4Ggtnb
lnWyss/hSxbC3RhOEqeXDizbNMILIeVe7MVXb29sJfQT+Hzc4lJnRDvysfPO+3MKo7DXzt6X
Pgg8kp/72pAvgR/HbM13NePqz022q7VKgDK84BbhBHQn1fZqRcT6ookV60+DQF3aKahnz2U6
TI3yfJbtkdThwXEhPhq18g+fsiX121/ehI3y5o/qmYac9aRsz5I2lLvJkFQ1TuleKvLePMrf
qL7p85QiXxzvNSn7By2nu+JoLy99JGKnPrCnvWgSS/5b1dWxwJ375Bnr7/Id3oYTzKZznklL
t555lf8Vxt4tmYccEajcVNlvWhA8L3clsFxrHapxaiK7eNLhF4u3mPDQ6GWdypGcnWX+xFzn
jtPuA2rY+IA35ITCBRUahsMC3XTzQiPLAJuO5f9PW0HQLPzaKSwukZEQqcFfQcS5TVtieytW
y9AVNy7hLVPpSauJMxlrbz2zPN+tbTsM8IYVWImxrQUefu1qc3tV6DJdEu+ruGr3Hmcl0ebq
C2kfNKp8U3Af496TIgrsV8FlOA2T7lLCucUuSu+CzJ/Pnstl84lpi05amSG6QIgqwqGNWPkJ
3ww71GZwaKdDXnBAuUddGx6oNlAkf37Bu2Pajcv1JvYxhM4Gs6zgDF0f6oAVRAOkKZ9n+VDh
zEYtm8pfHIAgf7ZZ8uoBw5zZ22sB3cqdKwx08KhE9xEmVQCzHh1S3DeKu96HSV9/3EmgnUDb
uxsIoQk2f05VbTL2LQs7NTkvW6FD89+/1BXnLpxkppyT49+pt9X090aXxJ4/GR1r7hYDi2Pt
d2t1viVZWquogESjxNxce1LCb7K2tBW2MoBWQF9dbrEJQbu5+ktXR5YLCeY12e0jJn8Js3iM
7qcxz2vf5TIhQRh/d7rhfSBmkmkQd5aqVR4R1uZ1qnL05J+cTbj+yTXR3bH4QeA0vCDfRFOM
ECinboMda9LJFmO5nFELuEFPH13sh+3TjZ90S0lmtb8PUh50p0g4VZf4u/Cn3mdy45/sHl96
SLtNJ0ie5kWviPOzBKavsT07O+XVHZR0au7ywGd3rhwaf+Q86C6Gl23tzZPbvXuXMidj3QTU
iKQO9e4k3fik8W/twa70qbhIE5J7ZHmqKcW5hnbNbHUqaADEj5C5aPF4OSC+rkXkMDYOYqvc
oWrWyGXSQQ2JKH9FQZUzWwl0C+MIBMIgJSZToC6C5S2Tt27JGeGX0Mc1FofVOL0yASNvmozA
GNXhyyxZ0i5urnxMcM2qRS8TZrD9UNVGOIIWAJ/SmkYLvWt7R3rD94G6SyYK5bNvRScED7cU
0dXQcME/wo3wJjLkOAtxr47JpPvhQmlqiJUlGNSlhV546OHljco2lb94/BQV49PQnpM6akCT
xhAtIqCxKMuWxPaTjrzHw6Lop1kSdZn3V2Jss1SpBhE1EitxGhPLGEDzAmJmt/Ume9+0IIGi
7T57Pwb1Oq2lf2lhDWxdxeZlNCV/EIjb3gn/2fuRV0/q5cvWzrf01QbaZ7xQScnYjH+IIlYt
y78v2FLgWRGll0rHR8WuuFW3RMHcHEps4Gk5zW8Tecs7o+d2RnkLxzmJdRZph2h7iDulz/cN
FTgWlFcyfv9+21cvVwUoZMhMsNLvjqn3iU4JhZmz2DY/iZCMk9b5NW+VFxUftE2f/+gWkUQA
TcZ32PldmUl5fpv8zaiEvAluNh71hnRONXiot/C6/PJ7Sz+7jmVVercPNhZkL4TDTNAOKw17
YRXz0nsXzfkU4Fc/3Vhfeux1prcITlozeLR2ZFdL3SSRtl2SjVoUH3SD8KZsIrGB5997FL0S
OeQda0m5yirXUAwPKYryykFx5tl/1lZ92vo39mRnWFBBTUalvU5EIIVi33epIyMiCB4R2NJ7
Rk7cPwf3OLwvSmy2A98B6kKl2aIjRbl/7xbeUohbGBwrIIgi/26ov9gCMLyAtcBcc8w0sGjB
Q+RPZI0wjCQXqApGrwvcu4TOSEdczTfdLvMbBaNcEu8W3W4GL6aamYXnCvVvRPaDcL4aCmYQ
z8RjLhVqN6eQCpWJjshJJvhWknFLoXZTGfeyrLNxk0vTurNu7U1zv/Eyh7cVb3M5Limdeu3W
wLV7pP5LDzcq3FT+YqfnP8Qq7eMlVT5RmebOcvFEkrboVE2eykLjB4ECVJhcZMZ6CnJ3PAB2
iiOX265bG8Sznmq1kJcgV+IvbT2pyiYI/6vCXyTnBf0gqMXLosnMinFinFlzVoSbV8pjAx5t
FPAuVOkXZnBqTGQNoEhiNVioMGusCVh8xY5obLlmH95vl7OVVd2WDO8atscmysXclYiI9nW3
9s/h5PJPZg+Hr3hxb7rKRl7pahju+4vmNzWTm+1rX6K5xpGgmVuxQGZVgKWvDDAUEDSFuCzs
1jfSLeXI2Jhoe6dYm7cQNHjKuQSkApmEMkPcwFfalfTEtDQk7NaVvFqHU/q9K1nNfCWTSnSS
yMVx2w4tPNkI3jgdkwwimcauceNAZBG+O+r8W/wgW8NIvJDZuBbzllRlUnm7GxeZUAvYT2xb
OUbarcwgoMVDNFPMg4yRMVClzhv27zbq21T+8j59ifO23bf11qt8RT7J8FkSzLmewCcJF400
F2M78gPOH0wAstoi69Va32al89nepSvNraca3SElXNUzipssftvC3TVrv1xyHUUUag4YrWmS
HzHSj1AetOYqPzSRv00IbM2djdvmPoS79M7XOGxSufnu6tFttBtbCXkrl7CClmu+OjUVFsoz
tNAauQKvFIS6GQbnpOEfvv/IOgG4pBRl4dMUEOxv/brJYsEMhMpybjMwW+K5XO3jn92UuoS/
+3UTshCUQblEWs1bJalA3oKJTXe3/e1A49UO7VyyGS/O66hEUqulQ33N6EWYh2jwEZnfumBz
ypmjBV1N1fcAk1AG91XgoU3qNgpfvJ6VUKDtA2UtLg5Y3JUIC1aMx1w1g7cGc+65INtbKr5/
3mbwKznTH/BmjxkqjhiTM7JsEObDvKjMNCIVPPy1f6PFb7osqLC82upJI+gM1u4NDLHy9u1p
Ys7PsqwilPgb/1dOgP1BnZShxx8E6E585kp3pn4AEb5+M8kNNXKo7FONIOp9aRJWL3I3z208
KdULH7y4d2WWxahu1ZZNkQAbN4J0WN2FIKkTbLHuckVPjKGfptj+vbvgz/xVgE565sDmrg6j
jMjYV5N29UJPu6/5jW178EEAP6Efg37tWnW60SKCoNvI1Am91R3IXStdC65cTxRWcU1z+v0U
wrzStSycfzB5jXbNiks9o9uxTBqxYD9Iv7LkqmBSPuPJw5/FWeoY5tE0xOdVXhOS5kxHKRbr
IbKlUj+F7WgnWqTVrt2M76sfN0jYVbnOqQoIqbg4UAvz/dVvu88wbA4uiXUhE347bSCD8r2y
NFvCz6+OTHybgSMc6rWKj4GN2EliV6QHz+b2kR9+FYfulnpDBPIsyhBeLNumgXOzWW6qE+Xp
uVlguQprW3Os1InV33ERZ6cZP+IB+Yg4H4MLeGd4aW8/VevtP7Qg5f5ERJcVcFxx02yqny0Z
3JQ/9Zo0UuRrNUCnla5nZoEtcear3o9HjcJ2mUzoEqAejlM+PqfuJGXzuVxLU/xdwqzEBx3r
+S9tyNVafnrb8plP/j++9BzkhHe+UxC9oplpDoTCimIK/dSsLfMhocu94rxCc/mZk9y/Gfpp
mo/Sf3C1svTAuU2EyjN74GqW9Dz5T89mn6zUf+oDw5SU+yFvRxzu27qhd38QeAHn+MlVFFns
nMxkVinHZYpc1evp9Lb1Sm9LKJyfbpsf1fwJy3t0Xu0TLSBYTEVemDcK6OF1CelU4K6fqryy
NFFapuIbUNuL9YPDSp/rRaREyye8IcXN4URQu18v7BMezsTf6qPQi/+aJ72j22evtTSmSyBN
S1SyWVfr9KbTo+hzD9bjhhZvwjoWIPs5ZELwk+tdafv16KbIu6t/dHJJvudKErxZDjmyx1j3
wt61OdY8ODRTWg74Ffd7uyca8d6ae/aps0mBV86y3MTrlfUo25bVst/2pq3fX+22X3YivMH2
nc27QulzPaPXWIDqGRji+zABaXH0xfwAPLIIf17PsTeuYnqQuyAi73kwjezZc8mqb5r1u8jh
ggRDTpumQrtuhSlWJsV09oNAx6unAVlKhh2VF2+Cx8aD1pRxhEd7n0P0Qgfaphbs9cSwrRDg
hbzJEG2z8JhloXzD9KDt71x5Urd6zlFmwtIfNSWT2L8QDy0RX6tllotH3Cpa4nq/+iDwpzXG
kUvadUWhdAGadSB2RSS+kZGISiosO7F6g4fVzC04GhYB1uxwAcC5Ow+1Zkdwjr5XTkmAGWk8
zjKsTCLng+Q54f3SfTRAu9HPqOkHP866VVt/ENhdW4ftW7jov1cl7czyRKvSq4Yh6DAlkXOq
eNUTzXl8Nt87N9swOOKXB8sBC3DFJDCj9iHUczKqBQS00AexmKTDEazjumUQUOhgzTJS8sW8
0Rsm6RRwrubQmJ8+cT4hht5awsyPpy8yhHpgvO+fyZYa2YlAry0umO2NRK4qxsCB3MOC5JKO
6GQ68lhx2dWA8eLUvvokAdqDEsc2SsIfMwXhaSpW66kilrvz0T/Z8sKsBpz3qa+s3/TWpzHq
cmRH1R1Yilb0topddKlw5M/UU6pr3V7CJ1wLdEay19oa0pMCVuVHCab8Wvv6cBobUI/n6t1w
T3s1LedOCJHkAjyTM9TmyBr864hsp3k2/IxsrZSjeVoAvkbeqSRFnp/4bTc4gnnvbJMLh9DP
CCcZvEob86YtnEx1QAdjztbbTbk2lDizHkjNSqOeFEaCGfU3fI9POTTsWC2KSrXKHg9kApGP
q3QPrHkSQCTnmwFX/c5Vh1GblLa5cglFRh6yvQqXoJZzCDgAQRcjM7uPadKn1dpF3GWwlsdg
PLjaIs2Pt96Fn8vGd7YdGr7GAQ0Hj9XPep+itTJJFyJG7gqNPsh1vEcdGfIJ5Bm4g1cTnzAG
OLrDvvo4oRa5wlz0us4tjD0qosJD2OBuu1Tcyd7eyEbJrmwysw1O62sVGJld7hkRU8E/nT/4
YojMTK7BIsN/2rtWcD3UijSUmaR2kNLKuq8cwawTGky/tgzG1jfidq0xhrJNZ6uGfwqNG6FZ
M/V9FfQCEvhTmky20BgSPh2ZVj1I3h3Ag5vedQAfIce9K0mF83jUyPjC8sVSsO8FFkSZi1R6
OuqAZZ3X7Zif8Q2ZHr2EG4caR9or36vw0wD+KxpA0AxwTYPV1ni7qSEZ+TPh5UmHLMSyV7bR
KXcm+PxJh+yCY9NqfEYutzUN/kknNdjAEhmDO8wMXF/M2XHna8OvBc4UFCVLWuS+TY/BuNLv
ZZr2hpzWnVxOAQ2OdPF4j191lB+d6vDXkyGXkrSrGW3cq6c51v/k+PqjKyOJ6/5P8JzWxsF9
X/0djGJyZsV/XcIyTKQZHhsb+2N85RaLpkUaQELBICc1rjpcTdy0SNvxDvfsw01RKxsVfXng
3U7ZoDtUz/bTlfcveLH13ahtfm4Az2Q2g8mGoMKkBBuc4hBnRtpuJUuaNgQy4zNcemYj3vbu
TXZnVgFkN1n8poUgJxWPdpaalK8cGSIvoZ9+M+ePJmCFI6XgQV/lzsMLyTTg0fn8khnDE6ho
e7f8yOklPZj6B4Efdg9/ArWPtvP7ipYeLnDx7Nk0NUOenjtnqj/snfPMpu8vYajl6xYMbYRG
j4x3OTA2dpD8fKCHPR98Ak0UGHoZrFjXyJ4gpTztY48smOs3OQc/vL6cur+/lj8YLZm+nEMs
h8ucqcaRyddkFS1VZAvdwOOEMML1Sg5SO8DDk2NJ1rlZinsUAYKGJaiGqaGeduuJclW3eyLi
LKx9V9Gqq6dRT+iJxeHMH0R0lWItLF/yVtTVeGr8VJclnrO+bDfB16MLY8PZRhXO/SLRlshu
/7nptZFx4b0Bz/sO472Sx27GihlpErThrr33C6reEd43xN5bN42U8lkTGaGS1cwi3ZHPFY6C
I8BvVC+0vIMCfo5YWYiMfjtxsP6xKfJnOiJFhsy050wwFyN+0DPsjQl7dhW2sBd8Ry+cT2HY
4TeG7xpqF1EruJeab1nHXlc2pZnrIx9G/sw2kbcbGzE0HfQxMknLpq4+ECysG0+o0ieugKNl
1vvyx+P/AHNPntFLrbzjqIojPwsZKs9b6Y3Odu3hxZ3XM2Td7tZu/iAgFhrXVDgFB7ZnsHsa
nsnsKj8IVvixaafm9HRBX8MrPPEdzQb1KEA12rmVqZzLS/pbxOjI09H5bPLz03+1QuG9d59A
MllOObLn3I2dfrLqey/r2UXjLyWq35ZwT+TISjqbyLsdx5buE11yhaOdWMFPoeHjb3Jk7FdO
BlhbxoVdL8W5gtqN1H7QwZdrzLt6D+sq7GWtCeESFMKjBYb84YYBSFfy03N1dR8EduZT5dbf
tm+PapxQaU5XR57pshdx9u2GCZ2E8fRzhb9HPMcBdLDJHv1pUhlGV8+NvDewJMeLLd7E47KE
AZLr/LWE0jhMMg7c81boPdfcCTZbqV+w3UtMg+eUn03jEvbvw5w+MjZ2FjUN3O+bihSunzCb
VMIXjsOuKJTMqOQ031J4Mv1A1/4esj9+UoLXG2UTadFLnwTfAu6N2Z2EAO5jhnQvmHbf8GoK
N589QgFrLroAI/qfSWtDe59Lh1v5Lw6M/t7exgu2INJ7MYjttul/wO+NW60AeUPaaOF1KW8d
MrL1+MOwnrEitKqQUVEIpUIjA62eNXOyxXfu8Vmeey7MUBL4C+pg2wIcmOLc51qnaxN0diwL
FTv0PGCa2fRfy4hLJGvCGAX3mljrfVpjXje4I16U1+PxMCAx3GH5XS1znI6DjiyuEc9Q+Iv/
P8QjE2unpJqYD3qj3V2Gkfx3aYosJAkMqwalj1b21TMjpBkrgCOac1erdLU4uaMZaLWagatO
zfE5EWb9vtfLOwOOQJELqL163hFGS3pJi5Us0JnR2RXGLDQZcfW6tYcjtmYInxJnHPZBQLzx
z+bT0CG3lEb3HcHZBxfyD7Pivf35cSmje+npd/Vo070EF04ZrjgksIYOPpxMNL1l6cmU452B
XxIQ2OUz5b1WqaNQojCS8MrVMGo5bSahu8NoRLgi8itj0AQOo2xiFPOtY3t/pEKrGcRbTvEJ
xvwcty5pF6VVsD0ZmLFO1ncJ7/pAeG+HIZG7IGTGVZfxpEDrvvYSp6valiuTZ6+d2ThgbVeQ
G9J8of+31+mudpNouOXB9ePVln+fPFcklYN+kXzl4Gf89F96RPKbkk0enRA27yfNgBkqa3i0
TtNRSdmDtsesFa7yU5v+uaJTi7aIKy1OU74XJn195pprNbzVpNxz9cZw1caaftNlocege/5+
OFew3AQRilEEBlIu82nfNJV/4l+DuEVHy/QdsS4a4ky1nRpnstv3/PkJrDLm4AWcJhfQQnr4
m/tFFLD54Bp8SUFLavUT3//3x9tHMSeww7l3Fy9LSwUy9D8I3FsU0m7JKDFb6xR6c8TdR7Zy
Pbm7G8BadzZ+VQJmPJO1cP5O7yKaPzlBiv3/mZyMa/mT0xm9k712p33as1+3hyIGsmxWuKXp
O5HB73RA/vFvSRFO9mV2rGtrQODIEx+cf9DbcHbcCPF24YKMuwiKABWkDM8ZvJUEhxAbCmr5
y1A4iIhEdEqkURturB7qjyC8MYzYP71X/ZpDh0aQQ1J7fytIIwIbNGQiBg5FHwWDoX3ah9By
aobVS/z5d+D+uwtPBAS27u6dQAjaQN9cmna8x+kNwQwkuXj7eQJ9rLMINI6O6Nn2En7CK0ny
dDyj29CRiUp6eUqdaonz7wiWtWabNKQvqd3Z1OD/8HmJBIqELiUdAIHc+HxeAR58Pq8amNa0
Q5ENf0DZRXh4RTB71L79ukbJbgljen2RyaQiwN4rSxE4/mlmyC/2jwsBHddqmsZaYKKBq/pE
RiOtUIsYMLK0ojE7Hd599uEVY2Nj078FNyeI2VT/b06gUBKkxwfYvzGzs03HA/tnFUmSR+rp
rZoqNXfWPghc/iRDX7cX+XkomsAKn/4zUt8xdPF6yxStavkJuf8rW0BCk6bAMXm9r8eeNqAh
qM5XdXeGr+rNwSfxZwQE+PeQgiawSflPUQONNTJikmThdtTu35ofrLMjF2+6pOlrAgD1lrvY
cFWwoZzaWjrHMu7dHLuV3jODQNyI7f/K+xsCIjcbJW86Tfar7w8m5SbiwN36tTsBFSTWACPD
IPzhCeIzSeK52GYdeTQkYs8UIsC6Kgvo5Zl1/0HvomFL2e7N7hxx3w6FMyWZ80j9mPLDySVN
+Vlj/zCkJ+NcudzCQUCV4z7Vcta58ZG+W/S4UzmpMdZuHoSELCXyeMJP+SAwO+vs+Cdb8it6
s0FHSkp2LhAbFQ+8O9GsDb6lAOzxjrhlFn7fePuhTxr4ylf4n/D1A8sQTC+qvba8wqY1kmKH
djneo7Def0X6E3X7n+m9TIAB4flIy+3V1Bmem2+vFlNVGFIVY+9fvMq8wMAuhouBGgimUcYt
8DBllawc9iRIbPJPU6QT9zh6LroTPYZwZm5f4RKM+bHLTtV8QtJu/g5AgUZ6q7Sasai03Evj
nX0FLXi6muyjanTkt8ahyki0zvGZjNp4qYACRtKctYmOB7aicakiQFTeLhF14IRDaq9b0Wnc
0OPM6on3BZ7J5ve97c9F3YJ7YjgxQCqIaprRBFQ3LiDioSBRTfGmFiHFnCzlh+UWqY99Oocz
bz1yeNCq72YSME3lE6rxAg79fehr/057KzPvnnuaPdwPebBwpaugiX+Z0abRkrFTILC+Idty
LOG2LnTV9xbSpnCIw/IMDTRGcM6c2rx0Eh/r6PNpVpfRCyeuhpcA8gPMlxmzL1mO62D+xaZ9
bWz/1vLlUwPnck2cxC+9GzJnz8+qO9Ykcqf//PnGJ178l5MUH1ia3mfCSPs1MKzRiboScH/B
S2x+PMa9FYMuzDq7xTeBPlXZ/53P94QRMheACkHf90qj/x/y/jyuyWvbA8aDCloUKAKijBZb
UBAoMs9aQaxlkIYQZLSiDAGCzDOolCKT0VKZIQqVIREQAUMIIaDMM0IYEpIwz0kYQxiC79P7
u+dXpac99p7zeT/X+/pP1tryrL3Xk/082Wv6rniKlsSFymLTTd1QWeOadCRtg+fCk3++DL58
9BY0fTtnhtpyWvVZM9L1yC4+XCDj8O4///M/HeUC6wPwu1b2JzmNxZFCn4ss13UJwKUMlu3O
j/H396stStr5OOA8xE9ZllT7zGYGwh2Q/F59AMo7HxYhojqRdqBjZ0rqFqHa5Ahhrjp27byh
tkm6N+PRG+Ut+FPO54Iz6TkWlXAI0+atJvN4VRSKcfZ+/FyP2tnEjqyFwBmMR+qNmlDF4YJm
yRqdOVQhU60P6r4oZfHG/Njy4UQ7jOiNpWZ3mHiCfccyueFNrqx7rqwM3L7E5TQGLuuMD+hU
aw5mfi1gNI15nN3Z5rJAthMNgUvwgW0HWOvFQUpZYvIJxwPsWwiuPWdKSiWpvc6vM3bEnPER
ubrgMStRu38HAQkE4jHQ+zx9rNTSC/NsnLzk3leFXuY/gxCNNu689PzbDZmMyT12CG/ZQvKv
N6Ex9ZRQSmnPWcqgjzJ0AWr/AwSuvxCkP3qZkUzqLLb42SEvBl6VUZF0EfqmRB+G6sKFYfCh
cpQDdX/6BX5krEigNe1+OvLL4HoE0oJmTBlh3Z7QPYfkZThi04vs1yMNsjwTVllzf7rd/nT6
/83/ocKe904wl9bLsqg0DYwvnUuNIK3VXJlh3n3I/9WWb5nnZJ/+HB6e+WjRNIjnxR8V0VtF
SASPNSvpaXePewtVIr6dS4t66jxBul+qcLUVJes14UxORxjhoNH6eTXGgBvX6jcYeS6QX/WE
V2aQQpJqqr6FzAjEgBu6oYhThRj82gFOcnLfpMwMP/R5HND1YHV0BT++LhtUunteWiSgE294
qp1bcJH5LXLyZG9pifUzQ4UppBgyl0K0WNHiadYs4Rlva8YlmSiFBghTclGyrn5QqwbTQKCR
0flT/zPLCgTScT0RnPd0CRxjVxBPfhCHvftKrZ0UE3hj0g4tU+28pitMNDiNmmrNpehzbEdF
it7UYjKyPDTPLrve06p0h76UzwwRDzIobGkq2xZz6dxdo5UOonsVTdCjzQ+FLkZTvgn5bsLU
eXxWAtq3Zma9Y4eIs0O8A126adw2U6lRhFpsRBM3loM1SqAT9IW6L2+J9PrGw+1Q8vmFcXFx
TCGpmv2zIKtu+yii6CFDHw+nHxsOQOZKZ/CvmRQs7eDkPSD2fWySvH3xYucIGW1X/1YtSaMT
uqpaXtrn0pjgM4Wqnk+Ldx5+CDHRynZY57uhGhzRlg2t2BHLVZz01stUNTebZS73jw1hLcKs
OgIRxlgp6WbIaC/8Rsaknugvu9k7XtPdkIL7mTRlQ89F/EVZv3Mb/EVmQaqVcSXhuo/He/0m
Ss38DHTXu+9Si9IyH4PV9k2x+dpTD2E9ScKeDGEvOx2vjNz0zi4saTrwqa/ubtyjUOfXJWGd
YMHx3JxVYbBp8F2opNfpXK2NMiVjlTHznvvp9Im0xJEHvawZGnei7wljYd+A1za5afmGqsGr
pFOYBy5F6Rv1zOt/9xwAUlkZ/3JkCH95PemiZmVVH7tZp6BYEBZwn2DEibGKPvnBwZnLMcJT
jQwN8R0OremTikvCP58AG1Rq3laVR9ab1PB1Gztc8tV2ptgGBLmgXmw0AVtedUUYGh2jIrha
AxQLBl64fv2Pz9H/b+Rjz81czXDTeX88DgWDWMB8vi6lpa/nZsiWtvAKz3kn+MnlRIoTjbGo
BMHnDlhDVemjvuNyi/lpGxei7vzZxJ/g+GlntFTCsnJ20mA2yXm8KfPX6W0DfhG0dMO+JS0H
NLj0drfbwi+QMXDhrM0Jn98iBLklQHaHZNYfVD2Y4zOBkNCaao4VixUKznweamH2hnNYWqrf
+JrtTxBLVW9xqZGO4CDYkmtF0P18GdR8hls+6slp0QxHd63Hnc1Hvb3NZiKz9DV5Ml+t6fNS
TViyyXHAWVcV6gbAM/CkYwNvyGOtwILCfWY4/9hy/4Yp5I/2ncv7Q+hdSrMhtilSiLyhrobE
8IWhSktf72AhqhdRcvxGePKCSTd3ku2ccasIIXks55nfLEYqahIHoli+xT2qNvguelOdc2yS
aChrtN82J6UmwST1HoS4yPBy2rp6qvSquREWMhqloIu8v6M85trg0Fhwy31guTxSCXbNINZs
pN2aYfKU1lIyspGLyms2ZTGpuhaJn0/8j45IXM8ePU6KhXlPTdqWwWVlPLD2YNOgleBJscBK
RcAT1ea3zIjgI7kyLivQnm8cN1SV4Cfbf9HnO51VvIo2d7ylxkpD7z9YX+KOHmA+8hMrXOfw
PgnW/EJSk+3RgVEWSxUEIEyr1p7TobY4BGZVrQYduCNhGnojfmFJIbdaIZ7ZSZKVlSlcO7Tk
krN6TsL7uI6KTzcMHHV1jH+tB0P9qtoFdXvFedzxqdXGsqWZpjyq0VF5GBL6YPfFKQY/ayb5
Z/1L1GSxgs+1Qlwo7SmeP7gOoxjJoVgkb3WxLcEsOLWAgHiTK78eHql9ADX6DmTHR88fdDaf
QPL6U7zF38R79LPo8y9W3DDC7PmssHIHHLHTsbJdjYWUS2gSCvrR4VKI0QQf2nqNqnCdXnxl
ShjimFmt6x7kRbRixesfndzibttm4+xwTkULdV842Y3UmNK9o4dtrmm8PDsYXWymqQgV6bMK
Ds75FiF87+BKb1OodujETwMTX4X5BsySoaVUdvaJyJQshFEzzhWTyxZh6+OFCFE84dl358Kd
p+UypJ7oXX5NsiFF5hUN4x+PuWXqflNpNX7DpKWRjNSEqECbJx1z+o0h3WH+FtFchiG6c8ov
2R7HAWTNdN7bmpGz+bJT2QQTD5LBkY4dT0p8EcKMch8hAZGKEYJYjo7QzepskoQtYfFetrkZ
p3NlMgAQECOjEJmT0uefSb20m3FlMH5gTadXYmSR6Jt0CnaOzzpRtzfw6xW8emhRuS8qrMH+
flp6ASE0rDn4zrXSL3Zdw79iVSI2LzD/thkHUlmfN0lypM0g45Jj7EnYS5HITGOrTfeSaWRC
0GsEklo72iIutX5Ci/VSsTtUqdfMv7srjQnqf/9VcEBlfgJD99BL8whNapNBVSh6X+k/jUxH
oXdTmcybpmFPlrpibTmLSeWNncXQtheqaxHfIKRT0KyVQjTd2ZJ5r+f8+9Lepz8WPWB/NzZ2
QJ5cQ1hWvQ2mve7TCKxMl6zB08ccSlf2ZW0ZuvvPS4wNtWeEdaW/qtQrBKoMe4qDgC3Jqg95
8v58nzh9Rvp5l4hWzfAcdFzX3KWtjwkUCrV15LFBrwzAK/LtU8ADIjKoPuj4pkdPvqBdPdyi
nBqxO7p+da/aPDnG8yrP7VuwtPpKo0Got7IbUAAvlEGFVcV1Io6WenvNPLJWehyredZNTBKd
rEWy/pIoNNq3GuSx5J6Z6qI7aGXS0msmfFUy6s4OzscvXXHMvGNMg4hH3bTL9MtOt986JpUN
q8aFKhnPLVtaxBfdf7BOHCUKg62arztKfxmetLhroUF9GjiADfLx5nsDJ4o1oSGEb8rNhM3A
ZolhDtNuGMDzjSrKQKfFIXn0xM58pgUC3Y+w3mkJKmBQTo0dBqGpqVIRWapb60sGbsrsvdr9
Kc9tEfBmoNJtINgS497ve6ZPvpGoCmtISD6GJogM5QKHsEngyIWScW0WhDjggsEjX2D4tI9M
NyeKi5uOW/AHmzmWYdQz4MToTPPKgmtrNphAHGQ3Nkgm8xdWCcVnub85kjLRqHJymd5ehrF+
S62O5a/Ey6A0pVILob9OXXem5MlX+50u7ZkvNx1GoTxKFJgWMJdI3cYpnm/DCUulAvf0hIfD
AUj95ncgl4rwcL3MlNNLpwmPR9nXRHP1LYzwkPbk1YWHoSCN6pzUfKBr5Vqxs3lT9+vWXC9a
U2u5GRnqhlRUt7QyhUjrXBeEJnCUtS+ON+fdGvf8DicNxgEvaBev73pjjAJXTJ7B8mvc4tbD
xS2ttoAWLyfHu41L1L0WE7DhJ8d5aNTjgmaQvqTCRlsXf6CnlVeDRe610kaSnjbWu2a36aSU
tP7XIbMJtdGcb0rYjoTp2G+XgGC3WeDBV0t+eQfFNpSslaJObOTHlqthARzG13Wl4yl5KlQ9
hShxUiM2jSlob48VNDDkKVyJyfGlt9F4sA4kIr1EmE74jtoWb3B6fvOxMd3EEpVGF3HCk3Qb
gqcVe4XJ+TCUe75sEUOqgh/d0HXm9nZ02EXNSB/NgFE6R2Bfeib2GqS7GUJyUSTnynjgfMMs
ouH3UaiCRsGThfw+OiU+hxMqXT2V9plHtg6vQzS8YWVOd9HzKduByAcFnHa4S+SluMxkQcmF
+yj09TugFqDtfIBtrKz9aQKkKtetZ7zZLWdXIajEjslg63N6Lp//m7AuQLTGmIjzBueu5pXO
W1q4D1Z4KVxNX5/OCm5iAv1cts9X1x5miGl6HwyUXcA4xZpXvqrAfyO/Ps5SxGW/A4Xzf5Ce
cai3P/k8Hqv95fgDbkRy2d24wiD6toTnYth6JIt4Ppryufp28Mil8Z8GMsaVYGKyPE/NDGqc
aVijbuxc4Ua9958+Gx99vJ6UGJsCx7bFHocT9XOLEcW2Gx5vcEYRS/JvgHo9+CqkaiFteXgo
hNhcPrfDG/Xj4f9sed6frv//lf8AkrI81tpfhTwcrm7YQSvcBPCTGrcVrm0+hrBK3h5Wmoyy
LLCaEvjxmhqRepoUfJxKR/vAIpekRv+wODLMUaBhsZTf5cya2HaHScj9Jdf+9QsPTGRHRMhZ
b1bPvGQb4iqP7ChKO+LSrW+NiBXlvwPdRcREydXnwuLiXYrKhDfo+rlFOXUtFjE7p8do3KxI
qTdjP/XXk7dkhcNdDBSldB+z7memeuSsU7D6efiADqJ+jd9J+hMQSEYaQjgnObeNucz+pk5+
4392rv1e38fQ2l5u6xpqV1RCSDXfMG3wiGHdPJL31j1U8GYLQdv+xDgPurbES7ERO4t5Tulf
DgokM5ND15lGmb3pkOOrmsseS7U6MFTGjYyJRis26uGi/Rfz7Z2xRzzK8xl0sClt61Z6LiUw
YNFpv1KCPzv/TGv5KFS9u9MhoZzWf4A6dtCGYR9UqXG76mmux4h+v3wBvh3jZf6soNFh21iN
WmaRF4RUDn0OFly45+YpdXqJHJ9htRCuTsvgn63Pv5HBdNeJeZ7hRVSh1ZfWoVyADLzlykBk
Fv9vtuyhsE7m9yUCK33mgd1kkWHqyDdlpP5ZNiY/y553htjecj/DPSPcb1YtCKsqKBIqARGp
g8g6RmlEXAomwIlW8+LlkNxqPC8Rpb//2x4VOIQaxQ5m4cCCYxBV35m7pqYjpZjbFQ8st67f
DrujZa2pebTsa627tfDhJTitsykhw+UAUVrykoZ+C91qKyfJV7aITk3DjEFMfxRfEKzQSGmf
VoXN4XQ95sSOfcV5nPQoSNr0dWUCHFeenQnAzWX6NwC/oGrNIcus/FP9d645mZeeKxHhyOPZ
lD+AUdFnw0KJuhPxA7JVCY/nbG/599Ga1RoXllUZwZbMOsWGP2xZYIBbfr2gHtWslumqoWhq
1zZUFSVNboT4z7gaNZcLjm4vHb40OWiZB57SjN7UmGcKexZLS1OA1Y1wqr+UanlfoMCX0zP7
x1PlR643rGljrRa9fKvP3GeqOhyHwgoqQjlzdyDKlxS/oUpriHXpBxiZB7Z0N+fNdLj88FtJ
tCjsfUkf0B+ZniE4UXip1Dy2NVakHIauT8g4+8PG5gaTVE7mXD950MhBKnPnxrgSYZS9xCIm
aqEHEoatBskco7C6qusfzPZpMyJfDQpZ5A8sjxmgR9kr/p1QKdfBhCCf+V014HE2zwuzmvT7
6YTozAR9qH+5hlAG4Cnb/YYV99WhvWrvd0ftPp6OnMFuvAQasfrMDL8xLHXaPw341+6AQFyf
bxVvPmRaUKpNXh/jguL/NIlwr9T3ed5HC3FbL8cM33ZCl6pG07NVdpqqftg9aMUGnz16X+pa
YxdUO3yiEockgn/c4sE8DryP0Umc2OKJUGvYiHdvL1ej5etuPXLyzjp0sYk/XlfAei3iu7sj
3/cD6KmOcb5Jqk7lJ6rKrXaSqpUB4GhSrl72fP66Y8sXKbuTp7K77ALuU3Q0OgfP7coN0qRv
e3q2p0N6qXoB4GN6EmhLQRoeYpdrEKzNEAmwnn4HilExR1Rp8mTjl5bDxYUQ1V/n12RaGrFQ
+iowdBCqJDwZQioJnmidYggdvhFQPtr0LBqm9ei1w9iTGSI02t5d1KfyLMyZ0BocpFBmb+It
7ZbropdjeFrfQAfr66xFRegifY0jcFsHZkV3DJ0JLZwXISXshVt1HFX+tdsbMbrdTl25pTwj
sIAJ9ypic9TPa1cUCPYmXZk+BnVfpEpUZ65CO/haSXYe4J1Gd7GkoebKZ162cMvM1DGoFHf1
Cq5zaz6dTePpJ+dXoW645XDuUrRt5hSb+BVoryn2PmvdAoHZfmbDr7Gm4XYdmPGc/mGUrMqN
GzAE71qwf0c4qjBntIpf+HbYT1kCpOPb4jFhF/d7z7I5qEyb/vCI7ZwjYE1v+5x1KlbF1GjQ
HnBjCtIqzus+/Bed12A3Sm4Gl0JUqXLhHuVC0jjmviB/PYwRE65AyTiTMfe2ovpGCVUrDh9V
E1G48eTY6Pvb5h/0vl91xmbXbKhZpwfHEYjOt+um2ujBBE1PqOBubcSSGX96de0lDJCmeMT3
JYzp26WRFzu1Yun6fVulCfP0r0fD/yHmt08JWXavF8PscZUGfV4GHZqfmhoDUZ1vJEMsVbZH
LQ2v4F1PXZmJvnGDhDqDQU3A2NDdCGmhl0pAT00UV+T19yW9T3/00Us49Bk1wT5hWSoupy8Q
L3YfiDL/0D15wHzWI8EstOCEalgw3XlWA6hED3C1WOLyGH1/kk+cli8tcdF3AnJJX+bGLUVt
G8NR+MtIjqSKdARzn9laQUdiyWUN/fs5q3Gp6GFkNs2ypZR9PfXkXqX5ap9C795NdsqFeteX
27Otwh8bihtoLTcjKNwH1qpWF8eQg6V3Vy9E1QEX/qcMzt4Ad8DgrCrqeynfd6aR+DWqPcFP
o5CgPlSSGQCZjM9PQ92Qa1YxA9r1qg7JIHm2ElYN67Ljfl3q+4GhKJaEywUHZp01xUt1zmFE
lQYDazd0jQOCSqb8JlBhQXTJXBmuOXbEzU1M0/0EkqvAynYopsJjmbZ47sxBOe9iE3VhI+Mw
0ZjKnc23lYeQlRn89c/WqyYghYgEe8lhbfD8ljXL0TDqZcmorqycfUSrscocw76C3DffWdzp
OxJRA7s7E+4471DPr2+zZqC48tWr9e1lQTNtIhy1vFqYb+hsDsm64g222Chzcl+/Lugc7C1l
GzCC28Q537Ub9NxSbrlhM86X9dzOscGxTx5nQB8+iDQ3718bjBVTKp6DvwMpsAu839DXIlPp
2z2h/N2UnfLZdJvNTPRd3IyvWRHT71jtFzYNTfhVVIItNLchgm/oQMnYQbAUaEmMqPI68hs1
xYOypzPByEtLmZvEXlWqO1qexReEKiAUqXeEj4YWl2DTylcYNoy+Nd02+W2g4olYixU7sINL
4XyDfEoRhuykcFVjBoVcuttDwgaKtiTrYaXj1z9Pzeny0HgH0qwx7amKe0qXvAg3T31qmUtp
aG8FEEdiR2864s3aPPJPtc+uCglJKfPI1Wwsc7eucMVcQrYWfLZoV4LKLeZJ4MwMYgOrp/Vb
UdePHjrevaoMT7Bv9rEmVtHNxMkO+WnruarMfSH/qpckkEWLX0h6SiG8Yhtj3ZmzNtqkLr5I
5WEnTIKDoYfUk7DSb/ngSdCfOYf3xW93JRXDqtRNOjqvCUVh8JFAzLfz/e1/cBII9j10nmgt
eAd6TY1kySKSfd3RplRNFgcCmcooMRvRQri4zHgDoON33r/uffpjK4APqM8PF10S+AoXewxG
13lQ9szZKJTz0h23c1VP9GlTskM2oZETGMY+EZKh9GUoZbE33WpXisvtT6d9fwmfCK1gVzz9
2IwhcnvQbik8ODNa+ZjcQEIVVdR73dBNKqG3zybJ4heFNEunkLeajs9iVRaCMDc2vNcpnB7z
83s15PnJ03QMSF3s6ERtG1mKdLALWk3ZKJb+1asme/JhDw33W/xk15cQnuftkP2Gc2y6tJio
pf3qthdE0JdzfDOwhBKv22EMMa5WQJ1ZIY6yHqyqHBU583aiu/ynKMfag53c7/bO/Rd8b1tD
Y2e5tQZc/XkCJPwxrsLYv7tcaPygfX8w9A2fo6w6XMIrfAjdfkLMQB+oVbhlFI2e8i1tPxYw
TMhsTz2iTEG3O3TmFRCttss9qoAiR3Nt8/a4hBrMbdJvpRtez7+LCjPaf6cfC5ochMQlljiy
KiXfgUYHGM67vNVh+5/f9MdPOslMQWGjXmoQ6IMIAZ/5fhOs4GOS/qjPsMOZTemWuAR7he4m
5jxpJDSRta27vr8UFnFSW6c7LtGeb6wgaMVcA6sORL8VjK8vQKvlVyodIBCPSJ8rtJBl8DLY
Ig0RdZhAPiiZ2quZmjEecapRSeYaEtzrfX1kO20tung+W6AqKlBuXFlak//sVk5G7/Obgdvi
KfWDcP9zpc0aIci49dziVDJ9K1gC7noxu9PI4lftxD5li6JZMmyqFJt8VWegqPdUEutGpMxy
tPOt7qI5dEgwZ7eJUmfU5a59dVzujDjm2+Eak4HA6WcArD5NeNG+95w3tdKs1LiEBstfzwSL
BOWGWwpJ4oI55x0N/60AgQK5OFJEVNtzmJTY3DxEO86SiQwIPlFuGH0H5v99R/7MWRxu/xsm
JGn9MVAP+pX66PWGiGp57nt33t8cR8IDxApJnCtMKs6IVJnv89o7MI1OoohtxAgtBqsILf5F
uuLHIrjdobitlt5YKcIsF0NIWZ3r0S6ToWtN/AFREcYnR6u/GjWu3eeNt6hfnoRvlqkubEkd
03dqutf4wSrfX/EnSEObbReD0SlJyFRys3eEs13clqKhTtQdgZJ46Bw6RZ+SRGu+tNNeEhFf
sXNo99BZ4b0qcr3qXyihZqb6UsBmVkNYFRX9fLl6pMS+e9V7MoA/ru5rr/g/4fNLXgXRIc2c
pCSRhhFMeVEJKsIm//lIWtyGSwYA9dP8xYljviFaY+rtokDKCHwYoyqtbgYBW4UlC0mN6q/9
XeAX0IGz88wnvc99PVAwkd4x89jSuZC17o5OqByA+/JIhRHdWC25sH7Tk3HWy505OreV87jQ
pJgmM2AsxK7Y1/2BCjwG4Tu9YT/4jTWYXTTPP02IKR1bOIa36FVynpjc2Jbfjj4J5JpU36h2
rYFIjkfeNrjzwdW/Mx+7wUv5X2k/MlHalrNgTuDxio73t45IVO1+LRFr7CFiN+Xh71gSh7hE
w5abdi8WJRnu093m1BvW/T7NJ09dMHiZYTRv/+uoi5HFbjxVJ9KetcnetI56cPDb2aQiYyq/
j5DJUk0wOaPLtLl4tqoCvGNB4n70B7U1MkrnHF0ZYciwk0+69oSJ/v1qkvem+xem699pGg54
HTH9TFMCakW7oV1rYEc3xcs93QEP85oPrhw0mBLuP+TXswDJ7Zofp8aph0c6IvOmjEKXYdMQ
VcOFPBp35XurAs6MwvP4pw69m2Sq9oZsuKT3/m+7MeMr4OManhbM51aHm8dKsJdmxgaII6/Q
8bPEClOJeRjCWmkotwpJ2//yA0nvMR9to9pwblcGl5exwU/YjnqdUHB7fETUhXIX4Ed9YXdI
H/GrRqpYlCwp0B5MCtCvB5Bhtjjo/MGo9fMZT96b7VMnvwDCOkeOt0+mBtHSmFq2Pz2KNAgK
X7B+B0o8cHvWPTO0xlx1bh2yJYLOjFwH0F8i7F0bwUzLy4p6exV/H01CtYZvQoM+tRFvKyf6
SjFJh4V9suX6tgJ2DIZDGCCSgqQI/BmwfNcJZSi50nKCbmB4Unnm5xJDuLmLdmiPVjkucNoA
gZpxbGtozTuaMXGME6gMgXvbxE+jcuPz0x/0WbFQQM02iyHgD7jtfgex4Obx32MY713jv+L3
peoMhnR6CbilEQ657msMDQh5fLt0DsJsYu4z+bt49CDQcqR/RZt65PfBhARfJK/iIgWsgOku
RzgMISPvc19fg/R720z7BbjXJpC6HJvasEAfqjbVpZoTGzIozpLD1x+s9VdqxXH/G6sOT51y
dc0dm+rw0O60zq48hiWo0vGq35nuKYvoYWHIWOAQSbII2L8v83iJQqy5h6GzH0h5j/lI/7OI
2eC5Rcijeg/JHX/LKjQy0H9299BXyldG3MpaaAKMhqhq5QVRuRkW8VwRMP7kvQk+dfJQEVGs
E4o9Ng6NNiKqhZuUNi5cKo2lRjBG73P4VsaTghKPS+4Elal9R6m9V9Oye1wxca/GXJh++fjb
52CoMKNrJS7hx9Es1XmL+Ig4HoMIrcAcIk1v5vaqh7dD5TM4n6jmOCbfnw7mpToqvgPtv9Je
guAntqDia8RmgfINKfmiOITE+XO8b9fwqkZ9ZRURouaNdXVvKs0SPe3t1EjlLhQVEpC7kxbv
nn+qUVCQxFX9n34u0nQGh3AW5+w0Zd3o8OnmZoyZI95qZrqjGQ8xYAMQDznqi+bfVYE9ZBA8
qAoYsC/CHI1JRcjAjNwLMheSBFQjfe1tWMslu4bBQm+e0ubbE6S/Uyt9PbmPfGfvXfuN94fr
ejE7vQ9oxVaGme5cI1W/QpL0CHk3HPLY5/OVHuneSxLPwiuYlxB4AigHrfrmEBkZXpdMvMOk
XEe4Fz4QyPvjQsRTS0RD13GGW15lyNYx+BHiQpOBsXpDWE46Mlwor4Af7zg5mRmTEdPFWZwb
tpEytBPX2NWLQF/97E9x6D7Wt8BtEvC6X2Z6c8w6dSx4eS3b4hSmeDb1ed/OVdkCM75z048A
T+7hZXgQ00/0atvy1mDlWXQZC33n2w/SVD9Q59NjBFcL+VPFCLLh0AYU8nDPmthLXNRdHJwZ
Rd1XG3pqvsw1SeJiz46ylONgZSp5cE0C57/xDuTEqvc5uVfXv6oC4emDcBQ6ON1+zJvCJ/6H
XoLf5/sP1oODejua8lSP7kq2MI23A+xQBgGWpMhZFc7c09RluRzH44PJQvBSM5hNn4iJe3yJ
O9Z6XG5mA/3i3IehKxHnQQVTgqM0z3q84m60CwOf5EuwRU3woE5RMU41n0m+jbLKuzqZ6nYD
DA3pU+dzOla4ng+Uav0XoojQ73rtoT6ymoL3h4UfiuxxALrLW7mpYLJMk5mhcZDhufRt6yfH
7FpYB9xrnt5GSJ2hj9FNxd+Bprwau8eiR87vmetTZoM3tKp6U9uijnuZBi0FXioPWvyaAdn5
HFJgHPbIRF03JQ6Z4nl23nlnrKB7knvgD5pqbP1ITjySjpOcTVBnW5IJwUuuhISaiCEAqER/
T4zxr+yBP8j9VwP/SdRdEND2dCkFfnu1kHE3f6xP+FJ2Y0svLkRPPGA+OQnK9Hi4p3pXobw4
J92Y6sTSKFfbiVRaLvgvn+I1ddOoIkSwRLMx/hLLSX47ln+9m/froC4vtNVOZ/WLFx50FgRq
MCs39GeqfeShRTh9IFpG2c/hqR3QcNdv0fOwH2N6BrJz0nbwNCu3W75GIvdU+4sK3t32fR27
V0M/iPb/2cyfyLiAynQsD6Oo3eRYBVmQyrBuGnzeuwa57nh/25c3cXYs83gW5eZQBi7Uz21e
49QMC5/kx37h+OG7BtD0r8Pk/9nz9tYgBavX5rkgZN9ZraGh7983b9QV6Wm6XXskrK4MnqPJ
vLli9xqdyjALuIRwqErfzPCF95mGPRKUGv3yqsrT6b9nuYJUlscJubc3Chn4Ihfib7t4eEB3
UyYzYL4s2YLpcWfPLj6JuSbJi3f6JdzhmxxOhRmtwBVCHkB1mSGkcZFcPVsyHv5OY9KCrEko
tUayOSlbbas36thpYMuhu2sOf/VnO+Zj04j3JVTXzqtkd2nA1SC08UhKn0rBTFA+jtB0byqY
+9ml6LocCTf/vtGm7IqK8MsIu54lOphM3/9/qM8OCLSQ9W3fhPUYde4tquB1IkVUV8p5cGkR
ajHFLb72lBgp54cpL9NlsYvuosfD9F8oO+5+KfrH1+9fFWD/+85DAeWJUlWJo1Ol3/Wpw1W9
E3S48S7rgWrblklRsrtmVkZmrbnEeIXS+nz5gtclN87EldxPZ0JUvpgQIkIfza74uJ6LSMIU
RX0tEF9d7HtByvwMTGjRq9Nk86E7kRj28+UVHzkr9BAZ+w7Uuf9KyfPw5L7JcZ4yaBmmPErx
BfAnBT9Xh2eSHYA/2XRKeegOIRJ+3grPLPeBLLqdkE7hygPwOMzOrMD5eqFlTyg7L/nEtmpX
/CySwRRimJiIU8oLN+iAUPJ85CXWWulQz8QKhScmwjnkYsGkzwYl6mIuaQdT/9TpmuP3bpuS
0vcDOPxJiE3f6+KhW92+T01a6JFfQdd0LklPtd/xWliwbKuUPlVW9cypZ842aqrzDpRwlequ
FdVZcFxN6eTtGZMRncDsZ3S0jvqCLVU/QROFv2RtNoxKKw+kq5pER95nqhttxC2HyH5D2fr3
TO790vBnVcij2tPjAceJZtV4zfwpMESVdAOdAVfsWl7dJo6c4Bqb7E2Pc1YCimY41XCwoY5z
TUSPx/uP676v1r9/k6fwCP8OFFnI1EpdC+vfmcsGH0Ng7e+dXVNry8+qVR3tdNRNYXFIzoQi
05mGbuaTYxXvi3if/mhzYd+6aTsuudtQ0Msejdfqd2MV78xHfjkOUWFBrA5PkdJ8Cry8pC3u
049XR+qnIezqMaaR532fvD/VJ05rbMXcb6trbUpjij4fhEeQXLjOZ3/tbfwgVMvZvjtluthk
2F370eaFh8f36vkf/MUyUMDBR/pElcCmgwZ8+jOYkPUn0tf3zgfwhwhdzFNiB7WrA4fRcpHT
XorOHtDk49iUpTOd5YFdJk8725SuZaZMu+IzZDNyJwOZ0GB0TeCh1M0mw53eqBHkDls6yxl4
rkU5re9A3Xd/H1Z3m3WNkz477bvudLE81zClRVPYX6PXeSqr1RWypmt9fxd6csSyZ8HDpF07
jgjbksTADX+5rD47G1Y2MZVVt/A4gj/GxTDpoUdvD5ACYLnSpcfQZqklCO5o81RKfl7lIC3X
rNhn0JSJkP5FrH/NaEw4HCm2Eb593KZskwttYRR5xKR1OTm0uwwRJ13HU6x/NFhSWq6Rvm7Q
eNxn56q6O4D8ZrOpdJY5x5LjNYw78Nk8V1tT59SphFBpgUDzsYGARH0w/NoAnEaEVWq64xzN
jYvykRdz05bCbPLDfWg13YnHOP9eLTpI2ILYdx6T55eOnlezFNRhxDybF+nuNNMo+A0sX5Cx
b1ZLtMpQPevoGGueqbrsCpvTiQ1Z2U2KgxHG9te8/z3u0w/g7nEbCU/3cbIoQfAqukUiAdDr
UruWuA3Z/ssKC7kGeHNDsWAgI0VZ6mkl3bURSE6fIucROC76S/ZX35f0Pv2RR9TjW+sqrYm1
wVVPfdOZZDnzSpYYXNGwnuc8qzDBurBS6sqZeOeROxF33hf9idNAp9Hzs6Ueq+Q3WYeJptC4
0ltz66Y7/RO0yo1/BmT2V7bQ34qNrFBvbCaNlZ6112kblxZcN7yIkaS7kwLS49r6X4YF5Tdm
yLUbPCcaipsGz6fduWqoWtPtI5eRI0Olhb0DqfaUPQ8O9I+QavTTqrZW6466iBFagVi4ZTBM
gyEdJpG9wn2XgyQxfaVZeNqrtWIKRkvxUeavHmka6mePZAQUa6Thk4AmdorQUeIjETA1viiH
aGQatNxwWbPSv3fmHkKZaxXf6WyGxD7kOzGH76KnL+XdqX4O9CqZt1HdUI7+Puc8dvHNJpQb
Y1xLq4QdfweqrxGomsQgFw0f3y6IsiSznrOR+GqB0gXovHjsSq3EsvkDWuUtKhJfJdA6KmCZ
aPhwaMS9AEOH+hUwPXiy7eXnDWNXdE0QaywOKsm2FP/Qfdd56+eJ7mhz0rR5Dk0lrqQjopDn
mY7o99tRX+T5aVqUIUqbJ3l+vb6ugZl8Mx2K3MTXgzjM/nEauoNjOHdg/3QAf/6rHexIt+Ui
ZURw88KyNaG/mta6ACRNLk4uLG9eKBDvLpJV20D7+Z2yYJsWB0YuRlvnKK5LvdlUpDW3hUWS
rdFQ2nmDiTTz3KEoudqqTgtvsud0N+2qAG2hZF40dqXrS59vHtBejTsga18JpM84IzsMU5Zd
I3rJrBHeqBg3sYCAfTNogakRz5FX25Hkgoko3hYD9/lvu+hYugSQNN7c6V4ltOEJ1NbmSyz1
Tk40eePy3Ms3fOrRFuCcEPcVH/IpSo8/dtdUoGo+qtsYwEse2QhkJBu2XtiQtNSeR8hJzANl
/BVRs3c4O2vw0HcgHJIz3PsOlLvfsduKEUIPR554DkAYVj4zoU6c12RTbLTJZQ7qlHGDx4+E
O0z7/OCjDZDVgvpKIabpvokQ0wmNgg5pJbJcwhY1HXG3yIMNldNo0gwuP3HMe6QZB6lCubjn
ohaJELWOjgYAK0cfFz34j6deWh1qLEitnisYzqnLL6lcTQhCZIrLNFovoAJ/tCuplpVrzXyk
IkQeWCqgcSetiMCIOebBZsZo/15TertIB1iyVgeFSkcGurhSDtb+/VDGvuSttzYJegNeC4+k
dLeF9k2+A/WVz+0eUgT/cjbeNwQ8Sm9zrbnU2EPfrhglFazs//8v+7flc02OkMe3/B5Hfj20
JIvdee1B7DM1CckoqsNbRVTdgUhfkiCphLwYeA7RL1C96TpU8Fv6PHTj9EOHwn8ov/fzY9+y
m6tRZrqEQilW3665quYrg0yVKeYoEdbQzAS629ftlfop81wIxEHG7i2dB16LMBn3xEjFpmyS
/uVSq0xJQuSR6Dt7VfurN+hfOVr3ypEy7NhQ01ObgsamBjXtdq7Z1yD4BxB5NiWnlK1a7zNn
A8cjL91nCjm0Injup6109JlduJwZ67Mq2R+blhhuGg6r1Pe4mlFUX4+BWLlX82SLmMQ4gCfW
FNSC8j2w+gslRfmnXpegzjzsnUlI1ce3DYqoGQjN6jymmzMMBl539q+Ll6l1wQPImOmpNq+N
NIyJW368G+IrNTAVhoKhnuDNoTuk4O/oohfYBi36ah+u/eBkn+mme9wG17LGWeKKtRvSJe1g
o40WJDxFMo7lVaeG6l3L2LX4rgE9XGa6e95t8BWL3p0CvG8cuxSxO3d6Sl08twlnSRn6UcbR
sKh7QLvCH/LctpToY5Ak8Stv6ir9zIkeJYl2wqR8FF5USrcDLEgNMwreva0Hvou3rNps3+D1
lxJYTEK+OLfmhYdzjg+um0qQsZAtxe3UhYx5zGN4HHu70igwV9fIJHJ14iEjNbR39Zqvgarb
7abBHndtWuq5C01TAUnTTBm5nrJAKc0oUoVdOXmR2c9/2BDtpBPySAVRs3ZE6h2owmvHnb77
fcbdeof5R92QtvzCCSAZa1sscOARSX/HcZREnffu/opNd5J86TyrpqiEwDfd8aKvbna7jKXn
HUzSzZN3bSQftmgG/BpQF64iJ+mtBPjl3WaavTtBJKrOa8YOgLsH7lxxWFFg0IOm8o5ONppV
kxRZuP29ADojCKw3xBE9mE5eNlT3uA3Z5Fr1+FHfJEgiEF9etREqD5xQwSjbDc6x69JQ7S9n
ZnybWVGfaXZZQafWWAGCtOE1uxcCZEnVzbGWByy2QCaQVec54E8y2JYB3igeU6sJOziPKnGP
xEyDQNazovHQqGMNM863Qr9C8KP0DA9LTQHtzsBWgemAYckVEf7voLqC9mVukWaXnR/gDt8O
NtCjPNOK4ERd6MA7eW81k7njVgRR4Oe+Pq89q2FLuVRKeQJtZhiFdiAQo2nn39t0XAPBmXmW
VWwvnMZ6m558gJmAIb/7+vi0vn8gZ+n06q+7WOvkroHeugKCl6sF8QWMvgCOBrL+EJQyUO3D
9+R8QH5s62aVJarwyED1L7ChwYI3WQ80KE2Ip2ysGlhq7fw5gQ8kfurM8S3beP/d/ArwZIH4
g16pBnCVIaeu5exetf4ybyARf1krpqbKuZW1MbJ92KmtVz0u64h4CPsxW3SRTEiHEWkXS/T8
IRrzJWkoXYhFDDU9Pld2X/7WnuS0PXMGB2lkkW9P/JIjRcRpBrT0q3ewSwbuYhYd4s8F6MXf
0GVvWzwdzsOr+i42NKqoCIpAIcJWwnkJSR0FlowfYCXV8wMBHJOKEawKpFj5fF8RulFQWnJW
i7WjLBweEEA03Gp/3NEv6twWeyZLY0o5tp8umercV10bbhnmOLiiaKxtm28MpNGF18a6PFg3
xqmoCht1dBAdIIM2EKgNTRdn0L/GBCKyFKzTqvuYcoXDwdHtk2v/JBTJ9UFBpRSnrztFyiFo
5rSEPjWMfM9O2XFQXdz2x6l5sQdJzjLrc3mWrRiLGIh/RzfsdH7aZi/o54HNS1PW/YEFKbWi
3b1eZ3lr6U+8b2OvTxWYlfaq7TpquSY4dV4j2QhbEI7dHXpRZfYaryGjxjhBN7VByD1xG+oP
3Cg8qIp49YrxpdENNzGvHKrFxUaMxcgd7+KhMpiubTkc8TT/pNid324+760F59SxVaGXL/T4
qdEv6Y5LuM1wvcUqOiNY2vOYct+Gjjq/KdsyUrFTiifG7EGf/i40cKoWwPykUQ5E/+3WBCBu
s4Dm1/lJ9a/5LmIe7EphXFxnLB0l3oGOfxbylilTk2PMdtdUAN7uYvja1XljnVc3jcIekbjk
z/+21P/+x7UcStRcHHSpYpq1uaSzZHX3Sz/IvKY+m7V6u73PqhP9ywzs+OM+aIoCtmDKls4k
Dp3g/selez8/Og8KkZMZmH2xKEWRwZmQe1ABWWy0u2dIOhK9V+AnzfMYSFzOxWP7E+xb8Pr4
/YmPZ4KQ32dUIowRlVb7Ty7t1e0vI8r7vli3W/2CisT5I348u+9nLdVG+lQd/Cu3HegYZ/E7
nd3YOcQV6OMbyraIS83YGwTeuGWL2SAP+oKF+zrXGa/1OzNHET93Dg8aJFwEss1beKZpNrXe
bpsKdscIub3wyO96+Bolb2ljCiYrSqShi7PD0sknxfrXM6ebkEqUMbxjFyJ189zdYgtbKQ/3
FbrSCcjinDYh+Wtpn4HMjMKVxRJRi/JfZwCYg4MjAQCkuiFLKCZ5HX11N0uA1o2eRu5+cRu9
Qyx8BzLnqcyprOns250dGzyisMVneLWAMQ10/KgeXt0vrTwGFfDYOhxSwSGv8E2VYCTcEam3
/W4OrmmuzG1XtmgGVlN9vjdwqOMUQXvmtdV2v+WZp9lLnWxuD/4Mg9qSdOEYNgKOq4AGquBK
l2NFaG3sbQpi/EuxtYDmEcAnZe8/x9LUb9k1OzlQUGJeLC3Xbv3ltvjLwt3LfLahU9O77Sl2
QovenyEmz/c/wGLwjjankc4h3WufR5jYz+MdoXkc9Xeglv0snRmTqAdTQY2rGMzueXG0vm8F
ikCRqJjqXRN/lVHLkNgf5lEi24NMXVl9brkm/hPRKbBhf4hH8TsQv+vUyMGRXzj8pTdKcUb7
g7yLaZ+5TtUIUfo5/IHqTilcm0UB2DF9HcdbtiY8QV6hic4jWboh2lr9QygAg87ggD0qIx/l
loELSst3OUVwQ548CSeSwpvWv5gWl9NUOIc3se7KgMNss0nyBeY9amxUOO+ZguZjdDC1MLff
lOgAtuogWg3aKL0DpeRcq/JoG+Rf9FSSGg2GwoM1Kx1sOYJzeLDsqQoKzipEBjg5GoV7Cern
Nauek6rg1VsQnwlyJeVks+3v2GEUdr30vmIlPNmRvimVsXcHA7y8SYncfPuP70DfqTu9nrjn
4t+8KjYWy5YEj5m+uHLyHxf8J1sEgkAitwaVedaD7U/0zxWsKWgGbIt0bxCbuK046IB9l/xz
uhO7vn2Vogeh3g6QtG3YYWxi4FHHP/sQUl1leXQ9wNMgLyxsvxiC5+uqSjGTaCmlfvv+GbFI
ou8/sWb+W5OPzV5u7r6TMkeJMH7VZeHNf07rqXWe9LjrYBSBGRb9f80oTNUNcieF7zApJpOn
BAImYKoGmFBPKpNV/9DtH1//Pz7/2of+QXE0hKNWoS/q61f+JlvUx41tm49MXnbuLVP1mSW4
zET/6gKciIx91LphRXEPlsfT4ta5QjaCueoAf5ryaM5rLG2aRZXgkK8PUadSUxYRGybKWeo4
YDCH2wkAqS9vi1JQtwiZQsf4qc7vOvszpy9s6uX7lhluVyyVcvj7COkHG1aS2yo2Q2Bj3tgK
NfbuaWkR39i2bEdHOy1nhpfp8d3TYpDfcO0jHe2qPBheWVpAW6A8J1mJZ9AV+6rbDP0kQpK0
70M3aKv0aYzBd6n6MdIX82wLGOc1NrSFJ7eYrb7MlxOz/uwCxmUNjPb+SRIwslF5atZzpIBh
xfeMmiORQt00cGLtRPAtZkRODfF0Mc1KLjPDkVxqLVt83xkgsJFcL/F9Ao8S3oHk6tAqa+LR
kDym7xMx6WyfloINvnegGlLz2otIi+/gxq6t9bx570AkL+etqwZyz5Ayq5OjxS0sTaViDqCV
f+kkLDxLsqVgaKS6YO2O2+DbgkfzNVmnO4GBjNSpWiCed3XFBNqyNGiVNzRyDXidzGps6Jj6
QpxaFh2AU9CIdlQKloc0c5lh6rEpWYpV5PATolY2eAaYl5XM4eEPMnHFHH4cdCr3QgWut+8X
BeQXQRG2W3ww2lT5yfvZlzaPjKbKh8uTM8k/XdvOZUUWV7m/ZfaiZkgE2Nku9YXsuXhFSxVo
DBwp0cHGse/K6Zxxnuhr51lsz2+sIvhFTtuVLIKlJK3ABaNmah2bLjIeqBv6FrwRIdx37/x7
77Gb/i0tZRanalQwkAUfq2tE3T51k+B3oLfp13955KAeIh/H+lL6/H9v6/9sZ0UQ7+iCT35f
0L0RfeKOtJTGLC5JaMF45LvHUSKsuyM6qvPEeb18WHBAEP0Z0+zi0ZzdiokbjtuYX4U+iDyA
nKewcAhG5/H8iaDZTMuYpvkVIIxo5FErqcroA8D///Bo/uMR/Ti318FRleW5BUhnfbcJ30tm
c1i6WJfLrSjj4+micvS6/2vG3naAWnMiPJiNhJ/ChCdpzAy7pz2OvHqTz2XSoRy+GKKQL78x
+of43d941f0LHAhexsKt6fWX+ljyjslpiVRjC/WkvvXzXWxd8wNAhaJwyIBmF6O7Ul93CQvC
wP/CG/Vf3zD0IBRuW9XdlFBjQJU4M3xiu0D6QjkypnDCvb+xI1M1EKduV6IYtITOD+cdd0lD
HqwIoguBiu1zLEJKG5izNa+WlUpolV7h7cgw+IWKHCvtZwhlRXsrAIfWOUB6+sKGa4oBAH75
unmKGc9eXeitWJc3mHriXXzbLytCd0pCYUJD0zutZ91WN6x/v5/5wIyzxSYftmkRTn0lVWzi
XSFQ1B8y0gf4+m830d+BGomzdFb9M6ej2L6+3WuEquEk8jRwdAGadwF9j762p869AzEeaPrE
imM6GQ7fP6By6jxnMrrcizv69Fp9rNMRZyM9A47Td6vE2DtUv2sJ+nQ/uYZ5wmt4zQIyIvBC
24Tfm06Gsvc308oREDKr03aqu5bBf6X5qpKfyi60Q2omh/YKAiPU5l4glPf7ZSdIf9FMuRGJ
OMxPwLlcmNL7YQIpUrVdVabpKoqJoDeir4+BC5wnKc3lLm5N+VNBMg8G3HLlKoM8clYld3Xb
J7nX/Tn1SYbJBsI2CclOsU/BUTXN3ikOWD8Mdixwg+tk/d/OX+ZyyvbwAkPPil95B/KWFN84
ep8lZ9GNHI02yf0Jor4yXHMbx6Z7JyaUS+vUHDm9Czr75T+e8P/6dJ7odgjwdAxnR6OcLVUc
eaYaiXP3l02JEPQJaTiM50Kt03HD8x9c8Tvzkf4gviMLvYiYR49USYq2JYRQ2QvnHb72MmaE
sJ2Nmn+eLnYamtNO3uR6ePJ3wf8HqCcGRdZK12by4kQGLWDe4Dz73Ihg9qNYSQ77oZP5YFsi
vfLX6YaNxERx0TCOSLXrSnTyXqX/ym1+KJbo3REbGkl/a/D5C178XniZPaKgQXbKmsWP6F20
ce3zk9XyIc/hSBRPUD3pthwblNdVVhsUGFE0R4tp4cb5Eqb7Xju5VQvUsy7MPdkj53dWoC6c
CCM6fQVPB9oHQebYogbXohHQclj6zh2yPRkXudFeoWhAyG3MjTqpkfpKqaVlM7KrhxG0idfp
4JAuWES4+isKePu8cf5hVkyDPxPhB+sk0X+Y6HWJR2fhetXN1IyMumE3dDfDjELrXkZe3Oli
f0f3kF6Jpv799H6uQ6Gv3QWLfMOCzrkxdaxn+vxkIuDLgd1R6xR8T0iQEZ9t5oj6eGTMWPDS
eocEtmAgYWi9j8YxIXGn3vldX8C7wzWfkGStqbdzhQl3z99oSKgw3W2T+7aBqcJo2K6r5ezX
ybb4pi9AXg6vHZzi3bC1DBE0/EX8D6b+f4v8uHTo/dE07UcFi9n1SFWSSsVzHIXjzdMJ3uQy
lpRf2yrXHh+6BsCdRSc9vwlZNE9P9maM3HFKe3/NnzydCy+xDf9hNfv5pLE+3vDpXIjQ6va1
NcPxev+dE/2nrEdZjcQbpbyqGgPpj2iDS8texM0LI3f2aP03nCuloX/pUxWhDLR3LtwM88Ow
H1zVVorP8RAvmL+bvRSY9dku6PTqc+9sChIWGjTmywUfKd2sAPq6KUUvRTwM/dMj1n+tlNdj
wT1wZHnjxnD8ONyyfBxVtH5DTlNGJoLax9zXpM2Lg23I6cmWEAFwDY2peFl3oOJK0gxi1AzU
KTP207j+/u/FUR3UOPhRC2MHr0L18fUPK1vNDzgLM/zpEKGnbcOjxr05o/ZKNs7epGz5khyj
TtH+g/tpibDhk83WzTLNanOn6+ST+85NR4Tcx7oSttI27vqM4BfAWC3uN2ZvrLojwK6zw+W0
9i1ZEcCR8aPA+Q/k/M58pCGtI/C1TqLbDs+4eal6sEp0RUBizi7mbkwgAGDuPccVcyJ8fByo
KZzTxxTRENlURfLu16JZv0/yf4A6I/C85KzNNHnfoom36SLFgFlOPiWPHL1HCgHjHS0URqRb
cNAYh84YzDwqIiTboDnqlQB4r9r/m39Sflvrf7R0GHRKACx5jlHasiGs4rnzuMZLV2HHTidF
kVRLPHrIrmfVMn9gY/xV8ljwin+xsswpAOWttG/HTbHug5v2faqth6BHRjbG99QUWYAHi3R0
NjRAYj8/bDbJVMqiWmnph6YzhRcjjg3iLkmi5JgXFj+4/D3mI+2pX/zc7S3bCMeno8b5RxFR
FgQQij8xUGZDQ6exFfGLZ/Y3k1Fvl4p2P1f608KF9+b8dEjgPof5AAUusEJOzut6VFSX2I+R
522D5AYBcCF5PakSudayiisGzbxEw4dSf8g7/6v0LUEBFC2df41D/jX8i+siYf+iXquE8crR
2+4UOZvQ4Hu31d9q1YZiaHWEGV0xCgCHmWQ7hzMWt8F9hMMPDwdOAQnHP9b2+ktHL0b3nf/L
O/39jC1Tu/gpXUh07MioTelfoE8uzQZtvRxvftupABhxr0b/qdTgWF1ShA7ydJZDEypn+dLb
/nP6ZOv8mSWuaxRhdfEBbDJVxzQcLec8eRMywXlcsyPvvg2FcX8YXOMNXwjK63NNyNIaHEc+
6CCna/lBS4/55tfSFmZoBzbnJp73law4vH4+77GUO4BwlI5CIpIDG5qxsxF3Ze7801WBQB9p
DQhIzMjJqGDNJrhbcygs6zLvxTI4ePOCNUekcAlbQBEJ3JSMzjZk/ZRzGP0nE32aw8KtA80W
mfaNi8XQClbrsDXQHap15hZxx+1s3qOsqs6p/T8G5Yaxde14uzd19ARGo0fq9uj5v/4g47Tg
BJv0Uygv7RQ6tjA0tAaGFqme2CxX+Q059V5jaLANHtHqzVtMw0BEzBG+VXGIIWJyKMqVEhe3
cUHmf2D4TukNX8t6YB3c6JIhi0IN2QLhEkHJaRe17T5pTxH93uRzWXDPSg9V/QLlW7BjzjMd
t34Y3AE5VH1wW1FK2OD+3sIlD1VMs0N5KSl9s5941/DNwyvUFOgcrqWZv7iBvTgy4IZ0HX/l
4PT6wIsPrv6d+chTjJ4QUq+lbnIhATodFmzny0GuJJtJv+b2X7vSNz4jucEAMEeXWb84b6zj
hc41OjXumzz/+xSfPsV9MYDwJl4L8ZoDhKxZcUhXQo9TblTigam5+sJwMFAYna4Cjdpv3gYg
vX+V+cibDfr5zh6l/5c6035fJbfGeuUuTVyAhFhpHy3L+fdM13425tkl/OvsuadEixixB9R+
H1n9KKMmrIX3K94rcwrPwfl+RZiv80v60O46JRImpSoJDgzafGSP8o+/LwigrA/aO0j3sko/
0zzovvu6Xz3RYLdgdmAZvXtSauytplWBYbKk6FF5pg4cgxrvCO3T5Iiye0z/Pct1n0qAcr+c
2WRY/AlBVSkpJSRi/B1ofN7m1TvQT4cgPRtHFWj2kC76SracaSVtlumIHN33B8PtAx0+NYbb
fL2lTHghXKqNvtLh4EsbGowxfH3g1Zw3NKallO/UtOs1xLazKufJ4zt7NPv/1g5/1V+Wp2re
9gal27gtQk7bkncxPH1aNJ9v3tOv943YfE6vpjpMn1SR1RZ1+tz+D+6UCHmgmzczq9YzwgTz
oGklt8Giq/SgbFTCQcVeZ/mpXWtNxYTHbMskgmphroFLel0dGkNQt6j+jP2BkN+Zj81fMVYq
grD1EnxkkZnoS4htJ/6okzJBF+1UrAuaTB/QvnC+kLeI6gKsssE7v8v+9Cluq/XOXJkZboX1
uREfZrgZ0ML1q4NXcNSEFsbrPEKbr3q8IV0vg/DjZ557df3ffjQHH7Td3oBNf+cyYRZBJw+x
N84UDKCe7wylbxQVULkT/Fdb8amtQbzwSegYxDzJoRDJdGvBmakwwKbnv7z892uCQc3tj9qj
0nIigqOejaDcs/h6k59ZRCmHFtPKyLTCEzwf7JpDnw1kHmWYyJN9OdW6TRrb9VjfSGArdxcQ
hiGXtSLj0nv9Uumr+RvLQ1R1p7R3oM9ikqQb7zXU7f0O/pv/yPP5oSTijZ1rk1HhdsyVHbwU
jZOHgC5dOL51vG95xKMU87PGZPiXhyF/MsenOSwSMHhqf68av8B8NmFkM4NqGLX0yw/Enav6
zF9zoPnaiuT/h7zvAGvyXPuP4hahylJkWFFQURDZK0gVscoQGUGmBQUBCbLCTlBqWUK0FJEZ
hUogERARQgghoECQKcawAoS9Q5hJgBD+b/t9p0XO6Tnt+c53/Wu/97qU54Fn3ff7vM+4x+9u
C2Ev5BdguljaQ1THmaoz4Rvo/NMfze0m7UdVX+tmOnG/TNstMk4dsXxDeg4hHSzfKcF/Kyh1
/vsBMi4uYHalMkNSAMDosrNevvYcLnZItHsDof+dVZrtfN1NI15SeWEUtKB3yTu/9wh3Anxq
WdKMpXx6g83MltMTw9m1AbJazRaUXj+G7+V30YuE3gXFQf0BSYFixIWuNNv3gLVG6eIeGUUc
xyNIZQ30xW7wP+4X9DuP2V8iIRKky3POeZ1MGsWmN9Gjk4F4ywPp6D1r47ftCrX9COjTL2T9
aM3kCbQZO9Zubgn/jf4+y19v9fQnVM9wDN8+4NGPdwephaxKnWyZ2URf1nQN9vrhMmd1Zfky
bEJNN55VOA3YQzVuJPLPvmb/Z8Upm5Dxk/lEvlwrdCIcdW4BfTD/piHiKjI2Q1KZpfvjhmjD
O9Kp4GqHIdeoAFkdmMJYuwx3Mtp05q5I2QF6jK9GK4A0ak8kOnY0PwMudXkb+fq3PJnizcOb
5C76kGa4EYd+60b5hemL7IDnml9XkYE5TCCbFE6xyPV4rrUW5PxtR76I0PPA8bmnyaUd8RTQ
sn23+8u/tf6X+ClCb6sn329ofveOMUcchdI7rw+bzujXLVjmuw+7+lGU6VX0pZ4Kv1ATyhpo
tQ/Vt4HoP/8hWtW/qNA9Q2/q9pPMw8NN6cYilhNNKiNDjYZ4VUvmvVrNHeSiuHfknXkdOGFz
bVjTu6glDPCge5KT2frMp384Vi2IT1oBplBLHh2ET7wm3x3f0xmHDSQCMRUf0dk9G+3zHvRc
UsltCzo8EH/kPC/y/v0k4O7WN7G/HRG7RWYsLMeg4pD35Usz5UFaaumPABgtbbYbT0V0YsMr
+Fv29x6sIWsgmzISz4qVB64AkNhRK9pm28iZ/qjtSfaTj2hD7LwuMHn7PiBulsDfWv5L/BRh
t5VEZVjDEluS6U9+WFmGI1Y2zbZeYMKvscNQyfRrliHLcMGVTdf7NlD755/h/0FBCGibXpjp
SXNki55QHkUyE+oG+elOqEU6pjhvWvegnP82gDXsUGRQB7jVPYSuZ9SmAZ3pvtpn9XJity0l
uXue5wCRMuTcoYgtIqmthmBGxc2A75KkT9R1dIpNLMsHccyk3YfPAnCG//j5fTr7zcTldntG
g0lLEX0I16zqwEKlAugHROExRj1vCj9vyz6jy9A2BS5QJ/n/cTef6W/PmrzuWOwdhnh2Z+pY
qY/sqSdGAzeVaSqoP/joUKAdH92ayIMQRkY7v3Emz+g7Pd1A5p9/Piv7v2rIrvimxITfDCyS
ngxdoE4YQdIT90qXo0JFFeu2eYpHyqbJkaAxuTF+4idhKIeerrFktkvyw4uH/nBcRNCmc2HX
Xt+iaLb1HCg09YpZdkhIVp7kaMCmAMBCc9bdgNAT1OPtGvZFi4AXYNaV9yrcHJSDgnMrBFEi
8GE9ZwVlR3o/OgxDHvgZBamJkiDEu8GIQyeSMnnnr40Q7HDKc6tIFFRvvFQVsUXMZX3Fdenf
vYKb2toht4fTBMVIDeoBmbBlCflZ7iHfdNFZbGF99gABkiADd+1GdzyQ2AVnnNm5sK6Lzz95
aA1kfVvPaA5hOd2zerxMhdZLDvYy454OKjh/skDwfvnlKuZcXlV0AK510AgBErXYSPH/sTP3
xR4XpeO1IxQjolHgXIkDKhgeWmtiL+0TtfXVXBa8PAOioQtn+Nr7T50iqVqCr2EHwuLnmRHU
9Vzb9D4o/MOgXZ/ePpWv0W/izt2a3F8kRcr8pgeNo21V97v7UWZ3mp2RGxaHZo2gkdJ6r22B
w7Oizvom1qV/L1JangkO77B9N8f1Pn24jHezl66P3Ms9HexqWG562ScMyob2pnQvJzJdX9sA
0YdT+9b18NknNx9cdK9dgF9Wl+ztWVXEjkN045csKNxDgYLnQunn33PeogOWLjhEInCtrcmA
HKo1fAPF/9eEJMdN8wykBAGTBrjH9b6W1Wc5hkNbs+dCAlrxZn2L3hO3PfehCt8US2+wZxCQ
DuyvzXrt3wR2Lr/phldz0UXsopot6Z+XPKkMHZhveEtTGx30YXiIQsP43a5ZrnYdEpvewOi/
ZX/vwm3ZYveAzneuj4WiDy8FD0/T9S8II/YLwsflkWM6jz0b0kk94iVY3956DCDYvvG31v8S
P3cgqQ4tmT56FVjG3Is8KdLKZSm9YzJi58QrtOP8lmdxcv2HbHI2UvrPUP7Og7HwG9oUNvTR
zP1wS+aGSESftrSZUNYZRLyNhAKO93vrtx9tNW9y9lu9olwhQLmrV7lVyj9unlDEMDXhKpw9
RUtcA6ll7FsxeA8XfCVo/GlDG3KbjNJve5/IekJMRPVXU0Ju2hQJLxequN5sQdDJ5bvFxtkR
Vqh3SbtOWvrIpyxokHplcDHDk0naIRliXnf2fQFE5TplYLUUN5BXBoBDoEM8HqmaPnalsMuv
Z9j/Htng8YA82FELX6XXyughLwAy3GyqNcfVaJW7uUlTpm6h5Vj5YTyd5PkcTVs5aGY6tB23
fvB8poc/OpAJLqFJxzDJ7Ov7eX5k0n7u3MyboZbHrFwAkS3Ij3flxm/dAH/3fIfYjXOmd5lP
XhhCRejLBVvYLIANWaphFbZJL4Br6K0hw6Etn1oJrB/j55jea4ixlxI7zDXEjsi3onltb5H1
O7Lefxi9zVO2WcJqwwuCX6yBWPc+AdL5ic4//ZLtOemxWqEmXSw9nFTlrPPbsBuO57p85MJm
r2Kg5qIyFylOZSGBI6QLxL5G07y9IiEzu33/8VsVnm+bFKocFBQoWgkleDoW0cfOYFCDm67b
g+dWtYFPSDGA2Tdm5jqlaJfFOfQwfH0jAAKZwSn4Tfxc/3S63sFx3YZENIcXhmURwl5uQH79
tdbvnsBydoT0+UAljxFP6C7iEiAD69h57UMzcvsjuAR13n9SeQ3kcZM8tKXg16b/Aqm9tpij
InZDkOhCo4AncVIFPqoPjqNe74h4P8KOwAcSkPShGT93Xu2IBWKHaPNGev/s52tzV9tLYxm6
U5e9LQLNXh920eYMyKnLvF7NZd91lvgOYhCafufxLcwJZGOvTkA0czAaI6s7E9LxbyggcwVK
A3kCC/0XHL0euwXnAbK2c7BqIMirkHa2yY1RH/W3uxfhtbVoV25GbpLhjP6xs+s5uQ2sc5iw
lDyhjZsyn624W1NXyZBCR2KMMwBXLP3K9SXXpX+f4etWo0UysR+q8EUHc26/DRW+2ngRCPIx
ejnFJcNAw7VXO4BTpMeqvXX0yrqWP/9kXNhFJV3Nd4rCUywg6lYHDv5WW4rUd2/Pwtm6mcDY
Gn6HNdDJ1tMKYXErj7iHbCs3EvynP4lcTvcoHymJfG3k+K3yXSeiVnl9KWQBwx4MuCtz9w97
LoC2XvGvL6ZZ9vXw6HLIAjOmZQRgU/Nq3PNnm5qsEfc2Z157I6p+p80nfFJaeJt5OjjFGjf0
AK5tLu38jyF6/rvKVshkjzKHkdQSF2r7pr7VoyModXDey9eqQCEF2pX5YqyhYJ8375q6Uy4m
xj0qRVbbUtW81y3800BT63oXEWnfBoS/rhYQdWIvOSBzuhkLEAbwWakH3x5YNv1eQbSTQXtT
1URgBS0BMBM79l1fV/fzTwYK6mnwUobosWorQDCDRRrqG3sR+FkI8vyDAr647rNvmXM9WINe
+rkkwPtk94ON9P7fclYAYTLwr1n4qkurwQESIXQhRNfOcx/ymZk+mi9zmHMv4pyQK6ayiGNH
P72NkN/6tVslf8Ra1OGltj/1fsNgSjdyHVIyw6Yr635L1LGRz7/khZlto3JvBhUFZrW52Nu9
eNrYKyyyb3NVGWJwGZJgIkQD5up7NzwrAGq5pH8o/Jd6f4HE9qh5vGvrksEAQ5LA6tKKQzi7
u3PDX+THaKqaN7ZNVy8qTBlhE6YoOdfJM0NiFzZS/Gc/XVxl20zIx98sCXsHuHOXKKgqQbyE
G90P9AwyyBWAOUiP+3D+ZQ1Lg64Tma4X8RYGZrQaTfVsuZ8Ns2X+uIcZaKvNYv2b1BTItkXp
q7UXiK5T41WogaovtYxuBOsdtXVqR7DBuVhb9twklnP2SeV6ZvJJm9x0Uhs129OeMKeErPa4
Rr+ZCMTvofP9ppp8fe1P0uaCtvwFgsl7kgFJne3hml66ISpZunLr4zlt1/eaX/VLShICup6o
riZKiQ1vLw3/pOpnnhGUHJWiZ86l14qHBKmZFEGI0T6A0J+W+Zo1kuVLLnipnMVrpVT5X99A
5p9fBfOfVCludfOvAIxkbr49OU0/3u7rGbCsE+zKAS0KIPEZyUOspozV1eP4Ym3Aj+6rAs71
1KfrmcUnLfDMH5Lp21L9AmvWRRBvlrUHNw44d3Of/huLLrYNEzJvWsyDVVZxDM22Zs7d9HqP
N+pbBVc0fHBnz95C1QveXN/5Z5+WutzUBJY+Ue4MgEVcWRxnv1S8eAKd2QMXVE39Duzl5Epe
DdmMOKRQuZHQfxZA47C0JemM5PgK7iLnq8oT7OdklCs/jxgqmLKbt7EZ0Cb7ntvlvSWGOG1E
1DDf92O5I4Vl8JwD9O1ulYAZOlKrdqmnk4VG/2T+xqhfA6Wa7gzLHNPb3rk9O/zv2lr/i+ze
EhJt8JsVM961UFHlOkQyfWdYnjPvSkjdv3FNy48vKeWJbWJJQbwSp5nnmAvWAaOcQ6NlCjch
j+oz+oshCQfDRrvQHWkSu3gMn51z6wcCUlqa8HU/Od9QvSxDJT5vZ9lYHQHEZluRdvbkYh89
VwPVkJk9Zz+p8a8zws/bUgp2p+ThpJVfvnTmkXKAyCg5PhGGd+uTtju3d5RJrHDUfpT6TeX5
v+7gT1hCB516jFlPPiCzBvq45+2M/4wF+4JtxnY1m2K9ktt5X6GW2yR4Zzc4FAFk/OlvZUa6
t88oUIEga9UppK9wr07aZWsHncDqnZFjmF0E4ivm20/1XuaYB6+aqZpnUt21Db3isg4zhHms
J1ui/jhOJUiE2VbRDrcp8Wcm0zU+rnAOFC1tyms1qeAWQOt1PVeSwbx09BropeiWT2bAMT6M
qrKpbqjRLCyaE6c0vwZaAH+hSIDSF5rplDNOIcsKkimry4f168I/qfavMz82Fy1yQtvHfuDW
kivRPHyq3g+iuHqLQB3sjI/eqj4N6Mm1c/uLf93QZ1RC8PQIUspn6ebAyMkgr9vGcDoJ3Rtu
4Wp4sCKyqWdZz7PLJk560nt0bvNM+Aaq/vQS4P+wZbP8St5NvTWQfMjVAltEv+Fqeg7i5UGT
aHa5gh3uefwa6EtiAYTZ9w1gwvLNJ6za/J1W4TfBkPR0GgLnZeLWZcx0LRHB6IXvftufDUGX
ehf7AibktdERAaRW60zEMe1DG/j8r7K7zk3K+74doZmiWcRUNCDxta5H1e92HQbLZlgFagpJ
Zqtt62XyoC8F/1qW+ZKCyMe6qpX5Mk4s5hjtMgRH63xLAGU3PxQjAtr9S9pcnOeEXxjWHzBf
ydjIwj/9pew/6hW+ia+s6RvAvLvnxBoIykvoLQsDoLgqFG6SBjd9LDtyg2MnPCAgjUiEpgZo
h4keLQVwoAI/YZhZkrWE19lRocNMaG8yzeYm3RWXac79wi5AEY8SDtz91vMcCWHsuUeKjXB8
86ZY7wdJ7ifV/3Vmq4R/NGEsjW4gXexpr4ai04H5ixgukP6Qhp8pEMN56XdqSVb01u55sv3H
f93YZ1RCAF3TAH7Sb7JAZtBbYawsQ1Kcz6ave454BYtpaW2V5Nlnub9GUEcK+u6xz24g60+/
+LpNuiLdM67DwHbmy6ea0g3K0KTHKb4+LuAefwC6ZltNUfQ70s4859Y+ilVvMcyZNIUFgMVR
MEy2PrPyj9swbxbxD6pZIMt2JQI2VvKlKoQKckgiYGMVyD7X3SL4zay5KXMu3dGYSBub6kUO
VLlUrmfn5kdaDdcWFDz9JgBVnsv44hqozeenmCKpPyyPjMrbSeTnMpVfqi00tmD1hF7wUc+u
r/s70mauEGxFdPOFZ4aIRE+GArLXUu8HMc3KBvDjPpRg4Qps4VTej61MJ5vwgDu/o7XPpsim
ds59j1aWwHARbTgFfBO8mtInfPPD92ugZ77EV3nsJZhogeEqCg5M7pWzG4j6H0xuCZjVAI2j
qXw/NX+csyRcbdRFSDQQqTZNGHQJiZjuJWQ6LFkVRTi+HzLT+0F8waW/e4mfoBoidlgfK9IK
qWs3Wtkn+HTdaD7FdZKKoZqbyh9Ev8EAx/6BbQGPEcD5dHOYZXK04bvha+jO/EPiYqpE8fYG
/9AT4NjDUdynP5q8TLbuLO8aHOofsiG5ENHoQCAMk4i5bv7QedaT2SCn66Ls/28XychV65PB
6kcIFaNeP7iLG7QsL2IQ3+7oeV+/6m89aKLSUmvm0JMvM0oVf2DaW3nq/Dq2gEBXETZaOgIe
aquO6oWngX2lwJU8tBXrE+cYWV+w/cRiiVSEFGvrE2744npuftLCb2SE9aj57Mx5dCkg2s6T
uZTFyzN2fLOVdiez/ekdnKv1asFZyhi7cCwc9kcb/o3+/hy/3lQ9TYPHFvunOqqjhyhMWo6w
8oe2YQtf6lt353c+6QACP/iIi+nQ1r8TWewpQRsEqHQTYOMpGExNXVQUUxnMz3kqLLIRzeZT
rPiNcGb7343bOkeHvvGOGbn71JqED8hnUs9AKcZcrFW+yw2qag/eEqJoaSzcWKNqSrbcO8CQ
+pGP5vq8Xdd7uO/GGujHMr0FIBAoZXtGjE75LsI0VFIWPnJFRcGvaTSG/u6O9Bl4pA3lxEoy
aA56YsY8Tgc3rat9aQDW2dxl03wz6uNptwc0S7tUv3aVmnr3Qp+C7cV+LV4SpoHbS9x0rwZ9
aFWR1Pbqm9UTx2pBjwIA6AdswApWxl2ercI1AV4OmZhpuyfxixAAzFxZGay5LX06126hu+BN
VtwPNsjkrNvjwNHhZJ0KGiOnaxkUOArBl7wOBADeTyynzzc5JsXjBjveq+SsPHlK65641rxK
/36wOTRM4BHanK1UNe+VI62rhV5JjSM8ZiM4YFQcd/charxXcIQ76thAwD4oYHId0W8pHXRL
OtGbntOcO0dk1tLSAZcY1vz4Sv11cWVi2feu1P5WPB6Z78pKS/d5ws7NqKRmWU64IoZUFVwV
QsRwW3hXwpalzWN5Npoo/DR057bEYCDu2U/K3aVUAKO6cHGJG76Eexv/oxbqnafJN5NMQBlY
9KKVvXo3T6LMX5gKtn1ZWuNL4h7m2esh7Pjm8i/jeVS9Honj9HYC4C2jnAnmjemwH9i99BWq
OiUo6O+dELn8+C7a/YB3RNyj1GSnoR6SiqVjhHCrD6biQgyaBG2lNfQ6l0JLtd/Rz+ggaGJs
1I5SV8SdWx2dxePtPjkf78wOpMUcyyzLmQGYXyCifitjlRAakFQPWICZGikETc7dOcEklPo9
WcEDsPlJdostCXcTpqftpZet1ZfVL8UHqhobSm/Xvq+hZZDafjyzvLGHnE11aTTiTOafdMT7
uCEhVZm5i5n6QaGnO0kfR79LvRxZmD5Ob6y4fzcr2LVyJuzgh44FmxmutPmbGW3WUt9U5T/9
hI+j8h5bli1927nfTKi/q/PxNBWMdp9/lQme03fi3nWxaR5q/5Y9VeOwR2urqGs5jDMZIJ9Z
gDO6dzZCXMqFO1RayBi058Jn5CLPkahJouDHbo4AFuYnlmm/dr8jlfoVPbKu5QvMaj4rDrKK
jZX+Ya/rs/SwVxoUr5EcWnEIBQh48Fr0U7++45A8C9gIyqOl4OVpV17rR/1b3JSeBah5oJ5j
3qvXwXCyaDf8bMj+X7v5XaldeyeKQ1qDens/BiyZSD0Ctlqngv7N8xyE13uYKK14XvyCJHgx
ZdNfy711TzzBMPNWcBwppZooXf7wSsDlXEaLIz8x3bUv9L0jZyPj1knj7pe5unflkz7yRS5P
E3KHJ7QeZz0quDnicrMXs8hNZaukTeTb431yU7D5mGz3lGwX4NGHhwMNRoVZcesC0NM9Mv27
QdjeJKmwNOXlxRnwLUWgu226q7rcJY7HwqTirF34jUMg0HpJsNDKI+KjIlWpq4GWGPeDhgb1
jcSSWZdpg6ndlj35TrIybzBuTN3Mwzq+Q1Fbzy6s4KBsnVCNouAeVVqBdWM2xj1+1sJE1jDw
yeL1A3y2rQuxjic+vBxbPigMhEokanR8DP1Otyws5vCm3L17h6LCfx4sMN5dI5Oeq5kswZJ3
XJMZbTEDpuqpEFobYsD6UEYf8Od/+vxnMfhAMelXjzPr0PtG29LFEYwHh87Dv2OXS4Y82L/K
MxU6X4B7354M+MoWhq8f067rk46xfb5Hi4pCQnHOg13MBQBGinv6GkKmnSj9g8Ledvq74tPH
Vg56A/ajpesrggQrnRebFDW4N+gSb5hNb19ymsoX4nAOhSFiF2s+4LZZqZ10sma4UOtPdeGF
zcd+oMUmdOn4Q5R1R/T1grW9BRGzgpES5xrpK6N3oLcfGHvta9PtcTYnpdqnyFY3Ugwg7hi3
aJT0ra3fAsPle6v5ZFTxngTWzcJ+QJboYIJPdIdeZ6yqHSeiEqSemxsGZlMrZvWkfdyiGUpS
wuTrVtL7g6t9DxJ9vAZmcJdbA8OeU3tPQaA1WvEIL2Y+Hf2+HKXsIqsbNHdPc1JnfN6z4AYk
Ib3R9YtTEDv2kzftXv2t0+ZOmONIn03vPOND8W+7rgkPjYe+gXJjcgF8bvOGuAvRjElKotjh
sL7LJlv9n9K1TFzAjxqlqqvaX09gYhTcl/eAE5uKTbH21otGXUQ9reTi6Xstpedq4w94012d
mfki0426AV8TwVv9bZKzp3Wbe0aok5awfKr3vOp5UzcgvILSGcluEGh7U8Njhi2G0TWeGXPY
HXBKfW2+dzgZdeULvWRoXvmBflmYA6VfNnnVLGCbqqUNIdFZ5r1fWsijAcbYrIjJ+erlx4OV
KLnM8/e2zu7GFGgenFilRxNGTbo0AnSepAgkukRl65q0e9XQWsE1dwRlPmrWjJDMCZZTGTc0
HhlYmgY9CGtIckL5pPpT9k6fVU9R1A7tHhPLJUU0WnEJlspCe1Nf2Deie7K57UJMvl6OfZtg
im5qgkvbGqgQh2OhhKRiDzyx6LvZBC4WK8xMOY5CWWKqnNPyF/n7FJXbb3v2KF8hFOPi6hHm
yzV+FJ9Ve0LLcy/D2huwWU5WFb5L1iUqanon+JMpB3xtWyYSfTxG0dHCLbz8dHEAiUPlm5bh
rXOe4rqCbmMlPGeTWnRv8UXNv9bNr+Rj7szCFAbs3uS90rmVb4GY0b0wU4+oaJPh1TVuO3to
A5P+gHbZYlUDB6V2dI/emfdjejY891wV2z2Ay/aXND/Tq3AKKXipIRMpwHgXc3wGm5/iXM6Z
wADLJ4hQhi8dtkIpnklTYKvDtqw2PH1fkAa2OMVNOmOngnrWzfEPawin2Y+a/xCrJ9cYIIge
86eJhNX/ePBgN8snxHloKarTlzaiPEAiRm894mNbwUIKaOI7aPMhk6XLJnd/nEi+diCZTWgi
WI2KLypZcJSARQPjpH2ezQThjTKe2z0cYC846IwvwlYLvv6oEDatE4HEYtQP/9BIXvRh0tpo
WoCR5ZHtNfZX8aJIuYMe2A6aFmnhilWShYlToH4jQhSWMdo3MoG1p/gRCeP8WOr1GwPBQAxC
o56CqhkvWmYup2s8Y1ZI6rSt4Jc819CjrGLkkr6x5IaN5795/ida/uMkv75D1HsnLfwCxuzr
66cD/reoOMcZ/R1a0kMcCf2Bx9KIx2Nd/oARGHwKwS869cmsOU7Lq9WLqI2XuslacmkneJHe
D3ej+u+90dxMGs8wDjT1JcG7toryaof9eGcvfrG+6ibhsnhfXbQPo3KPuQlFdZdbry1NihX3
rCNzyICm0m4YgVBujyo2cDi++grrPZQ8Jbxvd/BY7CqWk7SwIjgbtPWHcBAoNo07n4T2SXp7
2TfTHJlKUldV917g107HZFab7xVTVjSfoOH6Dd0RrnbVQYdzw5+F0cvVL6yBurvi53pTpl2K
8ibaJ941NTfgVXuIPmHXUFcPa58/D4v6+Qm/5cnAl6pDi6JxavmROR7i+f51xbERd+McLhgs
81xi/c5TLbhj4Zc8n394m76HetfLjPA2TVKA2uWE9XPvqlVNLRKSyis7gSmTG4UItzRvvzYQ
adLrFWiaDQTEm9474m7joqts300UPNyWJToexVS1hDaZw1KcdHwtWoWrg5/GUYSEupxfV+ra
Pu69UfoIEE7s9Q5YAwkWi5fvxMTa5CfB8Av5ubEiAZimLkCOvK0UuSs6Y3ai+ruv7L4YlG0e
ZO9eUJC/bZeS7xbcgxR8n28UrHBqwrWK4DRl+H2ZfHR22NcMIckBpxvaHaDNz7Qy5wex02Fk
zBzlzSlouT3hOcRKavxjoQILe/UdUqRRyx0pcQ2nO46nDU3G5KLi0INviqtogd5vTGRnETbc
ljtvnTxsU8FPovEeJtX5C9eyQxPtMDJVOFM2tdGwZUsGrefIUmPbrNu7lq4V368wpcwxrXiC
C2awc0HwfBS7qtoL/Dht9PaU1jzjDl3ozjVcrwcnFutMx++drMFgMocdalQauX0GxBCvSRoE
8o62gjrf8kHV6MRIr4koTBWm2Fkw4oGzM7BoaX6yjSImL893ohkmYNwdmhbyQ09RMNXXADaZ
HUKxVDWMl5U97ORM3rcbM57QYoI4LS7Su2fW9mosje3lFAyWegZzkm97eYthRHVsumHLlJJY
8sh2IknU+OwcWz9zQaDN4VpZQYuz6pPqlZyzFatEw2dj4p7SypEuekGgoU+Lfua5bY8tAq3b
3RbHMOD3Smug8UhIRIsev+saKBZDXk18wn/37AYC/4DMMIEjUhXX2SgnomLyxe3b6erStu2r
yuO2KYkTDGfK2P52H/mZicyYCeSDIjtDd1cy7d3wFkJWJlO1OPQxsz9Oqjkvfel0VZ6pAdxd
rqGi9JpUMzYHob+9R1J4KSslq1Xj7pt6t0WXdFOzZDZRBjRUWCbruwniZeINiSwhIs7hUx17
Ci9qakvu1cBBvIy9C27RFlcFd8uSCF8IfNVyjrECWclCdm2V1s90wE73hHud8tPsTpibdvbr
gkfe7sZOD1Wqq/ipfkQPpzUMmi9oX8jlXQNFdk/O3XeUs2Xqd6pr3DVhpHtd5GDHU/wKLi4L
jlFpC3rbW/M5jvJMenlQCGwrxUd6JOCNo4f1GugH4VYKvQX1Hcnk1RpIpG7bV78yNR9aQu9S
vL5yG1XN5Cv0c5i/2k4kuvKO3tv5Wz6Fv9Td/GS5w6ndUImgqOWis5sg25SDhBAPLPnqIUCF
UJQG5LSmUr9BbKK5BfXZso5RcLuiXb5ML2bTl/+G2ff2u/OTsePNJoFF7s6kCJyi/cqu3ALO
ofzmaM2M7RLsn9wWaSapPRURZxoR+3cjfxniTwkRwTZeS0Q1VGwItqQrBEYWks4DohWhJLSA
YTZetv9m8ypXUluW3uEyBMRVOFL5a11J3+BZ6cg0tari3FmhMAajIBqOyS1GXPs41W+LtzAM
inEnWCpZkANnDQtAM02jHxEJkglQfOMgNBnjgCZFuF6orWtJGW2LmWq1LGW55CAzdhTVQotD
XMWE5Iz6FHfPz8+fyLxVjIVeGi90oiJU97e5Y7CFU924+T6RpJoKJW+Z+BCKPGL2st+wR0qb
hQHJgNCVcrIrnrcHazUelUktZermZgMB+1oeu9zQun5qMlORVTDgSJnSqxkSvQoC0UZH+8cD
NbUyshK8DgoJNAUwe/EQ91O0TAAoFxN2MSo6mbUpXl2tu9I9rcF70MdbT4HBoXjR03QFxada
WAqp7i6pwrDVB40BAKlT0xBwjk6Lm6c9InQ6Ts4F0N5NP3vhEfT4zmlvT27iJNs95haaPICU
IMeHmklpzvIdAhsHKXdIZE/phOqc1LG/HOKusdBMLKB6ERva5V5TnRobA7KkkmcNlGhvGCKW
vaEApPTWO4taQzJne1ZMrUaUvxXf80KSkmVboO09zoENxAbnH1VStX8XI1NzQHSQ6G8U+uoJ
lhScqXMI/dRa7qKUM3NK4PTNGWnHlnyVPatCASbZZRXKByHF5xuNgh+NteViohddMCcrFUJB
gUma3Z74htFTqZTo/WIDbYXOuz+Iq3AItXBjM5cmb6HhGVmSwZNFp+4IiQY280YvPiEhmAAc
RVW78fbmlpZU5V4Xl1BfZXDOEVOZ0Cz3ctqs67z2o4RHaIbktp4DNKRZ0d7+VhdM9qnBruTo
KCLMDXM8edbcWASI1yi97asVDdc3zdJ3fG/1T0GBALN7+AzeZB9+EHoZzt8OuRWN9yn4Hu8T
Yhg8mYwJu/YQ9nJTn12PT9Bb+G012QsJBW6cjoNFglKkKO2YWMesfvs5ioGvlPbjEygRq9Fy
WHJKiGXXdaW53tRzd+6sgQI8tA/6X7e8/+KWZvvrqUkR+JtFzEhMphwViJCHOkJ2Qx7T7N05
a2rbhxKFFYjAVusHlT0nrIpkY+RwWZ3RM17XUEyoDYbgO499eONtlnuHOO9RRP44ZIAnmhXn
oSgORLoq9nmCiQHKRm+b+fWTAVKbAJs+C01mC0QoLF2678Ehx/wE07vPv2md12ANsl/u6fik
8OeeWcJLMqhSxDP8cK2bln3z5Lc7ASOluEu6q8onD2wJ30DdPwt0v+XcBG7kHFEPNi69w3qr
w0Lp/FQ/qr3g7rw+ovLnZo7j8gpYnA74R8Rjx60P5v63l/bU4C4gllRcJMNw6eaMdcuvFw7m
oT+uteWrWfpQOB5/NZDkhYPT1C0KprwnsXObC5ZP2GE0s3qsyhXjsNdHGskFSjnjqxVT9z4F
ktr69WJNMQ0285jd5NZVDF7s9mLdc/arJFkZHuYq4SGPj1Fz2MepRce54T/8F6t+5tcu8uTd
5Qf9hhRjyIzVpqvhINDfrZDRPaac4pD7ds+mY23gNwYnbGsZ6QXRFqbxbnUzmDpkgHjPcshy
gsXmCH2nngOl0nEEjUK8Rk/eNzWNno+iLwgkqVJ6wcdu1phZ1sPDCMLtQjyp5K214SAw1BYX
3GOVT8suk892w6RklVsKDUcjrTbFe2nZCeEa1kBnCO2RNnCVzlbGCPdKaxautnabsRKMKrw8
ex6iRlhmDUmZvlY3KSpkO8QR1aYtBt3LBODg5/eD9b6BN9VDzSB4y9P8qbBtsxSNyELYNK/V
nXm3dOGFPeQgmV6MZeXijUxbojCHJDjykLzaBeLdt2DxmWVqZ4wq0UvZimBkmvQBdhxnikin
q7l2ItN2fbe1f+Fe/4goZVitbQ4t9aSpt6sXGkbrFSRbukoNDdCySFhjVWuCRehKYnBfGsDc
Y4NY1ruqrrSe7rYZz0AhQkkv6sUNWHyrei5m+shKhcBRIT1wyPLTb6/XUb4/BeMNDh/8tuyx
sa99PSxf4MhPK+hJszElZTDJ446g18/v6pf/nJc+8kLmW6vHeWugi8gVOX6xpQgpAVFdcDFG
hnFWtfKXgn+BxPYhzoA+EmV8olwqUMNej5eEkuKlJ4LqVDbS9j8xet5kTPRE4GrfsrK4rzgn
XR+ugZQr9q3YkLlPs+MzeKFc1WX/JE7+2TO/3py3+vqX8FpDttNu8OQCJWMz2SmPiYxJvdmT
X5je2TiyjXlhWlub83L5lFYIObBLdwWxiKtylog0MpULPcrQXQOtqCPZ7tuJfH9c4SIoM8KK
KkgEKwEnt2pjWNjUwVe78saKLMiqtt/LsGx3a+lNLgcqfCoHtmDaxWh7pEnh561ThsGLgY6M
LbhxL90l4X50c7pr/4P3l17+Ov7thgORWwIv16bd5gfL35aU87P+MIkP2BX3VUumQQw2KmYE
JR3jchxNeimoxyuUMkUMzReRxhx5M3ovDBPoSzpTzGUxIM7qXvXcFvly4kxSIjeu5y10nyeD
AATR6HOuhQqo34WdgqhyLNjMoYxW5uZnd73s9yKKEft4qG94iodePQRtvbpIpItAcu4QvitR
aDR3b36Wf9OMPpRdltdZCB69+4h5L+9uMPGoBuKgcgJD3o7gWlnXa1MLxzkGcpibUwZF6XiV
gRqzhbDVK0Z9wJlXqI0WOXu32kRi9qsaVFyb34M8ocNlzjUiAw6xrwOW5g/4V4dOgO/IXxQb
/jAaQiVqnu58XNCTmqwNY8Eig0OWDrcZ+NsgfZoazKY3W9/bsig/RI7rboN6xqHe0KOU7+NO
K98e4l5tSQsmii42+ErxG4gExLcN1u5wXmoJpQfT5LhsyPzZEoUrgaalnIMN8Lp+q+kHF9v8
+C+3zeseD2g9uXy0MRXnWoV9HYBslSF3SFUDd97vl99NPzjlm0JUPveWaOzP6Hl+PzLRyDQo
c7Vh6YAkum1VYDGXrb9l0yOmrK2H/K25rDdxgmr0Z0NmxXfOKLTSyAaQPIPxbHiocTNlfkB/
g7qQH16W3gIPKk3X49qf0Jt6cfYGH1KykGGYZ6B3Rzz814nwF0jxhwR7Uvt88W86URz4jRDO
gS/4v91I4R+4RW80IQA4BHzn7Suht/Xc9RoU79UGCc5r9ysWv0DU77o1zhxteeuIvoaIGeJb
B0cKUbf1Yoi9DCsxHQi421GmGJTr0dtbtAbaV7WF/a84vuky0SMbke96yxCx+m0N55yG6HFK
vkuQfL9dI6CWb1UnAQKrfwvBWCchtUDVRCnkXDvpi/Jd2LHiUUgp8dkoD7DY/RQ1QcSwXSGj
k3ugoL2oVKYXywdA9vecOsGsw+0ZbCsAQPwdT+/7dOn5ClqQ4Zrs0KnSQrgj7P53YsXjfC9M
+gqsRwaak1RDXe4X+wHxeZgD0fnDK/PglrFZ5tlDHWfODtG9eC6aV/sVHqlxdw3ecktWP86Y
U1ccpASXolD9dg9/UhTvWpi0xBG1G2qbu1/bzmA/sMPKg9G4Ohop8pEymHzfJYp9Xbh5N3IM
VSrf0HdhmSZC7VXp6RyvD2n5/ozSSQqtg4lUnq47eeWnV7CpL+39fFZVvFVJr5XJZPts8alW
NRc/RtF9eErRK6hRqGumueTq5o8tj4e993bJVcVgGEb3QbOm0dpZD3TOd0uY9AZZ0NsCpPwb
p3IzZY9lus+aQ6OSk2OOZR/PfPLTRfWQVOQ7ukIwXTnN731gWGRsyMAp7MfRaYn646jtYiY4
C+PmRcPvMVyrMR6vLOxiRtWjx2DdB0Yh1k9KbhW5NAnTcNAYp5Rb2TKApknqYlR8z92cTycO
mZ77mj2aEA3Y7pMpMryG6m1nS7KKy2RWOrb/ta4cfFLTGSrLjhkmB2hLcY4KyOXs83xf/rp/
/xdXNr2mIi7N6/l2A3qZbX4bLhP/VJUN1P+tACb3UrRCluZn2sfbHAfwoLqzv7wAkaY22orB
lLRnAie9D6YQ2+tuw8YBcDLVL/V1K38p9RuJ/zCU81BaTxDGO7ZLisi532fpaFCgRaxhCOrN
AmF/Aj8ZAQaOL1zW24pZHOs2Yy30XYImLgYMuUYWzqsXA+q7Yp+7J8PXl98iO7E0EpTISDBa
wW268BSXH0XqIkUjTF+ugcQeXrsI2hyhle3S3TCKjFLzyFgYsGmdMpsKvVyTD+/x2ZHBn15q
EDsuJTT14lh8bxKtzDO/FxcRB9U7pH0LBNphTh0Vo0ikjdoz6B9okUaEqQBMmd53u85szVvQ
bM4fSa7VPeM6eNLxvRdFGjys+bGlr0/0IaB8xnqb23xk0Xezvxto9QlTzHGzEXiWGh1SmU06
R/SQKhvDVmFkkxmWSrrZsnLUcLMLhub5QT5uKQreHxaVILELuqTntih4mvWT7YY9aZO+N4kv
ILGlmuG9idZ4IWPYy8UTMzn5cg0i5sg+A7N5dLXgfhKcZ7mSrKme70CE5eYPNyQaW0IsWoKS
k2cbW/J3CtXTD0v4jGSupkM8xkv87J8dEHKV93FXPW+dVYVCZlNLUedJdoGDxUp97FlLe/AV
e/RJnbw7LYnGESaNHfv9exsaUhQ9xJuNlcbzTFaVlETalQayY0KowrbIuGzZ0GJjS4ufDgnr
H8BROFuo3/dtzU937jwtvanuKzdETGOesDYtry/2+afJDQ9zFgRCNQIMG6clyvQ+OobfEN9I
1f/M02G9tcp6v0VzQ1MEGC6+qtXAhRw6sOOXTjfjy2iIW8QIxiuEULlATWtI02UH1iKK83iH
3Kc74S81fk3ssp+0N1oD2dW+x75mpcfG7dWz+wkXRPs4Jv4Sx1KEotJSnVrU5YyL8SkwCnt6
8f2/gZz6+9eADHzrbLcwKr10DcTr2qn3AVOw+1FPpLRywgvD1ecJej/sA4wd1j3/YmNX4k14
i5B10kxiuBWxz1vws/JCuK6pHWX8z0qEaVhnz64X5DHfHweMpchPKR0SY8Cn703NIPjN2ZYO
lM5SsW5mhkXjGNfp8/eiqtzC9oyQTGZTZIZ0d3uxWSGjLO7T4nAQSNI2pkwBjddwLFebjo0b
jztn8V6V/+RlsKRK8NHJ0sVWA7CIuTA5GAPYh+6V5PqCMjvHA1qMDBETB9dAQa8R49cnU5Ho
Fk2CreiIC7qBN0iE0t9dSFdT3bVar5Rvhwmr235/csX3DsPYinW/zO+UoeHHwtHiKd1zouUh
rNGVSf9qS6kpvrR+nGhpchUD3jvaD+e0qbU9P09Rta98h+lRd5IrN4chHxIM2Yk1Fi1YUEnz
heAst3I36mvePu+RZoHo8iIPtPSlNqXchZOSNlOcTGq9i8tJR0xoOroy37UYvIWjYiEqvI7l
QBLA0XruS0/nHWtZA2VfBxyyHvBHONcJvv+01Gee2wZOQ5Kfzs+/zF1KpySaLhNm+O9VbqDp
czq1/yx4aP4Hggf2w//VLzofT2fKrYEYwD+avmzwVct+n3OvskZ8/QMBi0zFluEt5Z8w9YtU
7GjyCKTEWHm6e6v4vd6yw2sgd97RVfBbroP+zUOgXV9MPEdb3m/ZtlKHfYeK+/GG+dSF1Div
adrD8y9vjFd1l/kL7J16sOwekyUHdUvKdKbGFHq2ABDMvcCFVggwN0EfTGhMVbY4Pww1PtNo
iDhZ3V2AY4LfH/soins/aprfC2zuV50HFenvvcdZnpR0C96+TW4/D1BQd1APFGjYKNBBLA7M
ezWj+iJ4LOX2jXbo8Ya3GISrEzc0DJMJdwkx/d7JyeXIsch0BzO22LFuc27D0E37j6yKYuPG
Jjymfa/IkDPFwsAqnxUVRYS6Z8szJLNPZOZExZTv37EKHW5QP050GbaAGJgBKEa62cnII9XL
3/OHB/vNH0Q1BpxadinA+4zK+HmGzOMWscXtveWpj3MysddUA2Ybu4vthSyWiym+uBc7z37C
UxCZkKvCHvWNMQcUuh2OUc5/fz79tPxnl9u/PHdzWezKHqRpXvmZXK4K36GnG2j4jA7g5l62
jozZl6uAyfLJit0HhvQamd9WtBWugY7pDu1/P68+erQG6SXOHGTf1dGS5L0oLVwouvQTHulv
7PRBcuoO7mlOrMgC+JeBIpBWj+YC75BzLVwESMzhEyadwOV7Cqlx5H0/ZueRTUmz2qvh3+vK
YWbwR7uU5rXi86QXJ4uW9E+fXV/pX57Cv1+u93z3QRNLUcWcank2STDcLuvBGEh9zBy69oTl
lApb5Wz5Ypth6ONpwSb142lHqC4kAQzscXqkvT232Lkzu8aehwi5KgicyjfZEz0AD7FLM4LO
jBQPhtVzgvMZZ9I7c2eBVeXpgDo0Y3PqXR+iMGuo32cNRFQ38DNWdSeUvLAJ4dUDCj0hoalA
yCTSR/+byp+H/2WSFfTAdWaGmX9Yq5UuplgSmdM/uR/ngkLG+vegpRb3gp8rG6yBdjm/U3ZH
WR0SvrpbaSyacEYJtwYSKlGhWnR89AuVtPlJleiguswwqg7l1AOeyOekXp6qW88eQPnmelVq
0RdXo5i9/9EayIy87avrnxT47DNKrGG+BfBTgoKuJyNBuoIIqjuykab/kcAc0uOAdx10FGZX
1A8Y8gcisNNN6rsN8T+6dLbOYurf1RLFJggGlteyiPU5+QqNBhYUJaHzHHsCpftLtUeFyw88
m7QPGr5Xi1TqctkmUnZ70Kl/fJmRquZJkczN/EkYkv0EeeQ8bLvl+6CQUaFbk4Erqbfv6D1I
USiMtIcoLfLvKcY43+jE5KS4YBRaoSeyXU48SY6eM1ruY1q6LqoWzl0rb7FlQaE7tt23xeZe
OMmBBIidKVkJ7bUi0nqTt+VJ3JzQfM7NmBskSpL6pYUnVzgPAdste8iVJsXhbsOBxHz6zIPL
FDZrSNx/vr8lPok3Pig7XUTj7UV38iQfhtpOAFIYpIhO0EcCuWk8OMwRBhih+GuMPqbXzdJk
4bFffZhYKa1sQ2PEdFWWNMYdCSUL0bxLgmXBP/q2G1W3SDjlIK/CmpGDayAM3/e1E/hmRnxv
bDVDXYar0E0ZJHV0hvsErtotNRXRWtUVOkk8obNFkjzyS82Dut/gK4vn/KdS6YaZltIhsE3l
xW2QVFuEXNbM3GjrrU7pBNlNQ6HNvuO10NuwjISi0uQsTx0j3YNmHDTS9+IbktNUz8IJBgsD
dcQLmbqP1uwV6pUhT1z0sStc/GIQckIC3NCPE2BVvPvo19hkwyr0mS6+nxTMdcC7U8tyY14M
daErZ26bdelIrY6Ewi+GL3ZMQprUsS8DLXnuHxFovrC4NvKTspBgr+8kNAiTy1Jgf+kA2ae+
Wo62FSc764sciqtOZSXFGXur5w2M3hhstwe/MLd3ACyBW1LcWUdEW16pQ5NJJQ53KxYuQWvT
SxfK7W33KZr3dcdqiuYSDO9L/chRJQcuVjWFb5zHn+SzFUoOQDxGtF2+MfU6V/zqtj26ZnAG
29IYvVIHxChkNxLS30Xu8uqNCT3h93WRZBZLjdmTiSo22nzu3/BvETwyMtlk/sDh/SKzWnEz
ZvlUEHVa8VbQGgiAgpusXD+sn2C+siqSqggo5UcF5kxKBK/yokOCasAQ+rZh40TKa0Tb9Gan
8PU1dhhT5xvn5WmyyWzo5jj9v1OD2PuXdwQojHWfHoDpIt/P+hQtSBCI5UWw2IDCcSDwRQJ4
7MS3Yskf5BA8j6Xz1bQkr8AAlgse9WOgsp6kaL6lib3QFOIG1Shsu9cVITtAlnV2sYhOFy5F
v+090Ensjdt+rq5N0dyIkzlyk3kuCjtao/FIT0t+qS/v6Y2dFNNvujt0kgHrCWl56fevFhsO
iAM7gJiXwJmCdp8mB0b0q53gXSdGLycruHA8m0z3saD0wWbuh4VySZ/hQGvrrmkDggZLgWI8
6Wd23rIrxSn10d69A1FTgmc6QifnddFecYQcj7QqZjdR/aBVNTEZ+Qgw73dnxHiZqx/LT8a+
pqhUV1dzsmX1H/EbGQEIr/t+uuHspeW4OKiJHeVaEhONLA1sdEWd5Eamb9hkRq+cyN2m8/Rl
RYx1++SIfLCLeX/wnrxEGBWOu28FO0Jh5WAZ90bWcx4E2s9aFEMKZgjIUSYnngDbgzmwPZz9
tMjnngO2B+VBrW+nxhZxbecRL8r4720k8H92ifov/kinZ4a+FEx5ca1gaKoVUmR0UUWeokIj
naTMYpflLVqGtnVNd9AgPHvc6waUQTQUPsV3MyQylU9utbWwZLV3DaSebY2d/iCgLRNhd6iB
OZ4vPDXZw62IfuZEZd/aLpbQEKmoSVzVrIRKOjKHF+wLIiA9rwXA+eZL1zAu7sPY+77Kw6hG
WDq37hACUrFzxuM7u92dy6Q9HOMiWD7caipLnGcFtNXXQ3D9EKQaLGnZmZmcEnrCDbXNFRcY
vbipbFym0mGnt+ljxrsCb/lvU8/5TQSu0JUF2lwKspyH6TinNP5d48XGAcdTMqMww/4GuisB
mNzFG0JXR49yn9svKdhpBEmfw83mrvwQ4RryKP+KIhelQDgMjjDKROI7RASpB+9zdfvFlEVh
SH5WfDpO5RbNWtMhoaq4zza1uIfUD1GaaGRFMSfPG+bszhhGNKG/rWj1k46YiqBsfFX/xey/
/f//S1CMrShdYNO40gVtjW2D9CzB1XB2xfcJ9O+bCFIlBYCVqstTI0Ac++uzaWdZRVDGzZAb
FDCj0izn78xO4nrOler7PuBme3kK8oljl/MjkSaDFLds1K5cYmTvsB9FKs+yc8H9sG5w337W
vTda6rMNB294Z9n39RYni74MYEmKvV4DCeR/rH0eLUI13kuvEfJpCiAm46A6YX1iaiAQhQRv
Vk0FBLU5xS5UZfuGRKowxUBJcsTFtWbv3okICbh3INX0tESdF/RoPx0zkpiEGteVKecQv0Qa
XSsEbP1CtW7FJkir+jz1kxIF1kLrAdI+NfIeP3EXX7YaNi77Gub4TCY9szvGZYjcSBFSNVp+
ZFR35hbNFmHUFeJ7qavsKFKf8vq2vDj8KOlJkUu3mQF4WKWa7/utX/p/29+zmttkf/DDA6/t
QsFjGkGFwTI1Dhd0TFTrw55kUqNR6Xab+SMO877WaI0gw6/BLiwWJY11xaulexi2uaUQ2i88
izVQKzB2wEV2pRZKK8Mehjz9WQl2vDZPz+POOcO+bFGvMOcQd7WiMy/M9WSyByz7myyXe0UN
nwbqcisifUf0jfpKoFFcrXfVNLuvByrsYzKbnydHPu1rV+qSe38Ms8jrLQ8gOfdkh1UWfSpd
2qbbc65COwNwwyvADhiumksc2BH+6xv/K6TItETTuIkDrwHEg3baLK9k7MzOjWT9H0PjnTOB
llM1AOWRA/ermRMFme3pDgOsSBSHB1L4VIZkCUizb62Bpkg7JhaLFqPWQJAYQb9xGd0lxffO
bW3+1mugFxdlr3/CzW97HHVazhBfuaFgfYAsaLFVbAUyqzjOkh6Y230cBIJbGqtSVKhGxsqS
2bI65iByAQpq47PkMrL7Go2jYWnbRbhXtpiOgx1nQJUUIMpWOqYJb4ocQ8LKK/htMSGBdwQ3
01Jjbbu0I4x7bD2uEtETXWD7F1MSBOUughgDItJqrwc+EfXQsf2oztSUiQcLrIpN7khx/EKl
O9jZ7j2moAqDyY2KeeWdGerfgQmFK8xDAVMNlqoFgE1tFWkej2BNPyouhtppnCo9OaHVm2cQ
aIuyekMQ6aysQYl0a/uTY7BUcjDUyKhGuMmCm9YSLiK6W2Osv0HNBI1XBbviLmyh3P2REmJI
U/JBJt1sN41ISDBFXI31Vct0LjfqwUvZbPK8vll00XKYohiXRoTfLmlLd3AY7m+ilZXoEvzY
+BDT/CcPGizIWCVj0enl+THJrPKPuxS2ZA9ppzd5/WDPSIh94TQ0sbLd2y5roC3VJWfBVuz4
rHkSUsTIMNNc6kRuclR+RquykLHqVbHINyaad5LiCfD0pjdx7OfQk3rbUgrM4kIWQt0wOhb0
IojHY/clKmWfwAJIBqXMZc3IP5aUU6vFA2heq3T36AeeBdk3zH0VsEXSB8fmJQfFkVbuBWQa
KcLYd2Cr8OxgvPbkkww59+6rAwIBWe7iifA9aSG+4LsRcUYtz5yvZcMv9OxVnh9xwaCJlkZ1
/rq5xcWrTPxrIqrYj9AVX5h3s6uqqrpIcpIYPGxmLEwuArZ94SDXav74pet9sOQGFJ9awc47
8sXBvEfRIhOaagMhN117kvGPYNoc7gG8pZkpQsJMmJwjaP7J1AM50z/Kk1vU91WkDcDl4/m/
/fSvn33OmVFPjs2BtrLWQIiZdv2HFzdStM4bPELLLoh1p2WyvXLpKakPKPhPY/cMLNpTSvy0
WbP+xJrn4+x8Sj8Nl5gMpVpS6LjAmGxZ51IVhpdkFmL4IPoifuFAG3raYk8P0cuAMJfnuIv0
rA4AfVMdb6wuGDrzgjoF2bfnYn5MxYUclJP+wroh/q9FBDKWvD3radYoRW6M50UHuLS6F0jH
VqG1ZZ2ZE1tj53ZGu+5OgAp1FgoJU3GM3ox5+uBPQE0r/hePgP4N7NLfvXZaCdoB6+NU0k7A
5WdCi9RXeHdaUmZ0DTT09tyyP4Ynpa8cvo45oH8l/wMJCo7MJ8ZlNSXt8lFTIMDi9KzfYF40
8UFi4SKBB+CCXhJB7sV2oZ5+wYVdzoO52dePbX8gcXBAcbN6W4AAJx3nNS5ey8+OwujIX1PL
dgFk46PfD5cRTN2z2p5kUIS+kHS80FacjscMTBJCrJo+LJ6UfxRyUHnXKkyxI18n0cwnGnBe
Qwl17/NwX9Qahbi7sRYIdo5Yi0L3J9kxxfbygiemDL2sGDDiPvzSouWhifIro+RUE8Vx3Gvj
4dowJ5XyGJeeqVMKPelq1C5ZbWORWlVh43pXajYec0Rqy06Zd5FHD66kGk+6p2os2VyopnhR
xEf6UsNyAaOYZrDe/QE8PIcxMFuzV8nSsTD7Kck+7hVwbiuBP3rJckhwNXq/cPJyoLVGSVYN
tGdvl3bLY0x2SJOlaTzmv0AOmsMF63Ozy1xScqOznV9Xk2OuC5M/nkOr4d+EeVgMQvgWdifT
tp/BvFrUld8XnT8d4ePiUpabqeMbSycLScszlZSEqy12LW1bMWj3b8Ll2FJLpovSn49eW3Iw
ETWAKbROQc5XkysEr3/Q7BkZPV9k8EDKSb3JwhZdlX3G3zZZmdZJUL2oEdbZhFA+OCgwkl5W
Ol/hO8MMLRLNg66KeixRbTNzsp1HjfjqAeeViZRJjDsGAOsCTIn13wE226XsbOL94pL4++kv
JsUTO4qiIyKcsO3MdvBzFXMh5UnuWPRDe0VTgQwrTW8yrib/ZGdt08AF/+gsMdGYTEb6tho/
FhDKASkSJHK+SbUbKaKkbCCkpGppbfJ0/dQDrs/sxR3zowMQSpppjXfVw08m5qclP8ccfxje
ZvUOI2vxLInj8fQ/KFV1Jjb/ADVeAzUz9y4E1ePTc12mV1LUBLO6GXuN1Y8XIj3KObnZKU4x
zh+jwmGxqyfxY8C2GypWDNcNCUn6OmqVZcT3VbC9b7uUwzZTPN4P0GFzsNmCOgtBgSIB3d1a
RquNTz2n/ZrXIRC5AwhE3Lfj1BaT5FRXGdO+73CxCQb17sXBtdj7BhYQoQGMfPYaqJaFkobP
dog9r0zng3s68E+lF9fsccqDwNxSRKUUCpMtl0iWU5hT5iJNEFcyLH+2C2oaj4/GhD5lnv3l
/f7vrda/Zbf9v6s+xfaW8p5wm2Yiq2bC+ChdLZH0oXK9c9UzIaHTvdKIO1I9H6Qpjm0e2cHO
lQt6scvop4FgR77W48z+0DXQ7rds7c3uv7Dmp4RAQg1v9wwFaauVF1ETVzwboF8g22ZvnZFW
V8MMpiM2FwjU+EEGmGDF3TjAha6lmTAEWfluDdTr6bxsrRtyT6f0jnPSKUXz1kDlIoRyR3Ct
wYFrJbxjw8PLp7qOz7hhKwxoCaa3ZmHZTpvGrwPdzWf8P+6+PKCpY/sfRKGiQF0AFQGfVFBR
FFllSbSCWAUihRBlL1QQEJAdE5KgVNmUSBHZhCgoERAiAgYIISiyb2IIO2HfCWFNgCz+rm9p
gdb3fL73ft/a/JMzl5m5c4a5NzPnfM7naHixXivZ+xXTQYcmJ42cdmGEPb0C/WanM7HtbWSI
C70xXPsNJBjmTtWrDBUnlU+FSyVKHZEDXw+8SJl7Pp7hkp82hYC2kdyx8fP14S5pg2z1rMru
9Uhqkak3AWeb3SC7Oa/7+3CnPOs3XRZIVercQBPeBEb+WvScm0/UiIZ1VVpDej5zuDsF4U9K
d2UqpujW2Z7OpK+7eFUxVVKM2eIIKqzMYqP9rfNVW2ekzhDMJTZTZSzcbeLnXfO4my2wP0r8
JZ+Z3d6+S1CC2r4sKBiROtbS3yAvKqqrfuViiu7Zy2l75VqxNgAnTU0QHx8nLiySIt1/Uqzw
5phvrcfuF7MsmTDc4KRIbaxZV2HSI1NDe1ohyCK7j7q8mzUDuIMJZo2Rjic3+o/o035QNYzI
nzzMzfU/LQ5WnC+vXfaDoue89Ws9eWYyFxPfEZN3W3Ckdn/zpi6SW6yoHW0YykSB98YLyT3y
iR+BwADYt0j0o8v36t4Y1dFfRVh/IGfOGSeCL28VuEnamh8RL+G1SK24oi1xIC6xQMphK+A7
lnl22lhftXwbEIJw/tCmoOL0aYX79erPQNsnrQw31zbDZcyzokBxzcdSqeGMVtpTXLH/9IHp
y4zBNP4JQNdVn0ryU1hEsvs+7vE3HBhwFF/1xy+/ABzFMbLnux/RgSiYvuzgPausS4B6n+1b
5sfgpNFWrl5Is7HFb4N+lFg9Vf+7d5n0ldksGLDzLAN2nq6OTX54yYhXmdrycoyDH3aesU4a
wM6TlqOiSiHQ25NnOgeeZhcdZPsAP0H/453nxb/uPB1W7DwB19VHdp6r5+p3Sw7dzacGrg30
/7jcUfLNez6q8qu7ob9b8Yu9COwRvl+ceoQAIZHsKPCE+/9sbdou1DsZ5M92W4piUsiGqPNu
7lN0nMNQJ/Y7wvzFl6lTzSIxU/uuTkiR0zSYXfmdwwuW27kd1yt7BmwFcxDLrhGIY40eR1Jc
2/K4nUFtaCvYkZI4QhjXOgAxysqM8KOjnKeLtSbi6QARxpFr8djtJ3SF5Q+GZsSHhc28qcxY
gSz7XyWKeNKQT/O2PNUhf+T1ztIcmySbS1aKy1DEDLE06jNYcQWqjxfNmQ1I5ukiZjaVZpRE
2PgiAAQ0emCRr2h65WLjh3E9ce/5XnDkcK2NLQpcm/26lMe3/QbJJ7G2F6lOvJw98UEr63+C
rEwfVwYJaXMgWEvTN9jl+5rHtn5Cqy+oCj+GcEBWtlnOsRFf4qXAYl3/DywKJq2bmY1bNCJZ
FL+ejfNcW21fR7iqncOYGtQYihJJmCD2Gqls6883qsbKVpWfYF0bZDyVSZdNnSaGEhAfOB4d
AY5HVdexsUZ13EB1L6qP1MPknpJchF1P90jD6EiiDIKWmuYtKhIh3VWCJF3l48PZ9nLXYcUo
sEzvu9SpIQFzLes5KshYEEIs9AngmYtY6h4+PkaEBdtuONyBsSHVP/ZjX/xeFCL7mKWtQYQr
iM4/QL3ne+l+6ACdqfHN7pjIKJ2hbvpogmBr7jx8IZ3ddtdLs1v6GolsrdqNd3AoN92iZtUy
EYcbaQx2dKJtKJ8+EhLP+aa3paYvMj2LA6vt6JCRiUFo5JVrZOS6JMg7hwGH1c58ZZBmmlyB
9gqDe/bUSxsPS7nOJPIbr+vVPmZzF7rBZpsZwXm9kGl+gySHwKlJtimFvOnuJr8vw3+04Af4
j1Jb61pGaID/6CHgP4rqBPxHoBJ8RuNv/Eef8GzsYPruxQgllRxAHgWeuUjNY9s+odEXVIUf
g1dAp/gKtKvB2RR5PAF+8u75tcP/bDPemo7+Z9seQ+sryu5NdX519cm0EP8f2/IhmMo+E2y8
Cmt6k8QYI8RfKFp0extJdRF6ORquDZl0tyVag12erg/5jAQrMt/VtybgdpAeTfSE2myAzlvM
ZXbZvAU25UC6s9aglRoL50/E2LodCfbjucrZZNJwQtyHd0nyzvRq4zZsAlXN+T1fVtf68pUt
PkHmx/h/H0BvYGxPfc9HeY7jPbq9+acTn9DuC6riMFZttqwBJkrgEwCSZBRzPvg3+eg+e1++
dho2+Pu+mIO3y3TReXL3RM+l4BIqxpYfOgVK49ahg4R1JqRG/J06kpMWrYIsCYo8N519zIiH
HNkfZRLWdrSqvO6/y+nwyXsOKMnbNY7wyhL1BOquRWKE9dDXR43pQoKrlZqwCc2+wIrDW2Oq
Nt5YNdh/XfgQFRDVO0cu3wGE/9RtfM+Xm3P97pVre2Qf/uu2X1CNzYFL4liDEUoIldMyVIvn
QpcETwatGf+/QawIIynpACw0CxMfiHL/tjcUzSID8Chj8d4Bl0DDfsHujoL4WMcGNbrT97kh
Ruwo6eEE+SGTPkODSHvtxetvs72xNdb4n4fBId7z2sG78IUX1P0LB4cEK6vnxHNGCHUu92As
0qvn5EaWfAGXuy3OKEuX7FroRSalnKwY9JUZTJQkp8zMnckk0AOOE0DMuuAIElUgylU8QHzm
XVcjK9Eflq277OnI/wRgBBfHKOw+iHW4MiHbdBJnazZ1+sCsZ/KCTUUHlax0VJ2llTmra1A1
Y6s18pZOOjfbFuSmtOAwmNxT5SlwgTgvhdCY7Qy64rHgM1jTWsOSGSbN7xIZZU+VDrzQArYV
TuRHPDeAYzu4aT+mhMjXPwt/65XqQH7kZrNvkMnNPPMawNdeiuXraLQoMScZXS+HzNkkcTVl
xX2zhm6AToU8MME6GVMGli6rKk7Y1l4JxN8qPpc5+nxabsnqhqLv+vGNr2nuAdYPryAxuSzz
qMTUiXkXgtJ4y8xYvvXTSpKLc1i+X+F0seK9Rvduov9M5eUpKXd9rQi6jInmyczpHuu+7JyC
F/mHq6OyTaLDEl3Ki/YXRkQ4Hq6DbtPt9xxP5hlTT+iy5bKV3uHIT44HUKfgtLCCLBPWITPR
YyyrLrgLHVMrUjO2MEHzNGQ3Be8JthrwPs71e2CTGk6Ow9Thrz8ecEbdXXwyNsW7Ca0hbWvS
FW6NbdJJFosg3EfcWL5mFxZpEXDuQ0oh9eDFm3fhl9csuNVFYbcJV26Jumy+7FDsKwedkKWk
6diOFvCQUPH/FnsI9W0AgpqAVE3OYCB4S+Xdz1ihn6VjwGqJmY3cRyjwnn29q8f5L0ubkVpx
lcGNktsBEMQ7nzHgleJ58q6RjJY96ioo6F+2/pIq7Fj04WANvSlliGTbTZa1eF5W1J7fJq78
j4DUxtZus7OZA/5i065VhZpMvyx/t44EXGlK0exUOVTv2l7H/SnySFtB3ctCCdOxT4SUdS71
vezuv99GCzwO8DSri+xcvO+9sHv82H4CDNXklXB0Iu3gDDzGMHD6NG3jtL/FAEZyXkb08q5s
CcEn+CHrNzkx8X3LG4qeEqyrE4q/SiAaWsbN6C2d1FRelptJzqYlDCjVEj5gd63RfqFCck4p
Qlsy3vP5eA64Nc3v0l8uoV8VoWeHWL5A2dadjjZ469aZj+wKFZzqOeVmj7KsS5MGn8obxw5d
FYHDdw5BqueOu+jeSVThFOyKeluBhyUAP0Hfkud6WytHnUKA2MZL3hrwQfQ008eE5f3j7jTw
qfp4iIfR3MYsK4AC8ES+QTfp/HEp6a8XoRAPwxmyn9UCRwS8C0PskmLrbg2QgtQukkoyl4WP
jrFfPpYiIrcV+mNiPU+FUpEinF3o6DMa231MhpJBF9+gFKCTTs4znMiTAEkhCAa+9EbmQGNO
+lgTJ3SLwVPMngfSQ3K3Oh0Cpge8GIfPaVi0KhhWpVrWlZNcEm1iC71JW5xkmsutRzG76yrd
eXv8aA8Cb04LxTcIugSe6o9UIvlDy7raLYzIZ8ZNMS5XLCsrCiHwwJ2LDOEFFIhnXHr/PtzA
6wfXQebLQdI8nLvIppXSOsZ0q9XI0X20LO9RgoTHYCFfzw/zzweDxeQrzK5Gy8+3FRpVpTB7
m11TSig9+Wb1PIpMMfxhTFtBQZtmy9XnAAf/wEBnGjXT/Gn4ZYK+ckeCc+iM3oePgNk/fbo2
KC1kZ6QPO1w27YNcbiugAKC4nv5b/uw9EoqUF0UTg/ibptamZpzviNLDiMXUg/N6iNKoh5/B
Y/Xpex5db9xAwQFZbc/3fNy8regnUJCYHFEU5apwAcs+Jw+8mz4SPfNRNTcjlxMNghsVtgEm
SkwahBsbuvm6GwRhBmHlsPiZH232Rf6hkoCTRHRNTRelz1KfDlHB87vDfgtU/s82PR/7zdqg
6sOaG+nDU56Ry734V/h4FROzCMyINlCnwox26aS1ZHFzPsMDMCCH2d1ABP2rWf6/MveZcb2d
5lGbTCdMCnD0sdJ73Ypj9KpGMadhvKsKEOc4tO7ivxr52r9XTqQPBujMeWqBF4vM3vO1X7Cr
EtgVeMjVdKLJkPvQ5V/OxNr+/shlsepZ4JCRkLcYyLhaBOaqaCHpYPmTdwPWjvk/sUR8/FD2
P2H29s/yf9DwFgtEhimjvm7YEO4zEQZE3cNoYM5B1gDsutznULP+7O07nF5x5DKc1S95HYqU
KB5nSebpADQs0/y+vSvnat3T5SFqDzhYFd7iv569YId+vpX45IluoURf8fLCBLAgXYfXwVY2
WCEfYF2dm6nLinwEYxrLsxK1T20K7Ylr62zCuFydKE09f1srDaVRlpivZ9SoN128Pzu7aSZn
+43eoBU9rBQd2NR12t6UN4zUd6CvyjZw7SA3g+/A8I5h7PMipSsrfvHyUjbCxGy5aU9lT9ol
kKSO1RGAnfO7ZhyNcuzxzg1rtfvCCCr10LCsMNhlhvapPIAZwDJQQrnKR8/L//WFUACDO0nT
WSQlXGec+Iyf+aolUsb+IchtU/DMNmsMWnByXSb8EEWl3nwgjhv5uiH+PR8OCIQKWjl9G4wX
qvAlha8m0Cph2VBG601e6TnU/ZnOKONdgUstqB316zNXVl8hO4wVAPhhnNlyoe0i6uTdCyv+
tFLcjF5OMXCHFyROjr7nE+hbx1UNL9ZVEMbbynTxmPyrAckr232J8q5r23oHujNbUtLZJyrZ
aYeBhduljOEpZYKYMff/I0rw/3Mys4/yMX4WrqefM9ozTz6gY1vYQ0AmZnSyD8HHOA8zeeH3
x5OdNaCNgoG7/ESvGC5TtCKxnVNnlB6uWg1mWCtLEstj4xVOQ1ImlNFd8Z7PTl7DcJO4w+yR
Minfa453LMheWZbH8DUbDVc1/LVQSfHkFRqnL3iRpzm/NYj+o952fqpUIz6MfLFE6PUGllsN
d5uHsy+nRTqMOygQ9Y9Kf4pvKeS3eAEBeXJ8rhWPefIE6Ujq6xHcLRMuDw9mnrY7tm6tkv9Z
SMXHI/cPpOLIWLAIKukST/HuCog3v1W3GznP5hWzHRxGE7IfJQ0/wSPgjZxz67d1rR3b2vIG
5YWc2uwSB3WbzRSZDUnRjpOQTBUblBWEduKQLa7BDR4ir7Of7BXunOADPkGXySe27g9j2cfd
PXP+Mwg/egOXL8Eh0cmHuuPpfW61zJIG59TFE9klYZo2stIazEedQ1JnD7GWdWpVOBeUTqwa
qhnYkk2T3FJgi+kZVDVc5tVwt3C+NrZ5oMmLGUy8eZ/tN503mYh1SoyCDa2PXtXy18InvpSF
N4zHO70tHO1XQ7/sbMoEPOueB3hfHYlwgo0SDU4VzsHd1Wy4GSfrfu34TyCJRBbaPhotutkY
X04E/zX52lPGpyVf+/fg9sBU/X/eHXsDu+OWt8ywiOlbVw/BcLB4mDAvxobjPv3N1c9AIgF5
b1SQf6lW2I6vY04/PzoJpGForAQW8U/SYjPFoL94nlMh1OS5gVrRKWQvdNAmv1VLYzu9ZUDu
9YCBmLI2B+/aXdg5+mLKYJr/h93XL8wT5IsVCJ0E5LoI7CWvIvL+bz4CgBOQNapcHtLCUYHk
LmWzv6UT+scNz+OgnaCbDcOzeELtc59wAA4l4QysYsUQf12pELYjCx3dNJ3Bmjwv+vofLf4U
35pJ7d5vX2bn+g+rcsJJE77rbsEtLTNK4AWuZgbh4b4JuLbFqHjZ+/zooDXq/hctD3ac2+7W
hSE1GsJHVTQEEx3kaR3l05NdtQSjGsSbOv80p2L/sDDmN9sX/hfpO2K1Wq/Vu4ldjiN/5bSu
HO57LeYqfgzKqGCsM/gMjuav0qky2V3hnkdGOKcxbIevtkg9ImE32QwIGnjcLWvaz5iHDkOm
T15ZNZnr4rRahwICq69MKr3nO9i2yEIgZVBX0HwStlUL2BNDm37y8ZulGwrzarqgSyc/lo9k
M1JDduLeOBamCKQvqjq2ac1/6x9Ffj1ryyvLslpaXGSJZaozELRH7QfvUar8KRYpe1MbuD89
EWGM76kg7KGvGuM/2n+p3wL4GWHGwyvStWhyzXxgDXdCrWp/7ZN9mNMjiEtW9Nnbh21GgPTc
2L517BNrVPw3IuUjC5zyCm6W+Jck5hdA01zgt8bq551LKymKCcdcpw+1eo1cV1ZW7qBKygP8
GncRxbP0ZpjhknnZwL6SnmlEewxyyEtE6sHx8VNpgZHNwzKRPXkXW1zZDb3Lqd+O2zoMwTVU
zNmBDSCy7N1dJTeb+yt/7lFhcutf8Y0WCSlbDbi7OVZ0dnT5DihlZl6CQtWPqnIbM2yriFDV
eqi++ihRDapspGbIxGzXa3wqOrSUM24UAgvx9vLep1dJL7SYrCSZMQWzdNzGNdICc+GeDZE9
BMpTKmu+CvSeL7vsqXn87NQ3M9+2enTOKDX2dApFeSZGBLr0M/G4CZ0rXfCS3Ke9Dsby0txz
Momw/bl9RqZ6finJM31QlQFGJ7lR6FJLoe7wphO9yGQHX+lox2RZmzcV9XcskmBb0yMuSj7N
dXGsTFnWuFboFY4IkFHijpRv20PXPR64sAibb5Sb0e6tsvvlv/If0ayagi0PWfp4b3qhkuJU
Rsw93BG3oG2SFKPMmt0kOSgk2iIE/KjkOLokuLzdTwJJ1lsVWvsiix5vXf8ZDFB6tHSWjujp
gJsQeqyPC5pudZETFCG9eZQRVZGIVTndjetJMuAG5d/9RTFA4D9LcsGRVdk2um7Xg2WZkSmb
DAZbWh/OJr5a1kXGpFKZF16OzAa3la5s86u8Y9kd3HqACsqG8WTvrsU1/1JtXcRyScc8yDPX
lT7bTUyDsTsGZtcNFYghKDqifTQDFC8iXzWcy9H+Hoj2/DN9tGIl8XDLn9itcmSPbzuLYlBM
teoN+33u5owWj16GaQfiTlNd3/Nl1oNfb/jNO/bzTULKjDVk4KtohZk8RdSLW2L5WcTphh17
YMa2uihxrkoVx3jx2I5f5v4/zEXwuxzlYtc+A161RSCD+57v5GB0gCVjlnvqDEDLZZMLmz4p
Bd95MTtRx7kqbrFmvDNPj7N457QT46FEyi8qfBAOgLOkUbJqiShsXFvcdiC+Pndk9ga18HRq
6RAs+N4yW+wkFr2ujncevgICubKDT93HmbReINqE1NOL3vMBrlY324kjlYMbSF7VUWMllgGQ
mB5y6hWk8AjaaV1d8LvSlTf40mWhk8MCcu8eCPYbw1C04DzfiCTubcUXwldHuU5N195U4Ak1
fi04294x3tdHVNfq+rk+btloZZmLoYJJFzWbA5P1i5AJ/fyYWAjx/iSQBAhBcE0L39+icvBv
mXHDomiOyDMbeNbdieaVtSz1GI/RObfK7rtX8J5yIQE9U3fYhMN+S6Tvy8F+Dz2Xdrv00hTQ
Rp6ujhfpQ/NGCAks8SqQwkwFfoU+U0GKSr+S1Z7qvtkQiddkeakWsy/60btvE6lG4lD39NDM
fLNG5xlmhgJVKM6d9lAK6+MVgqmR1jn+bsYHscs9CQd9ZuxbG68Ghx1sMAjZHqBsGABtp3dW
dhycrau8eg2n0HW+o1hi+JzDzClEdzXhEZ1T274zxuFiIiFwV052k4zIliGscJGdxIhDJkE+
FnWxQEMfm/rWvZFWF4x0zTyyTxIEQU2Yl2A8HFFnvwFc1+bHZfGDBelYj9GXw6lLhwDXtS9k
0BF/ZKdH0yQ9CzbrACCSH88qgmw0qDIN7S3glODvW82U9LOpvaaVZ+2dhl/S8IaIuYi23cng
75W+O0aES8rMZyB47TgnS/bE16JnK8/LGM4i4LJHEfbavHbrDtByqCCvUafroe2SqL2fnv8S
yTgBxH6u8XKpaQgg7J+TLqtaPoyWwRLPa6h6B9fcaYwaPnfLc94SJwxQtbhQ6gkHqdeOx/R5
EInzi2zCyfTdbbM5IONLATBevHNP4zqhheD+HuEAzCvdqJCyBgU33Sa0lI/RBDPPzVVKHcgK
u3U+AKqfMJ7gzFCWHinvki5LBbh+2hJt74t4nOvq7Dz5TsXdw3Bi3sHJxdxziup+dTo9vD98
PCzB0TlDm0mnxS9c17kyoxhyHDwFsLa9nGIt3TEvt/V66OHmzsWhh7RTvyucP/7yQ1T50B3L
s9UZ+yuaZ5SosPC9Ec1UFcYZDbu1a3t1OS355TWJjGEhB3t925TO9uauDF0Xl/rqUCwqgdR7
oXJPu7rXkkafWhccSEfQ2ZIF4BiQ+r4UM0SM6VEx1Ge8NL/GZ1bAniypNU+y6GNZ6HP5k8xC
KLpUKNJHt2xa/Yi4r2iPEjWvVpd3o36Md1TCfdVoD2x7ls/QH241TiXX+LljDbhOSkBa+/ZC
SIrbbP6rmoORFCkBDyCTdPSMVqmu2aqmvxT4MWkDXK8k0/EhdB+AmrP75Q+rhQOSz0hkgUQj
dXynuiMWBtwJvOdw9L12Rk2lIPehGyP4mQA1aHWTL7skFOttgnrmfiGAHG1QbdGGuFHAdICQ
96SL3mGStiU+yGAHZl52UQM2vxWYmk2la3X9dJOlVl9ye7/8DG3ZvasPhM0ccX/WePr2pl1G
UNNY22DHoqnFbYZvFrNMvZzyOLfNxPyTIUU3XNBH+tBbsoHEHj85UmXRPrs0tALnmtLf8xUF
yBUw/Lnk8+U88V5k59iTxg09Ub3qgUgJPM6U5cVfkJqmoENd0hRH6Sahz2KI90QsPsQMwyI1
d4KmhpoGli6oHfbJH0kbshEJ3JrSFUi1TDxDZ75IO1k94IMdcQFynen3NcRgeNs87Ro9coh7
Bid9wkaUWB56nWybykUjeDN38szx3e6RxbSe7AT31pyc/vTQhOwJ3zrTuZFXuSqMdZAx6a2a
52Yk1yUhItjE/mL7jtvLOYcH4BZegV/NX8wXtwRIk0L6ApTN6oAn3fHkEjpFYSOAQPL2JPh1
LuvsduGN2Hm2S4up61tzD9SJFnq0zBsJ16O9FvYAyMRddlDe4LDT3tZFo0dGaG/1u264R3ds
cKrKvJ/e8428wsFO6cQtiTq5NebmOoJjBb4dOeVmAYLWZe+z1c8bxwBnq3xaiGUayLTOOMa2
yY14j1sXJljBOsX7C4U3MtDSjR+dR8xzawZ3owz03JUpPe+KndoJuh565TWpU6Z7Bo7BFby3
QdDfzZwK0UB66JGTPKYczER+mjcDgKEIjynxOqRqM/phcH92OKe5Mjrw6ku8A7QZ/EjgdElE
VwtlVptwC8oVzUpcuvrqZWFTaqIFyMCir7vxUcsxtJKqQOXxnwdPRe7OdDusDff8lteJh1DV
DvoUB1BUJsheHkaZsdp1UPe48EApaAB7yVHHxubVyyF2FMrueEL7ceJ7vpu7TmPin9i5xKpG
UGLTOysKd263yPd7Gu4yWxmM6sG0MiYEyIM+SSOOlehv+4ajonhinj8Y9FgFecYWWXgDFBiC
kcKWJFm108Pv9oKRMXxdl7lKhQwc7FVG61dj7zJvJ5oaIy1Tz4W+wQpr28TnR0OrwkHnBg5k
4CXD5REnjrg6OsNbQnLnD0t6ufq6apVg0/r7R8ahpr0N7kZEM4ofpzK9r1Uc2jkSHL/2KVpV
5j+X5Fo8/DIkz9D2pw9c+FrFNQWw+QzWgP9neeTXi02oJI0Zm6oSpdlwf7gzUze5rTAWHCFk
Moq50zsNC72YVGJZ5NbJmNe8P7Jol9O7cjD8p63tvJCyDwwjrNnLlm7O90lA0CZs+rpnV0kf
x7j3iEger5ukmKeK0CV5CAk3o074/w1FvLKPv8qCoETMQo0vJDPmPV/I4M4NQb+p8bcLj2l5
qgE6rZehgbSKUuzylA/qhEXrAbUAq8yrXmjuybdyNMpkcMtHGn+Zl4XueTuBxA5yfgSAGOc1
1qPbW1+Z6e7IWgxsc1VDtb5QEyZPBJgsnfR7uEa9/8zwuLIz4amJS8MLL3QLOzkG+3fH6kPU
7lAWTjQsahuvf7+y3u/K/+XlugHtmwm4ToY8XCgTDM4BAHWbL8YMdmoCNQbXJs9X0WcRHQuy
DtfDgOPpraCVAxLeMV6eOJbt5+8WyeUq4JzVkZGL5pm8HUfEbsWVRPVVUF/TO98ty4tk95yy
D+UETa5q/GtHn2o/PGvtPDZ9Lb3TdM5ykyCaLvItsE0ARy9zt8UoiVInrriJYhEfngf4R56H
X2/4RUmzIA/F6eOmA+I2JW9aHXpekWTviVs2OWI3JWRVglWez+F45Ouy9yQBqtXVn/8sIcnK
vv5ZNODKer8nby9rKZOh61Rd6SrEzSsm7i0vciLfz/Cek0dRfW6UF8H7bV4Pkm+qe1C2QC0O
wxzyWIsds0qtEIZL0Jmgz/Ba2nBdp5hDmU7tjFnLkV14hIA6eL8a/EBTZwy33bu1pzCK4dyB
Zp+0s1s51g/J3qFq3q1vGmUDMKFNstoAsTdgjX1Jx5xz46rskiM8+qE9lZayZ3foyla/yp9q
HvieYFFAr1dvSaZZXw+eBixs3w6WMFK9Yl4Lc93in5gyHExk78o0/Nrvn0DScX3QWRJc47RD
kTHUDs8H8Q57Lp2EWYs7AJZG3MiVzYyffHqtz69V9D/B863s659HFq6s+Xvyx537n0XLDzOw
tMIIBXWKSZJrNfxT/JZ3K85w9nh3S8xk5tSk9RFh0QrIkW5c2+3dwij6sY2zq4akvDTu7XfE
u/bN8kAz6UkTU8v8G9SJHzdg9Cwq893BP+irst+KnFjV4pfCp24D0mxeapYIKUspaBBq/awz
rXnB2gfRtzbJD9qz0o6f6NuHZDM72nyQd0Big0JFv/T+ZxDENo8kvOd7snSif6iBS6Rf6URf
MgheOmnB3ZajA7InZPt73JvMfIngyvgBpBJ8HxheV3/+IG/aj+SE/Cx7q/iTFvaR0j7M5ucI
DtGmntg5qjyG6QumLIN+WLaM7oQR/eZpI814hG4KVbZ0PZBrZcVnx6LvpjSSRzJqn31H8kJP
i6fyAabDNpmeQcGTvSuqrRSV57vQ2aYZSCs8B7yn6tDKP62QN+guFFVOB5DKbpf0HOq8JsHm
ikJNOUchU9jjoITBypuSCNa0D/gUe1MrgAH55uiKll++iJH+9hjpQHWIeDaL3nc5ynWS0YFb
PBGE3KJcDDo8IwcgGV4Oq2W/59OP3sbhs/rVgv93zf8Yb9TvWRbjE8mXXiILMwKF/ZTUAILM
7YbjO7tH6AbFm8THuv2GaOc0odYd49kOZwoNjUx7yndqpMh1hYay+OX474ipoLysLjBnsnng
gG1lj3rGayNkz6niXw+u6wz63X/wBkvf6vpEOERIdYqnuLRrgfEcJwi+vT547AhmdHeMWyKJ
3L0rO8u7nR5rDX61vmJVHzuWvRWVC5ZD3Ys9fr4dKWfxir0704+Imv/4MerTkHjiUq3ClcEl
BdDozqEEY5xBGy0X/Hp9y1hq7BjNYNEWQUYLSZ7PZ+66D5V9tf7BqiF96YUt6PTsH3tnj79h
N4H3YdKA0I0D6f0mnD2nREPu6xyeKA/M7lF8N09E8sLpS7yvDv8GUfu5joK18/ZPKWXWVl5b
PvDfhShlJBfm+xe+Oqt7ucubwQE4+uz2CZ0FfEhVU68BLJCXL4AFouvEcYLul64ciICsCEXf
Avt9lqnM4CIKU7npZSBaZQbuHMoiCuz52OnnE120acuDFnT8VYB2xCO6rAVg6ykDkAlW84Rk
TvjVd7rOLQ68to9DqVcO8suRt0AyjKwLxfvNAptHm97zXfnhxj4f9fyeCwPS7/niKt4+ZY3X
Y3tvtJ1Yo9G/gc74HdTzys7Eu1tq6yd+RHgTFiPPH1cKT3aVwo1fT5r2e7CRt7Le78nr/rsg
IuGHEzH+JemviNK8U7I2+J5MQfCNjZfetWCFomykIPXQZ41cfLzs3a15q8biMBZi5eSrmuNd
u3O3Xxqq9iqa/erjQPpPhAuZkbz302NfIbBqHlcpDGMs7+3Z7PvQxcDbV8excYXPKEC4yiUg
ndzzVSP50gtbVDLu9Jwa9AjdzmtHG+B4zeXYqq8Ib2siWQVU2yzjbgzKV5a5jlq6Rs8/yFpM
1Oow0fNk2FuFO7zOvKyvAvPY/cZx0A9DAC0ecrhbs59Q3brROSU0TcGtLTPPwGN3vanKVB1L
iPQZYerCURMhUX0eoG39/ks2sRld9HmYJ0C3FU86dnT81aDHLQmXWaqDKWnKinpsAlOy/tGq
CduxOB3eOpz4dKqHDKmEgyXlwMXwEsF0DSJvfqfQqporCp/4Aw9t1cLKbjhIf8+3U6737XfZ
9wgkyZ+low3QMY4u8+gOyXHe1/vaVnT75YshpAsvdIV+dmv3INcuHJbv4fpRbV+t9xp1umO9
44FTHfYu0dvDAuMY1yyP4vE7965R+I9iU/3kwJCJUYS5nkfJQVOjIsc3Y7uutMLQu2GjrcU7
QhfS5PFwfne7NRr+rbguuaj70mKgXV+DEPoePZNFRMpATTgXDgngWhQeFx7r00/uLj4s1lTS
sFADON82Cq/qRHlm8HvGMA6rJDOuMkN70FVoEYIZsSD7kzsET5auqvlr4RMPVba+FWXTzNav
8kV7DjS0XGEtawfkci7otj6OhKTOWj/sYPBGWnwtUTw9KmeP4cfu9etdvyCJf+NyyRBwnL3d
qcuGu3o630cmU2G20/yDJLFpjqiMpwGYUJufBWpEP8zxQt/e8BsX0udDs9ZMkiIxKzaxpYo5
4jGz+6GXtbhOiwaEKqDdS9cEDnP/4rPhmG9ObcJSePsFmfV6F9vN8frWnBIZPys/7kjnhoh5
dkPSqWil7baJngbXH+lHdrM52Qu1SG6PELlo41ebnZbuZ2c+qJgxH/IB8Cuk/OoEp9ptY2za
HohSCDpT6RDy0LsPJG+rkQG/DGg7sYWolLEU17FDZVYdOM61MV2bVVJQs/yOD6Icli3vGW+x
pHeWvKNMIWOeZs4Grzql8eOi/A4NdJNA53ygZuy7m9FaDm23I68F/ODuUI0ww0/6FBeR9xz7
2Lv4E4EFig5Zw0dCXqOkHJlL5v01+T2jM4DLkk8mrKlVhaLzCOZERp91J51tzKF1AxvtWxtX
HwF/0fMLFfZALDZ35FwzeTtpEK0SaHcRa390LpPHp9Wj98BD6HoiW4VQ639JHTCiSMfzdhy6
vFbLP+Nx6wkoXzzAqpket5QUDIBcbz0C35NIrKbjTw6dCm72m51EbsW/KMsH35MpWTkborIB
w6eT8nzrv3XKsx8r1EhDeghSTZf49aQPHc0e8q4t62wZGPA87CqZjdw8dtEM2dErObWy/Qr5
U10FMCdLbRlJPnV1iEcMY5cb974EgAZav5ugj6B2Ddl6m5ixIizZWgkon0AIZWSq7gYqaMVN
vnhRmDtx0dYd9jKJnNDT5g24bELYJx81fdvqbsG6w+tRKDm2n/X8KGD+en53jar/fwjg1tz0
N8X/LtnEuqiiuiFKVH1yrGM8Q5N4BJIPa4ivqcNPwfheGpsdasXU9Ag960pzzr5zk9CfAby/
Z0CVAUIZQSuGJfBwjj/jdEgp6htXb1jwLlRTyzFgDZ8qI8LQecLuYwK4Cg/NgngVCPoMkFVx
L8g/gOCxWGoTsKKHleKnumttdV2zWEOxl62XklgREDJuBP1c1np7JqNWgk6Y055TwqMhpYDB
49DXKzv/4mUYxlKKJ6aUqCgFuHmyMthIUVEr9FdSU+H3mEMevlDAwd4GONjzpi/8RtM/ho3W
VMPy0NnLw7I/jpR7q9m0+03Wgx7r72w37WHNMdaVL6P7THCzzq8R22Fq+hYiGuxGvBe9Zli3
OsNu61efEalwfsQcaa8G8vVX3w6j+SQpflcWt0DsN0EQlqd4o0oDPy1DtSQ3qbuHGYE2O7PR
xuWhCyk0te1M9gm63cr5m3V3mypPhgZUWjXG/uA6z16UTJ29kQ4/MlA+5ZpfGy27v22JJcdL
DIZMX/db1XBFJ5+2XV7PNwHVo9Y0tGTsdXrVs6gC1gIpuMjyej27t3mUW5E8At3f8ynS/JWQ
90UPoddL7Flxgy9fVPTOarEyeTUlbee/5DdERhDe2lNlKwRIPu6l89j9S9dkxDwg7lwDuXa6
w66eGbuktdp/cUe96VH/5Rf9le/qFacL+V72/u5/kB/TY9o5P+jd+GbiXmNARIKRDF3LWBp8
V3IJ50AJwQ3Ym0qnlCccfhM4miY3K3B1ZR9iW0b8tVR5JppEVDq9j37428qlc6Yeiyee0cI1
Jd29FYvVziyZgyqqcmBNVo2v49jm4xvermy/Uv4068TXTs/cxdKW9HLRBPR37t1aQNIIWos+
eYD/rdbeS+WBcv0gMfS9KR3X7hKMhNwi34vzK2/xpcv8sCTPha8IhICTTwJsdG53u8oR8KM+
9qacy7oDj+9/4+BlTWD4AUhpByhpklmdAeRavhS0Ruc/xpFPzTeX5JINnrwSkC0/JAVKGMdR
w/8KJPd/lUnbcNtrC6rBQGG3fKH9IMzQrVN92GE4PSPDBeNl79AlVPIZtrbNgYXd+VI9WCT3
iYkKDMcyV4/px5onHBpgckePiayaoi2J6acztTS+sTKpDcM2HX2eo2PLcTu1q3Um6CekWN5i
4RvRAy4lYhip05Qc9jItDEW3LV/XfWJVF78WPpEE4CtXaq4kZff9Kalu4rLlhXfZbOlZgKzA
btomZOeMt8cM+tw0uWspQd7Aw7Jpfx1u8aHFnl/v8SeQMiIL89909WaRLZIqgZDJNwzmuvPz
mTmjVpGTikkl1lHPYABD5yCF8/U5uzXa/hn3ywKy0t36iOB04/QIFF5vvkfK3b6yMbV/5BFF
1mELX5XmqinQm0pn9TfK6ZwiqAyQ/U8TZEeszpJvfJX1tuENNL7idjJN6zB9HFTjuxFwSP7m
hPz3nj4VYBOmC72yfESOOFvSc6C6aeI9X95MOu/rvQDY7CDRasBaptitmlVyAJ0n8WzVEL/0
wkHv7NN60OxphCQ5kiZP8CY0wUIA33bBGGCRqsKLaFc6Z/gChE4vVfgPlq7R9Q/i1fjvetg2
B/rd9NcQ+z7piKIM9sP6PDzU+GF9pkDBDtv2rFmfp0SzLe7ZzTo866+3xpm0qhZfxtgCYTm8
/TJ/eTtxZl46vZyEILBzz79TBkCL1wnRsJne3N41s/iP4ic6gA8sfJd2cBAWZjqnkgrh5oTI
3tui+Ch/EXdxQEIDLV3nJkzOwauDf9r0wz/6/VN8iwu1sNWVPLVvWXigpe8IqQPu7+n47ZXA
JpakpbpIOX6gz0bVtLPsHWMQHVNL9l60i+pdo/cfZXNrKO06aY2L102KVjW0LMyZGU3D2wCA
W0cHWgY2UOIwpXYX88i+rgP5UXpNUAs1/71gEn4v3ayRaGQCGv3mzGfQrFRW/rwph7TEbNv1
xFMNjvb9cbxEc4aVFtEOuM/hm4ODVs7T+vUTRrH+sjFuhfbdyFQFZG9noayaoZ0TtXMy/fFu
sF7dDkItc6mZGMBg7HoGmLyCX1dgB/jt7Vb2sUL+xDPb5fHvcBzTQUz4BQoELSAgJse5j9Jt
7F33tQ+4LlwzpHy36Hs+pSYfdnfJDW4VEAk3ueIWX754AJ2F8vU/fq+94wrn5p07GJRuYvxS
Djg46CLmG82omzWyXz174zf9MhmLmKTro18LEYLW6PzH2PSqL+TzeqTEOjCztb05yac4DYvn
6K6ys8G0k/82Moz/ZbOXcxll9sV4cpN9vb88yle1jnfivIKh4paoRvBmN6p0v5ILlRsZHQ8b
FDyxajrWEeHtwxSP2HoMzn+mh2ZmG7rUbDdYORM0VHTIviunpmKI7IURPOY/7OsDqTfdsWM7
i9X/lMUPXjOlvxQ/cYsrtnEEL6pSCOrvjo/kibbVknjGe8m9Nwhw+XFl1zgjxuNF26mkRBsD
D9u3cznOPFXJo7/c4c8gHDiVta+tsN6GlgJesNy2Lgzgf3RqHNqQPhvicmgW96pjrw5x27f4
yedXGoeEstcq/OdbvlTN3IyKm69JQ1nUD+bcnmavD+bcisIP5twzY0dSK3AN2R31CdoN0U9c
2qNAhMCzk0BAp3Vn94aZVZMjXDoR8QwuSO2T72GA24tu5cR3NnMFaWqylcFdWqfHfHq9HFKG
ynVx37csWKVjbezf8z1Cb9+YvKqPXwuf6tsIeM+neV9O7h7vaGcco9NhAsqNlK4h7znYmELy
hKhpJ8Rzk181YNinINiqTX+urfD2ay0ax45dI+Y6KpCfqN9PckT5IwrF3/NtlmDUiorUq9zP
3uZMQEG2OVxWP8h0Ls3dxuIfC/p1gv8q/VG2GeeASJuu5EvqvmHZjt1SUjJFzgt7ncDq8sge
Qd3eCwSIFOvFtcN90FqWfFGqQXaXIaf+uIZzmm5VKObq1v3/vqVYxrT+znJOocWAyLJiwkHc
D648EROQZmY/chTzUjhptDbEGKJukTUWORf2In9T01ya1/NR3g6l3lWTB5W0Kk5wbQ5QC+kZ
yLrYOlUXOJ5Riuk9s8/jnOL2jkGHENheHf9sV7XG3BlLJQDx91sT/d+7+zRbmwy0/mYhsaZ1
RxbFkKry3F/oMsYcpWA7KZw42hgtcTy3mQ5scIrUbR6569Y9AE6dmwpXjfZLL2xXoWJMb/P8
NGwOQXv6/RIfDxjCu6fp3cCP0/WyzV+9W3TOy6uKbAp5ZHeBPhGwYx5wqLYHrVH6z3gAFHhz
rav5AOWafv+UPtQvnHn/EWaqOx84cNwSrh9NxdGIddnTVHvwtxVtSxIHlxXjF00hHfnnlVZP
jemIJck+scuqr+K6eKCfTFd1XQLyMilG1R8gFgdNKzRCpHclbfp5StyOYhAs6QOf0w7k3E4k
DCN79KY2bl8zyf8ofur72yfyuPNM5jQkVMuQ0gf3d3Vp45LQYlvp4Hvby99JaSkfr6Z4DmfT
kjqXn4QucbMo3ovPbR7+4yZ/iu9Kdoa4p3dysjxV5omFLogZFSJ7V3IidaBCPvpm2JaOQwOW
hM62tD1SpWu0/TOa225bn1s4l2AgxzkP4GteF0bg+hdJrh33D6ezoVV/sT3VraXESD44TgNM
vt9RlFMA+gISHN9/3X3PyqlZd6+IYhtR3EwneoIPtAWoGsIpx5cWkNVBFh4KAff6vB69mlCt
vJzpMEpAdkzTYeBAMbuVzVfInwgM0rzTF7aTfc7yVRxj5y4/o2wa+abLU87DR1P3j8cqFw73
DSUoDHhluUq4MuXO1uKnmvjIQStu8sWL/BiMSWesGipgMfG0ToC/koumZrMBHqqp2dKvuyh4
MmeLob7yIOZr8Ik1mv5BXscJyx0WhN3INkJ/aETM5GJKBuliaH1VHMb7NWDgUK6CJpofP96n
JuFG0VchHGpVNvRbHM8AiKC64+NZJxlB/z4dPWC4PZYqG9XNdnTKG/pxlJk6wmyeAZBUe1mn
FJU1CihRygNpSUQ9SK7W7cauIIuCVbOWKvN8V74WRjNe04dK8yER0uyB1a3sxfJYaGLcGChE
NDm5TW+6lQh/mrxs09j0HEeOnddRNEOvlwla1c2vhU99TTtfsohYbH3W+PNQUTpr4LkybywC
fsi7vkx4OJCQfxZUe7YWNxu8x+7Xjr98CUivfkzNlFgERG2Bo29nf2NJcdQhcTYT/bRRrOe/
w0v6fw9xA8vb6+S2yYrb5hhU0wiQXLMTqq5U1VrbQ82el5cVmyuHBDumRjvNUdYFebVo/Vh3
0OSNpKJ3LkU2OZWHI6Iej18ofPm0I9o9M46VXmikVnFpDKCyig9NpmzrHCk9hLn7nk+lZCvb
opLz8HPY7b9Vem5B0vJQiJ0ezqZkTLmpbJVrjZu37CY3cx9ec9ITkU/U0ey/RexdnFMr3vxd
ZmuEumImYRkw5W9abX3YLgDwjj5LvrYYQxukGmHDJJ6GcW+fjg6jyXXHs14hlwVFtBxvpo3l
Gbh4Kh9qAyAeCXvBezR6P7IeP83mx7djcVbc3a9Sl6NNmYgPe9N1/MK2ntZESTrq/I+7P9Lz
l3lZeZZKP/2kuUxDBqV1rGDMC+OVhXIAnuy3a9X5v3x7KyZmeqhwXHrdpmTdlLZ66CTluNrk
YhOfDv1gavgjLVHtYlr3Fq+n8Slx0xPx0whDViRv/6QwrWrEP7E4mxdW58jBkenw8k404qgo
QBSsYUUdpPZZDZuGbwFzdDuxeijmpMBspapVm2Nj8J06iAS+McvD3wWKrH04eGWGmLT7PR8L
LBnQGt0zrMa1KOEtlLqP9uyeG+HgAzw75ch147vKAb63QBFbvREymBkIr2LMLSSwg/uzkhpt
0NV0d50f/RemfcPZPCCnZbHUiBN4iHNwAGWATny7AOfR+QZmjzsPM7TJaYv85ZxInq1eR0IS
2u+t6szSqeHcgwiLodywZgDS3xHfwltuFoipGEQkdmXTbtamLQNaJRjVopFtQGpvbPHwj4H4
2PpGwGx+JY0qi7QSQDvhZLUleaeCLN4gZdylZf3mBWoCykobFK9u8rR3Ax1x29Tpb97wGmdS
WUGMcpxvvQOtoZcjJ1utDOB0mHQaguMRXbVpfIybZPyoGit8hOJ+OVx11xW/eMYAwW+oEOv/
ijF14+S/jwdYR9ZqsQ6/Ztfhp7040VPgi4jCjQBPPf+jplMSCcfdaBdJxf7+Ffrp2KTTggDb
5maJ1ScO5ZmR7HBCKyjw5LuZzHg82Kt/bHtdwPDBNOptdL5q8J4ehVDZh2sX79/Ln/zwT8MZ
w5ZPh2mVAACnUiIVQpfBhWQYJfeUfDxe4iO3/GNfBrzdj6Dwke+TFOXfBKDiB9yKsTMoJX1f
COk3vkRAEcDwPZYw31W014FkrqTnHxe6tHO2bvHhdvF3A425t9A2JUL1GwCAPMD7/5cFy7m/
0LBEH8xPh9ZlLju7Jih1jjiFaLX0txzNI4Gl+itTLw0PmtjXkzedqUsDOCmHD0QuQLdIj1Sq
bBm/MTc1854viAmyrai/6UGonzLUZBP4c0h1rYcB8ONUpN2iqytwtQ4gunjr5pQoau6cTKnD
C/c7NHPaAZpHgdlruUP2YNb9PttlBxxaRyxsuDPm8uyc4useb/+xOc5l0MHhuRitwOLq6cqu
7gAVzmXVjBHJe8s6xVXTrV1dbd4sJYD7zHvpbOpgIaaviy0F2EiHTrzFJzWYuHFilROFUSEX
82Fdd92mvFurF4BUunKXGt+Ob4F1Bbm5ey9V5wNXtrlA3tIKYV2Ppc6RTi0dzp0NLHVbWpY6
roas/V4kifa4OKp9CaQ7Fj2/yx2J9noTfAmRPiInAYJEvnQaVedl2tL6q1TBurJRkKmh93x+
vpjRIE5yuk54ZfSdBQgA/9SqnD8fCDFr0B+orsiMnnTLslzeDzo4/qiq+ZpmeRQs52U+ZLS3
CZ9BkGte0sQnAhcWjtTa7VJbsBmMxEb1m6fb5hC83/Mdfug25es0mIGJ6rHoRp8ivAAufS2S
35CtE9c0q53qZbUsvQ7gdZoUyaLhix90Lkmf8wcuCeNrrQSc/Z/Z7jfnfduyTJzfdZhcC+ff
onUHYNJTctWEEtQhm59r6D/gKlylZNjioaX59s3tt11b2Kaq1tmOeOEh0IHQGf+ZG8Y+31dV
Zt4XaQ8zYnujaNy6QuunGTpalzMhpeEucbNvDJvM9JZLNi+/2yTw+w+RuFzrtoVLr9FPEvB9
nq+Oaf3o0JYZRdvRlVFfmHFlPGk8waH4Pd+Y4fOzZ1ISAu+9QXwt9vDvHW1Q8s2eS+iQafpb
FrX58bmDfbbvMnvu0NZH/vtMmRuuLhCa7Vs3aCIfA8CwJIq3vFzr/KFz997zSTFfdcJVnGGq
PFNfq5phhAuCcr4mlZy1o8CvhJ6+frU5fceSu6WvO+gJ/Na+5eFJx5mi4suM8SYtxnVDxD1m
0I+7fn8S+Pg+EVDNJwiKm6fgFtQIBj8/cNfWQ2wx7gV+2AR+kwb9Y/f5Iq7zY7AKUEpxUdAV
5LnBAY1rgy6eIBveZhp5G5vWW7V6Ywko9OkmlceRm6dDrnmOhFmAhTXRTluZ5Gy4w7t7l2wj
1HFvPads8a+zA02WpTPY8LkO3fNnLZGyS2/wg89f+pJTWsHt7icLCU2UxA7e2any1NH8TOzP
dcGeBqdL3MaXDsNCmhFaDQaDlYL5ujuP52TWFhR4QHKfXeIZnnc1bUIkdBQTCbfM2FovPQbL
hLp8Lg5nBBJbbzZNjre/53t7nSUtXvgUyyX2/Yj0bQY/DGbNxRzHASlGiw++59MaB789meWU
Eqviiy7SjCgTBgWfbz7ILrgqspAd9qC0sXYxs6wDdGPYzdbvjcA11xTwLqehLod2VaTI7aIS
+tci3dmhgWbYWM8yF9N5LT8j2/v8RYS37FCVWZoufRwVcpoMm7krUi4tyvqJkxtnLYN91Nnq
tLgoSJIW1dgOXKFr6d4BQt/ulaqlj7plAll3FcNkKigZ6Jhg8+Rb8eQXwy5vEFIgp6XLanKP
Yhiw+GW5tvZoIEe3ycqcvNzIW8o9A4UpM4H06Pd8WMHxxlPWB7Esg2PtvlzBd2lYYvweWseo
f57cEKfMVRxwP+VDusl7aBaj18vilvxlNPbZnnp8ATfVuqe7czTs9YUlDykNX9tTwXcgg3dR
LtZbCiDmsfHGURVunadTNVlyosPG6mrmB8i9jdc1DqTFZWTsze7uPxgWx+hwqPlKKt/fSZmk
UXir+nVNGd6Y+twxEX4/3q8og5LPBblg1xW5zOjXQv0yLhO3iJuYQbdtp4q/3UQewsUn75o7
V0aUYoUU8kQ6USJJsO/IVnCPc9VxDPVsisyFZIpqq6yUlUHAzJs3Qlm/+5itewzvRz0rgMzn
QjlKmvJOhmjl7B3o61TQ9tr1v5CV/3d5/fjNrb1yGZalvS2xRraPbEn4QZhsj4nxBlVuZsw6
/fmkUpzYz264qO3MB/Rz5lVYrHKiHwDajjuxcvxA+k0xE3POuAYhFzD5pmpEmGQumgww9EnG
Xk50k7VopRUtPw1sxLc5UDPEqJ7YjLGsJuviZG+3qiCWm6nPlg8hMx7uFApa0eGXLgoYc9ty
7YfGi++PJuC6ghwWKIq7jhUO9N1MBxz6p594T6rWFZFvbL5xYq2i/5Tut7o5JIRdG/YgmYHM
ec7k2RCe6V/Y+XL6KL2+lpXVVpfrxXjUJKM1Hg4wpgpqU0Fil8OSm/5imqSkw9Z0WpjoDXxr
O732fnx8OtqJxt8HeNYTxFw6EEVdzsvD62H+J7okDutf03LUN5HmWA80HWrtiCt0cdz7NDQu
AeBaHxM2Ka8eNsWJHc03sRa/3MFL6lCyjM+YisWPUaH9cdg781cQyWLhKPWigxiudY38gU05
Q6cSQVLezmXj/n615LHDtuv25+Iv75S0f5Z1ZO/T5CYQRC/X1iWtezQ0vF9e/kB2wuhD3dWW
tb8PfMOZhTfci1exY46Zi1ZXz4CSd9fMzuUU6vYNv6U98GjrECXgOpodFCHN+ZNXXJnyJAP5
okAtJdg2CFwx7SljHLp14wGI+oPMVumBeBsJBLEMgiH67E7D1tkeScjTG7Py6xv2QCs8YYFE
Gt7zOfidbDu6GFVG+nbvVY2p7uqwWbhouj1woDwx9MwVrm6mN+CyCLMPTBbUF0dWC04l3p+I
nIcZmczhCkBBH4a7vbalclvpsMIlp0UkV+pSR24vczZgZ7t3T/c07y2Qw21qszMnfjrljdU0
R1f4CIveORTrbkWfCrAmlZ45+u/TIZr1WN2ucW0tAONYM+1lLQzDwPGJMkz/K6Uiawcqpoos
Yl8kn5AdeKGwA3khyVIlj53TtvXp36f1r1+yktkUACCTmdzcmeaCtZcrUF4cy79jQ2jU2ExS
M+suNPd7FGsNveZIhKOgNB5X99Xd8yubr5Q/9eS25E3wS3rUWMFtLvn2KMFG/YnKhH9a/RRw
Jt4pGLSywy9cFrhJa296MtmNMM1AnJaPj0E5tUwfhsIGN2ydz6JMDc9VPj92mBO54Y7D3pG3
DfHRHlNdQbYP1+r8z8EAeVT02Tmwdxe7fYOgT8HcZB+2FX997iS6dG03fHwClUvJQ4hbD6hX
Z6cqe9psbsZi+rqbFhK36w2NXVORJm3taqw20U1RJKj0tm6R+S7c5fGBbVfpDQ5FHt5bMLGY
aPP4LOc56IXjLWMZJA1bStrTaeAkYBPhWNJc7jeS7wMFDvhqFP3zkgY1RzSKtYZ77EwL1Uk1
Pt1lOFN9EsKDRhS3pQDLM0alf/6cuCHkut/evQhDQ1MzqKHQb3igxKoz4mbrBIY9LuJq/UKZ
LkGB0MQQSPWldozjoMDZLMtzqYMLhyyQiR+sp3cQER6dS7r+EFx7TQp4/0HXrJJH19Pdp7b3
UHJzZrMoOJc8Iz93irUyLGWg0TkOe8QZI9kodGta5UnP0d2l07hvBwRruxMFtp3uUu3BS1Q8
eepoWZNyaNAqBxZiVGwxGrlgkeGQ790fNwsJFyjsGS2vv/mUK+Y13cF667LkyWq7K6p4JLVH
U7MJFOxwaciPi7OKYzD9xoRsm7XOexNCto25Szlf45J72RHrAPzuPeIZzYQi6zmqnn+yIHTK
3VoGNXxBPXbZybscIz11VfYYIrAiP62VVbhVLNHqjvfEywG2wE9SFIn9s3ADUBeTqSs8f937
Bun0y0FU8IvFMUeAyTeI830hAy7+/YYshfTI7ajgNO/j9nLDV6aEUYP8/ubjDjdlU10CGy6E
LmV23sDWbMhW9ZXqjFpWnx/IisPxpGfOjpBHc/ZYj0Rj3Qiy7RxbWkGOQSylTWKEkDv68kdZ
c624OWBoWTMDwNBoEcDQ2mbF5Adsjz6wHVawLu0q/pG2rcD3sMq2dzsII0JSkm8nA3xhvQGa
zNE0lFYGrvhNI8BvPzEIrmP8VNKS855v/+cQa27va+m8EMHxbtNGl830uWnlymMtm3KPmPTw
8Mzr9jrBziapsx6vr5x1nrYfpuXHdHLUfLsZvOcyq5gVRHPfdDveKSxzay9wh/VSnoxeW4qG
ZUnMTODJjJMGSQrzWvnufi8jkbrsyx2orCSYh8UzqZc6KPrihvmg3z5Nf73yqX4afkylaWBA
xUh0GLNf25+cZsU+fGQrvmZzUE52OQcBSwmE7U97ynIoUDvxkRt9iZevNR7b9cRCVonzfctT
Rp8z+4hlTSTNZt6Oljm7DgvXGZtJbNhw/K8BychzQEAy/Fkn76jk3d9o+s9CZv+Zc2dtRwK1
1yKGam8VN0xPKIY8MKDobu1iEXEu6vZyikbV9I5Epiv2m+VoQ46bSX+GPP/pB2f7WpW5WgV0
9+FY/KXRhKyMI9BHUzqbPM3ls27qpqSHK+mbwYZwTYeswouFi3fGxU0r3h0eyRDSFb8WMObd
1VlkiN4nmGRtfG0os7byCsb75LvUpaOqGeM/NIqgbHQc2QnqibLeuwFzz74Rv5HwgIX0RZ6T
YSmm0E7WbGH9CE5lSMetK1abR8UNoAWr1OSSklFzIGh51oItuuP5fp7IQyTaGn3+WWPMjEK4
OIubuXUSSX+Oghzt1s8FnULO3M9+z5d/sQ5DeigLoBieMp2qGKK61B5mOvUAu03wHsPmcbwp
Lamx7qbt/+PuzeOavLZwYZQKrVbQMimjlRZUpiLzFLSCOAApQojMCsooRMZAGKJyLJMQLVVm
olAJJBJEhhAgBBGIzGAIU0LCPIcxEEgIfum537kX7WmP/e757u/nlT+y9mvetffa2e9+997r
Wc8aWa14yx0UHjaKLfLveti3lVky0NLPzwJ2RUekAGecQesCLbjQxLbOrjOKmrr42z/iu6+E
J0bWdfGTb6ZgJZ70kYdRoGehGvhVmKlWaKQ+Z3vnjE/MDcNfGEih4or2HJcdiJgLc2NE+tfl
ksIdrxZ/9Wunlrj+0hWm0cd6U/aEHmnfMkE0o2t2qFBDAOcln5LOkfQTrSt1tEtCZYkb4DLD
necfq13Gvxdo34Lsh67zz/D9O+O580/JmIfWkcEAl9fR5GAis/pn0+USQWtDyFoNLOrkiG6x
FqAY9uTraOpIH6oAYSyxpX8wZ3FeOiSadseXTFbMvVSb/VULO3RYHbB4QUexQJT/q+lLQIdp
hpbwU/zte+00Oir7AIb33TvT54LsNWzEPJL94L1A7ZAp62WEhmyE1zhEbTDTGtmcnLaV87bf
34Vw16JJ1ZJ4Pq+XLNEV5Yc7nkt2Mf1eU4vReAA3i5jSeSO6bIhqyLj265n/d1iKZhZTsUZg
cx2LrpSRAmwFa2xonN5MKrWqPpX8TOpUXnz86tSEmWUjbOdrbn1p3Y+L1JqWrq8wFS46jf5t
4u1kk+1AkI3moqVl5B12/d9fNV6Jc7zMok+VQJwSVgYG0iWnB1kb0W4N+4qCYhFHaotuhw1r
Dp0aqJbrKntdAebjbe/sepoEW/C4Vhby1PZ14miH2NY/+gsLCnPJEqC7sHRusAAa8EDf7mbw
9WI3tFGn/NsuIrAzo70hfxF8rOZP142fCJAWOKGBzkUGH8g14T1yezvtMbMlHnm4wMOJWzkh
VfEqON92MFPouRj9NKvWaQXAR3tkbD+d2t3wXTZ8lmKEqP7Rw0mtaUewIJNatWSsE9dYpXzn
JxDcHKMJzSSQnEmtlfLRge8FgPV84ozqkY+NFGL8hD5Z34IuYh72xGcsu5cMdBUBTvITn4p9
7Br4yzXnx2oFBHzoJFJLwYm3pQFMTZMxlYJT8cgQBfGRUdtV/TDFAZwAN0ny5JaMtkWppeDi
yQJj/invHd4ftOy5YhJoau+szHFA70jJyik+AbxQ6JusHy59DZ8T3nq23dHz2KJJowP43ESh
51WJ29KMayp+ZIMFEZ6YJsYymhjlwhgnvhfYVG0yhWl6rtYd/ugMPxNWS4/XZHbltC3LCJ2w
c1GAZtMv5QdsMwij+HDkWgLgqfU6M/P3XylPZhP9fuVKMzN2lPaUWDiLyAHb9A9WzW7oRIpt
fylUIQcJdzFVrh8myzc/R5g+lO5drxkV30bu04uKPFpVtnUWA3RK+RrYsgyBkUofJZi+ESo2
8a+SM1VukFuXbwoP3vbW8Zn3qXfYUheDzGwo7oenCD03ubUVzUvbv3lfvqn25M5PBy/BBlbn
uepHAqVNHkQd3bny5Ve9Upn+jzpwUiHqxxZMDji/u81Hlnidr/EC4zyTKlzyVZQWKJaOeOdw
wEGOB4nf71GuZ5wY1iWnsRK8U4TN4ZELI39/XrABgv1h9NJOVwyqx9nKUT72+QhYvpziG2QU
OXgYMKMefFcmJgwpuBlR4UWMlvH1MYxir+7ExvkiRmIJu3/RvSah+/oLqdkZgW4/YYlC6jMx
D5fWViFOpHi258IZlfk8QKy1hXT4/WpjBXlkBfOauWv5jZvUEhzP0WTE+U/niU/cX4r79UkB
HwBuB9xoMiGYVmrTErZ4BevEsde3aXjfMuzqegMvoCgj55ynd4Yt471AQqxnSauo2e7mf+by
nhHj7blHvwVBmrKr0b8viWuSGNs6IY5M7jIYapYjrxHYBffbEUWI+pDjRmH05AzPOsYcoFvd
+GO7+b7EGexUVlrAsBYIdBV/+LDclNdrpPjee9XOERu3u+b767eeEkf4d/2dhdjHlfyPsqjK
eJeq8eEpN6t3LPrpW9U61SFOOA0f9kwrIRkuHWBm/rZgMrMI8xp9EkXQ0rLs0O4KYDXWhxe7
nIj4Dql8sOJSdHITcntGGz1r0GK8pQ9/YbsQIMuY3oMCXwy4NLd6KzkM6XH7Zozj3efgiyKX
51b9TZqApSUTMQ5CyS7HI7QxLTi2OaCZAF2t1/ab3dfS4WqlAbVZ8KuIcdzzzM2iDojekjF6
h/BwRrR5S+uwgidFSh69ZYREi1T4rQ4I0euSnX+jrBqSDhVy5LwUVscFIW7n5e1UtuR6GtGA
OPCb7apfDhKiJbbsSyagJHH+l8DA7aoroshOu0mPHdNA8PY8Cn5WkO8VuMr3CtD4aZMNZxnd
Z91MzkU4jfI5lKOudVfB3+R43J4zDCuqfDGvh52PkNRwLViPcNAtyPTswNg1yR9MVC4na9G9
SBPxB6CzlClQA/E5mChT+5Xs194RWWu/jJFwydAVbn2unMh7AXvnqxyH5zFSxyRp//bn+Dqa
k36zGdOlIYb1aKQhrXyqesRJEZnFs+mVU4rTbNTL03sbmvMPiDTLFTLNk+yGCgChmocVbkvX
79aWEG1XdqJpAgIfQEdau/DkO0wBHnZNJYs2x5JMDmr6YDQebJGBKcMEom8Gcw5ksKbJHdj3
70/W+Vo/eat1keejao71011/i0i7Zbl/eicHyU+J7Zv9jPEgxW7TKEiZ6J/wzGZDX9dn+876
B+3d3fbPUD7shFYyD6clrahjQjskwNLmdStzTY6VspaRpfQ9hziy15si45I4cRC5bBPJdmBP
f5pp073BMx8bKuNvXc2cxUPVKNoUq6RUMbEh96ijK/UnVJ6TkF5f7xCiRDMP/E5Y/JdIo4+V
/sfyfrd5N9+JYJWykg4xyfmBAZYtuEjr6FaZ5mK4zdK9Jlj4VQKiBbK/mIEDSVgjgqoSEAOU
VBjaazghgX32+Ou/Hx2IQEh51h0Ple1ntbca6/eG41Zkyje3VUJ8HyUDl7zvfIQfO4ZzkAsj
KP4a5QLI5VUQGKhrFGpfQSefy1uhxn1PN+e4969XRxUOs2VthmqZpORYHdiKh6RK/HuBF8C6
A9//mfWfSiqwN9NwcFbLK10NgQ3LHYzUfWD9XmAkOMh3x1jy7Nsn+dIo5drvWhJrNmW8pBS2
f7UijggO1/9ZnZ/h9XM7L472JLSoL5Eya6wDnv12FYGkGlK6xl7LGkpfd80XezCUbLdzP2yK
UWbuSrA7H0WRXw+5R/5DD/yVj+Wvwgf/do+J/xeTdAgBjE+xrI+ty3dXqJ7Kq+oNJ0gT4aqg
gGT7IF/e5OmPIq/3hYWW9c5UtO009xSUIFrp2pNmsBW/A0oZSD4QOTZ9BodybZx0uz3lihtp
DtvqqPEtycRZSx6U22nNHKd9wf0zSz95nD43HBtpIlAbXC7jUnZyMANLOyKLOm7Ne2+ENHXW
FAbpvJFhTxPsHCmq8CSIXVsekk4W+PXan9X6GV4/hnDwdyzW+7XYSIQ/TbhMo8ZA1L4Ht2oY
Ye2CBSwLsnu/kH7ci3CAcXGXn7QXH35y6dSOEfPe2z+Y+jmO1T35aY/OK6kt1KQOJenO4e22
Z1JW+ZSvPmPWpXxXUlErOgBkAHsCAoHGM9D0rMfQ2u0dFlvo7LHdxu99AZv0hc68GaEjzLu6
IS79rwJs5ilm18hm3H4V9mvFauBsiM/2L8yvq32YhrnPMJMgQG1zKNWFN2+ztPfabk275U9e
OoBMgv2j4PsgTVrjyU1mXZDnZIWws8rVdpPNFopU/jsTfmnSTxI1De19pbJz5Pv63XV85vL+
jXm3x1aylbcW1HeMasblFyw68/l51eIEKDPPPTMjrg/j5WpDl2jVygMoYD0/WcTrP9j7f27I
vu6r4w3hfxmsIrtFhm0ATFp91tGY36NS53zYd92HjVchN1ddGrLwEpsg23ywrzJ36LQ6mQ/P
Ih/66pu/vxQW/C2w63bzuxHkIahze6N3jZN9rxHpiYnwN8yukXtp1eZMjk5ucEj0pWrjk90h
arY/FcR4+pbNxuxsmJGqDwx80E0SX/VxXfIVE7I1qZpusGVtVdosqu/Bg0TvBHa0Gj+iz8Ja
ToiAa9E7oM3N4dLJr8q2Yyqt/bfjueBr31h+oGlX4RNBGPu75+HPzRell984LUeFZ06FqQKL
Z6pYICoPOCRcyIqi5NtMbPTJgvjhKx1F/PCV4THKImO+bkBpeVddn7u4v3Oevy/0iDPW6DbW
SGnvW1s7jnRVHchLeS8wP84QRrOie2bJBsalWeJhOU7BvhGpgFrSM4elHRSu6qs/4hKoviEd
sACXw5p0jNRxo3azqAdbnlE/7d8/Gzg9+Ma0xE1w6h7fOfcf4Gt/t0v/u6lAVlJCdAy1c69U
ER8HFRaoDGZi9SLWlzzAvooM7B4wT6Kci9vKHTZEPLMcbBwYDLGKea7Tj4wdIdWI9y/tna3f
3fh9SutP2/NVMpn7m8Togbq6+zLrQjoDQuFBVfvQq7Fx1sKnouRJeUjhuubuxfYw3uNwewwS
Zxfbf2a3kl3yJ0b5CZS4Vh4pdVOj6unhUvrYpb7KM8taypsC/TOosFOT8LCrS+P5MVOgRWvk
3Z2WfXfv7KrhcxfRAfi0IozyvYEVgOEJmg4/0h0FjOcOfvF81iHJ2lQxS4hl4dP6tk+9qyu9
d9V7R+D7px9bLOhf1O9C0FOfrC7ILCoNcnePtATGAvT37fsYSfBXPriPlf6n8n8XAGfeiTJ8
zlN+1Knk1oQfcSZ4WTYtzZOhtk15VWxv9NNzMXGOVjXUsiTYBFleXinnN3czTg9s0cpWYU6R
vq/izu7G7hefI2CH+wyodH2p41FyYoIX63Hjq2R9XUjXUknvAdIoNu78wGgfhWpfmHjiXYil
rLQP4ora1bx4BD321W5Fu+VPXnsIwjpmoVpb1u9OzyxRrehDMSD4Of2MJ3XMAWHQzKPCJvqX
K4IXl2vDqegHCQinHk012+2fVG/vruozl/edWydSfAiNAVIzj8Akd++MLVv5chdiQO57gTkv
+hdjs/h80LOgiw20UzXsmrtpGePrr7ReacCPfKX6B8P/arj+759U7qquAFsZpmZL4iWnips5
48uKfg9TLcimZcSzldCE5aukb49sBOL1R3VqJMcSvQIG8ZoKOvwFsB23TAswY8L62wwZX6jN
zWN7fgvywvis94904rCz4eKkDis9L0UcAaG1KNhkKDcjMc5UVwtIWBrxlU5JvQssZsj3WQVv
tkc/dZjZ1XABAVIXMnMJQo/ST0DNUsyha6HbJvL9GM73tVFRAYybFtduSJhr91jaWIYlepRb
dAp3f3DzrsInnskfWsMoIY9mpy6+yEDVjvjCrM2iFree8BPoHPlyqbvfhhBsNa6Uyt/GI+Bn
3+aZ1uGtQ3WiMXb33tXvqupzF68QHV9g0gzyhgbqErQCmt+8QZ9cP46u+HpnbbHRdmlvN17z
NQo4qfGPIyzyEP9dzD9dCpvSkVJeurvwh174qwOLLyBzMk1ys68Xr+AK1kc3iu3TsDb6+vZa
3nmZmNLz510w4FN5pxLiMd3z2OOR0ITclSH37yQUP3YBfmJn97S2NTWU2VsHWL2ItNt+3FbR
JE4q0xoTdu4NL3pz8LhSaIAiM+oEqs1AutmkjnHTWRAzGWzTJnlwsDSrHfK1qguqzbxjGEW2
i0yFVukv5AZuWTcmZPFjfIawjIoA58vISOfYO7187/9E/6WEbOx13Ypo4ki/+o2Y/Yk1sS9u
hP444SY/aY8ef6xDASZGiwb4Ukh4zaSh6OXAQRd7AwVSQpazXVcLc86RmvkAyjUSjy3xjXbb
MqxPyHbmjRZurJ7XjdPm0yapuAjMg6spQRXmIFu/63xIlM8KaEUDGI+E6xGHhOXS+trSMo9H
KzbQj7sibXtujVC5GRKCxXM5t8PhvspjGgJsETtObmbfLQ82Vwa6pz8gtKOEJBlxjZ8sqHiW
wYSZyQZ4Oft3OAN/Mwgmq3YVzVCfTDLwyRcM+4r6GMnsvJjjy3APd2DRLCYjQq6uefKlWaeP
QcmYsi4Xd5HubNFTOZWVle/DEFPlz/slgxWgEnPsNCxvfb5MB4qNCtSUqwkn/ORq+u2OV9T3
GxWIrbNLx/52ALwKozjmpngQpax8C4kg1AUumUXN/aDlDv9KgDPzPM6qzoEdA48dquFOK/V2
QdS0r11rj66ekPz6g1GiudLrkx8SqkL0ZAaH9aFIX5XRvYiRofP0ry1KR9otXn50WrX73k8+
Yjq1fp6EUXwU8324uBXIaRMRXA57JF2pEMFWrDqudy6q1bs//DUfCUtv7NHgW6DSjhjfc+va
7po+c/nE/AtXlDVcr9ydDI4gVxZkJWvOW9KI0M2BfXVBPc/p3VuBo/ZJj1ZpB1OfjTuv8GkR
frhFNg34Tv6XPxj+V29JMwAm5oYRmR3waPn+HdDSZQSg8ygPtqmgLfUBpO4POndf2IuqHp13
LPczPkEtnzMQn33sPpdR4W7ekgRiJC7YWLUWrVrZWFIOa43Ho7HDtScXDwNjow0NkOOVje/C
015uLCa7DvfN1thLurqWerbTkqB+FW6R0VPVkeCAqhWyHBeasqJ5jLUNSM6mTjRaMYFxmzm8
y0MdW8yNI+uCqbget0w+qJyw3jAECJmr/kfXUIPwtXccxRX0gkUTVvNWtsN6tIqXhiJu0OaW
XKrYs+YJbDqLrVntn7Hu3jeIDwLQrY7NODvN3n9dJzja7CUVMUONDEIXsi6Hp1VWgIM1bOco
EEn6TTDWDJqyZiVGrd2ruiT3qHWD3lkTizO4R88qOJHC8rx+e64PoNOynhcUagT1GK6Yi82z
FhYhaI2cn6XFpC2tdsVLGgMY52Y7GXXCsEGuxuPhSN1OkanxDQ5VM3hidTU82ENZur9MV8cR
24X3Pauib0EWuysLJSXRlKbJZ2l6BNEedENZebSo7rA8cP+UGo0DsVEAoI/JP/N7lqsaVZPR
VhEt0pEYs3grNhTyrO6ugvrUuZ8wM2EEfsjuqYcBxSyjwdJV+nUddF0chJ9rePaL76fLHpsQ
W6XEtNXlZiJrfqIFo73t/MBBqyuFpSPhEVIvyAGZJzNWYV+0t3chGuKZcrXXg6LuePYUBvHz
RWzMoNNRZ/NIPuvMYWwCMswn44t7QlrbbbS8JU0aqCYgkuy60e9bEB2ezfdCuvxnL+TeEs64
Hy5wg/TlRocmIA6JfOFFmTe3VxvrAY7rCNKqLbxDfIzTvTNYNuKdFcVzeAqQvxbiCRIJ7oq0
Lzp3D0XhiXYz6EOP8RZ+0FWTesyGUmlqgC/Glq7H3mdHmUws7qC9RXoqMeC3/yIe5VMj+ITv
rK08t32xGtiUbVi0nEen16RRpwewWT2mc69dCN+EppeSrHi4Wg35gHcP6HTiU0+HfCLPg3lv
YneDP3f5J1O7Be5g7erK/o6h7VM/FHtvbtSFmn6z4pfOPTW3b8VfzTBH0de72kp8U3vUZ3Ng
Rb7cJiATfszg2seG/6Wb8cMI5v+QgPVjzf8qfxigqmXosZV8+822SNFywdXvDxlTk4zfLive
TacwxogSujv0GiviedT+HTvnDrxFCUSScR82EX3wmy8vNotUOGt0+xILlm1/zqybe5uHLiYX
zkt5WL9ZjfJvVWsEwyZN+LElzg5IjQeHMPE557b6p6Ts8v1marpsesavoLPCOfLNb/AJYcxA
eqSNC75EvW6Fjy71VFJsmRT+toGeFjUemIjvryAUI8pKy4iv0J3DWxVX3xJAwVp2FPfEgBvk
YArSHGcRgdT4VUz0OuvCqK7kPrFGuuZih4dhJAjcaBzlb9hhSt8gnDcHRUvBIjndopdR+e8F
lAMTZn1e0yWcmVSyGBaYB13nhsuLwlfOTjsx8oBCZct+KXKBseEzGWXg+1aOTQ/8LzVawB8t
q9kgwKlNjDe5DOND5ORhbXzJ5NjS1Juz7+A6HPsM2OkX8zKXmNSMq7n7AnUX+xF8eO1cSo8z
JUClIIWs5Ry2KHp20hbjJanvAj/gvbJEdnov4Ntk57iJcrFZ8RNi+HoQ84DebfHxGek1gAQt
u52koeMPnaYPhJe9ydXx/9qK3cCj3q3Sdq5CCCtKElMq3LwzcGG0DSzlbQI/GEecIjdeK4j7
T0dleSenLBJZZLk8veaaw4e5dcvK0HNtv57fGCMUYdOxxSqX0SeXxtOT+rldVETMnoB/jZcP
Pk9ZYJVKzJnjDdFCpza3TbRA/+Rog8rHI9fFlvZ6hbS9C9IOsKjySH4MjA3aAOSnLfREXmnF
m/Huh9z7AOYk+A+GNIWAe4UTGiM420Iuv1td80VHX6jwRU/BYfuVZ8H5N3xrl29Z8pEe9qwX
/m58LrnO/LEw80JkWc0ZjfYPGrW78KnQSmNEVjssKMJ2XKI6v/Z8Y39AZPkIHQ0YOYXJW7TS
NSjuZ1puZCcnIQMAUc1hB91e7xu4s7uaz1wmtRW6gKFgE+cLjQ2b3EHDZsmcABPYTCOp7PAS
eeCokK0l/+/wWDxT4I+4xb86UDiuACKelpvl4i5s/lh/iv0RhOLTOu1DXKSYVoFpev/XpvVz
yP037xXrr3X1G9S6M4awbxqHDTfe4SKvllg2DtV4JpBaK2DqHehAT2Y6q4NbBvY9hXqTjsby
+MF8v8l0ioWUTLGT0vznjdIg7reiTU97v8VnVJ+eeoAp7wfDpt/1jdWshCnWdugV4eieig0I
2Xor+qEQTz7Rgbf5C7paQDE8/mh5k02w9LDtc591KFJqJsw3a0fcIomY3whMiTqyYvYFZbTr
S31wg5puseL9bWMq101yGmKOukxmjlNi3I8fx1SQ5SVaa8yiQoO1xlZjfyek3iu9Fkk2+ocx
iVwIUcsyT37UqJqQRfEN7yu4XSGT6zoYzmq3uA9GEOajMUsACdeEoZP77NuDvchpSe8Fdr4t
X7/8GB73Tk9IrZrYws9vDu7EQ3pM10O39vZGnJ/ze0131wzcaOa0vBlwWkyyBdFkaekoQaPX
W6dWglSYctwo6NN+TWdoekGAudbV3/EeLTiohSbX1ujWPCesJNnvxvhVfKTwKbq5uPOD7cFM
JbSS+6l4dAZzkqk5f6+lOjTi8e2SWdBS89JeC0Fpec/tiapS5rjLdsyyMuQcVRfNkLUnapvR
8i+RTxRg6foFELcMBPQ1gp9J9ti/GwYnnYrPh0K38qhHNMM86epNb5CCvQXVZWUFXsPx+fQ7
jspKsFBpt5PZCs04SzPwK9YDZNiimpQXs//YxgfTSoSynsF7AbEI+3Ehtzyr6nwPv19t7IA+
ifMNNVYmqP4lu71FME2fjTWDl31BKgVKt8POx5grGHpp7WfQ8H8B2P7Uw/mZ7ZAeH1r24THJ
YTRif46t79yALbBEKlC9h8quL1B/JM2nnjJwdJWlDIW6CNo1xq9PqTUtMuZiujXs/l2vfKbX
+CAOM5bVaG+qQ0Mb0w0V3mafQ22jDxuSnvLTlVgKHhv5g13SEZLeLaXB8hPttmEJeVi6K1nu
LsJCMtyClJJDe+MDy9UNDR8ccjVv5xXjNRfeC7jPVREKEnd0IxtBI85Z0BcgLW2OcsA6P0y3
T+rbljgDrlRWcdLsgsLZd9DcVN/4/vKjeDpGB5jUs8Be6XcvWgU+yUAKlSj4FH53VUDgyzgK
pD0OFsN8Bzj0cj/hY3fWHxorEGPZGHFDGnx6RS0Kp0RRMHc+owtlq9Oa3wuEzHP8sQy9xwHI
mmNjq1U5b27J7+SMSQ6RmJMsFyd5RM1VfUv69ao9BezNfJK6gvvGKgcw1ZCPI96WBTkPBpUC
0zJcJTaJvEAyMVfoficEf6ViHJMBONLVvfhCum6y/hZkrbgVoAc3m9KLW6NuEIKa4JF2sYlt
02upt9TXItOtMGDIUIlzDfvXt/rGi89piFkeTwFxRCeMl2/RWxIjKn+WRKEoP7q6GliHJiSX
vYCbC9GXQOrnmdtxUqtYnhCVYqpuLHj9ESX1lyQTnih83kBhZGPjRvT6IRFFDQx/8XR1mCds
Gn5zg4c6x4/6C30nckCrWPTUVUq4bliaWNB4f9lvo2b8mJbTD/1V5h1aWVFxolXPAZ1ZKIvV
bn9I6MvJ5nSe4M/OF0tmVm6f5GZcETFSLiZ+UbQ0ay0KSarD5bk05i86F8oCvJzl7lvAE7b3
9i/x4brFgxVstV6Rb94LOLfD/NKbJhMnW00u4mvzEtj5QjEzuuvr7W+Rj1ffBCDz6MGmb6/J
GA0H6cwRadu4ERtWZEF13ZSqYHLr/N3GU1wO8E5WWH/xTHUTFxk0fGw0GDa00lfHnzGqLF4u
8KsySIuZHDr7pr+vJPMiOlr02u1XmdEXcjRs+JMXub4b35eaWb1j4bncwOieNWCknT77itgH
zvIj8EQtRpnIpz2vlJde3ZB1BYPpga+MOCLPywNrdijPbE3qOqvvjkQ1BAOb1b11DsrYjm2U
3S906/Z3LYvVr5IsdR+W8szAKqk1hrsanlyNLb1NRgJuhZuWlnfK3J5O0pnhBp8vYOrr281U
hy79mJTmV+M2kxY4hwfDFsGmcnYbS0PGNodEFWhG86GLOUvIxmgvMLa4pchXZ27L8GcTtCYG
o4vJTQDNuVO0yebBbiRogSJpfDX2u849K5cPJEdJDUbZN2Qd3nreU1oWpDZY8iav2a7n8CNP
ZQrLqJeWFxP9jcj2QSwK7VOtvo8Hvtob+PKH0sKstNUgiK0vBa3YBgJRNMVJXRlfgMbeC9gB
ftoEzgykZy0ubvYyw00HIq+0e/aYbKfOotH50u4mbkILFPnyzbtfhef3YR5U00G0gG9u9/v7
+wN80ImQuQrn3jXPyG3/Vk8lCtrYpaZH25lp+uph+H2XKwbz6CK0/qh4Y1d4gW4nYggARYjL
j77eKa916w4uXa6ivAwx6X/OzkvCZ1qCUHPiFnAEXlMLlFV2eDzxeJaNFvfE0tgBncnpTPWv
10wrVWjZJ4bFJ2lNiYATPg52TTnnrNGFK+Zck+lyoE88NgM9bGtlY2U70nVt/U6o+ollZJyz
z9DRSLFEmcuCt73xjwCSAJC8UehGetITTAplCH9Ya4gfd55PTDwLdB4LKRrTE1LWi7ltqMVu
bs2Lllw8qMsTA5NPrHuiT8Q/yApcCxvjx4yk5B3PwP74RexxADJchx8kfzuvCXwcjzmXxBsz
Cse64oMUacs1kXcePv3bp5snEJiYUZTj9DkXsk9J7Yyh+mMUv9cp7qcjIwc1+WEN+feyYDnP
XxffrziBeo0yp0q7IsU5PV6Sw3UMgnDI7hnvC36ekRI6NeqXQAsAqYVR30jmQnkp1mEmicTI
sKdnF+Ol99XmKgaeC+k4rKfNExMEFpQ4ntagYT2GWS8i6/+QduN/qv7UN+rgvH7InPT5sH02
9Oxsv0pPk3B0BqKVDzqIhL/bZt3uLEK7q2DAOICpxv3fpswsiANHf4cg/F/zj0Ry7+gY7M26
2NEYj5+la9sgF6jJfj2+yNKEhx9hdv9ps6jh+LTAZmA7QkRr82bjsCLZMQY8UzWoW2P7GDVp
ZunUwncXAPa1RnYVaVMsKVY2IAmQ5X3JFeD97HrW1JSwoJGwPSEuKy6sloCvWlFrvz6vH6gp
Qda2bI9QOkFA2LWTdSxS0L64oKev6BLrsMmkwIVoDZuxJ6hCf7UeUImgLbnYx8Eh7ARB/iSW
QrUD0Yfdvj8MJlnEkBm4CJFZCBqlWLGdJrk6w1HDFe1YRggRTGwNpDBtzZhfuUZ+9tvpT3tT
imQTgdzNdjhX6wXcTNh+jGFEMNxcf2MC/VmG8eDqIEcXhxB3KbNPRY+DpU6g1R2xmdPyGQXo
ABtzG4D1yviS3NiPaPz+sSeNIzhdI5mE7Mv9MYpMgswYEhUcrRKp2E2Qsmotg7CMtMFBWLZ6
D7CZbFLDzu0R+0GS7WZXZ160Ja8LdiutDIW3JR4sXkRvI4a2RFS8XDkH8UUWjKt3AvEmTgZq
pYxuXMrI2/cC+3CrHsRBW4HRMsOmoNgkRvcJhkEO0afnBB9j4wV7eBsH6w0qCcAXJCc3qZQq
vEJdIo8pMzoSuGf4LxPckxNbYJHNZ+AeH04UXPXhraX1V5NTSLbegfAEt57B1/mLNy7ot2Nx
zgr5xN+q1GoDOPSktCTIIugn/iqiquYKA55Aq5nr50EsaGHM6HbY3UZQvxEJIKxC17jiBeP7
kPbkB2Ndb22jnjiJ8ySXM4mPzujqccYDEms44DQXdUbxTNYvk/Bg+T1NN0MJY8nRPMX64WK/
PpbL5ePTtMSzr6dDS6eOT8MTajVGO/gu+AUvF26GtmAKphioIzYxkK2CGnhXoTBb313TF5s5
j/y2Qt8LMhPygNGWcWzgRihiao4NP/dmwN709QzOa6nkrf6DOmz21A02S45UGRi5Q346mMvw
GhW81z73vEvJjl3atO18Yf0Fk6DOXz/IP701NxfXBYo5Of7cdYr6TnHRPdY/sijNGLwN4gfm
A2LNySe46d0HVaJ2ggexmy83KdWnI98LvNbeDt+We+jbdXrYLHRghzQmKgUJd1u2jMo0WTqX
tyffaLxIHeOWN0SrJblk8BMxTfiFkAhmjYKO2bkFg4EreNku14R1DE1C0Hoxrpeobnq+ZyuT
ILZ2lcNzC9vDhcRGW+gM8KQ8V+hL998LHNhEQRgshzvRoJaSnw6Gmb7aBDeqIg60zdbS6e8F
8lzu+PSQoblfDxVMLCuC0OjaYNCw7d4MpFcDUWCYOhvXZcJ4NALiPwivn9uyg+4WW1xOgWHQ
x8MVxBs5FQH+CuXwvprY9IZZvc5mMMRidCc5jrHBfBNnUtcweWaqFAZYu/+I2hNY6akHp4Z2
8uqaabGpZT1ZWUZE5ZLbc10980dt2VWvDg7LSUagSyZwJQcKOWpOpqvXL+hJGp5cMwUFHjX+
cTS02sQh36ZXBQm7nb8Ym/Vmhh+ZzI36aVyypWyeczC7hhg2fGwqsFp+CV0DC0ZwDpa4dbOM
KDxqeeyjsm6qA4bX054roXC2QgWzOFmvZxdyusZUuZ13eOEWHskPZHQP0a7Pw25tt0+4ovrK
yk/iANtTvSJQsTxhkRPM2R2jxcv80+BZXTXe0JywBqJH+a7dBoshpTfZ5dY9+yZ/cahQ9j42
UbbSom3zcWP1TqzWXmRNwjGabQ/w8dst9WOB1tHJQGvExDHGCOvGpJEYLn8R8J3nBo8IbuQ/
ehMrPsJGCe+kUm/F0JPzA2qxjMr5ChL8ZcHDoCqe8tb3ZdQe/WCM23uBr6rK8pcCzuj1ccCr
OpCJKoNHwTM4dczW6WvSLBZu4opxrUjGBlS3lKcqWyBlVXeBtUO/W2+ljmXg5hzYdTvbsdlN
ExqpLwB86tPObgyOWZUKXZp7GPTEQH1SRaEJkiYvD4RkdWvOc+duyLRF5QUVQSYi/EajeJLk
eszikBChzi7CqcIO7PekU9IWBNBH64bliMkvPY3NaBjRENRe7EEtu7nztwkwEdqbfBzh1qGy
F4CuISPI42iRneGhofNpYcXM2AD08kv/q2hvVu6tTS1tW3n1FT5V8plvvb7LMTYtkXGf5/Zz
SnZuxHw71/Oc47RmunKuh3g2bzqPT61ZMbKNDBhGtTCIhSLwbJG0zC4VY/maJqZWkluWsbOa
hYyYTdN21zaQVZxEBokzlnla0Aae5C3qctSRrVtAuJSPyPpb4BX5o6uUNixcRL8oqarCmafs
SICfaXhXqtavc33CVqLfrN8lxMbMFt6DzshYJp5HCJ1imsQmjQs70A0WqyGz298OwiQbG/GW
ZGtPy2273pO5O6dm0ZPaA6gmrvSLfmr/F9GvB41Xg/GFVEr+5THhQws0fND6AxqX4vjuVr/Y
SL8VBjeX/007e4XvIgWUJDUdS802mkltUvOzwmgkbHtSuU6nsGQ/sUvkgLm1w5pyY5OhzqSC
zLxIkm+U/krUQyPo9JH3Amvm7wWC4GsjMYGI9wLabmzl9wIA4d3/ER/lMUnNlEfSLjQMVw39
nF/gUPZ4ZCaL9GONnftNUos5BqkJsgGSxukplCYdkt+vFve/NY0wmut5tfn4iJNgxv6Xuj/P
oJWGc15b+BkCQhq3b7lkopGXXNKRshTAfS0r21GnJauXV5MlesISA4b4zFDY42jfgsjGxi2l
7xTO/LZYWms6aKSc7k8oZB4sRXn3s+Xpm/noTon0CmtXu0nXAki/lamM3ql4xH7s8BxSlo08
ojr+v0eVfYQbqtSKcZ1GJuSmFgTQMEbWb/iMlcGgMNaCk0v+P2PivmguPa9u8sIvcCjJztZc
cy3P6MwHjB57voZVLR5w1FOSpucEVRUUQ53elXMUp9AF7wUKjCIH1gAjxlrP+u5GKtxaCQ6h
rL7Y5ikA85sm0E216Dmug3ZkffmhP1vJfer6UVBB/fxMTlJXiSirhmKlcy3gQc5xz6g6Cful
cd7Q3Yfef6b/87suuIrOy/REo8p/9/xNk+eyqMTcTllPz0ZQpIpjRy8WRlQ4r26+hYx5+G9Z
O43nEVFfjBJPyxp0jSLFQhBWs1tueeM3htJRKsDW+PR8ZfmJxk2pk0uA38h2VnYUCRuQ3Vtw
pdc5Y8NVddDd9uF5XaWizBOEsrzJEDKjSczOkyxmQnDtWTiju9bdShxYO2vJNVLBrS77gLvJ
ugBwOyWRkIPU3K48W4nvZrgifl379i64x993dgd0bMAr5Bw9PJ0d5L8mmEcroEiANe1jwzLS
45e4IfcOrrbU01JuVI1WVqkl4dVm9KBSKGO581OqE7Ye7zahr7wIVegMTK1DZswlo3AXnnU9
0r5a2ldrddFTs4jD5xV2g57eUwI8J0282cGHabyqeS+gIfx9bPc4hMpcuZzO+/G9QMmMjGuS
G/TUy+B0wqFNGwsIMLAmzGWdd0BQms9pdrd1YCajjWdC0GpyPUZb54nUngIwE4Q2GObyDh6T
tefH+ESOSBR5O+VsCdDc1d7d3ZdRa4fBFa3YWscjOfEGUerJ2/nujTBA2E47kxtW4WnEu594
tsOdlTLxRgGXx/RvSaVuDMdsQ7miX8jmpPxa+3Boy+tAxQGGRdX6l1xq98FJOdUtqfyJKrUw
Yh6tGjfRcsdvcDbybUXi2KTs13meAEjg3DqJYGArMLXMCQsCx1K79fc8A1E3Fh5gGPCws+3j
QZotO8qQHyepNyj8mnSzkNE02eRcqy3r0lVZ3DI9BuE/Bmb3XtALCUptrVBQbAMf8Bocko7i
Uc/QxlbxbboHYxLut5V8HTi3hXGyAOZFb5aLQEXvbcuRubBz/+DqyeBSu0NUHY0iewXTSIMy
GqLl7v4HJUkQ5WezG0XcX2MfVvw2a29sr93uBD/rmc59eLBDl9kzlpfos6H48n8wyv3bZ++Q
YrFo5pNY5rzgiupIKD3BdEgDHnkL0bhwLygQcz9TWaYKWF0FrPJLuuqEtCTc1ePtV7fWac0n
YFhkkzz+juUE/jDdOOSMisXP0YdDW9f9cJuk5mwZw5vZmXz2t8rb83i4igKumQJaiC/IkujC
WDoRDq/ZTt7JrJWfZba67ctXUDkzeh5ZPFd5nLYNosE5wOMBNiazNVZ67v4OJUREQ0UAQgHi
uEfxRF5SiG3AsKaVdqOZmYV3/PpThTMCAvrDTZUbO0vda2Gdcz0/hEYrXikDPWiXnRenl8bQ
tnywiXnuhRvXJGw6lS8kn7N4QD+2irJinhNKT8qQ0VJiUVI9jbZDr0IXQXSmphyqGwuMW6kI
16FlFMSL7ps0LYyTibCk+IzS2Y1dNKoGsCXbmEBAg1xqmfLeyL2TRypom/NaZqSUpsARaIH7
8WGQ1TV8jGCwTIP6jY37MqT7MujO557pBVq3A8JwOShaLj8l3oRDxnJh7oqd2eYMprxDAiT/
A4jkdKko1+TWpeOFy/neZu3QlUbrAAsIHrCs6vVwqKgkFftNh44ZaQoib9TIXmmkiG28Xjrz
tw8uNFfH7JwZORcqik31Kt72hjcZgiGqVujQcFIeoCFd6OzT3WNjby1nwNe+OGjyFSsBbSKm
HOnQUmAC87/maWt6HxElk5tYHTK+SqqukGZa6XhCHqB90B4TM/nC+497TIeDwPIT9+rrd6vb
LX8qPotP9lnZUV25dIVg9E1TsO8PVcPntTfWTyRD69EAUq3gHxMW7K7k85KFRWtDDUNc8vnJ
5Cgj5LsFExPtnB5zNHr7Tp78Y47/9k74hpA5OrIHNdh3OmB7LkbpBjWBq/LrPd6df2/nXwVQ
/fs7Pr6694vQZ2tXuqMJ12K+z94/O+mEpKsGJZeHJue8YRaVVzhb+dlsomKmyhCpQZN6JvuT
Yg5q+fKqEiNtxMYTctcmhStjoqGnGTTGz24stXOcqwpIl3YcW280jXfgp50nwtP9wWq8js2b
7wV+7DV9fndrndYGD445Cu+uEJ299v/PnV+utXfpG+J0pF74ctmxtabvcJLG5uLzHEmAp25o
WyC1oqbM1TxsyXYshS7HP7iBJvqiatmiyqMo8ar7r4epSXVVHjWhB2uw1zeLJ0f7D+vYaInp
LtpoajvjtA7TE8fQXuXQBOG8YKcO3amprlBm8Xpt5YZQWrF3Fqzvfpr9wVCrB63FE26EGVYP
OKU/nDjSIS9hQ09ZMUEv+xwo/p8UC9L/nygW+Ky7B8ydL8xp4nQsL22fCpVX2XZKzCeN2kCu
YE5Fc7w/Ps46RcJalzw6LyUcIgOFnyFAXdoIFiUuh+9b4dlY53+GRnr3lXdeDEvxrz5+irJ+
0O00fn0OZcjM3VlPR9wW+3is/K/ypyIEBEikRG3aYPQFHRots1bh4sq9YltiaoXEXE8Mkk4R
+Cip+f/S/xlKe6Zke3z1WCkOmxVo9/4Rt8aBIeY8CEYh34X5cKPv2vBkyoeC8VVtrejcNZT/
QQuljPUCyLgjN+2GVMyfmPtXYMs/ueWjyx+88MPZF9UFloEPZI/SHVHi4Q6VuPMBQtOsOl1r
FIpKCKMUNZbZ9Ui0Q5cj2bnDXLP29ogbYijO2wiz9wKpBY38HZ3je4FrCn3nWpW3c3SVt/L6
uQI7r+RtTCdmS007JIkDwusPV/kZeJWtEna8K3bqTV/E/QrcMrwFXDMv2djDu2GcB28hu8Mz
1eAvRee/nRTbsc4S2+7x492BO4ieQK6GDCCnktwWBP9GhSLCoazlCTLUZ1A6xmuvthwA0jPS
fP6x3m2IY/oqyNzer+C4e1SMfjryu0ZSvHhxp5fqYG1hYJvN6H3H5x3Ai8RkiH33WkCTNp2I
GkZXe7OuopqkTvDPXEMtzcxtIQ3xfE6qO9XW2VDmxCqwoe0JiqBZMEFFemZTWV3UhC9++dv5
BPzXVgvrX7d01miKewxhmbaA32zFtNh7zsidXjnZi58cTcYw5KiKtkR6VPQc7vkkLYE9K3Rm
ZPdPujebQ1282DruJVoZh6jMqMD6uhnVWbu0wVsUmXtfc6KZaF2UkvOJdzOo10kcWV+XuhiX
+QxbAG/kwgce/t0qP30TCMirXGTWwfQfw/dHi6zn2Aob0jiU/vvJMGUGpur0/rxCbKJfQWST
jZgAZ3cFn7csL9MlX3w+qVVUSksF8zopC2wkRuwiWjxtjGTvcSSIsZL6tx7QMxeiUKI3XZsw
TVyjwYHHthsveg9k/4ndfwX9+ZNbPrr85eG+uI7LZzfW724+uW24ZIZkShEJlRZjYWc9jv3r
qyeDi0MzUBnF+Y9GLM0jxSQRB3qRwj918vPccK+VArIHAmNbgPsXbH0xgfZpMWwfhEaep1sJ
sWYUyj773Z6/y4widwDB4TnZ3pW1GBaHLpdHP3/hReaDFfrkhsZxA/cyq3/01vaTHR/xleiR
sI7DVRhzvHBvO+xsEAz623T2WdiZfzX698+9yZw38xsVKZBpa5wzyD6uopx24NEaPwJqIYW+
YQasPnB3Evfj26HtmuUa/ynbw4+eL3RIibDMwnjf0CXQvjzWBRPZ3eo+kD/5rfW0Dg1z4Znm
qnFTw4xsCsdntuxr3UqTtaRpOxzKGUJxahG5+FaHsENeyf5snpbUKeX+RKYtn/JQ+4PqPuvC
cZydKjXd+cHKKYye5zA0/2KZmPwLEHrM3GaRPHrmuMK5ZEBSDZ8a6AWZzwUJUzcGFkuptKHh
+wQq/2Sm+UtQ7id21V0576jecgXIVYUEL0Es6+JOTySXeiNG+Ybk6X9p2JsFG+p6L0DKiVPY
KXwvoFonajGJQr8XUKdJj6iTRgOmB7PPt1LCOh/5CapvCOXEuppATy7R/SmuNyWsAKb26chs
UcttTp296ZioBLzDEcoasVM+Ao3JapRXW4rm5l9tKUMtupCKfDefrBYVZPU6vG3B8w8bzXVA
lmDx/sOaEpbQpSGv1gNfz0A5r8ZI7zpUlvEClSP/at2uT+HE4BJ0T34Qommh7bG5ZrDX3NWc
nWiuhEM8e/GMikJebgbfh3OaiwMnRS9cX4jK0gGt6al7XbfSXGyqyV1Wf7BLlYCAx1Iv5nTo
TsRmhr4dBYZvJ98uLEDKdvx+zGhrGfVeYH/CnRt7UKND5Jea5VzxRqfmMvPM4yaXfAqOA0b0
PtC0u/CpcagC+46F/kL2eT01LqqUGWn9rIy1kInqTyem+i063nGKU4Hd54GfBHzjGwHahK5W
6sbCmK6E0GsOmSjGoihwd4Wft3yIiMmtOJ/W8qQ0FhSNutqvXXvKY6ogi46g0kv5gZaNMDnv
UA+mtdqiw9LI9Jzh+a9hwwtOLVj40TsOy//e8k+k1ORHKlg8cec7Ko32d7UFq9qwwMf3lBKr
K+s0IlppmS65dDezdhxw+GFgRJT9aJhwROeYdd8/0VQe8il03rWRMvyjSarlkmGa/GZwArVt
hosSYkBe1QiMo6e6HsOialuXS2h0w5D3ArIHCfTbETb8rFcttztj4kKug9jqF3SPyi4GJSXR
A4KPvpzGMWEdGGTkaT7UqVBZ6aoLTyZdrYyPp/JcZ9TmnX09Fao3AREqEWLLlaKROyL30S6I
mAc+Qp11Rc6J5Ilx/9BIGS/wdtVTqusc5i2T+HCs7ybjKRX2azT1EB/mhAF+H2bEkdzoDzJ9
zdwuXNqwq9e/1fmShhyHsqTZlW6QoZBLfEfy8G+y3++U09CDWG/cq/D8GIBvsspeRfZgqam3
DIzTt/pGQWV0WtyXo2YEREy+4nP8VhrXkHemR+GHMRyjI9rR7RnCRx/3TceGQFlpQtAchlNP
UKA/rxUtfCCrX8yLurRilFbs+V6geIb6M6UE7/709vp6B2K/O0NlTXPOyqm/nEt/KJTcic9I
XcU6qJJZTs2+O+YCg27zyXj00myAM6stBpcX4PSY1+4tLPG4j5tAYbMQgrqEEqeeUOMkZFAm
v5vWX01J/u40Vhsd5juNmb87jcVjkzHF4N+dxlEqCI9LvXCUIARaLKqDA5zzWe7kY6mOEvlY
qpdv5xU6KIs7cfdf3oLH9kCADLeHgQbRLhHtLUszRnG33Nk81NkKPpbKV3hfFgWYa1y05JFU
VQU37KSSlZdW5oRasYVR6+DJD1zGSGNwHTBlK5AlrZRhQWu+4+M4zc0lBDfFNRd3pTKaeAmo
cdLIQqx9RNrct1jShumhcDyMn6TonsdEzxJM7tDBowy5i6GOvG/6pqYMF7q2FRSdCkzmlI5J
906s67Yhkt9OwVjAYteRQmloCOD5ViBHF9FOmUFmkvrnuC9FqVHScwZY0kyNXgrbvWTTrcmI
Py/mtQvOYa0M7/j18NIa6o5NhLu6WU1tLC1wvh8QyqnLql32pOgp35X+jQJO8a1BX7PVWtgE
j0imkgWf0E+sDr82gV4Ym0r1uNCHEyG6PodY5/MhuuGbrEGcbwbeBY3GjYK0QeBYK1BYgc+S
pl2H9j+a//V87rHK8T+Rp88uVTcXbwr1/7LAlzme/oCW0sMYRsacpW8Fzuq9FtFa1rixYus8
Jrn1uldP95GXqbLCNxsKT6l4cMyKxX133+VIUlJt+/aWcP5OEETDbZgfMzp5G55/73k4sVx7
UX7FL/KWnKLi8R2RIZrjE0QSVAntud6mv6WnZgMKtjSzsrXiA6WOG7GZhyf2/cwy4jkEesx6
Pt50vuN0+1/N3PW59+T6eQrmHV5u7DsHoi52qvNxglnj5lxihSpEBBkWjzVJGUmQO8jCgCsW
f/B7bMtRUlJKSLB8LxAZVtuKWta+N1C/Sxk/1ZhRszJ8/bve28GYpI31AK1t6wTkdwM5nqo9
CtfF60+L7P7yh/Inr74K5Cs4IK7x21vDvh4sWUKqhzRSaoHpNQUCDxHOqNY84l3JcfsVcPhm
D/i+5EaukAYc6UlzTGfPCP+RbuXDFnxGpf3ceYfHklseQ1cDwb4lkNpLXOhqk2EMFI6zE7TI
+1lCPIhaW/ElIoVYd1q1fXvuhx8KTL869vLpv7dw19LrCDWohmQwWZJS45UcWMHf09viTPgZ
JvKjjWaBFqxmuQXIE45cl/BrFvzAhDIxltrEqP1iE9+vYRhj26aWGJMUbuX29qmMbEpVDRq7
83iSegk3D1Max7vRSHcCHaIh+kVu8AvLpr4O6wSpn1rwbONDtx2Gb0U8wDPGIF+HQzz6WFG3
uMRgpTu3Ts3bdpht6SofOLmhXXyOc1uXDetacwue0MUdVIsWepSxFTQhG2NxlR6wBGUZ+ycg
dkTNa0zqWrdj49vmxjvDgPCzwzIQMSLTcF8CcyPmkL5qXdH22g3KqMO43IOrW1lOfpfSeTs6
Vw4WR/+Eny1pI13ideB/s6A1CfWxbUXCIdtIeS2PGW1/XQSBdCfKcboNeRBm+rKqrSYoSkP5
+Q+qJLhH90LsFaw7J9GvlCPEG5dbOrDzlddpRGT3zB3v5uU5YBFYT3VR/Qa2w618Yr5Ufl1r
QLoHWlTnHI4NNoEpTy/uv/scCglVbV9x6zFIJzCmVio4+cx6wMwI1CYnzPT8oPHtGgl4w1zv
CTbvm8K9dRe3uP35XK1/1CwpNqxyIIbp/MsLglP9VjHQVVQD6s4QAlYbvehbHS3GXYgXWkxJ
N2Y5b8nvc0Hk0QytTKEnpDdgjmvksKqCuq9sfJU3QIsuiuWRg7am3rJ0hYsBoadrYICW7lKj
neEqTS/cAOgng+wAhCyDwZwpX8iGL1cP21IX/C8YyPyep65mNRLx80YMAtyGJDQ9DJiZKe2w
cnVZaRgyyQH/tJ1+hg9KsZnyrOZ6Bcr8rMuP2/TylVKmZxvGzBi0A+Jrr5fgUJs9ZS84O7EJ
j6GL5AsGD2Lisjqx9KwpMXPcPEf+bhixBvYwSLJaei51dedmqTfn4PN/ehSrUM8eB69GddvK
N7cubdfKbMv/PKRTxxDHp3YQ5zlCvXn9w22FsovKZuqSPVQyLXAYTID/SC5l8gYLZbGmZnV7
yDtzY3XvBfA7Ii/+6U/k/O5PHJ+kWfzuT8z5lz/R2j5/AvdeQEJ5viBH4e3Z1tGQW5OKUrj8
ueyzfGdiTJm7Ee9nk2NTK7DzQTcR1J6wvskWPlCphM5HxFwfif219F3qLypuqqMpzyNn2PLP
FCJhe2px79oeJQIu32P7cdTaMDGW6UIEbFp24hBWBXX313ZSR4CVayEbpfLS4IV6juzja2Es
EYGZx2G8GhV1NmP4YfBVWlJQdMKQWhDzFZrJDcix6qpbFLnUpVRbMLAl4rQZaGqB0/Tjzn0n
gza4MOmIkDCuWK6MzslHdQ2XH+zUU3F+dR08kx6FX25oguv4efuwuoiSdztHl8GxMDjkwu00
T48wPvYlNskCAhsweOCf/Ool97xSV48q/6o80hOJv2BwwPH8Y48mD8tGHHVKlawQtAdfMFxt
bOdUgHQ3EvyQAoSfq+pN3xslpvPbW7SL6Swjp+NNrR64BXRXewLX7soBydn5tEi9VBFxOlFT
xzaP4mlkAUnO4w2d5NrVf3dG89kUpPNykjxdh0Fa2hse8h/fXUKhmf2vtLF2Icka8lXxfbhc
ETVOdKSdx006l2v/mlL9nT9Xn3ZoTGi2ID6pOmUuH4jG0g1QCt9QQkh4A1DkSGn97hkxxrJJ
UwdkkqdY+1ZzZaI5Yazf1Ej0aq8qG4+GHOCm8LP8beC9eoLdo9PRNGDV17Ef3LxbkcAnEqgJ
nHLD6uZYFXc1qLme3FzIPujBZ3BMAmv6Ihq66r6KIx8AbDx72//14oTz8nwFBFTK6CugF6Xx
t3i24veu3Pmgxs+5sL9tPraEnPxmR5IZUTJecdDLpisxOpxU6puA5PRGjqynIIb2SZsqh3OS
tcO1sAEuQEDRVhGqe4XL5Qf5jiiN/IntX6IwIbUTiKt9WjrZKaJWSRm4+bfYZiUcEoEwB1m2
N9XYL5nrzi5pDSW68xMI2PFdyYJjKU+iknpWnSXwbj0BLk6rN8/woXxuqxoIZ+f8u2Fz6byy
QD4bCMHerp4/l+VsP7m2wRJxY+2viRmOVPrno3qElhx0N4HajQ8dWA/jlVnmTTOgwopeqSm2
L6Li1Gi6yHzq1ce8od8f1Yv8R1VZzVmNHfYz0jSsWy886mUQGUUZHQlaeWPsW0tYYKruV2Y6
8iF2rzsP+/DyBe9Hmv7T72/8L79/lpEY3+9vIt3F9/uPOKIWrxzkFWtZlY6VosadmGuSRQi8
AM3WXHw7+bB84x8e0z/ptH9e/q/SaUkk9x8Idm4adD452CPGZ+kpKCqiAH6z1smSHCfy1Etg
Zxdcjm00EQRTH8jZJ0ZaT9Acc4vsOGtWdu5sduk1MefdDZWzTTLK7GsddV2lgzHLajNGcJve
eUxfQbNOW6opYd9xVhYVrEMPraxEmbXb4so7nK7gD8ufTCxV97CAr7zyQQbtiXq6W98H8qcG
4wtIhPYrWhAifxzZIQJbX66u1xpuu70inJcL4WEkBBmGl+Z6fY2f+Lcb+i4Zupagx0Dy5Z0g
cE1kfz7ji5YPavysCxIm/cqApEyScMhbJILU3A9pj5p/PGqrcO/hZesnA6lJb7tEfNG0Hntz
x6bZhJRh7hw+UGyRz5fp+F+1+nlnBT3Y6dyQkkbD0fpS1xzXm84qHFDkSk39o/q/i4zYf3c+
Es+8uXL55yxdlaXgy91aOoZF60Wtb5MCAUu/zbHvGhkGMjE14F9SJGdxU561yXqKV5Y0ubK1
bVv/D3fvHdBkmi2MI4o6OoIMbRQBV2dAQGCQKiXoSHGUgEwIUSDggNIJPQECQZd1KBEyjiKE
qiBBEoFBCAECxgJElGIIoQVC7yShd/D3unfv74LueHU/9n7Xz388z/uS85xz3qeeqrk+P2tW
+tV3G3kTER1GwYsoIcZ9vPuYUkIK9fyFZzEZybVkbUUcElElWKSnOII/aV+L4GJUjPvdV1TX
DaGr9ez20ttmNDDpyaTq3zZi2wR/qlFGsEKv3X3WfrD/yliRJd2Zfz54ClRs/+zVO0XsQKjy
kD3tFWeougzpMVuyUh+rmNHGsNm5Yx43VaG4cNro2qYuv+SGkEZQYUvBlYB9j5Gzqzm7XOzq
cugr+kvt1qz5Rz/v/W7AzjTrx4G3An9LshmZdOK1VtVxZ6YVZ0MykAjzyK5TW8m5OLOlUZZl
8HQirDRn1i5FDxtkGaGiOTQAZD4aE7rpvw/rKnYbI2ZLz3pGyKv0mKBHtMPgQSwQF2oe2X39
c+0u4iEtOg5FpBmUqyUZsJXEFBdP7L0lV0gklR2QqZyIde0Sok7T7w94p9uVwigz3iYVaUZX
R0qXxM1ykanKVo58aiRzI+/bvgklepTM8swWOFowgz1zh9KOSnbjiutWfwYCXua1xxa2SS5L
uztIOn47Vz7ROIKcPW6HkjeA9Fp4Q5li6yplGS7bPP9cmJ+8+u63exQfZZP3Slv1viWmQ5XP
LCIChnRXeTquiyYwEi6qRVSbxEWvIJUXJ1TouBTNZUaE5DHA7kxqrPjztPkb+fwy4HcfF5b1
8xCvQUbCuCGheHbiXFYLnnoLTakMNZy0ox8vB6/tursuPoIPXNSZ1LaIigs19LxzuZ1QQPlG
5PyW8gjxsXPkTv2x9nd7yt4D/0d1GYGqhj/f7KDIGR46d3M3cS0ghdBjlwmYKl6HIlVyCaCI
G+b0x3vXmb6PRssxqmk4c4inZL3kseg5oGZ39MqFfZvSnh8WsYU78USU2T7nCzFuaefRThAk
UD+hxTZr74kynJMyNoB3SvdJTLJhyqEnPnGY5KOMAFRCcBB0rF7b149EMFyZA24Ih/9UVJ/s
v7Y7gWW552a+mc7cclZF74DbQu4SUy9dS86/bIfdiGuC+MBUxh6PqVbTbiB+ft0laDd+bVaw
5dSf9vulvRASmDNpKEtrVPvmCKkI/m33N152MWt/M02I0RBd12SBRtSoPu7Nbss78Q/scp5l
7RJu0FKXfQAEM8j5Hrq2lbwK4pfbr9oVJIFv3RAFyeThEVzIGLJAX+ko/ztJtZeSVx/xwMGW
mDpoD/OelQua7hNP8S9XWgl8+d3uz72XbpfbV93D5zzAB5dRwtVdL/ZbPsj0mKpqI9kBPvwT
JrJfo/e/d3sUsp+r6Twgqakq6m0XZHbP5eq43o0Rfv/kBANrUrZQ0LnrSeBtdkmgxXnkfLZH
J8SGRhorj6uNXlLKrSVJ0yrjzNHX8Kf+VFifvLaKsh86XDcdGKDFdgQFBlu5muYYURprXpJv
ifHA+T3XDEXJy+qL9CpwgdY86QJbO6Avff0i/VVmTEYAU53/196nf0rBl/ZiJ+hQW6ic+PJ1
H/jB5Mpv0iAYOzaT3UoJ5Ryi0xCXP5LS61/idAtPsduHBl+p2BG5r6gQEw0oZNx4u5yFsVdX
nw8oDNRMDj1ScXOtNrHAAXc8VIukM6O/ksDm897zod1mYehNMax7ouu1L6UjXORcB3nMCpRz
IyER2UkvYn+Tgdn2S7hRSaX0mdsW4u7ao0k343am/YxeXkpEXLVk0w7/dvlPZfDJA1H2fH3N
cZfpvBpp2R2tRklgZLl7NF8DqqtDxFH278keeZFiqqZ9kBWbUzzkdXNFfHXpZp3S+uA3e4v/
tOsv7sW3i6MSzHK9hP4rlzIR7ObSXqkhwKhDsaH2mq/IioTsPP10S1kCPIJQqS1v5mOwk7/6
HoflwPCwPesJDquIye98P3f9G1kN6GR55X81tT3ESkzLzc4O2pwbPV3XXlXmrx8erYh+4NKa
4zisY8ryiMGzQ2VziZAZAgmUACSr2Nu+iSlxCIsdyO48NDhWDpYwb+h4E1ipWpCmZZtKK0sU
KGvY7o1NUbjeadBOISbnu9lBfmJ64nGHWK7fsMrwS2ujv6HubcK2sfHJm7dwWVWaZFztizwm
BWHVa0V0K2sDZlU1W4KhvtJjRTun4j90u4HT8DRT4VnLH1phB1dCb30rVbC4xt6/d3xjh180
vKs+CFhN4JAOxfgZI91vl6d3mXAXGiOEZ+YOOlGXyuddClAswMMKZGre2G7VeWDn1jJLAJV8
S2bUIV434HGCvNoij6MsvinGvrH76XG7nAaJOmHzYCunQWuWlhsGJyZLft2qHL1AvHb28meW
qtzWY7+C8NQ/fzv9+BiFZyLezaYUv8Snd8vgobrFdKpOn+EbmJlxfRlaDYceR9JfBdZn6YVb
sedDTt5VJoRP2K5N2t/bxDj9dbrnQnBuY8F+zXrZQa0BD/0MKZ9LGcDKm4L8gYpO6OACKy8V
OVKESLEZnXTLTCIk4X4++lJkM5aNKD951Iqk3IH4d9mMx8+2ipnTG35zHmfWcLnZjbB9heRv
sbCpuTCu9gRq2r4s6raT8wRp4uvIjd180fC2lsXEfHbHqm6XXTIXI3TQNCYtAwoZMyFJtGqs
vLFqPCezk1fYwGlspGj0jCQdLAlvzABf1Hlkxi9o2ju2pZxvA1d6R1BqXsxnrT5eBCJ43gpo
PPlmxZa+em/ht88dmyKhhZ53A9N/orgIdfQlk/PMfnpGEVtRyq0nR1AqnXIXtsnoSY/gJSeD
X5TyLuFO0VBnnhcFtOZH1+UPoFtV0D3Fbzaytg336wt8n4/VmoYV0y3nSAO5Ri32iaMEUChS
YvgIoAm5Hfvgo0ccOtNvvcwid86fNrkaefiPjag3wTtBdqDk+Yif43T2fkP7MceyH6qrwW4m
T/m8IeL+wF/7p0GSmxB8MQ2Rvwzv0oszSpD9YcCe9Cy2RJviojDc+ZxqHF5+T+ISA7UzFYjp
WU0e4Y8axqUh8dwBYoCv20pC897CLWXx3ZBzMSI1vMipQMVldQN2TLswSfWXgVXTqOcOzO63
AkXBQAb4e+g3n7ulFziQO/IkT/q0d2jaJyNcfDylVr/N+D2zRdjeskiGx5i/nsuAnJulqOhT
bPLrGA6I+VqKhDlykst+9gJIZke/AfebqPrrs2sbmN1GRxg61XDYHQRagjXEFfychvfPnTbR
HkkeCh8R2j37lMEbD5vyHSM+goZyZGwJ3ssVT3ZY5VxZ1LJcHWDjXC5LvSsZ+Sf/Ptk1UeDb
xZltoi9UM/VzbGj2DIuUqpFWQu5anI5G7ms+336rT1l/Qu7/yOObXee02Cvo30HHXJ1X0yaO
H5dT84l72UgvhPER1rvN3qycodyqElZEXMqUr9gnbfEMyDKk1k21p1NH3RauI+5tKY2KqLzA
xrk67m7+W4E/kmi7XQWr9YLqGr8PU8YDoZHL8gv9sOtHP1fhKWQzV9uiBvGMLBeizkiSSPZ1
lZ6txKTnmV0OA1CkYfuOhFGTrEvMk0fby0oeRpNgDawZVfNQMiQjtDEitF6dJ+hwbQOT21+G
PG1RfBMC7eNl6wzVWz0mY7V5JnBCSqKfql2mU/hPk6ScP5QKsoRxFvfrbSi59oVakOyJR+PN
9pNh1vYFasKdZhE/uyTz0E17/7SSC1DICUfoX/NPg4wNRvQu7Tx9eQMBm8GvMeVpvzAjgeq5
eVaWHp7UbA5O6q5n05QSfmHodESoi/fB+JSYh7bps1cvUkLxOBslgjxoROfUZiRfbusvGTZc
JOdWLaYyp9Ueoscpyr5sJaelOWBq5oOWde3c9bfZk28KLrJT4Z2ssBx9HdOnWdUrypLTJBL3
yoW9P24p31tpHX1nmeg8eSDsuVdagYZYHMFrTMNtakn1issA0x65fAiNWTyOvWVY5urpj34O
PlFdmpnCdpaySopeu2tvAYbw6kczAmV5G7nbnc2Sti0wHYiItnKV9+I0ks4/z3QKCzIJjdds
taQikvswKF/j+KiDKqSOBSmKBJJmXFXF8M1rZc/rkF7nl8bMe1nNX/e6thHlZvgTa7MIbDOF
Xy4G6oD58ocZZpF6LR1MDWJGcnK4JD0itMqsdC92sBtOLT8Z0Zs+SBOTCvJOy3KFiQHJWXgS
xGFus8jWfrLNLPyPtrY5dHkWAfVTHRqZBqqsAZ+baIbMajH7KZCfCqW4q9Xk+B5vfwaVfCCL
HKI/LN8agvudcPNrRRwF7ugl+RFvyX+Bh3e5q80j7FsY8etGdX+3l87xftZL929/BrKfN9qr
c1d1imTLbtNRn1EQOU9B1rVCVxLo1605BBd9mOyD7a0RIKM7jouSa0DYQft6mHhvjXd7Np/z
Az9v5n71IhMlOdg856VLM7byP37lqj3V5wUByGYLZPqe4qAtiXu/+u8CHrYZG9qhjKrXA4PW
lOlvBdor5c4xj9IW2qYSgIyH2YJji2rk/iu+KCevcie0m7Tn+aZVjOMbdW/21Fq0ftJGaRyW
s1VBzqe94nEYU9MGX7EohO+pzZh2F448vBao8kwG9ehiYkJlQUYClJZBwC9oaeW5ryeJlXz8
F+dWc/SSFqDzP7UR32b4Uz17BN55qYJMjdTZOvBktPPQBEm32NJH5fXJ9iDofMGFvaoDERcp
+dNRz4+zg6qtfNx7fllYWpzvq6OXaQ9t2zSjN/f/hbWUhvNBlFuuZ3p3sjOd32icmHs0fqt7
HulWlYmTKsT8gV74CS7MuV3r0tmYGU3I87RhBZCARcKfWNjNKRTlCV7ZWnYJ6SXBLe5Du5wH
mYgjc11pJuVjcy7JAf4uSQvy5ZWTSA68/Jzvi7hDIu2pUNZiXrnman1jtm2zmlO/szPLox6K
4oM1rFFJU6H3Zn0aTHreCiy4c4xmzR1XDxMtjk9MWMj6QUK8vv6aWhbMdvX10DNMxTJE/bkV
YSl3c/Mf4sTNq0U12NWc004y/22dCvWpYX9uGGy4O8JdD95GnM8un5rnErPoHdxkr17kghKF
3bnz9B0rcLliZjQXrC4qOn5qU16PbTbhfgs7TSqN/iZtyxqZ/Rrb0XIf003SYud8g4WiW9XM
yr8SbfL0cR6puOPtfa5eFBw6n0PykHIxugo/mahObVwsbaaXfhX95+L/9AO2hH6rgiXF07aH
RxKnR93G5jvXLU8hKpSyJh9/5dnUrfeIZ1oaINGVktAPJbURXdB1xh54CFBatf6HLXYV+XNm
/u1vBO+Vc3jKIQYXetOZ2Fs6ml27NKyI6etna//uWpINlKIbG62m5HvH/7R4KQeOTy4YLdPD
hcw9LlIbMOugCvx+eUspVKTkFcwvtmGaI+46Ct2clhtCPXf0BO7+d2SnP7uWrfpk+20D4zGz
HNfR+f4jLYU1jrEQ0QFi1bgGBqiwpSBx9oTIJtrFq1sofleGZqSKSuiZ1RfLbRrICWBQnk7B
0JXqiMpCN0noyxY2vaPini/ufDVF3CrCo9cDIipX9DqLqdVIhb477wxtQrip8RmjMrtlxceu
thf3NcWeIeaQVuAyyoD5fHeln+n/H2lVZ/Pjqb8G5V8gMl1c3wqcQuSdt5x6KxBucjNDau07
sc3hdZto+LIaQkfn8M3c4RnX7D42UT5P5+roIouep5GAR/Hg1+ykFDu8Q82UK44wee0pMG+v
cBGGdx0yGWGxL5eoMLwIOTx3eUvZBUbHC6XBMLpXnSJ3BFkCTileXht/5zr8UggbuFBHzaiN
2uPDiXUiBv5UJCtSx6YhYzGsH74S/txhu4+Q9/BSk+ajLtiRh4QWScO62KGwW2Dxesj8PfG9
TB1Lkv1w4q+Ft8GoSpGjkLoyOByojADUF/dXImLigfxsY3XbD1/YyPi2H2WgC/IWlQ0ts8+p
9lDXH6uaijsxzIGsJm0fqNygWqfQsC/fy3kiXY4bh49BqLS90fRSOcESlclMPn4xs9Os0nz7
H9c2ItwMf6q6bcfO8TPZV1z98+65XqT0mqZUTvo4kIa8WVEpPrT2VmP0vZ7l78fm+b5i4SPq
1sHB6Cf+Yzkt2LaLs0D2hocZwZJKm7v9cluC10OzPShkUHDpDY9BvnCL0EGL75OWYp3Na4gP
V/TGMwKl6smBWLsILyC4INkpJRSxE/S9OD0XTA1kis5ff7W1jG+hcXea5x6UsoK+iznuGUxZ
23VU5Konyst+KaXwBuppxuOJPb+PsDPbWSGldQ1UY7AtqLE5wLtuvYZY0NfG5zsSDd/AJzex
RqfebLY8EBrDk9kLJaS0BPGUTLuSpquDZ8c0exl8duZvV45s+vvNjU825goYO5D0rlasn9V5
Ag2sakjDP7jCABU3ZDm1dlIP36zcF7Q3463AgUAi35wht/+ECnvuSETRaL5z+2Jj6DaPa5s7
/XJb6vyhc4p9wxfyuu5zMj2zbPoM9RFE13lr9uusvTy7nVt94d3CURcn85OOxFphrZq4xtST
S7ciY3KQfHblyUtt88prgx3Xd4Ue9qaetDfr+3WS2Anu0jB+ynQnUeIVX9Hgr7K6Us+F99ht
cssCqcEpTiwUjyXOQODzczN+BgqdR8pZnC3kTaEzvCOJ4zZ9j+LOB13h2TG6K0xWxB0a+DyY
hwJw4H36ka//yWtk2Nh2igov3XyxgACnSFSn7cwzPRIedr5k2im8tkiMJ1gZ+h1Csbo/Yr92
Bq4km+zWjEHNa8NJEa+u+937SP9f1Cv1qV7j1qqGrGRJUg4L/CrIQTXMlj8Y+4hJtIAGzIs3
f6Sq5r/E5zawjFeht1WdLL0+fj0G5cLwKJDDPsvSl3fmDwC+V7Lfp6qCSy1dqswhNt2UUHRj
RHyZf/nYStDZ7wQ+01BxmH6xixVxalC2Js6ZLp0YNLoc1MYfoJhQl+DrEfR+K9kRg5lM2SZy
1POG7/kPY2bBjr5O7lpAmt3ImDgd56lRoYSNDG5vWMJ2tuurJfK+500oZZ4I9M4iDTsDmcx1
vHu7iNH8WSuBHARuBSbnOxMTR+JkKhV4cfMsoWQjDTgmKqZ7wn8MFyiVvBHje/Cnr6EhGRrJ
INOeQWpsh6xMacFRoyvjwfPuGTaDF3Uycd3mgpmhuuPas08Q/J5WexPbJ03Nvg9xDu5U3Dvz
oGunUO97HX+xTe3QhizPs00aZM85E+3JwvwBmMYY4Jtgvfb0gpk5HBRkEaLrDn4dZE+o74LI
l3G7n01q1gFFLSJqYsPbr13ZYs+EPd7jnmtPtOXIcoOJz5wNopbSJhM7WowGd1VEbq7XFHWG
xkqUBN11d7zxUojyofCBspR9iNSb3gXPwxMQTl4eB5bzc9H0/tgpbj+b0rc0lYDi7KLMxnbc
RfLlQy0KPdJZiDiUNSvfsgAq5SzGc/r5q8yNSHfXN2cEXOFa/FSalhZlbTJRcRx84ogrJfRE
kdfFMrkBHowvuD/QqKNtKcyk79d5YNVeUzB52vSQxIo9we8ss0YX3bCs2Bu8EeN78Cc7Igho
27Zk+MAYM7Ok5mqbGb/8/laxsepAsMbC6dPwH4JEYjqnfZvKqJpWmEqYbGkMVyI41MEaIrau
E8mr2n748HvdfqnNXUkBJo+ueK/blhbk9cFnj99UuZ3HKXSs67op/WTHWuJla5QpV7Ilt77B
JujVEQ/G/K9ZKcar9VCHGkAPRlPn/XXzse3/WArvluNpb1idJP1FTIYxuciNao2cCtZyGagK
HzxVGH/6xMTQtPdzdIsSnpBGQzQvxHfLmAQxYPzc39CLn7keK2bk/Tpc2zC066q3yB4FqbMd
msMQUZBu5W08JrnPecQvD1C3rp+ZzwfVD/D/Vm6qJQo+IO0pDU3CpdTzE61XyI74XRXXNjAs
uGvubme7nprSQQQ2zt4Ysa87MgqDzzjUTnGWfyuAXfevvxfIi2bbSYtF2htzmu2iX7IohmlK
g+EVAabyKlKKOP8Az4VnVw5vQPk++KknCcB0PHn+eS/Kypvy4Be7ScWmRdLUTkWcVCSi0vTR
ucoxz/fTLb7f0RfUjpcxWfgeDfs9X3EM2edCWobH6RSHtocg/XK4Dr+d4kSjXTgwicXbFS7x
c6NotJT5uwo1j8O/cV7PkZ1U3bG1jIqXtVAbPN3QxtWLZ3QllZmkOtKNiHMFGJ3gb3S/fTOj
M/x9Nc7nIL9/4bqBnsz6o9LC2aJzq6qnVEo/JENcjgULuMKTRVLyZdi34HF7pc4z1amWv+PO
tldaR9yh+UplvKjMiyssjSjRtpEopeAos14qqvX/uLd3qcsO7hd+vhHtHso4tszfa2T1aPt8
Pj17ejoo7vwRHOwF2UKFCuE7VIhEjCqWqBcLn9fmkZw6IQ4DrDn4z7NVYQmBAyysmFFfHxMI
aD27EeN78Kea34BMHIf88L2uVvDXj1w6J481leZMYTwygME5dN8CDhqA2G8/vMWrynuU/s81
d/wwNlg6MRKWNG579fUtsF2UfdMs2697gEhYIKDRbUwgBb7+/RYODVeiS6EqL1lgMLdy7KZC
lOiU2/408m2zir2ntpZYIdWg/JnkDlmGOmZ/g1Ds7NiMUq9jE6k7jrMj/jOzQu407LQg6L5o
drzYpOXxsJbeecg2TqSWkzyFUYJgEUa1EPPtf9m/kfpt57s8KLKmESekLb2qF0liZ9tb1KpL
pxmYdRfLKD7DA4iCUh9Ae/dxLS6UmmX32cUeo5F/0FKMxrUPsm8mD3cR5yC8yM6NGN+DP9lj
QUD9rcBYJIFFmKFXRc8eyOSYj17SHnKutocSnBahZovrh9Dqh2kyuyDkPLdQZJHTQyIHyDGc
LG9o65mpFLNyufvaez1/oc093HHXR5cKX/Pob5TyDaU0QqzwYNAjpute+ZgMzBpo8aQDNtRk
QhamI5uDqWJMnUe7wDxy19KIP/wxErOiWybbozCytZwrRuVhDDtCbrWXQcyXZepxTl1awRod
HjlGJ1z0lxQGsqoHp+gRx7dH9ejYGI4/Reznpou6H5JlaJmDyTE2KhV1aRZcKbVgmFKZFliT
0WEQ1Iht4Q7uwqyurB99K+AbTllH0t4KXJPorwrvR0dXnOk6dLr2Wdae+eGWoqCUpGaYFtPp
UcpcV/KR3Gh8rMuTrhUzzNPC+KgIkurx8ONNtL2/7UV8wO+2rJRE1+3C60iwHzjVEwovs16+
wxTTAM1ul8s/5ac6pZwhLDPkOQNeTa1H6cBp1vTYR9hv2w+kSy2dtzr88vgmfBfUrMHPbpUu
cbpbnFa7i7KZBHfA2oV7GvvDcShc9K2APrw7TIpeNL+u2tRhK896lnmMziie8AbVqw8QsNq5
FHOzMvPtiZtQbm58+uFY4IHq42STPJ2UsEPswCooyYur/y7F8s2bJMO1cXW+IPvkRVaBZ8Xj
yRRYbeUIZXreNMp/LkIL6esdHDAPfzZ2eHPHX2pLMLd8YOy2DWyX5jk1cxPJuU5SSV8YEDgq
oQlVX1d5iXM5fWwZ6o4EQk/n5cGawVpjJ/WeQBulEDMH75qUZhSSz37/x9aybjCD7Xzi64gL
TvrW3rGXc7vsYdNYfoUy3hoKnogQoUSJwzPd85M9Jt0nc2OplpGWwelvRNRWeao/vRUolQSK
21jUrweLNPQNZKxcd3srMDvRPXy912Bu2vO11M4l0z7Qci9l12y4tGNVNVC52JUJH2/1Mqk/
Lxm7JoxotbbSAsp+1DE7wg4S49cIl2W13vDnrlbjspNhvf7bvJ9+wKgBJTn8Bdp9mlENr8be
Gjmgq69zsSwuYMhn+ecBu4yi5NM/G0rPz4PI9TU2OZhmqE1kcdChFS3zsLhXBc7OC/Nhh2L7
u4V6NqH9Gk0u2BW7ZnZCHXCgMpLy9YtVR89PUntZj0zKnYGKQV5VZoVnT4hu+s17jU/2kxC8
p8fxJl2sgPbmT2L9pLQMaYkEFqzAQtUy0xidnpIRJkbN0e4vKw9R7HXJRsorFRIcmWjLvJjE
iIMgVtKOW+/1+6U2xWktFPva10Nn3LyXqGJxOV7UA+LMGR0fl8FqzJp2nmBdyF/eeHEbrHRN
ctoyFQk8JnNm6OjQY29TE8ALrP039Mcu6/+STHZTm/vrPIG46Z5A2g31bV8vf/wovQM6Flmq
yl0/Wxqlu6ThtJ41pWNJUR8kpiT/amCf00WWOtrG233jzbhPO60smFJOKlrWFha+ldNRpr4i
vXDCM/9IeCo6fO2pne5GYrUPzhdgKbMqZg71+ceAa5maiwOQX99EcgQo6xT6nfgBpt1ZWkXI
UO8g90csPsBV2Yrln8+SFa9G/uGvCvHPBdIyiQevhVy78tELyCefqIUcg6rZrdPajV/pwOUU
nza0aK6kq6nAuP32WVxnGD+yc9kMoWzbLX9QPgUxALW5njdWHvSSP60FjWAaVk4kZQSKbWJu
I6NfGHyh0cbwNcph2C7InVy1KI0GNwW+Duh+Db6InHalLLZrAe59Fb2gNvLj4EtFyKuxBntD
hbuZxa8U53IL40xKcZxI8pYzjK20MKgpzVjfdX4Rsn9/4/3usddYufOaBc8HBNnXPugNNmwb
jqk0uhtecK/9VUrQGLvxIOluH8bOpUUWChGbySzPsyzavy/DeE2wRUFNn+lfH5M5n12BcAIH
WPoIs24e98jlgh6ZwHhmRZ2Sshuxi3w7fMbvUkcnwS/AphLjtWh3BvIcyFPdUwd/WQjFhuc0
ZwhzDZ8EK81kDnWV5Qbol1KEgoscQHFFj6lwbh8FM2+jIm5WpGnCDz0ddGoj4vfgT3d0EDgl
XNwB7WyAlQAFaKpa9TALVSkJZuv5rOBLxXWNDZNrwoZtu2QYOjZkdGIe/z7TOlRVfqYsEQp6
BEHvkkzKwFQ7TB7/GCnvUfa/uuncXc+C1IAiKE9isP4Fe226JUuqtczuKhX5t4hg21JOvQQd
Af7pGwffk7u31Ywc4UNw6vlAzbvrTeviVTs0/huHSImfWuUck4uCz5C5V+pMqLYt4SvqIMXJ
d/5b5mF8wQmzosN3KpU1D2panJ0HWWYPsbocFaCNVDFLd6IraK3cY8G7I6t4ueu6yrUNjGwT
Di3ihcG3/55Xnz0Aj0UgDGE/MY8bN8YTR19nKTkZVVXnh9fuCB4JKPFX6fELCObQgVAitBlT
PX+5CF7un++QwylzOu3+Mdl8xsh8ZxaG5p35fR8/0T8pubiu8qgSUDHAIgvnSatEnv52WdqD
vBjmzFB1xGc6//iK7EOLVVjRSx7Duc7qLhyWfLSBry8ZVJ/slYD6OT+siXw0mgBBcoqqM7AM
0EVitV7apaBGKiL2+m9bvrkLfOZgFMe3BDjmWA+RTJtUroCt3dg6e6qRq2oSUogrg3A8d8yc
AS/wPyyZ90r4urRrAuabkZk43QWViS557jhEhpDS6ufdWSYmS4uCw9eDDQM3fi0JSss40rl3
MjJKX5JIM2MtyJvmGYfOOjmxPHIXZnIXnnWVa3vbp+29M7EWIB+LRoDZGWlOD3GAvtdVTq54
GUj1e5HK/ytqI8r34U+3sW3rDZvhruin3F5XGaWMxI4WkYu0dscsPbINVzdfue2i0CnkFWjZ
Oq0eEsVJcVGKrmku8a57lUW7O3iz08NtjbtyrWyL7yHvs/I/1fbTL7IrLEHmF5Wd8Iw9PmqL
MQ16lVMr3kGBBoDmDt9/crfj+zXXdGE5eCY98xLTjRXg01gHsUi7BdaKuJPfib5Hu7fllJpw
cmSd7S3fCmzPXlWM3u3639yK1JfGjHIdOGGzUwcbEnRO8EIjLJv8gCIMN5ZVHh3y1EBk2M2e
85gKnTlMyzsKpjMCU1XkhKMJNcKGFZ7W9N+PAbG4RznROzdpSMWXWsZRNSjJRb8/+hSexFH8
g9wzICsa8t7I+Yg/MJ2CobPjHTCk4/cVKk0FjWh8KLTLwZWCmB0a6HqVxSHMAfFFZh+TymcM
U2ZwI3mUsyrbbaf6EB8X4e0Raj+fzlwGqbzGqD0WUgy83TlzLyCLMkuT86ZnjZVfmV9fOPio
QG5NXOrJxyj4ct6JyAxLX6Tcn75fPbGS6NIdnkjqt7K2dI/lO3WSzdznVpV6JFwZKLNUnjtl
Zy48hsjBPy7yxKZVWMMLNIRjnduTXYYrD5f3bDnDnztIeW/CZBXnZGpqqyg2CG1azck6rlhv
8MUETzH/3Kn1GhXjxkKBl8abyLwwbOPNRvnPZJcFEvtnDQuzR0NNcvndlRpxFtYrrEGYbI9q
69+kf0yX80256qXk4qLN6WIGApXYMs7325E5mIia7f/E/PxfPXzGKJyBi7eaWMNkRony8obB
O0Fhv3cV/G11ZUJGwZoqzmGiXEw7qdaL1K5K8IQqhwtzMnxz5c9rr/wXBV8AtDuLpXCJdBYI
stK0fZkCC9oz+0hPXqGYJeGhy4SDuOKtYjPUv34/q8vgdrWU0kqVycvyqqoxUYgy3M/ckIRW
UaMZTdTCNq9TW87qZ92CDllwW6dK8lktKFNvP1MQLmfAlUMMu8Pw6IKyNHiQw/fzE8t3mvYN
R1x2SBHDtKQcTM+6bb24ujtr+5Fj+RHDnhTZur+uP93Iw07Dil8Iur3NZ+Bv5mxzK3GlizkW
XXwxjnJ1nGmqfsTYwwcHvtr49x/An3wXB2yvPvh06bm/NM/tM42mk7OmcH05uFoLo+pomjEQ
v5585aPx6x90/L/3geC2ucxWNffOfC73qCxwedArmX2ROSdXcokSk2hPL7O3zfA9ZGRcKVxj
JIBqGQDimdrZzx8dBOJaUr69OMeUXQc7LB6/sOXsiaJy6UmtYm8Fno5G7HESPPDxMgPbq0I6
Oy+yHe84qI6FwI7EqnmrnLEkuKDDMNDcmkzDjgKI7IiyQuaTLlpGHWGsMwAn4TQqrXOkuXMJ
uzCj7hS94EZBc4SaNnKx3ZM4ptsBSsSThlrFnXv6O2up1o2xyccIHsTwkd8uiFjCtd8KfBPC
7R1yqJS4yql85OrZDpNPX+O3Vb98hb09jsGagIwcLh/4qGpI4DPG4/rcyaZxxsn+PrP7tvn1
J6UC69hQM+zzlGQEUJxKbBYjh2uNEVp2C82OCzBmzj3yyCTp/aryiBQg+xOh/MjDjNDT/29s
zdts0oDAI3Cezt/03wUePQGveV6g+bAmucwYk9yFfM6OX0c1KIWzDueQT7JdogmVEdYssnSR
6DSUmRggXQF4cLxLZZZ0b+On3hL4s1bG/cMk0GDNmzKlzg74yi0wGgttCmSLarwj0tS6KgKL
tV65hjMURg6BK/Wx1PK56NknJlxpMJ06Vo8cfVWGzAjl4oUIG+neXrNU29kyj1MysG0Zr00N
zXIbCy5BMGGRmpx3iiGI2JhlFDK920DCnRHpDSXOmOTz9pbehseJuA62gnkc5RApf788hmwd
O2V94KxqxUbU78Ofbp8VeIAp0jMErE8qanqsJ0ziRL2R0iD8yblyf/+JNS4R80Yl8k69U2VE
Aucbj1Z/+bVxtoIJtlUeXY9yf0EGBxgZPSfcC336fv9fZHvPlXHH0umAkKj2FLsXMdVNJeEV
r5xp8SntB/CarStsyetXOrHeqeE5tQtfaVZ4+plIzT+Rz1EXXTF45aqUu+BB0+BtcaLYd1Lc
JhWaGhLnZ7QqnDhJOPyXjI/7ECpH5dUM11T1FIgg4agjJ7TgjABrilnEIQY2xr8LwrO4Kruo
72jqTb6d5Z9D8rxkk5mBXXmhryz7cJrlwgFpRfMn7MmBYnUbP9/+VpLLeBW74i5v39EjA5CA
QM+DNglOCvOwY7U5qoC2qCo//GnwrjOVpFueP/W1zFc6ZZx69bIp8JFnekGUR2oKJXde36Hw
cPFvG3G+D3+GsVTwwXKfm7b6AuorlKGmsUOzZpedYDk1eCgVXcpiyg4MsPh/vRJIb/XXWj+r
6x2hOguvjPG0ekbEuGD14sGSowsq1QJ3rr3f/xfZPnaeCJSdaF1q5+hKEeQbrt/Idk+aEevu
V9jDWq7EMU6onlJT+DXFTs7Zd9hj4tF5P0RNN+OHQGqgcXBuZnWsShW6OfIjOSn+RZEIqs7p
zhzsi1iUUes1P3UG9HGLvrWZ/T5WHL4KJOWVjDAecNdTvU9stSSJX+0GqiwtuO6hBYsFEEra
aztSb/u+3nUimjDvIuuSY5gFOLEG+HRTjAZ4djtSNlIq5Db3hCPeO9n4q932Z/g0Z3h9i/7y
rW+DZzumVkDpKz+LnBvhFqsCJjSPVh/LiHqbkeYgfQi7FtGl7acPlMCLB1SfbyxObcT4Pvw5
Q7VUr9ObdMBeqpf3LiiCqxEIZ7r9PSgCyIH3cMH1m4xgGWoWqK+25eSF5tlUwBXyR87JReRR
WrwKDIeNADLP7Jh6v/svsr0Nhzp0jBQnY6wjH5kLAb8OXRB39p6P4UtczLqQsweH6RKP3Oy/
tCVcft7KeewFaX28sLSs+nXT8VZOXkHJbL3SRCgLJnViJTwersH7a38IsmNJX+GagVb7UqFo
QiZX5uj2o8XIGCpgDNJq9MmwNo98c20D4UAVMC8U0vQ+PS7usT5Tt0OelWaKj63wQ6spcSWq
6LlTpXdzuoRi/fcWcb0w4EXLrEt8toJPR4tCxULGXlD5jAJ34Kzh6gaEH4Cfscnf6IJrk9Oe
1aYXkOBZz0le4+UOuQiMC5FvoRCBVn24cLpPRnhB29Sipa+hoazjuPvyr7dzO6aWPF9SbiFo
Ug037TCLKh/0/yU+2DaF5Ep6w0K5VsBmkEzEzx0xCDhMZ/6eiq5wGu7/xaOjujQ1DoIcQHg2
L/A75qIrMwbn0DC3A7u2ntnPM65vw0WdbOVNpWTkLWSNQuu6WagbcQUuaBQXSb9/OcTQMb74
60hvdmZ9ubcdQTEz1inZyfAs7vDmfACnui6gVG24w6hwp47Kk9rFSczAm3rH4mfMrW64eGbq
h7gy8uELV6QqH2s3SL5qT95Zz/Rm+oidbpoKrAtVjGeAqZL/cHzatOZ+IJlPLuImIAD4ihml
/MyZHmBjD5q04W+G0wKg8ZwnEq9O9HPbrsEijCsZaJH4lBkXY0wkyftsMxFIDFVU/brIRJ1/
tZUvOPBB31/iA9mQOofh2nZ72pQaqhcqmpDlLeOoL1cxjzOlRCGJR2mNxCPbLNLkAP/43mEx
aVilMdShjW2bTvLAuJSviYjR2gZZsiNq/wa/gs/SZG6fdlGMATwzzOKvfLvoz5AKHm+WduPt
CVNScOiTQeeXuxhghB6lJN8IbCwC58bMn/7t2qZvRS86nazb3gyTVv4mmXxcpb66rG5JbY/S
0zQbBBRk1MZ0UugEFEebf7MJAdD4ZKd9gSBVVa6eDn+PDqGaKqaJUKl8OKqFTGeyjx4cLBAH
zgF7zo5qledzOUHaNYnGYS6DTXNwpYmFaYiFSojVyoStc5fQ9Pudf5Hto1I/19ffIofI9zm4
yLxyo6VgowgQDubczVS2JIK+pMQTFJsFdbSVhZ3quzuf32lhejvLvQNavhLcd5O6gIDJTvRa
8QW3tjrG3+W4Az7mN6QFRKRP6jk+T7r2a/jHk6XowaQp3nZ7I6UXwhjmLAcOW4+QCwYcj0jf
UlSNzRrxhMPihU1n3C0GhvXPsFYavQsyx5KLq0IUnheOWspRE8UmqgQXNn6/bS26WRXHfWd+
RVMirqJmZcj3XccW9M1CJv2mxqmGWaypC3v0Rs8X++uY6VHNQF3iLGfvnrHQJ+bmqMXGc/aF
xvRGbJlkTqfQ/EakH8KfPl4x2+VkTz1Mk05vONS3yF3eWZmI7VCg+EygZ5Er4f8O2/CHxP7b
nwhun0vvvGRrqawnj8Win8YFBPe21eZQatsp2AQUZemcimWpMJWh4N3nNKkR4bNHhXlAL30i
B1wG8znErn5R5B+9oKBKw5x2PrXllH7WpUb09cO7wwXu/peqwT93siSuuGsXN0ollrhAUy+t
wHI6d+wewZK5g1Oo6JUmd3zBOXbSMlyju1o04baUQvVbAQadLbQpmERQN0iCo4M0+77TiuXX
J89DJPqYEdLXqMyUW56StFAsq7F0txRDytU0QrIURxsC/N3epKCkz8aGWyyVgbDd7evPkoAt
/eMhj5/hrgGElNgfKLN5MaZF8XXPdG6yv7h4C6jUYN88VpMRqrzz9L0tF/7/BYR7Bse9E00O
7WvT1TCSQSOhyKPDVlGhCvwemduZ6/s6LayD6rC3QMKIpUaa2ZsayX00KuK04bUtJ/QzF8G/
6MC4rRZdA+MaZiRaOKMUuMCkM8YY0BCM0bJC567fAg07KOraZhIoMtSczdKCa5zL1A/O9PPi
ADPIlXln5c3eTUeIHTvGDalqbhV/uNl5SimptJZSkCqk+TW7pBa/aVUWH06oirw2kljs94eu
DA3VmL36dZ5nIIMA9XfnarVXVVPgskY2Rx69fsL3vfjmo5L5dGOjgMC3C1MNg/aHxo6WBa3Z
lFJ8jPvuIM4RuR2KhQ73Lbxl58pHtzyFwkdp/7e93FM8fpvEoRAmUaczH84exy4PwV+FO+7p
0rVmgOY6nh3Rs3AXH624zTV/5c7Vy88mXW1sTKorc11M2vFi62n6PDtPngOFms+R2xvsXjjk
ytDyjlCDEgwt2pKmPCJkroUqmBkWoE8PHpwvDEXXDHSFxmd7Vg9kYpHq6PC7WgG8vwZsJF8w
O7SX9/qANOmGvmSD9bJ2Rs5YcolJEqm6Z8C+0IMFkW3QGolZVkv/6nrTWwEPe0BLNLG7tmr2
iUXB6JrtbCi5eoLNueFIdUnRmEDuIG7E/AH8GXdpwajy4gk22y5t3wsSzOg+r1LhfIsXk02J
BOtOxcBoDt8DbIwvqlcejV6Va1s9PSkf00kNALOImS7ybsR1Lept8/k5J4+kjMsymzJifEDS
F/IAgrIzbEXpx6eIXTWLb8CRPZqd0G8Fxk885jGsgeyl5xS6hKKnhYoftoel+GaYUcREb92z
Y+VULJe1KtdlUH77uC34X5PBZzm2bbOS8dVRuZn/l0mqK9Nffh6fOXYwIXBhqvokjMsmhLdX
kTg7OKOFFH8k/bvUH56+jp61Tz1eb1Zhhpi9MnzFkbLy+o6g+bUNhArGhlJ9lHTMTuqlx5lo
AFksVXaZMwiutRrQ8iIDx9kGTt1ZVddrdnpvBUSCD7zoiknoWXb24YargV8mxTOg4xdLRoAF
OcMaChrR/3jM1+esnBInW94KRK3fyPd9EZtUKmFJKNQoWUdaGyNz3pAy17XKlmZG2gPkzlz4
3vW88F+saCEnOi5SAnKUdTyuunAnykivEd4OKSXH3gpIHVw3MGvY8VH3kQ2y+F8Niu9rZiKv
TomkdXEjc+AkEOdWwHafHluyrIQV9JGnlX+zcYjHbD2qn1JgeB2dIuJxecIQR0GCEo2toiiB
qWBl2aRpE5KkOxmIBTPenrb1rH7euvsA9Di5Os0yxetr5SBj1oMJrpHwQCjLwhTK48yNLDzz
tie5SxXLXtIFZw20pehMIS1iTFYCBgn8B3lgv3kgidvhjQw4t9c0vhXAVf5I2XkjFx47gcAo
WJXk5ndBptoK00z35cbMGf2Yee3K96JAFLS+8fbZjb/9AP4MlbnA7ussx1+1pqRvV1Y/7Pul
q7axPaQtJfEgFtIRJh0ETo3NaSWkhmHn6iJCxqsE1QJN+1IvsUrjnpl3ltMeP3LmhWvTI6cK
tcduhpVXqCmEYJPCs1oIrs3pz7w+oOoLfNAxlnxXOI4wOH4w3eTbxWBt1SsD8Hw0BMESr4dC
NcaNjV+qLw767NLHq2JKCOSH7Zn1XPoTNd7qCrxC70gKLN9DJ6+xQEySmEVbePqeR9mWSOOz
NO57BMZuPGx9OFNbFb9AoAYzs53tYjIkRC0Ssb3GETgty6ITeyffaL4OVb2R4zbvHuvd43Sp
JvNoc+yxWGfedswGerff7OyYl2SxQ0uGm3kQHxGzZ7SMW+/K1FD+fycm2ZRlYcf9S4NtJ5PJ
JPwMLiWjwNUhX7/OvgiL4Up5vBXImFWTK7Defnj/Brz/BPwMzaZAnw6mhbFQw2wpseml34xT
c2Q+DqxgQ94KPCrEdNnwIDym9dNjYgn1XUT/qIb1mDjq44fVFApF1YLZCV0+zi4cRScqV1Ui
czNUyuWdVlHTyxInvv7btX9C1Bf2aJtUeYKfTeOeEINuKbeXZFPMeKEF6xklAKhSYeMaqsaU
A6k7y5cuC5zmxXSqFsD64pf71uHJlWoUTayt6netnv1KL+vKeluhEmEsyamKA9FzakCcsmDP
v0Eyn7f+0l8kLWXFws/oIG4h8WWmOVXJyDVrluxFCt5Uzmfu8kuDjd9JVqjxyVRhYcjJvhqg
rp7moDe7Q9MY0C8VjeUIZ1BuyfYoJ2bGN7xsXlyqRFUxwBfLhVmpB/A4GZ3p6TyocdXaTq2R
hdP+PRtRfgh/unpJQEhhLqYnAS2S5CV83L30yc6EKjgoJZEYM2WaHQOW9DFDdOXGFOmSQ9As
686MC5LwlygZ9yGRuzIZFUVaImDPcoSmm+0syx4a0PeriiYDitJHRhO5sjciKD7iDtfOHv6Q
ti/ticS2lqw46/EK445Du5sCKo6HF0TZUEhsir88vr4Wt7NagjkYy20jeOL4/vfEzAhqu1z/
ZpDp7YkvZXhCOWQYVYMK0zKugWrW6CDWLSfsgpmaS0dySa343xKebr0odjOaE39qJqefXcyO
yv7F4RXNZ5eIKhWZO0k43tZIrwwtw+Ezu8rHAeMX/jeonKWsf0nGMf1+Pxef8OzcsWXQBL26
+mUt08dqZBEUCX2VWVrk6EYV09E3Dw40N0bh9r7cW9gzLLeoT1/bPmPy3HCNgDgUqhjzssil
LEtZ0rXC2JGef4SbC2jTXxD05/ky/TUfJPLfCQqmHGOV4y9ROUpZGvHFrIlqdORbAc7mClTb
hPRe+hyPo75CynfVENNXSIE9PY4E1+JlIRLqsYtzKzdAtg59b8Rw/7x3qqr4lEK0uoZOUNoL
bJY5aspEN5iDlanEN2aEbrt6+OMi/ox5ssNl7OhrbtgL/+rSQLDCnkdx9BIqwnBP8hEXKl53
Fjpy1z16SZHqQmoZJYQ5yFhbTlyWGGaMJ3kEo2vizP5qFwnyHuk8Q5Zwn/Ivmzw+1qJIdIuO
ydiZYUIeuWO+5EHEii8/Lb/wcWq/gLe7JMoXQDGPkTUFFSjVoG9DTW9ERlg1vCyo9ZStF4O/
Gm4j4H9z5hcWxzEaE/XmFS4WoZ+sdZLH9LLVka5NeiZlkzw7wgCwUxKrKSM2Q076LHApPua3
K+rYONyNOE+Rb6olvS5mptjkMSw9gIJpXPEqs9+PHDl88N7Wi0YkeYRQ7hI7GptL1Ae0+zG4
i/vZeNm7qVS/10zb+TfP1nP0iQuha/qZ/cxR6QUFFu0GJ1mBhU+BIHLxfGvWgJCTX9TtfMRJ
5U512g8THiV/aL4aqoD3Fz/Or0/RXNLvysft5BkFJ8XMnnMnAEnPWQK3DChzCRyqTxPbB29Y
tPSQOco1G4o0IyNqshAGGP3StwLSLm8FcmVGUiCiYhq9L4/PRKZievhyxSL1crsXePhSv4fR
qVhtVfCBi0WGKyaroX2qHXiuYYWeMw0xxTG4PLv5hLMTZHAfavZN6DWvOKfS2bPNlEquv/7y
LAylpNCd+d1mq7fgQ71e3mIZcTLrl4v1Salh4RDYK3rMlGUm1IkVOwRC3b9ijNYShAb+0SFK
PqnYHiL1Q460suPL5qCwaKI+GCMLf40kLXh1FKnPUAVtr330W32OQlpA4ALqgsV2T4OcGcsA
/wk3arZb8vpV/QKPwX5Ij6nEMqIa5WWXFE3AF0YUM81Rk96trrT40/72DwOEMgO0nnZRqw1V
qZIzj71DIbYvyNaWD8j6VqKYZnpIspOLU7n+4lDX6wDQhdDFjxL8JbzMf1IYRmc81rUj+C9R
tHbn2HZrQdKAZA7roJpbLsOh7ulMCchI62h0DFdd82Kl+dLpp4GXB8cqRVx5qleCVtV2Kfiz
bCIpQw+navalpE0XQNQ1xKTUGGDaIeOqPtZg7DOXy/8OKWwfKj9WZgKclyUg1uZQc3pw0tyD
/a3AHAz7jznYCMxB6U1zsPKDOTgVdfsJ4qRSpxVN/fi7OdgxVOH94RzEAsNjISmGuO1Imc+4
cqX2cHZJ94kU1xmr65YeRpp6hiSk1l6//qku+iJbp/Is37gjKRrPtf9rA7AR8kT8Vk6tMiZx
mNGUqIPRBH+Vi2WaV/rqFrhSEzBRZHOjO7eXKbOCip/q33Xv2gYxsccOiMZcv52o0VfkQr3N
g5zYs300yik1PWTRGfGQL4qClvGY2S5QOd8Dght+JSCI1avgK9tlpYafMSGbV3FVaAQ3VmOu
FswkJF0tQPtoe4xQrf9Ckc8k/9qqfhv+DvOArXBL0+xqxk4gaym3j02YmF+aqwZyPL05tRHt
B/BnaEUBXw6UkcEftkO4a7bp7CY/bxZ19ivSRTbM5YgSSSnW9UXNJMGZrDMymbc4/Cx2qCug
+6mQ4yx9KPOtgMqqD/UFfCURtcuVfzNZs+vH1DJibGCeBT75+BUo2PEvYtbL+zjrIm7EZGJ6
S+a20MMf0PmFPejVeTLDTtVrX25Z7VqO0z2o2v2s8uHwAFQMdr+dbMyyrlbvJ6LN3Aj6dXVV
xuZ12+Xq7dSi186EPM84B0HJ6aPHGK4Hk7MY3iPl4IdTwJSIITQYisGtxCyj7KHqU6zIwzLA
5svfV+IQ9WIt+8YoWAoxOq/ZKQ0SZ2kC+K0sb1gvjhGd9Osh/Xg8furlyY8baP5l4cppMUxe
KVH8k4jJmU5EF/2qquXfd3vW4c6rwhf7R/PQrr9EQOKY6EpMKsNvdDZueZj14dT1i7zNQZxU
/MfU9Q3sGHr0j6lr3YidtR2ZRPRXVVWZwwnJrhVV4AtfSb1GXYIPU8KVS5busI2Sw/agrZbu
M7h2hQ/tcHJ0h/fmbqOuPp0j4rdwarXJ9+9zVzI6huZRXZulIOlKc6M5lWJLCGgg20MSn12B
wn1ruEEUQZyjQ6vmvUMjzej52XxsSgQtr6ctP+LwMXa2MN4iQj9FR8m5YrTt4BPzsNHUvS20
OKG5axt+vl32CZAZbfVZ0FetgWDThcx+RLqCFUWxDJE71VsTrmtDkDda1LTq3/mjn6hox9Hi
U0anNvz4Q/CzJqpAjnBeRQb0xdqgwauJfQrP2OgChTcLMjfRRgeuE1s54Rogkd9vxkzV1SGx
DFgIH5m0I3vUrwFqgOqtNJDrLn/Q2Z1y9JtYFc5Lai+cNVuOtkK8FQhZHMtnL7JR8ui6BYp9
XX1Q8F/0rn1I5xf1xLoAto7IbQlSDiNOGFooPWfm29ZzdPIWuCh5A+mkNisYhim5CkOYuS++
FfgxfgpaPrqrOPD24I/5Er6v+HI68Rk9iHAgmMWnD069JWYjidWQYCdNoWIfK8UiGuOdn2bS
fw87JnT93yYSkGcm9g4UMSgK1TJmQrXMgpMyfj697+StUefXtEPhWgVenWpjfuU+qAJmsqqh
RiSmbM7nFxQB50j38GZpGI4lV1x75KA2HVHf+L10rM6QSpxNjXCKPSuuAnkX2l7ogV8rKTeQ
Lp0y7JNXZYK1zP9+eE2lBCVw7FDvDq/goiXC0xyyXLLMQRb14A3R/sXxtneH14Xc/kxvc2Pz
+fzTrmGy/cO7FlfuYdx1f6IF1r/AGkN0uP+5c4JXJKrgZI0OdHAgHdPVXxH87L+sIXq7fgiB
3Hhq8b0L0zBHzs1TxyncZ9eeifVTEJzZRHBlg6xhbfyMs7cH6uhwGDGjV3Dm1AYp+6awA0dX
5Fw8V1ptqOAKGVr2oAdei2UI3ChUoP5l+LnM5CviRkwNryEfDpD1HRGUPPOQqTp2kBfEvt0L
1rKrrtSEE11fg5LyG3Gtvzm2bUD9z8DPuF0KCPhKLzhxEfIT9a5RK+yfKLlutusydYdWbYec
GSowmRyyVYc70QACtq6Dgq0kgKp9Z4+pxVUo9HVbqrr6FpXMI8HE2bDGWPZ5eH78PPm4It+c
6RjZIQ9kESvCdGNfw7BP82OJe/MGz+C7Uupdv/INxpY4par82O0FDjhLnIChwPXRi+MBRo8p
sFq7guJga3NUrEds7gPDpH/G2JfzzBQUXva0acmi9/u6eiXuzbSFMsWyqJJJz6SMMwWUEXyi
YoYKSV3dkBoWFGACOpZMfKDUmkNRTG7VOQQkIVmMOtDOVka41OSWFj0eS0nwPMCCjdzpZfk/
mfEnkVH5s4tDKgt8TZZ/7PWwu1z2uzreDwmxx6IJye7xDHPgZmp4dte/aYN99wX+c5YDYdh+
miywFUde4bWYwK9hL2f/GOyOl01uLXGRmtPt0qG2jtZLy+Kf0uyXKX9QmWYF/WTtMXz6HNjh
lI2OVNmpoeHfw+kWq9WFxP6eUXL9RTbdfRBOrAaKU3QAm6xz1UJ0EhWsydJQF7MWNJ3uaoEF
c/nnuE+uIhuHUnamN2PcAj1tJjzEzer/Y4+1lBHzcDriSvbfq9+zILtoRK+nLT3olV9rWpBU
ETXvpjgNMG9jNbrJOv95Ppb4z/NxxD/GlezVutU6f2Z1LpB+rM0b3bPy9GF6PAaVWJk7ZnSD
LtR77R9/9+6/+K4fF/LsRG6rKo7Nj06O1zOyTAAfKYKz3lzFuZxOwhoULXq4gBejr1ppdrPz
dN/XLE5LZMnEqIOIz5oLAqyjSGqP9SXhph5IiW9A+s/AT48FfffrYIp2WP5Eg5euZeKLrnr7
y2M2SqmVe4FaP9B3M40LDqe5Ih4usu+u0G+YLxKSM2Nz91j1UkQXF5i4pM4JgzVV0oHlqx2+
c2vCcx1ZIrbP8O/ms8/31o1RLqsQDfPGeHl5apAQd/J8XJjR0N4oPUexRW+SKeJ2rlUHNWie
sC6zGD1rjp41bryOjElnygzJyysRPAhEj9/41/4Zc1/KM4PuJFmQ78rdhgMe9hf6tLMlf/jj
rcDpqiqK+micGZAMg4J1wi8pJwRrgMiaTGiQOQQM2WYC8+yPsOJ46DNNUEFptZgjRwz0Jkvm
b3lEhDixtMJGy/xpNsB82dvZo7ND20y1U4URbPWHuhKFMKo9hBiAT3XX1xbQUfJzDnlBLE64
h/MzQlKsO+Gw4Y5/p9B21QdaIWPzOjOTR/LlkwEVVFXVktPl/a/xsgmr1KkXgAbq9Yt1wgoB
0EDpZDkzdaXGM2zmpULd5laRhM66xlBCwWFlaWzn/YCAWu3+HIxTG8tv8h8n6Ol8llOXBnuQ
zOjppMfwxeuAE7QH/t3t9+gSYlylAgiczka2nqA6z5yPtPSMSFYBdvEDs5tm99Fa4PJbakjP
3+8347PuHgxs4ZXVMebAFt7fmezv5xJ2p7vQ3oStYZhTDDNHTdODpyJp/zHuZlTdDDqCyVwp
h0XQpJJCVmJaF98jFNfr9yz48gZ5Kr8VyBOeKjAZJCG4h7xektH+CKpsnCerEovDhQ5aTZi0
0zOCD8GM1/DO5j0Wi91BTuCKvIhA04wRMoTN8JtSz2MhnMIvYvGw/vbJ6073NqD+J+Dn6ZwE
BESx6YifSig6aGEF4Qr40eiDEsnDp1oQEHUTv8FUAzxBPrfQfh1I5E+xXgystupl+CopXzv0
dIqZ0yhNBotdfBPglyWtlKrSWlw0PqkyaGUZnzxK1GeCXxIKhFnLBkoehIdJydzWjh9ndSXo
8Qf/P+rePKCpLNsXxqIKqhygLBQHJksskLmQSYYk2jJoSUhREIKMNiijEJkSSCDRpi0ZhEgp
MgkoSIBEQIQQQpiUeRJjCCAJhHlOQiAQIIDfqb799e07vK7b793br1/+OtknZ5+TvdfZew2/
9VsRJ1qW9c+s0D2LIdCu/N91VoaffvD0YGZCtnBVT5xFDc8TTgrbHI1Z9iwbZ9a38xf+kz/4
/0iTdLHQP9lS/g+W8s6Tdt+YsC1cEovcV/geFR2eI3PTuiOFPeEzEZPETGHvDn9tn7VyG1CR
70Huxeg1YqBlBHLuxkjTI5ecqo0aPUdEEY8FWiynCY5sf+fMmBilO7cZM+1SAwu40QfuTec/
GiV3Qw6WMPQw7o5jFn2mAj7ULwnnjVFv8xnotXH04cYk+fholGaTMxPJ1Z8n/Q8PX+yQzbEA
EmtEqzxpMpCUXVhvD3uise8gLW3Bu6dDaRdQ119CFpF/UtcxpiCju7gmr//4qtcXRER16QOv
uq8rK+xV9eJsGDWV2U13AdX5U3uCC7RoPpr1Toao7EAS9ldj+VvAWA7hUnd1amjpbLVs++M8
5JpNoRvVF5ywRf5rbT1G5+G1IdnNtbdyIN4nqT6Dr8z4GbWVWkl+u/XYRw62uv2/5GzoJND9
/Ks3khZS91wFqt+jx4EB28c4v14c6zrufzgysfitaIPJEtIxe6oqI/izWsUvFCN9Igj3CEZs
Jh3tVKkGoRh77OkeK/irgf7sucWYwPIE5+pEhnzASsMxm/drUcmP2G3js1wiy3D5k9R1uKCj
/KsWZvBN7vDOk9ts2XOsIzcWo6+dZHURLaMjZ6ZHm4L857YPoQo5n/+tEjy/3vO/zFb7Lw/4
mWlEbpes3FbdSKXXLTeG2bt0HzLGdIIa3ODMHAt6cCuBoMJWcO7d2NLWKCUlpq47uTq9Y4w9
7Ykcnxrzy0d/M5tG9t08sohxcGZFQIdux2o3yE3bo5KfzE3tHKjeICWuTDUYTbw/8Gzm0tPU
IxGB1YEsFO5GYA5BbgD+MuQlfeCd1yGvs9mlqxiTxCyCDM9wBNsKPwIfS5CP+asB/H/rcN+c
MnZW+mePmhWJUQLnx8EpeZkObHTtEx+dnoFwS3smISXUz8oyHbU+me3bAGdBDeE/HkH2yhs+
jV78qh2qExp4UvHmkrl5RDIFhcv14FAJE9ZiGoAE0aGNW7PCd3GHjJlQJ+FjJ9AfPpofmXYK
XE2rLkaw5hTcJm0pBOjJ9kobEOAczWNhYN8EJWTfam2FwjeSyln2cGdrmyM/fvM/TzYYy6Ha
jGhTUEnBBbXZwA4gUFCYSbxzSfUGBhEubBdAg9maCts5/OTRJdFgCsF+Qby0Lvj/bfbe3l7W
RMw+1x2PmWM55VfMVCwFJ9vJyfeKEUaAzZ4HH6nkMUGN7p6HoT2HQZNZRJ4x01mckP3sm0tP
+K/Z9Aui8pFZ91u4gJVCSlOfYkrQ6INt9dkK39gQ8lhxaiLF8PCqSafuUvxOzIS86sYnqdmM
P+asXeW4Pm4zwj34zxcBKUGzlNT5BmZxe1mNSZw2KfZsX3NnR+b6jmWU09bFSyA9o/KJtZ4W
urPHSkBPoWslWrKI++4m/PCG84cD238lufsu7jqJUx1W59zR407hBsPs2hFU4v0j0XOU84N8
TvHHZLHggoHOz+5mx+57mI48hbzNehpXVXB9foPoX993fOMsRcFosT/I6tky8Dh/6/P3agBS
+2aU28O73uICTKFYs8SRI17lvQiXHNJUm7F/YEZQgiC8rSuRx6WAjyoo2HgdjHbuD1g+ktux
BzdPnlZLqAtdZ0bZLzBXVmdn4xuqf9ChBrcIW90bVCFXR0lZmTnwXqankadxX7fPM4cxh23K
Mm8XKXs9whB9IIgPk31fFhrko7tgzlQ4rEqY2mulGYJmKx73tjmNDWECvnjg2uSv0Vf/ADvg
SUFllo92ayeVlmelCg0NJzMz1y/+RlrS3xqj/6vnvuzrE4Nj1WfMfqiADiCZtdR38Cza3ZpX
/FYPogbYlA/vV/YdEXaECk1Ykv1BCaTA/djO7tn8EoGyHjs73Ey1ClM+4GgN973M3oTDp/Jd
nmKPbK9NeNCMW3HJ4T5n9O0evbsSfbMbPLhiHBwZ7N7/U6XiOmAr9DqhROjEHEUt4fahBNLp
2C/z1u2th0zsncb/+OAfMB6yfT0oPvs/qgaAJ88dUA0aANXgAWwxpM4A8OS5AapBMbeibepX
T7o6SziSE2FkZBIN2PgQxS27WcEv0C4HSUcl2ef3Cyz7KaRKcTrqZZBWHle3PIE4k5AntGdi
/qQcRP/41Xe/KgfsZ9uIkAi9GohxtOMIdzbZhmLzdPHPywIXHNJXmkBIAxx5HqemOr6MXqdO
Rdx+hAvEJstlEpEMQsSbzrasVSdcW9ixW6y/WAGycVJqj1R2fjoYa25JOg/tn21jVOn3GRUJ
rrLDSSSh/RCKXOuo2ssKVx/9t8kchovDYPnvd38XOXr1s8SB79HII0Gs2Zx0+003dNv+18EE
tdLjItYIKCBBKP3tj78xL38PJPVfupKDeLO3FZcYEaixOcYrSojmT1UuYD+5kCSkayfFGUVK
micBJlq+2/WjIX39dksij15ubKlXEq8fS91A4WBBpUIY/soNTr5a6fbRha3S5EfC6s/0wsX9
skaxGUvrt/R+an+e8zyQ2iAPuRmKRdxiJRoZswz9ggk2rRXVQBQI2rjeB3cnYS/rZTwpf25F
j9Cx1U8r5F9mW9bt2JiE9IXX3brhQZsS+nIE8zHgK5lJmi08lcWCh1ce/sZI/FOe3tfC5wH+
Kbmx3tEcdthCnWLKXbv7j/JLbjB82koEI5ZDHq3orMwEgm5vq13MQ3ixGej6OYpOTI5CuqXZ
bSGZcKmhPqJyR4nVKhYcjx7SEiDb2CL3yonoRV5oYlLw5zEzl4oFSluNQ74JWKaR43tTP5Tn
NYufZ1gF9Ky6ahb4aHelFk348SjcaATJAt9XMIFhFokBD+tCZVbk79XX3cIqSd+zDBrMKGaA
kx9hSkX2L5fWZhrSUDiLmYi1HeeOoMCkwASi9Pvmf8jgAkpDKK+uzPMvXoI2R7ArsMof2Hq4
cA1YIOKMKm7Fev95gbAA/4cFYswvaAXw9afqrT7q457B/pIrJvi6tLYwyVntY5YwbZ7rgBOo
HqHzZ+vBeAxwFOQJVY98dgXwArqj5sHpbI+eEEKf4hEUdQsISjr6W/xqPXCVggT9ORGhPurT
wQ+v9X95XvBWHwSgnzhnuNleky1ELRHGkB9tfrwK/ANyGMCLZdd7nS3PFMykrshtH8TS0pN3
pBcP0dGHIuGosqZWS+zr0SN2gdn60+wBPYZqm1lggszFDb4jatQsZOioowdg9CoAns+uU3+l
N6hIZx7i4X/e2T+p+EmqNRtkQt1oLy6ZsomKNoRLXIe0KTC8U0OYPfYZMTXNXTtl6J1DVplH
uY/pz/GlS46wUmeWzfkwhWUMuqnq6wODvzWTfw8y+M99yZ+ePZAOlo0wKYj9YbK8rzIjK4jl
skJ56jBooqsqBBFZm6m7Bf5Nz4eOumfxjKz/UArM59EO/WOIjNpok0ewb0xHaeXLvq4FusHH
B/csylm+vZvmKqVJWgK/0vI6IvYacR+jVmcgOMfLzUStN3R6YBVtmlE0+iA2t6lez5Os+Y0W
yUon0ovke7rP8fA4ExoBP4IbAtE/a9lUYbU8CdVsN81q4gcpmw7y246wbMmqmcxFGgIntL1Z
wjvSgVRBlFBUz3/ew3YvviUAqamFhRxqIwZnu3iCVR7wzPTHHEAjcZhQ9yxiycYZ5We/NXr/
dOfPj7bRUPz3jNdU1eWhat6xK28KQmf8g044+04NF1hREOG0pEBC/rkvZXsJrjiFZe0IU66U
cRCVT7eGB5ncKqlQsu2gqR5BE75brpAhBQqO2NRpE8tFYw8RuDIarWXxaKtb5CepXUjDWojH
Ci9w87FNirpdQZNcIMl36pav04g2Ud8jX65J5nRQefno27aYHxdUWkKPwxPraX/oesul/5Kw
Ms8opRoVTMIntyx0Esj6JTywZRq0kWUPpWUm3b0+WOZWGZSsqMcIHa3zSTpbcFqLCOQWHT48
nSD7W+Gq/66pkJ6doaPLWEEAEeqfAxPaiautHWSpe5xOEXlmLiUva6jG1GDddPQYdmghV001
iykYmtwKBdyXhDObPChN8C96i50i7QdAb9ED9JZKX5eWFuaS4M/mTAnRzwqh73iEU6kwppWN
dIKawKIJ+/d9FxO6ZEA3NviBV35zo2P2/n5L9x3GfE1JVa51LGsZmUJBz/XRqH8yZ6w0Sxvn
JxBHzs8VhdHjsfmwoWq9JaqQ1NPVXvGGbluYYnKNFrSbXaB/rTzncCKITMzKJGlYNusJfvHS
9hUS0lOVkdoR5J6+YuvKokW0vj3mzJyP0wJ2HXF4OptMMemogEb2k+Rv/+uQHpYlDW5UVW3p
j7qq5j69VcbILQ7IrIJ6EmfgN5xwM4eXxJUEjAYodPxBLkDg5vSozev0jQlU0lmmsYdVFrDb
jTWkWWNV5XT7q6Qov7Wx//0qDvCc8oZTdnrK+2flYQ/k9G+zrwyVO1oDCzpJox0FAiJkZTNu
2UhHWHRitk+FTOwjBdVTiLmT25rscvJ2scFToLaFBHrSdJFqZI8m+VXInmtTmTxt5cyEZ+Uf
S21Si/4SW2seOlf8OM5d3fvNCFZ8y+YICz6KDJoZbUj2zImKJtHx+0mlBYmrbWb1JzKzBLAn
++Y9jBd5fe3tSYZo20IqevAMAoZPtrhpGq5FVSkIKODrjgj7AzeXHnPy1ha39p1FGbi/U5p1
J+Vp3L4UPr/OHNGq+N2AbpBjRNtUFlFctCOvhj+GaXiI5Q8u5nSZzharJu84d71fDbe09l2s
Uw2hFcQF8R2D6M4SsBoyTx4B1KSd8XYjchZ22ldGSOW9Nor80FhLhHbWqt1dz05y07tluS1i
2IHrSy4L9EJkSlO+jdd5spJTFUpzODvoYYSiiQpEu6RQyVJ13UllUm+UWCr56VDzv0rDP/vR
IeX6evuDwVlZH13CKpeZJhw6qrYgSYug2+c0mfA5crLDMfXHaLtQXsPVZAxuciCEXV5nvFup
dlSfQ8o/wph/Qh+meuOPBWcESH768lJ7HiWnHy5qT292OD4RcH7NmYFEcBAgs3S4AiyJFFbW
60bxgK/Bx4g+VgDI7nPnN+yd5YglWgNoHtuTEOXegNhwgfZf+PC9frRxmyMUHn08kzkO5GoS
ZIKEvU5GHIVHGbgHShGXK4Aq3Ab1U56dxFhzNh3H6zmPuyb06skkrndmZvsFUqGlxJI81pBU
ZVlyCy+l5RCNUH0+plpURi/0QYt09SwVkxULSldZhvaxUU4z2cUNTmDzrIeor/9xU/WrtSdw
J7HYkUM2kX0mTs7opILYSsPF5m/R51S0aTFT/sQoXnLyLpRqM7a+7WvXQSyz2MUZPJlAExNW
Yam97Lw1I8S96S9cIk50Fht6VHk05TfUxAGQPCqinQ869rabuaN2xJpDfpO0DItJ2FXMtuzH
ywStxn/YjokQELptUVVVZvy0kkW2Qtg0u6/8e6uvOplGPpkFL5POkgKTHw/ZmC6UZ5E0TrMU
YKka2X+Y27zY4XVYuBTaPj+hL2GaKR6xAac4gPpl1RVL/8X002WtkYkasZVj+7h/GcV9rrtI
MaUXmvZ2T9k9gZTiBO8fFETvRDroZeuyhQARn4On5GvMnN3uo62MaQA1cpvlfd9lheP2pEJl
EmyaHGGr7LSMbiHFZb9Q+KvV9S/d//XB34eM+suVa6rfrbb1cI/77fLPrEQELWXFmO7un40b
tRitF8h2TD4gh0EXY6umy/edQA/ZOTiZ2Wx1jWwp9fjDj/Q6+UJZpV0dWflnWCciPWmgxqhO
2T+G4u5jKE12DVXm91s7BUamhutQOhygZ7BBhHArmqoUp4Zl04Nyj9PK3xDrVqhmciZngbyA
nJM1nkftMfm6bcTTce8joe5FZpbbUdxLLROh+SQml1rgEwqyyI7LZ1Q4QgKUbZH27zDGwUYl
nHE/73mjidbJJYC5ttJwKpGYc80EbrR8wdQ7W7Xg6eGCc6tVm2s131cvZBIc2ksdvjCEJU+H
tg6T8vNHrqtkBEW5znnfApg+LRMtUJOV1ta2pmXPf9+nsDZLV+R55KNeYRUZSyHt9UqPtuom
ZLoHQ6Lrj38Q3AxkAZhSj/Ide8mRZhAW4GGcyLtptFU/7jX3QVswuZlWOrVoaLi0l+wAQV5X
pVVv08MDa5fb+ny9R5XcANYS1uLIIXa63a4csoMt+zLEKzbGcsxVNL2g3LK8jNFetSVnWXji
eOZhoSXi66oVlNpHLQ1rBFuvLi474rYrTWWeXhRUc26eBI5kk0oeor7/y0T+cx7saws99JFS
80TFLXWRU+eSkmgdDfceMNKbYhNBMSRawp3oQcFcz6OGNIK5W//3bIhGghDFWNN0qVi+Pcnz
DlDVo2+3rt6nngvsYGiNsUnZ9D1CUUD1CBVWtUCvCRKXPozC7t4yRxKznnqdEGrMeL3waGsu
AG12P4xSaRmSv+mLKzKPG1xXU/sklRA8+GrHew2FlO6jot0b9fwYbJ/bsMCAdbSQRfa/sehl
4DNUtHNdCFpg2eVCeTiyG/7rVyhWsnAe9/h99S3MaT+c38xi6Fjihv4Fi3azfTE7s3jtPp67
X5gT2skeAwa7zHV2UpIPI8hBG3GRbmItctfa3W9rrzEQD+rWUaub1NYyWnWlNjFpTsmeGuHc
K+BOlVQ0PXcrwMZoE2c6BWDYsQcaTbIYj/CUt0Fl/v63yJIlZ8pYnEldhVNGcIfqeVGZMYNg
uBSNWiSBA77pkJWWvdpSVRxYizI0NCxJRt1ypSry2AVWj5lQUMFpUIBM7T9UIv6sBvut1wUX
1Pn9GsP/F+v8+tf0zL10D7qw/GkZ2mfik5RTCANAwmYxhJORkvXNRvdf/XddYEujUGxvn9ex
h0dT2nBwGn0aGenYWHaNJVr22P9JqpKayuqme2nGG8HaOTRrJ89Mkp9WtgHTHgGaPF37ec4M
/WX7DKNBpyYmawRI3Q9Tf0PdesHQZfifyxTa3cMfmwrxXJ8lRyCr7ZKSXigi3zqcX8lIZaPM
YF+hxzJqV3y0RAFt9JE9E0B7ydkI4oX3eY8NQc/J/SXb+0Xoa+zY2NRssXTQ5By0xx0WPDHp
XXkUnWyO4Ht2krCYR3By7ehe5E8H3GZkbwD/8R0i2r2a3PxU94FnWfFYT0dmQk4MmmeznJA3
VlEwSuPOiWUr7vzG/Px9EJx/05ms22i98UT7J6mOp1Bxyy61dhk+QyEvuBidzQ/nmVywwqNF
29M9WNRmZc/GSHtmntDC2utDPX5XBUWXKEzKPuSPpXKe85Uq0TZkbEh06iep5wvZLLOAfH8m
qgIugEutgpjv14KmpzEaXbPyLsyX1rB5i/K7SFNavpPoKvpla9wf47vEEOu969+/9l/7tk3l
Hnmy1X7zGmv2+hiQi3eW2DeCx8mf5Yxq0T6yt0zc3kwQcys+EjX81e2HVurlw3PEIZz8SllP
6htcQeyJzA8ilZyOQzIsUqwj1d+xQjWBIFhZJHGw49uV7yogymo02zSyEIlbyJiaDgm9db67
AVTfxF+Cs04JLBHkDnN3DMeRvJSDiOiFdS3WHaJHQERXKtUCVHMpGI4wWX495E1KDjkawCgb
6OjAhPh38FjVrBqLiWUOucphbUbsxtRr3SQzTZausewxe4d6TC2xq/JX2aM3txwGz2l1sCLB
p+YdDVUEs4HHxXpANYbeGx4V4meismOlAvXt0SXXwc2PyG/Wud+Z16kW+mTjkmZc9z7HUqQ/
GJffNnceDKS6yBtyzAQon7MFG7MtVR69W+rNtPBs+g6/WZR7LIoX0uX3NIVOiyz7iRU2lr1S
pccl+s5BFb6Xc/43M/7P8UXNZMimzo+ebmPMBBD3vK/lUuqi15tHCShDcfEJFDgeg211H6DK
aZhEgKudwqft47vFCMfQHzaihqtIYWvWXeWxjkIdNZ2fipcrQzyIoI+yj/nllbEFIZLKYNuq
RjNjGJ5hPHoy2dmuaoH8p9U/Bry4dL86rGJbtXNG7Drwshc2X1feELy/ZL3xHCuHAbkpterJ
HGzJPLic1GS4YzCMAeu2dsTn2npFzef/5FOHdCvmPlO9RKsrjqDUvtbntE+W6ycSUJYYhP37
VwEFhHwoWg+BAvcqH2vbK7T6PfFl/S0+JNQK9LsSwcJ5Fukt+a0wupRy2C87rvNOOB1PhFlZ
NmmPudh9ibzumOUxhDZCDL562WcENifNKGCQaMHMZtdDrMaH+cJemcI0a4GDxrKn/DcliVlv
K3TAu0ZLUBoliIAZB1X4iS5OEI+a4J1VzfkhPqVbxxnVvXGmWlvM+ao07kchVorHYDil5zG4
eOFP/iweKZD7/uIIEKu8HAqtDiCaqChFLVXBnkQdQtVZGfh/EI1ILohCSpnkX/pycOHG5fvm
YxCaVHzSxxNuuUZ7GnD24w6a1EZc1tuxEyuzrZMrkvtY/1vXSH5+Y4QXUxNMI/C1TIoNaFrl
2T9eyNSOhbg1BdGP8Zjho91+SfPlpwNJWalMIFp853d5NywcV8XtePsljlXVrr3YBDAT9B8R
oG43t+u9dd8KgNrJBb4N2WWbi9mkpLnW/T2Txdo73HBz2jzX2Xdx28/0i7hK8c+sHrqX2p/2
FTqwrwDQsKTYAyLG0V57a7jUIwDmncmpMytC9RtZek/yz0QDaDHj7O+ydWedVM+uVEzuhJAb
61mhIRsJQkfnP/RtXulQ/UbIDm1fAEyED2LVg4CJcJyK9W4n+dY74fo8y6+RJSMLxItjd/40
kgBbtJHZ65j7i1/QjXUQIJmGrqZlni62uhcufFLBZpZ5EPxynFn8+FNLpmW+IwVt2aeTUQtJ
Z4nqbVBDlYJTatd/Yz7+Htqc/7yrP3ncFUIB1xbUSwuI0n8jl0zb/Kq5j4c5Z5YhY6pPxwDU
EgM1fA1omNFiG0Kvt9mqI1K0Ok2Pht0jrX6SogpnNZv2kmlpxOjdB+5PpjiyWfy8h/U5/AMR
AMEmv6/KSAIy8Cyf7tjVz2Fs3J1lEwogX6y+hDswpjTWmUj72BDME7BGlCEEnBPpmiUeVw0u
izQfVdRluXBmda6+o7OnAvvYaMPArK11xzSU75hsTlDDcXPyGyI905L88/ZjABBqk4s4l7RI
cGqLUMz2wbeLL86d7L/qFR2ZPHSW8mbJLSUHd3UTGw8lZe8mBTVBcbvfy2nkyawrTJxh3H2+
jDMLELmnDrSP5f6OR/KBNLaQSL5c2ek1tQGDeKGLLb3V4fsAERO0mNtj67kdKDYKJKkPy5oU
rMPm4q90FvDtjhmuX3W2Q16d5fEsAsgfSaNJOrsrIHnoEqQv9OgRRhYlOqQExZtA4K/0EgHT
QDPD3lpyRwQ6UK660UGxD/XyjrSXpK3Cry8NVWrl++hUoalNpwRYZLncm+5dxMoBb6YVfk+p
7No7YNdyfyW39WL9+Yw7eFfR5FBha+457S2doep6yyclG3Hy2qQ5zgvVeOI6YhpvwUGkt93i
WZQSVE5YRvxE8t1JT5rixTeG8ONo5pzBBTpx7VD1LaZ3qvqPXeTP4oY7iYmESJUh69mrGSE9
acdz0AQPy4FVzeptOdX5Nw0RHbs8Mz/ce0u+HLlo8cnkRk6pzwzDcEy7EpOTBuYZnRr9z0Xr
H9sq/cOeA1iP1pCOG80JmyHNONrb0U/N0wmZ4M+WJWNPRp+GDLvpLQhGBp/Tvhcu5ftk8607
rQQR6/ummQEMMxOv6xsNm8U9wnP0useS4WqPLNlcvlyZVfr8YBCdKAhBe5EyBYqi3aZ0GzhW
NZM4gF2TWvP0LcswcAFE9e7bsdN+XjxhtZ/bm3ai/xzL1qaLEK0aTF7v6ivXd3y2yvYZCsyk
og2ioO+EQHFJh+9ADYQDo7LZwXFB5tl9DShj6P2WXDPVivS2aHOqwHF5yNzQfveP0r1UWbg+
Oqo+iT8pdFewrfJAiRrzqaLNgnwfck0wTTJ+22WTOQB7EOFQ+hwJPh9cU84UVlF9HQvawiBj
v2dCaeK7kuBHYNxmR3jK1WsTkK+j3McgMvy57qfulZ+kYHSbH+XWKBbWa+m1ZW2YxnhKTX3v
xkpUCGa0awNfeXpHmmWab+2gO+vIjRVWBQYeRa8Gnje3eIDaCN32UC2rrvv2dotcKnspFVuI
qGjKuMIME83zlj2f3sG0f1iQ76rhUBTXU+SjQrPp4pX1EMwMLT93976iOk96sKb4W07ucs+R
qUDl+ls7SVqrDmX3LYq8eNciUECFzKUc7+vLnmnJtjI9HzFyd1NCrU7qLmCinrppEdy0qPbW
0nn/WMn667vFelKCdknL3lRoD1orW6egNpEIZAPaAwDHfftjHi7Y9XBP7BpV3F7tXzfiDGGH
5uscQCaBGYvC2KoDDcaMycTUjSDqFCmIpJP/tY5B0lPyWlzn7FxhnCOBvJA5fHSjY0wJoc+L
xh3sgyiF8w5DUYGAFbRiwLRGGBoedv7MIXx00Dd8fiydbdXLwyfXpo2zdz4EPAmoyrKPLnzb
lCysKd9eg9OoI+ptNj8dMJvQVI6+2hFCVyr+I11wlRNteGTb2GeUhz9ZmiqESkxQNL8KQTAx
Sxbz6z9UNl3lbId2jpycXRs0cAqWvsAMp9iT02EBBX3JcI9yv7gAYtYXB0UTbPP6H+cIvv5L
LqFBXo/6+jjZKdsSeyaqL5kaMkae2/a7JaFcMPibZP+/3u5/y6X/64X//iN9f3Aj9D1nkFRJ
My0nkNgVbfATw6YVTHAvwj7+HUX/xxhnVmC5kfntiQrsIyM4qqZRJXsWSHk6qjiJ3dkbX+Mh
iegzJzdsrsXE7m/poDuj9t4Mmii7qQ8XDNoY40QqB8Ij8dMARWjghxVq6mjWKpy4lKfcsas9
Oh7p6V/gLSVgkwCVQdFs72jX1skq7bfdCRs+yYp0CdCz3fOyTtIMBnZO1GvffxepHrCRSfhJ
oy7CCtcfLzXvHl/grVpZ3hripbusYsvFq7j9cfb3cPZwQd+85PoC4DHEIUU5UYi7WwmDflaP
ry9FMUywqoQgDnZVLj6XeSzPE6xdPidtwCHm7Vme3MhA+c+1Oj0y2rhbs1cAstn0hx/HOHRN
peZAwdq+v9ssxIyCGnHfwZ1UN9VYsBKAry/UAVVUt7lbbFMr3HHNdZkBNr+GrkQiaDzYJ0pv
LsdOkGKnYlSvEzHOcnBJJI6RNEBXRB6BeXudlk+4i7x3Xik2xkEWe0NDfvl6bj/HByWSP4rq
RwiYfZxIPiX2nSvdrk1fbaVfvzf2qTtzjedBHiYzo6zjHsQ3LHiGoT2zT5s0elY/rdu91sZB
G07GdVfyUeI3IyL9Wjri9FxIX08N+a4d/pdmDmp1jlrpBaqok+PdG2x6UjefOHA+pLXnKKbS
X/6zZexaBowjG/Ye0xgeRmZA3X4upVdfIfc44O7BIwD/EYbfUS/38T5LLe1pXUlB9EdTnXKf
0wYhfS6ZBL+Kq9GGgnj6/I5oFV/uCI32aF0mhyEeMbNTzj/itwlkrqvkwGYfPQlxWz8+4m+o
bNTdFDEdcm008ygCMtk29kkqQIV7dczSzr1Ah4F2AcwIrytt7ygozeWgh+EANk1BYQyI4O/+
e2H9H/++r6p/0DhFO5FOCsqMjrRGZ782YIaqj5Kuqyi4zcIyPKlp53PuE2ItmAYdMSLlBkZ8
0FyyZKS8Nb44uF68GkMNYaF/nFXzG02Krbybu7AgVlfVyRLve79WVxpuft+a5Zu8ZU6xW9YN
aXDQwPWrZkquz2PmrqU6Rb5MrCyet7IeDOSBKn6/cHzA/ZOU96PQirH4F3xVaux37VRnnsNX
fJ7tdGyKxc8o0yOwKtNZMRJz8f26Pu3kDNvpJESv9jzVMprUNQrnEkHdYQGSZ2s89zLvc1tm
/FjbCcGhV2Fz01r0e7k4HrjPK5uYJfk6UqWLRc4FhWMXcoYushncphAz5OQQH3+DGa3iMAdW
3go7zXNzyWkHjebjaoUj70USU/3NXeQP14gl4n1rQkip7RoVmpO50xU0aNDrpICd5LGNuEPZ
jQDngFAaoVSMBuW8W16kbmqWT3s3TJH4peQJVzqCgfHZNcGOC9yDXxw7P8LL1g/KBvyMFLiq
JeYJHRrltLztkswQAAVUNvqt88xmhgzro5sqRQD5RjGUmpEPsGEe0xtO3ZsHKV2cDyu81kWc
nZ81M9PvQKZW3a0521HR9I7mBe3cHQep281X9cgc7UFQPIWtKT+E9GN4Ds/vBbH6cw0dDO4f
XkZIicrUi5Dq2zeP2Np9Fb6u89geVnCTr2dX34sRsZtsAJ7YZXl7hrnOjPqFSgewvL4VmA41
HNE0+11lFoIO3w7OEt9QzaGi9DtHFLXaRrCWlxi3GCql1OLAwbBSIjjSnXh637v/cXn9rRtI
T/LICKDW6m5dqDsNqMp9tBVq4mQ44uMT++pLp977P4C9NvsXcrH3n+BL82bpY002H8IWyPZN
iOSZTM8FIuGIPboK3qTiBHf02Lx7LdZ5xjuHb2cGUlp8EOdt395cUQNeGaGhg1tW/AI32RkB
ScFVUCdD2F1c9mlaYkLSs28invCrlDJsReUfZ/2DdzxbCTLc2UfWVTZPu33bVI/ueAMR+KHs
sr5Ghqq29sNrTV+dn3rrZRkyPGr1HRfjNfUmoZhRqCgI3mQByafIj2RKjwke62ncafleSurL
iQFYrMewVaYQAq8c7+PZ/VB4qSCLTL13Yog3yeGtTY4upeOTvjzMUL8R+9PkJ6mvNxPheKVn
IZy402d5KvVWHIJ1UkPmg5OFO4Ff/DZP8t+VuPtbcwKcP2l+PjPryeygn16OCPYk57GNo+Cy
hdf4uJ20+JZ41OPk8EivWPBJ6oUpX9WOMLQpCZcrJIW7dztUWLN7Zjru10xWGBRFHowNFPOc
7JstNIqZx9L6XHZjzDZP+PR17zQ+GYqyPNJRaXPC0BrbvIjhXn5nT3HTLpa+xfc86d/lIteE
oRUPi/DWhFgVTYOCDF2qVv5loULiYFC+ZoH/gvg0qLOFiBu2CG16L/a90bp3c+vOUOTWOgjy
/GMvb+PYrXiSv8h0kMc0Klr7Lj4NUXpCyYVuCOaZR8W/CAYpxPxcia3hTmbIrYXEDt5cXnZr
bH+ATdt4M0gBp9Rzrjua+Cx6QAaALXkq2Gwh65OUDsFaunAxTmdrqrkJ/hL3tW+Q4sInqSHf
UNA5wKLTv+GEGJE9bHUnYrRK/x1K9guqqcoifj3bqyglvOlYmamBfeeRW3tFlm609pb3NMLb
ZC/9TZf1pksEH7K3Enj6rrLL4sXXofD0fHrt7v3xzbnJMjfKiPqORwIpv1qeDLIzn2OL/eXm
lKOSESGbJGrOi/HRclC+TUeW+E1foCecNs6swGh4H31FscAH97CzQ4wlGy8dIbdUmLAlzb7G
o4YODukty1sEhLptkwJkevWsLKg4qmLWgbVJdpmgHjp3a7t6amIOIINoJ+vXSi7w3ZAe0Img
zBTvjDIljQqXMOoh9mHwjIuOrHni0Lk2xNliyJOrT3h77+iW7TqZG1pPz0qe8S283fMOjhLB
ereDMT6sxXZ9Ww1ru4+IW8rrqZSnFazDC6lqYbac/t6FujhHtfVhyR2ehR2C7xClHfi07yp6
wQns2vMesMo/ik7ypat81h2nkadPhwrjNZWaStEhi4/Yy4aLsuYvor6bJrjnyx4gYG7SBGyJ
EbS/dcck6SL7VczAjLpjAlktk6/mqCDB0X36J7TvhA9zWKtNWeHJrvUdK4287h1nhoOAOVsq
Bh2rtfTLalM9ERx2NIBjwz4hRPwSFhWLbdhrp8lCCCXXb7Y6aISC5vPPsGlQ7/CL/3MhmH3F
mN0HmFir5EGe09KQs5PaLRW8yyRCLvJkUIUHV4J0IObrzizW6LZiwUd/lMtN78PrZMIRSJ0s
uWPscg6QdTM6gr+nsAQFJ3NU8PC54ke8k9nk3lnNmx5JsY2PBwK788N1Nz3fMM9tPw83vO+J
Ik3dMwumgoh6IaNutfk+JW0r/lxZD9Y2NdyTyIS7Yum3F6tUfwgz3bMxAncU2tTKXu1Zcuqe
ySYXHvMJg5wOzGMgWnv3nyXPdcS+29uRfhnsGbp5xSepGHkbhvZjqamfoNUOV4J7GWZYaeLN
qN4uksb3tBtU6+10zzEjxMgDQFIWAR5p9zzDaUfnENzBW6Pg0q0T/d3dvYBCnfRSLB5XuWr2
UmyyFQk1NW06dHsWf9P3cm8WYTUr6oKFLY2FzW1wW0bcbS0zsCluwkvLho7D7XcEDCDKWyPX
gC5BgrCN4tZlL9NgQKGwSxrMKZoYoYFbXSuhXiuQs6O5P6Dj4Dd/H2zVsWg8Jtx4W+Ge47Ts
FDzly7kT26Efdym60MYlCqcqTHYqaBSxHMYrzrUC+mV3qYz4AFHeijb2OaOZ/aSU5NuAoMqk
I98QvHzCsbvl4wKMAaDGU65GDuVaqtllrTJyyoacO6rmFUPt2IDaWqcRsS8NWzM7WSH/Snc7
/fpQTgZieMhnIO4Vul71ZxqLCXXLN1LUg0+ulFZW+01jD8OvPd5tRo/KAz40Qx5TKeOBOxs8
HZvuahpmeDouoXx0bGwnvo63l7JTOD/kN1uU30SZzwJA1Nt92VqE3F2Cz8DuK/SoZVGHOibO
hQ/7gtRNC/XxeZnbQkIoQMD59oDSYI+SfR6w83iV8JxNHDym7wGhQcFnn/bJtXtIqjDZsxfH
NoZko+2qzhLH+if83r8vKZ4OZEZaebgSfPQYUrxqR5s6n+RIJ6jhdEIqQ+qvEKz/hU3lf/In
QK00FnmDDNDVmulxiAFAYiKAcM/kGRqCXT/Xmr1UpGYQ6y9619DSAxnoj/AUeBcsnBexiN7k
ttVefRHTLknD8iOJm1pKKimPvfCyUTu8ok+snpOXsm4LriD6Xkew1aJDPOiUiU0j452Qnmob
k4/E0szi5iboYY/WVpsfvzIHEhBSegoxiFtrRpQ9/Um7eOTalYJrBe9uGk4S9u8ZtI/Ql/pc
ZrkBhKNHL+ty//g0bMJApWY5NO8bQYNB2Hir0zwjGU3ZCSJatpkts0ZmspsayrNvqMxLIfzd
eGvBl8dtu4cVq7Qp6bVi4zl4UBZvfng4er2tM9/r9KyDlcRQiivyGF57vjpFQ9c4yD+/ERrH
QCWb0aMFPj7DFBuFZZvFVV/uF3/4zRn479Yj/vWG+9Y8j3gQA2jWcPstH9/6y+ehTj634sKz
Ct0+1ik+h3q5djNfjiZKtG+oGFmm510zsWRNBynXrXRorOO/C+d/aCbRPkmdDEHLSpeG23Vr
kO2Z6T15LQWaPQshqoNWko2CvOaFbIJ9np3JVWZaWvNT96j+HSWPAeGCRCnGmLlx982cqGA6
+VzWA9yJRSDZviylLd9IbUZ/QC6XLAqc0fmp4u3bwej7Lzpwe3KqlSnOWLVCX4+Ht2NyFbZC
yzU/KF+dhGetg5QMPhNw2l6oIFzn414ZMBGzeEJO/H68r3m23oMSgn8zLbjWgrX3M3BDrlIW
G629Tv5YZY0V5p4ajwLf37lEURAqEdzR2nGXuxiCYcGGyaBcUQbjalYPOuiB6rcrb9dLtk6W
B528V1e849pCUufKHs5hFOd4uGZVvlxZO+c7UPXyRge+qv2FihNiwexde47CeQ8IYz107HIL
53ykGOAmCx8+r7P7fcx8R/FbWjO5Sm0H1PJiCLxu/tOhokYb2trHUX7gU5UxVyN7sYDoP0IC
Sh/0ej2ElIp/8qSEGwpRHYbnmbBHH0wp2QsEYRmaUCNPrit20juXOrQu528YUDxQzh8vUOc+
1Jq9WvJzX7HELMHKuzUZd42lO+PJW+7b1uTFr/b/BI4W1c22CoeciXWa1cy0F+MeJM25zei1
U9yRRUI/tLS4SdnqPBFn20B5AcP7xelwefGvAxs8Yt69SXhQ1l+zrjp2reu9rhN3J+OOXEvy
oH+OVXQC/dnKkiaVjLbrBgLZv0+/bH4gLmiriBgogsa/7S4lGIQYOCbmo5nchyrJ0KWI9quO
akc3jarO+bNENQ5w4JKb8OvLxxvCxN8dVs2b6YHSwRXPQ4Of7PFNLkyfXcoJVxd5IRZIcRh0
MXL6G7lg6FJydXlrrOvMFKItH/GBncTa4970uYOyAtdwDpWrM3e+5boAXZ9c4e+yq+PTKwep
T35oGrWymIxresYUbe/xb0hjEwcJ6VY5eUAYTmipmJ/T8GK8F7d2rlRyYdkV5EUz7Ul4muIf
NYFeN5iH9yNXo5zlkEok7hmzSQ2BwroyfiUn4sc8rq/fxUYqSzPNbUGAUCIBeM+adxVcnk+n
+SFIKV595PFGx1T7UbU647gfOiYMF2R/3zLHfPR0PrGy1/R9cRPvI/yaZPu6ckNqhLl9V+rG
FmFiAL1bFebDELOazWq2KDNuy+jiLC/FDkboLjifHqnUq+8fEzxAWjHm/z46MB3xiJL78a7H
LvnZ3Mom/W3K707fPp9bvYrdAsm6tVc0Nbiax8axKeESB/3ZDxXo3QrTUUBZaqrKuZ9meHwL
Fdq7ZXUgDcH530OwSAdjnZmGhY22hcnB1L4xYj791ORr8V4rc9Ifgpk/z1D1th14yWBzS1Sw
jrPH7rhZ2S/uhE3sHXSaEb2bfUthL5dfOJ+0VTXjleRXOou4F3F4Cali4T+W3Dx8Yy232+uM
/egs5D4ctUu+PeUhGZlWVnw+IPsIek4jPCZ+ZB2IwcYPoT5Jjc+XqIR/knKWsxECBKhPI6km
dk9CeKNudXHbYX5nlA7mkWJTXQXzHp7dnTyJF3tgqumjb/N50CVysUZ0mFFKLRWMRzqpXaSr
fJLqhp5a3MoN2HJqp5suL+9p3mRKbuZqymjlV/USce/PL+dRdmqYCgsOJ8O0p7fzEhPv2nG6
S5RligbX7pkW4M7cvoS60V+6kHvpZAe+cuUNaxUz60qccZ4Mb/MEntMX3jdzpFdi3H5w931Y
Vly4yfZk3Lc9uHy/uCsNdTo0sWGgrCurjhNWLoK16sstPzBf19Tf8IIhK2nIWgveWPXOAKf4
TeGN2zUDO6yTLs+NNtb89r1dBPmYN/UlPkD22uYbLU7Np7PYO0UjbwYitksjurKwjLDNppR4
GC9agryajR/0ZUFuKTvY/ZQaY+JW0CsccszmwwKK1eyYZXCjtQZ5Vc0x2b531+sSkXWW44Ix
o1mniC4LmxODWIlCChQSoOYEcwL5EJQjLHOtOwDK+WO+VLZsnzJ1XY67IQlSBk3JhJhZVb7k
9FRxPz7IXpBcH2hbyO3XeL79XePns9asKQHenakHo09MN5vvKhXJWmKKvOTQh0QNpwFC55za
V0EEf9EB6j7ObYxRhH+GPTyt4vbcfv+Bppc37Tu2rNzuDkfiEutbvOmGFcKr96NdJJuklobc
RwikTz0WH6nSL/28fZxm71Dai8slIMjHJV50hoCVfsFSMeX9VKgrjXt7TanUjy1YPe/uN6a7
sRHcRRfvG71toRm+FJqZ4pS4Y9tJZuWcOG7qA7hAybJ+77fNVlNesLgQS3ywI7fpFi+o7/Ay
7q7PsGXesR/e2RkGJiFXknXO+W4gqBrFCpDfp9lL1wSoWG0ZsCOZtrk9G6MNR7ZAEC/bSElV
WjgtP1KlSeExDv6qILNjhvqzykJmJqmhON7T0XBRTBrotGxMbglVCanTolJRcpwPpYAu9/bD
S9eEjdNJ11V+TjpLtXcMzSRmrlrbBdyJ+9et+p/nSD65psyb4pm8sUALnTGyiUQcBlhDOgIT
E1ebv4WdUzm7hZ2CEKP4qtf2iNhsAWb32BUAYnxu18vgCZBpnm3laDjW57ITBYXbREx+cVPo
lI5D0pQ5IiTJcD3OSOmzxmFJCwDor5B/k1U8FepZoFXeZ2LfBv5iOyBpVuO09p0r79zrekM9
lT7Q/bNyK4Tob6yU8NnQb/oUI7QIR6IRQpwpi+sVRDWVWEeXkC767ZyZInwVzaP6Rq5kxC1g
CTKn820fuDdUTMENx7Sa/MqHdFm7vEjmKZIXRTK5UdbhmdayrV3w0hMAQQ5YtnlZhBud0wEI
nEGw90Jd2GZzpWq+RCPlbhd1f7WbPjQi5xmjjOW8ITDK94zJbejsTPKds/7s4p3/9Vx9ti/C
hFUYcvtA8jb3KyCCIfNaHMKjhz8NuQTeoDvkIplGNiZwG5K6qmgICj7iZAIf34mEj2hYwr+d
8c7PABYt8S6wFHbu29rC71TgucidO2p/V7PO0k9TkDa5m+G0+zt922pEdB+WOQkpttwEK8bO
bLszgASHjGYR7NLWnnzJgS92dpr2EE0C6t4F+f6eT1Iz2D0Jflrq72gF0i8+W5KtOd/UVkZ9
u8t4Y99Qioz0v/bhNkU3DmNytth0tztkuGCm4qpbZgFpMcmvlgTA0rJSR2c/a/1fj+H/wRnZ
6Vb7X1m4V5tNT7jjL75LfDCqIH1as+dYWEkFv9lio+hNnvySo+HL24X+/jZerl3vK0PFEu0z
KqECbeWysWwSvcf/gDapQpllCYEJwIJnYlm19K58rawwQ/STPWUmd6OMnhwsOHvn9kkC7J39
+uXMrpm1Wwzunjx0Gf9m6LLFDD+Dk+xNg49sHrOGepknAcFna2zaCcevD6Xa/dBoZyAW6R+e
mRLvVoQHRbCXX59R1kcDXrjXk75qIaEe+p+kqoPFxdQt2Jcq/pBCWe0T6ZvRksLEaMM1U5NY
c8J6ZjqMLfNWbKPvStqyO3z+uR1j8WScd4Tcvvaboh/GTcLAaZODe1Xg4oJthzlO1eXzKpee
b7TQFIQ6hJE9q+28TIbuGG/DLEBW2vvSSY3SnNj3LCj4hUO3wJC/jdtX3fB+yImo+WGnZ3JI
hLUl4WZvxCf3zGMbAciW6nVjpTFqwTy6bLeHIn23fz69wz0M8s0m7dUqCGn3oAe01866PlFc
UGw8OlfzSWrCo6OU6zyAfxYfgi0QmwzSt4EysLl8riF5tgP/uuVOGA2kvFVfyX1fsWyfv+LG
6hRsuFxX1kde0Y8Mw27LvGd/zG0K5BwXcpdnH95Gb19bY/hNM5B/qBF09LE5dfZ2gtcFuPem
YgvvNWbwdO2xcNz9sMCjcb3PbgkiWXN4pSnSuOlzIzXK4kgcHpt2arvwFzmc8dm9lglVccdK
bN7j/gIs/hH91C75TpyN6PKurG8YaQioLfA5Ldd7fPFhoGP19uMJ+DwKJT5XM5s/Uknhj+0a
DislVA4sHahuywvQRQlbNy3/8DBwdAiT5bqFq+ydaeSapdWq8zvBekK7kj2Cmho95i51/JPU
29AgMeQrzsmmoasDZnZb+MPRZP83n6T+OMklC3idxvwIQT8qbW9xCrxUOb4VZ1Q8vKfyUC9K
dw7X3xk2B8YlX2GSJLWrh1gqMPM56qpVVAPEhioiNfLPmjSB1PL6+XOfpFCR+Pk7gx2Luf2g
LEHEg8FwcFQfpchubOqCuT3uJWfpGm8+R2Dd+UnqK2qluiDgTriLRcNaWvBMdiOzQYQ5elhM
uWA2WNe2FoOcXl52b7Ir4OxkPFOix/mZVxdOV+ureGzrqWmu3mg2mV+61BcC9ixusWjIVTdb
9ZP2SqVYDTipkIaf6pbHxXygyHc9la/oJ8/m751aIe+wgGiog0xRHqW+nwkpXFm7x+oQZ6Oe
w0b7HiKX16tmZfLFdvtrsd7v3fuK+dyHyLIo2pRxbFO8u37Ts86eYv7QqVH2Erbtyy20NIri
fan0htPWGSVy3G30ciz1jsUX3pfKxgiTL06KolpHGavvvIyTGlLaUJCEh8FOQ2phdl2rU8Ww
ShrfbvV6EHNI03U3Qy86Yjm0bmrrlIl6uUuhRP+asHh4lGW3+n1ch0dvP+LJVcjCA4CkVYY6
N4dfpX+SimtalcLh0IAjuknM/iR1SvafrP2Q9vbsDfv+56ttoZnrp9GP+1ePy7au9wxAfHtM
rbCWjaV71ocs6qYXuZUz5G9AuR+dP0mdkcn1DDfZ2pLzMN7cQNtE7Dw+abLeNhqx2ugpyo7L
7QjHP2oG3qoJJG0LIWV8Epfs0QBpu2BKxXDDLHBOzQ0VMEZQzFG8zL6qhsG5B5TYQmCyCIVd
3WQ+QmrYe8m/96g3P/ToygaXwe6r4N+4cF7SEGz+PJv+cUJ8ILB4kAwdCMrHM1/J5/87Icl9
V73DQqxaat4b3Lt/pX+H9vpQw7uq+mGgKfhnoOlyzw4t/FDR2GtlDmfroEp88LyxO1OM7DQ9
tt0UkYJter5o+buOTdB+TQH5YViM5zXaYKdg3l1gDcC4v6BWagrmS5Rt9kqfirwq3lLbySj1
2RBemYaveLjq1Ie8Es56rz1Mea5jUhiSqwr5RToYXVphhcZdTd1yFFmoZsE47TL3QJdoMyxS
TjQnbEgAX/INHE6D1L86FDDbUuJAUxvm/DAJkPge2PsqEZWPfc9rNi4PsyyVoU5R6ebxNG7X
wtW6hqY3GzJFJyucPOpildwyjIZK83/KYf+hJL/mi1H10nI4SBAY2++VuEVWAtpw+4TBf2yw
Q8sm8funeNwDe0q2ZCRXdO1O3FBXBkSSBKmKhrcezCT3LHC4sk1V89TraoqY4Ig3GWAVK9kB
LGsqi04OFMEEr08pLcUZmC/SYPdgny0m7EnCA4/0N5hfmDbee7yz4rch6t+/8j0kEsgPqnjD
falCOFAoPh/jqICX95sQ79I9BOxlvQE5X7XCY6bHChv6+lqC1SZMYrsknCsyG1wbh0ANUpwC
fuV1tn8P23nAz5cjIszIQoojbadMhglJnJsfo5mL295qwJaGfF1wB6XscN8yr5YAizhW9DEf
8b6G1ZOPPv0w3HT7hGfm7rGs7cB8t9wME7z+nQiM96WG/CD1yaHv64CCno3p7I1KyW665M7y
cNw3mwes7drkdAVLQN8HJ9wkNUGyWsiCfJ1KWDDA2ZkOx4gWMVGGAswPF/sDPVXMf8ecVNfn
bw9IYvx13Kgw/KpLgKx/y4JNl6qxtfdEXnEGm9VQWzXVNOz5QrkoLyM2+Rope+pupafzpmSI
ZoIpiMt8Ws4USFcHxt4JD35h7ZTYMzZIG98CmYTOwiaCybWWimaa9SU+1jbl7tGBCCQb1ajS
30g9NWvc6G4e+Z6PMU1u1lcOFGtgN4EAt8yAeCOQIsUbwfV+3La3sfAaYKxM5p/xHR+hspcD
74SL3KlB+Z+x6gKKB4mWF8B/Q8X8P1CP/jsv/b+K2ZLuQs99XZvT2390ORQqILdX0tHf9R7S
Nugj3WKE1wVQU4Kn9Fod7fAyWQCm9XQQqZQ3JXPVQpUQT42EQpALqEDKfaLPSEsH1R6VpOde
AECDhxPuIP/GoO9TrW3oNNDeCR/76GEzqXZosZtzQuReaGSg4NzdKuq4C1CIwhlBM8ZQR3vr
aE96rzU6iye14J0L61ITGw7gP4AubY1DLPJ/gfB9gY3xBeb+WjMuCnIGz+lwBNDn6/Jzd3YW
cZc/SdFSC/fSFtX6920N7KR9kopQsdtVH4DkSa+VbqnvzVoQtu1K8FbyiQt2XWaFNtxFJMnG
EIa8tMPwB9yrTT1YsRgrLfg3v5Wdc1q12+2NUhMRftyLln9XPE2QZC5CFlSf76yo/dcf7+5I
rS+z43H514IQswSswc9w96HI4DzCXbyRS09PoaogMIEGpVO1C4JT14x7meCDG0A1HOvmK/+d
AvfbfcnkshWR1jZLxh4Jq9HOrfEhEdaMilj65bcV85Xz+Z2Hcnk5Vatgb4oxNt8uPgjHOzXM
nUAfXMWPWlmyj2F3xtIIiNFnyii7zzbVM7hMD+VhMX3vI7VSW1Lzpm0aSPb088dDV9dbru7u
NCZWrwDNACqsmu8CmWa+rRCZOezdUHvUjdRRUFDoge3fwdX0MZuyZO7FPgsv8s4AqGixOYj9
4JlXAYiuYi0q+CpgT3S85/W6Sh5LIyN+CXUs38nQx8qA79tUwTh3QkLDtbrWub/McG92vF8Q
wjgPQ/RXpbvKBI9mBMF279k0GKd8XxWdWfULnavZfGg/OF5dO5+G2veaznT/RQlo8rQACnMN
aEmyvj6UO5apnDy2Bf6CTXjGcaNAIrT3FW8NKQOkybf7JX0v8Vel18rNFfYm8sU5rntPZOc8
wjV3WyAC08pdXbWjopppl1oe7POgwjkmjYLvST/FzHui/KD/UTxi6pPUiCdi+zLYvwitHrG3
tmX4SYqnUbp7Ss3oQ0Va1ycpjFXtJ6mNR057D+WzFpw6RZ+kGsC38JIrpXgw0OAI6KRi7XcE
APO1rjbXvLMYehlC88MDAv5Jykq+/x1xOl7yZFFtQbXwV0G92iUr1huAfADZ/foe5fwiz7+W
D7wokH5pMSDuanszMZ+kfv3pJsS3CKbO2Fs/UfXr0xTtbIILi7zVK/dEWY9+bSj+UwNSPWxm
QgZQiSRXSPjLsgORFdN+kLHwHaDhKumT1BWZosYnT5MdQYvjRd17Ue45iJ2sHw/B3tVOwyQ/
48dCfLdd1XLDOvPFBz9J1Y90iF5BLKbSIPwTQJEDCmHh+jb1gzjN3Wks7wsmxAbYSBr5P5rV
YALDIb7T5w/dhdiRF012OYkyG0MO5T+83LkvFWm+bfW0bo/3UWZ16JRy9rUtOa+N6l0Venrc
yLRSj0fSapz/tDnqo5PILRYuvqFEj/3/2HvzsKaSbW84SAvdTrQioEzxSAsCAiLzkERbEFuB
iBAjsw0KAjLPEBJpWhEUoo3ITGxQRgERIkOAgEwyGyGAkDBDIMyEKZCEt+w+9/3O6ff5+pxz
7z33+Z7vdf8BWbvWrr332lWr1lpVtX5PffBuE8E+/cKrVieia+aP0SgtzfK9PKNnCxJdFPdX
l2rmITTrSbH4y77CSCWMSvqwRunrz601n+tCe4Vryb5nP+2RxnmvccqnuO2Akp20lrK+ChFd
dOFD9wyBeFPyrRaftti9wY8Ysf5nesGwvR4/dm8oRTxtBn1lGezwibR26PKU+3XmyCq3le+9
5YAEUoLbRVxNsa1x3ENF+Dz2dJ+xukV4OtNfGrY/2XGF39vkMEV6/+FGVekXRjf+Pxnw+sea
BfJnK6Z2IPfeq8gnO4ueLu96sRRp2r1xgBDviRAfOrHd66V0azAxJXCmPiun2MSvA6w3NjAf
Nbo3smkv+Y3AP3HfLyxfJPBFAl8k8EUCXyTwRQJfJPBFAl8k8EUCXyTwRQJfJPBFAl8k8EUC
XyTwRQJfJPBFAl8k8EUCXyTwRQJfJPBFAl8k8EUCXyTwRQJfJPBFAl8k8EUCXyTwRQL/F0hA
9x7vtFemGHZg1A556G1jwWRIYt5QuF2+g8YeEmW0wTAqv35RHYMx8mAhm4P1b8yP/F8gk3/7
Kw666j5LyxwZpmrc4dw5dcpKdp6TmlI6QHR9sEJF+RsbqkpXvUeoV6Mv96lzwuwNe4r990nm
HZ989Mq6h04MiFpBGfq1N5qxxs5V/ouPyofvne5or+5pNmutTgiZnLXxKoxWRvk45bmUFW6q
GxhvjslnJTvI9Dx4gD92Zve/WPm/xM43mdynoV/q3mGv5TnLwY7y0nJnKsRU1U6vlIkqkfo3
5qnqfR6VCkXVAKwIJHWNlZXlowdc436SvPhhhkaD0ysvTHxUJNkm+5ZWtQVfk51EnDBGezil
Lw83S3HOMu6CZxGItXOSFdBob5/L1+5fz3xXEbDmbXjYqEgDGc3HGMCfsamcOSocle/NitRG
z+TXplhKZAvQvdEFA/nFsLr+ALJwuXuNwpIm+tu3vSP5vR/X7mBAYhO0TUTJ7+85vlbQWLbe
K5e9IV2RPXOdvh2i6YESVdrYUpg6JiWkmLRgteTR8Wjox3JnvI9cXbLyAm2PQtQayeSDrx4u
xkaCXpbbPFBl9Sm5Y4BRlzVEKHKYQFlsUUQXjN/rJf5LkvzPMGcV2rE/TOn5+e+uo6wtyLp+
IgV6e7yqFpbxpFcPm5REatAzqKJ3MDF5BesZDpOqIlR1TBgqCBW4N/6Pd5Pm68oWLksQ1Lk0
JvhtOS6XY9q3ysGcwhiXZyjkNWf5Fi/nFz4gHEYDGGsXwtXCbuau06sh431i5SXZy4puywic
m14R1JP6ctLlk3iTbXDwNdf3qYkkZCYtqQIlPK05JZ+XGx2K9KBPiOr+8dZ/QmvHdFdpPmv+
6Nq3UTj9UZOXZOg3kK9l0UGMckhmpvd0aymjDjcA9AfyIym1rakKjx3IU+h+3Md2IcZZXkWh
NXlSsN5+tYSf/QFR6PZskX1uqY97qpbnJzSbPEniXcFo7EAun0ak8f8Ll0o/MfSzyUh5Nhud
m3c8zzUrtKFh67XQc/AO/lJdjTzhOymsmKrNX0v99vZsZg3lFow7UKUnW8fONd3m1IPk7uU+
Jxs+aDPq5025LfMmVbCOeyGV2QxDMdmbUlvUQfS8GbaxVRnkZQSawdhEw4AtK6v/Wuj1n0jo
D0Vn00u27mOhCskHNKU9DB9abs/yQxXopHhzk22ze2k+JwuPh6KMbco8arqH9BXkCacMItwo
bgg9xWfulKi4pJD5R0qz8Z7idP8Oi08Zr05dmko+jr0gm5eXXxpEoqpNJu2++4f7/UPy35ff
6I+3FjQZhx5axR7wKvL3NrItTKwftLLlfn8bAM1otLoQzhOhw2if2xnwsCv7nNaqna/SQnqx
o71nXFu6qGcKp27Z5bf5rLVOVTIJBICGtfDTUsh5dupI6I89PN5dkysgP6Oljnb/9T5ftTNK
/SCPItqDTrIxN6yUj11DoQDg3YOopKTdjixP6qLY2c6OfoAU+yMzWFQ2/6gESbcvw9HcJij7
Y4BzY2BZbgCjCekpItKtekXxfFSqx9jiUX/dNY+TyxJ2tDJmEUU+U+9M5dwAgSeVmFjmCvc/
3IAZ8bvr6jhh30D2lBPltmkVoEQGKzxys/IU8N81NMd+dyghYeEFrdNLTk1MWCZweGjbo6fB
llImwnyDVestiYMtWiXin+D33MZfi1rZNRZ8fQpsQuZ8cr+0lvYwxU6UmE0xagzjP5PzqEo8
e91ORWTQHCETQDjMlpXPrz4tPQaB8HdqL7cL7mV79pdthjcqYVP3Kch9KPYuMLBp7SIPVlk2
E4dkKxm0rMRlqnqD8U/Pgx8w69tVRNXOlKYfufUZuoho0SE63Z0fvabXExJv05a46IGJG2g3
G2wZRU0+vh8a4bMA+5Rr0xt4baSHmPb96kZFQs4t2vtqG87WbFJe2CdBcQjM8eeqPl/hWk6K
mLZbY0FdlkN/4ny2bUtq6p7M3lS3IZGitOG6RekXtac2nsJfbZ+PTo4VEqoI717SxI635qUc
SR6C+ZrGJflgzEy6Dji9sprCxGmgPJzJzWZjWd/XO4RujkCf/7E5/ffS+7AV1lyvjpfzPLBF
vjDiGGhRf3fwiVRmBEcvq81q1R85G5V2AGei3bxNOLc9N2I18neMf04U1ZSmEMaclfWs3QYq
Rui9G/4pxGbcLyWOYsdd8SWFPdt3s36rQOBqJXRGmbD9rG/orFYt5Ou2TiG4jcKkikmMIlzO
e/FRm3RMRJm3iqGIuQEnhpaSlnXKmmDeqIHaFnc67no3R1rPl9u+AQV9YZZ2vv2Dnx4R+et0
KHYySPspBfG68DbBoBoKdkk2TzxY2aVLRaGoGiiL9vaNpKTl9ogl6bh3dje1Z2rbZ4OrFMew
pOcUj6I9XvM3O9oV0+E7EGiM77sS+82ei0qIOI/8FOuHyc8E95dvR4YTtUxtLRxHZrXXTMSd
MgMwZobv85y8wQ5aUmBSmcXGMkXN5Iyo6J/L529Kd/H557CsBoaGl7AHes6VTmdP0avCqm5i
//Lz3q//hu2f+fmfRBH8Z6r+I8+eJ8yuTmxktTyxDbGXOKh7Py0i3vTaXGdjIQC6OE61nf8R
qJq8h/7Nkb5lQdEzZUjsKhry6rld4EWcWqrQHV3C8Idv8iCQXS8ri1m5hNzZYJuCpTbLFF0n
wQiJejXxGuqtm8GOuxTwXNuDAx4GwW6JGaFBIobnrj9/THvto9Js51qIyr1TIAf9YVBUueNV
TGM+FfVKuxB+6aGZsUngLP7aySwHuVIUCjYiHPf9dERJwQ1ziQT8QKfpne5l6o3pZ6+sssJu
Ry/0qQEwW5AlTFvapcn0YarJoK7dhZK69O9mBltJ6h1dUbqxKg20yjGEoysj0jY/PkxyAE+Y
vRfsYUIs1wyoTiNu2D1MeuG6dYtZzDrte4rquvbwKdulMDpD9jupyAiOzbD+vjHpJw1DUkzq
DTdd2HRhVDrLlVuxjHaYh43Xl9nCZvIIVmDgbjAWMKiq9O5zZUHfSQlGb5uWZ/TmOtd21Cdz
FJbUbs+LFc+yV6kT6ZRRc3WqtMJz6WcQ7ZjBylKpGCIxjFGpsTdIFx55L/RKZ0tRi2tjnmwl
k807SRB7hrnb7JkCd9aK1NC36tHijVbjoD8Uo4IqBeJQYfMz/aroJsqAvrlPkQhakRtvzlI1
PhvUqE61NTNRb6eqDRyXaT7zTS5IyXJJ2VG7JdthwXZYG6Pz4c3Mw2f5ve5o3yskD0y8eSTS
NRefFpDvO5EYFbXwDfLF6oXRW6kXM23Gscy2lvnxiqjscUfrpDXOnqyJdfbQt7qB34Ycnxx4
VxH3rlNn8H1bVtTSaSJXwd3Mp8i8xjCZmRzmGX9RkRHDqVn2TLDtY+PHeinvKSXK3VqqKkFm
gWJnepCeBsUhUcnKRrF6DWBfeVB0RtIyf2e4F11Wp4mq/STDfrI5SpwYHLIwWL/aS+sg21B9
VUwzHJKX8/Owl0iwmaUwyzI16cthE6f8/tiq/3tpPnyfIq7waGk1eZij8eHmnj/WfrzMAqlq
JxvmtOn49UG1X7tmso+A3bbTiLDUvTZ/5P0TWgTWx++7pQwytSV5MDwvjblWvmTqscNEq0ID
psLw50iL7xVWhROc/bBTbiHzUkLBLttt98sTK9dTYnL7ixNynbuxVNJ6boWJ2PFU3dzoMYUH
eccBigQsC/N8CqFjn2y/yX1HZhVmcr8S6kRPJfAQXkWcWbA/8hw/K579cgeCpynuQHSZiA9n
OZNYF9z4BoD866zEr3779xeL6WU79kVmj43ZJjuRRG+XWXRPJEU7yJVV7X8PwVct+Jq99Pm1
DtMx6vmRrZd9La9Az/2G7XLjXEV2Fb0wcbkj34ITZmfKGjEbki1/7DhDCnSaGA5NuTqkV2/Z
QiUWOMpWVc3RkjmKCYVU2FQugXhQ+uSDz8ddH33N0WfcMd7iu36MxgC7kkfKQQ10yiqpqh1u
bkHbmquaVMovLlMBlq7RsxuicvUHolIIV7pPMSXtxzWlYxJ8QFotrfPd2WfcN/AnLMUUM/RP
rhibe+QsTuQ5Nh1oI4X85TZxZkP5jinc2aozIyklgBgm+vBZIWqwUdg2/2nHwWHqkus6HyT4
0eT5GP1Cj71WWoffTmousRTy0hCWdYWeM2x6VU1kYKkxStoyozyrHA+NGHC4qR8kJvUxLu3U
wslpjZXFBq6TTyCc3rBqW53yxD60MjbNICCv0R/ZQi+RIiGf5WPt46kW96Lv/kkb+buiY2JW
eI2CgvkdiODIvIGEaTTWfbB5sMlo7MjZ1/90JX+t8ciWB6JPngovRPOgj2/+86Pe3z3QP0Hs
0mSZdRG+1rnYp15dTF5V6s5zTW76innkbSnmstjJ1ZMVKDK+cH4Wu2/TAvnLdweFQv2riw+j
HSP1v6pA+Q7XtvauJT7AW1enaDLI7OtfGY1nm3W6lLPCE5676X3sHRxkF6vbfQyYjKon+kSt
UGw/JRf1GTdHu6Sk79sq/UkVsrdzRmjKN3w+0nx7i0/jLETaskNIXDUYM6K8PNa4+H2+4oVu
ZowudfhJNSHAoVdDWNoyimQrLebZ32jO5JcosL/WQ+Raa9n2lnhMuYrHGrZXVaVQg1BD1T65
ecDQv+aUm5S0NiFNb0GfYtO6l/su9YspkPFlr3PSzL1vDSyjnHfRzUTMjLfiaXl5St2T8xod
tlnyj28qEt++pX/S8zUd0Lt8ofGjn7uM9CPjU6esvQ3zRXNje7qNsfanuoIJkhHxkG/P59nL
VdofCbJPaeImvTC7wP50Pf7mZMdD71FmpW35YgA9rOYSyWKjwmCTQdSgjC/lzh1+tnfP9Gwz
Jy2hCYYM123ydBcL6y9SQWZU1mj25uM9XDeHr8IONWodD7NMufZc7AzkmNh13umJO+n2q3Zi
LsG+zioPdIsi4g/CsgoQQnWkAIJYXDVz2ZHRfE86R/6mKO6j4tP9/L6W76dwD5INX80GHSWO
zOsbp2BFcshuZZnOJmpjeS55YQdovKZKZdTgu6you2/PQgSfsU60LbRO2d8TL9sXmH6CPJfi
G2rctaRH7y7JzQrbe5zGdiztcs1ct+iw6Io+F6u8NJA81EBP7m2hldc8o5buPy9j3FkyXGX9
vsQnP1A+as1BIQuDzdHDK0tebRspknqLEF72ke0QP1CCD1V2CA0K8kdNB6vjYpxIT7eft7jK
AuWYFBW13FCLOPtPNNr/PIsAwqaAV+70EeRhwy31nXt88o9VRdPN9BuDktZSRh8dM+iMRGSl
OnK7nnPXvZS8/sj6J/RVsesFlGXfFGtxJS09SllAISFC3WAzg5SgctMY5Fnfgk1/JUtRTy0I
tar98NqxxjQz3u1Qe8garVA+e76d/2S1nHEjxe8VDCqAF5Tglx7SSA5zPZklnwWbvutR+9tt
r+DNsYiby6QkutvFuo5V24rXrkUeM37m6BAFkkfRHGmotAOdkYc5uUJx7T/u/lBspWiwqanE
drDP7WHAPMX4c/ByHcQOJdu7cvaF63wzKWYw6fyztp+rlX/yxsJ4saeaj7OJqpZSn+qo+T1D
u5ck2+2gbCJqExVS/O0hL4hfp8oS3nG5LTKZvK888oUZIXNW1IluNgATlmbMqQzkOY4rm6Fd
c/P78NCgpKh9ftrbdTEtbYtigXLfaCGnk0IO2AwS4w4Hqd8aRx20fRTt2BM9TzWxJXW5JGVh
vI+NlZs1FDTXDX0333nSXZEXmTdf/X2v/4OkxKw5cwTUtWb4dWFUXnQmNSv37s3i11qFUQ0x
+Ofe/O5Dq7Yq3jPlA1knzOGI76s9FLPkevOOF3ZLv2io1Vn6k6/1t0V8kMqe4AJ3T89NhKDr
sQE/c5bHEHzoDOLbd7t//lu+f+b3/1RoROQvvUgHz5i+poKYBOJbD9Kr/hJiFr2tEpsWejxa
cZU+s+R0+7PZ3rBOsBFhcy+Uk7mtgXj2Q2BfQKA9bg93ILRsAPWa+Ia8xB9Fk4CGzOtd81wo
IBRM964oJJ/qy3HZ8J6psDAKjnaqdKxqCKkd5Qum/4XT6QV7zcThzsrmQHa90f20/H2V1K/1
Qwd+HE5MQ+vJeDlTjNe5QtL4c8XCs40o+2pYdagZ/LWCsZgJhfzz9UGjhAJ0NPt6D+fqcDKx
1d1uCYN9XJ+Xr24uzIN2mwOwWonZXdi7ELiKJfHJZ6xLMx/qb1iXicmuWY6lDQ1shxtHBn0t
34VihKYUcV5kcdrgOwrxYUl2N9zKq8jAvilqbeoUvUwYXq4buC+w82W9tIx77PEZYXS2ZmdR
VN5AVjIpyNdpXmNTmJUX7ZSEvyZ746j29ECNADlzZLYStVl9L9fRqq2pAlpCBLZKdHV/4mNP
PuNqVy2TeaNE919Lc0kajtOkS0PICKZ5qIzCDiRykeL0XrH/qJSPdan3W4Q87eQH1VeNhdto
Qfj8QaZ9a9lRrbBhg+rrsBcg5I2oNlHfZ1LdOXzIe+kOxbXz1jwCUZe93jaAhbXFIeAeKJvt
5w9rWzbuH60QT9gf8CwzQcOEUyC0i/spv02DijfowhGGbkr9m+PPjmutw7P33VU8QSbs/X5H
d939Q6P/uoAq3I6OIljWHHn3lfG075ZLE4K2JTTsvKvvD5x/Rgro088HIqbKUnnyTG/f+mwJ
dOZlPDQaJo93E3ccLoEvevl7mK6XTbUlxx6eFrEGUMpaTmlPQmLpHEVNFfOQibB7leG/fPvb
HQ5ENA99Zw1y8+3WIgu75SVWlKnrV80F5bfYGWoyPtwG6c7nKMjKfc5vzqhM2lfEx4WQyorQ
Wso2hbnJ+XnOVe3tbKebhxKynL8uLid19FJLcsfNn2S56wUGXrhVmbsoEmLl8lCKazqUVIFX
E558kLibC+6aN/RW/3hTmWndeKGAhrpdhS29KJcWjbVcJt50CGQvH540Cl7TP7LGh6qtOvBY
/0pRqE/Jtbb298ksTVliXLaZCDKkWh731iR3cTYI7Wl2kGlYvsanXftnAvubsq92zZpNEYnV
5BGOVE6ECwXZQQraDnrPOf+16O8S+Rvef/CTH2rSvDWpm01t3YHUr+z7qfYf8P9XikVe9i5u
Wy/Vz0wFjpzcbfATq/LvYrG7j/oHDaEDVbQtB/bRFz1dpsU9EkxU4QpOkyK32tfXGN1mCwa7
Dkd8V2P+FpYu6UOph6W5PsiokiqJsDMwCMAb04liRV2kgEnfhYhe8JhXyZZpeOezU+jvh66X
Gqp7FJQ4kFiDzdcuaAw+yyOs2IVLjxw7dkZ+Qi+INmxD8Mq2q/alKFsNrpdWMheHXFMVmA3A
ityBnF3mLIV++AvAuoVpBvl3aB12G0tnjslOflRz7V5enW6sLXPIt6C4vZuHzWY5V3X4DjcJ
yXAmaoDXFiA1zzMSZr++LtsxqJ2icvt2qN6utbb+ygMpMVmWFb5lkbYk0dwyE1TAcmBilmwo
P+jWfLFFsNSL3UHFHWWHytJj4i5cINgViAcoMRWiMuZf6WkuO0yqSVu5rgrtkaNGkyKaA+73
UwPfzlECnCId8gdiq3McZxKfzcSybGf75MsMArYUnh89e3vLTjPqxY3p8jCuSva4VSNxuG3E
zNgcifM5JvHv/Nrgbf5nHPYjDcuhvjz3zeLqQEJGiFzjfGMOEyuG5YllTtAqhjdqfwk7+ZY8
9TBNqYCAIh8YGuommlwtnx/Dz1nNmavNoZ4Yb8PCQ8ULi17etgqbt7buWVbnSIZgFD/poHOJ
rrSQNbRFg0HoGaH9dP1tn8CSNws3ZvVr590SCjCpLn0eruoNW0OiSmLyiyzShiB/9tqpiUhz
8pFNWlBdRl52XdR7yppkSChXpD3EQQYA3b/x2oHESkqOEVX1NcZi+2jETTXUNT/6tY7tHoNg
jKIFdbR7oYGfdBcCuce10YqnF7Q05b4YII2YMvv86NJOcqUdqraW5gfnmuRc2PQ6w7ulCw+s
pTvQm5kNKasG9LILhF/HqIPNh6laKvb4AJfmjXDX5xDI8WzzebxzqM+PNYrJx1+lVV+Trnio
JsURfzVhJibHiWmjLPwUXncr7WBZTLvpd8uKkSzfVRj6fEOvfAaAkFI2GEh6sAOZlSEXQ8r+
WWP4v9WcIuDcrOwGmX8p3zhQkeIpZPJxk5KUkvTElxzu1Fjtk7eARntelc9yCrtr06HPXfG0
j0uE5S/QK6ABd127u/By/mydewPSCzbN9BfipazuFq6d6Y/r9qQcg7B+gQL9JZ9IdFxiWswC
s/SshjzD+WlIVWrjnEqgZQn0qfhT1stWlJ2pY1DYwuxbmc2z2wACwCS/pT3wAJdeHwOtF6T5
xrSCOIrjpvfCgvFF3hH4eKq0hXNLO35/GL0rEtrEv6BTPXkVk9ri1cZVeMfzgpp1dCmALFZV
hH2Ij+1Qxrk1yUGfIsR2yxKJqwwmMKHkPufWhh3Iovy74VUy8rcTt1q7OC+1LXmJLsMgM9bW
nI4lmA0tAvqlW0oPJM4qrI8vYl9aKuKe6SanC7yU7PGpC5zENC9Vkn8dEsfsQCT3h+gkTdYw
Wtk/jYKkq5VLcpsf3CjtaJUyOLrZTpo654GR56mLr3qzwtFwdFNaJLq4fImxWetm1sTba8M+
oHInrzqmLgrRxG8Vq7oUTX48ltWV39+n6rx5ozc7mqNUNKEdT3Rd10h14R3RcBlz3j/LPnBs
HlxjBd5jn3jp8t4bfSsS457UOdcA582z1GzMXB7PKOh23JyrKG6Z/2raaGkeW6r7BbI4zQ2A
t2nI0yVci57QrG5uHw0A2ciEymkgM6xMoQtr7iaF9yGsiZhJnaC+ZvSTjbbPbYhnJcFNjERx
DAAYfRueiRDAJL2V4/kgwGVtjQRZE3Bamm9bbA75y5owT52fqWxNONEatoTdtOiayxzmrwoZ
+TyW/5eOfzCoCehhuG6oWc6Et73uZNcBd4+9iba8AFjlKZBD2lWGJnhvRtyd63ztHWW5xjbt
iaf4MC65MCcLTouQ37fvVJiWoIRpQ2Zd8UPXh6IzazlZx4/DpgVGIJDdlv71H+TzxX62zqCr
Cht2OO+a21q2cEAbVY/QNupQx6rhT5KpHeZxtooCpPTDt7fWc+8ZYNpRASrrG4vt28+TP7/x
4C1miMfuClJajqMjBYS9ylwyZOgAzHnRw4kdONqrQUubaepIyDLJc8ottitxqIrOgDt1iJi0
Mhjmxu8V21KHCqzgY4O6hH3BP2ZfydLQQ405LdDyUY4ow+RMosWoVT6x1TVP1pHiAWabxpdc
Fgcqvy8Iv2l7QgdB3biwXtw+tfXRrbgsYJWWeWeQbNCtsxXpucvHJWploETYwtDuB5LqQOhg
jtiu/9LH+ccXN8/Gk/v2DdgNL/LEp//PJTUHrfPkEouE4SUY1Z+/TvrAWO1+hKtYhdZ07i78
x3X/Bwd/9vJDP6yDtlH1BhigoA1SFbmu3mgsPatToy0N5NTb58i3aJPhe/lJ6zUGXf/sh7fP
4BXla7a7qoUvrdI/ZYsd8rAnBpD6XLLHCwNW9ziczHJZHMLqwq7MpN6aUozRx/Uq9GoXN0ih
beZ9PK7XVwTWvmtMWjs1Thmgk8UeVpkPhVk+Dq6F9Na3t3e/KXB2YaOL39xBiynZldhQbCsz
W1AaRrGysKCveicj8whS2mpJkc+9L2vJPSB9n5RFb1Vb2KCqKrFl83VQQQvGRnMqJmawjON5
+s/LF/Z7Z0dKYvoTbQxHsaPEvJmjadNgQYFWsaeB0T2ntYplkNIwaNF4K05YWL3dODIYIlLc
y7AqbN6r7VbmwHBVKxOwu0OZ7Xh0O0OOttqwPZJz2hZ9QWmX+hB6jetR6UjRCBtPsNUIWS9w
GKMYhz212aiDn4VAgnHqIbv1Mp/VyE8LG5tYpuhdzxjGXZ1wsEmWo+XJP3a8/k3BRwmripes
hxERhl0CGjGk3FE0VONwtyFviPuA4CX2W+P/j0/z+3+hzuXZ8FFzaavMYUFGhjVeCegITMe2
6mS10aezCDlFcf0K0UxOkGD71KhRgnI7rvMs3Plq93gbAQ9llYIM71C1fBezyZ5lGV4IYT1i
yr9alKBcdE+60xA6L9iwILWL8EsfSM/sAzyR23A5P/c87GVvlydzkyAH9W11Jn3blPALXdw4
VOcteZl/rGC+RJ6tRM9oLiF81ofqzOHBQ4Rfhir3herGEzhnu/MfcPQzJ8qm6HhnCwBN/kAc
5X3+vh+GcFCzEd5ZhIfWC8TbWI2ioHINHbnIkgJHo6W6l+ij2ueMWpbRzt1zs4nFnNMuKKDb
zVYwdp8stnV53+GO7Fco36ithCNjJA4RnL1Hm5fvUvITsRDA4jO6BgdQMPhxvkz7M5hKazYc
DnLcOvvfaF5+TilKPmClxClJjD1qPrdAhyNiBGJselcqDNbzk+CiBhzueDZIbEqYLZp0412t
AmEH49JFxl1eJe8aeVLxHXm1zRRkL/1XSsO/rqxYJkVI/jBJcp+20R1baKVbxccsRiYEChn2
LasVDRabCoSpBeQHeKAszETQhmoWzR5r5tKv+In/tYCOVmwKUhHLqm6QirkX7yYm4+2Nvvbx
zjBJWN2qSAZNck1mPlhejyqUDQ2pjY9fvTSuj4k8sm6xrXlmfBNCKcrwlByfBAimcXPdSdDG
i+qK07+2f4Upik6F53+qSIE2fD7zst0PUxSVqpU//aZknH0q4vua6KpOo9bNyHdbNQ+v9Miw
JSMu/5/zQ7Eu5PFFYAn8Nj+Exfp0qQ8vL94jMGyNtr5GyGX0qe9Alhn3yAzb81vfAnpY4+AO
5C1HmVAIVsp9CGfBxIJz8dyS0Z+5AV28n4WSpus6bIK1cPuyZ98Grp7GIC/A3RxbKstdELYs
RAb/FIB9sZc2aakPXtfAkKefd6fH2HwyirMd7dkWb0Ku3sCgKKSU6yuuNDjB0fI9LxakKtfx
9ZY2nr+HLn41xLsh7u8XOLWgnxCgYddE9GU/dkFRNlK2MM/WUXZNZejJ0v0KledYkcg4fmfq
nNsT9m2BeNvjwc3ZLZnul6pjAvBtF9XzZqCdt+AmxLd56xqzCJDpfPUZ4wJBtvODwrqWgNZk
jrjIajrDivCkX1wD2zRazykDbfaSR8AMW/roDHFb4iH/Cl3gXphixWj2RNAPUfYfFkzUVib4
Pe0vY4On2dJ7BoumA5Xj2D7PodC0wC70xv7PmUARq6+xWH8GDEHT4rFAB/5Yy5kdCsGV3wEZ
fytBIabrMi9EhjuuAFKMquNnznLSE/VZzdtNNiAFcClh5iw7PTF1pXm7kQ5o9d/oJMkVo4Rw
S+mp6pe4HwQbVjsY9/Wrvmnd0Kg+g3saMRXi4kuWtvvKaTu5MwXRyrcM02DTs9tqw87TqH5s
3hUgVQ8WEZlwtzK7IvcGcnmEG5tGWwL5RQXcnnIP/BrJVgE251eMwq73XvZ+5qu69xETVUI5
E56Ey4i/vJNiID8wBjgJ4WtcJxveJ7a0yOIWNkIXceIDdgdiZXTFGiFTDz9hvqoTz7v8HGe1
caUNnOhUNPJMaiUjfEagvbM9pl3v5+CqRh+G2wgV1+HO4WGGc2xNtIRjWXsfAeHzHIv8OiTW
cuUOT7/5Q1Muwufcsr4mE+HcQtT5Gf8r8RWAIG+Y63yhiUlxTvp6S9LWBzvBv67ZddUVa+Tp
qyTdJFvNqw1riuh5Q3hCCU7CO0rY70BuwDN/YP6IjDOe8kBMBQpu863NSGc9ZZ9mp+HZ1bVC
w+eYbkheftL0DkTMi2/UXzObOhWC+AiBafT0EpSN1Cg8+IhgO9PWOHeFwdKBskgR3OfsNLfc
MLitdVLOuucsSCEr2L6g/NKC84zU3hCqYwUyxp5b1svPlYKeKGc/xTur2QE9jXDE+h8rmaRL
NjZTJtx8N25CvRuVM99iSGX45VUUs3vjBtSsKTbzGobUFvtk1SwXSX8Btadu5xAJypvjBmFS
r2a2S4H1Pqn7wJKttANp7J9nXWerbdzm32JW3rNkK8ssX4A/PDTHHbyBsxO8oog40cCTMV+9
bs52558K7mMwu1q8HcPMB6dey3PehrP0N3xHnSc2G0m5W0rwrsk3QknMb7o0CHHjHuPZ06Uc
+7abUOEetzSS+UChvtthrijhHvsOPzP9Rep898R458uFmURhzln4eC5ar4etvUxYmBH324HI
CdL8TzN+IshJsWB0MWPCxMh2bFbVcnNc7Cf4wj0wNX1BsMdfh/GLfqo/mXfjIzmTn6mb7tsB
XZwJ5Ep/xGVEMHUJrC7oIsN+S+cFzlBwkfGcRQEkekvrd/JXVjeXls0Vp+xAMvjY06lruECV
7ZLMHYiB4Jy/ISNLrmq5SY5h+ulzOfA2clNXzFZsbhbbU9wLFFccz2od9kcxQgi/jBXux3bS
uskn7rpRqIFpydjLD7ZQ2E56HedZeIHRNVN/+ZXFtENFzp5j2Et84ESn78zKQgcJXfLckXdR
gAizYbdmt5VrNtp1RritXNRwYbI6leC2aBfU3LQF71J4ARLN83JZmbwzUJ0mxE3gy0Vet/N0
WeE5KKz7XdqBnPjg2t2rmJKzMn7nUnWa6CJrpCf7FU5zebL77VfbumDl6QxkO/sVQfPJJKU8
GN6Jj+N+J/6k1z7lyMo8T7KrJHMSdwnIOXmqUp/kfL97buYo4WPdmpRzxSu8cvdo6rauqedq
bViz1QHXzLaSckeElS85C8iZ4msO3RZ5x96iErjq0OLeuGT8Jv7dpy1qDs4ECLrbF7kDORhk
yXPtQWSD9Mkz7CxgGmDAkKvhiugO32avcj7uQBqURXYgyUToTC03u8BI3Rsh9VrbUpVVWn0B
kfAZ+gPTZtSm7V2vUBMpeAU/6bM/RLfP9yD01Gjkgbz1U85GK0kC1VJ3gtbAmQt1BAc1x80Z
AaLUnU06OCHQTHCYssEdPdabWVB2JHMCgAY697e24kf5rdLLJNH4uJFn3QRHhCxfAdK6UNao
ZUntDrI476bR0rl8pPXQX8AJCY+u4lf2+BH+q+llg1Pwy3fFD2+LT07zTh5S+wX+UoRl39C+
IDrLUc50dx7sVmYmBgclx1he8+h2rZQvpLe6lhlTYPlR0aR2pEvUPIz08/jvlt1uF38Sr5dz
eis4bXMPn9mxqoXHPGdt6X5/BPm5sAWELwavwRa55WvUtHcNpRFkzbJ/QFh0hK8aDTwQRI8e
0MoOKnnzejtwNawxa2B+1VJzfCVC7gao+dqw9SN7oZ9pWh3zKwWNcW5kyrgxmFURgezNma6I
s124FqgUzVycCdtIM1GdNdc+IhL26THyNQRysDsHsz5Bik4jczKGxzXP4bUhu7CrK5MyT3ln
XEOwFY3KGjN6kV4NAJENOpiSKNLhPT4fQKrZHWx2cDz5lFGEVJU/VWpETC9rpjIgJtvRRfyC
APzAAZFk1eXi4gJzD2qKhYGhupmh6kET1YPgGDjOV/G7HH7/K/iUdb65GvEM+43HAVVX8d1c
zzH960RHZEmAUghsuy+H6JFcaIz8lTKKFkbZZpcarEelU/5iq9bHH4JtTqCLwtJCFlnHNtPL
thk9IwL3eJhqzge4c8ECb01bsGz8U28RTlMoaja4AWF+dzAAluawA+FBMEjrmu94zeHWrrA0
tMwO5Gu4XEGfMNmxll4k3Zn9BPEYKtzLiCYUj8T24J2vtDwG/FglbPNPKRdgqbQkzvPN9Le0
H7l4AU2/UB1Lc84xDKq3D4C6FI9MteKdeGCU3Sfu718yHjgXdK54/FNFAohTjBW+tfHn4r8J
kAxVS0I085sWvpUM4+L3BOGkO3RKOEHqzFn7drm5IOv69+t3GMiVuy7U3rLErv6ltsiDc+PO
yJXH4ERRkg5bWmLpIyz1FJt3DYy6VF+dz4PhEaOSbKYw57W4b29mMqJ/7oCoUclLphqnHEog
mHWocM6N2rPzzXipgoxu1mVgv5ejQZ/EZfOBHtiN+386IIezhXUhj0GB8dZhhV8dQcBTkj03
o951sa79ytUGdV3uQHAMRz3Z+Vd4yUJdXS8BBI/MUhmA4MGZ8LNmdHJ2IFGSAIlDw3kHYgJw
bIB+2IEcKrfnuXYB/haA64PmmIxGsrP1tm6ATySogVtG3Fdd+0wiEPDQ5K7Nl/UqrM+6Bou0
HHLDjWXvl5kFJLBnLGvcsgHQ56Yb1EoN8TJiJaSdZY/Y1qoP2qIkcE9C1YAuA1nRPy1INvc+
Kvps4Lyp+gS0T7gXE14yAawgwfa1uKmPOI5E5JM1gtznXPKvIjVLJj6Wh0Eti4AVBMpjp4Yw
ydha/Ks+8gtgVzayfBHcrh+be63JXcAAamAFwi9LiMLf0HhBoHVIpHxaMS8e76coAlKtd28K
e8Xmk9nc7XicrlAUExi/+9hnAu6EikN3IBMALgfDOIBJ2v4eFnMAsRwxFlLFioGboF2ai38F
AnoAFab2pUatuKVYwWL2DINhHmYT3EaQHRtUnbutSR4A9dE777C1TGl4x7Ov9+swqZ0/s7Xu
DwMKAM/cgMvla+n6TgxtSYZK4MRAW1ZnMus7S9la6zHSTUP1O5BaoejKQlYJ3FTGxWzOnQad
Cs9Go2ID5Voa5nUJjh4zACY2wrQwL3WxKy6632Jbwtfks1nsj2REY1LtmrL7B0PsV71cqFTF
dJcV73QqvGngIy6T3zQkg9UNN9U2CJVwNuJFg9ZgwMjfrsDR06BbxxAImHB60cLkX1GjsCFQ
GILexpsD5hAFwlmFh+BIT3cgmVaI1bNYbIgYKGzFUQqgWyeh6RFdRhu++VyJj4iMCBbrg840
b8EfsCYbrV7BYoM39Hcg9E7yqu/F324JY6RsV4LuZuRHmH7O4bBqgp25XNAAMweQv7F36cfx
eGXkdnH06g0s0hwbLMfl+iDade1/I02DsrncN7h2K0BiusyVg8DFb4A0kp0/F1/lBQFuFqJ9
wHPVC9N1tTOQweWpkdu3An8j0wOduTwNIZZpGlcSqtaTkAZwCHBplzl9oJmeBpaPYWfPDoTc
m8tzr+XdgD7p8Uyr5Bnhdau2xbFiLMhWLEDF6FvR9+lz7u9eRiQBG2YXI53xfrnEB1mcPY47
I9TP6EsfJMg0uQOBExzZj8Nw9kg4Wj/1xpDanMs6OUlwcW3Bd9m3pbF6Ed60G9oesbHFYnOL
WhptufCmfTh1wbXRNb6KibHIg3L9dYSW2yCI69kjzoiLwlwmOB4gt9wWms1jivi2NGBPdhVH
Ba5Y828xKu/TVrz3PhSec5jAXr6Bs8GbSaSbcBtn1lVXyCcgHF65XUaCfsrso7g5y3bOUz6u
XcjDvokhjhvBYQg38QJKoJbkdHTJssYfbR9mIn55jEUe0Y1FTwxJBhEcxwgTdzFdIrqxtBWP
IQSy2K4A6sPH1jdiIux5VN+9C3a9Mgv8U4HDV4HuWc9MJPvKWOMrjrHThnvuk7lZU5dpbX24
7yLWtZBXf1jxUL4FFAzopgNCObS0S3ItRSwVBPcaGQRiL4ww0XATz6SkHQgTNJv1iHWNmpfd
E1R2MoGXCcz22wis4poqQTa7nbYD6fIQWo/YGEswl19xZukgfjPCuasb5j+AUDems4szNSK4
mBWS3LUDCZoKwTXTICEq5i47kF5fGHxhhB/U7o5YSSes3hU6z3RHbNU4Z9MAi3XuKwA3gXXO
5pjUCnX94K9O4M20zwGFugDxX7g0bh3ru2l7FPtQ/KkHB2ey5ftu1X4vRY5Shdg7XgUfgiY0
jwafe6L9t8Pj599/uxDoKn73HV9F7EIR1+NtUJLPpHr/ZhE7OhvuGo1FfAhTnUGaT9YIRXIB
HpKFdOaMctYT0GN0/uqVXPbXwPMW21dxUeWQVems4h1IHnBLGmmQIJhJ5rp+l1FFOWSpMsUo
H7C8+Py6wLcErysNXrcbZuK4A7EHBTHlfOyZzs/1DlWk4Zc3INDDuknNOxDsVACCAVyhc+xl
89ynuE28GmCBlYOwd1c01xiMso06KXg2F8d9ztks66lEcOyTwIDBBMbpegRrbOPq+5VZm3ZQ
jznQx6XQuPLKp80JtlOOvPjf6YrKuOYEL18VKNcOfGlM5wzzB2nb5vZXuLXkDXBPdiHzPJLX
7XtiYcqNPC/Y44l9cRg3j1CtWTCt4H3ANn8bgqfsQIj6DaFla8+xzYe28GaAxNRtl/nfDcOh
TDNLcfOe0OqBNc914BEV+UtmtlVpsxY6c3m1wA29FptpgZtPkIL195CXwrk2lY/MJoeqPPBO
MeeBxkXg8hlmrvqk8RjVuYFOgMYnuPZu7XBmW015i3RHahcHwuWV8zLUgwMXxcY/NbcClSy4
1r4mlNnWIK1kVBLzhNMP7TPqOYNXOaidL90JHLGpWl7l0K/qwUFPGr9e9wYKTVNwbXBNAFxQ
c8KoJNKedRZnJ3RFQb8KOXYqVNuc8wGBKFIhMPWrzMe+CtVGfB5TCH35XXRpO8XF8nUveR7o
7cOMIbyKmFZpqLboDiRJkLG2ypo0Sngk0QRLg/exjnF4ZHhozspyQgCwJfoBwoxa1yIMPAG1
IvNT9zLQNxNrgoxneBWJMhDzw6qAC9Iz9JeAK+TXJ/Ope+lzle1rEgwPvIq0f9C6H0dlim9b
6mLwAH5ji4ro6Ee086/r/uJbBgWgQbiU04hEoPHkGD6IYQb4DBqgV30uf8oiQReXCTyXbnIm
8Nue+ZIBmcZz/kyu6yb41kEXF5N4Tt24z6WJrHro4nwC7xZA/duFWy2aikgy/fGNVo3WEVah
hxL/xTL8tQMkX2TJQ803TEJsQ1SJR7TyRiaxZdnEIiCWNVB5Q3Tfb91sl87at0AZJClf3nyZ
a9i161WB7FACEt+MzlpRcjQO7XOmLewL4cuPioonxDsLCoovXDA1bHW3LHGNKiTFU2G5WcmO
zWpqwLIdT9r9sw+DMhst+X23aiBaskxrShDZkqU8+PGUY5Npvq2w1DjFwUlpvL1hYx4u5T0e
nZN1TskPi9fPcCkv7e8qCmX2HdczmStwjVZIWtu2JBoibksFBq/aTXah6yokVDCL7iQCQqEC
y4MHwBCGru4UW7vJ9199OxWXxZBi365tofdQ8NWaTlohRW5WJnm5RYfwya3N6WtW+MXc5Gm8
WEiG07GD2tLslmxNvZKnC4oOC2nwhQt2fT2zZQ8r1KNdF03tVHDPzIw3M9ZqWCiRoGorJ4w4
U+D7FGef26HNHjOhZXeYmsT9Mpb1JYSIeNdQCrZx4HilIj5Nvf2izmlUoE1qNMnL/pACQQCn
rqWAJ4BReExu4af8cyFhMt7V/HG2soseQ0l9/pdrutyKkUvn1IH0/WNPjm2F3g8l7S3DGd+2
XCeFicK82eceHTlhf/lR8jJ7arTxINrVs/uVVRGjuSG14sHGGB/ut68G/gg9rInSnH2oZowe
6YrQMIqW61nYc3QMui8kzXpYnFrQnOVNRvWE6QS8etShsPDrk3shufnkew5VwavQ88scd/WA
rMR5Y0MY6az/5qiWWVuNbWZzxZaC//XtN0I5IwSzlBrbpOajWwrEI9tEoBCGt6LpK3Meal0U
2w486ToCV1CSc29RuXZsjit6wSJsoJZHjP0VoPlF2pgTMtqq2R583NvV5zwxCfs24xCGKfaT
lUItE82EweET76rBhmCKsxE4kzQRSnADZ5RmwIlBThkIodzzHQwFfmpl3pbS982TVQC+aL7r
xGLcyP2R/GniPvu2IBAGbO6ktyyi+YjBhEXiPpU2DNSsG1gXVakCPdV05C4EXuCFXy8jAJMq
2LXh766LeAo89dusOrjpV06hlZ0p0Fa+DSk1nTHCRhTQRHAXwsdza1JngscJG9HvdyAIF9xn
WjV4krDxsJr32MX+Y/i21OmKKUBW8J64ID6Gr0md1mEQNh4VcWU+Il4Cv76oYhqQ+dzv/krq
zPBGS3i/AGPvc1yyBsQlPblTQPm+jNhgFbKZvFHyRooR75lQnq6NLwXd4mUaDUtre4E1fu5G
+VifrlBVdawp8xMt2X7iPfDkFYLp+W3vaHsAbGQ29nJtb+ZLMT2R4CD/lyC4fwra4iXes5rC
uFqk3EiRXw8UkJt4JV66+pQBL1KmDPaAaQTExGPX7o96qZVVJN87YKKhF3dMw2VGuBNmZyvh
aj43W4q9BJz9i3AvRlv2PLiJD2IJ+Pp42gjyWVNb9qdeBvu1qzmFAax9KvDkemd5N8WfrvpP
MTEV1gDs0nWRBemJjdUf7Eow6z84N6sFGn3Egq4mywVu6xhZPDd7FEoJ35ASD35DUK6uz1n3
f1Q0/Xwr9hGtryvBx2sIlmavsnUSPp4J1QBBPH0NfCGbQOFbkzoS/IrALRh9GhbQwbsv9N2U
Z/aweIVZ/3VJgzF4dUmJH90ITcwYKMtk3ByqFluwrA5JzstagFU64AWly5OWskI74Cqnaq8L
GSI058fnx2WW9x27fvY/es0/+X9fmBZ09imTgAbRGqH3Z/b+k5f9PRsfewB2W5ARbsB2wQdB
41x72O5m66eFWpqaCUoPfXmn+Ke8lhhtUU64qRGocLYLa7KumeBERcwJts+Io+xs1Q6FpYDJ
gtdQ4V9vx2Oe4SPgnTDonGDDfEc1uuW2rt+2dinutbi/u0kBusW9WiEsVQ83J5BmreZMXbFG
XiCAlX+8b12or9c1cCdK1OXX/WYRm+deog8Ehdq3zMFA5O1lP2Ek4lKhmFcnOW50qD//00dV
Bpgayf8Zc7JoYtOxlLnuZ+PCg6jnj5AFPTCEb9bd7TrvPUTUCsRg9ozEdD3z8nWkzs3P/cA7
JS6ysl1rTTg1EluX/2nwujnnurriJDkhFJxRAWGqgLf7diCH9+9h35jMYrTpBI3G2xuWloLt
W+IiPi9bJ32HCq21LdVY6wEAKwuBKECAtRMaXkXc/QDWjX+ruwIsrYizB3bxh3k99mMszgog
v+1ASPZ7ER+4CHACKY/J7+LNY4DdYADENQW0yAufAsT2Wy8y91At7zZUrVVOoWQSAMgjprOE
WMA3vqJjTlBRoqltaL4VY93YTEfqmAGao7mh2SmJExWKmhh8yqyqKvdi0AbBxBwEg2rBy/sH
B/uMMiqeg6m7c9noEzYvUJOTXTdCk6Ue8IDHOYF/alVVVTmH9L1IhD4W9/fRahWxs7NdN6rI
MoN6iaN85FrW7OzsAjwrIgYXwJzJhGJcHqeqel7FVzpnO57/QuFZHY2itraF/o2TJKjPaxd0
92DcHk4VeX7Yp+rBdgLfr/amNZdmV5b2GmyceTO+YCsQE6atI1s0Ub73pVFxjrMRrWb/ni2X
lfP2LV5QAViMoxm+4rHQ+ZEuhdQaHzYhLd8Ld1/cY7hHQ8Iu4X1H1vxcavKrjaxcophnn63f
YHJOhlO0k3xSVlJi0oPHIbW/N2LFywXD62Wjkd3ti7VX9kTtZvhFsnRq1+tzuVxI8nPIPteK
TKKmTvLYZNLK4HAIV23BVey5pNZXKt0Pm9LC49EevYEX4n1CQXjC41zc5xVKig8LCg3M62Kl
x7bKtGCDBMcoH8TPe4J3f/BDlVn4dJAK2znu1osKieuOyLrFjRuiALSLvzP4wajQWujIW+ao
4FTkmNhUyqFU+2j409W+l9u2GeS9H6p09RGP5wfr8ScVW2vuExvV1H0Rwuhc4Tckg+0agqAZ
PexQEDHiIYoe3xST+8o+u6qx4LKgDDI6k4EyytzkJj5gj0SmBkyq4avKbxp4W0eyk7FpPovP
x5mbLFNTArboqjzZwynZNTEqMYMsUENBSIwJ/gJ2hzeSPRVF19q0XvWJKdHALi+UiMFGdIZj
s7DweNTuVL9Nplu5N3FeMZzz3mMPUUoPXumtbktNC3CWEV0zP+jRdKuFfasyu1Esj7AnKnFp
yoWw5+7bv1vE5TXY7DRvd2w+7byTZxg5omA6pKDoXHttR4nYqaHsKuPArLDrecdzEpfBpkpj
Y4Of9JuNh4xcVrzkxOh9Gjq8q/svhYC2gIy7uwlfKM7pWrnrat7t9sslTKpAdxjdHI7DC7yE
aQfLZbfUmsjRe9SyN5fCursJv+RhUvkp1bT2Fp42UPILE28JchA/lUAZBVyMIM1vdaIG0Jqg
5/kexz0CY+zWRCtBTmXQk57C4tyAjwO/X7aUrRM2KD2vBZYhbceeC9bKbmmbom7coRFGIxZ0
9kwwAX/oZXpTHu5nofIJRNz7FR9WCZemQ2gFk2HmcdMrPsslYbQjgCyfcH769YrP4ptqum6S
IM1Hr1UyWCegn7eQYBDB1Dk+KYrY8O8Hywdxc6DQpFUftzDzmtzei+sHFeU/fbDiw3iNaH+G
WALMSpMKiA2f0Q12JPRzoDMzTtoc+GKB0tK4zM3hTbDWK9knBbpdvjTLlWr8HCzKmRh/ugl8
xvpI6PSQCg+CbZbD5Bjx5jlgcLtQDIZHpg5s8gJiw3O0aEs1ktOPcHx6wCITRHoWxHEZm/Yd
4JbfT15FbLiPJmwp3vut3BTlCMqHwMbHjEREB7CmKBUoPHdQ+0de1AhOXWh49uKkNc8kVQUo
sNeIZBDZeOkDfD7ZTjFchi6OdZbLK60B2Jd9YPUZcPFAJKM3qbWZk7xpyYucAY41H9elCvjc
LUX3CNPYzxoUV6AXT2BrgNVnB37XoOzPGhT9Hxr0jwq25/Pk2u/FdKBgw8xbExSfcvBKVafw
js4uw+0RV9OvsW9lTgT7jf4cKmEEnkD86UpLmztCpm14v0z/QBC0A5gM1jr+YAJ3d/2Ddc1C
oGR7shNM7eXZ0l8trcBiiiM4HzTkJ1l3QbVfaX4VKuG2l/06rLvWdHf3ir5o/5M593bEVF2u
5N6ReIRMHR0P4nYNvDtQ7zrlfYBB5pP33O0jhI6Iq9pqdVtYo3t6urCYvSDSB4GP/ywpC+5q
W+rYT1EFGyYWtE3etWKN7qdchcVISPzGca/qDODwJY73f1TdgXxmca4PwRpFDrrCYmSbeZCw
ZjAgIuN+nO9fVydBN89tSML7LdiaF8Klm1JAlAU0GIc7QSt36HtgMbpdvG/DLrR8esrWjH0o
3bS7iHNsOyatVKaF6Be0ftodNyrY466UL21S8gJ48Yae3LtbMUVvHVvK/IBdOQNGp9dQs7fr
c8Hq+3URW9ag5fa4cwX0k2UJUK4GGNZ7bod8F6yOAY1kBliOYH71AmW85eWPzZxGxJzgnIuu
TbA67Trw07I/16tmgpclxPAuEdb519U5X6/cGN+B/AJKuI9Oaa84gM8tB+GuZp0KVi0I+5l/
42P/8kSx59wNaE24E2JNPewR/8aHAmyfUTVg0sOpIqsEw5HtzVVCwwIEK8i89GvI//v6uyNc
n7Kt0ZTLgyDAUm8rcPb574PF//67S9HfgCUy5tzref90uLCuJC/ZG78Bj9j4VEus/d9M//CH
UWFIEH/DASft/U/eYSVnATw4IS1vdPLmUK+KHdHB+1UHqkNVs4CW57o0RmsIgpEMNjlp78p3
IDroJPJCVL0Q6/6v3H2HWE+kU8TRp7bieTLLjmqGdImVlHjrjws3tk7QlBS6PLptc0mGIihs
DUvYplt6P0IC+Sz3cepz4Fetn5r4VIF/4vTwbWG3uk2ZrSpKo1t1wMEBYy4s/fwkI5chZ2Wv
bGP0bkxQSH26sZ80NPmJGOmR3rta/T0htgKPzDXJmyEcoIWkFZofPGgQ+PWlvQnTn5ol02bq
qnER4r036e39lk9vugxJ2UvpBtj0WZhJcYo91sQw2Be2GbCLu+/vyt2asEpsH2lcvEoK/YkQ
ApYYfKvwQazsoxVXq0J5sHe8LFS8Jt8jjGBMRS+FnwHi9Of95eYF2TpahflESeYUjeDT4bPP
nu/klqN1HkO/SjUraV41EJVPi1FUdl7gP/YP5f9Xhv/WBcPd3rwK09w1H/ISJ+IYmHX7tx3/
aHYxVkt3wGaaM7gceOj2UphwINPSllxvl7eIC6ToRbQHKL90uzA0GHqdbB/uJohqaCksskpW
Mbfoqoa0SoJnFnnSuwO5SnS7tZRtlAy6eStVwzjZZW2G6NqoBucyw5YsEpUZmQEJujh5y0++
SM9o6+YrrXjCIFS0b/ls2tnPb31Ay3u+mlylfopeXLlqo2R/secV1VFFULNR65V9GdzKLSMn
MXG3gP+uyTPpFuUdyyoeTSb0hIq5vlz37bIs1xT1RtsiB5TNJjOPao6MxfgatvmqqZ35+t2+
CN0A7zYE3uaVe1p9kXNfUtG0Bn2wsprJqEarjAfBI23NmVTb6Dm0xRYRdeW78s+P8u87/ieW
cP7+9LFS58ttYxo9rmxGZKHumXDm9yKBr0wd2SikzqlQ8pMRNXkdWgXbYrJ8+Ouyixf3j+I8
WIFunt2hxDRqmf9+OMkXrpBHPHzLHN5+AWY30VW4t2n3j2t1H6fWe0aVy0aCijWk7MXerVWL
DmnYknu4zy1qVQQzm1666T3VXXbvG0VlexRcFp/AdJh7NA4NrfUT/IQfQCCChuOA5cJI4EGN
h2uboq8DsoribO2I6j/S85yH7jqe+ib4Y9zltPNpBWkJhzc2U8LzJ5Gdi+EhfcvPa/7OEvyT
D/T/z955jn51vbqD2Pl2gzwNj3S0Ls5iPtO3PyHyo1WZzXaZu+1XJgJIGwXa2w3CPs37i8QQ
ZUrhbV3sS5P36cs2ds0ZDFzgO0GX/9XelcA1dXT7qBW/ulM2FYlUK8puZN+1BbGVRQwhymYN
EvaAAQKETetzAQRq/Sw7tFADJBJEiGEVFxZRFjEGyhY22cQAYQdB30wCdeln6/t+fX3v/R6E
m9w7c86Zc/7nzJm5N/dOwFMuh0sIzJ3F9F0jLOfy/vjxmlUqFtT2UCnUlcum+cntBk+uDC9n
nPl+lUlWtn3Ds7QLpOymBL8JnYDma7W8lnsRM0wq0+BZydrPLiH9jqMSS1roND/N4fsPXSl4
OYrfgbUm5lng+7ngn0/d/64lzarysXqdxKRZdmYvRrW781vCWpOIKcp219jUNgkZKmW7TJDF
s7BVJOBK8IiYVu4NRrJ13rp2TMoLblGhuwVYzmLnpQgJ5wLzIjtxp7mjKxW+a9WWHizYLLkm
PBBPK3nxresswVc0qCZAnFBv+TIn0rh4jcofhMVfUPX3DPJ8RaWw4b+S1NZLeK5dS01N0NIW
+hn/rO4HWRq4kJNC3H9pz07zQ4WemDqDdZSnk1wezm12W5hW0t3QfWeCHUGYOF0t2eZ1NLcT
y5wiSL1kTM5ISpwaVagrJRZJX0PYDBsGP/KUP2f7dROPLFOi4tX1HO1ZGhVbVTGuuRABVacR
CH8J/Zc/cNjP+iK2JD2qd1XmDha6m9QRxmLsNOuRLzjcobNS3x/dZlSTbZ9efb6/TUOhxkrV
NI3cim155tn+sDJcb3Z38ZqfPhb1jWuyjOMbGiZfI86OkFLXpf+PX6P6SMWtYmxKuZ73N6TH
tZ/+Seyz99eKEJNoaLzgtyf/7H263K+5Km7YJ3t9toYPRItpoDzJaqVr+thmmNp27dbZO1mI
43Um9p+3dG2QKZKLH8VNEpoSk4pihPXm158aqm6iBHu+IPP62j4B6yYt29dmNn3OeGPAQ87t
q1UR04GuKNKkbrnd3OZKhnkaa+gkNmSZ+IjXzQmF1mCd5eV+o0R6Pb6GuqME00rFyVL0g6rL
VuxCirgH6qp0Eh53ssMoVPWKc2d/8beckU8Q381UC8w1qStc/+vak9N9t4bch9Q8uemk6maa
cessZcMZ1LOIAKxstHee8bek22ZMknpFb8q5hBiN7Qq4X9s2qROVqicjSJ62EWpsA23ZAhUD
zc3SIJqWr56IauSN09E3xsOHWaZcN98OhxZmezeVEoEdYqOQeWQpvb6+SvrqAyvzxvXrh482
6x5rfJ7GSGw79PX91Gx7mvpNeareg1Lz22u0P9I1/ybZ39PJv4w6UZg6MhajpDRYvK0tSK4t
oPn8Bc0xLX9mTletkcR1C3J4/wg1jNvRejH51XUT8umxQu1mLys3inzH5AS4IBVGq8/ZlUee
L95zNOoq9Vs3sj2Scc3R4sq5lGhP+S0TIpyEWzSKXGrGDEtEZOgsWOtoRVVAHufXRJ2emLCW
or35FJR6RXCCXh8zKKKBUhMfOPeSuTvaZ1PLcuK4fxNzaoO6hsaun6ZyGLc4JA+sjK5la4k6
LzO9Kd7TNgUXt7J9xT2t/s622t2jV8q4mdF4Qg861ZaNyrg4jMHeoKYrhbvMTJhGr5r71oHy
6Ux9ykXSZOPeLb33HlVFkDSi2orEFasnx02qD/2Tk7pdz77BSS74jh34bvsfqxocLlp61Nrk
6Z1zkNn9iCMZXncBPKuq1oWzoXKruM8nizRvT8t+K7Gi3uAC1idKdHho98mmESei29FZK7A2
llbuOVe3+MwZlr0duJ39lZcCmG983N8+JQbSzcam5dWGu80X1ZNE51qY0cxL0WV7zpz4OAFv
qFDjraF0NDXYNnvOQPqBwpuKv3xvmbUdAXxVXbpWP9kpZPlpy4PKOr8YxNWuuiVlPtz/CRuB
MCJcmxMtqUi21NhZIr+Gpd1QR4+sS0eb+NGzD7EsT1pIFXurRNu9elr5Y0Za3/Iz+3FJWwvO
lTdtNWuYXpc/1lWbctslXcM44SqJEnmkXKXTJvqIDDf51XFFsL6aru/y7jsIpGc1dkveevtp
tYLpnHwlm3hVW+30DcjCIjN7j1DJaJze8egC1bLJUXQn5lmYkLr1JJNK8PC2aI3n2AVYR9Fi
AnX2zofuJM039xYOLqx4aerD6rg6pDJmxxh8eC+hWaY6e8w8k23pl6qnbGmmJ/Lc/Nxl9RAN
NkV+4heJScRuJ2r0muyRvgRuOc0C78yaoiupd5XR7vL8MfX92O7SH5zqr7fSmDEMn9n5Z9t3
0pjudqnzEVdtCggZ9PCBZBZ4OqgLF/y1kLHtTzxwa1ov+nSgU5jV3usYGjZ6k/ZEhLcUj6GD
Em2nuMxfwujR0dtQxNOBIFJXY5/zqkkx5Up7BoKkm+MmieMhUvXkS4OTbiMZRVTOSPCWKF5X
yv7UNlEyzw6bmSItLa2cdi169V7/Ew9lziRlOpgmzg/GhHpzKNRAjHi2kTpvLoRhpdBMN7i3
3O70Xx4pbwv8e9aAlH2NyMKupvfPWTTZ4u7n6P+zlWxKVne0rAxPvP5Nb6EcNZjMPX4xOgkX
/K1Vh/Kqa8oqsVuPd9hrfKrGNYtra9XOOSDxsy2te9QnNmXVlgn9YpuoBlfusxHF6rnE5aeA
ObSonNbaAd4vA4nZXCnrhAK/bGv2lO2x7OJjTONKXBe2ZRKDQZGpTpXCRnHz38tdktCrv/+d
luSO77b0bVK7ZP5lTZeQr/pIkHaIThfpi0YjMePQrf5+tNIX5aLm0WVrVq4qH1S/qYjFzVMJ
1gUm9XZileS3F/SwuJtYiwABQ/YqfKVHylEt+aanRolaVJc6MBVqVEErpemfsxPWZ1hYkk8P
Jkp0heTeJchz7eWcUWp4jySz2iDrkSKjlz7sZm5cyhHQa/pTkizP7lQMK7nV9xkJH1F6KypY
q1C9425uxonj6ZNWdLSYoQn5qnEIC6yoDS62eK33QSwzlLKYOVfWHb1XS3t9W136Lo+RVzXW
4lIP5YYJk7bYTrw9uBSecFm8y6EchYuL3r1dSF3djGB6XVdHQrm91E49y5ppwrbzZeulxuN0
wWmy8Ma1l7UOd/Torujpcxi51ROv2Ddg7SihZrAch7v+kqVxMyj05sUiYn7YTOwvyLy34+mP
9v8vrjUG7MlSYoY2t5/fZq5Sumyf3BcSSU+2VfetaFmfPjW+3BWs9kKwYZLbrOj1pj5YEVNL
tlRXRoqCCfnG2hCt14geG52rrzT7Ogasgx+qm/UV+KFbsF0yzqlPq02rzcAdLXhqMbKtFx/G
tJz7fkfIFepza/HMC1n9BVMjjHUG2zlWMqbhvRE/KltYgrWXMUhtV0pGWFj0F3eU0q7oZyTu
7eKcSX9xW8dtNqSu3b9hIMee5OHTPVBYXEaKyLNLfnq0CPsiq1G1rHruZF2o0PdJ/gGx5PNq
xa1raVqaU5kjXE6uLdbIBzx760/ROx3Qt0krsiNmWV5EM1NMMzrNOfmcYeMBsQBhb/BdRi0j
0jiQuavqWXqeH6/a+JJoXN1x3YTohKymSLA8eYC2zJ3HSmz7y9fsqHri801hFOJo0OZ4/AsW
R5Yig2tTQYmoYDCWwq7hYFF1dW49xrcRZarKkurFB13euGZgIOdhsrGi7cbIQ6QBzo/tkhwP
V+uawu5xEx2wPIHN+mCX1Pjn1IwJ+SJb/67YT/IRGyupyvIFxaEdHpKlzi5jV4rygzUYCofU
+0fovR1sE7IbMjZ6a2NzuBIaqRXHUC3zuy5qucG7RyehdifxSskQQS8JU3LI6GnxGnLD2atE
l8o6pnmoEM6huKXIPGCEYGhOGBMRQ6uYnCsZcct8jZAtPsp6EYRtF31hirv9lMNiKpDtw+Um
8IkZwziqzoyMGyXbPn6/9B7/trvBR6qfuSTaNx0jperK0itKw4jJnFIywYS0Cs1p7SQy77dq
52qYI2/ZxaYX1ySaWnEIhpMT1x1q/Ha1/iI2UcPEFhVFH6z91Ta7w3WLXXEGtcLsRR1T/KZM
a6XLeFLK1pa4CaVWrq3xD+GuXMuVONsCsDY0vY1OHaTjqVRqYA1a/1jcxEkk+IpDQ35Ln1qQ
053my5EhnKdP3JgpBROrdVimlzRpPZbs53YlKFUL5NHp50UmFof3bmGN7Mm7vtZD2bScERl2
AX8pKFA8M9yZQQjHxTtTdlTBe/HHzvw3Xwb7e2bZ/jGarQUdY1/dCfY+j7HLjaSVsTL6j/k5
dJ+akETpX1DRv6bGwpCoKVvLNeB3macdigrVb3c26UQfadbJPVj1ZCJyh0wvkoQ0Qq57JJGR
zEZbBqJ6Rs1/1N3Xm48u95i6azpFObXtwpYJ7i7bJ3R/Er2+O7VHZJREt3hGb7PoosbxTAJ/
WHOup5EWumz6CgXnooun05GEUKHdpURu4bDLMbE5Nu1pOcY6jFd3lrRddtTfd2a/wriZ/ogy
0cEijjldkzMhqSE7kpkt6YWzjeL01G3UNO2siVZo2bC6N6S/u6KygtL4IzvLteKA4fy6BDUM
MZsY94lE79nr9mej03u5SGxexEwTMyPBonDCNoCBqwxt6sY1IqUeFpmH03IMDSujwjvE0FmD
5IqeBhW/9Z3svQxF8yOl9lZ4PKapgDz/vNeVXjhIq8SgVVRUpCf1D2vZt9k2nApcgRtQv4nK
U/gm41GrNUM0CC8Exs28uoh6N66qTXolJ3O45S5Y+ezBWXePkg14bo2yi0eSdoPQ5bQTTXfu
ljOkMnJxbGHw8wm14TjprbGIbCTdNtPxlPKJzrFVN1ULb2oIVVXQttnk4pMnnvXP95YacZHH
cuwwGIM5nRiZkC+lRZ9+WsVqzPDlWMsni/GOJNZ8dUGrScy+shQXVxT6VantFL1w92hrjuWc
L6m7UoRTiMO7Um4U6EvxHM4nWtd7DCE3D2eJEDtsKXLjdjp7I3I9S18QLEQ6bah61m4XqXpH
T3uTX3W3tKBNirIIkYFm9eMvhdXsHtU9TEPW5EdbUQdjKXpNK93HGtkarl0eNeb/UZwzmEt9
3hxZyFOTaozkJLrLYwxZdpt8zaO4TVG8/qdzjsJ6/fHU2Pjlv/TinYof7Ar9xt5y73RJeZGt
e1u8HTr3lpCpBg/fY7A56Tq6maY+MNFV519iOXvVKCOZZ/kd94/G2Hfq/sqrKP/YeX2c3tyc
rn65Ojh5d6+D85Sfnk7pDs+KJDH7bIP6eZSd8FUNHSPq8BTV4fFLcIeBYdkkfTnp9DsK/bUH
f3LrBUL3fuxte//g6rq1Y9MuZVtlEzRKje/UMUzIDqaPLsamba+uo0n1yuheRauh9WVXrh3T
e7hhk5ZVm4Zq0lRq68PHw5x41ZLyMNfMu3Xpj0yMjs8WlRTfok33c/WK5QIxn3dJt3872Nwb
40rbQshNCnMt/SG1wog0QGsKx+ucdbLzbaPTYuSphWC5eCo1eUxF//oDtfEalSMNjLUeOw6w
Rr3HwDrGDpISW9hYAqfAcpISvpsi40p1KhcW5ux3b9PTxve+CEabdmejyKZU3+Jj6bv2tUik
yo9HPkged3ScTY5EWiv6z33KxRzfJmy6DA9wlnuZEhWjfb6vQU1fdbSeYp1toN1zjFzLSnVh
SBDMo4qm0XqZ4dTkCQw+0C8uLjWw+vDqzAYfDwfC8wJrZMeTXNWaQ0JcK+KNMQUMfj7ick9q
IVjhMj6tIXZoXSwC8answ9LPt3r1Rhwpf6pagxxqafK2NTPrffoCYxSeMcyrjwQPzsuUKjun
d293YGCerCnrmYqplRxl3y822zrSeChh04/p9bkqyiSa/OGq2IvU+dmuHfeogYaG4JmvMvBv
aLjiyZ2/NjzelybKe/QasUO3iosMuaGh39HZa49saHlJU7YuypcvcHuCzdHVYTfR2RbHyc8L
eGCuLFMYpDkyQNlOv+vV8Z4scL2jt1Od131BLmHqvK1BWW5MvpptkM6vmo2eaFdldmSSgwzN
wu64pBjGND4z/V5s+r34wGrjgNORJTsLHLs1lt3wj8jPL8hT9shvZbjkN5OQmIe7ZPIrEuMK
iFTZuJHdwyEX04unktngt0koX97b917rf3D4iXZfenoyqzddPGssd/QUqe+zUwpGtIBG2dhy
tmI9SLRXwU+TmBiHJ9SLWBpXVGNM0KLnFE/5fbcV02HWW5CXn3WToViaYooxynzA4FRgUHqU
Iom0EomMV7NhsRO78qbP1J9GIA4OYWaEu/1UCynq+LC0tsfqnqmGjkPBB2osu9Em5pUH9ESa
ryckHxfbJinSco8aNX/Xv7WYOHjf/ph/QOT9WkkXb9caFYncseFJmvyRKm4zbWrwYtTYcyNU
c7xDuYnhCtYdxDYJD+tSuIJiPbGNv4LidhdqXBS4dtUTtlJ/bJi14dSLLJsjXVNKkiGTWYyb
NNoui5ajVpTiJJlMHtteLZ/XVjnMCVrtcI/ZnmdYLzWwuosan0F1psdRqE55ZZUuYUIUJXv7
dbNEr5v0bk76M4I13ZmqFxa9SY2xzgbDphu1YdGPaugpopjLZNoVJBct3bzcYtT3gbKYVmYD
z/fSJd0Sxv0WrE7v0NYIEWQs+N4Yc13bdca3ild5blSUlLIaj9udoexw3la1yXbbr83m4N6J
1GNP8hTFy46WVzK74ybAOFrMaMSgwW8QgC8o8U4P1z/+A6++WxWdyCMyL9eUrpTtrIgr4PZb
0xNoRxtVWyMme4sD48Sz7Bn92NTY+NTwjAcFvKdTsVTZZLah6V7JEKMATE2P5FnspBCjgDfR
5mDFpg9aR87Z+FpEunJJWdYRVsVKbBAS+LgR6sW4+PRy4eZl2++82/j/hqNTs684jzXsL19l
Th0IO0MbCMgjI83EQ9Q2iytbjKm10GXi0/pMlkvyDv3iJ6fzGiE3dO0WSm0+IoaUSXeuV0kt
PkYNKnnxDE2UjR72YBsaZyJ4CkMXrPUesawSqpMdI/QlwiNeHklgkCaK5Yj9UeBmZ2b++so8
8k6vK+YPUoemu9UHG7LAD0c1s27kjE9T9Vzi55GB5rVc6VjdDT3bYuh2/RHFCp23ktKfo83P
eltVjdycWN3lkFdJUarB1JvM5tWrssbOvJAGSK6o0bz7yGl5/kyYmYZ4vlMaYc0/0R3W1QUE
917r9F7nKoYqh6LvgwXTb2G/bKMhO0bR1M1b9i85Ca60Kyqm4cNHaysZY5nhXBbRoalA/4Hu
8I6fK1IwDxLNHEcVW4a7Kb31lALuiwpHA6+tQ639YfdtbfIwRfkDBQx5CwMps6Rr3R1s1KBh
K3XKk7z/C81DrNB/2m88efRpHmezdas1Rbfc0mnIhpWBEUF+HYExPArXOi7Pj03BPvhUxZVN
E8/IwbWpc1sou1PDdzBUWXCR9dF9+nf+N0TIh3XwCqx0cK/9vN+P1DDXHH+g64nn9NAJV3/S
qHv17JWORhFhVHs5qjv6sPCai/PbAw5xGod6uddNH90kKmHUprfoX+vPfyU6E9hSRRl2nnmK
MTHObNbdx/NA/8w5Q+J6p45JZeCa46YfEm+VbBYzDJpJl2sPJS8reUyWdg8K5Fn1d78qyDg2
4Xzn8fVOtkE3ljRuXPyp5D2zuMRUryvba685XWjUwF/D4Zyr2zYjk7mo57OrzpoZgCc5Xp3j
6O375pC4Aq6JGRmJj7DyQIvaMI3AWTQaPCe9XddCGPmTGjT6k5DumM/nboytuBp4lDOnVXm/
0XMqfiJL/FlHL9Zyxq1ANcjx+e3gZvnvjaSq6jdcOHZMDJOnycsff4Q0EIo8dDAnyTZQzYZe
Zl68XudgfwBToT01KzC25tDeavPK+rBbHt0Y1BiVJvPMuET6++JtAy4Psav38ibc2zKTSiZ0
yamFykNBsVW5pscLslhG4WkN4f3ZTPqnHhFhEWci3Nas2tKgr68n2szAg8m+eP9FrijLxD8V
KL9x3eEPO2ypZgmBJQSWEFhCYAmBJQSWEFhCYAmBJQSWEFhCYAmBJQSWEFhCYAmBJQSWEFhC
4P8LAqGvmwSmni5d+DSAn6/f/3v1GpRCmtOlcAmnxWpIC/+WgW2xDH4COiDndOlrPh+f5Hdv
/1jg+a3iC7jH54O8BlAm3N4ue7PPr/jAmzkCtLsKjfBBOCJcEATw7g5L4LbOEkFE+IISacRh
sOeI8AYbAeEA3kGt0B6EGkIDoYXYi1BZ5BB+n04acRJQQ9kO4N0TSAGcr1OELBEBCC9Qqv0v
ZP+eRwdQGQLtPAAHAWjhAiTBT2nEboQJePcHG3bh8yBCli9VDbFnoQQF9lTe2/cAsqBUU8QJ
vtVQlheQ6gdaIIJ9b2C3F3i5Az2hjnvBC8oTkYb7qvx9K3CsDDZBS7BGnV9+EEHmyz78ljyH
BY19QbvgJyEXLICSUWDD8unRC9ZBlKQRluDIAeEM7PQEWnginBY0OQh4nUC5NALP98kpvoeg
VwL4UvYv6O0CSk781pICoIfWnAClAtS/BpJPArmwNe8/4STy6Tz4SDjwpXgDnsVSKNudr60P
0AXGiTTQ7wQoc0fAOugrR4QiaB9i680/hqV48IJaOi5QwXoCnw7qSeBzvkvjvGC7IgIHKAIA
hR/4hC06A3m+QLZAlhdft5OgBEadIFogXtB6F6CVC78UxjPUT+AbPOCFkgTxLc2X4Am8JfAx
jDwYx7CHOIGyt22HbcMId3+vHOIvQONtaqiVD1/3t0shnQOf+o3P3m3lJL/txfYX8RVo5w0k
nuDjCXmgXfAY+gLi6LNgJeSB2i/KeLt9Nz4mMN4gAtBSaBFExxv4DcaID9h7168CnR1B/RuM
YX+A0YoDrwA+PxbxFSiD5dBX3qCFt9v91/77fWzCEoFVMKrexghmA6gr7EswlgT+hXbC/v0h
Pkj9FdBT4G0Yq46gN0AdXYB+AoQg/0HEARCR3sAW2LojiAfIqQEs2ws+jUG9oK8b8SXAaIPW
EYAEB1DvDd6h7BMAjcW4E+STY0CWoNeZgj2IO/SNoM/COPowpxmQL8hcMOKhdwXaQt9A62Fu
8FnIWYJ8heLrKsh35gve8gC8MLY9gLQ/k6KA0ORTwlYNQRsQh7f7lSCqIIIQG5WFLHhjIadA
T8A6QY+XBnYK8sBirvg9DxpY5Qjo3ADyMIqkgQRfcEwEHoLUb7D7ii/tXXQX2/EAdd5AxiI6
0E4fwA2PYV8igQ32RegfiLcjaEUwvsBIh+0sIn2Erw30EewPsE9BfsgHqX4FGwqMARBLOB6h
QHRo8I9ugpEIYvYuP+yZEBPYz6Dv/l05MMe9PSJ/nC4fHtEFmQNmSOff7NL6zSp1MOZBCxdt
suT3FJhJBfEmQBBmjUW8LRFGiP2gjx18z2d/xgntgH0Ljqdw5IYvmFP8+VhaAvnQS++3B7lU
+JTQkw7gCPILSjz4OkFPoPla+/BtXNRTEBdeC9GBWvAxRNYFbNAeEpAo0GpRm8XxGmaLP5dG
ALI9QCQLZhZw3JMGsxYj0JdgRoWZEQ/s8wU9UeBRmMVgbECrTwBOr4V4hL3QC+jujVDiY/Gx
1kDpnkDSom+gLYuxLciBgswK21QEtIs+XURIMD4KMpsg5he5vwRSIU4Q7zd8cN+RjxrsWXhg
GcyysHWYGd9u/cB7dYJ+ZwxwgF7x4tsL+z1EQZB3YG72XrAFSoM9Es6boI8VAZawNThCwKwB
R0A454SZALbuwKc2AXuCmF20D+ZaiDhsCeoIZcJ5IfSbIDuYA7wEnoJ7ighzMCoc4NOZAU6B
PBxf58WxQxG08caK9zGALUAMiXzdIEowCmBehZ4QZGU4bxbErGA0FmgLIwZmrhN8HL8ElsL5
ObQSzkGc+RxYUA/3BT0aZngoeXGe86/8+DWwFdIQARIQVZh/3/XYm5z7NTgXUASU78YTLIUz
ZKgxxE4g7U12Oww0hbEi8AOk2g9sh6PiYqxDDhjrUAvIL5hJwmhR5EsW9GjBXPsGyCtQBoxe
GNuQFlL6AasFs4H3ayHiR0CbJnw6LX5WUflNW+hpwexwsV0iWKAJYo0FuhD5GkGEBGM3zPUB
QE9YIxjDrfhaL56XQE2+AjFiyp/bK4IjAaowymA8Lc403tb1MAIDqKGWMGua8bWEZxl7wFii
CXIvzIS/O9uC51LrvwL0hojj79QrIVwBkk6wXgSekXnyRzo3YAHqw5SL53Dvf658k4WAvLdr
wZIZi30Gzr3fq/07j9cuZrCTfI1OggyJ40fTB3RaAel/O8/9yzRdxpe0AfHJB861/6h4GawE
v9so8R7RNDi//5i/kY+k+xhZ/x4NfMb8s/8CK7i3H8QuAvE92Fby+fbt+w/+p+DaCbh+UQoW
DPgve4cvYuEN+v/P/jZ+kED4X9es/SOVPtkDgg92XND0CsH++0EokNq3gu9vxH8CIoyj9w==
    SensorDataFile = <blob elided: 365386 chars, md5=6bdf4b68>
    Type Image = RLX_057923.jpg
    URL = http://relux.com
    VarID = var1
    Voltage = 0 V
    Weight = 0.00 kg
    Width = 100 mm  [stored 0.328084 ft]

note: [stored X ft] marks values corroborated as IEEE doubles in the binary element streams (Revit-internal decimal feet)

## geometry (parser evidence)
native form markers: Blend x2, Sweep x18
no freeform markers — native parametric forms only
